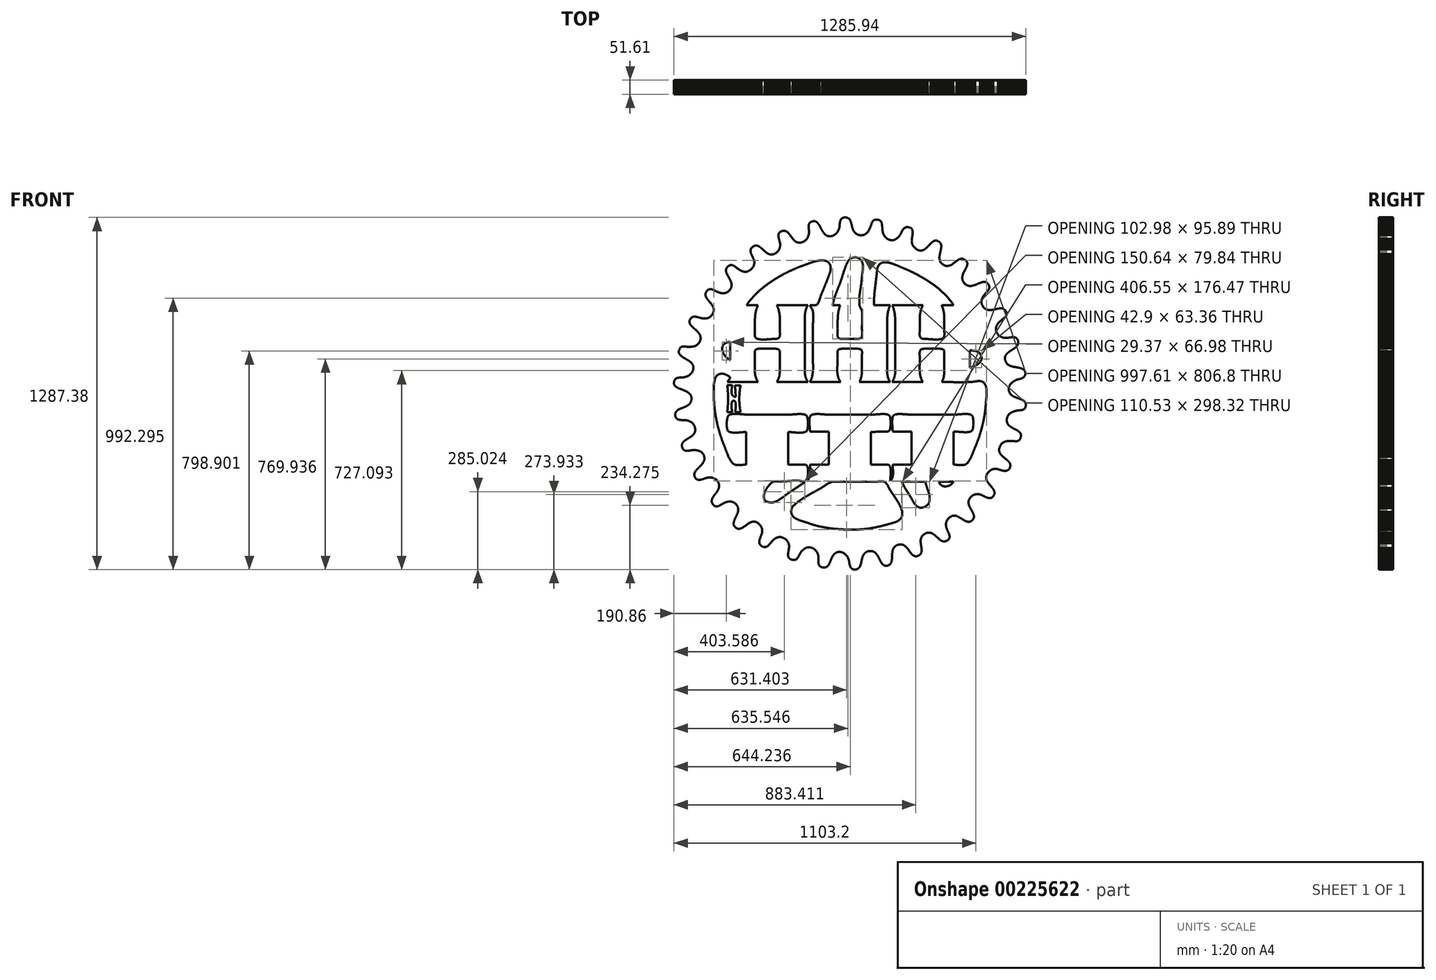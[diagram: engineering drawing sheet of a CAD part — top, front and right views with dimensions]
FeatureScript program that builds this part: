
annotation { "Feature Type Name" : "Feature", "Feature Type Description" : "" }
export const myFeature = defineFeature(function(context is Context, id is Id, definition is map)
    precondition{}
    {
        {
            var Q0;
            Q0=qCreatedBy(makeId("Front.planeOp"),FACE);
            var sketch = newSketch(context, id + "F0", { "sketchPlane" : qUnion([Q0])});
            skLineSegment(sketch, "E0", {"start": v(538.6, 219.48) * mm, "end": v(537.62, 221.14) * mm});
            skLineSegment(sketch, "E1", {"start": v(537.62, 221.14) * mm, "end": v(536.76, 222.78) * mm});
            skLineSegment(sketch, "E2", {"start": v(536.76, 222.78) * mm, "end": v(536, 224.4) * mm});
            skLineSegment(sketch, "E3", {"start": v(536, 224.4) * mm, "end": v(535.36, 226.02) * mm});
            skLineSegment(sketch, "E4", {"start": v(535.36, 226.02) * mm, "end": v(534.83, 227.62) * mm});
            skLineSegment(sketch, "E5", {"start": v(534.83, 227.62) * mm, "end": v(534.4, 229.21) * mm});
            skLineSegment(sketch, "E6", {"start": v(534.4, 229.21) * mm, "end": v(534.08, 230.79) * mm});
            skLineSegment(sketch, "E7", {"start": v(534.08, 230.79) * mm, "end": v(533.85, 232.35) * mm});
            skLineSegment(sketch, "E8", {"start": v(533.85, 232.35) * mm, "end": v(533.72, 233.9) * mm});
            skLineSegment(sketch, "E9", {"start": v(533.72, 233.9) * mm, "end": v(533.69, 235.43) * mm});
            skLineSegment(sketch, "E10", {"start": v(533.69, 235.43) * mm, "end": v(533.74, 236.95) * mm});
            skLineSegment(sketch, "E11", {"start": v(533.74, 236.95) * mm, "end": v(533.88, 238.46) * mm});
            skLineSegment(sketch, "E12", {"start": v(533.88, 238.46) * mm, "end": v(534.1, 239.95) * mm});
            skLineSegment(sketch, "E13", {"start": v(534.1, 239.95) * mm, "end": v(534.4, 241.42) * mm});
            skLineSegment(sketch, "E14", {"start": v(534.4, 241.42) * mm, "end": v(534.78, 242.88) * mm});
            skLineSegment(sketch, "E15", {"start": v(534.78, 242.88) * mm, "end": v(535.23, 244.32) * mm});
            skLineSegment(sketch, "E16", {"start": v(535.23, 244.32) * mm, "end": v(535.76, 245.75) * mm});
            skLineSegment(sketch, "E17", {"start": v(535.76, 245.75) * mm, "end": v(536.35, 247.16) * mm});
            skLineSegment(sketch, "E18", {"start": v(536.35, 247.16) * mm, "end": v(537, 248.55) * mm});
            skLineSegment(sketch, "E19", {"start": v(537, 248.55) * mm, "end": v(537.73, 249.93) * mm});
            skLineSegment(sketch, "E20", {"start": v(537.73, 249.93) * mm, "end": v(538.5, 251.29) * mm});
            skLineSegment(sketch, "E21", {"start": v(538.5, 251.29) * mm, "end": v(539.34, 252.63) * mm});
            skLineSegment(sketch, "E22", {"start": v(539.34, 252.63) * mm, "end": v(540.23, 253.95) * mm});
            skLineSegment(sketch, "E23", {"start": v(540.23, 253.95) * mm, "end": v(541.16, 255.25) * mm});
            skLineSegment(sketch, "E24", {"start": v(541.16, 255.25) * mm, "end": v(542.15, 256.53) * mm});
            skLineSegment(sketch, "E25", {"start": v(542.15, 256.53) * mm, "end": v(543.17, 257.8) * mm});
            skLineSegment(sketch, "E26", {"start": v(543.17, 257.8) * mm, "end": v(544.24, 259.05) * mm});
            skLineSegment(sketch, "E27", {"start": v(544.24, 259.05) * mm, "end": v(545.34, 260.27) * mm});
            skLineSegment(sketch, "E28", {"start": v(545.34, 260.27) * mm, "end": v(546.48, 261.48) * mm});
            skLineSegment(sketch, "E29", {"start": v(546.48, 261.48) * mm, "end": v(547.65, 262.67) * mm});
            skLineSegment(sketch, "E30", {"start": v(547.65, 262.67) * mm, "end": v(548.85, 263.83) * mm});
            skLineSegment(sketch, "E31", {"start": v(548.85, 263.83) * mm, "end": v(550.07, 264.98) * mm});
            skLineSegment(sketch, "E32", {"start": v(550.07, 264.98) * mm, "end": v(551.31, 266.1) * mm});
            skLineSegment(sketch, "E33", {"start": v(551.31, 266.1) * mm, "end": v(552.58, 267.2) * mm});
            skLineSegment(sketch, "E34", {"start": v(552.58, 267.2) * mm, "end": v(553.85, 268.28) * mm});
            skLineSegment(sketch, "E35", {"start": v(553.85, 268.28) * mm, "end": v(555.14, 269.34) * mm});
            skLineSegment(sketch, "E36", {"start": v(555.14, 269.34) * mm, "end": v(556.45, 270.38) * mm});
            skLineSegment(sketch, "E37", {"start": v(556.45, 270.38) * mm, "end": v(557.7, 271.34) * mm});
            skLineSegment(sketch, "E38", {"start": v(557.7, 271.34) * mm, "end": v(559, 272.32) * mm});
            skLineSegment(sketch, "E39", {"start": v(559, 272.32) * mm, "end": v(560.31, 273.3) * mm});
            skLineSegment(sketch, "E40", {"start": v(560.31, 273.3) * mm, "end": v(561.65, 274.3) * mm});
            skLineSegment(sketch, "E41", {"start": v(561.65, 274.3) * mm, "end": v(562.98, 275.33) * mm});
            skLineSegment(sketch, "E42", {"start": v(562.98, 275.33) * mm, "end": v(564.3, 276.38) * mm});
            skLineSegment(sketch, "E43", {"start": v(564.3, 276.38) * mm, "end": v(565.58, 277.45) * mm});
            skLineSegment(sketch, "E44", {"start": v(565.58, 277.45) * mm, "end": v(566.81, 278.56) * mm});
            skLineSegment(sketch, "E45", {"start": v(566.81, 278.56) * mm, "end": v(567.99, 279.7) * mm});
            skLineSegment(sketch, "E46", {"start": v(567.99, 279.7) * mm, "end": v(569.08, 280.88) * mm});
            skLineSegment(sketch, "E47", {"start": v(569.08, 280.88) * mm, "end": v(570.08, 282.1) * mm});
            skLineSegment(sketch, "E48", {"start": v(570.08, 282.1) * mm, "end": v(570.97, 283.36) * mm});
            skLineSegment(sketch, "E49", {"start": v(570.97, 283.36) * mm, "end": v(571.74, 284.67) * mm});
            skLineSegment(sketch, "E50", {"start": v(571.74, 284.67) * mm, "end": v(572.37, 286.04) * mm});
            skLineSegment(sketch, "E51", {"start": v(572.37, 286.04) * mm, "end": v(572.84, 287.46) * mm});
            skLineSegment(sketch, "E52", {"start": v(572.84, 287.46) * mm, "end": v(573.15, 288.93) * mm});
            skLineSegment(sketch, "E53", {"start": v(573.15, 288.93) * mm, "end": v(573.27, 290.48) * mm});
            skLineSegment(sketch, "E54", {"start": v(573.27, 290.48) * mm, "end": v(573.2, 292.08) * mm});
            skLineSegment(sketch, "E55", {"start": v(573.2, 292.08) * mm, "end": v(572.9, 293.76) * mm});
            skLineSegment(sketch, "E56", {"start": v(572.9, 293.76) * mm, "end": v(572.38, 295.51) * mm});
            skLineSegment(sketch, "E57", {"start": v(572.38, 295.51) * mm, "end": v(571.85, 296.89) * mm});
            skLineSegment(sketch, "E58", {"start": v(571.85, 296.89) * mm, "end": v(571.3, 298.18) * mm});
            skLineSegment(sketch, "E59", {"start": v(571.3, 298.18) * mm, "end": v(570.74, 299.4) * mm});
            skLineSegment(sketch, "E60", {"start": v(570.74, 299.4) * mm, "end": v(570.14, 300.56) * mm});
            skLineSegment(sketch, "E61", {"start": v(570.14, 300.56) * mm, "end": v(569.52, 301.64) * mm});
            skLineSegment(sketch, "E62", {"start": v(569.52, 301.64) * mm, "end": v(568.88, 302.65) * mm});
            skLineSegment(sketch, "E63", {"start": v(568.88, 302.65) * mm, "end": v(568.2, 303.6) * mm});
            skLineSegment(sketch, "E64", {"start": v(568.2, 303.6) * mm, "end": v(567.52, 304.48) * mm});
            skLineSegment(sketch, "E65", {"start": v(567.52, 304.48) * mm, "end": v(566.8, 305.3) * mm});
            skLineSegment(sketch, "E66", {"start": v(566.8, 305.3) * mm, "end": v(566.07, 306.06) * mm});
            skLineSegment(sketch, "E67", {"start": v(566.07, 306.06) * mm, "end": v(565.32, 306.76) * mm});
            skLineSegment(sketch, "E68", {"start": v(565.32, 306.76) * mm, "end": v(564.54, 307.4) * mm});
            skLineSegment(sketch, "E69", {"start": v(564.54, 307.4) * mm, "end": v(563.75, 307.98) * mm});
            skLineSegment(sketch, "E70", {"start": v(563.75, 307.98) * mm, "end": v(562.93, 308.51) * mm});
            skLineSegment(sketch, "E71", {"start": v(562.93, 308.51) * mm, "end": v(562.1, 308.99) * mm});
            skLineSegment(sketch, "E72", {"start": v(562.1, 308.99) * mm, "end": v(561.25, 309.42) * mm});
            skLineSegment(sketch, "E73", {"start": v(561.25, 309.42) * mm, "end": v(560.38, 309.8) * mm});
            skLineSegment(sketch, "E74", {"start": v(560.38, 309.8) * mm, "end": v(559.49, 310.12) * mm});
            skLineSegment(sketch, "E75", {"start": v(559.49, 310.12) * mm, "end": v(558.58, 310.4) * mm});
            skLineSegment(sketch, "E76", {"start": v(558.58, 310.4) * mm, "end": v(557.66, 310.65) * mm});
            skLineSegment(sketch, "E77", {"start": v(557.66, 310.65) * mm, "end": v(556.73, 310.85) * mm});
            skLineSegment(sketch, "E78", {"start": v(556.73, 310.85) * mm, "end": v(555.77, 311.01) * mm});
            skLineSegment(sketch, "E79", {"start": v(555.77, 311.01) * mm, "end": v(554.8, 311.13) * mm});
            skLineSegment(sketch, "E80", {"start": v(554.8, 311.13) * mm, "end": v(553.82, 311.22) * mm});
            skLineSegment(sketch, "E81", {"start": v(553.82, 311.22) * mm, "end": v(552.83, 311.27) * mm});
            skLineSegment(sketch, "E82", {"start": v(552.83, 311.27) * mm, "end": v(551.82, 311.28) * mm});
            skLineSegment(sketch, "E83", {"start": v(551.82, 311.28) * mm, "end": v(550.8, 311.27) * mm});
            skLineSegment(sketch, "E84", {"start": v(550.8, 311.27) * mm, "end": v(549.76, 311.22) * mm});
            skLineSegment(sketch, "E85", {"start": v(549.76, 311.22) * mm, "end": v(548.71, 311.15) * mm});
            skLineSegment(sketch, "E86", {"start": v(548.71, 311.15) * mm, "end": v(547.66, 311.05) * mm});
            skLineSegment(sketch, "E87", {"start": v(547.66, 311.05) * mm, "end": v(546.59, 310.93) * mm});
            skLineSegment(sketch, "E88", {"start": v(546.59, 310.93) * mm, "end": v(545.5, 310.79) * mm});
            skLineSegment(sketch, "E89", {"start": v(545.5, 310.79) * mm, "end": v(544.42, 310.62) * mm});
            skLineSegment(sketch, "E90", {"start": v(544.42, 310.62) * mm, "end": v(543.32, 310.44) * mm});
            skLineSegment(sketch, "E91", {"start": v(543.32, 310.44) * mm, "end": v(542.21, 310.23) * mm});
            skLineSegment(sketch, "E92", {"start": v(542.21, 310.23) * mm, "end": v(541.1, 310.02) * mm});
            skLineSegment(sketch, "E93", {"start": v(541.1, 310.02) * mm, "end": v(539.97, 309.79) * mm});
            skLineSegment(sketch, "E94", {"start": v(539.97, 309.79) * mm, "end": v(538.84, 309.54) * mm});
            skLineSegment(sketch, "E95", {"start": v(538.84, 309.54) * mm, "end": v(537.7, 309.3) * mm});
            skLineSegment(sketch, "E96", {"start": v(537.7, 309.3) * mm, "end": v(536.56, 309.03) * mm});
            skLineSegment(sketch, "E97", {"start": v(536.56, 309.03) * mm, "end": v(535.42, 308.76) * mm});
            skLineSegment(sketch, "E98", {"start": v(535.42, 308.76) * mm, "end": v(534.26, 308.5) * mm});
            skLineSegment(sketch, "E99", {"start": v(534.26, 308.5) * mm, "end": v(533.1, 308.21) * mm});
            skLineSegment(sketch, "E100", {"start": v(533.1, 308.21) * mm, "end": v(531.94, 307.94) * mm});
            skLineSegment(sketch, "E101", {"start": v(531.94, 307.94) * mm, "end": v(530.77, 307.66) * mm});
            skLineSegment(sketch, "E102", {"start": v(530.77, 307.66) * mm, "end": v(529.6, 307.39) * mm});
            skLineSegment(sketch, "E103", {"start": v(529.6, 307.39) * mm, "end": v(528.43, 307.12) * mm});
            skLineSegment(sketch, "E104", {"start": v(528.43, 307.12) * mm, "end": v(527.26, 306.85) * mm});
            skLineSegment(sketch, "E105", {"start": v(527.26, 306.85) * mm, "end": v(526.08, 306.6) * mm});
            skLineSegment(sketch, "E106", {"start": v(526.08, 306.6) * mm, "end": v(524.9, 306.35) * mm});
            skLineSegment(sketch, "E107", {"start": v(524.9, 306.35) * mm, "end": v(523.73, 306.11) * mm});
            skLineSegment(sketch, "E108", {"start": v(523.73, 306.11) * mm, "end": v(522.55, 305.89) * mm});
            skLineSegment(sketch, "E109", {"start": v(522.55, 305.89) * mm, "end": v(521.37, 305.68) * mm});
            skLineSegment(sketch, "E110", {"start": v(521.37, 305.68) * mm, "end": v(520.2, 305.49) * mm});
            skLineSegment(sketch, "E111", {"start": v(520.2, 305.49) * mm, "end": v(519.02, 305.31) * mm});
            skLineSegment(sketch, "E112", {"start": v(519.02, 305.31) * mm, "end": v(517.85, 305.16) * mm});
            skLineSegment(sketch, "E113", {"start": v(517.85, 305.16) * mm, "end": v(516.68, 305.02) * mm});
            skLineSegment(sketch, "E114", {"start": v(516.68, 305.02) * mm, "end": v(515.51, 304.92) * mm});
            skLineSegment(sketch, "E115", {"start": v(515.51, 304.92) * mm, "end": v(514.35, 304.83) * mm});
            skLineSegment(sketch, "E116", {"start": v(514.35, 304.83) * mm, "end": v(513.19, 304.77) * mm});
            skLineSegment(sketch, "E117", {"start": v(513.19, 304.77) * mm, "end": v(512.03, 304.74) * mm});
            skLineSegment(sketch, "E118", {"start": v(512.03, 304.74) * mm, "end": v(510.88, 304.75) * mm});
            skLineSegment(sketch, "E119", {"start": v(510.88, 304.75) * mm, "end": v(509.74, 304.78) * mm});
            skLineSegment(sketch, "E120", {"start": v(509.74, 304.78) * mm, "end": v(508.6, 304.85) * mm});
            skLineSegment(sketch, "E121", {"start": v(508.6, 304.85) * mm, "end": v(507.47, 304.95) * mm});
            skLineSegment(sketch, "E122", {"start": v(507.47, 304.95) * mm, "end": v(506.34, 305.1) * mm});
            skLineSegment(sketch, "E123", {"start": v(506.34, 305.1) * mm, "end": v(505.23, 305.27) * mm});
            skLineSegment(sketch, "E124", {"start": v(505.23, 305.27) * mm, "end": v(504.12, 305.5) * mm});
            skLineSegment(sketch, "E125", {"start": v(504.12, 305.5) * mm, "end": v(503.02, 305.76) * mm});
            skLineSegment(sketch, "E126", {"start": v(503.02, 305.76) * mm, "end": v(501.93, 306.07) * mm});
            skLineSegment(sketch, "E127", {"start": v(501.93, 306.07) * mm, "end": v(500.85, 306.43) * mm});
            skLineSegment(sketch, "E128", {"start": v(500.85, 306.43) * mm, "end": v(499.78, 306.83) * mm});
            skLineSegment(sketch, "E129", {"start": v(499.78, 306.83) * mm, "end": v(498.72, 307.28) * mm});
            skLineSegment(sketch, "E130", {"start": v(498.72, 307.28) * mm, "end": v(497.67, 307.79) * mm});
            skLineSegment(sketch, "E131", {"start": v(497.67, 307.79) * mm, "end": v(496.63, 308.35) * mm});
            skLineSegment(sketch, "E132", {"start": v(496.63, 308.35) * mm, "end": v(495.6, 308.96) * mm});
            skLineSegment(sketch, "E133", {"start": v(495.6, 308.96) * mm, "end": v(494.6, 309.63) * mm});
            skLineSegment(sketch, "E134", {"start": v(494.6, 309.63) * mm, "end": v(493.6, 310.36) * mm});
            skLineSegment(sketch, "E135", {"start": v(493.6, 310.36) * mm, "end": v(492.6, 311.15) * mm});
            skLineSegment(sketch, "E136", {"start": v(492.6, 311.15) * mm, "end": v(491.64, 312) * mm});
            skLineSegment(sketch, "E137", {"start": v(491.64, 312) * mm, "end": v(490.68, 312.92) * mm});
            skLineSegment(sketch, "E138", {"start": v(490.68, 312.92) * mm, "end": v(489.74, 313.9) * mm});
            skLineSegment(sketch, "E139", {"start": v(489.74, 313.9) * mm, "end": v(488.82, 314.95) * mm});
            skLineSegment(sketch, "E140", {"start": v(488.82, 314.95) * mm, "end": v(487.9, 316.07) * mm});
            skLineSegment(sketch, "E141", {"start": v(487.9, 316.07) * mm, "end": v(487.02, 317.26) * mm});
            skLineSegment(sketch, "E142", {"start": v(487.02, 317.26) * mm, "end": v(485.9, 318.9) * mm});
            skLineSegment(sketch, "E143", {"start": v(485.9, 318.9) * mm, "end": v(484.9, 320.52) * mm});
            skLineSegment(sketch, "E144", {"start": v(484.9, 320.52) * mm, "end": v(484.03, 322.13) * mm});
            skLineSegment(sketch, "E145", {"start": v(484.03, 322.13) * mm, "end": v(483.27, 323.73) * mm});
            skLineSegment(sketch, "E146", {"start": v(483.27, 323.73) * mm, "end": v(482.63, 325.33) * mm});
            skLineSegment(sketch, "E147", {"start": v(482.63, 325.33) * mm, "end": v(482.09, 326.91) * mm});
            skLineSegment(sketch, "E148", {"start": v(482.09, 326.91) * mm, "end": v(481.65, 328.5) * mm});
            skLineSegment(sketch, "E149", {"start": v(481.65, 328.5) * mm, "end": v(481.31, 330.06) * mm});
            skLineSegment(sketch, "E150", {"start": v(481.31, 330.06) * mm, "end": v(481.08, 331.62) * mm});
            skLineSegment(sketch, "E151", {"start": v(481.08, 331.62) * mm, "end": v(480.94, 333.17) * mm});
            skLineSegment(sketch, "E152", {"start": v(480.94, 333.17) * mm, "end": v(480.88, 334.7) * mm});
            skLineSegment(sketch, "E153", {"start": v(480.88, 334.7) * mm, "end": v(480.92, 336.24) * mm});
            skLineSegment(sketch, "E154", {"start": v(480.92, 336.24) * mm, "end": v(481.04, 337.76) * mm});
            skLineSegment(sketch, "E155", {"start": v(481.04, 337.76) * mm, "end": v(481.25, 339.27) * mm});
            skLineSegment(sketch, "E156", {"start": v(481.25, 339.27) * mm, "end": v(481.53, 340.78) * mm});
            skLineSegment(sketch, "E157", {"start": v(481.53, 340.78) * mm, "end": v(481.88, 342.27) * mm});
            skLineSegment(sketch, "E158", {"start": v(481.88, 342.27) * mm, "end": v(482.3, 343.75) * mm});
            skLineSegment(sketch, "E159", {"start": v(482.3, 343.75) * mm, "end": v(482.8, 345.23) * mm});
            skLineSegment(sketch, "E160", {"start": v(482.8, 345.23) * mm, "end": v(483.36, 346.69) * mm});
            skLineSegment(sketch, "E161", {"start": v(483.36, 346.69) * mm, "end": v(483.98, 348.14) * mm});
            skLineSegment(sketch, "E162", {"start": v(483.98, 348.14) * mm, "end": v(484.65, 349.59) * mm});
            skLineSegment(sketch, "E163", {"start": v(484.65, 349.59) * mm, "end": v(485.39, 351.02) * mm});
            skLineSegment(sketch, "E164", {"start": v(485.39, 351.02) * mm, "end": v(486.17, 352.44) * mm});
            skLineSegment(sketch, "E165", {"start": v(486.17, 352.44) * mm, "end": v(487, 353.86) * mm});
            skLineSegment(sketch, "E166", {"start": v(487, 353.86) * mm, "end": v(487.87, 355.26) * mm});
            skLineSegment(sketch, "E167", {"start": v(487.87, 355.26) * mm, "end": v(488.78, 356.65) * mm});
            skLineSegment(sketch, "E168", {"start": v(488.78, 356.65) * mm, "end": v(489.74, 358.03) * mm});
            skLineSegment(sketch, "E169", {"start": v(489.74, 358.03) * mm, "end": v(490.72, 359.4) * mm});
            skLineSegment(sketch, "E170", {"start": v(490.72, 359.4) * mm, "end": v(491.74, 360.77) * mm});
            skLineSegment(sketch, "E171", {"start": v(491.74, 360.77) * mm, "end": v(492.78, 362.12) * mm});
            skLineSegment(sketch, "E172", {"start": v(492.78, 362.12) * mm, "end": v(493.85, 363.46) * mm});
            skLineSegment(sketch, "E173", {"start": v(493.85, 363.46) * mm, "end": v(494.94, 364.78) * mm});
            skLineSegment(sketch, "E174", {"start": v(494.94, 364.78) * mm, "end": v(496.05, 366.1) * mm});
            skLineSegment(sketch, "E175", {"start": v(496.05, 366.1) * mm, "end": v(497.17, 367.4) * mm});
            skLineSegment(sketch, "E176", {"start": v(497.17, 367.4) * mm, "end": v(498.18, 368.56) * mm});
            skLineSegment(sketch, "E177", {"start": v(498.18, 368.56) * mm, "end": v(499.26, 369.76) * mm});
            skLineSegment(sketch, "E178", {"start": v(499.26, 369.76) * mm, "end": v(500.37, 371) * mm});
            skLineSegment(sketch, "E179", {"start": v(500.37, 371) * mm, "end": v(501.5, 372.27) * mm});
            skLineSegment(sketch, "E180", {"start": v(501.5, 372.27) * mm, "end": v(502.65, 373.58) * mm});
            skLineSegment(sketch, "E181", {"start": v(502.65, 373.58) * mm, "end": v(503.77, 374.92) * mm});
            skLineSegment(sketch, "E182", {"start": v(503.77, 374.92) * mm, "end": v(504.86, 376.3) * mm});
            skLineSegment(sketch, "E183", {"start": v(504.86, 376.3) * mm, "end": v(505.89, 377.72) * mm});
            skLineSegment(sketch, "E184", {"start": v(505.89, 377.72) * mm, "end": v(506.84, 379.16) * mm});
            skLineSegment(sketch, "E185", {"start": v(506.84, 379.16) * mm, "end": v(507.7, 380.63) * mm});
            skLineSegment(sketch, "E186", {"start": v(507.7, 380.63) * mm, "end": v(508.46, 382.13) * mm});
            skLineSegment(sketch, "E187", {"start": v(508.46, 382.13) * mm, "end": v(509.08, 383.66) * mm});
            skLineSegment(sketch, "E188", {"start": v(509.08, 383.66) * mm, "end": v(509.56, 385.2) * mm});
            skLineSegment(sketch, "E189", {"start": v(509.56, 385.2) * mm, "end": v(509.86, 386.78) * mm});
            skLineSegment(sketch, "E190", {"start": v(509.86, 386.78) * mm, "end": v(509.97, 388.38) * mm});
            skLineSegment(sketch, "E191", {"start": v(509.97, 388.38) * mm, "end": v(509.88, 389.99) * mm});
            skLineSegment(sketch, "E192", {"start": v(509.88, 389.99) * mm, "end": v(509.56, 391.62) * mm});
            skLineSegment(sketch, "E193", {"start": v(509.56, 391.62) * mm, "end": v(509, 393.27) * mm});
            skLineSegment(sketch, "E194", {"start": v(509, 393.27) * mm, "end": v(508.37, 394.72) * mm});
            skLineSegment(sketch, "E195", {"start": v(508.37, 394.72) * mm, "end": v(507.7, 396.08) * mm});
            skLineSegment(sketch, "E196", {"start": v(507.7, 396.08) * mm, "end": v(507.03, 397.35) * mm});
            skLineSegment(sketch, "E197", {"start": v(507.03, 397.35) * mm, "end": v(506.33, 398.54) * mm});
            skLineSegment(sketch, "E198", {"start": v(506.33, 398.54) * mm, "end": v(505.61, 399.64) * mm});
            skLineSegment(sketch, "E199", {"start": v(505.61, 399.64) * mm, "end": v(504.88, 400.67) * mm});
            skLineSegment(sketch, "E200", {"start": v(504.88, 400.67) * mm, "end": v(504.12, 401.61) * mm});
            skLineSegment(sketch, "E201", {"start": v(504.12, 401.61) * mm, "end": v(503.34, 402.48) * mm});
            skLineSegment(sketch, "E202", {"start": v(503.34, 402.48) * mm, "end": v(502.54, 403.28) * mm});
            skLineSegment(sketch, "E203", {"start": v(502.54, 403.28) * mm, "end": v(501.73, 404) * mm});
            skLineSegment(sketch, "E204", {"start": v(501.73, 404) * mm, "end": v(500.9, 404.65) * mm});
            skLineSegment(sketch, "E205", {"start": v(500.9, 404.65) * mm, "end": v(500.05, 405.23) * mm});
            skLineSegment(sketch, "E206", {"start": v(500.05, 405.23) * mm, "end": v(499.18, 405.75) * mm});
            skLineSegment(sketch, "E207", {"start": v(499.18, 405.75) * mm, "end": v(498.3, 406.2) * mm});
            skLineSegment(sketch, "E208", {"start": v(498.3, 406.2) * mm, "end": v(497.4, 406.6) * mm});
            skLineSegment(sketch, "E209", {"start": v(497.4, 406.6) * mm, "end": v(496.49, 406.93) * mm});
            skLineSegment(sketch, "E210", {"start": v(496.49, 406.93) * mm, "end": v(495.56, 407.2) * mm});
            skLineSegment(sketch, "E211", {"start": v(495.56, 407.2) * mm, "end": v(494.61, 407.42) * mm});
            skLineSegment(sketch, "E212", {"start": v(494.61, 407.42) * mm, "end": v(493.65, 407.58) * mm});
            skLineSegment(sketch, "E213", {"start": v(493.65, 407.58) * mm, "end": v(492.68, 407.7) * mm});
            skLineSegment(sketch, "E214", {"start": v(492.68, 407.7) * mm, "end": v(491.7, 407.76) * mm});
            skLineSegment(sketch, "E215", {"start": v(491.7, 407.76) * mm, "end": v(490.69, 407.77) * mm});
            skLineSegment(sketch, "E216", {"start": v(490.69, 407.77) * mm, "end": v(489.68, 407.74) * mm});
            skLineSegment(sketch, "E217", {"start": v(489.68, 407.74) * mm, "end": v(488.65, 407.67) * mm});
            skLineSegment(sketch, "E218", {"start": v(488.65, 407.67) * mm, "end": v(487.61, 407.55) * mm});
            skLineSegment(sketch, "E219", {"start": v(487.61, 407.55) * mm, "end": v(486.56, 407.4) * mm});
            skLineSegment(sketch, "E220", {"start": v(486.56, 407.4) * mm, "end": v(485.5, 407.2) * mm});
            skLineSegment(sketch, "E221", {"start": v(485.5, 407.2) * mm, "end": v(484.43, 406.98) * mm});
            skLineSegment(sketch, "E222", {"start": v(484.43, 406.98) * mm, "end": v(483.35, 406.72) * mm});
            skLineSegment(sketch, "E223", {"start": v(483.35, 406.72) * mm, "end": v(482.25, 406.43) * mm});
            skLineSegment(sketch, "E224", {"start": v(482.25, 406.43) * mm, "end": v(481.15, 406.1) * mm});
            skLineSegment(sketch, "E225", {"start": v(481.15, 406.1) * mm, "end": v(480.04, 405.76) * mm});
            skLineSegment(sketch, "E226", {"start": v(480.04, 405.76) * mm, "end": v(478.92, 405.4) * mm});
            skLineSegment(sketch, "E227", {"start": v(478.92, 405.4) * mm, "end": v(477.8, 405) * mm});
            skLineSegment(sketch, "E228", {"start": v(477.8, 405) * mm, "end": v(476.66, 404.59) * mm});
            skLineSegment(sketch, "E229", {"start": v(476.66, 404.59) * mm, "end": v(475.51, 404.15) * mm});
            skLineSegment(sketch, "E230", {"start": v(475.51, 404.15) * mm, "end": v(474.36, 403.7) * mm});
            skLineSegment(sketch, "E231", {"start": v(474.36, 403.7) * mm, "end": v(473.2, 403.24) * mm});
            skLineSegment(sketch, "E232", {"start": v(473.2, 403.24) * mm, "end": v(472.04, 402.77) * mm});
            skLineSegment(sketch, "E233", {"start": v(472.04, 402.77) * mm, "end": v(470.87, 402.28) * mm});
            skLineSegment(sketch, "E234", {"start": v(470.87, 402.28) * mm, "end": v(469.7, 401.79) * mm});
            skLineSegment(sketch, "E235", {"start": v(469.7, 401.79) * mm, "end": v(468.52, 401.29) * mm});
            skLineSegment(sketch, "E236", {"start": v(468.52, 401.29) * mm, "end": v(467.33, 400.79) * mm});
            skLineSegment(sketch, "E237", {"start": v(467.33, 400.79) * mm, "end": v(466.14, 400.28) * mm});
            skLineSegment(sketch, "E238", {"start": v(466.14, 400.28) * mm, "end": v(464.95, 399.78) * mm});
            skLineSegment(sketch, "E239", {"start": v(464.95, 399.78) * mm, "end": v(463.75, 399.27) * mm});
            skLineSegment(sketch, "E240", {"start": v(463.75, 399.27) * mm, "end": v(462.55, 398.78) * mm});
            skLineSegment(sketch, "E241", {"start": v(462.55, 398.78) * mm, "end": v(461.35, 398.28) * mm});
            skLineSegment(sketch, "E242", {"start": v(461.35, 398.28) * mm, "end": v(460.15, 397.8) * mm});
            skLineSegment(sketch, "E243", {"start": v(460.15, 397.8) * mm, "end": v(458.94, 397.33) * mm});
            skLineSegment(sketch, "E244", {"start": v(458.94, 397.33) * mm, "end": v(457.73, 396.87) * mm});
            skLineSegment(sketch, "E245", {"start": v(457.73, 396.87) * mm, "end": v(456.52, 396.42) * mm});
            skLineSegment(sketch, "E246", {"start": v(456.52, 396.42) * mm, "end": v(455.32, 396) * mm});
            skLineSegment(sketch, "E247", {"start": v(455.32, 396) * mm, "end": v(454.1, 395.59) * mm});
            skLineSegment(sketch, "E248", {"start": v(454.1, 395.59) * mm, "end": v(452.9, 395.2) * mm});
            skLineSegment(sketch, "E249", {"start": v(452.9, 395.2) * mm, "end": v(451.69, 394.83) * mm});
            skLineSegment(sketch, "E250", {"start": v(451.69, 394.83) * mm, "end": v(450.48, 394.5) * mm});
            skLineSegment(sketch, "E251", {"start": v(450.48, 394.5) * mm, "end": v(449.28, 394.18) * mm});
            skLineSegment(sketch, "E252", {"start": v(449.28, 394.18) * mm, "end": v(448.07, 393.9) * mm});
            skLineSegment(sketch, "E253", {"start": v(448.07, 393.9) * mm, "end": v(446.87, 393.64) * mm});
            skLineSegment(sketch, "E254", {"start": v(446.87, 393.64) * mm, "end": v(445.67, 393.43) * mm});
            skLineSegment(sketch, "E255", {"start": v(445.67, 393.43) * mm, "end": v(444.48, 393.24) * mm});
            skLineSegment(sketch, "E256", {"start": v(444.48, 393.24) * mm, "end": v(443.28, 393.1) * mm});
            skLineSegment(sketch, "E257", {"start": v(443.28, 393.1) * mm, "end": v(442.1, 393) * mm});
            skLineSegment(sketch, "E258", {"start": v(442.1, 393) * mm, "end": v(440.91, 392.93) * mm});
            skLineSegment(sketch, "E259", {"start": v(440.91, 392.93) * mm, "end": v(439.73, 392.9) * mm});
            skLineSegment(sketch, "E260", {"start": v(439.73, 392.9) * mm, "end": v(438.56, 392.93) * mm});
            skLineSegment(sketch, "E261", {"start": v(438.56, 392.93) * mm, "end": v(437.4, 393) * mm});
            skLineSegment(sketch, "E262", {"start": v(437.4, 393) * mm, "end": v(436.23, 393.13) * mm});
            skLineSegment(sketch, "E263", {"start": v(436.23, 393.13) * mm, "end": v(435.07, 393.3) * mm});
            skLineSegment(sketch, "E264", {"start": v(435.07, 393.3) * mm, "end": v(433.92, 393.53) * mm});
            skLineSegment(sketch, "E265", {"start": v(433.92, 393.53) * mm, "end": v(432.78, 393.82) * mm});
            skLineSegment(sketch, "E266", {"start": v(432.78, 393.82) * mm, "end": v(431.65, 394.16) * mm});
            skLineSegment(sketch, "E267", {"start": v(431.65, 394.16) * mm, "end": v(430.52, 394.57) * mm});
            skLineSegment(sketch, "E268", {"start": v(430.52, 394.57) * mm, "end": v(429.4, 395.04) * mm});
            skLineSegment(sketch, "E269", {"start": v(429.4, 395.04) * mm, "end": v(428.3, 395.57) * mm});
            skLineSegment(sketch, "E270", {"start": v(428.3, 395.57) * mm, "end": v(427.2, 396.17) * mm});
            skLineSegment(sketch, "E271", {"start": v(427.2, 396.17) * mm, "end": v(426.1, 396.84) * mm});
            skLineSegment(sketch, "E272", {"start": v(426.1, 396.84) * mm, "end": v(424.45, 397.96) * mm});
            skLineSegment(sketch, "E273", {"start": v(424.45, 397.96) * mm, "end": v(422.9, 399.12) * mm});
            skLineSegment(sketch, "E274", {"start": v(422.9, 399.12) * mm, "end": v(421.45, 400.3) * mm});
            skLineSegment(sketch, "E275", {"start": v(421.45, 400.3) * mm, "end": v(420.1, 401.5) * mm});
            skLineSegment(sketch, "E276", {"start": v(420.1, 401.5) * mm, "end": v(418.86, 402.75) * mm});
            skLineSegment(sketch, "E277", {"start": v(418.86, 402.75) * mm, "end": v(417.72, 404) * mm});
            skLineSegment(sketch, "E278", {"start": v(417.72, 404) * mm, "end": v(416.67, 405.3) * mm});
            skLineSegment(sketch, "E279", {"start": v(416.67, 405.3) * mm, "end": v(415.72, 406.6) * mm});
            skLineSegment(sketch, "E280", {"start": v(415.72, 406.6) * mm, "end": v(414.85, 407.93) * mm});
            skLineSegment(sketch, "E281", {"start": v(414.85, 407.93) * mm, "end": v(414.08, 409.29) * mm});
            skLineSegment(sketch, "E282", {"start": v(414.08, 409.29) * mm, "end": v(413.4, 410.66) * mm});
            skLineSegment(sketch, "E283", {"start": v(413.4, 410.66) * mm, "end": v(412.8, 412.05) * mm});
            skLineSegment(sketch, "E284", {"start": v(412.8, 412.05) * mm, "end": v(412.29, 413.46) * mm});
            skLineSegment(sketch, "E285", {"start": v(412.29, 413.46) * mm, "end": v(411.85, 414.88) * mm});
            skLineSegment(sketch, "E286", {"start": v(411.85, 414.88) * mm, "end": v(411.5, 416.32) * mm});
            skLineSegment(sketch, "E287", {"start": v(411.5, 416.32) * mm, "end": v(411.22, 417.77) * mm});
            skLineSegment(sketch, "E288", {"start": v(411.22, 417.77) * mm, "end": v(411.02, 419.24) * mm});
            skLineSegment(sketch, "E289", {"start": v(411.02, 419.24) * mm, "end": v(410.9, 420.72) * mm});
            skLineSegment(sketch, "E290", {"start": v(410.9, 420.72) * mm, "end": v(410.84, 422.21) * mm});
            skLineSegment(sketch, "E291", {"start": v(410.84, 422.21) * mm, "end": v(410.85, 423.71) * mm});
            skLineSegment(sketch, "E292", {"start": v(410.85, 423.71) * mm, "end": v(410.92, 425.22) * mm});
            skLineSegment(sketch, "E293", {"start": v(410.92, 425.22) * mm, "end": v(411.06, 426.74) * mm});
            skLineSegment(sketch, "E294", {"start": v(411.06, 426.74) * mm, "end": v(411.27, 428.26) * mm});
            skLineSegment(sketch, "E295", {"start": v(411.27, 428.26) * mm, "end": v(411.53, 429.8) * mm});
            skLineSegment(sketch, "E296", {"start": v(411.53, 429.8) * mm, "end": v(411.85, 431.33) * mm});
            skLineSegment(sketch, "E297", {"start": v(411.85, 431.33) * mm, "end": v(412.23, 432.87) * mm});
            skLineSegment(sketch, "E298", {"start": v(412.23, 432.87) * mm, "end": v(412.66, 434.4) * mm});
            skLineSegment(sketch, "E299", {"start": v(412.66, 434.4) * mm, "end": v(413.14, 435.95) * mm});
            skLineSegment(sketch, "E300", {"start": v(413.14, 435.95) * mm, "end": v(413.67, 437.5) * mm});
            skLineSegment(sketch, "E301", {"start": v(413.67, 437.5) * mm, "end": v(414.25, 439.03) * mm});
            skLineSegment(sketch, "E302", {"start": v(414.25, 439.03) * mm, "end": v(414.87, 440.57) * mm});
            skLineSegment(sketch, "E303", {"start": v(414.87, 440.57) * mm, "end": v(415.54, 442.1) * mm});
            skLineSegment(sketch, "E304", {"start": v(415.54, 442.1) * mm, "end": v(416.24, 443.64) * mm});
            skLineSegment(sketch, "E305", {"start": v(416.24, 443.64) * mm, "end": v(416.99, 445.17) * mm});
            skLineSegment(sketch, "E306", {"start": v(416.99, 445.17) * mm, "end": v(417.77, 446.69) * mm});
            skLineSegment(sketch, "E307", {"start": v(417.77, 446.69) * mm, "end": v(418.58, 448.2) * mm});
            skLineSegment(sketch, "E308", {"start": v(418.58, 448.2) * mm, "end": v(419.43, 449.7) * mm});
            skLineSegment(sketch, "E309", {"start": v(419.43, 449.7) * mm, "end": v(420.3, 451.2) * mm});
            skLineSegment(sketch, "E310", {"start": v(420.3, 451.2) * mm, "end": v(421.16, 452.63) * mm});
            skLineSegment(sketch, "E311", {"start": v(421.16, 452.63) * mm, "end": v(422, 454.06) * mm});
            skLineSegment(sketch, "E312", {"start": v(422, 454.06) * mm, "end": v(422.8, 455.49) * mm});
            skLineSegment(sketch, "E313", {"start": v(422.8, 455.49) * mm, "end": v(423.6, 456.92) * mm});
            skLineSegment(sketch, "E314", {"start": v(423.6, 456.92) * mm, "end": v(424.35, 458.34) * mm});
            skLineSegment(sketch, "E315", {"start": v(424.35, 458.34) * mm, "end": v(425.08, 459.77) * mm});
            skLineSegment(sketch, "E316", {"start": v(425.08, 459.77) * mm, "end": v(425.76, 461.18) * mm});
            skLineSegment(sketch, "E317", {"start": v(425.76, 461.18) * mm, "end": v(426.4, 462.6) * mm});
            skLineSegment(sketch, "E318", {"start": v(426.4, 462.6) * mm, "end": v(427, 464) * mm});
            skLineSegment(sketch, "E319", {"start": v(427, 464) * mm, "end": v(427.53, 465.4) * mm});
            skLineSegment(sketch, "E320", {"start": v(427.53, 465.4) * mm, "end": v(428, 466.77) * mm});
            skLineSegment(sketch, "E321", {"start": v(428, 466.77) * mm, "end": v(428.41, 468.15) * mm});
            skLineSegment(sketch, "E322", {"start": v(428.41, 468.15) * mm, "end": v(428.75, 469.5) * mm});
            skLineSegment(sketch, "E323", {"start": v(428.75, 469.5) * mm, "end": v(429.02, 470.85) * mm});
            skLineSegment(sketch, "E324", {"start": v(429.02, 470.85) * mm, "end": v(429.2, 472.18) * mm});
            skLineSegment(sketch, "E325", {"start": v(429.2, 472.18) * mm, "end": v(429.3, 473.49) * mm});
            skLineSegment(sketch, "E326", {"start": v(429.3, 473.49) * mm, "end": v(429.31, 474.78) * mm});
            skLineSegment(sketch, "E327", {"start": v(429.31, 474.78) * mm, "end": v(429.23, 476.06) * mm});
            skLineSegment(sketch, "E328", {"start": v(429.23, 476.06) * mm, "end": v(429.04, 477.31) * mm});
            skLineSegment(sketch, "E329", {"start": v(429.04, 477.31) * mm, "end": v(428.75, 478.54) * mm});
            skLineSegment(sketch, "E330", {"start": v(428.75, 478.54) * mm, "end": v(428.35, 479.75) * mm});
            skLineSegment(sketch, "E331", {"start": v(428.35, 479.75) * mm, "end": v(427.84, 480.93) * mm});
            skLineSegment(sketch, "E332", {"start": v(427.84, 480.93) * mm, "end": v(427.2, 482.1) * mm});
            skLineSegment(sketch, "E333", {"start": v(427.2, 482.1) * mm, "end": v(426.44, 483.22) * mm});
            skLineSegment(sketch, "E334", {"start": v(426.44, 483.22) * mm, "end": v(425.55, 484.32) * mm});
            skLineSegment(sketch, "E335", {"start": v(425.55, 484.32) * mm, "end": v(424.52, 485.4) * mm});
            skLineSegment(sketch, "E336", {"start": v(424.52, 485.4) * mm, "end": v(423.35, 486.44) * mm});
            skLineSegment(sketch, "E337", {"start": v(423.35, 486.44) * mm, "end": v(422.04, 487.45) * mm});
            skLineSegment(sketch, "E338", {"start": v(422.04, 487.45) * mm, "end": v(420.58, 488.42) * mm});
            skLineSegment(sketch, "E339", {"start": v(420.58, 488.42) * mm, "end": v(418.96, 489.36) * mm});
            skLineSegment(sketch, "E340", {"start": v(418.96, 489.36) * mm, "end": v(417.18, 490.27) * mm});
            skLineSegment(sketch, "E341", {"start": v(417.18, 490.27) * mm, "end": v(415.24, 491.13) * mm});
            skLineSegment(sketch, "E342", {"start": v(415.24, 491.13) * mm, "end": v(413.97, 491.61) * mm});
            skLineSegment(sketch, "E343", {"start": v(413.97, 491.61) * mm, "end": v(412.7, 491.99) * mm});
            skLineSegment(sketch, "E344", {"start": v(412.7, 491.99) * mm, "end": v(411.46, 492.26) * mm});
            skLineSegment(sketch, "E345", {"start": v(411.46, 492.26) * mm, "end": v(410.22, 492.43) * mm});
            skLineSegment(sketch, "E346", {"start": v(410.22, 492.43) * mm, "end": v(409, 492.52) * mm});
            skLineSegment(sketch, "E347", {"start": v(409, 492.52) * mm, "end": v(407.77, 492.5) * mm});
            skLineSegment(sketch, "E348", {"start": v(407.77, 492.5) * mm, "end": v(406.56, 492.42) * mm});
            skLineSegment(sketch, "E349", {"start": v(406.56, 492.42) * mm, "end": v(405.35, 492.24) * mm});
            skLineSegment(sketch, "E350", {"start": v(405.35, 492.24) * mm, "end": v(404.15, 492) * mm});
            skLineSegment(sketch, "E351", {"start": v(404.15, 492) * mm, "end": v(402.96, 491.67) * mm});
            skLineSegment(sketch, "E352", {"start": v(402.96, 491.67) * mm, "end": v(401.78, 491.28) * mm});
            skLineSegment(sketch, "E353", {"start": v(401.78, 491.28) * mm, "end": v(400.6, 490.83) * mm});
            skLineSegment(sketch, "E354", {"start": v(400.6, 490.83) * mm, "end": v(399.42, 490.31) * mm});
            skLineSegment(sketch, "E355", {"start": v(399.42, 490.31) * mm, "end": v(398.24, 489.74) * mm});
            skLineSegment(sketch, "E356", {"start": v(398.24, 489.74) * mm, "end": v(397.07, 489.11) * mm});
            skLineSegment(sketch, "E357", {"start": v(397.07, 489.11) * mm, "end": v(395.9, 488.44) * mm});
            skLineSegment(sketch, "E358", {"start": v(395.9, 488.44) * mm, "end": v(394.74, 487.72) * mm});
            skLineSegment(sketch, "E359", {"start": v(394.74, 487.72) * mm, "end": v(393.57, 486.97) * mm});
            skLineSegment(sketch, "E360", {"start": v(393.57, 486.97) * mm, "end": v(392.41, 486.17) * mm});
            skLineSegment(sketch, "E361", {"start": v(392.41, 486.17) * mm, "end": v(391.25, 485.35) * mm});
            skLineSegment(sketch, "E362", {"start": v(391.25, 485.35) * mm, "end": v(390.08, 484.5) * mm});
            skLineSegment(sketch, "E363", {"start": v(390.08, 484.5) * mm, "end": v(388.91, 483.62) * mm});
            skLineSegment(sketch, "E364", {"start": v(388.91, 483.62) * mm, "end": v(387.74, 482.73) * mm});
            skLineSegment(sketch, "E365", {"start": v(387.74, 482.73) * mm, "end": v(386.57, 481.82) * mm});
            skLineSegment(sketch, "E366", {"start": v(386.57, 481.82) * mm, "end": v(385.4, 480.9) * mm});
            skLineSegment(sketch, "E367", {"start": v(385.4, 480.9) * mm, "end": v(384.22, 479.96) * mm});
            skLineSegment(sketch, "E368", {"start": v(384.22, 479.96) * mm, "end": v(383.03, 479.03) * mm});
            skLineSegment(sketch, "E369", {"start": v(383.03, 479.03) * mm, "end": v(381.85, 478.1) * mm});
            skLineSegment(sketch, "E370", {"start": v(381.85, 478.1) * mm, "end": v(380.65, 477.17) * mm});
            skLineSegment(sketch, "E371", {"start": v(380.65, 477.17) * mm, "end": v(379.45, 476.26) * mm});
            skLineSegment(sketch, "E372", {"start": v(379.45, 476.26) * mm, "end": v(378.24, 475.35) * mm});
            skLineSegment(sketch, "E373", {"start": v(378.24, 475.35) * mm, "end": v(377.02, 474.46) * mm});
            skLineSegment(sketch, "E374", {"start": v(377.02, 474.46) * mm, "end": v(375.8, 473.6) * mm});
            skLineSegment(sketch, "E375", {"start": v(375.8, 473.6) * mm, "end": v(374.57, 472.76) * mm});
            skLineSegment(sketch, "E376", {"start": v(374.57, 472.76) * mm, "end": v(373.32, 471.95) * mm});
            skLineSegment(sketch, "E377", {"start": v(373.32, 471.95) * mm, "end": v(372.07, 471.17) * mm});
            skLineSegment(sketch, "E378", {"start": v(372.07, 471.17) * mm, "end": v(370.8, 470.43) * mm});
            skLineSegment(sketch, "E379", {"start": v(370.8, 470.43) * mm, "end": v(369.53, 469.73) * mm});
            skLineSegment(sketch, "E380", {"start": v(369.53, 469.73) * mm, "end": v(368.24, 469.08) * mm});
            skLineSegment(sketch, "E381", {"start": v(368.24, 469.08) * mm, "end": v(366.94, 468.48) * mm});
            skLineSegment(sketch, "E382", {"start": v(366.94, 468.48) * mm, "end": v(365.62, 467.93) * mm});
            skLineSegment(sketch, "E383", {"start": v(365.62, 467.93) * mm, "end": v(364.29, 467.44) * mm});
            skLineSegment(sketch, "E384", {"start": v(364.29, 467.44) * mm, "end": v(362.94, 467.01) * mm});
            skLineSegment(sketch, "E385", {"start": v(362.94, 467.01) * mm, "end": v(361.58, 466.65) * mm});
            skLineSegment(sketch, "E386", {"start": v(361.58, 466.65) * mm, "end": v(360.2, 466.36) * mm});
            skLineSegment(sketch, "E387", {"start": v(360.2, 466.36) * mm, "end": v(358.82, 466.15) * mm});
            skLineSegment(sketch, "E388", {"start": v(358.82, 466.15) * mm, "end": v(357.4, 466.01) * mm});
            skLineSegment(sketch, "E389", {"start": v(357.4, 466.01) * mm, "end": v(355.98, 465.96) * mm});
            skLineSegment(sketch, "E390", {"start": v(355.98, 465.96) * mm, "end": v(354.53, 465.99) * mm});
            skLineSegment(sketch, "E391", {"start": v(354.53, 465.99) * mm, "end": v(353.06, 466.11) * mm});
            skLineSegment(sketch, "E392", {"start": v(353.06, 466.11) * mm, "end": v(351.58, 466.33) * mm});
            skLineSegment(sketch, "E393", {"start": v(351.58, 466.33) * mm, "end": v(350.07, 466.65) * mm});
            skLineSegment(sketch, "E394", {"start": v(350.07, 466.65) * mm, "end": v(348.3, 467.14) * mm});
            skLineSegment(sketch, "E395", {"start": v(348.3, 467.14) * mm, "end": v(346.6, 467.73) * mm});
            skLineSegment(sketch, "E396", {"start": v(346.6, 467.73) * mm, "end": v(344.95, 468.43) * mm});
            skLineSegment(sketch, "E397", {"start": v(344.95, 468.43) * mm, "end": v(343.35, 469.23) * mm});
            skLineSegment(sketch, "E398", {"start": v(343.35, 469.23) * mm, "end": v(341.8, 470.12) * mm});
            skLineSegment(sketch, "E399", {"start": v(341.8, 470.12) * mm, "end": v(340.3, 471.1) * mm});
            skLineSegment(sketch, "E400", {"start": v(340.3, 471.1) * mm, "end": v(338.84, 472.18) * mm});
            skLineSegment(sketch, "E401", {"start": v(338.84, 472.18) * mm, "end": v(337.42, 473.33) * mm});
            skLineSegment(sketch, "E402", {"start": v(337.42, 473.33) * mm, "end": v(336.31, 474.32) * mm});
            skLineSegment(sketch, "E403", {"start": v(336.31, 474.32) * mm, "end": v(335.27, 475.34) * mm});
            skLineSegment(sketch, "E404", {"start": v(335.27, 475.34) * mm, "end": v(334.31, 476.37) * mm});
            skLineSegment(sketch, "E405", {"start": v(334.31, 476.37) * mm, "end": v(333.42, 477.41) * mm});
            skLineSegment(sketch, "E406", {"start": v(333.42, 477.41) * mm, "end": v(332.6, 478.48) * mm});
            skLineSegment(sketch, "E407", {"start": v(332.6, 478.48) * mm, "end": v(331.84, 479.56) * mm});
            skLineSegment(sketch, "E408", {"start": v(331.84, 479.56) * mm, "end": v(331.15, 480.65) * mm});
            skLineSegment(sketch, "E409", {"start": v(331.15, 480.65) * mm, "end": v(330.53, 481.76) * mm});
            skLineSegment(sketch, "E410", {"start": v(330.53, 481.76) * mm, "end": v(329.96, 482.88) * mm});
            skLineSegment(sketch, "E411", {"start": v(329.96, 482.88) * mm, "end": v(329.46, 484.02) * mm});
            skLineSegment(sketch, "E412", {"start": v(329.46, 484.02) * mm, "end": v(329.01, 485.17) * mm});
            skLineSegment(sketch, "E413", {"start": v(329.01, 485.17) * mm, "end": v(328.62, 486.33) * mm});
            skLineSegment(sketch, "E414", {"start": v(328.62, 486.33) * mm, "end": v(328.28, 487.5) * mm});
            skLineSegment(sketch, "E415", {"start": v(328.28, 487.5) * mm, "end": v(327.99, 488.68) * mm});
            skLineSegment(sketch, "E416", {"start": v(327.99, 488.68) * mm, "end": v(327.75, 489.88) * mm});
            skLineSegment(sketch, "E417", {"start": v(327.75, 489.88) * mm, "end": v(327.55, 491.08) * mm});
            skLineSegment(sketch, "E418", {"start": v(327.55, 491.08) * mm, "end": v(327.4, 492.3) * mm});
            skLineSegment(sketch, "E419", {"start": v(327.4, 492.3) * mm, "end": v(327.3, 493.51) * mm});
            skLineSegment(sketch, "E420", {"start": v(327.3, 493.51) * mm, "end": v(327.23, 494.74) * mm});
            skLineSegment(sketch, "E421", {"start": v(327.23, 494.74) * mm, "end": v(327.2, 495.97) * mm});
            skLineSegment(sketch, "E422", {"start": v(327.2, 495.97) * mm, "end": v(327.21, 497.21) * mm});
            skLineSegment(sketch, "E423", {"start": v(327.21, 497.21) * mm, "end": v(327.25, 498.46) * mm});
            skLineSegment(sketch, "E424", {"start": v(327.25, 498.46) * mm, "end": v(327.33, 499.71) * mm});
            skLineSegment(sketch, "E425", {"start": v(327.33, 499.71) * mm, "end": v(327.43, 500.97) * mm});
            skLineSegment(sketch, "E426", {"start": v(327.43, 500.97) * mm, "end": v(327.57, 502.23) * mm});
            skLineSegment(sketch, "E427", {"start": v(327.57, 502.23) * mm, "end": v(327.72, 503.5) * mm});
            skLineSegment(sketch, "E428", {"start": v(327.72, 503.5) * mm, "end": v(327.9, 504.76) * mm});
            skLineSegment(sketch, "E429", {"start": v(327.9, 504.76) * mm, "end": v(328.1, 506.02) * mm});
            skLineSegment(sketch, "E430", {"start": v(328.1, 506.02) * mm, "end": v(328.33, 507.3) * mm});
            skLineSegment(sketch, "E431", {"start": v(328.33, 507.3) * mm, "end": v(328.57, 508.56) * mm});
            skLineSegment(sketch, "E432", {"start": v(328.57, 508.56) * mm, "end": v(328.83, 509.83) * mm});
            skLineSegment(sketch, "E433", {"start": v(328.83, 509.83) * mm, "end": v(329.1, 511.1) * mm});
            skLineSegment(sketch, "E434", {"start": v(329.1, 511.1) * mm, "end": v(329.38, 512.37) * mm});
            skLineSegment(sketch, "E435", {"start": v(329.38, 512.37) * mm, "end": v(329.67, 513.64) * mm});
            skLineSegment(sketch, "E436", {"start": v(329.67, 513.64) * mm, "end": v(329.96, 514.9) * mm});
            skLineSegment(sketch, "E437", {"start": v(329.96, 514.9) * mm, "end": v(330.27, 516.17) * mm});
            skLineSegment(sketch, "E438", {"start": v(330.27, 516.17) * mm, "end": v(330.57, 517.42) * mm});
            skLineSegment(sketch, "E439", {"start": v(330.57, 517.42) * mm, "end": v(330.87, 518.68) * mm});
            skLineSegment(sketch, "E440", {"start": v(330.87, 518.68) * mm, "end": v(331.18, 519.93) * mm});
            skLineSegment(sketch, "E441", {"start": v(331.18, 519.93) * mm, "end": v(331.48, 521.17) * mm});
            skLineSegment(sketch, "E442", {"start": v(331.48, 521.17) * mm, "end": v(331.77, 522.4) * mm});
            skLineSegment(sketch, "E443", {"start": v(331.77, 522.4) * mm, "end": v(332.06, 523.64) * mm});
            skLineSegment(sketch, "E444", {"start": v(332.06, 523.64) * mm, "end": v(332.34, 524.86) * mm});
            skLineSegment(sketch, "E445", {"start": v(332.34, 524.86) * mm, "end": v(332.6, 526.08) * mm});
            skLineSegment(sketch, "E446", {"start": v(332.6, 526.08) * mm, "end": v(332.86, 527.28) * mm});
            skLineSegment(sketch, "E447", {"start": v(332.86, 527.28) * mm, "end": v(333.1, 528.48) * mm});
            skLineSegment(sketch, "E448", {"start": v(333.1, 528.48) * mm, "end": v(333.3, 529.67) * mm});
            skLineSegment(sketch, "E449", {"start": v(333.3, 529.67) * mm, "end": v(333.5, 530.84) * mm});
            skLineSegment(sketch, "E450", {"start": v(333.5, 530.84) * mm, "end": v(333.68, 532) * mm});
            skLineSegment(sketch, "E451", {"start": v(333.68, 532) * mm, "end": v(333.83, 533.16) * mm});
            skLineSegment(sketch, "E452", {"start": v(333.83, 533.16) * mm, "end": v(333.96, 534.3) * mm});
            skLineSegment(sketch, "E453", {"start": v(333.96, 534.3) * mm, "end": v(334.05, 535.43) * mm});
            skLineSegment(sketch, "E454", {"start": v(334.05, 535.43) * mm, "end": v(334.12, 536.55) * mm});
            skLineSegment(sketch, "E455", {"start": v(334.12, 536.55) * mm, "end": v(334.15, 537.65) * mm});
            skLineSegment(sketch, "E456", {"start": v(334.15, 537.65) * mm, "end": v(334.15, 538.74) * mm});
            skLineSegment(sketch, "E457", {"start": v(334.15, 538.74) * mm, "end": v(334.11, 539.8) * mm});
            skLineSegment(sketch, "E458", {"start": v(334.11, 539.8) * mm, "end": v(334.04, 540.86) * mm});
            skLineSegment(sketch, "E459", {"start": v(334.04, 540.86) * mm, "end": v(333.92, 541.9) * mm});
            skLineSegment(sketch, "E460", {"start": v(333.92, 541.9) * mm, "end": v(333.76, 542.92) * mm});
            skLineSegment(sketch, "E461", {"start": v(333.76, 542.92) * mm, "end": v(333.55, 543.92) * mm});
            skLineSegment(sketch, "E462", {"start": v(333.55, 543.92) * mm, "end": v(333.3, 544.9) * mm});
            skLineSegment(sketch, "E463", {"start": v(333.3, 544.9) * mm, "end": v(333, 545.87) * mm});
            skLineSegment(sketch, "E464", {"start": v(333, 545.87) * mm, "end": v(332.64, 546.81) * mm});
            skLineSegment(sketch, "E465", {"start": v(332.64, 546.81) * mm, "end": v(332.23, 547.74) * mm});
            skLineSegment(sketch, "E466", {"start": v(332.23, 547.74) * mm, "end": v(331.77, 548.64) * mm});
            skLineSegment(sketch, "E467", {"start": v(331.77, 548.64) * mm, "end": v(331.24, 549.52) * mm});
            skLineSegment(sketch, "E468", {"start": v(331.24, 549.52) * mm, "end": v(330.66, 550.38) * mm});
            skLineSegment(sketch, "E469", {"start": v(330.66, 550.38) * mm, "end": v(330.02, 551.21) * mm});
            skLineSegment(sketch, "E470", {"start": v(330.02, 551.21) * mm, "end": v(329.31, 552.02) * mm});
            skLineSegment(sketch, "E471", {"start": v(329.31, 552.02) * mm, "end": v(328.54, 552.81) * mm});
            skLineSegment(sketch, "E472", {"start": v(328.54, 552.81) * mm, "end": v(327.7, 553.58) * mm});
            skLineSegment(sketch, "E473", {"start": v(327.7, 553.58) * mm, "end": v(326.79, 554.31) * mm});
            skLineSegment(sketch, "E474", {"start": v(326.79, 554.31) * mm, "end": v(325.8, 555.02) * mm});
            skLineSegment(sketch, "E475", {"start": v(325.8, 555.02) * mm, "end": v(324.74, 555.7) * mm});
            skLineSegment(sketch, "E476", {"start": v(324.74, 555.7) * mm, "end": v(323.6, 556.36) * mm});
            skLineSegment(sketch, "E477", {"start": v(323.6, 556.36) * mm, "end": v(322.4, 557) * mm});
            skLineSegment(sketch, "E478", {"start": v(322.4, 557) * mm, "end": v(321.1, 557.6) * mm});
            skLineSegment(sketch, "E479", {"start": v(321.1, 557.6) * mm, "end": v(319.93, 558.07) * mm});
            skLineSegment(sketch, "E480", {"start": v(319.93, 558.07) * mm, "end": v(318.77, 558.45) * mm});
            skLineSegment(sketch, "E481", {"start": v(318.77, 558.45) * mm, "end": v(317.63, 558.75) * mm});
            skLineSegment(sketch, "E482", {"start": v(317.63, 558.75) * mm, "end": v(316.5, 558.96) * mm});
            skLineSegment(sketch, "E483", {"start": v(316.5, 558.96) * mm, "end": v(315.4, 559.09) * mm});
            skLineSegment(sketch, "E484", {"start": v(315.4, 559.09) * mm, "end": v(314.3, 559.14) * mm});
            skLineSegment(sketch, "E485", {"start": v(314.3, 559.14) * mm, "end": v(313.23, 559.1) * mm});
            skLineSegment(sketch, "E486", {"start": v(313.23, 559.1) * mm, "end": v(312.17, 559) * mm});
            skLineSegment(sketch, "E487", {"start": v(312.17, 559) * mm, "end": v(311.12, 558.83) * mm});
            skLineSegment(sketch, "E488", {"start": v(311.12, 558.83) * mm, "end": v(310.09, 558.6) * mm});
            skLineSegment(sketch, "E489", {"start": v(310.09, 558.6) * mm, "end": v(309.06, 558.29) * mm});
            skLineSegment(sketch, "E490", {"start": v(309.06, 558.29) * mm, "end": v(308.05, 557.92) * mm});
            skLineSegment(sketch, "E491", {"start": v(308.05, 557.92) * mm, "end": v(307.05, 557.5) * mm});
            skLineSegment(sketch, "E492", {"start": v(307.05, 557.5) * mm, "end": v(306.06, 557) * mm});
            skLineSegment(sketch, "E493", {"start": v(306.06, 557) * mm, "end": v(305.08, 556.47) * mm});
            skLineSegment(sketch, "E494", {"start": v(305.08, 556.47) * mm, "end": v(304.1, 555.88) * mm});
            skLineSegment(sketch, "E495", {"start": v(304.1, 555.88) * mm, "end": v(303.14, 555.24) * mm});
            skLineSegment(sketch, "E496", {"start": v(303.14, 555.24) * mm, "end": v(302.18, 554.56) * mm});
            skLineSegment(sketch, "E497", {"start": v(302.18, 554.56) * mm, "end": v(301.23, 553.84) * mm});
            skLineSegment(sketch, "E498", {"start": v(301.23, 553.84) * mm, "end": v(300.28, 553.07) * mm});
            skLineSegment(sketch, "E499", {"start": v(300.28, 553.07) * mm, "end": v(299.34, 552.27) * mm});
            skLineSegment(sketch, "E500", {"start": v(299.34, 552.27) * mm, "end": v(298.4, 551.43) * mm});
            skLineSegment(sketch, "E501", {"start": v(298.4, 551.43) * mm, "end": v(297.47, 550.56) * mm});
            skLineSegment(sketch, "E502", {"start": v(297.47, 550.56) * mm, "end": v(296.54, 549.67) * mm});
            skLineSegment(sketch, "E503", {"start": v(296.54, 549.67) * mm, "end": v(295.61, 548.75) * mm});
            skLineSegment(sketch, "E504", {"start": v(295.61, 548.75) * mm, "end": v(294.68, 547.8) * mm});
            skLineSegment(sketch, "E505", {"start": v(294.68, 547.8) * mm, "end": v(293.76, 546.84) * mm});
            skLineSegment(sketch, "E506", {"start": v(293.76, 546.84) * mm, "end": v(292.83, 545.86) * mm});
            skLineSegment(sketch, "E507", {"start": v(292.83, 545.86) * mm, "end": v(291.9, 544.86) * mm});
            skLineSegment(sketch, "E508", {"start": v(291.9, 544.86) * mm, "end": v(290.97, 543.85) * mm});
            skLineSegment(sketch, "E509", {"start": v(290.97, 543.85) * mm, "end": v(290.04, 542.84) * mm});
            skLineSegment(sketch, "E510", {"start": v(290.04, 542.84) * mm, "end": v(289.1, 541.81) * mm});
            skLineSegment(sketch, "E511", {"start": v(289.1, 541.81) * mm, "end": v(288.17, 540.79) * mm});
            skLineSegment(sketch, "E512", {"start": v(288.17, 540.79) * mm, "end": v(287.23, 539.76) * mm});
            skLineSegment(sketch, "E513", {"start": v(287.23, 539.76) * mm, "end": v(286.28, 538.74) * mm});
            skLineSegment(sketch, "E514", {"start": v(286.28, 538.74) * mm, "end": v(285.33, 537.72) * mm});
            skLineSegment(sketch, "E515", {"start": v(285.33, 537.72) * mm, "end": v(284.37, 536.72) * mm});
            skLineSegment(sketch, "E516", {"start": v(284.37, 536.72) * mm, "end": v(283.4, 535.72) * mm});
            skLineSegment(sketch, "E517", {"start": v(283.4, 535.72) * mm, "end": v(282.43, 534.73) * mm});
            skLineSegment(sketch, "E518", {"start": v(282.43, 534.73) * mm, "end": v(281.45, 533.77) * mm});
            skLineSegment(sketch, "E519", {"start": v(281.45, 533.77) * mm, "end": v(280.45, 532.82) * mm});
            skLineSegment(sketch, "E520", {"start": v(280.45, 532.82) * mm, "end": v(279.45, 531.9) * mm});
            skLineSegment(sketch, "E521", {"start": v(279.45, 531.9) * mm, "end": v(278.44, 531) * mm});
            skLineSegment(sketch, "E522", {"start": v(278.44, 531) * mm, "end": v(277.41, 530.13) * mm});
            skLineSegment(sketch, "E523", {"start": v(277.41, 530.13) * mm, "end": v(276.37, 529.29) * mm});
            skLineSegment(sketch, "E524", {"start": v(276.37, 529.29) * mm, "end": v(275.32, 528.48) * mm});
            skLineSegment(sketch, "E525", {"start": v(275.32, 528.48) * mm, "end": v(274.26, 527.71) * mm});
            skLineSegment(sketch, "E526", {"start": v(274.26, 527.71) * mm, "end": v(273.18, 526.98) * mm});
            skLineSegment(sketch, "E527", {"start": v(273.18, 526.98) * mm, "end": v(272.09, 526.3) * mm});
            skLineSegment(sketch, "E528", {"start": v(272.09, 526.3) * mm, "end": v(270.98, 525.65) * mm});
            skLineSegment(sketch, "E529", {"start": v(270.98, 525.65) * mm, "end": v(269.85, 525.06) * mm});
            skLineSegment(sketch, "E530", {"start": v(269.85, 525.06) * mm, "end": v(268.71, 524.51) * mm});
            skLineSegment(sketch, "E531", {"start": v(268.71, 524.51) * mm, "end": v(267.55, 524.02) * mm});
            skLineSegment(sketch, "E532", {"start": v(267.55, 524.02) * mm, "end": v(266.37, 523.59) * mm});
            skLineSegment(sketch, "E533", {"start": v(266.37, 523.59) * mm, "end": v(265.17, 523.21) * mm});
            skLineSegment(sketch, "E534", {"start": v(265.17, 523.21) * mm, "end": v(263.95, 522.9) * mm});
            skLineSegment(sketch, "E535", {"start": v(263.95, 522.9) * mm, "end": v(262.71, 522.65) * mm});
            skLineSegment(sketch, "E536", {"start": v(262.71, 522.65) * mm, "end": v(261.45, 522.47) * mm});
            skLineSegment(sketch, "E537", {"start": v(261.45, 522.47) * mm, "end": v(260.17, 522.36) * mm});
            skLineSegment(sketch, "E538", {"start": v(260.17, 522.36) * mm, "end": v(258.86, 522.33) * mm});
            skLineSegment(sketch, "E539", {"start": v(258.86, 522.33) * mm, "end": v(257.53, 522.37) * mm});
            skLineSegment(sketch, "E540", {"start": v(257.53, 522.37) * mm, "end": v(256.18, 522.49) * mm});
            skLineSegment(sketch, "E541", {"start": v(256.18, 522.49) * mm, "end": v(254.8, 522.69) * mm});
            skLineSegment(sketch, "E542", {"start": v(254.8, 522.69) * mm, "end": v(253.4, 522.97) * mm});
            skLineSegment(sketch, "E543", {"start": v(253.4, 522.97) * mm, "end": v(251.96, 523.35) * mm});
            skLineSegment(sketch, "E544", {"start": v(251.96, 523.35) * mm, "end": v(250.5, 523.8) * mm});
            skLineSegment(sketch, "E545", {"start": v(250.5, 523.8) * mm, "end": v(248.9, 524.41) * mm});
            skLineSegment(sketch, "E546", {"start": v(248.9, 524.41) * mm, "end": v(247.33, 525.1) * mm});
            skLineSegment(sketch, "E547", {"start": v(247.33, 525.1) * mm, "end": v(245.79, 525.85) * mm});
            skLineSegment(sketch, "E548", {"start": v(245.79, 525.85) * mm, "end": v(244.29, 526.69) * mm});
            skLineSegment(sketch, "E549", {"start": v(244.29, 526.69) * mm, "end": v(242.82, 527.6) * mm});
            skLineSegment(sketch, "E550", {"start": v(242.82, 527.6) * mm, "end": v(241.4, 528.57) * mm});
            skLineSegment(sketch, "E551", {"start": v(241.4, 528.57) * mm, "end": v(240.03, 529.6) * mm});
            skLineSegment(sketch, "E552", {"start": v(240.03, 529.6) * mm, "end": v(238.7, 530.7) * mm});
            skLineSegment(sketch, "E553", {"start": v(238.7, 530.7) * mm, "end": v(237.42, 531.87) * mm});
            skLineSegment(sketch, "E554", {"start": v(237.42, 531.87) * mm, "end": v(236.2, 533.1) * mm});
            skLineSegment(sketch, "E555", {"start": v(236.2, 533.1) * mm, "end": v(235.03, 534.37) * mm});
            skLineSegment(sketch, "E556", {"start": v(235.03, 534.37) * mm, "end": v(233.91, 535.7) * mm});
            skLineSegment(sketch, "E557", {"start": v(233.91, 535.7) * mm, "end": v(232.86, 537.07) * mm});
            skLineSegment(sketch, "E558", {"start": v(232.86, 537.07) * mm, "end": v(231.88, 538.49) * mm});
            skLineSegment(sketch, "E559", {"start": v(231.88, 538.49) * mm, "end": v(230.96, 539.95) * mm});
            skLineSegment(sketch, "E560", {"start": v(230.96, 539.95) * mm, "end": v(230.1, 541.45) * mm});
            skLineSegment(sketch, "E561", {"start": v(230.1, 541.45) * mm, "end": v(229.33, 543) * mm});
            skLineSegment(sketch, "E562", {"start": v(229.33, 543) * mm, "end": v(228.62, 544.57) * mm});
            skLineSegment(sketch, "E563", {"start": v(228.62, 544.57) * mm, "end": v(228, 546.17) * mm});
            skLineSegment(sketch, "E564", {"start": v(228, 546.17) * mm, "end": v(227.45, 547.8) * mm});
            skLineSegment(sketch, "E565", {"start": v(227.45, 547.8) * mm, "end": v(226.98, 549.46) * mm});
            skLineSegment(sketch, "E566", {"start": v(226.98, 549.46) * mm, "end": v(226.6, 551.13) * mm});
            skLineSegment(sketch, "E567", {"start": v(226.6, 551.13) * mm, "end": v(226.31, 552.83) * mm});
            skLineSegment(sketch, "E568", {"start": v(226.31, 552.83) * mm, "end": v(226.11, 554.55) * mm});
            skLineSegment(sketch, "E569", {"start": v(226.11, 554.55) * mm, "end": v(226, 556.27) * mm});
            skLineSegment(sketch, "E570", {"start": v(226, 556.27) * mm, "end": v(226, 558) * mm});
            skLineSegment(sketch, "E571", {"start": v(226, 558) * mm, "end": v(226.04, 559.25) * mm});
            skLineSegment(sketch, "E572", {"start": v(226.04, 559.25) * mm, "end": v(226.12, 560.53) * mm});
            skLineSegment(sketch, "E573", {"start": v(226.12, 560.53) * mm, "end": v(226.24, 561.83) * mm});
            skLineSegment(sketch, "E574", {"start": v(226.24, 561.83) * mm, "end": v(226.38, 563.16) * mm});
            skLineSegment(sketch, "E575", {"start": v(226.38, 563.16) * mm, "end": v(226.55, 564.52) * mm});
            skLineSegment(sketch, "E576", {"start": v(226.55, 564.52) * mm, "end": v(226.74, 565.9) * mm});
            skLineSegment(sketch, "E577", {"start": v(226.74, 565.9) * mm, "end": v(226.95, 567.3) * mm});
            skLineSegment(sketch, "E578", {"start": v(226.95, 567.3) * mm, "end": v(227.17, 568.7) * mm});
            skLineSegment(sketch, "E579", {"start": v(227.17, 568.7) * mm, "end": v(227.4, 570.13) * mm});
            skLineSegment(sketch, "E580", {"start": v(227.4, 570.13) * mm, "end": v(227.64, 571.57) * mm});
            skLineSegment(sketch, "E581", {"start": v(227.64, 571.57) * mm, "end": v(227.88, 573.01) * mm});
            skLineSegment(sketch, "E582", {"start": v(227.88, 573.01) * mm, "end": v(228.11, 574.46) * mm});
            skLineSegment(sketch, "E583", {"start": v(228.11, 574.46) * mm, "end": v(228.35, 575.91) * mm});
            skLineSegment(sketch, "E584", {"start": v(228.35, 575.91) * mm, "end": v(228.57, 577.37) * mm});
            skLineSegment(sketch, "E585", {"start": v(228.57, 577.37) * mm, "end": v(228.79, 578.82) * mm});
            skLineSegment(sketch, "E586", {"start": v(228.79, 578.82) * mm, "end": v(228.98, 580.26) * mm});
            skLineSegment(sketch, "E587", {"start": v(228.98, 580.26) * mm, "end": v(229.16, 581.7) * mm});
            skLineSegment(sketch, "E588", {"start": v(229.16, 581.7) * mm, "end": v(229.31, 583.13) * mm});
            skLineSegment(sketch, "E589", {"start": v(229.31, 583.13) * mm, "end": v(229.44, 584.54) * mm});
            skLineSegment(sketch, "E590", {"start": v(229.44, 584.54) * mm, "end": v(229.53, 585.94) * mm});
            skLineSegment(sketch, "E591", {"start": v(229.53, 585.94) * mm, "end": v(229.6, 587.32) * mm});
            skLineSegment(sketch, "E592", {"start": v(229.6, 587.32) * mm, "end": v(229.61, 588.68) * mm});
            skLineSegment(sketch, "E593", {"start": v(229.61, 588.68) * mm, "end": v(229.59, 590.02) * mm});
            skLineSegment(sketch, "E594", {"start": v(229.59, 590.02) * mm, "end": v(229.52, 591.33) * mm});
            skLineSegment(sketch, "E595", {"start": v(229.52, 591.33) * mm, "end": v(229.4, 592.61) * mm});
            skLineSegment(sketch, "E596", {"start": v(229.4, 592.61) * mm, "end": v(229.24, 593.86) * mm});
            skLineSegment(sketch, "E597", {"start": v(229.24, 593.86) * mm, "end": v(229, 595.08) * mm});
            skLineSegment(sketch, "E598", {"start": v(229, 595.08) * mm, "end": v(228.72, 596.26) * mm});
            skLineSegment(sketch, "E599", {"start": v(228.72, 596.26) * mm, "end": v(228.37, 597.4) * mm});
            skLineSegment(sketch, "E600", {"start": v(228.37, 597.4) * mm, "end": v(227.95, 598.5) * mm});
            skLineSegment(sketch, "E601", {"start": v(227.95, 598.5) * mm, "end": v(227.45, 599.55) * mm});
            skLineSegment(sketch, "E602", {"start": v(227.45, 599.55) * mm, "end": v(226.88, 600.55) * mm});
            skLineSegment(sketch, "E603", {"start": v(226.88, 600.55) * mm, "end": v(226.23, 601.5) * mm});
            skLineSegment(sketch, "E604", {"start": v(226.23, 601.5) * mm, "end": v(225.5, 602.4) * mm});
            skLineSegment(sketch, "E605", {"start": v(225.5, 602.4) * mm, "end": v(224.68, 603.26) * mm});
            skLineSegment(sketch, "E606", {"start": v(224.68, 603.26) * mm, "end": v(223.77, 604.05) * mm});
            skLineSegment(sketch, "E607", {"start": v(223.77, 604.05) * mm, "end": v(222.77, 604.77) * mm});
            skLineSegment(sketch, "E608", {"start": v(222.77, 604.77) * mm, "end": v(221.67, 605.44) * mm});
            skLineSegment(sketch, "E609", {"start": v(221.67, 605.44) * mm, "end": v(220.46, 606.04) * mm});
            skLineSegment(sketch, "E610", {"start": v(220.46, 606.04) * mm, "end": v(219.15, 606.57) * mm});
            skLineSegment(sketch, "E611", {"start": v(219.15, 606.57) * mm, "end": v(217.73, 607.03) * mm});
            skLineSegment(sketch, "E612", {"start": v(217.73, 607.03) * mm, "end": v(216.2, 607.42) * mm});
            skLineSegment(sketch, "E613", {"start": v(216.2, 607.42) * mm, "end": v(214.55, 607.73) * mm});
            skLineSegment(sketch, "E614", {"start": v(214.55, 607.73) * mm, "end": v(212.78, 607.96) * mm});
            skLineSegment(sketch, "E615", {"start": v(212.78, 607.96) * mm, "end": v(210.89, 608.1) * mm});
            skLineSegment(sketch, "E616", {"start": v(210.89, 608.1) * mm, "end": v(208.86, 608.17) * mm});
            skLineSegment(sketch, "E617", {"start": v(208.86, 608.17) * mm, "end": v(207.06, 608.08) * mm});
            skLineSegment(sketch, "E618", {"start": v(207.06, 608.08) * mm, "end": v(205.36, 607.8) * mm});
            skLineSegment(sketch, "E619", {"start": v(205.36, 607.8) * mm, "end": v(203.76, 607.34) * mm});
            skLineSegment(sketch, "E620", {"start": v(203.76, 607.34) * mm, "end": v(202.27, 606.71) * mm});
            skLineSegment(sketch, "E621", {"start": v(202.27, 606.71) * mm, "end": v(200.87, 605.93) * mm});
            skLineSegment(sketch, "E622", {"start": v(200.87, 605.93) * mm, "end": v(199.55, 605) * mm});
            skLineSegment(sketch, "E623", {"start": v(199.55, 605) * mm, "end": v(198.31, 603.96) * mm});
            skLineSegment(sketch, "E624", {"start": v(198.31, 603.96) * mm, "end": v(197.15, 602.8) * mm});
            skLineSegment(sketch, "E625", {"start": v(197.15, 602.8) * mm, "end": v(196.06, 601.56) * mm});
            skLineSegment(sketch, "E626", {"start": v(196.06, 601.56) * mm, "end": v(195.02, 600.23) * mm});
            skLineSegment(sketch, "E627", {"start": v(195.02, 600.23) * mm, "end": v(194.05, 598.83) * mm});
            skLineSegment(sketch, "E628", {"start": v(194.05, 598.83) * mm, "end": v(193.12, 597.38) * mm});
            skLineSegment(sketch, "E629", {"start": v(193.12, 597.38) * mm, "end": v(192.24, 595.89) * mm});
            skLineSegment(sketch, "E630", {"start": v(192.24, 595.89) * mm, "end": v(191.4, 594.38) * mm});
            skLineSegment(sketch, "E631", {"start": v(191.4, 594.38) * mm, "end": v(190.58, 592.86) * mm});
            skLineSegment(sketch, "E632", {"start": v(190.58, 592.86) * mm, "end": v(189.8, 591.34) * mm});
            skLineSegment(sketch, "E633", {"start": v(189.8, 591.34) * mm, "end": v(189.03, 589.85) * mm});
            skLineSegment(sketch, "E634", {"start": v(189.03, 589.85) * mm, "end": v(188.28, 588.39) * mm});
            skLineSegment(sketch, "E635", {"start": v(188.28, 588.39) * mm, "end": v(187.54, 586.97) * mm});
            skLineSegment(sketch, "E636", {"start": v(187.54, 586.97) * mm, "end": v(186.75, 585.54) * mm});
            skLineSegment(sketch, "E637", {"start": v(186.75, 585.54) * mm, "end": v(185.93, 584.1) * mm});
            skLineSegment(sketch, "E638", {"start": v(185.93, 584.1) * mm, "end": v(185.07, 582.66) * mm});
            skLineSegment(sketch, "E639", {"start": v(185.07, 582.66) * mm, "end": v(184.19, 581.23) * mm});
            skLineSegment(sketch, "E640", {"start": v(184.19, 581.23) * mm, "end": v(183.27, 579.82) * mm});
            skLineSegment(sketch, "E641", {"start": v(183.27, 579.82) * mm, "end": v(182.32, 578.42) * mm});
            skLineSegment(sketch, "E642", {"start": v(182.32, 578.42) * mm, "end": v(181.33, 577.04) * mm});
            skLineSegment(sketch, "E643", {"start": v(181.33, 577.04) * mm, "end": v(180.3, 575.68) * mm});
            skLineSegment(sketch, "E644", {"start": v(180.3, 575.68) * mm, "end": v(179.25, 574.35) * mm});
            skLineSegment(sketch, "E645", {"start": v(179.25, 574.35) * mm, "end": v(178.17, 573.06) * mm});
            skLineSegment(sketch, "E646", {"start": v(178.17, 573.06) * mm, "end": v(177.04, 571.8) * mm});
            skLineSegment(sketch, "E647", {"start": v(177.04, 571.8) * mm, "end": v(175.89, 570.59) * mm});
            skLineSegment(sketch, "E648", {"start": v(175.89, 570.59) * mm, "end": v(174.7, 569.42) * mm});
            skLineSegment(sketch, "E649", {"start": v(174.7, 569.42) * mm, "end": v(173.47, 568.3) * mm});
            skLineSegment(sketch, "E650", {"start": v(173.47, 568.3) * mm, "end": v(172.22, 567.24) * mm});
            skLineSegment(sketch, "E651", {"start": v(172.22, 567.24) * mm, "end": v(170.92, 566.23) * mm});
            skLineSegment(sketch, "E652", {"start": v(170.92, 566.23) * mm, "end": v(169.6, 565.29) * mm});
            skLineSegment(sketch, "E653", {"start": v(169.6, 565.29) * mm, "end": v(168.23, 564.41) * mm});
            skLineSegment(sketch, "E654", {"start": v(168.23, 564.41) * mm, "end": v(166.83, 563.6) * mm});
            skLineSegment(sketch, "E655", {"start": v(166.83, 563.6) * mm, "end": v(165.4, 562.88) * mm});
            skLineSegment(sketch, "E656", {"start": v(165.4, 562.88) * mm, "end": v(163.93, 562.23) * mm});
            skLineSegment(sketch, "E657", {"start": v(163.93, 562.23) * mm, "end": v(162.43, 561.66) * mm});
            skLineSegment(sketch, "E658", {"start": v(162.43, 561.66) * mm, "end": v(160.9, 561.19) * mm});
            skLineSegment(sketch, "E659", {"start": v(160.9, 561.19) * mm, "end": v(159.32, 560.8) * mm});
            skLineSegment(sketch, "E660", {"start": v(159.32, 560.8) * mm, "end": v(157.7, 560.51) * mm});
            skLineSegment(sketch, "E661", {"start": v(157.7, 560.51) * mm, "end": v(156.06, 560.33) * mm});
            skLineSegment(sketch, "E662", {"start": v(156.06, 560.33) * mm, "end": v(154.38, 560.25) * mm});
            skLineSegment(sketch, "E663", {"start": v(154.38, 560.25) * mm, "end": v(152.66, 560.27) * mm});
            skLineSegment(sketch, "E664", {"start": v(152.66, 560.27) * mm, "end": v(150.91, 560.41) * mm});
            skLineSegment(sketch, "E665", {"start": v(150.91, 560.41) * mm, "end": v(149.12, 560.67) * mm});
            skLineSegment(sketch, "E666", {"start": v(149.12, 560.67) * mm, "end": v(147.23, 561.05) * mm});
            skLineSegment(sketch, "E667", {"start": v(147.23, 561.05) * mm, "end": v(145.4, 561.52) * mm});
            skLineSegment(sketch, "E668", {"start": v(145.4, 561.52) * mm, "end": v(143.65, 562.06) * mm});
            skLineSegment(sketch, "E669", {"start": v(143.65, 562.06) * mm, "end": v(141.96, 562.68) * mm});
            skLineSegment(sketch, "E670", {"start": v(141.96, 562.68) * mm, "end": v(140.34, 563.37) * mm});
            skLineSegment(sketch, "E671", {"start": v(140.34, 563.37) * mm, "end": v(138.78, 564.13) * mm});
            skLineSegment(sketch, "E672", {"start": v(138.78, 564.13) * mm, "end": v(137.29, 564.96) * mm});
            skLineSegment(sketch, "E673", {"start": v(137.29, 564.96) * mm, "end": v(135.86, 565.86) * mm});
            skLineSegment(sketch, "E674", {"start": v(135.86, 565.86) * mm, "end": v(134.5, 566.83) * mm});
            skLineSegment(sketch, "E675", {"start": v(134.5, 566.83) * mm, "end": v(133.2, 567.86) * mm});
            skLineSegment(sketch, "E676", {"start": v(133.2, 567.86) * mm, "end": v(131.95, 568.94) * mm});
            skLineSegment(sketch, "E677", {"start": v(131.95, 568.94) * mm, "end": v(130.77, 570.09) * mm});
            skLineSegment(sketch, "E678", {"start": v(130.77, 570.09) * mm, "end": v(129.64, 571.28) * mm});
            skLineSegment(sketch, "E679", {"start": v(129.64, 571.28) * mm, "end": v(128.58, 572.54) * mm});
            skLineSegment(sketch, "E680", {"start": v(128.58, 572.54) * mm, "end": v(127.57, 573.84) * mm});
            skLineSegment(sketch, "E681", {"start": v(127.57, 573.84) * mm, "end": v(126.63, 575.19) * mm});
            skLineSegment(sketch, "E682", {"start": v(126.63, 575.19) * mm, "end": v(125.73, 576.59) * mm});
            skLineSegment(sketch, "E683", {"start": v(125.73, 576.59) * mm, "end": v(124.9, 578.03) * mm});
            skLineSegment(sketch, "E684", {"start": v(124.9, 578.03) * mm, "end": v(124.11, 579.5) * mm});
            skLineSegment(sketch, "E685", {"start": v(124.11, 579.5) * mm, "end": v(123.38, 581.03) * mm});
            skLineSegment(sketch, "E686", {"start": v(123.38, 581.03) * mm, "end": v(122.7, 582.58) * mm});
            skLineSegment(sketch, "E687", {"start": v(122.7, 582.58) * mm, "end": v(122.08, 584.18) * mm});
            skLineSegment(sketch, "E688", {"start": v(122.08, 584.18) * mm, "end": v(121.5, 585.8) * mm});
            skLineSegment(sketch, "E689", {"start": v(121.5, 585.8) * mm, "end": v(120.98, 587.45) * mm});
            skLineSegment(sketch, "E690", {"start": v(120.98, 587.45) * mm, "end": v(120.51, 589.13) * mm});
            skLineSegment(sketch, "E691", {"start": v(120.51, 589.13) * mm, "end": v(120.08, 590.83) * mm});
            skLineSegment(sketch, "E692", {"start": v(120.08, 590.83) * mm, "end": v(119.7, 592.56) * mm});
            skLineSegment(sketch, "E693", {"start": v(119.7, 592.56) * mm, "end": v(119.38, 594.3) * mm});
            skLineSegment(sketch, "E694", {"start": v(119.38, 594.3) * mm, "end": v(119.09, 596.07) * mm});
            skLineSegment(sketch, "E695", {"start": v(119.09, 596.07) * mm, "end": v(118.85, 597.85) * mm});
            skLineSegment(sketch, "E696", {"start": v(118.85, 597.85) * mm, "end": v(118.65, 599.65) * mm});
            skLineSegment(sketch, "E697", {"start": v(118.65, 599.65) * mm, "end": v(118.51, 601.23) * mm});
            skLineSegment(sketch, "E698", {"start": v(118.51, 601.23) * mm, "end": v(118.39, 602.82) * mm});
            skLineSegment(sketch, "E699", {"start": v(118.39, 602.82) * mm, "end": v(118.28, 604.4) * mm});
            skLineSegment(sketch, "E700", {"start": v(118.28, 604.4) * mm, "end": v(118.18, 606) * mm});
            skLineSegment(sketch, "E701", {"start": v(118.18, 606) * mm, "end": v(118.09, 607.57) * mm});
            skLineSegment(sketch, "E702", {"start": v(118.09, 607.57) * mm, "end": v(117.99, 609.14) * mm});
            skLineSegment(sketch, "E703", {"start": v(117.99, 609.14) * mm, "end": v(117.89, 610.7) * mm});
            skLineSegment(sketch, "E704", {"start": v(117.89, 610.7) * mm, "end": v(117.78, 612.23) * mm});
            skLineSegment(sketch, "E705", {"start": v(117.78, 612.23) * mm, "end": v(117.65, 613.75) * mm});
            skLineSegment(sketch, "E706", {"start": v(117.65, 613.75) * mm, "end": v(117.5, 615.24) * mm});
            skLineSegment(sketch, "E707", {"start": v(117.5, 615.24) * mm, "end": v(117.32, 616.71) * mm});
            skLineSegment(sketch, "E708", {"start": v(117.32, 616.71) * mm, "end": v(117.12, 618.15) * mm});
            skLineSegment(sketch, "E709", {"start": v(117.12, 618.15) * mm, "end": v(116.88, 619.56) * mm});
            skLineSegment(sketch, "E710", {"start": v(116.88, 619.56) * mm, "end": v(116.6, 620.93) * mm});
            skLineSegment(sketch, "E711", {"start": v(116.6, 620.93) * mm, "end": v(116.27, 622.26) * mm});
            skLineSegment(sketch, "E712", {"start": v(116.27, 622.26) * mm, "end": v(115.9, 623.54) * mm});
            skLineSegment(sketch, "E713", {"start": v(115.9, 623.54) * mm, "end": v(115.46, 624.78) * mm});
            skLineSegment(sketch, "E714", {"start": v(115.46, 624.78) * mm, "end": v(114.97, 625.98) * mm});
            skLineSegment(sketch, "E715", {"start": v(114.97, 625.98) * mm, "end": v(114.41, 627.12) * mm});
            skLineSegment(sketch, "E716", {"start": v(114.41, 627.12) * mm, "end": v(113.78, 628.2) * mm});
            skLineSegment(sketch, "E717", {"start": v(113.78, 628.2) * mm, "end": v(113.08, 629.22) * mm});
            skLineSegment(sketch, "E718", {"start": v(113.08, 629.22) * mm, "end": v(112.3, 630.19) * mm});
            skLineSegment(sketch, "E719", {"start": v(112.3, 630.19) * mm, "end": v(111.43, 631.08) * mm});
            skLineSegment(sketch, "E720", {"start": v(111.43, 631.08) * mm, "end": v(110.47, 631.9) * mm});
            skLineSegment(sketch, "E721", {"start": v(110.47, 631.9) * mm, "end": v(109.41, 632.66) * mm});
            skLineSegment(sketch, "E722", {"start": v(109.41, 632.66) * mm, "end": v(108.26, 633.34) * mm});
            skLineSegment(sketch, "E723", {"start": v(108.26, 633.34) * mm, "end": v(107, 633.95) * mm});
            skLineSegment(sketch, "E724", {"start": v(107, 633.95) * mm, "end": v(105.63, 634.46) * mm});
            skLineSegment(sketch, "E725", {"start": v(105.63, 634.46) * mm, "end": v(104.14, 634.9) * mm});
            skLineSegment(sketch, "E726", {"start": v(104.14, 634.9) * mm, "end": v(102.54, 635.24) * mm});
            skLineSegment(sketch, "E727", {"start": v(102.54, 635.24) * mm, "end": v(100.8, 635.5) * mm});
            skLineSegment(sketch, "E728", {"start": v(100.8, 635.5) * mm, "end": v(98.95, 635.66) * mm});
            skLineSegment(sketch, "E729", {"start": v(98.95, 635.66) * mm, "end": v(96.95, 635.72) * mm});
            skLineSegment(sketch, "E730", {"start": v(96.95, 635.72) * mm, "end": v(94.82, 635.68) * mm});
            skLineSegment(sketch, "E731", {"start": v(94.82, 635.68) * mm, "end": v(92.95, 635.5) * mm});
            skLineSegment(sketch, "E732", {"start": v(92.95, 635.5) * mm, "end": v(91.23, 635.1) * mm});
            skLineSegment(sketch, "E733", {"start": v(91.23, 635.1) * mm, "end": v(89.65, 634.55) * mm});
            skLineSegment(sketch, "E734", {"start": v(89.65, 634.55) * mm, "end": v(88.2, 633.82) * mm});
            skLineSegment(sketch, "E735", {"start": v(88.2, 633.82) * mm, "end": v(86.88, 632.93) * mm});
            skLineSegment(sketch, "E736", {"start": v(86.88, 632.93) * mm, "end": v(85.67, 631.9) * mm});
            skLineSegment(sketch, "E737", {"start": v(85.67, 631.9) * mm, "end": v(84.57, 630.76) * mm});
            skLineSegment(sketch, "E738", {"start": v(84.57, 630.76) * mm, "end": v(83.56, 629.5) * mm});
            skLineSegment(sketch, "E739", {"start": v(83.56, 629.5) * mm, "end": v(82.64, 628.14) * mm});
            skLineSegment(sketch, "E740", {"start": v(82.64, 628.14) * mm, "end": v(81.8, 626.7) * mm});
            skLineSegment(sketch, "E741", {"start": v(81.8, 626.7) * mm, "end": v(81.03, 625.19) * mm});
            skLineSegment(sketch, "E742", {"start": v(81.03, 625.19) * mm, "end": v(80.33, 623.62) * mm});
            skLineSegment(sketch, "E743", {"start": v(80.33, 623.62) * mm, "end": v(79.68, 622.02) * mm});
            skLineSegment(sketch, "E744", {"start": v(79.68, 622.02) * mm, "end": v(79.07, 620.38) * mm});
            skLineSegment(sketch, "E745", {"start": v(79.07, 620.38) * mm, "end": v(78.5, 618.74) * mm});
            skLineSegment(sketch, "E746", {"start": v(78.5, 618.74) * mm, "end": v(77.96, 617.1) * mm});
            skLineSegment(sketch, "E747", {"start": v(77.96, 617.1) * mm, "end": v(77.43, 615.47) * mm});
            skLineSegment(sketch, "E748", {"start": v(77.43, 615.47) * mm, "end": v(76.92, 613.87) * mm});
            skLineSegment(sketch, "E749", {"start": v(76.92, 613.87) * mm, "end": v(76.4, 612.32) * mm});
            skLineSegment(sketch, "E750", {"start": v(76.4, 612.32) * mm, "end": v(75.87, 610.74) * mm});
            skLineSegment(sketch, "E751", {"start": v(75.87, 610.74) * mm, "end": v(75.3, 609.16) * mm});
            skLineSegment(sketch, "E752", {"start": v(75.3, 609.16) * mm, "end": v(74.7, 607.58) * mm});
            skLineSegment(sketch, "E753", {"start": v(74.7, 607.58) * mm, "end": v(74.08, 606) * mm});
            skLineSegment(sketch, "E754", {"start": v(74.08, 606) * mm, "end": v(73.43, 604.44) * mm});
            skLineSegment(sketch, "E755", {"start": v(73.43, 604.44) * mm, "end": v(72.75, 602.89) * mm});
            skLineSegment(sketch, "E756", {"start": v(72.75, 602.89) * mm, "end": v(72.04, 601.35) * mm});
            skLineSegment(sketch, "E757", {"start": v(72.04, 601.35) * mm, "end": v(71.3, 599.83) * mm});
            skLineSegment(sketch, "E758", {"start": v(71.3, 599.83) * mm, "end": v(70.51, 598.34) * mm});
            skLineSegment(sketch, "E759", {"start": v(70.51, 598.34) * mm, "end": v(69.7, 596.86) * mm});
            skLineSegment(sketch, "E760", {"start": v(69.7, 596.86) * mm, "end": v(68.85, 595.42) * mm});
            skLineSegment(sketch, "E761", {"start": v(68.85, 595.42) * mm, "end": v(67.96, 594.02) * mm});
            skLineSegment(sketch, "E762", {"start": v(67.96, 594.02) * mm, "end": v(67.03, 592.65) * mm});
            skLineSegment(sketch, "E763", {"start": v(67.03, 592.65) * mm, "end": v(66.07, 591.32) * mm});
            skLineSegment(sketch, "E764", {"start": v(66.07, 591.32) * mm, "end": v(65.06, 590.03) * mm});
            skLineSegment(sketch, "E765", {"start": v(65.06, 590.03) * mm, "end": v(64.01, 588.8) * mm});
            skLineSegment(sketch, "E766", {"start": v(64.01, 588.8) * mm, "end": v(62.92, 587.6) * mm});
            skLineSegment(sketch, "E767", {"start": v(62.92, 587.6) * mm, "end": v(61.78, 586.47) * mm});
            skLineSegment(sketch, "E768", {"start": v(61.78, 586.47) * mm, "end": v(60.6, 585.4) * mm});
            skLineSegment(sketch, "E769", {"start": v(60.6, 585.4) * mm, "end": v(59.37, 584.39) * mm});
            skLineSegment(sketch, "E770", {"start": v(59.37, 584.39) * mm, "end": v(58.1, 583.44) * mm});
            skLineSegment(sketch, "E771", {"start": v(58.1, 583.44) * mm, "end": v(56.76, 582.57) * mm});
            skLineSegment(sketch, "E772", {"start": v(56.76, 582.57) * mm, "end": v(55.38, 581.76) * mm});
            skLineSegment(sketch, "E773", {"start": v(55.38, 581.76) * mm, "end": v(53.95, 581.04) * mm});
            skLineSegment(sketch, "E774", {"start": v(53.95, 581.04) * mm, "end": v(52.47, 580.39) * mm});
            skLineSegment(sketch, "E775", {"start": v(52.47, 580.39) * mm, "end": v(50.93, 579.83) * mm});
            skLineSegment(sketch, "E776", {"start": v(50.93, 579.83) * mm, "end": v(49.34, 579.35) * mm});
            skLineSegment(sketch, "E777", {"start": v(49.34, 579.35) * mm, "end": v(47.7, 578.96) * mm});
            skLineSegment(sketch, "E778", {"start": v(47.7, 578.96) * mm, "end": v(45.98, 578.67) * mm});
            skLineSegment(sketch, "E779", {"start": v(45.98, 578.67) * mm, "end": v(44.22, 578.48) * mm});
            skLineSegment(sketch, "E780", {"start": v(44.22, 578.48) * mm, "end": v(42.4, 578.39) * mm});
            skLineSegment(sketch, "E781", {"start": v(42.4, 578.39) * mm, "end": v(40.5, 578.4) * mm});
            skLineSegment(sketch, "E782", {"start": v(40.5, 578.4) * mm, "end": v(38.5, 578.51) * mm});
            skLineSegment(sketch, "E783", {"start": v(38.5, 578.51) * mm, "end": v(36.57, 578.7) * mm});
            skLineSegment(sketch, "E784", {"start": v(36.57, 578.7) * mm, "end": v(34.74, 578.98) * mm});
            skLineSegment(sketch, "E785", {"start": v(34.74, 578.98) * mm, "end": v(33, 579.33) * mm});
            skLineSegment(sketch, "E786", {"start": v(33, 579.33) * mm, "end": v(31.32, 579.75) * mm});
            skLineSegment(sketch, "E787", {"start": v(31.32, 579.75) * mm, "end": v(29.73, 580.25) * mm});
            skLineSegment(sketch, "E788", {"start": v(29.73, 580.25) * mm, "end": v(28.22, 580.81) * mm});
            skLineSegment(sketch, "E789", {"start": v(28.22, 580.81) * mm, "end": v(26.78, 581.44) * mm});
            skLineSegment(sketch, "E790", {"start": v(26.78, 581.44) * mm, "end": v(25.42, 582.14) * mm});
            skLineSegment(sketch, "E791", {"start": v(25.42, 582.14) * mm, "end": v(24.12, 582.9) * mm});
            skLineSegment(sketch, "E792", {"start": v(24.12, 582.9) * mm, "end": v(22.88, 583.72) * mm});
            skLineSegment(sketch, "E793", {"start": v(22.88, 583.72) * mm, "end": v(21.72, 584.6) * mm});
            skLineSegment(sketch, "E794", {"start": v(21.72, 584.6) * mm, "end": v(20.6, 585.52) * mm});
            skLineSegment(sketch, "E795", {"start": v(20.6, 585.52) * mm, "end": v(19.56, 586.5) * mm});
            skLineSegment(sketch, "E796", {"start": v(19.56, 586.5) * mm, "end": v(18.57, 587.54) * mm});
            skLineSegment(sketch, "E797", {"start": v(18.57, 587.54) * mm, "end": v(17.63, 588.63) * mm});
            skLineSegment(sketch, "E798", {"start": v(17.63, 588.63) * mm, "end": v(16.74, 589.75) * mm});
            skLineSegment(sketch, "E799", {"start": v(16.74, 589.75) * mm, "end": v(15.9, 590.93) * mm});
            skLineSegment(sketch, "E800", {"start": v(15.9, 590.93) * mm, "end": v(15.1, 592.14) * mm});
            skLineSegment(sketch, "E801", {"start": v(15.1, 592.14) * mm, "end": v(14.36, 593.4) * mm});
            skLineSegment(sketch, "E802", {"start": v(14.36, 593.4) * mm, "end": v(13.65, 594.68) * mm});
            skLineSegment(sketch, "E803", {"start": v(13.65, 594.68) * mm, "end": v(12.98, 596) * mm});
            skLineSegment(sketch, "E804", {"start": v(12.98, 596) * mm, "end": v(12.34, 597.36) * mm});
            skLineSegment(sketch, "E805", {"start": v(12.34, 597.36) * mm, "end": v(11.74, 598.74) * mm});
            skLineSegment(sketch, "E806", {"start": v(11.74, 598.74) * mm, "end": v(11.17, 600.15) * mm});
            skLineSegment(sketch, "E807", {"start": v(11.17, 600.15) * mm, "end": v(10.63, 601.59) * mm});
            skLineSegment(sketch, "E808", {"start": v(10.63, 601.59) * mm, "end": v(10.11, 603.04) * mm});
            skLineSegment(sketch, "E809", {"start": v(10.11, 603.04) * mm, "end": v(9.62, 604.52) * mm});
            skLineSegment(sketch, "E810", {"start": v(9.62, 604.52) * mm, "end": v(9.15, 606.02) * mm});
            skLineSegment(sketch, "E811", {"start": v(9.15, 606.02) * mm, "end": v(8.7, 607.53) * mm});
            skLineSegment(sketch, "E812", {"start": v(8.7, 607.53) * mm, "end": v(8.26, 609.05) * mm});
            skLineSegment(sketch, "E813", {"start": v(8.26, 609.05) * mm, "end": v(7.84, 610.58) * mm});
            skLineSegment(sketch, "E814", {"start": v(7.84, 610.58) * mm, "end": v(7.42, 612.13) * mm});
            skLineSegment(sketch, "E815", {"start": v(7.42, 612.13) * mm, "end": v(7.02, 613.67) * mm});
            skLineSegment(sketch, "E816", {"start": v(7.02, 613.67) * mm, "end": v(6.62, 615.23) * mm});
            skLineSegment(sketch, "E817", {"start": v(6.62, 615.23) * mm, "end": v(6.22, 616.78) * mm});
            skLineSegment(sketch, "E818", {"start": v(6.22, 616.78) * mm, "end": v(5.83, 618.33) * mm});
            skLineSegment(sketch, "E819", {"start": v(5.83, 618.33) * mm, "end": v(5.43, 619.88) * mm});
            skLineSegment(sketch, "E820", {"start": v(5.43, 619.88) * mm, "end": v(5.03, 621.42) * mm});
            skLineSegment(sketch, "E821", {"start": v(5.03, 621.42) * mm, "end": v(4.62, 622.95) * mm});
            skLineSegment(sketch, "E822", {"start": v(4.62, 622.95) * mm, "end": v(4.2, 624.48) * mm});
            skLineSegment(sketch, "E823", {"start": v(4.2, 624.48) * mm, "end": v(3.77, 625.99) * mm});
            skLineSegment(sketch, "E824", {"start": v(3.77, 625.99) * mm, "end": v(3.33, 627.48) * mm});
            skLineSegment(sketch, "E825", {"start": v(3.33, 627.48) * mm, "end": v(2.87, 628.96) * mm});
            skLineSegment(sketch, "E826", {"start": v(2.87, 628.96) * mm, "end": v(2.39, 630.42) * mm});
            skLineSegment(sketch, "E827", {"start": v(2.39, 630.42) * mm, "end": v(1.76, 632.04) * mm});
            skLineSegment(sketch, "E828", {"start": v(1.76, 632.04) * mm, "end": v(1, 633.56) * mm});
            skLineSegment(sketch, "E829", {"start": v(1, 633.56) * mm, "end": v(0.15, 634.99) * mm});
            skLineSegment(sketch, "E830", {"start": v(0.15, 634.99) * mm, "end": v(-0.82, 636.3) * mm});
            skLineSegment(sketch, "E831", {"start": v(-0.82, 636.3) * mm, "end": v(-1.88, 637.53) * mm});
            skLineSegment(sketch, "E832", {"start": v(-1.88, 637.53) * mm, "end": v(-3.04, 638.64) * mm});
            skLineSegment(sketch, "E833", {"start": v(-3.04, 638.64) * mm, "end": v(-4.27, 639.64) * mm});
            skLineSegment(sketch, "E834", {"start": v(-4.27, 639.64) * mm, "end": v(-5.59, 640.54) * mm});
            skLineSegment(sketch, "E835", {"start": v(-5.59, 640.54) * mm, "end": v(-6.97, 641.33) * mm});
            skLineSegment(sketch, "E836", {"start": v(-6.97, 641.33) * mm, "end": v(-8.4, 642.01) * mm});
            skLineSegment(sketch, "E837", {"start": v(-8.4, 642.01) * mm, "end": v(-9.9, 642.58) * mm});
            skLineSegment(sketch, "E838", {"start": v(-9.9, 642.58) * mm, "end": v(-11.45, 643.03) * mm});
            skLineSegment(sketch, "E839", {"start": v(-11.45, 643.03) * mm, "end": v(-13.04, 643.37) * mm});
            skLineSegment(sketch, "E840", {"start": v(-13.04, 643.37) * mm, "end": v(-14.65, 643.59) * mm});
            skLineSegment(sketch, "E841", {"start": v(-14.65, 643.59) * mm, "end": v(-16.3, 643.7) * mm});
            skLineSegment(sketch, "E842", {"start": v(-16.3, 643.7) * mm, "end": v(-17.96, 643.67) * mm});
            skLineSegment(sketch, "E843", {"start": v(-17.96, 643.67) * mm, "end": v(-19.63, 643.54) * mm});
            skLineSegment(sketch, "E844", {"start": v(-19.63, 643.54) * mm, "end": v(-21.3, 643.28) * mm});
            skLineSegment(sketch, "E845", {"start": v(-21.3, 643.28) * mm, "end": v(-22.98, 642.9) * mm});
            skLineSegment(sketch, "E846", {"start": v(-22.98, 642.9) * mm, "end": v(-24.64, 642.39) * mm});
            skLineSegment(sketch, "E847", {"start": v(-24.64, 642.39) * mm, "end": v(-26.28, 641.75) * mm});
            skLineSegment(sketch, "E848", {"start": v(-26.28, 641.75) * mm, "end": v(-27.78, 641) * mm});
            skLineSegment(sketch, "E849", {"start": v(-27.78, 641) * mm, "end": v(-29.12, 640.1) * mm});
            skLineSegment(sketch, "E850", {"start": v(-29.12, 640.1) * mm, "end": v(-30.32, 639.05) * mm});
            skLineSegment(sketch, "E851", {"start": v(-30.32, 639.05) * mm, "end": v(-31.39, 637.88) * mm});
            skLineSegment(sketch, "E852", {"start": v(-31.39, 637.88) * mm, "end": v(-32.33, 636.6) * mm});
            skLineSegment(sketch, "E853", {"start": v(-32.33, 636.6) * mm, "end": v(-33.16, 635.22) * mm});
            skLineSegment(sketch, "E854", {"start": v(-33.16, 635.22) * mm, "end": v(-33.88, 633.74) * mm});
            skLineSegment(sketch, "E855", {"start": v(-33.88, 633.74) * mm, "end": v(-34.5, 632.19) * mm});
            skLineSegment(sketch, "E856", {"start": v(-34.5, 632.19) * mm, "end": v(-35.04, 630.57) * mm});
            skLineSegment(sketch, "E857", {"start": v(-35.04, 630.57) * mm, "end": v(-35.5, 628.9) * mm});
            skLineSegment(sketch, "E858", {"start": v(-35.5, 628.9) * mm, "end": v(-35.88, 627.19) * mm});
            skLineSegment(sketch, "E859", {"start": v(-35.88, 627.19) * mm, "end": v(-36.2, 625.45) * mm});
            skLineSegment(sketch, "E860", {"start": v(-36.2, 625.45) * mm, "end": v(-36.48, 623.69) * mm});
            skLineSegment(sketch, "E861", {"start": v(-36.48, 623.69) * mm, "end": v(-36.71, 621.93) * mm});
            skLineSegment(sketch, "E862", {"start": v(-36.71, 621.93) * mm, "end": v(-36.9, 620.17) * mm});
            skLineSegment(sketch, "E863", {"start": v(-36.9, 620.17) * mm, "end": v(-37.08, 618.44) * mm});
            skLineSegment(sketch, "E864", {"start": v(-37.08, 618.44) * mm, "end": v(-37.23, 616.74) * mm});
            skLineSegment(sketch, "E865", {"start": v(-37.23, 616.74) * mm, "end": v(-37.38, 615.08) * mm});
            skLineSegment(sketch, "E866", {"start": v(-37.38, 615.08) * mm, "end": v(-37.53, 613.49) * mm});
            skLineSegment(sketch, "E867", {"start": v(-37.53, 613.49) * mm, "end": v(-37.69, 611.96) * mm});
            skLineSegment(sketch, "E868", {"start": v(-37.69, 611.96) * mm, "end": v(-37.86, 610.5) * mm});
            skLineSegment(sketch, "E869", {"start": v(-37.86, 610.5) * mm, "end": v(-38.13, 608.8) * mm});
            skLineSegment(sketch, "E870", {"start": v(-38.13, 608.8) * mm, "end": v(-38.45, 607.1) * mm});
            skLineSegment(sketch, "E871", {"start": v(-38.45, 607.1) * mm, "end": v(-38.84, 605.42) * mm});
            skLineSegment(sketch, "E872", {"start": v(-38.84, 605.42) * mm, "end": v(-39.28, 603.75) * mm});
            skLineSegment(sketch, "E873", {"start": v(-39.28, 603.75) * mm, "end": v(-39.78, 602.1) * mm});
            skLineSegment(sketch, "E874", {"start": v(-39.78, 602.1) * mm, "end": v(-40.34, 600.48) * mm});
            skLineSegment(sketch, "E875", {"start": v(-40.34, 600.48) * mm, "end": v(-40.96, 598.87) * mm});
            skLineSegment(sketch, "E876", {"start": v(-40.96, 598.87) * mm, "end": v(-41.63, 597.3) * mm});
            skLineSegment(sketch, "E877", {"start": v(-41.63, 597.3) * mm, "end": v(-42.36, 595.74) * mm});
            skLineSegment(sketch, "E878", {"start": v(-42.36, 595.74) * mm, "end": v(-43.15, 594.22) * mm});
            skLineSegment(sketch, "E879", {"start": v(-43.15, 594.22) * mm, "end": v(-44, 592.74) * mm});
            skLineSegment(sketch, "E880", {"start": v(-44, 592.74) * mm, "end": v(-44.9, 591.3) * mm});
            skLineSegment(sketch, "E881", {"start": v(-44.9, 591.3) * mm, "end": v(-45.85, 589.9) * mm});
            skLineSegment(sketch, "E882", {"start": v(-45.85, 589.9) * mm, "end": v(-46.86, 588.53) * mm});
            skLineSegment(sketch, "E883", {"start": v(-46.86, 588.53) * mm, "end": v(-47.92, 587.22) * mm});
            skLineSegment(sketch, "E884", {"start": v(-47.92, 587.22) * mm, "end": v(-49.03, 585.95) * mm});
            skLineSegment(sketch, "E885", {"start": v(-49.03, 585.95) * mm, "end": v(-50.2, 584.74) * mm});
            skLineSegment(sketch, "E886", {"start": v(-50.2, 584.74) * mm, "end": v(-51.42, 583.58) * mm});
            skLineSegment(sketch, "E887", {"start": v(-51.42, 583.58) * mm, "end": v(-52.69, 582.48) * mm});
            skLineSegment(sketch, "E888", {"start": v(-52.69, 582.48) * mm, "end": v(-54.01, 581.44) * mm});
            skLineSegment(sketch, "E889", {"start": v(-54.01, 581.44) * mm, "end": v(-55.38, 580.46) * mm});
            skLineSegment(sketch, "E890", {"start": v(-55.38, 580.46) * mm, "end": v(-56.8, 579.55) * mm});
            skLineSegment(sketch, "E891", {"start": v(-56.8, 579.55) * mm, "end": v(-58.28, 578.7) * mm});
            skLineSegment(sketch, "E892", {"start": v(-58.28, 578.7) * mm, "end": v(-59.8, 577.94) * mm});
            skLineSegment(sketch, "E893", {"start": v(-59.8, 577.94) * mm, "end": v(-61.37, 577.24) * mm});
            skLineSegment(sketch, "E894", {"start": v(-61.37, 577.24) * mm, "end": v(-62.99, 576.62) * mm});
            skLineSegment(sketch, "E895", {"start": v(-62.99, 576.62) * mm, "end": v(-64.65, 576.08) * mm});
            skLineSegment(sketch, "E896", {"start": v(-64.65, 576.08) * mm, "end": v(-66.36, 575.62) * mm});
            skLineSegment(sketch, "E897", {"start": v(-66.36, 575.62) * mm, "end": v(-68.12, 575.25) * mm});
            skLineSegment(sketch, "E898", {"start": v(-68.12, 575.25) * mm, "end": v(-69.93, 574.97) * mm});
            skLineSegment(sketch, "E899", {"start": v(-69.93, 574.97) * mm, "end": v(-71.25, 574.82) * mm});
            skLineSegment(sketch, "E900", {"start": v(-71.25, 574.82) * mm, "end": v(-72.54, 574.74) * mm});
            skLineSegment(sketch, "E901", {"start": v(-72.54, 574.74) * mm, "end": v(-73.8, 574.71) * mm});
            skLineSegment(sketch, "E902", {"start": v(-73.8, 574.71) * mm, "end": v(-75.03, 574.74) * mm});
            skLineSegment(sketch, "E903", {"start": v(-75.03, 574.74) * mm, "end": v(-76.22, 574.83) * mm});
            skLineSegment(sketch, "E904", {"start": v(-76.22, 574.83) * mm, "end": v(-77.39, 574.96) * mm});
            skLineSegment(sketch, "E905", {"start": v(-77.39, 574.96) * mm, "end": v(-78.52, 575.15) * mm});
            skLineSegment(sketch, "E906", {"start": v(-78.52, 575.15) * mm, "end": v(-79.63, 575.4) * mm});
            skLineSegment(sketch, "E907", {"start": v(-79.63, 575.4) * mm, "end": v(-80.71, 575.68) * mm});
            skLineSegment(sketch, "E908", {"start": v(-80.71, 575.68) * mm, "end": v(-81.76, 576.02) * mm});
            skLineSegment(sketch, "E909", {"start": v(-81.76, 576.02) * mm, "end": v(-82.8, 576.4) * mm});
            skLineSegment(sketch, "E910", {"start": v(-82.8, 576.4) * mm, "end": v(-83.8, 576.83) * mm});
            skLineSegment(sketch, "E911", {"start": v(-83.8, 576.83) * mm, "end": v(-84.77, 577.3) * mm});
            skLineSegment(sketch, "E912", {"start": v(-84.77, 577.3) * mm, "end": v(-85.72, 577.82) * mm});
            skLineSegment(sketch, "E913", {"start": v(-85.72, 577.82) * mm, "end": v(-86.65, 578.37) * mm});
            skLineSegment(sketch, "E914", {"start": v(-86.65, 578.37) * mm, "end": v(-87.55, 578.96) * mm});
            skLineSegment(sketch, "E915", {"start": v(-87.55, 578.96) * mm, "end": v(-88.43, 579.6) * mm});
            skLineSegment(sketch, "E916", {"start": v(-88.43, 579.6) * mm, "end": v(-89.3, 580.26) * mm});
            skLineSegment(sketch, "E917", {"start": v(-89.3, 580.26) * mm, "end": v(-90.14, 580.96) * mm});
            skLineSegment(sketch, "E918", {"start": v(-90.14, 580.96) * mm, "end": v(-90.96, 581.69) * mm});
            skLineSegment(sketch, "E919", {"start": v(-90.96, 581.69) * mm, "end": v(-91.76, 582.45) * mm});
            skLineSegment(sketch, "E920", {"start": v(-91.76, 582.45) * mm, "end": v(-92.54, 583.25) * mm});
            skLineSegment(sketch, "E921", {"start": v(-92.54, 583.25) * mm, "end": v(-93.31, 584.07) * mm});
            skLineSegment(sketch, "E922", {"start": v(-93.31, 584.07) * mm, "end": v(-94.06, 584.92) * mm});
            skLineSegment(sketch, "E923", {"start": v(-94.06, 584.92) * mm, "end": v(-94.8, 585.79) * mm});
            skLineSegment(sketch, "E924", {"start": v(-94.8, 585.79) * mm, "end": v(-95.5, 586.69) * mm});
            skLineSegment(sketch, "E925", {"start": v(-95.5, 586.69) * mm, "end": v(-96.21, 587.6) * mm});
            skLineSegment(sketch, "E926", {"start": v(-96.21, 587.6) * mm, "end": v(-96.9, 588.55) * mm});
            skLineSegment(sketch, "E927", {"start": v(-96.9, 588.55) * mm, "end": v(-97.58, 589.51) * mm});
            skLineSegment(sketch, "E928", {"start": v(-97.58, 589.51) * mm, "end": v(-98.24, 590.5) * mm});
            skLineSegment(sketch, "E929", {"start": v(-98.24, 590.5) * mm, "end": v(-98.9, 591.49) * mm});
            skLineSegment(sketch, "E930", {"start": v(-98.9, 591.49) * mm, "end": v(-99.53, 592.5) * mm});
            skLineSegment(sketch, "E931", {"start": v(-99.53, 592.5) * mm, "end": v(-100.16, 593.52) * mm});
            skLineSegment(sketch, "E932", {"start": v(-100.16, 593.52) * mm, "end": v(-100.78, 594.56) * mm});
            skLineSegment(sketch, "E933", {"start": v(-100.78, 594.56) * mm, "end": v(-101.4, 595.6) * mm});
            skLineSegment(sketch, "E934", {"start": v(-101.4, 595.6) * mm, "end": v(-102, 596.66) * mm});
            skLineSegment(sketch, "E935", {"start": v(-102, 596.66) * mm, "end": v(-102.59, 597.73) * mm});
            skLineSegment(sketch, "E936", {"start": v(-102.59, 597.73) * mm, "end": v(-103.18, 598.8) * mm});
            skLineSegment(sketch, "E937", {"start": v(-103.18, 598.8) * mm, "end": v(-103.76, 599.88) * mm});
            skLineSegment(sketch, "E938", {"start": v(-103.76, 599.88) * mm, "end": v(-104.34, 600.95) * mm});
            skLineSegment(sketch, "E939", {"start": v(-104.34, 600.95) * mm, "end": v(-104.9, 602.04) * mm});
            skLineSegment(sketch, "E940", {"start": v(-104.9, 602.04) * mm, "end": v(-105.48, 603.12) * mm});
            skLineSegment(sketch, "E941", {"start": v(-105.48, 603.12) * mm, "end": v(-106.04, 604.2) * mm});
            skLineSegment(sketch, "E942", {"start": v(-106.04, 604.2) * mm, "end": v(-106.6, 605.27) * mm});
            skLineSegment(sketch, "E943", {"start": v(-106.6, 605.27) * mm, "end": v(-107.17, 606.35) * mm});
            skLineSegment(sketch, "E944", {"start": v(-107.17, 606.35) * mm, "end": v(-107.73, 607.41) * mm});
            skLineSegment(sketch, "E945", {"start": v(-107.73, 607.41) * mm, "end": v(-108.3, 608.48) * mm});
            skLineSegment(sketch, "E946", {"start": v(-108.3, 608.48) * mm, "end": v(-108.85, 609.53) * mm});
            skLineSegment(sketch, "E947", {"start": v(-108.85, 609.53) * mm, "end": v(-109.41, 610.57) * mm});
            skLineSegment(sketch, "E948", {"start": v(-109.41, 610.57) * mm, "end": v(-109.98, 611.6) * mm});
            skLineSegment(sketch, "E949", {"start": v(-109.98, 611.6) * mm, "end": v(-110.55, 612.62) * mm});
            skLineSegment(sketch, "E950", {"start": v(-110.55, 612.62) * mm, "end": v(-111.12, 613.62) * mm});
            skLineSegment(sketch, "E951", {"start": v(-111.12, 613.62) * mm, "end": v(-111.7, 614.6) * mm});
            skLineSegment(sketch, "E952", {"start": v(-111.7, 614.6) * mm, "end": v(-112.27, 615.58) * mm});
            skLineSegment(sketch, "E953", {"start": v(-112.27, 615.58) * mm, "end": v(-112.86, 616.53) * mm});
            skLineSegment(sketch, "E954", {"start": v(-112.86, 616.53) * mm, "end": v(-113.45, 617.46) * mm});
            skLineSegment(sketch, "E955", {"start": v(-113.45, 617.46) * mm, "end": v(-114.05, 618.37) * mm});
            skLineSegment(sketch, "E956", {"start": v(-114.05, 618.37) * mm, "end": v(-114.66, 619.26) * mm});
            skLineSegment(sketch, "E957", {"start": v(-114.66, 619.26) * mm, "end": v(-115.27, 620.12) * mm});
            skLineSegment(sketch, "E958", {"start": v(-115.27, 620.12) * mm, "end": v(-115.9, 620.95) * mm});
            skLineSegment(sketch, "E959", {"start": v(-115.9, 620.95) * mm, "end": v(-116.53, 621.76) * mm});
            skLineSegment(sketch, "E960", {"start": v(-116.53, 621.76) * mm, "end": v(-117.18, 622.54) * mm});
            skLineSegment(sketch, "E961", {"start": v(-117.18, 622.54) * mm, "end": v(-117.84, 623.29) * mm});
            skLineSegment(sketch, "E962", {"start": v(-117.84, 623.29) * mm, "end": v(-118.5, 624) * mm});
            skLineSegment(sketch, "E963", {"start": v(-118.5, 624) * mm, "end": v(-119.19, 624.68) * mm});
            skLineSegment(sketch, "E964", {"start": v(-119.19, 624.68) * mm, "end": v(-119.89, 625.33) * mm});
            skLineSegment(sketch, "E965", {"start": v(-119.89, 625.33) * mm, "end": v(-120.6, 625.94) * mm});
            skLineSegment(sketch, "E966", {"start": v(-120.6, 625.94) * mm, "end": v(-121.32, 626.51) * mm});
            skLineSegment(sketch, "E967", {"start": v(-121.32, 626.51) * mm, "end": v(-122.06, 627.04) * mm});
            skLineSegment(sketch, "E968", {"start": v(-122.06, 627.04) * mm, "end": v(-122.82, 627.54) * mm});
            skLineSegment(sketch, "E969", {"start": v(-122.82, 627.54) * mm, "end": v(-123.6, 627.99) * mm});
            skLineSegment(sketch, "E970", {"start": v(-123.6, 627.99) * mm, "end": v(-124.4, 628.4) * mm});
            skLineSegment(sketch, "E971", {"start": v(-124.4, 628.4) * mm, "end": v(-125.2, 628.75) * mm});
            skLineSegment(sketch, "E972", {"start": v(-125.2, 628.75) * mm, "end": v(-126.04, 629.06) * mm});
            skLineSegment(sketch, "E973", {"start": v(-126.04, 629.06) * mm, "end": v(-126.9, 629.33) * mm});
            skLineSegment(sketch, "E974", {"start": v(-126.9, 629.33) * mm, "end": v(-127.76, 629.54) * mm});
            skLineSegment(sketch, "E975", {"start": v(-127.76, 629.54) * mm, "end": v(-128.66, 629.7) * mm});
            skLineSegment(sketch, "E976", {"start": v(-128.66, 629.7) * mm, "end": v(-129.58, 629.81) * mm});
            skLineSegment(sketch, "E977", {"start": v(-129.58, 629.81) * mm, "end": v(-130.52, 629.87) * mm});
            skLineSegment(sketch, "E978", {"start": v(-130.52, 629.87) * mm, "end": v(-131.48, 629.87) * mm});
            skLineSegment(sketch, "E979", {"start": v(-131.48, 629.87) * mm, "end": v(-132.47, 629.81) * mm});
            skLineSegment(sketch, "E980", {"start": v(-132.47, 629.81) * mm, "end": v(-133.49, 629.7) * mm});
            skLineSegment(sketch, "E981", {"start": v(-133.49, 629.7) * mm, "end": v(-134.53, 629.52) * mm});
            skLineSegment(sketch, "E982", {"start": v(-134.53, 629.52) * mm, "end": v(-135.6, 629.29) * mm});
            skLineSegment(sketch, "E983", {"start": v(-135.6, 629.29) * mm, "end": v(-136.7, 628.98) * mm});
            skLineSegment(sketch, "E984", {"start": v(-136.7, 628.98) * mm, "end": v(-137.81, 628.62) * mm});
            skLineSegment(sketch, "E985", {"start": v(-137.81, 628.62) * mm, "end": v(-138.97, 628.19) * mm});
            skLineSegment(sketch, "E986", {"start": v(-138.97, 628.19) * mm, "end": v(-140.15, 627.69) * mm});
            skLineSegment(sketch, "E987", {"start": v(-140.15, 627.69) * mm, "end": v(-141.36, 627.12) * mm});
            skLineSegment(sketch, "E988", {"start": v(-141.36, 627.12) * mm, "end": v(-142.6, 626.48) * mm});
            skLineSegment(sketch, "E989", {"start": v(-142.6, 626.48) * mm, "end": v(-143.88, 625.77) * mm});
            skLineSegment(sketch, "E990", {"start": v(-143.88, 625.77) * mm, "end": v(-145.28, 624.84) * mm});
            skLineSegment(sketch, "E991", {"start": v(-145.28, 624.84) * mm, "end": v(-146.48, 623.8) * mm});
            skLineSegment(sketch, "E992", {"start": v(-146.48, 623.8) * mm, "end": v(-147.5, 622.63) * mm});
            skLineSegment(sketch, "E993", {"start": v(-147.5, 622.63) * mm, "end": v(-148.37, 621.36) * mm});
            skLineSegment(sketch, "E994", {"start": v(-148.37, 621.36) * mm, "end": v(-149.07, 620) * mm});
            skLineSegment(sketch, "E995", {"start": v(-149.07, 620) * mm, "end": v(-149.63, 618.56) * mm});
            skLineSegment(sketch, "E996", {"start": v(-149.63, 618.56) * mm, "end": v(-150.07, 617.05) * mm});
            skLineSegment(sketch, "E997", {"start": v(-150.07, 617.05) * mm, "end": v(-150.39, 615.48) * mm});
            skLineSegment(sketch, "E998", {"start": v(-150.39, 615.48) * mm, "end": v(-150.6, 613.86) * mm});
            skLineSegment(sketch, "E999", {"start": v(-150.6, 613.86) * mm, "end": v(-150.73, 612.2) * mm});
            skLineSegment(sketch, "E1000", {"start": v(-150.73, 612.2) * mm, "end": v(-150.77, 610.5) * mm});
            skLineSegment(sketch, "E1001", {"start": v(-150.77, 610.5) * mm, "end": v(-150.75, 608.8) * mm});
            skLineSegment(sketch, "E1002", {"start": v(-150.75, 608.8) * mm, "end": v(-150.67, 607.07) * mm});
            skLineSegment(sketch, "E1003", {"start": v(-150.67, 607.07) * mm, "end": v(-150.55, 605.35) * mm});
            skLineSegment(sketch, "E1004", {"start": v(-150.55, 605.35) * mm, "end": v(-150.4, 603.64) * mm});
            skLineSegment(sketch, "E1005", {"start": v(-150.4, 603.64) * mm, "end": v(-150.24, 601.96) * mm});
            skLineSegment(sketch, "E1006", {"start": v(-150.24, 601.96) * mm, "end": v(-150.07, 600.3) * mm});
            skLineSegment(sketch, "E1007", {"start": v(-150.07, 600.3) * mm, "end": v(-149.91, 598.7) * mm});
            skLineSegment(sketch, "E1008", {"start": v(-149.91, 598.7) * mm, "end": v(-149.77, 597.13) * mm});
            skLineSegment(sketch, "E1009", {"start": v(-149.77, 597.13) * mm, "end": v(-149.67, 595.64) * mm});
            skLineSegment(sketch, "E1010", {"start": v(-149.67, 595.64) * mm, "end": v(-149.6, 594.22) * mm});
            skLineSegment(sketch, "E1011", {"start": v(-149.6, 594.22) * mm, "end": v(-149.59, 592.4) * mm});
            skLineSegment(sketch, "E1012", {"start": v(-149.59, 592.4) * mm, "end": v(-149.61, 590.62) * mm});
            skLineSegment(sketch, "E1013", {"start": v(-149.61, 590.62) * mm, "end": v(-149.69, 588.84) * mm});
            skLineSegment(sketch, "E1014", {"start": v(-149.69, 588.84) * mm, "end": v(-149.81, 587.09) * mm});
            skLineSegment(sketch, "E1015", {"start": v(-149.81, 587.09) * mm, "end": v(-149.98, 585.35) * mm});
            skLineSegment(sketch, "E1016", {"start": v(-149.98, 585.35) * mm, "end": v(-150.2, 583.64) * mm});
            skLineSegment(sketch, "E1017", {"start": v(-150.2, 583.64) * mm, "end": v(-150.48, 581.95) * mm});
            skLineSegment(sketch, "E1018", {"start": v(-150.48, 581.95) * mm, "end": v(-150.8, 580.28) * mm});
            skLineSegment(sketch, "E1019", {"start": v(-150.8, 580.28) * mm, "end": v(-151.18, 578.64) * mm});
            skLineSegment(sketch, "E1020", {"start": v(-151.18, 578.64) * mm, "end": v(-151.62, 577.03) * mm});
            skLineSegment(sketch, "E1021", {"start": v(-151.62, 577.03) * mm, "end": v(-152.1, 575.45) * mm});
            skLineSegment(sketch, "E1022", {"start": v(-152.1, 575.45) * mm, "end": v(-152.65, 573.9) * mm});
            skLineSegment(sketch, "E1023", {"start": v(-152.65, 573.9) * mm, "end": v(-153.25, 572.38) * mm});
            skLineSegment(sketch, "E1024", {"start": v(-153.25, 572.38) * mm, "end": v(-153.91, 570.9) * mm});
            skLineSegment(sketch, "E1025", {"start": v(-153.91, 570.9) * mm, "end": v(-154.63, 569.46) * mm});
            skLineSegment(sketch, "E1026", {"start": v(-154.63, 569.46) * mm, "end": v(-155.4, 568.05) * mm});
            skLineSegment(sketch, "E1027", {"start": v(-155.4, 568.05) * mm, "end": v(-156.25, 566.68) * mm});
            skLineSegment(sketch, "E1028", {"start": v(-156.25, 566.68) * mm, "end": v(-157.15, 565.36) * mm});
            skLineSegment(sketch, "E1029", {"start": v(-157.15, 565.36) * mm, "end": v(-158.11, 564.08) * mm});
            skLineSegment(sketch, "E1030", {"start": v(-158.11, 564.08) * mm, "end": v(-159.14, 562.85) * mm});
            skLineSegment(sketch, "E1031", {"start": v(-159.14, 562.85) * mm, "end": v(-160.23, 561.66) * mm});
            skLineSegment(sketch, "E1032", {"start": v(-160.23, 561.66) * mm, "end": v(-161.38, 560.52) * mm});
            skLineSegment(sketch, "E1033", {"start": v(-161.38, 560.52) * mm, "end": v(-162.6, 559.44) * mm});
            skLineSegment(sketch, "E1034", {"start": v(-162.6, 559.44) * mm, "end": v(-163.9, 558.4) * mm});
            skLineSegment(sketch, "E1035", {"start": v(-163.9, 558.4) * mm, "end": v(-165.25, 557.42) * mm});
            skLineSegment(sketch, "E1036", {"start": v(-165.25, 557.42) * mm, "end": v(-166.68, 556.5) * mm});
            skLineSegment(sketch, "E1037", {"start": v(-166.68, 556.5) * mm, "end": v(-168.17, 555.63) * mm});
            skLineSegment(sketch, "E1038", {"start": v(-168.17, 555.63) * mm, "end": v(-169.74, 554.82) * mm});
            skLineSegment(sketch, "E1039", {"start": v(-169.74, 554.82) * mm, "end": v(-171.38, 554.07) * mm});
            skLineSegment(sketch, "E1040", {"start": v(-171.38, 554.07) * mm, "end": v(-173.1, 553.38) * mm});
            skLineSegment(sketch, "E1041", {"start": v(-173.1, 553.38) * mm, "end": v(-174.88, 552.76) * mm});
            skLineSegment(sketch, "E1042", {"start": v(-174.88, 552.76) * mm, "end": v(-176.74, 552.2) * mm});
            skLineSegment(sketch, "E1043", {"start": v(-176.74, 552.2) * mm, "end": v(-178.14, 551.85) * mm});
            skLineSegment(sketch, "E1044", {"start": v(-178.14, 551.85) * mm, "end": v(-179.51, 551.56) * mm});
            skLineSegment(sketch, "E1045", {"start": v(-179.51, 551.56) * mm, "end": v(-180.86, 551.35) * mm});
            skLineSegment(sketch, "E1046", {"start": v(-180.86, 551.35) * mm, "end": v(-182.17, 551.2) * mm});
            skLineSegment(sketch, "E1047", {"start": v(-182.17, 551.2) * mm, "end": v(-183.45, 551.11) * mm});
            skLineSegment(sketch, "E1048", {"start": v(-183.45, 551.11) * mm, "end": v(-184.7, 551.09) * mm});
            skLineSegment(sketch, "E1049", {"start": v(-184.7, 551.09) * mm, "end": v(-185.92, 551.13) * mm});
            skLineSegment(sketch, "E1050", {"start": v(-185.92, 551.13) * mm, "end": v(-187.12, 551.23) * mm});
            skLineSegment(sketch, "E1051", {"start": v(-187.12, 551.23) * mm, "end": v(-188.3, 551.38) * mm});
            skLineSegment(sketch, "E1052", {"start": v(-188.3, 551.38) * mm, "end": v(-189.43, 551.6) * mm});
            skLineSegment(sketch, "E1053", {"start": v(-189.43, 551.6) * mm, "end": v(-190.55, 551.86) * mm});
            skLineSegment(sketch, "E1054", {"start": v(-190.55, 551.86) * mm, "end": v(-191.65, 552.17) * mm});
            skLineSegment(sketch, "E1055", {"start": v(-191.65, 552.17) * mm, "end": v(-192.72, 552.54) * mm});
            skLineSegment(sketch, "E1056", {"start": v(-192.72, 552.54) * mm, "end": v(-193.77, 552.95) * mm});
            skLineSegment(sketch, "E1057", {"start": v(-193.77, 552.95) * mm, "end": v(-194.8, 553.41) * mm});
            skLineSegment(sketch, "E1058", {"start": v(-194.8, 553.41) * mm, "end": v(-195.8, 553.92) * mm});
            skLineSegment(sketch, "E1059", {"start": v(-195.8, 553.92) * mm, "end": v(-196.78, 554.46) * mm});
            skLineSegment(sketch, "E1060", {"start": v(-196.78, 554.46) * mm, "end": v(-197.75, 555.05) * mm});
            skLineSegment(sketch, "E1061", {"start": v(-197.75, 555.05) * mm, "end": v(-198.7, 555.67) * mm});
            skLineSegment(sketch, "E1062", {"start": v(-198.7, 555.67) * mm, "end": v(-199.62, 556.34) * mm});
            skLineSegment(sketch, "E1063", {"start": v(-199.62, 556.34) * mm, "end": v(-200.53, 557.03) * mm});
            skLineSegment(sketch, "E1064", {"start": v(-200.53, 557.03) * mm, "end": v(-201.42, 557.76) * mm});
            skLineSegment(sketch, "E1065", {"start": v(-201.42, 557.76) * mm, "end": v(-202.3, 558.52) * mm});
            skLineSegment(sketch, "E1066", {"start": v(-202.3, 558.52) * mm, "end": v(-203.16, 559.31) * mm});
            skLineSegment(sketch, "E1067", {"start": v(-203.16, 559.31) * mm, "end": v(-204.01, 560.13) * mm});
            skLineSegment(sketch, "E1068", {"start": v(-204.01, 560.13) * mm, "end": v(-204.85, 560.97) * mm});
            skLineSegment(sketch, "E1069", {"start": v(-204.85, 560.97) * mm, "end": v(-205.67, 561.84) * mm});
            skLineSegment(sketch, "E1070", {"start": v(-205.67, 561.84) * mm, "end": v(-206.48, 562.73) * mm});
            skLineSegment(sketch, "E1071", {"start": v(-206.48, 562.73) * mm, "end": v(-207.28, 563.64) * mm});
            skLineSegment(sketch, "E1072", {"start": v(-207.28, 563.64) * mm, "end": v(-208.07, 564.56) * mm});
            skLineSegment(sketch, "E1073", {"start": v(-208.07, 564.56) * mm, "end": v(-208.85, 565.5) * mm});
            skLineSegment(sketch, "E1074", {"start": v(-208.85, 565.5) * mm, "end": v(-209.62, 566.46) * mm});
            skLineSegment(sketch, "E1075", {"start": v(-209.62, 566.46) * mm, "end": v(-210.38, 567.43) * mm});
            skLineSegment(sketch, "E1076", {"start": v(-210.38, 567.43) * mm, "end": v(-211.14, 568.4) * mm});
            skLineSegment(sketch, "E1077", {"start": v(-211.14, 568.4) * mm, "end": v(-211.89, 569.4) * mm});
            skLineSegment(sketch, "E1078", {"start": v(-211.89, 569.4) * mm, "end": v(-212.63, 570.4) * mm});
            skLineSegment(sketch, "E1079", {"start": v(-212.63, 570.4) * mm, "end": v(-213.37, 571.4) * mm});
            skLineSegment(sketch, "E1080", {"start": v(-213.37, 571.4) * mm, "end": v(-214.1, 572.4) * mm});
            skLineSegment(sketch, "E1081", {"start": v(-214.1, 572.4) * mm, "end": v(-214.83, 573.4) * mm});
            skLineSegment(sketch, "E1082", {"start": v(-214.83, 573.4) * mm, "end": v(-215.56, 574.4) * mm});
            skLineSegment(sketch, "E1083", {"start": v(-215.56, 574.4) * mm, "end": v(-216.28, 575.4) * mm});
            skLineSegment(sketch, "E1084", {"start": v(-216.28, 575.4) * mm, "end": v(-217, 576.4) * mm});
            skLineSegment(sketch, "E1085", {"start": v(-217, 576.4) * mm, "end": v(-217.73, 577.38) * mm});
            skLineSegment(sketch, "E1086", {"start": v(-217.73, 577.38) * mm, "end": v(-218.46, 578.36) * mm});
            skLineSegment(sketch, "E1087", {"start": v(-218.46, 578.36) * mm, "end": v(-219.19, 579.33) * mm});
            skLineSegment(sketch, "E1088", {"start": v(-219.19, 579.33) * mm, "end": v(-219.91, 580.3) * mm});
            skLineSegment(sketch, "E1089", {"start": v(-219.91, 580.3) * mm, "end": v(-220.65, 581.24) * mm});
            skLineSegment(sketch, "E1090", {"start": v(-220.65, 581.24) * mm, "end": v(-221.38, 582.17) * mm});
            skLineSegment(sketch, "E1091", {"start": v(-221.38, 582.17) * mm, "end": v(-222.12, 583.08) * mm});
            skLineSegment(sketch, "E1092", {"start": v(-222.12, 583.08) * mm, "end": v(-222.86, 583.97) * mm});
            skLineSegment(sketch, "E1093", {"start": v(-222.86, 583.97) * mm, "end": v(-223.62, 584.84) * mm});
            skLineSegment(sketch, "E1094", {"start": v(-223.62, 584.84) * mm, "end": v(-224.37, 585.69) * mm});
            skLineSegment(sketch, "E1095", {"start": v(-224.37, 585.69) * mm, "end": v(-225.14, 586.51) * mm});
            skLineSegment(sketch, "E1096", {"start": v(-225.14, 586.51) * mm, "end": v(-225.9, 587.3) * mm});
            skLineSegment(sketch, "E1097", {"start": v(-225.9, 587.3) * mm, "end": v(-226.7, 588.07) * mm});
            skLineSegment(sketch, "E1098", {"start": v(-226.7, 588.07) * mm, "end": v(-227.48, 588.8) * mm});
            skLineSegment(sketch, "E1099", {"start": v(-227.48, 588.8) * mm, "end": v(-228.29, 589.51) * mm});
            skLineSegment(sketch, "E1100", {"start": v(-228.29, 589.51) * mm, "end": v(-229.1, 590.18) * mm});
            skLineSegment(sketch, "E1101", {"start": v(-229.1, 590.18) * mm, "end": v(-229.93, 590.81) * mm});
            skLineSegment(sketch, "E1102", {"start": v(-229.93, 590.81) * mm, "end": v(-230.76, 591.4) * mm});
            skLineSegment(sketch, "E1103", {"start": v(-230.76, 591.4) * mm, "end": v(-231.62, 591.96) * mm});
            skLineSegment(sketch, "E1104", {"start": v(-231.62, 591.96) * mm, "end": v(-232.48, 592.47) * mm});
            skLineSegment(sketch, "E1105", {"start": v(-232.48, 592.47) * mm, "end": v(-233.37, 592.94) * mm});
            skLineSegment(sketch, "E1106", {"start": v(-233.37, 592.94) * mm, "end": v(-234.26, 593.36) * mm});
            skLineSegment(sketch, "E1107", {"start": v(-234.26, 593.36) * mm, "end": v(-235.18, 593.73) * mm});
            skLineSegment(sketch, "E1108", {"start": v(-235.18, 593.73) * mm, "end": v(-236.11, 594.06) * mm});
            skLineSegment(sketch, "E1109", {"start": v(-236.11, 594.06) * mm, "end": v(-237.06, 594.33) * mm});
            skLineSegment(sketch, "E1110", {"start": v(-237.06, 594.33) * mm, "end": v(-238.03, 594.55) * mm});
            skLineSegment(sketch, "E1111", {"start": v(-238.03, 594.55) * mm, "end": v(-239.02, 594.72) * mm});
            skLineSegment(sketch, "E1112", {"start": v(-239.02, 594.72) * mm, "end": v(-240.03, 594.83) * mm});
            skLineSegment(sketch, "E1113", {"start": v(-240.03, 594.83) * mm, "end": v(-241.06, 594.88) * mm});
            skLineSegment(sketch, "E1114", {"start": v(-241.06, 594.88) * mm, "end": v(-242.12, 594.86) * mm});
            skLineSegment(sketch, "E1115", {"start": v(-242.12, 594.86) * mm, "end": v(-243.2, 594.8) * mm});
            skLineSegment(sketch, "E1116", {"start": v(-243.2, 594.8) * mm, "end": v(-244.3, 594.65) * mm});
            skLineSegment(sketch, "E1117", {"start": v(-244.3, 594.65) * mm, "end": v(-245.42, 594.45) * mm});
            skLineSegment(sketch, "E1118", {"start": v(-245.42, 594.45) * mm, "end": v(-246.57, 594.17) * mm});
            skLineSegment(sketch, "E1119", {"start": v(-246.57, 594.17) * mm, "end": v(-247.75, 593.83) * mm});
            skLineSegment(sketch, "E1120", {"start": v(-247.75, 593.83) * mm, "end": v(-248.96, 593.42) * mm});
            skLineSegment(sketch, "E1121", {"start": v(-248.96, 593.42) * mm, "end": v(-250.19, 592.93) * mm});
            skLineSegment(sketch, "E1122", {"start": v(-250.19, 592.93) * mm, "end": v(-251.45, 592.36) * mm});
            skLineSegment(sketch, "E1123", {"start": v(-251.45, 592.36) * mm, "end": v(-252.74, 591.72) * mm});
            skLineSegment(sketch, "E1124", {"start": v(-252.74, 591.72) * mm, "end": v(-254.33, 590.8) * mm});
            skLineSegment(sketch, "E1125", {"start": v(-254.33, 590.8) * mm, "end": v(-255.73, 589.8) * mm});
            skLineSegment(sketch, "E1126", {"start": v(-255.73, 589.8) * mm, "end": v(-256.96, 588.72) * mm});
            skLineSegment(sketch, "E1127", {"start": v(-256.96, 588.72) * mm, "end": v(-258.01, 587.57) * mm});
            skLineSegment(sketch, "E1128", {"start": v(-258.01, 587.57) * mm, "end": v(-258.9, 586.36) * mm});
            skLineSegment(sketch, "E1129", {"start": v(-258.9, 586.36) * mm, "end": v(-259.64, 585.09) * mm});
            skLineSegment(sketch, "E1130", {"start": v(-259.64, 585.09) * mm, "end": v(-260.24, 583.76) * mm});
            skLineSegment(sketch, "E1131", {"start": v(-260.24, 583.76) * mm, "end": v(-260.7, 582.39) * mm});
            skLineSegment(sketch, "E1132", {"start": v(-260.7, 582.39) * mm, "end": v(-261.03, 580.97) * mm});
            skLineSegment(sketch, "E1133", {"start": v(-261.03, 580.97) * mm, "end": v(-261.25, 579.5) * mm});
            skLineSegment(sketch, "E1134", {"start": v(-261.25, 579.5) * mm, "end": v(-261.37, 578) * mm});
            skLineSegment(sketch, "E1135", {"start": v(-261.37, 578) * mm, "end": v(-261.38, 576.48) * mm});
            skLineSegment(sketch, "E1136", {"start": v(-261.38, 576.48) * mm, "end": v(-261.3, 574.92) * mm});
            skLineSegment(sketch, "E1137", {"start": v(-261.3, 574.92) * mm, "end": v(-261.15, 573.34) * mm});
            skLineSegment(sketch, "E1138", {"start": v(-261.15, 573.34) * mm, "end": v(-260.93, 571.75) * mm});
            skLineSegment(sketch, "E1139", {"start": v(-260.93, 571.75) * mm, "end": v(-260.64, 570.14) * mm});
            skLineSegment(sketch, "E1140", {"start": v(-260.64, 570.14) * mm, "end": v(-260.3, 568.52) * mm});
            skLineSegment(sketch, "E1141", {"start": v(-260.3, 568.52) * mm, "end": v(-259.92, 566.9) * mm});
            skLineSegment(sketch, "E1142", {"start": v(-259.92, 566.9) * mm, "end": v(-259.5, 565.28) * mm});
            skLineSegment(sketch, "E1143", {"start": v(-259.5, 565.28) * mm, "end": v(-259.07, 563.67) * mm});
            skLineSegment(sketch, "E1144", {"start": v(-259.07, 563.67) * mm, "end": v(-258.61, 562.07) * mm});
            skLineSegment(sketch, "E1145", {"start": v(-258.61, 562.07) * mm, "end": v(-258.15, 560.48) * mm});
            skLineSegment(sketch, "E1146", {"start": v(-258.15, 560.48) * mm, "end": v(-257.7, 558.92) * mm});
            skLineSegment(sketch, "E1147", {"start": v(-257.7, 558.92) * mm, "end": v(-257.24, 557.38) * mm});
            skLineSegment(sketch, "E1148", {"start": v(-257.24, 557.38) * mm, "end": v(-256.82, 555.87) * mm});
            skLineSegment(sketch, "E1149", {"start": v(-256.82, 555.87) * mm, "end": v(-256.42, 554.39) * mm});
            skLineSegment(sketch, "E1150", {"start": v(-256.42, 554.39) * mm, "end": v(-256, 552.67) * mm});
            skLineSegment(sketch, "E1151", {"start": v(-256, 552.67) * mm, "end": v(-255.66, 550.94) * mm});
            skLineSegment(sketch, "E1152", {"start": v(-255.66, 550.94) * mm, "end": v(-255.38, 549.2) * mm});
            skLineSegment(sketch, "E1153", {"start": v(-255.38, 549.2) * mm, "end": v(-255.17, 547.48) * mm});
            skLineSegment(sketch, "E1154", {"start": v(-255.17, 547.48) * mm, "end": v(-255.03, 545.75) * mm});
            skLineSegment(sketch, "E1155", {"start": v(-255.03, 545.75) * mm, "end": v(-254.96, 544.02) * mm});
            skLineSegment(sketch, "E1156", {"start": v(-254.96, 544.02) * mm, "end": v(-254.95, 542.3) * mm});
            skLineSegment(sketch, "E1157", {"start": v(-254.95, 542.3) * mm, "end": v(-255.02, 540.6) * mm});
            skLineSegment(sketch, "E1158", {"start": v(-255.02, 540.6) * mm, "end": v(-255.15, 538.9) * mm});
            skLineSegment(sketch, "E1159", {"start": v(-255.15, 538.9) * mm, "end": v(-255.36, 537.23) * mm});
            skLineSegment(sketch, "E1160", {"start": v(-255.36, 537.23) * mm, "end": v(-255.63, 535.57) * mm});
            skLineSegment(sketch, "E1161", {"start": v(-255.63, 535.57) * mm, "end": v(-255.98, 533.93) * mm});
            skLineSegment(sketch, "E1162", {"start": v(-255.98, 533.93) * mm, "end": v(-256.4, 532.3) * mm});
            skLineSegment(sketch, "E1163", {"start": v(-256.4, 532.3) * mm, "end": v(-256.88, 530.72) * mm});
            skLineSegment(sketch, "E1164", {"start": v(-256.88, 530.72) * mm, "end": v(-257.44, 529.15) * mm});
            skLineSegment(sketch, "E1165", {"start": v(-257.44, 529.15) * mm, "end": v(-258.07, 527.62) * mm});
            skLineSegment(sketch, "E1166", {"start": v(-258.07, 527.62) * mm, "end": v(-258.77, 526.12) * mm});
            skLineSegment(sketch, "E1167", {"start": v(-258.77, 526.12) * mm, "end": v(-259.54, 524.65) * mm});
            skLineSegment(sketch, "E1168", {"start": v(-259.54, 524.65) * mm, "end": v(-260.38, 523.23) * mm});
            skLineSegment(sketch, "E1169", {"start": v(-260.38, 523.23) * mm, "end": v(-261.3, 521.84) * mm});
            skLineSegment(sketch, "E1170", {"start": v(-261.3, 521.84) * mm, "end": v(-262.29, 520.5) * mm});
            skLineSegment(sketch, "E1171", {"start": v(-262.29, 520.5) * mm, "end": v(-263.35, 519.2) * mm});
            skLineSegment(sketch, "E1172", {"start": v(-263.35, 519.2) * mm, "end": v(-264.48, 517.95) * mm});
            skLineSegment(sketch, "E1173", {"start": v(-264.48, 517.95) * mm, "end": v(-265.7, 516.76) * mm});
            skLineSegment(sketch, "E1174", {"start": v(-265.7, 516.76) * mm, "end": v(-266.97, 515.61) * mm});
            skLineSegment(sketch, "E1175", {"start": v(-266.97, 515.61) * mm, "end": v(-268.33, 514.53) * mm});
            skLineSegment(sketch, "E1176", {"start": v(-268.33, 514.53) * mm, "end": v(-269.76, 513.5) * mm});
            skLineSegment(sketch, "E1177", {"start": v(-269.76, 513.5) * mm, "end": v(-271.26, 512.53) * mm});
            skLineSegment(sketch, "E1178", {"start": v(-271.26, 512.53) * mm, "end": v(-272.84, 511.63) * mm});
            skLineSegment(sketch, "E1179", {"start": v(-272.84, 511.63) * mm, "end": v(-274.5, 510.8) * mm});
            skLineSegment(sketch, "E1180", {"start": v(-274.5, 510.8) * mm, "end": v(-275.9, 510.17) * mm});
            skLineSegment(sketch, "E1181", {"start": v(-275.9, 510.17) * mm, "end": v(-277.26, 509.62) * mm});
            skLineSegment(sketch, "E1182", {"start": v(-277.26, 509.62) * mm, "end": v(-278.62, 509.15) * mm});
            skLineSegment(sketch, "E1183", {"start": v(-278.62, 509.15) * mm, "end": v(-279.95, 508.75) * mm});
            skLineSegment(sketch, "E1184", {"start": v(-279.95, 508.75) * mm, "end": v(-281.26, 508.42) * mm});
            skLineSegment(sketch, "E1185", {"start": v(-281.26, 508.42) * mm, "end": v(-282.54, 508.16) * mm});
            skLineSegment(sketch, "E1186", {"start": v(-282.54, 508.16) * mm, "end": v(-283.81, 507.98) * mm});
            skLineSegment(sketch, "E1187", {"start": v(-283.81, 507.98) * mm, "end": v(-285.06, 507.85) * mm});
            skLineSegment(sketch, "E1188", {"start": v(-285.06, 507.85) * mm, "end": v(-286.3, 507.8) * mm});
            skLineSegment(sketch, "E1189", {"start": v(-286.3, 507.8) * mm, "end": v(-287.5, 507.8) * mm});
            skLineSegment(sketch, "E1190", {"start": v(-287.5, 507.8) * mm, "end": v(-288.7, 507.86) * mm});
            skLineSegment(sketch, "E1191", {"start": v(-288.7, 507.86) * mm, "end": v(-289.87, 507.97) * mm});
            skLineSegment(sketch, "E1192", {"start": v(-289.87, 507.97) * mm, "end": v(-291.03, 508.15) * mm});
            skLineSegment(sketch, "E1193", {"start": v(-291.03, 508.15) * mm, "end": v(-292.18, 508.37) * mm});
            skLineSegment(sketch, "E1194", {"start": v(-292.18, 508.37) * mm, "end": v(-293.3, 508.65) * mm});
            skLineSegment(sketch, "E1195", {"start": v(-293.3, 508.65) * mm, "end": v(-294.42, 508.98) * mm});
            skLineSegment(sketch, "E1196", {"start": v(-294.42, 508.98) * mm, "end": v(-295.52, 509.35) * mm});
            skLineSegment(sketch, "E1197", {"start": v(-295.52, 509.35) * mm, "end": v(-296.6, 509.77) * mm});
            skLineSegment(sketch, "E1198", {"start": v(-296.6, 509.77) * mm, "end": v(-297.67, 510.23) * mm});
            skLineSegment(sketch, "E1199", {"start": v(-297.67, 510.23) * mm, "end": v(-298.73, 510.73) * mm});
            skLineSegment(sketch, "E1200", {"start": v(-298.73, 510.73) * mm, "end": v(-299.77, 511.27) * mm});
            skLineSegment(sketch, "E1201", {"start": v(-299.77, 511.27) * mm, "end": v(-300.8, 511.84) * mm});
            skLineSegment(sketch, "E1202", {"start": v(-300.8, 511.84) * mm, "end": v(-301.82, 512.45) * mm});
            skLineSegment(sketch, "E1203", {"start": v(-301.82, 512.45) * mm, "end": v(-302.83, 513.1) * mm});
            skLineSegment(sketch, "E1204", {"start": v(-302.83, 513.1) * mm, "end": v(-303.83, 513.76) * mm});
            skLineSegment(sketch, "E1205", {"start": v(-303.83, 513.76) * mm, "end": v(-304.82, 514.46) * mm});
            skLineSegment(sketch, "E1206", {"start": v(-304.82, 514.46) * mm, "end": v(-305.8, 515.18) * mm});
            skLineSegment(sketch, "E1207", {"start": v(-305.8, 515.18) * mm, "end": v(-306.77, 515.93) * mm});
            skLineSegment(sketch, "E1208", {"start": v(-306.77, 515.93) * mm, "end": v(-307.73, 516.7) * mm});
            skLineSegment(sketch, "E1209", {"start": v(-307.73, 516.7) * mm, "end": v(-308.68, 517.48) * mm});
            skLineSegment(sketch, "E1210", {"start": v(-308.68, 517.48) * mm, "end": v(-309.63, 518.29) * mm});
            skLineSegment(sketch, "E1211", {"start": v(-309.63, 518.29) * mm, "end": v(-310.57, 519.1) * mm});
            skLineSegment(sketch, "E1212", {"start": v(-310.57, 519.1) * mm, "end": v(-311.5, 519.94) * mm});
            skLineSegment(sketch, "E1213", {"start": v(-311.5, 519.94) * mm, "end": v(-312.43, 520.78) * mm});
            skLineSegment(sketch, "E1214", {"start": v(-312.43, 520.78) * mm, "end": v(-313.35, 521.63) * mm});
            skLineSegment(sketch, "E1215", {"start": v(-313.35, 521.63) * mm, "end": v(-314.26, 522.49) * mm});
            skLineSegment(sketch, "E1216", {"start": v(-314.26, 522.49) * mm, "end": v(-315.18, 523.35) * mm});
            skLineSegment(sketch, "E1217", {"start": v(-315.18, 523.35) * mm, "end": v(-316.09, 524.21) * mm});
            skLineSegment(sketch, "E1218", {"start": v(-316.09, 524.21) * mm, "end": v(-317, 525.08) * mm});
            skLineSegment(sketch, "E1219", {"start": v(-317, 525.08) * mm, "end": v(-317.9, 525.94) * mm});
            skLineSegment(sketch, "E1220", {"start": v(-317.9, 525.94) * mm, "end": v(-318.8, 526.8) * mm});
            skLineSegment(sketch, "E1221", {"start": v(-318.8, 526.8) * mm, "end": v(-319.7, 527.65) * mm});
            skLineSegment(sketch, "E1222", {"start": v(-319.7, 527.65) * mm, "end": v(-320.6, 528.5) * mm});
            skLineSegment(sketch, "E1223", {"start": v(-320.6, 528.5) * mm, "end": v(-321.49, 529.33) * mm});
            skLineSegment(sketch, "E1224", {"start": v(-321.49, 529.33) * mm, "end": v(-322.38, 530.15) * mm});
            skLineSegment(sketch, "E1225", {"start": v(-322.38, 530.15) * mm, "end": v(-323.28, 530.95) * mm});
            skLineSegment(sketch, "E1226", {"start": v(-323.28, 530.95) * mm, "end": v(-324.18, 531.74) * mm});
            skLineSegment(sketch, "E1227", {"start": v(-324.18, 531.74) * mm, "end": v(-325.08, 532.5) * mm});
            skLineSegment(sketch, "E1228", {"start": v(-325.08, 532.5) * mm, "end": v(-325.98, 533.26) * mm});
            skLineSegment(sketch, "E1229", {"start": v(-325.98, 533.26) * mm, "end": v(-326.88, 533.98) * mm});
            skLineSegment(sketch, "E1230", {"start": v(-326.88, 533.98) * mm, "end": v(-327.8, 534.68) * mm});
            skLineSegment(sketch, "E1231", {"start": v(-327.8, 534.68) * mm, "end": v(-328.7, 535.36) * mm});
            skLineSegment(sketch, "E1232", {"start": v(-328.7, 535.36) * mm, "end": v(-329.62, 536) * mm});
            skLineSegment(sketch, "E1233", {"start": v(-329.62, 536) * mm, "end": v(-330.54, 536.61) * mm});
            skLineSegment(sketch, "E1234", {"start": v(-330.54, 536.61) * mm, "end": v(-331.46, 537.19) * mm});
            skLineSegment(sketch, "E1235", {"start": v(-331.46, 537.19) * mm, "end": v(-332.4, 537.73) * mm});
            skLineSegment(sketch, "E1236", {"start": v(-332.4, 537.73) * mm, "end": v(-333.33, 538.24) * mm});
            skLineSegment(sketch, "E1237", {"start": v(-333.33, 538.24) * mm, "end": v(-334.27, 538.7) * mm});
            skLineSegment(sketch, "E1238", {"start": v(-334.27, 538.7) * mm, "end": v(-335.22, 539.12) * mm});
            skLineSegment(sketch, "E1239", {"start": v(-335.22, 539.12) * mm, "end": v(-336.18, 539.5) * mm});
            skLineSegment(sketch, "E1240", {"start": v(-336.18, 539.5) * mm, "end": v(-337.14, 539.83) * mm});
            skLineSegment(sketch, "E1241", {"start": v(-337.14, 539.83) * mm, "end": v(-338.12, 540.11) * mm});
            skLineSegment(sketch, "E1242", {"start": v(-338.12, 540.11) * mm, "end": v(-339.1, 540.34) * mm});
            skLineSegment(sketch, "E1243", {"start": v(-339.1, 540.34) * mm, "end": v(-340.1, 540.52) * mm});
            skLineSegment(sketch, "E1244", {"start": v(-340.1, 540.52) * mm, "end": v(-341.1, 540.64) * mm});
            skLineSegment(sketch, "E1245", {"start": v(-341.1, 540.64) * mm, "end": v(-342.11, 540.71) * mm});
            skLineSegment(sketch, "E1246", {"start": v(-342.11, 540.71) * mm, "end": v(-343.14, 540.72) * mm});
            skLineSegment(sketch, "E1247", {"start": v(-343.14, 540.72) * mm, "end": v(-344.18, 540.67) * mm});
            skLineSegment(sketch, "E1248", {"start": v(-344.18, 540.67) * mm, "end": v(-345.23, 540.55) * mm});
            skLineSegment(sketch, "E1249", {"start": v(-345.23, 540.55) * mm, "end": v(-346.3, 540.37) * mm});
            skLineSegment(sketch, "E1250", {"start": v(-346.3, 540.37) * mm, "end": v(-347.37, 540.12) * mm});
            skLineSegment(sketch, "E1251", {"start": v(-347.37, 540.12) * mm, "end": v(-348.46, 539.8) * mm});
            skLineSegment(sketch, "E1252", {"start": v(-348.46, 539.8) * mm, "end": v(-349.56, 539.4) * mm});
            skLineSegment(sketch, "E1253", {"start": v(-349.56, 539.4) * mm, "end": v(-350.68, 538.94) * mm});
            skLineSegment(sketch, "E1254", {"start": v(-350.68, 538.94) * mm, "end": v(-351.82, 538.4) * mm});
            skLineSegment(sketch, "E1255", {"start": v(-351.82, 538.4) * mm, "end": v(-352.97, 537.78) * mm});
            skLineSegment(sketch, "E1256", {"start": v(-352.97, 537.78) * mm, "end": v(-354.14, 537.08) * mm});
            skLineSegment(sketch, "E1257", {"start": v(-354.14, 537.08) * mm, "end": v(-355.68, 536.04) * mm});
            skLineSegment(sketch, "E1258", {"start": v(-355.68, 536.04) * mm, "end": v(-357.05, 534.97) * mm});
            skLineSegment(sketch, "E1259", {"start": v(-357.05, 534.97) * mm, "end": v(-358.27, 533.87) * mm});
            skLineSegment(sketch, "E1260", {"start": v(-358.27, 533.87) * mm, "end": v(-359.35, 532.73) * mm});
            skLineSegment(sketch, "E1261", {"start": v(-359.35, 532.73) * mm, "end": v(-360.28, 531.57) * mm});
            skLineSegment(sketch, "E1262", {"start": v(-360.28, 531.57) * mm, "end": v(-361.07, 530.37) * mm});
            skLineSegment(sketch, "E1263", {"start": v(-361.07, 530.37) * mm, "end": v(-361.74, 529.16) * mm});
            skLineSegment(sketch, "E1264", {"start": v(-361.74, 529.16) * mm, "end": v(-362.28, 527.91) * mm});
            skLineSegment(sketch, "E1265", {"start": v(-362.28, 527.91) * mm, "end": v(-362.7, 526.64) * mm});
            skLineSegment(sketch, "E1266", {"start": v(-362.7, 526.64) * mm, "end": v(-363.01, 525.35) * mm});
            skLineSegment(sketch, "E1267", {"start": v(-363.01, 525.35) * mm, "end": v(-363.22, 524.04) * mm});
            skLineSegment(sketch, "E1268", {"start": v(-363.22, 524.04) * mm, "end": v(-363.32, 522.7) * mm});
            skLineSegment(sketch, "E1269", {"start": v(-363.32, 522.7) * mm, "end": v(-363.33, 521.36) * mm});
            skLineSegment(sketch, "E1270", {"start": v(-363.33, 521.36) * mm, "end": v(-363.25, 520) * mm});
            skLineSegment(sketch, "E1271", {"start": v(-363.25, 520) * mm, "end": v(-363.09, 518.61) * mm});
            skLineSegment(sketch, "E1272", {"start": v(-363.09, 518.61) * mm, "end": v(-362.85, 517.22) * mm});
            skLineSegment(sketch, "E1273", {"start": v(-362.85, 517.22) * mm, "end": v(-362.54, 515.81) * mm});
            skLineSegment(sketch, "E1274", {"start": v(-362.54, 515.81) * mm, "end": v(-362.17, 514.4) * mm});
            skLineSegment(sketch, "E1275", {"start": v(-362.17, 514.4) * mm, "end": v(-361.73, 512.97) * mm});
            skLineSegment(sketch, "E1276", {"start": v(-361.73, 512.97) * mm, "end": v(-361.25, 511.54) * mm});
            skLineSegment(sketch, "E1277", {"start": v(-361.25, 511.54) * mm, "end": v(-360.72, 510.1) * mm});
            skLineSegment(sketch, "E1278", {"start": v(-360.72, 510.1) * mm, "end": v(-360.14, 508.65) * mm});
            skLineSegment(sketch, "E1279", {"start": v(-360.14, 508.65) * mm, "end": v(-359.54, 507.2) * mm});
            skLineSegment(sketch, "E1280", {"start": v(-359.54, 507.2) * mm, "end": v(-358.9, 505.75) * mm});
            skLineSegment(sketch, "E1281", {"start": v(-358.9, 505.75) * mm, "end": v(-358.24, 504.3) * mm});
            skLineSegment(sketch, "E1282", {"start": v(-358.24, 504.3) * mm, "end": v(-357.57, 502.85) * mm});
            skLineSegment(sketch, "E1283", {"start": v(-357.57, 502.85) * mm, "end": v(-356.88, 501.4) * mm});
            skLineSegment(sketch, "E1284", {"start": v(-356.88, 501.4) * mm, "end": v(-356.19, 499.96) * mm});
            skLineSegment(sketch, "E1285", {"start": v(-356.19, 499.96) * mm, "end": v(-355.5, 498.53) * mm});
            skLineSegment(sketch, "E1286", {"start": v(-355.5, 498.53) * mm, "end": v(-354.81, 497.1) * mm});
            skLineSegment(sketch, "E1287", {"start": v(-354.81, 497.1) * mm, "end": v(-354.14, 495.68) * mm});
            skLineSegment(sketch, "E1288", {"start": v(-354.14, 495.68) * mm, "end": v(-353.49, 494.26) * mm});
            skLineSegment(sketch, "E1289", {"start": v(-353.49, 494.26) * mm, "end": v(-352.86, 492.86) * mm});
            skLineSegment(sketch, "E1290", {"start": v(-352.86, 492.86) * mm, "end": v(-352.26, 491.48) * mm});
            skLineSegment(sketch, "E1291", {"start": v(-352.26, 491.48) * mm, "end": v(-351.7, 490.1) * mm});
            skLineSegment(sketch, "E1292", {"start": v(-351.7, 490.1) * mm, "end": v(-351.19, 488.75) * mm});
            skLineSegment(sketch, "E1293", {"start": v(-351.19, 488.75) * mm, "end": v(-350.72, 487.4) * mm});
            skLineSegment(sketch, "E1294", {"start": v(-350.72, 487.4) * mm, "end": v(-350.2, 485.66) * mm});
            skLineSegment(sketch, "E1295", {"start": v(-350.2, 485.66) * mm, "end": v(-349.8, 483.9) * mm});
            skLineSegment(sketch, "E1296", {"start": v(-349.8, 483.9) * mm, "end": v(-349.51, 482.17) * mm});
            skLineSegment(sketch, "E1297", {"start": v(-349.51, 482.17) * mm, "end": v(-349.34, 480.43) * mm});
            skLineSegment(sketch, "E1298", {"start": v(-349.34, 480.43) * mm, "end": v(-349.28, 478.7) * mm});
            skLineSegment(sketch, "E1299", {"start": v(-349.28, 478.7) * mm, "end": v(-349.32, 476.98) * mm});
            skLineSegment(sketch, "E1300", {"start": v(-349.32, 476.98) * mm, "end": v(-349.47, 475.27) * mm});
            skLineSegment(sketch, "E1301", {"start": v(-349.47, 475.27) * mm, "end": v(-349.72, 473.59) * mm});
            skLineSegment(sketch, "E1302", {"start": v(-349.72, 473.59) * mm, "end": v(-350.06, 471.92) * mm});
            skLineSegment(sketch, "E1303", {"start": v(-350.06, 471.92) * mm, "end": v(-350.5, 470.27) * mm});
            skLineSegment(sketch, "E1304", {"start": v(-350.5, 470.27) * mm, "end": v(-351.02, 468.64) * mm});
            skLineSegment(sketch, "E1305", {"start": v(-351.02, 468.64) * mm, "end": v(-351.64, 467.04) * mm});
            skLineSegment(sketch, "E1306", {"start": v(-351.64, 467.04) * mm, "end": v(-352.34, 465.47) * mm});
            skLineSegment(sketch, "E1307", {"start": v(-352.34, 465.47) * mm, "end": v(-353.12, 463.94) * mm});
            skLineSegment(sketch, "E1308", {"start": v(-353.12, 463.94) * mm, "end": v(-353.97, 462.43) * mm});
            skLineSegment(sketch, "E1309", {"start": v(-353.97, 462.43) * mm, "end": v(-354.9, 460.96) * mm});
            skLineSegment(sketch, "E1310", {"start": v(-354.9, 460.96) * mm, "end": v(-355.9, 459.53) * mm});
            skLineSegment(sketch, "E1311", {"start": v(-355.9, 459.53) * mm, "end": v(-356.98, 458.14) * mm});
            skLineSegment(sketch, "E1312", {"start": v(-356.98, 458.14) * mm, "end": v(-358.1, 456.8) * mm});
            skLineSegment(sketch, "E1313", {"start": v(-358.1, 456.8) * mm, "end": v(-359.3, 455.5) * mm});
            skLineSegment(sketch, "E1314", {"start": v(-359.3, 455.5) * mm, "end": v(-360.56, 454.25) * mm});
            skLineSegment(sketch, "E1315", {"start": v(-360.56, 454.25) * mm, "end": v(-361.87, 453.05) * mm});
            skLineSegment(sketch, "E1316", {"start": v(-361.87, 453.05) * mm, "end": v(-363.23, 451.9) * mm});
            skLineSegment(sketch, "E1317", {"start": v(-363.23, 451.9) * mm, "end": v(-364.8, 450.71) * mm});
            skLineSegment(sketch, "E1318", {"start": v(-364.8, 450.71) * mm, "end": v(-366.35, 449.64) * mm});
            skLineSegment(sketch, "E1319", {"start": v(-366.35, 449.64) * mm, "end": v(-367.92, 448.68) * mm});
            skLineSegment(sketch, "E1320", {"start": v(-367.92, 448.68) * mm, "end": v(-369.49, 447.84) * mm});
            skLineSegment(sketch, "E1321", {"start": v(-369.49, 447.84) * mm, "end": v(-371.06, 447.1) * mm});
            skLineSegment(sketch, "E1322", {"start": v(-371.06, 447.1) * mm, "end": v(-372.63, 446.49) * mm});
            skLineSegment(sketch, "E1323", {"start": v(-372.63, 446.49) * mm, "end": v(-374.2, 445.97) * mm});
            skLineSegment(sketch, "E1324", {"start": v(-374.2, 445.97) * mm, "end": v(-375.76, 445.56) * mm});
            skLineSegment(sketch, "E1325", {"start": v(-375.76, 445.56) * mm, "end": v(-377.33, 445.24) * mm});
            skLineSegment(sketch, "E1326", {"start": v(-377.33, 445.24) * mm, "end": v(-378.9, 445.02) * mm});
            skLineSegment(sketch, "E1327", {"start": v(-378.9, 445.02) * mm, "end": v(-380.46, 444.9) * mm});
            skLineSegment(sketch, "E1328", {"start": v(-380.46, 444.9) * mm, "end": v(-382.02, 444.86) * mm});
            skLineSegment(sketch, "E1329", {"start": v(-382.02, 444.86) * mm, "end": v(-383.58, 444.9) * mm});
            skLineSegment(sketch, "E1330", {"start": v(-383.58, 444.9) * mm, "end": v(-385.14, 445.04) * mm});
            skLineSegment(sketch, "E1331", {"start": v(-385.14, 445.04) * mm, "end": v(-386.7, 445.24) * mm});
            skLineSegment(sketch, "E1332", {"start": v(-386.7, 445.24) * mm, "end": v(-388.24, 445.53) * mm});
            skLineSegment(sketch, "E1333", {"start": v(-388.24, 445.53) * mm, "end": v(-389.78, 445.89) * mm});
            skLineSegment(sketch, "E1334", {"start": v(-389.78, 445.89) * mm, "end": v(-391.32, 446.32) * mm});
            skLineSegment(sketch, "E1335", {"start": v(-391.32, 446.32) * mm, "end": v(-392.86, 446.81) * mm});
            skLineSegment(sketch, "E1336", {"start": v(-392.86, 446.81) * mm, "end": v(-394.38, 447.37) * mm});
            skLineSegment(sketch, "E1337", {"start": v(-394.38, 447.37) * mm, "end": v(-395.9, 447.99) * mm});
            skLineSegment(sketch, "E1338", {"start": v(-395.9, 447.99) * mm, "end": v(-397.42, 448.66) * mm});
            skLineSegment(sketch, "E1339", {"start": v(-397.42, 448.66) * mm, "end": v(-398.93, 449.4) * mm});
            skLineSegment(sketch, "E1340", {"start": v(-398.93, 449.4) * mm, "end": v(-400.43, 450.17) * mm});
            skLineSegment(sketch, "E1341", {"start": v(-400.43, 450.17) * mm, "end": v(-401.92, 451) * mm});
            skLineSegment(sketch, "E1342", {"start": v(-401.92, 451) * mm, "end": v(-403.4, 451.86) * mm});
            skLineSegment(sketch, "E1343", {"start": v(-403.4, 451.86) * mm, "end": v(-404.87, 452.77) * mm});
            skLineSegment(sketch, "E1344", {"start": v(-404.87, 452.77) * mm, "end": v(-406.33, 453.72) * mm});
            skLineSegment(sketch, "E1345", {"start": v(-406.33, 453.72) * mm, "end": v(-407.79, 454.7) * mm});
            skLineSegment(sketch, "E1346", {"start": v(-407.79, 454.7) * mm, "end": v(-409.23, 455.71) * mm});
            skLineSegment(sketch, "E1347", {"start": v(-409.23, 455.71) * mm, "end": v(-410.66, 456.75) * mm});
            skLineSegment(sketch, "E1348", {"start": v(-410.66, 456.75) * mm, "end": v(-412.08, 457.82) * mm});
            skLineSegment(sketch, "E1349", {"start": v(-412.08, 457.82) * mm, "end": v(-413.4, 458.83) * mm});
            skLineSegment(sketch, "E1350", {"start": v(-413.4, 458.83) * mm, "end": v(-414.73, 459.86) * mm});
            skLineSegment(sketch, "E1351", {"start": v(-414.73, 459.86) * mm, "end": v(-416.07, 460.9) * mm});
            skLineSegment(sketch, "E1352", {"start": v(-416.07, 460.9) * mm, "end": v(-417.4, 461.92) * mm});
            skLineSegment(sketch, "E1353", {"start": v(-417.4, 461.92) * mm, "end": v(-418.75, 462.92) * mm});
            skLineSegment(sketch, "E1354", {"start": v(-418.75, 462.92) * mm, "end": v(-420.1, 463.9) * mm});
            skLineSegment(sketch, "E1355", {"start": v(-420.1, 463.9) * mm, "end": v(-421.45, 464.83) * mm});
            skLineSegment(sketch, "E1356", {"start": v(-421.45, 464.83) * mm, "end": v(-422.81, 465.71) * mm});
            skLineSegment(sketch, "E1357", {"start": v(-422.81, 465.71) * mm, "end": v(-424.18, 466.53) * mm});
            skLineSegment(sketch, "E1358", {"start": v(-424.18, 466.53) * mm, "end": v(-425.56, 467.27) * mm});
            skLineSegment(sketch, "E1359", {"start": v(-425.56, 467.27) * mm, "end": v(-426.95, 467.93) * mm});
            skLineSegment(sketch, "E1360", {"start": v(-426.95, 467.93) * mm, "end": v(-428.35, 468.5) * mm});
            skLineSegment(sketch, "E1361", {"start": v(-428.35, 468.5) * mm, "end": v(-429.76, 468.95) * mm});
            skLineSegment(sketch, "E1362", {"start": v(-429.76, 468.95) * mm, "end": v(-431.18, 469.3) * mm});
            skLineSegment(sketch, "E1363", {"start": v(-431.18, 469.3) * mm, "end": v(-432.62, 469.5) * mm});
            skLineSegment(sketch, "E1364", {"start": v(-432.62, 469.5) * mm, "end": v(-434.07, 469.58) * mm});
            skLineSegment(sketch, "E1365", {"start": v(-434.07, 469.58) * mm, "end": v(-435.53, 469.5) * mm});
            skLineSegment(sketch, "E1366", {"start": v(-435.53, 469.5) * mm, "end": v(-437, 469.26) * mm});
            skLineSegment(sketch, "E1367", {"start": v(-437, 469.26) * mm, "end": v(-438.5, 468.85) * mm});
            skLineSegment(sketch, "E1368", {"start": v(-438.5, 468.85) * mm, "end": v(-440, 468.25) * mm});
            skLineSegment(sketch, "E1369", {"start": v(-440, 468.25) * mm, "end": v(-441.53, 467.47) * mm});
            skLineSegment(sketch, "E1370", {"start": v(-441.53, 467.47) * mm, "end": v(-443.08, 466.48) * mm});
            skLineSegment(sketch, "E1371", {"start": v(-443.08, 466.48) * mm, "end": v(-444.64, 465.27) * mm});
            skLineSegment(sketch, "E1372", {"start": v(-444.64, 465.27) * mm, "end": v(-445.66, 464.37) * mm});
            skLineSegment(sketch, "E1373", {"start": v(-445.66, 464.37) * mm, "end": v(-446.61, 463.47) * mm});
            skLineSegment(sketch, "E1374", {"start": v(-446.61, 463.47) * mm, "end": v(-447.49, 462.56) * mm});
            skLineSegment(sketch, "E1375", {"start": v(-447.49, 462.56) * mm, "end": v(-448.29, 461.66) * mm});
            skLineSegment(sketch, "E1376", {"start": v(-448.29, 461.66) * mm, "end": v(-449.02, 460.74) * mm});
            skLineSegment(sketch, "E1377", {"start": v(-449.02, 460.74) * mm, "end": v(-449.68, 459.83) * mm});
            skLineSegment(sketch, "E1378", {"start": v(-449.68, 459.83) * mm, "end": v(-450.27, 458.9) * mm});
            skLineSegment(sketch, "E1379", {"start": v(-450.27, 458.9) * mm, "end": v(-450.8, 457.98) * mm});
            skLineSegment(sketch, "E1380", {"start": v(-450.8, 457.98) * mm, "end": v(-451.25, 457.05) * mm});
            skLineSegment(sketch, "E1381", {"start": v(-451.25, 457.05) * mm, "end": v(-451.65, 456.12) * mm});
            skLineSegment(sketch, "E1382", {"start": v(-451.65, 456.12) * mm, "end": v(-451.99, 455.18) * mm});
            skLineSegment(sketch, "E1383", {"start": v(-451.99, 455.18) * mm, "end": v(-452.27, 454.24) * mm});
            skLineSegment(sketch, "E1384", {"start": v(-452.27, 454.24) * mm, "end": v(-452.49, 453.3) * mm});
            skLineSegment(sketch, "E1385", {"start": v(-452.49, 453.3) * mm, "end": v(-452.66, 452.35) * mm});
            skLineSegment(sketch, "E1386", {"start": v(-452.66, 452.35) * mm, "end": v(-452.77, 451.4) * mm});
            skLineSegment(sketch, "E1387", {"start": v(-452.77, 451.4) * mm, "end": v(-452.83, 450.44) * mm});
            skLineSegment(sketch, "E1388", {"start": v(-452.83, 450.44) * mm, "end": v(-452.85, 449.48) * mm});
            skLineSegment(sketch, "E1389", {"start": v(-452.85, 449.48) * mm, "end": v(-452.81, 448.51) * mm});
            skLineSegment(sketch, "E1390", {"start": v(-452.81, 448.51) * mm, "end": v(-452.74, 447.55) * mm});
            skLineSegment(sketch, "E1391", {"start": v(-452.74, 447.55) * mm, "end": v(-452.61, 446.57) * mm});
            skLineSegment(sketch, "E1392", {"start": v(-452.61, 446.57) * mm, "end": v(-452.45, 445.6) * mm});
            skLineSegment(sketch, "E1393", {"start": v(-452.45, 445.6) * mm, "end": v(-452.25, 444.62) * mm});
            skLineSegment(sketch, "E1394", {"start": v(-452.25, 444.62) * mm, "end": v(-452, 443.64) * mm});
            skLineSegment(sketch, "E1395", {"start": v(-452, 443.64) * mm, "end": v(-451.73, 442.65) * mm});
            skLineSegment(sketch, "E1396", {"start": v(-451.73, 442.65) * mm, "end": v(-451.41, 441.66) * mm});
            skLineSegment(sketch, "E1397", {"start": v(-451.41, 441.66) * mm, "end": v(-451.07, 440.66) * mm});
            skLineSegment(sketch, "E1398", {"start": v(-451.07, 440.66) * mm, "end": v(-450.7, 439.67) * mm});
            skLineSegment(sketch, "E1399", {"start": v(-450.7, 439.67) * mm, "end": v(-450.3, 438.66) * mm});
            skLineSegment(sketch, "E1400", {"start": v(-450.3, 438.66) * mm, "end": v(-449.86, 437.66) * mm});
            skLineSegment(sketch, "E1401", {"start": v(-449.86, 437.66) * mm, "end": v(-449.4, 436.65) * mm});
            skLineSegment(sketch, "E1402", {"start": v(-449.4, 436.65) * mm, "end": v(-448.93, 435.64) * mm});
            skLineSegment(sketch, "E1403", {"start": v(-448.93, 435.64) * mm, "end": v(-448.43, 434.62) * mm});
            skLineSegment(sketch, "E1404", {"start": v(-448.43, 434.62) * mm, "end": v(-447.91, 433.6) * mm});
            skLineSegment(sketch, "E1405", {"start": v(-447.91, 433.6) * mm, "end": v(-447.38, 432.58) * mm});
            skLineSegment(sketch, "E1406", {"start": v(-447.38, 432.58) * mm, "end": v(-446.82, 431.55) * mm});
            skLineSegment(sketch, "E1407", {"start": v(-446.82, 431.55) * mm, "end": v(-446.26, 430.52) * mm});
            skLineSegment(sketch, "E1408", {"start": v(-446.26, 430.52) * mm, "end": v(-445.68, 429.49) * mm});
            skLineSegment(sketch, "E1409", {"start": v(-445.68, 429.49) * mm, "end": v(-445.1, 428.45) * mm});
            skLineSegment(sketch, "E1410", {"start": v(-445.1, 428.45) * mm, "end": v(-444.5, 427.4) * mm});
            skLineSegment(sketch, "E1411", {"start": v(-444.5, 427.4) * mm, "end": v(-443.9, 426.36) * mm});
            skLineSegment(sketch, "E1412", {"start": v(-443.9, 426.36) * mm, "end": v(-443.3, 425.32) * mm});
            skLineSegment(sketch, "E1413", {"start": v(-443.3, 425.32) * mm, "end": v(-442.7, 424.26) * mm});
            skLineSegment(sketch, "E1414", {"start": v(-442.7, 424.26) * mm, "end": v(-442.08, 423.2) * mm});
            skLineSegment(sketch, "E1415", {"start": v(-442.08, 423.2) * mm, "end": v(-441.48, 422.15) * mm});
            skLineSegment(sketch, "E1416", {"start": v(-441.48, 422.15) * mm, "end": v(-440.88, 421.09) * mm});
            skLineSegment(sketch, "E1417", {"start": v(-440.88, 421.09) * mm, "end": v(-440.28, 420.02) * mm});
            skLineSegment(sketch, "E1418", {"start": v(-440.28, 420.02) * mm, "end": v(-439.69, 418.95) * mm});
            skLineSegment(sketch, "E1419", {"start": v(-439.69, 418.95) * mm, "end": v(-439.1, 417.88) * mm});
            skLineSegment(sketch, "E1420", {"start": v(-439.1, 417.88) * mm, "end": v(-438.54, 416.8) * mm});
            skLineSegment(sketch, "E1421", {"start": v(-438.54, 416.8) * mm, "end": v(-437.98, 415.73) * mm});
            skLineSegment(sketch, "E1422", {"start": v(-437.98, 415.73) * mm, "end": v(-437.43, 414.65) * mm});
            skLineSegment(sketch, "E1423", {"start": v(-437.43, 414.65) * mm, "end": v(-436.9, 413.56) * mm});
            skLineSegment(sketch, "E1424", {"start": v(-436.9, 413.56) * mm, "end": v(-436.4, 412.47) * mm});
            skLineSegment(sketch, "E1425", {"start": v(-436.4, 412.47) * mm, "end": v(-435.91, 411.38) * mm});
            skLineSegment(sketch, "E1426", {"start": v(-435.91, 411.38) * mm, "end": v(-435.44, 410.28) * mm});
            skLineSegment(sketch, "E1427", {"start": v(-435.44, 410.28) * mm, "end": v(-435, 409.19) * mm});
            skLineSegment(sketch, "E1428", {"start": v(-435, 409.19) * mm, "end": v(-434.58, 408.08) * mm});
            skLineSegment(sketch, "E1429", {"start": v(-434.58, 408.08) * mm, "end": v(-434.2, 406.98) * mm});
            skLineSegment(sketch, "E1430", {"start": v(-434.2, 406.98) * mm, "end": v(-433.84, 405.87) * mm});
            skLineSegment(sketch, "E1431", {"start": v(-433.84, 405.87) * mm, "end": v(-433.5, 404.76) * mm});
            skLineSegment(sketch, "E1432", {"start": v(-433.5, 404.76) * mm, "end": v(-433.21, 403.64) * mm});
            skLineSegment(sketch, "E1433", {"start": v(-433.21, 403.64) * mm, "end": v(-432.95, 402.53) * mm});
            skLineSegment(sketch, "E1434", {"start": v(-432.95, 402.53) * mm, "end": v(-432.73, 401.4) * mm});
            skLineSegment(sketch, "E1435", {"start": v(-432.73, 401.4) * mm, "end": v(-432.55, 400.28) * mm});
            skLineSegment(sketch, "E1436", {"start": v(-432.55, 400.28) * mm, "end": v(-432.4, 399.15) * mm});
            skLineSegment(sketch, "E1437", {"start": v(-432.4, 399.15) * mm, "end": v(-432.3, 398.02) * mm});
            skLineSegment(sketch, "E1438", {"start": v(-432.3, 398.02) * mm, "end": v(-432.25, 396.9) * mm});
            skLineSegment(sketch, "E1439", {"start": v(-432.25, 396.9) * mm, "end": v(-432.24, 395.76) * mm});
            skLineSegment(sketch, "E1440", {"start": v(-432.24, 395.76) * mm, "end": v(-432.28, 394.62) * mm});
            skLineSegment(sketch, "E1441", {"start": v(-432.28, 394.62) * mm, "end": v(-432.37, 393.47) * mm});
            skLineSegment(sketch, "E1442", {"start": v(-432.37, 393.47) * mm, "end": v(-432.51, 392.33) * mm});
            skLineSegment(sketch, "E1443", {"start": v(-432.51, 392.33) * mm, "end": v(-432.7, 391.18) * mm});
            skLineSegment(sketch, "E1444", {"start": v(-432.7, 391.18) * mm, "end": v(-432.96, 390.03) * mm});
            skLineSegment(sketch, "E1445", {"start": v(-432.96, 390.03) * mm, "end": v(-433.27, 388.87) * mm});
            skLineSegment(sketch, "E1446", {"start": v(-433.27, 388.87) * mm, "end": v(-433.63, 387.71) * mm});
            skLineSegment(sketch, "E1447", {"start": v(-433.63, 387.71) * mm, "end": v(-434.06, 386.55) * mm});
            skLineSegment(sketch, "E1448", {"start": v(-434.06, 386.55) * mm, "end": v(-434.56, 385.4) * mm});
            skLineSegment(sketch, "E1449", {"start": v(-434.56, 385.4) * mm, "end": v(-435.12, 384.22) * mm});
            skLineSegment(sketch, "E1450", {"start": v(-435.12, 384.22) * mm, "end": v(-435.74, 383.06) * mm});
            skLineSegment(sketch, "E1451", {"start": v(-435.74, 383.06) * mm, "end": v(-436.44, 381.88) * mm});
            skLineSegment(sketch, "E1452", {"start": v(-436.44, 381.88) * mm, "end": v(-437.2, 380.7) * mm});
            skLineSegment(sketch, "E1453", {"start": v(-437.2, 380.7) * mm, "end": v(-438.04, 379.53) * mm});
            skLineSegment(sketch, "E1454", {"start": v(-438.04, 379.53) * mm, "end": v(-438.95, 378.35) * mm});
            skLineSegment(sketch, "E1455", {"start": v(-438.95, 378.35) * mm, "end": v(-439.94, 377.17) * mm});
            skLineSegment(sketch, "E1456", {"start": v(-439.94, 377.17) * mm, "end": v(-441.24, 375.75) * mm});
            skLineSegment(sketch, "E1457", {"start": v(-441.24, 375.75) * mm, "end": v(-442.57, 374.45) * mm});
            skLineSegment(sketch, "E1458", {"start": v(-442.57, 374.45) * mm, "end": v(-443.93, 373.26) * mm});
            skLineSegment(sketch, "E1459", {"start": v(-443.93, 373.26) * mm, "end": v(-445.32, 372.17) * mm});
            skLineSegment(sketch, "E1460", {"start": v(-445.32, 372.17) * mm, "end": v(-446.74, 371.19) * mm});
            skLineSegment(sketch, "E1461", {"start": v(-446.74, 371.19) * mm, "end": v(-448.2, 370.3) * mm});
            skLineSegment(sketch, "E1462", {"start": v(-448.2, 370.3) * mm, "end": v(-449.67, 369.52) * mm});
            skLineSegment(sketch, "E1463", {"start": v(-449.67, 369.52) * mm, "end": v(-451.17, 368.83) * mm});
            skLineSegment(sketch, "E1464", {"start": v(-451.17, 368.83) * mm, "end": v(-452.7, 368.24) * mm});
            skLineSegment(sketch, "E1465", {"start": v(-452.7, 368.24) * mm, "end": v(-454.24, 367.73) * mm});
            skLineSegment(sketch, "E1466", {"start": v(-454.24, 367.73) * mm, "end": v(-455.8, 367.32) * mm});
            skLineSegment(sketch, "E1467", {"start": v(-455.8, 367.32) * mm, "end": v(-457.37, 366.98) * mm});
            skLineSegment(sketch, "E1468", {"start": v(-457.37, 366.98) * mm, "end": v(-458.97, 366.73) * mm});
            skLineSegment(sketch, "E1469", {"start": v(-458.97, 366.73) * mm, "end": v(-460.57, 366.56) * mm});
            skLineSegment(sketch, "E1470", {"start": v(-460.57, 366.56) * mm, "end": v(-462.19, 366.47) * mm});
            skLineSegment(sketch, "E1471", {"start": v(-462.19, 366.47) * mm, "end": v(-463.82, 366.45) * mm});
            skLineSegment(sketch, "E1472", {"start": v(-463.82, 366.45) * mm, "end": v(-465.45, 366.5) * mm});
            skLineSegment(sketch, "E1473", {"start": v(-465.45, 366.5) * mm, "end": v(-467.09, 366.62) * mm});
            skLineSegment(sketch, "E1474", {"start": v(-467.09, 366.62) * mm, "end": v(-468.73, 366.8) * mm});
            skLineSegment(sketch, "E1475", {"start": v(-468.73, 366.8) * mm, "end": v(-470.38, 367.05) * mm});
            skLineSegment(sketch, "E1476", {"start": v(-470.38, 367.05) * mm, "end": v(-472.03, 367.36) * mm});
            skLineSegment(sketch, "E1477", {"start": v(-472.03, 367.36) * mm, "end": v(-473.67, 367.73) * mm});
            skLineSegment(sketch, "E1478", {"start": v(-473.67, 367.73) * mm, "end": v(-475.31, 368.15) * mm});
            skLineSegment(sketch, "E1479", {"start": v(-475.31, 368.15) * mm, "end": v(-476.95, 368.62) * mm});
            skLineSegment(sketch, "E1480", {"start": v(-476.95, 368.62) * mm, "end": v(-478.58, 369.14) * mm});
            skLineSegment(sketch, "E1481", {"start": v(-478.58, 369.14) * mm, "end": v(-480.2, 369.71) * mm});
            skLineSegment(sketch, "E1482", {"start": v(-480.2, 369.71) * mm, "end": v(-481.81, 370.33) * mm});
            skLineSegment(sketch, "E1483", {"start": v(-481.81, 370.33) * mm, "end": v(-483.4, 370.98) * mm});
            skLineSegment(sketch, "E1484", {"start": v(-483.4, 370.98) * mm, "end": v(-485, 371.67) * mm});
            skLineSegment(sketch, "E1485", {"start": v(-485, 371.67) * mm, "end": v(-486.56, 372.4) * mm});
            skLineSegment(sketch, "E1486", {"start": v(-486.56, 372.4) * mm, "end": v(-488.11, 373.17) * mm});
            skLineSegment(sketch, "E1487", {"start": v(-488.11, 373.17) * mm, "end": v(-489.52, 373.89) * mm});
            skLineSegment(sketch, "E1488", {"start": v(-489.52, 373.89) * mm, "end": v(-490.96, 374.64) * mm});
            skLineSegment(sketch, "E1489", {"start": v(-490.96, 374.64) * mm, "end": v(-492.43, 375.41) * mm});
            skLineSegment(sketch, "E1490", {"start": v(-492.43, 375.41) * mm, "end": v(-493.93, 376.2) * mm});
            skLineSegment(sketch, "E1491", {"start": v(-493.93, 376.2) * mm, "end": v(-495.45, 376.97) * mm});
            skLineSegment(sketch, "E1492", {"start": v(-495.45, 376.97) * mm, "end": v(-496.99, 377.72) * mm});
            skLineSegment(sketch, "E1493", {"start": v(-496.99, 377.72) * mm, "end": v(-498.55, 378.44) * mm});
            skLineSegment(sketch, "E1494", {"start": v(-498.55, 378.44) * mm, "end": v(-500.11, 379.12) * mm});
            skLineSegment(sketch, "E1495", {"start": v(-500.11, 379.12) * mm, "end": v(-501.69, 379.74) * mm});
            skLineSegment(sketch, "E1496", {"start": v(-501.69, 379.74) * mm, "end": v(-503.27, 380.29) * mm});
            skLineSegment(sketch, "E1497", {"start": v(-503.27, 380.29) * mm, "end": v(-504.84, 380.75) * mm});
            skLineSegment(sketch, "E1498", {"start": v(-504.84, 380.75) * mm, "end": v(-506.42, 381.12) * mm});
            skLineSegment(sketch, "E1499", {"start": v(-506.42, 381.12) * mm, "end": v(-507.99, 381.37) * mm});
            skLineSegment(sketch, "E1500", {"start": v(-507.99, 381.37) * mm, "end": v(-509.54, 381.5) * mm});
            skLineSegment(sketch, "E1501", {"start": v(-509.54, 381.5) * mm, "end": v(-511.08, 381.5) * mm});
            skLineSegment(sketch, "E1502", {"start": v(-511.08, 381.5) * mm, "end": v(-512.6, 381.35) * mm});
            skLineSegment(sketch, "E1503", {"start": v(-512.6, 381.35) * mm, "end": v(-514.1, 381.03) * mm});
            skLineSegment(sketch, "E1504", {"start": v(-514.1, 381.03) * mm, "end": v(-515.58, 380.54) * mm});
            skLineSegment(sketch, "E1505", {"start": v(-515.58, 380.54) * mm, "end": v(-517.02, 379.86) * mm});
            skLineSegment(sketch, "E1506", {"start": v(-517.02, 379.86) * mm, "end": v(-518.43, 378.98) * mm});
            skLineSegment(sketch, "E1507", {"start": v(-518.43, 378.98) * mm, "end": v(-519.8, 377.88) * mm});
            skLineSegment(sketch, "E1508", {"start": v(-519.8, 377.88) * mm, "end": v(-521.13, 376.56) * mm});
            skLineSegment(sketch, "E1509", {"start": v(-521.13, 376.56) * mm, "end": v(-522.09, 375.47) * mm});
            skLineSegment(sketch, "E1510", {"start": v(-522.09, 375.47) * mm, "end": v(-522.96, 374.4) * mm});
            skLineSegment(sketch, "E1511", {"start": v(-522.96, 374.4) * mm, "end": v(-523.76, 373.32) * mm});
            skLineSegment(sketch, "E1512", {"start": v(-523.76, 373.32) * mm, "end": v(-524.48, 372.26) * mm});
            skLineSegment(sketch, "E1513", {"start": v(-524.48, 372.26) * mm, "end": v(-525.13, 371.21) * mm});
            skLineSegment(sketch, "E1514", {"start": v(-525.13, 371.21) * mm, "end": v(-525.7, 370.17) * mm});
            skLineSegment(sketch, "E1515", {"start": v(-525.7, 370.17) * mm, "end": v(-526.22, 369.14) * mm});
            skLineSegment(sketch, "E1516", {"start": v(-526.22, 369.14) * mm, "end": v(-526.65, 368.12) * mm});
            skLineSegment(sketch, "E1517", {"start": v(-526.65, 368.12) * mm, "end": v(-527.03, 367.1) * mm});
            skLineSegment(sketch, "E1518", {"start": v(-527.03, 367.1) * mm, "end": v(-527.33, 366.1) * mm});
            skLineSegment(sketch, "E1519", {"start": v(-527.33, 366.1) * mm, "end": v(-527.58, 365.1) * mm});
            skLineSegment(sketch, "E1520", {"start": v(-527.58, 365.1) * mm, "end": v(-527.76, 364.12) * mm});
            skLineSegment(sketch, "E1521", {"start": v(-527.76, 364.12) * mm, "end": v(-527.88, 363.14) * mm});
            skLineSegment(sketch, "E1522", {"start": v(-527.88, 363.14) * mm, "end": v(-527.95, 362.16) * mm});
            skLineSegment(sketch, "E1523", {"start": v(-527.95, 362.16) * mm, "end": v(-527.96, 361.2) * mm});
            skLineSegment(sketch, "E1524", {"start": v(-527.96, 361.2) * mm, "end": v(-527.92, 360.23) * mm});
            skLineSegment(sketch, "E1525", {"start": v(-527.92, 360.23) * mm, "end": v(-527.83, 359.28) * mm});
            skLineSegment(sketch, "E1526", {"start": v(-527.83, 359.28) * mm, "end": v(-527.69, 358.32) * mm});
            skLineSegment(sketch, "E1527", {"start": v(-527.69, 358.32) * mm, "end": v(-527.5, 357.38) * mm});
            skLineSegment(sketch, "E1528", {"start": v(-527.5, 357.38) * mm, "end": v(-527.26, 356.44) * mm});
            skLineSegment(sketch, "E1529", {"start": v(-527.26, 356.44) * mm, "end": v(-526.98, 355.5) * mm});
            skLineSegment(sketch, "E1530", {"start": v(-526.98, 355.5) * mm, "end": v(-526.65, 354.57) * mm});
            skLineSegment(sketch, "E1531", {"start": v(-526.65, 354.57) * mm, "end": v(-526.29, 353.65) * mm});
            skLineSegment(sketch, "E1532", {"start": v(-526.29, 353.65) * mm, "end": v(-525.89, 352.72) * mm});
            skLineSegment(sketch, "E1533", {"start": v(-525.89, 352.72) * mm, "end": v(-525.45, 351.8) * mm});
            skLineSegment(sketch, "E1534", {"start": v(-525.45, 351.8) * mm, "end": v(-524.97, 350.89) * mm});
            skLineSegment(sketch, "E1535", {"start": v(-524.97, 350.89) * mm, "end": v(-524.46, 349.98) * mm});
            skLineSegment(sketch, "E1536", {"start": v(-524.46, 349.98) * mm, "end": v(-523.93, 349.06) * mm});
            skLineSegment(sketch, "E1537", {"start": v(-523.93, 349.06) * mm, "end": v(-523.36, 348.16) * mm});
            skLineSegment(sketch, "E1538", {"start": v(-523.36, 348.16) * mm, "end": v(-522.76, 347.25) * mm});
            skLineSegment(sketch, "E1539", {"start": v(-522.76, 347.25) * mm, "end": v(-522.14, 346.34) * mm});
            skLineSegment(sketch, "E1540", {"start": v(-522.14, 346.34) * mm, "end": v(-521.5, 345.44) * mm});
            skLineSegment(sketch, "E1541", {"start": v(-521.5, 345.44) * mm, "end": v(-520.83, 344.53) * mm});
            skLineSegment(sketch, "E1542", {"start": v(-520.83, 344.53) * mm, "end": v(-520.14, 343.63) * mm});
            skLineSegment(sketch, "E1543", {"start": v(-520.14, 343.63) * mm, "end": v(-519.44, 342.73) * mm});
            skLineSegment(sketch, "E1544", {"start": v(-519.44, 342.73) * mm, "end": v(-518.71, 341.82) * mm});
            skLineSegment(sketch, "E1545", {"start": v(-518.71, 341.82) * mm, "end": v(-517.98, 340.92) * mm});
            skLineSegment(sketch, "E1546", {"start": v(-517.98, 340.92) * mm, "end": v(-517.23, 340.01) * mm});
            skLineSegment(sketch, "E1547", {"start": v(-517.23, 340.01) * mm, "end": v(-516.47, 339.1) * mm});
            skLineSegment(sketch, "E1548", {"start": v(-516.47, 339.1) * mm, "end": v(-515.7, 338.2) * mm});
            skLineSegment(sketch, "E1549", {"start": v(-515.7, 338.2) * mm, "end": v(-514.92, 337.3) * mm});
            skLineSegment(sketch, "E1550", {"start": v(-514.92, 337.3) * mm, "end": v(-514.14, 336.38) * mm});
            skLineSegment(sketch, "E1551", {"start": v(-514.14, 336.38) * mm, "end": v(-513.36, 335.47) * mm});
            skLineSegment(sketch, "E1552", {"start": v(-513.36, 335.47) * mm, "end": v(-512.57, 334.55) * mm});
            skLineSegment(sketch, "E1553", {"start": v(-512.57, 334.55) * mm, "end": v(-511.78, 333.63) * mm});
            skLineSegment(sketch, "E1554", {"start": v(-511.78, 333.63) * mm, "end": v(-511, 332.7) * mm});
            skLineSegment(sketch, "E1555", {"start": v(-511, 332.7) * mm, "end": v(-510.22, 331.78) * mm});
            skLineSegment(sketch, "E1556", {"start": v(-510.22, 331.78) * mm, "end": v(-509.45, 330.85) * mm});
            skLineSegment(sketch, "E1557", {"start": v(-509.45, 330.85) * mm, "end": v(-508.68, 329.92) * mm});
            skLineSegment(sketch, "E1558", {"start": v(-508.68, 329.92) * mm, "end": v(-507.92, 328.98) * mm});
            skLineSegment(sketch, "E1559", {"start": v(-507.92, 328.98) * mm, "end": v(-507.18, 328.03) * mm});
            skLineSegment(sketch, "E1560", {"start": v(-507.18, 328.03) * mm, "end": v(-506.45, 327.08) * mm});
            skLineSegment(sketch, "E1561", {"start": v(-506.45, 327.08) * mm, "end": v(-505.73, 326.12) * mm});
            skLineSegment(sketch, "E1562", {"start": v(-505.73, 326.12) * mm, "end": v(-505.03, 325.16) * mm});
            skLineSegment(sketch, "E1563", {"start": v(-505.03, 325.16) * mm, "end": v(-504.35, 324.2) * mm});
            skLineSegment(sketch, "E1564", {"start": v(-504.35, 324.2) * mm, "end": v(-503.69, 323.22) * mm});
            skLineSegment(sketch, "E1565", {"start": v(-503.69, 323.22) * mm, "end": v(-503.05, 322.24) * mm});
            skLineSegment(sketch, "E1566", {"start": v(-503.05, 322.24) * mm, "end": v(-502.44, 321.25) * mm});
            skLineSegment(sketch, "E1567", {"start": v(-502.44, 321.25) * mm, "end": v(-501.85, 320.25) * mm});
            skLineSegment(sketch, "E1568", {"start": v(-501.85, 320.25) * mm, "end": v(-501.3, 319.25) * mm});
            skLineSegment(sketch, "E1569", {"start": v(-501.3, 319.25) * mm, "end": v(-500.76, 318.23) * mm});
            skLineSegment(sketch, "E1570", {"start": v(-500.76, 318.23) * mm, "end": v(-500.26, 317.21) * mm});
            skLineSegment(sketch, "E1571", {"start": v(-500.26, 317.21) * mm, "end": v(-499.8, 316.18) * mm});
            skLineSegment(sketch, "E1572", {"start": v(-499.8, 316.18) * mm, "end": v(-499.37, 315.14) * mm});
            skLineSegment(sketch, "E1573", {"start": v(-499.37, 315.14) * mm, "end": v(-498.98, 314.1) * mm});
            skLineSegment(sketch, "E1574", {"start": v(-498.98, 314.1) * mm, "end": v(-498.63, 313.03) * mm});
            skLineSegment(sketch, "E1575", {"start": v(-498.63, 313.03) * mm, "end": v(-498.32, 311.96) * mm});
            skLineSegment(sketch, "E1576", {"start": v(-498.32, 311.96) * mm, "end": v(-498.05, 310.88) * mm});
            skLineSegment(sketch, "E1577", {"start": v(-498.05, 310.88) * mm, "end": v(-497.83, 309.8) * mm});
            skLineSegment(sketch, "E1578", {"start": v(-497.83, 309.8) * mm, "end": v(-497.65, 308.69) * mm});
            skLineSegment(sketch, "E1579", {"start": v(-497.65, 308.69) * mm, "end": v(-497.53, 307.57) * mm});
            skLineSegment(sketch, "E1580", {"start": v(-497.53, 307.57) * mm, "end": v(-497.45, 306.45) * mm});
            skLineSegment(sketch, "E1581", {"start": v(-497.45, 306.45) * mm, "end": v(-497.43, 305.31) * mm});
            skLineSegment(sketch, "E1582", {"start": v(-497.43, 305.31) * mm, "end": v(-497.45, 304.16) * mm});
            skLineSegment(sketch, "E1583", {"start": v(-497.45, 304.16) * mm, "end": v(-497.54, 303) * mm});
            skLineSegment(sketch, "E1584", {"start": v(-497.54, 303) * mm, "end": v(-497.68, 301.82) * mm});
            skLineSegment(sketch, "E1585", {"start": v(-497.68, 301.82) * mm, "end": v(-497.88, 300.63) * mm});
            skLineSegment(sketch, "E1586", {"start": v(-497.88, 300.63) * mm, "end": v(-498.15, 299.43) * mm});
            skLineSegment(sketch, "E1587", {"start": v(-498.15, 299.43) * mm, "end": v(-498.48, 298.21) * mm});
            skLineSegment(sketch, "E1588", {"start": v(-498.48, 298.21) * mm, "end": v(-498.87, 296.98) * mm});
            skLineSegment(sketch, "E1589", {"start": v(-498.87, 296.98) * mm, "end": v(-499.33, 295.73) * mm});
            skLineSegment(sketch, "E1590", {"start": v(-499.33, 295.73) * mm, "end": v(-499.86, 294.47) * mm});
            skLineSegment(sketch, "E1591", {"start": v(-499.86, 294.47) * mm, "end": v(-500.46, 293.2) * mm});
            skLineSegment(sketch, "E1592", {"start": v(-500.46, 293.2) * mm, "end": v(-501.13, 291.9) * mm});
            skLineSegment(sketch, "E1593", {"start": v(-501.13, 291.9) * mm, "end": v(-502.09, 290.22) * mm});
            skLineSegment(sketch, "E1594", {"start": v(-502.09, 290.22) * mm, "end": v(-503.1, 288.64) * mm});
            skLineSegment(sketch, "E1595", {"start": v(-503.1, 288.64) * mm, "end": v(-504.14, 287.15) * mm});
            skLineSegment(sketch, "E1596", {"start": v(-504.14, 287.15) * mm, "end": v(-505.23, 285.74) * mm});
            skLineSegment(sketch, "E1597", {"start": v(-505.23, 285.74) * mm, "end": v(-506.37, 284.43) * mm});
            skLineSegment(sketch, "E1598", {"start": v(-506.37, 284.43) * mm, "end": v(-507.54, 283.2) * mm});
            skLineSegment(sketch, "E1599", {"start": v(-507.54, 283.2) * mm, "end": v(-508.76, 282.05) * mm});
            skLineSegment(sketch, "E1600", {"start": v(-508.76, 282.05) * mm, "end": v(-510, 280.98) * mm});
            skLineSegment(sketch, "E1601", {"start": v(-510, 280.98) * mm, "end": v(-511.3, 280) * mm});
            skLineSegment(sketch, "E1602", {"start": v(-511.3, 280) * mm, "end": v(-512.61, 279.1) * mm});
            skLineSegment(sketch, "E1603", {"start": v(-512.61, 279.1) * mm, "end": v(-513.97, 278.26) * mm});
            skLineSegment(sketch, "E1604", {"start": v(-513.97, 278.26) * mm, "end": v(-515.36, 277.52) * mm});
            skLineSegment(sketch, "E1605", {"start": v(-515.36, 277.52) * mm, "end": v(-516.77, 276.84) * mm});
            skLineSegment(sketch, "E1606", {"start": v(-516.77, 276.84) * mm, "end": v(-518.22, 276.24) * mm});
            skLineSegment(sketch, "E1607", {"start": v(-518.22, 276.24) * mm, "end": v(-519.7, 275.72) * mm});
            skLineSegment(sketch, "E1608", {"start": v(-519.7, 275.72) * mm, "end": v(-521.2, 275.26) * mm});
            skLineSegment(sketch, "E1609", {"start": v(-521.2, 275.26) * mm, "end": v(-522.73, 274.88) * mm});
            skLineSegment(sketch, "E1610", {"start": v(-522.73, 274.88) * mm, "end": v(-524.28, 274.57) * mm});
            skLineSegment(sketch, "E1611", {"start": v(-524.28, 274.57) * mm, "end": v(-525.86, 274.32) * mm});
            skLineSegment(sketch, "E1612", {"start": v(-525.86, 274.32) * mm, "end": v(-527.45, 274.14) * mm});
            skLineSegment(sketch, "E1613", {"start": v(-527.45, 274.14) * mm, "end": v(-529.07, 274.02) * mm});
            skLineSegment(sketch, "E1614", {"start": v(-529.07, 274.02) * mm, "end": v(-530.7, 273.97) * mm});
            skLineSegment(sketch, "E1615", {"start": v(-530.7, 273.97) * mm, "end": v(-532.36, 273.98) * mm});
            skLineSegment(sketch, "E1616", {"start": v(-532.36, 273.98) * mm, "end": v(-534.02, 274.05) * mm});
            skLineSegment(sketch, "E1617", {"start": v(-534.02, 274.05) * mm, "end": v(-535.7, 274.18) * mm});
            skLineSegment(sketch, "E1618", {"start": v(-535.7, 274.18) * mm, "end": v(-537.4, 274.37) * mm});
            skLineSegment(sketch, "E1619", {"start": v(-537.4, 274.37) * mm, "end": v(-539.11, 274.61) * mm});
            skLineSegment(sketch, "E1620", {"start": v(-539.11, 274.61) * mm, "end": v(-540.83, 274.91) * mm});
            skLineSegment(sketch, "E1621", {"start": v(-540.83, 274.91) * mm, "end": v(-542.56, 275.27) * mm});
            skLineSegment(sketch, "E1622", {"start": v(-542.56, 275.27) * mm, "end": v(-544.3, 275.67) * mm});
            skLineSegment(sketch, "E1623", {"start": v(-544.3, 275.67) * mm, "end": v(-546.04, 276.13) * mm});
            skLineSegment(sketch, "E1624", {"start": v(-546.04, 276.13) * mm, "end": v(-547.44, 276.53) * mm});
            skLineSegment(sketch, "E1625", {"start": v(-547.44, 276.53) * mm, "end": v(-548.9, 276.97) * mm});
            skLineSegment(sketch, "E1626", {"start": v(-548.9, 276.97) * mm, "end": v(-550.44, 277.44) * mm});
            skLineSegment(sketch, "E1627", {"start": v(-550.44, 277.44) * mm, "end": v(-552.03, 277.92) * mm});
            skLineSegment(sketch, "E1628", {"start": v(-552.03, 277.92) * mm, "end": v(-553.67, 278.42) * mm});
            skLineSegment(sketch, "E1629", {"start": v(-553.67, 278.42) * mm, "end": v(-555.36, 278.9) * mm});
            skLineSegment(sketch, "E1630", {"start": v(-555.36, 278.9) * mm, "end": v(-557.07, 279.36) * mm});
            skLineSegment(sketch, "E1631", {"start": v(-557.07, 279.36) * mm, "end": v(-558.8, 279.8) * mm});
            skLineSegment(sketch, "E1632", {"start": v(-558.8, 279.8) * mm, "end": v(-560.55, 280.18) * mm});
            skLineSegment(sketch, "E1633", {"start": v(-560.55, 280.18) * mm, "end": v(-562.3, 280.5) * mm});
            skLineSegment(sketch, "E1634", {"start": v(-562.3, 280.5) * mm, "end": v(-564.04, 280.77) * mm});
            skLineSegment(sketch, "E1635", {"start": v(-564.04, 280.77) * mm, "end": v(-565.78, 280.95) * mm});
            skLineSegment(sketch, "E1636", {"start": v(-565.78, 280.95) * mm, "end": v(-567.49, 281.03) * mm});
            skLineSegment(sketch, "E1637", {"start": v(-567.49, 281.03) * mm, "end": v(-569.16, 281) * mm});
            skLineSegment(sketch, "E1638", {"start": v(-569.16, 281) * mm, "end": v(-570.8, 280.87) * mm});
            skLineSegment(sketch, "E1639", {"start": v(-570.8, 280.87) * mm, "end": v(-572.4, 280.6) * mm});
            skLineSegment(sketch, "E1640", {"start": v(-572.4, 280.6) * mm, "end": v(-573.92, 280.18) * mm});
            skLineSegment(sketch, "E1641", {"start": v(-573.92, 280.18) * mm, "end": v(-575.39, 279.6) * mm});
            skLineSegment(sketch, "E1642", {"start": v(-575.39, 279.6) * mm, "end": v(-576.77, 278.87) * mm});
            skLineSegment(sketch, "E1643", {"start": v(-576.77, 278.87) * mm, "end": v(-578.08, 277.95) * mm});
            skLineSegment(sketch, "E1644", {"start": v(-578.08, 277.95) * mm, "end": v(-579.29, 276.83) * mm});
            skLineSegment(sketch, "E1645", {"start": v(-579.29, 276.83) * mm, "end": v(-580.25, 275.79) * mm});
            skLineSegment(sketch, "E1646", {"start": v(-580.25, 275.79) * mm, "end": v(-581.14, 274.75) * mm});
            skLineSegment(sketch, "E1647", {"start": v(-581.14, 274.75) * mm, "end": v(-581.96, 273.73) * mm});
            skLineSegment(sketch, "E1648", {"start": v(-581.96, 273.73) * mm, "end": v(-582.7, 272.72) * mm});
            skLineSegment(sketch, "E1649", {"start": v(-582.7, 272.72) * mm, "end": v(-583.37, 271.73) * mm});
            skLineSegment(sketch, "E1650", {"start": v(-583.37, 271.73) * mm, "end": v(-583.97, 270.74) * mm});
            skLineSegment(sketch, "E1651", {"start": v(-583.97, 270.74) * mm, "end": v(-584.5, 269.77) * mm});
            skLineSegment(sketch, "E1652", {"start": v(-584.5, 269.77) * mm, "end": v(-584.96, 268.8) * mm});
            skLineSegment(sketch, "E1653", {"start": v(-584.96, 268.8) * mm, "end": v(-585.36, 267.86) * mm});
            skLineSegment(sketch, "E1654", {"start": v(-585.36, 267.86) * mm, "end": v(-585.69, 266.92) * mm});
            skLineSegment(sketch, "E1655", {"start": v(-585.69, 266.92) * mm, "end": v(-585.96, 265.99) * mm});
            skLineSegment(sketch, "E1656", {"start": v(-585.96, 265.99) * mm, "end": v(-586.17, 265.07) * mm});
            skLineSegment(sketch, "E1657", {"start": v(-586.17, 265.07) * mm, "end": v(-586.32, 264.16) * mm});
            skLineSegment(sketch, "E1658", {"start": v(-586.32, 264.16) * mm, "end": v(-586.4, 263.25) * mm});
            skLineSegment(sketch, "E1659", {"start": v(-586.4, 263.25) * mm, "end": v(-586.44, 262.36) * mm});
            skLineSegment(sketch, "E1660", {"start": v(-586.44, 262.36) * mm, "end": v(-586.42, 261.47) * mm});
            skLineSegment(sketch, "E1661", {"start": v(-586.42, 261.47) * mm, "end": v(-586.35, 260.6) * mm});
            skLineSegment(sketch, "E1662", {"start": v(-586.35, 260.6) * mm, "end": v(-586.23, 259.73) * mm});
            skLineSegment(sketch, "E1663", {"start": v(-586.23, 259.73) * mm, "end": v(-586.06, 258.86) * mm});
            skLineSegment(sketch, "E1664", {"start": v(-586.06, 258.86) * mm, "end": v(-585.84, 258) * mm});
            skLineSegment(sketch, "E1665", {"start": v(-585.84, 258) * mm, "end": v(-585.57, 257.16) * mm});
            skLineSegment(sketch, "E1666", {"start": v(-585.57, 257.16) * mm, "end": v(-585.26, 256.31) * mm});
            skLineSegment(sketch, "E1667", {"start": v(-585.26, 256.31) * mm, "end": v(-584.9, 255.47) * mm});
            skLineSegment(sketch, "E1668", {"start": v(-584.9, 255.47) * mm, "end": v(-584.5, 254.64) * mm});
            skLineSegment(sketch, "E1669", {"start": v(-584.5, 254.64) * mm, "end": v(-584.07, 253.82) * mm});
            skLineSegment(sketch, "E1670", {"start": v(-584.07, 253.82) * mm, "end": v(-583.6, 253) * mm});
            skLineSegment(sketch, "E1671", {"start": v(-583.6, 253) * mm, "end": v(-583.08, 252.17) * mm});
            skLineSegment(sketch, "E1672", {"start": v(-583.08, 252.17) * mm, "end": v(-582.53, 251.36) * mm});
            skLineSegment(sketch, "E1673", {"start": v(-582.53, 251.36) * mm, "end": v(-581.95, 250.55) * mm});
            skLineSegment(sketch, "E1674", {"start": v(-581.95, 250.55) * mm, "end": v(-581.34, 249.74) * mm});
            skLineSegment(sketch, "E1675", {"start": v(-581.34, 249.74) * mm, "end": v(-580.7, 248.94) * mm});
            skLineSegment(sketch, "E1676", {"start": v(-580.7, 248.94) * mm, "end": v(-580.03, 248.13) * mm});
            skLineSegment(sketch, "E1677", {"start": v(-580.03, 248.13) * mm, "end": v(-579.33, 247.33) * mm});
            skLineSegment(sketch, "E1678", {"start": v(-579.33, 247.33) * mm, "end": v(-578.6, 246.53) * mm});
            skLineSegment(sketch, "E1679", {"start": v(-578.6, 246.53) * mm, "end": v(-577.86, 245.74) * mm});
            skLineSegment(sketch, "E1680", {"start": v(-577.86, 245.74) * mm, "end": v(-577.09, 244.94) * mm});
            skLineSegment(sketch, "E1681", {"start": v(-577.09, 244.94) * mm, "end": v(-576.3, 244.15) * mm});
            skLineSegment(sketch, "E1682", {"start": v(-576.3, 244.15) * mm, "end": v(-575.49, 243.35) * mm});
            skLineSegment(sketch, "E1683", {"start": v(-575.49, 243.35) * mm, "end": v(-574.66, 242.56) * mm});
            skLineSegment(sketch, "E1684", {"start": v(-574.66, 242.56) * mm, "end": v(-573.82, 241.76) * mm});
            skLineSegment(sketch, "E1685", {"start": v(-573.82, 241.76) * mm, "end": v(-572.96, 240.96) * mm});
            skLineSegment(sketch, "E1686", {"start": v(-572.96, 240.96) * mm, "end": v(-572.1, 240.17) * mm});
            skLineSegment(sketch, "E1687", {"start": v(-572.1, 240.17) * mm, "end": v(-571.21, 239.37) * mm});
            skLineSegment(sketch, "E1688", {"start": v(-571.21, 239.37) * mm, "end": v(-570.32, 238.57) * mm});
            skLineSegment(sketch, "E1689", {"start": v(-570.32, 238.57) * mm, "end": v(-569.43, 237.77) * mm});
            skLineSegment(sketch, "E1690", {"start": v(-569.43, 237.77) * mm, "end": v(-568.52, 236.96) * mm});
            skLineSegment(sketch, "E1691", {"start": v(-568.52, 236.96) * mm, "end": v(-567.62, 236.15) * mm});
            skLineSegment(sketch, "E1692", {"start": v(-567.62, 236.15) * mm, "end": v(-566.7, 235.34) * mm});
            skLineSegment(sketch, "E1693", {"start": v(-566.7, 235.34) * mm, "end": v(-565.8, 234.53) * mm});
            skLineSegment(sketch, "E1694", {"start": v(-565.8, 234.53) * mm, "end": v(-564.88, 233.7) * mm});
            skLineSegment(sketch, "E1695", {"start": v(-564.88, 233.7) * mm, "end": v(-563.97, 232.89) * mm});
            skLineSegment(sketch, "E1696", {"start": v(-563.97, 232.89) * mm, "end": v(-563.07, 232.06) * mm});
            skLineSegment(sketch, "E1697", {"start": v(-563.07, 232.06) * mm, "end": v(-562.17, 231.23) * mm});
            skLineSegment(sketch, "E1698", {"start": v(-562.17, 231.23) * mm, "end": v(-561.27, 230.39) * mm});
            skLineSegment(sketch, "E1699", {"start": v(-561.27, 230.39) * mm, "end": v(-560.39, 229.55) * mm});
            skLineSegment(sketch, "E1700", {"start": v(-560.39, 229.55) * mm, "end": v(-559.51, 228.7) * mm});
            skLineSegment(sketch, "E1701", {"start": v(-559.51, 228.7) * mm, "end": v(-558.65, 227.84) * mm});
            skLineSegment(sketch, "E1702", {"start": v(-558.65, 227.84) * mm, "end": v(-557.8, 226.98) * mm});
            skLineSegment(sketch, "E1703", {"start": v(-557.8, 226.98) * mm, "end": v(-556.96, 226.1) * mm});
            skLineSegment(sketch, "E1704", {"start": v(-556.96, 226.1) * mm, "end": v(-556.14, 225.23) * mm});
            skLineSegment(sketch, "E1705", {"start": v(-556.14, 225.23) * mm, "end": v(-555.34, 224.34) * mm});
            skLineSegment(sketch, "E1706", {"start": v(-555.34, 224.34) * mm, "end": v(-554.56, 223.45) * mm});
            skLineSegment(sketch, "E1707", {"start": v(-554.56, 223.45) * mm, "end": v(-553.8, 222.55) * mm});
            skLineSegment(sketch, "E1708", {"start": v(-553.8, 222.55) * mm, "end": v(-553.06, 221.63) * mm});
            skLineSegment(sketch, "E1709", {"start": v(-553.06, 221.63) * mm, "end": v(-552.35, 220.71) * mm});
            skLineSegment(sketch, "E1710", {"start": v(-552.35, 220.71) * mm, "end": v(-551.66, 219.78) * mm});
            skLineSegment(sketch, "E1711", {"start": v(-551.66, 219.78) * mm, "end": v(-551, 218.84) * mm});
            skLineSegment(sketch, "E1712", {"start": v(-551, 218.84) * mm, "end": v(-550.38, 217.9) * mm});
            skLineSegment(sketch, "E1713", {"start": v(-550.38, 217.9) * mm, "end": v(-549.78, 216.93) * mm});
            skLineSegment(sketch, "E1714", {"start": v(-549.78, 216.93) * mm, "end": v(-549.21, 215.96) * mm});
            skLineSegment(sketch, "E1715", {"start": v(-549.21, 215.96) * mm, "end": v(-548.68, 214.97) * mm});
            skLineSegment(sketch, "E1716", {"start": v(-548.68, 214.97) * mm, "end": v(-548.19, 213.98) * mm});
            skLineSegment(sketch, "E1717", {"start": v(-548.19, 213.98) * mm, "end": v(-547.73, 212.97) * mm});
            skLineSegment(sketch, "E1718", {"start": v(-547.73, 212.97) * mm, "end": v(-547.3, 211.95) * mm});
            skLineSegment(sketch, "E1719", {"start": v(-547.3, 211.95) * mm, "end": v(-546.93, 210.91) * mm});
            skLineSegment(sketch, "E1720", {"start": v(-546.93, 210.91) * mm, "end": v(-546.6, 209.87) * mm});
            skLineSegment(sketch, "E1721", {"start": v(-546.6, 209.87) * mm, "end": v(-546.3, 208.8) * mm});
            skLineSegment(sketch, "E1722", {"start": v(-546.3, 208.8) * mm, "end": v(-546.06, 207.73) * mm});
            skLineSegment(sketch, "E1723", {"start": v(-546.06, 207.73) * mm, "end": v(-545.86, 206.64) * mm});
            skLineSegment(sketch, "E1724", {"start": v(-545.86, 206.64) * mm, "end": v(-545.7, 205.54) * mm});
            skLineSegment(sketch, "E1725", {"start": v(-545.7, 205.54) * mm, "end": v(-545.6, 204.42) * mm});
            skLineSegment(sketch, "E1726", {"start": v(-545.6, 204.42) * mm, "end": v(-545.56, 203.28) * mm});
            skLineSegment(sketch, "E1727", {"start": v(-545.56, 203.28) * mm, "end": v(-545.56, 202.13) * mm});
            skLineSegment(sketch, "E1728", {"start": v(-545.56, 202.13) * mm, "end": v(-545.62, 200.97) * mm});
            skLineSegment(sketch, "E1729", {"start": v(-545.62, 200.97) * mm, "end": v(-545.74, 199.79) * mm});
            skLineSegment(sketch, "E1730", {"start": v(-545.74, 199.79) * mm, "end": v(-545.92, 198.59) * mm});
            skLineSegment(sketch, "E1731", {"start": v(-545.92, 198.59) * mm, "end": v(-546.15, 197.37) * mm});
            skLineSegment(sketch, "E1732", {"start": v(-546.15, 197.37) * mm, "end": v(-546.45, 196.14) * mm});
            skLineSegment(sketch, "E1733", {"start": v(-546.45, 196.14) * mm, "end": v(-546.81, 194.88) * mm});
            skLineSegment(sketch, "E1734", {"start": v(-546.81, 194.88) * mm, "end": v(-547.24, 193.61) * mm});
            skLineSegment(sketch, "E1735", {"start": v(-547.24, 193.61) * mm, "end": v(-547.73, 192.32) * mm});
            skLineSegment(sketch, "E1736", {"start": v(-547.73, 192.32) * mm, "end": v(-548.54, 190.44) * mm});
            skLineSegment(sketch, "E1737", {"start": v(-548.54, 190.44) * mm, "end": v(-549.4, 188.67) * mm});
            skLineSegment(sketch, "E1738", {"start": v(-549.4, 188.67) * mm, "end": v(-550.32, 187) * mm});
            skLineSegment(sketch, "E1739", {"start": v(-550.32, 187) * mm, "end": v(-551.28, 185.43) * mm});
            skLineSegment(sketch, "E1740", {"start": v(-551.28, 185.43) * mm, "end": v(-552.3, 183.97) * mm});
            skLineSegment(sketch, "E1741", {"start": v(-552.3, 183.97) * mm, "end": v(-553.35, 182.6) * mm});
            skLineSegment(sketch, "E1742", {"start": v(-553.35, 182.6) * mm, "end": v(-554.45, 181.32) * mm});
            skLineSegment(sketch, "E1743", {"start": v(-554.45, 181.32) * mm, "end": v(-555.6, 180.13) * mm});
            skLineSegment(sketch, "E1744", {"start": v(-555.6, 180.13) * mm, "end": v(-556.8, 179.02) * mm});
            skLineSegment(sketch, "E1745", {"start": v(-556.8, 179.02) * mm, "end": v(-558.03, 178) * mm});
            skLineSegment(sketch, "E1746", {"start": v(-558.03, 178) * mm, "end": v(-559.3, 177.06) * mm});
            skLineSegment(sketch, "E1747", {"start": v(-559.3, 177.06) * mm, "end": v(-560.62, 176.2) * mm});
            skLineSegment(sketch, "E1748", {"start": v(-560.62, 176.2) * mm, "end": v(-561.97, 175.42) * mm});
            skLineSegment(sketch, "E1749", {"start": v(-561.97, 175.42) * mm, "end": v(-563.36, 174.7) * mm});
            skLineSegment(sketch, "E1750", {"start": v(-563.36, 174.7) * mm, "end": v(-564.78, 174.06) * mm});
            skLineSegment(sketch, "E1751", {"start": v(-564.78, 174.06) * mm, "end": v(-566.24, 173.47) * mm});
            skLineSegment(sketch, "E1752", {"start": v(-566.24, 173.47) * mm, "end": v(-567.73, 172.96) * mm});
            skLineSegment(sketch, "E1753", {"start": v(-567.73, 172.96) * mm, "end": v(-569.25, 172.5) * mm});
            skLineSegment(sketch, "E1754", {"start": v(-569.25, 172.5) * mm, "end": v(-570.8, 172.1) * mm});
            skLineSegment(sketch, "E1755", {"start": v(-570.8, 172.1) * mm, "end": v(-572.38, 171.74) * mm});
            skLineSegment(sketch, "E1756", {"start": v(-572.38, 171.74) * mm, "end": v(-574, 171.44) * mm});
            skLineSegment(sketch, "E1757", {"start": v(-574, 171.44) * mm, "end": v(-575.63, 171.2) * mm});
            skLineSegment(sketch, "E1758", {"start": v(-575.63, 171.2) * mm, "end": v(-577.28, 170.99) * mm});
            skLineSegment(sketch, "E1759", {"start": v(-577.28, 170.99) * mm, "end": v(-578.97, 170.82) * mm});
            skLineSegment(sketch, "E1760", {"start": v(-578.97, 170.82) * mm, "end": v(-580.67, 170.7) * mm});
            skLineSegment(sketch, "E1761", {"start": v(-580.67, 170.7) * mm, "end": v(-582.4, 170.6) * mm});
            skLineSegment(sketch, "E1762", {"start": v(-582.4, 170.6) * mm, "end": v(-584.14, 170.54) * mm});
            skLineSegment(sketch, "E1763", {"start": v(-584.14, 170.54) * mm, "end": v(-585.9, 170.5) * mm});
            skLineSegment(sketch, "E1764", {"start": v(-585.9, 170.5) * mm, "end": v(-587.68, 170.5) * mm});
            skLineSegment(sketch, "E1765", {"start": v(-587.68, 170.5) * mm, "end": v(-589.48, 170.52) * mm});
            skLineSegment(sketch, "E1766", {"start": v(-589.48, 170.52) * mm, "end": v(-591.29, 170.56) * mm});
            skLineSegment(sketch, "E1767", {"start": v(-591.29, 170.56) * mm, "end": v(-593.11, 170.62) * mm});
            skLineSegment(sketch, "E1768", {"start": v(-593.11, 170.62) * mm, "end": v(-594.68, 170.7) * mm});
            skLineSegment(sketch, "E1769", {"start": v(-594.68, 170.7) * mm, "end": v(-596.3, 170.86) * mm});
            skLineSegment(sketch, "E1770", {"start": v(-596.3, 170.86) * mm, "end": v(-597.98, 171.06) * mm});
            skLineSegment(sketch, "E1771", {"start": v(-597.98, 171.06) * mm, "end": v(-599.7, 171.27) * mm});
            skLineSegment(sketch, "E1772", {"start": v(-599.7, 171.27) * mm, "end": v(-601.44, 171.48) * mm});
            skLineSegment(sketch, "E1773", {"start": v(-601.44, 171.48) * mm, "end": v(-603.2, 171.67) * mm});
            skLineSegment(sketch, "E1774", {"start": v(-603.2, 171.67) * mm, "end": v(-604.95, 171.83) * mm});
            skLineSegment(sketch, "E1775", {"start": v(-604.95, 171.83) * mm, "end": v(-606.7, 171.91) * mm});
            skLineSegment(sketch, "E1776", {"start": v(-606.7, 171.91) * mm, "end": v(-608.43, 171.92) * mm});
            skLineSegment(sketch, "E1777", {"start": v(-608.43, 171.92) * mm, "end": v(-610.12, 171.82) * mm});
            skLineSegment(sketch, "E1778", {"start": v(-610.12, 171.82) * mm, "end": v(-611.77, 171.6) * mm});
            skLineSegment(sketch, "E1779", {"start": v(-611.77, 171.6) * mm, "end": v(-613.35, 171.22) * mm});
            skLineSegment(sketch, "E1780", {"start": v(-613.35, 171.22) * mm, "end": v(-614.87, 170.69) * mm});
            skLineSegment(sketch, "E1781", {"start": v(-614.87, 170.69) * mm, "end": v(-616.31, 169.97) * mm});
            skLineSegment(sketch, "E1782", {"start": v(-616.31, 169.97) * mm, "end": v(-617.66, 169.04) * mm});
            skLineSegment(sketch, "E1783", {"start": v(-617.66, 169.04) * mm, "end": v(-618.9, 167.88) * mm});
            skLineSegment(sketch, "E1784", {"start": v(-618.9, 167.88) * mm, "end": v(-620.01, 166.47) * mm});
            skLineSegment(sketch, "E1785", {"start": v(-620.01, 166.47) * mm, "end": v(-620.86, 165.2) * mm});
            skLineSegment(sketch, "E1786", {"start": v(-620.86, 165.2) * mm, "end": v(-621.63, 163.95) * mm});
            skLineSegment(sketch, "E1787", {"start": v(-621.63, 163.95) * mm, "end": v(-622.32, 162.73) * mm});
            skLineSegment(sketch, "E1788", {"start": v(-622.32, 162.73) * mm, "end": v(-622.94, 161.54) * mm});
            skLineSegment(sketch, "E1789", {"start": v(-622.94, 161.54) * mm, "end": v(-623.48, 160.38) * mm});
            skLineSegment(sketch, "E1790", {"start": v(-623.48, 160.38) * mm, "end": v(-623.95, 159.24) * mm});
            skLineSegment(sketch, "E1791", {"start": v(-623.95, 159.24) * mm, "end": v(-624.34, 158.13) * mm});
            skLineSegment(sketch, "E1792", {"start": v(-624.34, 158.13) * mm, "end": v(-624.67, 157.04) * mm});
            skLineSegment(sketch, "E1793", {"start": v(-624.67, 157.04) * mm, "end": v(-624.93, 155.98) * mm});
            skLineSegment(sketch, "E1794", {"start": v(-624.93, 155.98) * mm, "end": v(-625.13, 154.94) * mm});
            skLineSegment(sketch, "E1795", {"start": v(-625.13, 154.94) * mm, "end": v(-625.26, 153.93) * mm});
            skLineSegment(sketch, "E1796", {"start": v(-625.26, 153.93) * mm, "end": v(-625.32, 152.93) * mm});
            skLineSegment(sketch, "E1797", {"start": v(-625.32, 152.93) * mm, "end": v(-625.33, 151.96) * mm});
            skLineSegment(sketch, "E1798", {"start": v(-625.33, 151.96) * mm, "end": v(-625.27, 151.01) * mm});
            skLineSegment(sketch, "E1799", {"start": v(-625.27, 151.01) * mm, "end": v(-625.16, 150.08) * mm});
            skLineSegment(sketch, "E1800", {"start": v(-625.16, 150.08) * mm, "end": v(-625, 149.17) * mm});
            skLineSegment(sketch, "E1801", {"start": v(-625, 149.17) * mm, "end": v(-624.77, 148.28) * mm});
            skLineSegment(sketch, "E1802", {"start": v(-624.77, 148.28) * mm, "end": v(-624.5, 147.41) * mm});
            skLineSegment(sketch, "E1803", {"start": v(-624.5, 147.41) * mm, "end": v(-624.17, 146.56) * mm});
            skLineSegment(sketch, "E1804", {"start": v(-624.17, 146.56) * mm, "end": v(-623.8, 145.72) * mm});
            skLineSegment(sketch, "E1805", {"start": v(-623.8, 145.72) * mm, "end": v(-623.37, 144.9) * mm});
            skLineSegment(sketch, "E1806", {"start": v(-623.37, 144.9) * mm, "end": v(-622.9, 144.1) * mm});
            skLineSegment(sketch, "E1807", {"start": v(-622.9, 144.1) * mm, "end": v(-622.38, 143.3) * mm});
            skLineSegment(sketch, "E1808", {"start": v(-622.38, 143.3) * mm, "end": v(-621.83, 142.53) * mm});
            skLineSegment(sketch, "E1809", {"start": v(-621.83, 142.53) * mm, "end": v(-621.23, 141.76) * mm});
            skLineSegment(sketch, "E1810", {"start": v(-621.23, 141.76) * mm, "end": v(-620.59, 141.01) * mm});
            skLineSegment(sketch, "E1811", {"start": v(-620.59, 141.01) * mm, "end": v(-619.91, 140.28) * mm});
            skLineSegment(sketch, "E1812", {"start": v(-619.91, 140.28) * mm, "end": v(-619.2, 139.55) * mm});
            skLineSegment(sketch, "E1813", {"start": v(-619.2, 139.55) * mm, "end": v(-618.45, 138.84) * mm});
            skLineSegment(sketch, "E1814", {"start": v(-618.45, 138.84) * mm, "end": v(-617.67, 138.13) * mm});
            skLineSegment(sketch, "E1815", {"start": v(-617.67, 138.13) * mm, "end": v(-616.86, 137.44) * mm});
            skLineSegment(sketch, "E1816", {"start": v(-616.86, 137.44) * mm, "end": v(-616.01, 136.75) * mm});
            skLineSegment(sketch, "E1817", {"start": v(-616.01, 136.75) * mm, "end": v(-615.14, 136.07) * mm});
            skLineSegment(sketch, "E1818", {"start": v(-615.14, 136.07) * mm, "end": v(-614.25, 135.4) * mm});
            skLineSegment(sketch, "E1819", {"start": v(-614.25, 135.4) * mm, "end": v(-613.32, 134.74) * mm});
            skLineSegment(sketch, "E1820", {"start": v(-613.32, 134.74) * mm, "end": v(-612.38, 134.08) * mm});
            skLineSegment(sketch, "E1821", {"start": v(-612.38, 134.08) * mm, "end": v(-611.41, 133.43) * mm});
            skLineSegment(sketch, "E1822", {"start": v(-611.41, 133.43) * mm, "end": v(-610.43, 132.78) * mm});
            skLineSegment(sketch, "E1823", {"start": v(-610.43, 132.78) * mm, "end": v(-609.42, 132.14) * mm});
            skLineSegment(sketch, "E1824", {"start": v(-609.42, 132.14) * mm, "end": v(-608.4, 131.5) * mm});
            skLineSegment(sketch, "E1825", {"start": v(-608.4, 131.5) * mm, "end": v(-607.36, 130.86) * mm});
            skLineSegment(sketch, "E1826", {"start": v(-607.36, 130.86) * mm, "end": v(-606.31, 130.23) * mm});
            skLineSegment(sketch, "E1827", {"start": v(-606.31, 130.23) * mm, "end": v(-605.25, 129.6) * mm});
            skLineSegment(sketch, "E1828", {"start": v(-605.25, 129.6) * mm, "end": v(-604.18, 128.96) * mm});
            skLineSegment(sketch, "E1829", {"start": v(-604.18, 128.96) * mm, "end": v(-603.1, 128.33) * mm});
            skLineSegment(sketch, "E1830", {"start": v(-603.1, 128.33) * mm, "end": v(-602.02, 127.7) * mm});
            skLineSegment(sketch, "E1831", {"start": v(-602.02, 127.7) * mm, "end": v(-600.92, 127.06) * mm});
            skLineSegment(sketch, "E1832", {"start": v(-600.92, 127.06) * mm, "end": v(-599.83, 126.42) * mm});
            skLineSegment(sketch, "E1833", {"start": v(-599.83, 126.42) * mm, "end": v(-598.73, 125.78) * mm});
            skLineSegment(sketch, "E1834", {"start": v(-598.73, 125.78) * mm, "end": v(-597.64, 125.14) * mm});
            skLineSegment(sketch, "E1835", {"start": v(-597.64, 125.14) * mm, "end": v(-596.54, 124.5) * mm});
            skLineSegment(sketch, "E1836", {"start": v(-596.54, 124.5) * mm, "end": v(-595.45, 123.84) * mm});
            skLineSegment(sketch, "E1837", {"start": v(-595.45, 123.84) * mm, "end": v(-594.36, 123.18) * mm});
            skLineSegment(sketch, "E1838", {"start": v(-594.36, 123.18) * mm, "end": v(-593.28, 122.52) * mm});
            skLineSegment(sketch, "E1839", {"start": v(-593.28, 122.52) * mm, "end": v(-592.21, 121.85) * mm});
            skLineSegment(sketch, "E1840", {"start": v(-592.21, 121.85) * mm, "end": v(-591.15, 121.17) * mm});
            skLineSegment(sketch, "E1841", {"start": v(-591.15, 121.17) * mm, "end": v(-590.1, 120.48) * mm});
            skLineSegment(sketch, "E1842", {"start": v(-590.1, 120.48) * mm, "end": v(-589.06, 119.79) * mm});
            skLineSegment(sketch, "E1843", {"start": v(-589.06, 119.79) * mm, "end": v(-588.04, 119.09) * mm});
            skLineSegment(sketch, "E1844", {"start": v(-588.04, 119.09) * mm, "end": v(-587.03, 118.37) * mm});
            skLineSegment(sketch, "E1845", {"start": v(-587.03, 118.37) * mm, "end": v(-586.04, 117.65) * mm});
            skLineSegment(sketch, "E1846", {"start": v(-586.04, 117.65) * mm, "end": v(-585.08, 116.9) * mm});
            skLineSegment(sketch, "E1847", {"start": v(-585.08, 116.9) * mm, "end": v(-584.13, 116.16) * mm});
            skLineSegment(sketch, "E1848", {"start": v(-584.13, 116.16) * mm, "end": v(-583.2, 115.4) * mm});
            skLineSegment(sketch, "E1849", {"start": v(-583.2, 115.4) * mm, "end": v(-582.3, 114.62) * mm});
            skLineSegment(sketch, "E1850", {"start": v(-582.3, 114.62) * mm, "end": v(-581.43, 113.83) * mm});
            skLineSegment(sketch, "E1851", {"start": v(-581.43, 113.83) * mm, "end": v(-580.59, 113.03) * mm});
            skLineSegment(sketch, "E1852", {"start": v(-580.59, 113.03) * mm, "end": v(-579.77, 112.2) * mm});
            skLineSegment(sketch, "E1853", {"start": v(-579.77, 112.2) * mm, "end": v(-578.99, 111.37) * mm});
            skLineSegment(sketch, "E1854", {"start": v(-578.99, 111.37) * mm, "end": v(-578.24, 110.52) * mm});
            skLineSegment(sketch, "E1855", {"start": v(-578.24, 110.52) * mm, "end": v(-577.52, 109.65) * mm});
            skLineSegment(sketch, "E1856", {"start": v(-577.52, 109.65) * mm, "end": v(-576.84, 108.76) * mm});
            skLineSegment(sketch, "E1857", {"start": v(-576.84, 108.76) * mm, "end": v(-576.2, 107.85) * mm});
            skLineSegment(sketch, "E1858", {"start": v(-576.2, 107.85) * mm, "end": v(-575.6, 106.92) * mm});
            skLineSegment(sketch, "E1859", {"start": v(-575.6, 106.92) * mm, "end": v(-575.03, 105.97) * mm});
            skLineSegment(sketch, "E1860", {"start": v(-575.03, 105.97) * mm, "end": v(-574.51, 105) * mm});
            skLineSegment(sketch, "E1861", {"start": v(-574.51, 105) * mm, "end": v(-574.04, 104.01) * mm});
            skLineSegment(sketch, "E1862", {"start": v(-574.04, 104.01) * mm, "end": v(-573.6, 103) * mm});
            skLineSegment(sketch, "E1863", {"start": v(-573.6, 103) * mm, "end": v(-573.23, 101.96) * mm});
            skLineSegment(sketch, "E1864", {"start": v(-573.23, 101.96) * mm, "end": v(-572.9, 100.9) * mm});
            skLineSegment(sketch, "E1865", {"start": v(-572.9, 100.9) * mm, "end": v(-572.61, 99.82) * mm});
            skLineSegment(sketch, "E1866", {"start": v(-572.61, 99.82) * mm, "end": v(-572.39, 98.7) * mm});
            skLineSegment(sketch, "E1867", {"start": v(-572.39, 98.7) * mm, "end": v(-572.21, 97.57) * mm});
            skLineSegment(sketch, "E1868", {"start": v(-572.21, 97.57) * mm, "end": v(-572.1, 96.4) * mm});
            skLineSegment(sketch, "E1869", {"start": v(-572.1, 96.4) * mm, "end": v(-572.04, 95.22) * mm});
            skLineSegment(sketch, "E1870", {"start": v(-572.04, 95.22) * mm, "end": v(-572.04, 94) * mm});
            skLineSegment(sketch, "E1871", {"start": v(-572.04, 94) * mm, "end": v(-572.1, 92.76) * mm});
            skLineSegment(sketch, "E1872", {"start": v(-572.1, 92.76) * mm, "end": v(-572.27, 90.95) * mm});
            skLineSegment(sketch, "E1873", {"start": v(-572.27, 90.95) * mm, "end": v(-572.54, 89.2) * mm});
            skLineSegment(sketch, "E1874", {"start": v(-572.54, 89.2) * mm, "end": v(-572.89, 87.5) * mm});
            skLineSegment(sketch, "E1875", {"start": v(-572.89, 87.5) * mm, "end": v(-573.32, 85.84) * mm});
            skLineSegment(sketch, "E1876", {"start": v(-573.32, 85.84) * mm, "end": v(-573.83, 84.23) * mm});
            skLineSegment(sketch, "E1877", {"start": v(-573.83, 84.23) * mm, "end": v(-574.42, 82.67) * mm});
            skLineSegment(sketch, "E1878", {"start": v(-574.42, 82.67) * mm, "end": v(-575.08, 81.15) * mm});
            skLineSegment(sketch, "E1879", {"start": v(-575.08, 81.15) * mm, "end": v(-575.81, 79.69) * mm});
            skLineSegment(sketch, "E1880", {"start": v(-575.81, 79.69) * mm, "end": v(-576.62, 78.27) * mm});
            skLineSegment(sketch, "E1881", {"start": v(-576.62, 78.27) * mm, "end": v(-577.48, 76.9) * mm});
            skLineSegment(sketch, "E1882", {"start": v(-577.48, 76.9) * mm, "end": v(-578.41, 75.58) * mm});
            skLineSegment(sketch, "E1883", {"start": v(-578.41, 75.58) * mm, "end": v(-579.4, 74.3) * mm});
            skLineSegment(sketch, "E1884", {"start": v(-579.4, 74.3) * mm, "end": v(-580.46, 73.08) * mm});
            skLineSegment(sketch, "E1885", {"start": v(-580.46, 73.08) * mm, "end": v(-581.56, 71.9) * mm});
            skLineSegment(sketch, "E1886", {"start": v(-581.56, 71.9) * mm, "end": v(-582.72, 70.78) * mm});
            skLineSegment(sketch, "E1887", {"start": v(-582.72, 70.78) * mm, "end": v(-583.93, 69.7) * mm});
            skLineSegment(sketch, "E1888", {"start": v(-583.93, 69.7) * mm, "end": v(-585.19, 68.67) * mm});
            skLineSegment(sketch, "E1889", {"start": v(-585.19, 68.67) * mm, "end": v(-586.49, 67.7) * mm});
            skLineSegment(sketch, "E1890", {"start": v(-586.49, 67.7) * mm, "end": v(-587.83, 66.76) * mm});
            skLineSegment(sketch, "E1891", {"start": v(-587.83, 66.76) * mm, "end": v(-589.21, 65.87) * mm});
            skLineSegment(sketch, "E1892", {"start": v(-589.21, 65.87) * mm, "end": v(-590.63, 65.04) * mm});
            skLineSegment(sketch, "E1893", {"start": v(-590.63, 65.04) * mm, "end": v(-592.08, 64.25) * mm});
            skLineSegment(sketch, "E1894", {"start": v(-592.08, 64.25) * mm, "end": v(-593.57, 63.52) * mm});
            skLineSegment(sketch, "E1895", {"start": v(-593.57, 63.52) * mm, "end": v(-595.08, 62.83) * mm});
            skLineSegment(sketch, "E1896", {"start": v(-595.08, 62.83) * mm, "end": v(-596.62, 62.2) * mm});
            skLineSegment(sketch, "E1897", {"start": v(-596.62, 62.2) * mm, "end": v(-598.19, 61.6) * mm});
            skLineSegment(sketch, "E1898", {"start": v(-598.19, 61.6) * mm, "end": v(-599.77, 61.06) * mm});
            skLineSegment(sketch, "E1899", {"start": v(-599.77, 61.06) * mm, "end": v(-601.37, 60.57) * mm});
            skLineSegment(sketch, "E1900", {"start": v(-601.37, 60.57) * mm, "end": v(-602.99, 60.13) * mm});
            skLineSegment(sketch, "E1901", {"start": v(-602.99, 60.13) * mm, "end": v(-604.62, 59.74) * mm});
            skLineSegment(sketch, "E1902", {"start": v(-604.62, 59.74) * mm, "end": v(-606.26, 59.4) * mm});
            skLineSegment(sketch, "E1903", {"start": v(-606.26, 59.4) * mm, "end": v(-607.9, 59.1) * mm});
            skLineSegment(sketch, "E1904", {"start": v(-607.9, 59.1) * mm, "end": v(-609.56, 58.86) * mm});
            skLineSegment(sketch, "E1905", {"start": v(-609.56, 58.86) * mm, "end": v(-611.22, 58.67) * mm});
            skLineSegment(sketch, "E1906", {"start": v(-611.22, 58.67) * mm, "end": v(-612.66, 58.54) * mm});
            skLineSegment(sketch, "E1907", {"start": v(-612.66, 58.54) * mm, "end": v(-614.17, 58.45) * mm});
            skLineSegment(sketch, "E1908", {"start": v(-614.17, 58.45) * mm, "end": v(-615.75, 58.38) * mm});
            skLineSegment(sketch, "E1909", {"start": v(-615.75, 58.38) * mm, "end": v(-617.39, 58.32) * mm});
            skLineSegment(sketch, "E1910", {"start": v(-617.39, 58.32) * mm, "end": v(-619.06, 58.25) * mm});
            skLineSegment(sketch, "E1911", {"start": v(-619.06, 58.25) * mm, "end": v(-620.76, 58.17) * mm});
            skLineSegment(sketch, "E1912", {"start": v(-620.76, 58.17) * mm, "end": v(-622.48, 58.07) * mm});
            skLineSegment(sketch, "E1913", {"start": v(-622.48, 58.07) * mm, "end": v(-624.2, 57.93) * mm});
            skLineSegment(sketch, "E1914", {"start": v(-624.2, 57.93) * mm, "end": v(-625.9, 57.73) * mm});
            skLineSegment(sketch, "E1915", {"start": v(-625.9, 57.73) * mm, "end": v(-627.59, 57.48) * mm});
            skLineSegment(sketch, "E1916", {"start": v(-627.59, 57.48) * mm, "end": v(-629.24, 57.16) * mm});
            skLineSegment(sketch, "E1917", {"start": v(-629.24, 57.16) * mm, "end": v(-630.84, 56.75) * mm});
            skLineSegment(sketch, "E1918", {"start": v(-630.84, 56.75) * mm, "end": v(-632.38, 56.25) * mm});
            skLineSegment(sketch, "E1919", {"start": v(-632.38, 56.25) * mm, "end": v(-633.84, 55.64) * mm});
            skLineSegment(sketch, "E1920", {"start": v(-633.84, 55.64) * mm, "end": v(-635.22, 54.91) * mm});
            skLineSegment(sketch, "E1921", {"start": v(-635.22, 54.91) * mm, "end": v(-636.5, 54.05) * mm});
            skLineSegment(sketch, "E1922", {"start": v(-636.5, 54.05) * mm, "end": v(-637.67, 53.06) * mm});
            skLineSegment(sketch, "E1923", {"start": v(-637.67, 53.06) * mm, "end": v(-638.7, 51.9) * mm});
            skLineSegment(sketch, "E1924", {"start": v(-638.7, 51.9) * mm, "end": v(-639.62, 50.6) * mm});
            skLineSegment(sketch, "E1925", {"start": v(-639.62, 50.6) * mm, "end": v(-640.37, 49.11) * mm});
            skLineSegment(sketch, "E1926", {"start": v(-640.37, 49.11) * mm, "end": v(-640.9, 47.8) * mm});
            skLineSegment(sketch, "E1927", {"start": v(-640.9, 47.8) * mm, "end": v(-641.38, 46.54) * mm});
            skLineSegment(sketch, "E1928", {"start": v(-641.38, 46.54) * mm, "end": v(-641.79, 45.31) * mm});
            skLineSegment(sketch, "E1929", {"start": v(-641.79, 45.31) * mm, "end": v(-642.13, 44.12) * mm});
            skLineSegment(sketch, "E1930", {"start": v(-642.13, 44.12) * mm, "end": v(-642.42, 42.97) * mm});
            skLineSegment(sketch, "E1931", {"start": v(-642.42, 42.97) * mm, "end": v(-642.64, 41.84) * mm});
            skLineSegment(sketch, "E1932", {"start": v(-642.64, 41.84) * mm, "end": v(-642.8, 40.75) * mm});
            skLineSegment(sketch, "E1933", {"start": v(-642.8, 40.75) * mm, "end": v(-642.92, 39.7) * mm});
            skLineSegment(sketch, "E1934", {"start": v(-642.92, 39.7) * mm, "end": v(-642.97, 38.67) * mm});
            skLineSegment(sketch, "E1935", {"start": v(-642.97, 38.67) * mm, "end": v(-642.97, 37.68) * mm});
            skLineSegment(sketch, "E1936", {"start": v(-642.97, 37.68) * mm, "end": v(-642.92, 36.71) * mm});
            skLineSegment(sketch, "E1937", {"start": v(-642.92, 36.71) * mm, "end": v(-642.82, 35.78) * mm});
            skLineSegment(sketch, "E1938", {"start": v(-642.82, 35.78) * mm, "end": v(-642.66, 34.87) * mm});
            skLineSegment(sketch, "E1939", {"start": v(-642.66, 34.87) * mm, "end": v(-642.46, 34) * mm});
            skLineSegment(sketch, "E1940", {"start": v(-642.46, 34) * mm, "end": v(-642.2, 33.14) * mm});
            skLineSegment(sketch, "E1941", {"start": v(-642.2, 33.14) * mm, "end": v(-641.9, 32.32) * mm});
            skLineSegment(sketch, "E1942", {"start": v(-641.9, 32.32) * mm, "end": v(-641.56, 31.52) * mm});
            skLineSegment(sketch, "E1943", {"start": v(-641.56, 31.52) * mm, "end": v(-641.17, 30.74) * mm});
            skLineSegment(sketch, "E1944", {"start": v(-641.17, 30.74) * mm, "end": v(-640.74, 30) * mm});
            skLineSegment(sketch, "E1945", {"start": v(-640.74, 30) * mm, "end": v(-640.26, 29.26) * mm});
            skLineSegment(sketch, "E1946", {"start": v(-640.26, 29.26) * mm, "end": v(-639.75, 28.56) * mm});
            skLineSegment(sketch, "E1947", {"start": v(-639.75, 28.56) * mm, "end": v(-639.2, 27.87) * mm});
            skLineSegment(sketch, "E1948", {"start": v(-639.2, 27.87) * mm, "end": v(-638.6, 27.2) * mm});
            skLineSegment(sketch, "E1949", {"start": v(-638.6, 27.2) * mm, "end": v(-637.97, 26.56) * mm});
            skLineSegment(sketch, "E1950", {"start": v(-637.97, 26.56) * mm, "end": v(-637.3, 25.93) * mm});
            skLineSegment(sketch, "E1951", {"start": v(-637.3, 25.93) * mm, "end": v(-636.61, 25.32) * mm});
            skLineSegment(sketch, "E1952", {"start": v(-636.61, 25.32) * mm, "end": v(-635.88, 24.73) * mm});
            skLineSegment(sketch, "E1953", {"start": v(-635.88, 24.73) * mm, "end": v(-635.12, 24.16) * mm});
            skLineSegment(sketch, "E1954", {"start": v(-635.12, 24.16) * mm, "end": v(-634.33, 23.6) * mm});
            skLineSegment(sketch, "E1955", {"start": v(-634.33, 23.6) * mm, "end": v(-633.5, 23.05) * mm});
            skLineSegment(sketch, "E1956", {"start": v(-633.5, 23.05) * mm, "end": v(-632.66, 22.52) * mm});
            skLineSegment(sketch, "E1957", {"start": v(-632.66, 22.52) * mm, "end": v(-631.78, 22) * mm});
            skLineSegment(sketch, "E1958", {"start": v(-631.78, 22) * mm, "end": v(-630.88, 21.5) * mm});
            skLineSegment(sketch, "E1959", {"start": v(-630.88, 21.5) * mm, "end": v(-629.96, 21) * mm});
            skLineSegment(sketch, "E1960", {"start": v(-629.96, 21) * mm, "end": v(-629.01, 20.52) * mm});
            skLineSegment(sketch, "E1961", {"start": v(-629.01, 20.52) * mm, "end": v(-628.04, 20.04) * mm});
            skLineSegment(sketch, "E1962", {"start": v(-628.04, 20.04) * mm, "end": v(-627.06, 19.58) * mm});
            skLineSegment(sketch, "E1963", {"start": v(-627.06, 19.58) * mm, "end": v(-626.05, 19.12) * mm});
            skLineSegment(sketch, "E1964", {"start": v(-626.05, 19.12) * mm, "end": v(-625.03, 18.67) * mm});
            skLineSegment(sketch, "E1965", {"start": v(-625.03, 18.67) * mm, "end": v(-623.99, 18.23) * mm});
            skLineSegment(sketch, "E1966", {"start": v(-623.99, 18.23) * mm, "end": v(-622.93, 17.8) * mm});
            skLineSegment(sketch, "E1967", {"start": v(-622.93, 17.8) * mm, "end": v(-621.86, 17.36) * mm});
            skLineSegment(sketch, "E1968", {"start": v(-621.86, 17.36) * mm, "end": v(-620.78, 16.93) * mm});
            skLineSegment(sketch, "E1969", {"start": v(-620.78, 16.93) * mm, "end": v(-619.69, 16.5) * mm});
            skLineSegment(sketch, "E1970", {"start": v(-619.69, 16.5) * mm, "end": v(-618.58, 16.08) * mm});
            skLineSegment(sketch, "E1971", {"start": v(-618.58, 16.08) * mm, "end": v(-617.47, 15.66) * mm});
            skLineSegment(sketch, "E1972", {"start": v(-617.47, 15.66) * mm, "end": v(-616.35, 15.24) * mm});
            skLineSegment(sketch, "E1973", {"start": v(-616.35, 15.24) * mm, "end": v(-615.23, 14.82) * mm});
            skLineSegment(sketch, "E1974", {"start": v(-615.23, 14.82) * mm, "end": v(-614.1, 14.4) * mm});
            skLineSegment(sketch, "E1975", {"start": v(-614.1, 14.4) * mm, "end": v(-612.97, 13.98) * mm});
            skLineSegment(sketch, "E1976", {"start": v(-612.97, 13.98) * mm, "end": v(-611.83, 13.55) * mm});
            skLineSegment(sketch, "E1977", {"start": v(-611.83, 13.55) * mm, "end": v(-610.7, 13.13) * mm});
            skLineSegment(sketch, "E1978", {"start": v(-610.7, 13.13) * mm, "end": v(-609.56, 12.7) * mm});
            skLineSegment(sketch, "E1979", {"start": v(-609.56, 12.7) * mm, "end": v(-608.42, 12.26) * mm});
            skLineSegment(sketch, "E1980", {"start": v(-608.42, 12.26) * mm, "end": v(-607.3, 11.81) * mm});
            skLineSegment(sketch, "E1981", {"start": v(-607.3, 11.81) * mm, "end": v(-606.16, 11.36) * mm});
            skLineSegment(sketch, "E1982", {"start": v(-606.16, 11.36) * mm, "end": v(-605.04, 10.9) * mm});
            skLineSegment(sketch, "E1983", {"start": v(-605.04, 10.9) * mm, "end": v(-603.93, 10.44) * mm});
            skLineSegment(sketch, "E1984", {"start": v(-603.93, 10.44) * mm, "end": v(-602.82, 9.97) * mm});
            skLineSegment(sketch, "E1985", {"start": v(-602.82, 9.97) * mm, "end": v(-601.72, 9.49) * mm});
            skLineSegment(sketch, "E1986", {"start": v(-601.72, 9.49) * mm, "end": v(-600.63, 9) * mm});
            skLineSegment(sketch, "E1987", {"start": v(-600.63, 9) * mm, "end": v(-599.56, 8.49) * mm});
            skLineSegment(sketch, "E1988", {"start": v(-599.56, 8.49) * mm, "end": v(-598.5, 7.97) * mm});
            skLineSegment(sketch, "E1989", {"start": v(-598.5, 7.97) * mm, "end": v(-597.45, 7.44) * mm});
            skLineSegment(sketch, "E1990", {"start": v(-597.45, 7.44) * mm, "end": v(-596.41, 6.9) * mm});
            skLineSegment(sketch, "E1991", {"start": v(-596.41, 6.9) * mm, "end": v(-595.4, 6.33) * mm});
            skLineSegment(sketch, "E1992", {"start": v(-595.4, 6.33) * mm, "end": v(-594.4, 5.76) * mm});
            skLineSegment(sketch, "E1993", {"start": v(-594.4, 5.76) * mm, "end": v(-593.42, 5.17) * mm});
            skLineSegment(sketch, "E1994", {"start": v(-593.42, 5.17) * mm, "end": v(-592.46, 4.56) * mm});
            skLineSegment(sketch, "E1995", {"start": v(-592.46, 4.56) * mm, "end": v(-591.52, 3.94) * mm});
            skLineSegment(sketch, "E1996", {"start": v(-591.52, 3.94) * mm, "end": v(-590.61, 3.3) * mm});
            skLineSegment(sketch, "E1997", {"start": v(-590.61, 3.3) * mm, "end": v(-589.72, 2.63) * mm});
            skLineSegment(sketch, "E1998", {"start": v(-589.72, 2.63) * mm, "end": v(-588.86, 1.94) * mm});
            skLineSegment(sketch, "E1999", {"start": v(-588.86, 1.94) * mm, "end": v(-588.02, 1.24) * mm});
            skLineSegment(sketch, "E2000", {"start": v(-588.02, 1.24) * mm, "end": v(-587.22, 0.5) * mm});
            skLineSegment(sketch, "E2001", {"start": v(-587.22, 0.5) * mm, "end": v(-586.44, -0.24) * mm});
            skLineSegment(sketch, "E2002", {"start": v(-586.44, -0.24) * mm, "end": v(-585.69, -1.02) * mm});
            skLineSegment(sketch, "E2003", {"start": v(-585.69, -1.02) * mm, "end": v(-584.97, -1.81) * mm});
            skLineSegment(sketch, "E2004", {"start": v(-584.97, -1.81) * mm, "end": v(-584.3, -2.64) * mm});
            skLineSegment(sketch, "E2005", {"start": v(-584.3, -2.64) * mm, "end": v(-583.65, -3.49) * mm});
            skLineSegment(sketch, "E2006", {"start": v(-583.65, -3.49) * mm, "end": v(-583.03, -4.36) * mm});
            skLineSegment(sketch, "E2007", {"start": v(-583.03, -4.36) * mm, "end": v(-582.46, -5.27) * mm});
            skLineSegment(sketch, "E2008", {"start": v(-582.46, -5.27) * mm, "end": v(-581.92, -6.2) * mm});
            skLineSegment(sketch, "E2009", {"start": v(-581.92, -6.2) * mm, "end": v(-581.43, -7.16) * mm});
            skLineSegment(sketch, "E2010", {"start": v(-581.43, -7.16) * mm, "end": v(-580.97, -8.16) * mm});
            skLineSegment(sketch, "E2011", {"start": v(-580.97, -8.16) * mm, "end": v(-580.56, -9.18) * mm});
            skLineSegment(sketch, "E2012", {"start": v(-580.56, -9.18) * mm, "end": v(-580.2, -10.24) * mm});
            skLineSegment(sketch, "E2013", {"start": v(-580.2, -10.24) * mm, "end": v(-579.87, -11.32) * mm});
            skLineSegment(sketch, "E2014", {"start": v(-579.87, -11.32) * mm, "end": v(-579.59, -12.44) * mm});
            skLineSegment(sketch, "E2015", {"start": v(-579.59, -12.44) * mm, "end": v(-579.36, -13.6) * mm});
            skLineSegment(sketch, "E2016", {"start": v(-579.36, -13.6) * mm, "end": v(-579.18, -14.79) * mm});
            skLineSegment(sketch, "E2017", {"start": v(-579.18, -14.79) * mm, "end": v(-579.04, -16.02) * mm});
            skLineSegment(sketch, "E2018", {"start": v(-579.04, -16.02) * mm, "end": v(-578.96, -17.28) * mm});
            skLineSegment(sketch, "E2019", {"start": v(-578.96, -17.28) * mm, "end": v(-578.93, -18.58) * mm});
            skLineSegment(sketch, "E2020", {"start": v(-578.93, -18.58) * mm, "end": v(-578.96, -19.92) * mm});
            skLineSegment(sketch, "E2021", {"start": v(-578.96, -19.92) * mm, "end": v(-579.04, -21.3) * mm});
            skLineSegment(sketch, "E2022", {"start": v(-579.04, -21.3) * mm, "end": v(-579.19, -22.82) * mm});
            skLineSegment(sketch, "E2023", {"start": v(-579.19, -22.82) * mm, "end": v(-579.4, -24.28) * mm});
            skLineSegment(sketch, "E2024", {"start": v(-579.4, -24.28) * mm, "end": v(-579.66, -25.7) * mm});
            skLineSegment(sketch, "E2025", {"start": v(-579.66, -25.7) * mm, "end": v(-579.99, -27.06) * mm});
            skLineSegment(sketch, "E2026", {"start": v(-579.99, -27.06) * mm, "end": v(-580.37, -28.37) * mm});
            skLineSegment(sketch, "E2027", {"start": v(-580.37, -28.37) * mm, "end": v(-580.8, -29.63) * mm});
            skLineSegment(sketch, "E2028", {"start": v(-580.8, -29.63) * mm, "end": v(-581.28, -30.84) * mm});
            skLineSegment(sketch, "E2029", {"start": v(-581.28, -30.84) * mm, "end": v(-581.8, -32) * mm});
            skLineSegment(sketch, "E2030", {"start": v(-581.8, -32) * mm, "end": v(-582.39, -33.12) * mm});
            skLineSegment(sketch, "E2031", {"start": v(-582.39, -33.12) * mm, "end": v(-583, -34.2) * mm});
            skLineSegment(sketch, "E2032", {"start": v(-583, -34.2) * mm, "end": v(-583.68, -35.23) * mm});
            skLineSegment(sketch, "E2033", {"start": v(-583.68, -35.23) * mm, "end": v(-584.39, -36.23) * mm});
            skLineSegment(sketch, "E2034", {"start": v(-584.39, -36.23) * mm, "end": v(-585.14, -37.18) * mm});
            skLineSegment(sketch, "E2035", {"start": v(-585.14, -37.18) * mm, "end": v(-585.93, -38.1) * mm});
            skLineSegment(sketch, "E2036", {"start": v(-585.93, -38.1) * mm, "end": v(-586.75, -38.98) * mm});
            skLineSegment(sketch, "E2037", {"start": v(-586.75, -38.98) * mm, "end": v(-587.61, -39.82) * mm});
            skLineSegment(sketch, "E2038", {"start": v(-587.61, -39.82) * mm, "end": v(-588.5, -40.63) * mm});
            skLineSegment(sketch, "E2039", {"start": v(-588.5, -40.63) * mm, "end": v(-589.43, -41.41) * mm});
            skLineSegment(sketch, "E2040", {"start": v(-589.43, -41.41) * mm, "end": v(-590.39, -42.16) * mm});
            skLineSegment(sketch, "E2041", {"start": v(-590.39, -42.16) * mm, "end": v(-591.37, -42.88) * mm});
            skLineSegment(sketch, "E2042", {"start": v(-591.37, -42.88) * mm, "end": v(-592.38, -43.58) * mm});
            skLineSegment(sketch, "E2043", {"start": v(-592.38, -43.58) * mm, "end": v(-593.42, -44.24) * mm});
            skLineSegment(sketch, "E2044", {"start": v(-593.42, -44.24) * mm, "end": v(-594.48, -44.89) * mm});
            skLineSegment(sketch, "E2045", {"start": v(-594.48, -44.89) * mm, "end": v(-595.56, -45.5) * mm});
            skLineSegment(sketch, "E2046", {"start": v(-595.56, -45.5) * mm, "end": v(-596.66, -46.1) * mm});
            skLineSegment(sketch, "E2047", {"start": v(-596.66, -46.1) * mm, "end": v(-597.77, -46.68) * mm});
            skLineSegment(sketch, "E2048", {"start": v(-597.77, -46.68) * mm, "end": v(-598.9, -47.24) * mm});
            skLineSegment(sketch, "E2049", {"start": v(-598.9, -47.24) * mm, "end": v(-600.05, -47.78) * mm});
            skLineSegment(sketch, "E2050", {"start": v(-600.05, -47.78) * mm, "end": v(-601.21, -48.31) * mm});
            skLineSegment(sketch, "E2051", {"start": v(-601.21, -48.31) * mm, "end": v(-602.38, -48.82) * mm});
            skLineSegment(sketch, "E2052", {"start": v(-602.38, -48.82) * mm, "end": v(-603.56, -49.32) * mm});
            skLineSegment(sketch, "E2053", {"start": v(-603.56, -49.32) * mm, "end": v(-604.75, -49.81) * mm});
            skLineSegment(sketch, "E2054", {"start": v(-604.75, -49.81) * mm, "end": v(-605.94, -50.29) * mm});
            skLineSegment(sketch, "E2055", {"start": v(-605.94, -50.29) * mm, "end": v(-607.14, -50.76) * mm});
            skLineSegment(sketch, "E2056", {"start": v(-607.14, -50.76) * mm, "end": v(-608.34, -51.22) * mm});
            skLineSegment(sketch, "E2057", {"start": v(-608.34, -51.22) * mm, "end": v(-609.54, -51.68) * mm});
            skLineSegment(sketch, "E2058", {"start": v(-609.54, -51.68) * mm, "end": v(-610.73, -52.13) * mm});
            skLineSegment(sketch, "E2059", {"start": v(-610.73, -52.13) * mm, "end": v(-611.93, -52.59) * mm});
            skLineSegment(sketch, "E2060", {"start": v(-611.93, -52.59) * mm, "end": v(-613.12, -53.04) * mm});
            skLineSegment(sketch, "E2061", {"start": v(-613.12, -53.04) * mm, "end": v(-614.3, -53.49) * mm});
            skLineSegment(sketch, "E2062", {"start": v(-614.3, -53.49) * mm, "end": v(-615.48, -53.94) * mm});
            skLineSegment(sketch, "E2063", {"start": v(-615.48, -53.94) * mm, "end": v(-616.64, -54.4) * mm});
            skLineSegment(sketch, "E2064", {"start": v(-616.64, -54.4) * mm, "end": v(-617.8, -54.86) * mm});
            skLineSegment(sketch, "E2065", {"start": v(-617.8, -54.86) * mm, "end": v(-618.93, -55.33) * mm});
            skLineSegment(sketch, "E2066", {"start": v(-618.93, -55.33) * mm, "end": v(-620.06, -55.8) * mm});
            skLineSegment(sketch, "E2067", {"start": v(-620.06, -55.8) * mm, "end": v(-621.17, -56.29) * mm});
            skLineSegment(sketch, "E2068", {"start": v(-621.17, -56.29) * mm, "end": v(-622.25, -56.78) * mm});
            skLineSegment(sketch, "E2069", {"start": v(-622.25, -56.78) * mm, "end": v(-623.32, -57.3) * mm});
            skLineSegment(sketch, "E2070", {"start": v(-623.32, -57.3) * mm, "end": v(-624.37, -57.81) * mm});
            skLineSegment(sketch, "E2071", {"start": v(-624.37, -57.81) * mm, "end": v(-625.39, -58.35) * mm});
            skLineSegment(sketch, "E2072", {"start": v(-625.39, -58.35) * mm, "end": v(-626.38, -58.9) * mm});
            skLineSegment(sketch, "E2073", {"start": v(-626.38, -58.9) * mm, "end": v(-627.35, -59.48) * mm});
            skLineSegment(sketch, "E2074", {"start": v(-627.35, -59.48) * mm, "end": v(-628.3, -60.07) * mm});
            skLineSegment(sketch, "E2075", {"start": v(-628.3, -60.07) * mm, "end": v(-629.2, -60.68) * mm});
            skLineSegment(sketch, "E2076", {"start": v(-629.2, -60.68) * mm, "end": v(-630.08, -61.32) * mm});
            skLineSegment(sketch, "E2077", {"start": v(-630.08, -61.32) * mm, "end": v(-630.92, -61.98) * mm});
            skLineSegment(sketch, "E2078", {"start": v(-630.92, -61.98) * mm, "end": v(-631.72, -62.66) * mm});
            skLineSegment(sketch, "E2079", {"start": v(-631.72, -62.66) * mm, "end": v(-632.49, -63.37) * mm});
            skLineSegment(sketch, "E2080", {"start": v(-632.49, -63.37) * mm, "end": v(-633.22, -64.11) * mm});
            skLineSegment(sketch, "E2081", {"start": v(-633.22, -64.11) * mm, "end": v(-633.9, -64.88) * mm});
            skLineSegment(sketch, "E2082", {"start": v(-633.9, -64.88) * mm, "end": v(-634.54, -65.69) * mm});
            skLineSegment(sketch, "E2083", {"start": v(-634.54, -65.69) * mm, "end": v(-635.14, -66.52) * mm});
            skLineSegment(sketch, "E2084", {"start": v(-635.14, -66.52) * mm, "end": v(-635.7, -67.39) * mm});
            skLineSegment(sketch, "E2085", {"start": v(-635.7, -67.39) * mm, "end": v(-636.2, -68.3) * mm});
            skLineSegment(sketch, "E2086", {"start": v(-636.2, -68.3) * mm, "end": v(-636.65, -69.24) * mm});
            skLineSegment(sketch, "E2087", {"start": v(-636.65, -69.24) * mm, "end": v(-637.05, -70.22) * mm});
            skLineSegment(sketch, "E2088", {"start": v(-637.05, -70.22) * mm, "end": v(-637.4, -71.24) * mm});
            skLineSegment(sketch, "E2089", {"start": v(-637.4, -71.24) * mm, "end": v(-637.69, -72.3) * mm});
            skLineSegment(sketch, "E2090", {"start": v(-637.69, -72.3) * mm, "end": v(-637.92, -73.4) * mm});
            skLineSegment(sketch, "E2091", {"start": v(-637.92, -73.4) * mm, "end": v(-638.1, -74.56) * mm});
            skLineSegment(sketch, "E2092", {"start": v(-638.1, -74.56) * mm, "end": v(-638.21, -75.76) * mm});
            skLineSegment(sketch, "E2093", {"start": v(-638.21, -75.76) * mm, "end": v(-638.27, -77) * mm});
            skLineSegment(sketch, "E2094", {"start": v(-638.27, -77) * mm, "end": v(-638.26, -78.3) * mm});
            skLineSegment(sketch, "E2095", {"start": v(-638.26, -78.3) * mm, "end": v(-638.18, -79.64) * mm});
            skLineSegment(sketch, "E2096", {"start": v(-638.18, -79.64) * mm, "end": v(-638.04, -81.04) * mm});
            skLineSegment(sketch, "E2097", {"start": v(-638.04, -81.04) * mm, "end": v(-637.72, -83) * mm});
            skLineSegment(sketch, "E2098", {"start": v(-637.72, -83) * mm, "end": v(-637.28, -84.78) * mm});
            skLineSegment(sketch, "E2099", {"start": v(-637.28, -84.78) * mm, "end": v(-636.73, -86.42) * mm});
            skLineSegment(sketch, "E2100", {"start": v(-636.73, -86.42) * mm, "end": v(-636.06, -87.9) * mm});
            skLineSegment(sketch, "E2101", {"start": v(-636.06, -87.9) * mm, "end": v(-635.3, -89.24) * mm});
            skLineSegment(sketch, "E2102", {"start": v(-635.3, -89.24) * mm, "end": v(-634.44, -90.44) * mm});
            skLineSegment(sketch, "E2103", {"start": v(-634.44, -90.44) * mm, "end": v(-633.49, -91.51) * mm});
            skLineSegment(sketch, "E2104", {"start": v(-633.49, -91.51) * mm, "end": v(-632.45, -92.47) * mm});
            skLineSegment(sketch, "E2105", {"start": v(-632.45, -92.47) * mm, "end": v(-631.33, -93.3) * mm});
            skLineSegment(sketch, "E2106", {"start": v(-631.33, -93.3) * mm, "end": v(-630.14, -94.04) * mm});
            skLineSegment(sketch, "E2107", {"start": v(-630.14, -94.04) * mm, "end": v(-628.87, -94.67) * mm});
            skLineSegment(sketch, "E2108", {"start": v(-628.87, -94.67) * mm, "end": v(-627.55, -95.21) * mm});
            skLineSegment(sketch, "E2109", {"start": v(-627.55, -95.21) * mm, "end": v(-626.17, -95.67) * mm});
            skLineSegment(sketch, "E2110", {"start": v(-626.17, -95.67) * mm, "end": v(-624.73, -96.05) * mm});
            skLineSegment(sketch, "E2111", {"start": v(-624.73, -96.05) * mm, "end": v(-623.25, -96.36) * mm});
            skLineSegment(sketch, "E2112", {"start": v(-623.25, -96.36) * mm, "end": v(-621.73, -96.61) * mm});
            skLineSegment(sketch, "E2113", {"start": v(-621.73, -96.61) * mm, "end": v(-620.18, -96.8) * mm});
            skLineSegment(sketch, "E2114", {"start": v(-620.18, -96.8) * mm, "end": v(-618.6, -96.96) * mm});
            skLineSegment(sketch, "E2115", {"start": v(-618.6, -96.96) * mm, "end": v(-616.99, -97.07) * mm});
            skLineSegment(sketch, "E2116", {"start": v(-616.99, -97.07) * mm, "end": v(-615.36, -97.14) * mm});
            skLineSegment(sketch, "E2117", {"start": v(-615.36, -97.14) * mm, "end": v(-613.72, -97.2) * mm});
            skLineSegment(sketch, "E2118", {"start": v(-613.72, -97.2) * mm, "end": v(-612.08, -97.23) * mm});
            skLineSegment(sketch, "E2119", {"start": v(-612.08, -97.23) * mm, "end": v(-610.44, -97.25) * mm});
            skLineSegment(sketch, "E2120", {"start": v(-610.44, -97.25) * mm, "end": v(-608.8, -97.28) * mm});
            skLineSegment(sketch, "E2121", {"start": v(-608.8, -97.28) * mm, "end": v(-607.17, -97.3) * mm});
            skLineSegment(sketch, "E2122", {"start": v(-607.17, -97.3) * mm, "end": v(-605.56, -97.34) * mm});
            skLineSegment(sketch, "E2123", {"start": v(-605.56, -97.34) * mm, "end": v(-603.97, -97.4) * mm});
            skLineSegment(sketch, "E2124", {"start": v(-603.97, -97.4) * mm, "end": v(-602.28, -97.5) * mm});
            skLineSegment(sketch, "E2125", {"start": v(-602.28, -97.5) * mm, "end": v(-600.58, -97.67) * mm});
            skLineSegment(sketch, "E2126", {"start": v(-600.58, -97.67) * mm, "end": v(-598.9, -97.9) * mm});
            skLineSegment(sketch, "E2127", {"start": v(-598.9, -97.9) * mm, "end": v(-597.21, -98.17) * mm});
            skLineSegment(sketch, "E2128", {"start": v(-597.21, -98.17) * mm, "end": v(-595.55, -98.5) * mm});
            skLineSegment(sketch, "E2129", {"start": v(-595.55, -98.5) * mm, "end": v(-593.9, -98.9) * mm});
            skLineSegment(sketch, "E2130", {"start": v(-593.9, -98.9) * mm, "end": v(-592.26, -99.35) * mm});
            skLineSegment(sketch, "E2131", {"start": v(-592.26, -99.35) * mm, "end": v(-590.65, -99.85) * mm});
            skLineSegment(sketch, "E2132", {"start": v(-590.65, -99.85) * mm, "end": v(-589.06, -100.41) * mm});
            skLineSegment(sketch, "E2133", {"start": v(-589.06, -100.41) * mm, "end": v(-587.5, -101.03) * mm});
            skLineSegment(sketch, "E2134", {"start": v(-587.5, -101.03) * mm, "end": v(-585.96, -101.7) * mm});
            skLineSegment(sketch, "E2135", {"start": v(-585.96, -101.7) * mm, "end": v(-584.46, -102.43) * mm});
            skLineSegment(sketch, "E2136", {"start": v(-584.46, -102.43) * mm, "end": v(-583, -103.2) * mm});
            skLineSegment(sketch, "E2137", {"start": v(-583, -103.2) * mm, "end": v(-581.57, -104.04) * mm});
            skLineSegment(sketch, "E2138", {"start": v(-581.57, -104.04) * mm, "end": v(-580.18, -104.93) * mm});
            skLineSegment(sketch, "E2139", {"start": v(-580.18, -104.93) * mm, "end": v(-578.83, -105.88) * mm});
            skLineSegment(sketch, "E2140", {"start": v(-578.83, -105.88) * mm, "end": v(-577.53, -106.88) * mm});
            skLineSegment(sketch, "E2141", {"start": v(-577.53, -106.88) * mm, "end": v(-576.28, -107.93) * mm});
            skLineSegment(sketch, "E2142", {"start": v(-576.28, -107.93) * mm, "end": v(-575.09, -109.03) * mm});
            skLineSegment(sketch, "E2143", {"start": v(-575.09, -109.03) * mm, "end": v(-573.94, -110.19) * mm});
            skLineSegment(sketch, "E2144", {"start": v(-573.94, -110.19) * mm, "end": v(-572.86, -111.4) * mm});
            skLineSegment(sketch, "E2145", {"start": v(-572.86, -111.4) * mm, "end": v(-571.83, -112.66) * mm});
            skLineSegment(sketch, "E2146", {"start": v(-571.83, -112.66) * mm, "end": v(-570.86, -113.97) * mm});
            skLineSegment(sketch, "E2147", {"start": v(-570.86, -113.97) * mm, "end": v(-569.97, -115.34) * mm});
            skLineSegment(sketch, "E2148", {"start": v(-569.97, -115.34) * mm, "end": v(-569.14, -116.76) * mm});
            skLineSegment(sketch, "E2149", {"start": v(-569.14, -116.76) * mm, "end": v(-568.38, -118.22) * mm});
            skLineSegment(sketch, "E2150", {"start": v(-568.38, -118.22) * mm, "end": v(-567.7, -119.74) * mm});
            skLineSegment(sketch, "E2151", {"start": v(-567.7, -119.74) * mm, "end": v(-567.09, -121.31) * mm});
            skLineSegment(sketch, "E2152", {"start": v(-567.09, -121.31) * mm, "end": v(-566.56, -122.93) * mm});
            skLineSegment(sketch, "E2153", {"start": v(-566.56, -122.93) * mm, "end": v(-566.11, -124.6) * mm});
            skLineSegment(sketch, "E2154", {"start": v(-566.11, -124.6) * mm, "end": v(-565.75, -126.33) * mm});
            skLineSegment(sketch, "E2155", {"start": v(-565.75, -126.33) * mm, "end": v(-565.48, -128.1) * mm});
            skLineSegment(sketch, "E2156", {"start": v(-565.48, -128.1) * mm, "end": v(-565.3, -129.92) * mm});
            skLineSegment(sketch, "E2157", {"start": v(-565.3, -129.92) * mm, "end": v(-565.23, -131.38) * mm});
            skLineSegment(sketch, "E2158", {"start": v(-565.23, -131.38) * mm, "end": v(-565.22, -132.8) * mm});
            skLineSegment(sketch, "E2159", {"start": v(-565.22, -132.8) * mm, "end": v(-565.27, -134.18) * mm});
            skLineSegment(sketch, "E2160", {"start": v(-565.27, -134.18) * mm, "end": v(-565.39, -135.52) * mm});
            skLineSegment(sketch, "E2161", {"start": v(-565.39, -135.52) * mm, "end": v(-565.57, -136.81) * mm});
            skLineSegment(sketch, "E2162", {"start": v(-565.57, -136.81) * mm, "end": v(-565.8, -138.08) * mm});
            skLineSegment(sketch, "E2163", {"start": v(-565.8, -138.08) * mm, "end": v(-566.1, -139.3) * mm});
            skLineSegment(sketch, "E2164", {"start": v(-566.1, -139.3) * mm, "end": v(-566.44, -140.49) * mm});
            skLineSegment(sketch, "E2165", {"start": v(-566.44, -140.49) * mm, "end": v(-566.83, -141.64) * mm});
            skLineSegment(sketch, "E2166", {"start": v(-566.83, -141.64) * mm, "end": v(-567.28, -142.76) * mm});
            skLineSegment(sketch, "E2167", {"start": v(-567.28, -142.76) * mm, "end": v(-567.78, -143.84) * mm});
            skLineSegment(sketch, "E2168", {"start": v(-567.78, -143.84) * mm, "end": v(-568.32, -144.9) * mm});
            skLineSegment(sketch, "E2169", {"start": v(-568.32, -144.9) * mm, "end": v(-568.9, -145.92) * mm});
            skLineSegment(sketch, "E2170", {"start": v(-568.9, -145.92) * mm, "end": v(-569.54, -146.92) * mm});
            skLineSegment(sketch, "E2171", {"start": v(-569.54, -146.92) * mm, "end": v(-570.2, -147.89) * mm});
            skLineSegment(sketch, "E2172", {"start": v(-570.2, -147.89) * mm, "end": v(-570.91, -148.83) * mm});
            skLineSegment(sketch, "E2173", {"start": v(-570.91, -148.83) * mm, "end": v(-571.66, -149.74) * mm});
            skLineSegment(sketch, "E2174", {"start": v(-571.66, -149.74) * mm, "end": v(-572.44, -150.63) * mm});
            skLineSegment(sketch, "E2175", {"start": v(-572.44, -150.63) * mm, "end": v(-573.26, -151.5) * mm});
            skLineSegment(sketch, "E2176", {"start": v(-573.26, -151.5) * mm, "end": v(-574.1, -152.34) * mm});
            skLineSegment(sketch, "E2177", {"start": v(-574.1, -152.34) * mm, "end": v(-574.98, -153.16) * mm});
            skLineSegment(sketch, "E2178", {"start": v(-574.98, -153.16) * mm, "end": v(-575.88, -153.96) * mm});
            skLineSegment(sketch, "E2179", {"start": v(-575.88, -153.96) * mm, "end": v(-576.8, -154.75) * mm});
            skLineSegment(sketch, "E2180", {"start": v(-576.8, -154.75) * mm, "end": v(-577.76, -155.51) * mm});
            skLineSegment(sketch, "E2181", {"start": v(-577.76, -155.51) * mm, "end": v(-578.73, -156.26) * mm});
            skLineSegment(sketch, "E2182", {"start": v(-578.73, -156.26) * mm, "end": v(-579.73, -157) * mm});
            skLineSegment(sketch, "E2183", {"start": v(-579.73, -157) * mm, "end": v(-580.74, -157.71) * mm});
            skLineSegment(sketch, "E2184", {"start": v(-580.74, -157.71) * mm, "end": v(-581.77, -158.42) * mm});
            skLineSegment(sketch, "E2185", {"start": v(-581.77, -158.42) * mm, "end": v(-582.8, -159.11) * mm});
            skLineSegment(sketch, "E2186", {"start": v(-582.8, -159.11) * mm, "end": v(-583.86, -159.8) * mm});
            skLineSegment(sketch, "E2187", {"start": v(-583.86, -159.8) * mm, "end": v(-584.92, -160.47) * mm});
            skLineSegment(sketch, "E2188", {"start": v(-584.92, -160.47) * mm, "end": v(-586, -161.13) * mm});
            skLineSegment(sketch, "E2189", {"start": v(-586, -161.13) * mm, "end": v(-587.07, -161.78) * mm});
            skLineSegment(sketch, "E2190", {"start": v(-587.07, -161.78) * mm, "end": v(-588.16, -162.43) * mm});
            skLineSegment(sketch, "E2191", {"start": v(-588.16, -162.43) * mm, "end": v(-589.24, -163.07) * mm});
            skLineSegment(sketch, "E2192", {"start": v(-589.24, -163.07) * mm, "end": v(-590.33, -163.71) * mm});
            skLineSegment(sketch, "E2193", {"start": v(-590.33, -163.71) * mm, "end": v(-591.41, -164.35) * mm});
            skLineSegment(sketch, "E2194", {"start": v(-591.41, -164.35) * mm, "end": v(-592.5, -164.98) * mm});
            skLineSegment(sketch, "E2195", {"start": v(-592.5, -164.98) * mm, "end": v(-593.57, -165.61) * mm});
            skLineSegment(sketch, "E2196", {"start": v(-593.57, -165.61) * mm, "end": v(-594.64, -166.25) * mm});
            skLineSegment(sketch, "E2197", {"start": v(-594.64, -166.25) * mm, "end": v(-595.7, -166.88) * mm});
            skLineSegment(sketch, "E2198", {"start": v(-595.7, -166.88) * mm, "end": v(-596.75, -167.52) * mm});
            skLineSegment(sketch, "E2199", {"start": v(-596.75, -167.52) * mm, "end": v(-597.79, -168.16) * mm});
            skLineSegment(sketch, "E2200", {"start": v(-597.79, -168.16) * mm, "end": v(-598.8, -168.8) * mm});
            skLineSegment(sketch, "E2201", {"start": v(-598.8, -168.8) * mm, "end": v(-599.81, -169.45) * mm});
            skLineSegment(sketch, "E2202", {"start": v(-599.81, -169.45) * mm, "end": v(-600.8, -170.11) * mm});
            skLineSegment(sketch, "E2203", {"start": v(-600.8, -170.11) * mm, "end": v(-601.77, -170.78) * mm});
            skLineSegment(sketch, "E2204", {"start": v(-601.77, -170.78) * mm, "end": v(-602.71, -171.45) * mm});
            skLineSegment(sketch, "E2205", {"start": v(-602.71, -171.45) * mm, "end": v(-603.63, -172.14) * mm});
            skLineSegment(sketch, "E2206", {"start": v(-603.63, -172.14) * mm, "end": v(-604.53, -172.83) * mm});
            skLineSegment(sketch, "E2207", {"start": v(-604.53, -172.83) * mm, "end": v(-605.4, -173.54) * mm});
            skLineSegment(sketch, "E2208", {"start": v(-605.4, -173.54) * mm, "end": v(-606.23, -174.27) * mm});
            skLineSegment(sketch, "E2209", {"start": v(-606.23, -174.27) * mm, "end": v(-607.04, -175) * mm});
            skLineSegment(sketch, "E2210", {"start": v(-607.04, -175) * mm, "end": v(-607.8, -175.76) * mm});
            skLineSegment(sketch, "E2211", {"start": v(-607.8, -175.76) * mm, "end": v(-608.54, -176.53) * mm});
            skLineSegment(sketch, "E2212", {"start": v(-608.54, -176.53) * mm, "end": v(-609.24, -177.32) * mm});
            skLineSegment(sketch, "E2213", {"start": v(-609.24, -177.32) * mm, "end": v(-609.9, -178.13) * mm});
            skLineSegment(sketch, "E2214", {"start": v(-609.9, -178.13) * mm, "end": v(-610.52, -178.96) * mm});
            skLineSegment(sketch, "E2215", {"start": v(-610.52, -178.96) * mm, "end": v(-611.1, -179.8) * mm});
            skLineSegment(sketch, "E2216", {"start": v(-611.1, -179.8) * mm, "end": v(-611.62, -180.68) * mm});
            skLineSegment(sketch, "E2217", {"start": v(-611.62, -180.68) * mm, "end": v(-612.1, -181.58) * mm});
            skLineSegment(sketch, "E2218", {"start": v(-612.1, -181.58) * mm, "end": v(-612.53, -182.5) * mm});
            skLineSegment(sketch, "E2219", {"start": v(-612.53, -182.5) * mm, "end": v(-612.91, -183.45) * mm});
            skLineSegment(sketch, "E2220", {"start": v(-612.91, -183.45) * mm, "end": v(-613.24, -184.43) * mm});
            skLineSegment(sketch, "E2221", {"start": v(-613.24, -184.43) * mm, "end": v(-613.52, -185.43) * mm});
            skLineSegment(sketch, "E2222", {"start": v(-613.52, -185.43) * mm, "end": v(-613.73, -186.46) * mm});
            skLineSegment(sketch, "E2223", {"start": v(-613.73, -186.46) * mm, "end": v(-613.9, -187.53) * mm});
            skLineSegment(sketch, "E2224", {"start": v(-613.9, -187.53) * mm, "end": v(-614, -188.63) * mm});
            skLineSegment(sketch, "E2225", {"start": v(-614, -188.63) * mm, "end": v(-614.03, -189.75) * mm});
            skLineSegment(sketch, "E2226", {"start": v(-614.03, -189.75) * mm, "end": v(-614, -190.92) * mm});
            skLineSegment(sketch, "E2227", {"start": v(-614, -190.92) * mm, "end": v(-613.9, -192.12) * mm});
            skLineSegment(sketch, "E2228", {"start": v(-613.9, -192.12) * mm, "end": v(-613.74, -193.35) * mm});
            skLineSegment(sketch, "E2229", {"start": v(-613.74, -193.35) * mm, "end": v(-613.5, -194.63) * mm});
            skLineSegment(sketch, "E2230", {"start": v(-613.5, -194.63) * mm, "end": v(-613.2, -195.94) * mm});
            skLineSegment(sketch, "E2231", {"start": v(-613.2, -195.94) * mm, "end": v(-612.82, -197.29) * mm});
            skLineSegment(sketch, "E2232", {"start": v(-612.82, -197.29) * mm, "end": v(-612.37, -198.68) * mm});
            skLineSegment(sketch, "E2233", {"start": v(-612.37, -198.68) * mm, "end": v(-611.66, -200.45) * mm});
            skLineSegment(sketch, "E2234", {"start": v(-611.66, -200.45) * mm, "end": v(-610.85, -202.04) * mm});
            skLineSegment(sketch, "E2235", {"start": v(-610.85, -202.04) * mm, "end": v(-609.94, -203.44) * mm});
            skLineSegment(sketch, "E2236", {"start": v(-609.94, -203.44) * mm, "end": v(-608.94, -204.68) * mm});
            skLineSegment(sketch, "E2237", {"start": v(-608.94, -204.68) * mm, "end": v(-607.86, -205.75) * mm});
            skLineSegment(sketch, "E2238", {"start": v(-607.86, -205.75) * mm, "end": v(-606.7, -206.67) * mm});
            skLineSegment(sketch, "E2239", {"start": v(-606.7, -206.67) * mm, "end": v(-605.46, -207.45) * mm});
            skLineSegment(sketch, "E2240", {"start": v(-605.46, -207.45) * mm, "end": v(-604.15, -208.1) * mm});
            skLineSegment(sketch, "E2241", {"start": v(-604.15, -208.1) * mm, "end": v(-602.78, -208.61) * mm});
            skLineSegment(sketch, "E2242", {"start": v(-602.78, -208.61) * mm, "end": v(-601.36, -209.02) * mm});
            skLineSegment(sketch, "E2243", {"start": v(-601.36, -209.02) * mm, "end": v(-599.88, -209.31) * mm});
            skLineSegment(sketch, "E2244", {"start": v(-599.88, -209.31) * mm, "end": v(-598.36, -209.51) * mm});
            skLineSegment(sketch, "E2245", {"start": v(-598.36, -209.51) * mm, "end": v(-596.8, -209.62) * mm});
            skLineSegment(sketch, "E2246", {"start": v(-596.8, -209.62) * mm, "end": v(-595.22, -209.66) * mm});
            skLineSegment(sketch, "E2247", {"start": v(-595.22, -209.66) * mm, "end": v(-593.6, -209.62) * mm});
            skLineSegment(sketch, "E2248", {"start": v(-593.6, -209.62) * mm, "end": v(-591.97, -209.52) * mm});
            skLineSegment(sketch, "E2249", {"start": v(-591.97, -209.52) * mm, "end": v(-590.32, -209.37) * mm});
            skLineSegment(sketch, "E2250", {"start": v(-590.32, -209.37) * mm, "end": v(-588.66, -209.18) * mm});
            skLineSegment(sketch, "E2251", {"start": v(-588.66, -209.18) * mm, "end": v(-587, -208.95) * mm});
            skLineSegment(sketch, "E2252", {"start": v(-587, -208.95) * mm, "end": v(-585.34, -208.7) * mm});
            skLineSegment(sketch, "E2253", {"start": v(-585.34, -208.7) * mm, "end": v(-583.69, -208.44) * mm});
            skLineSegment(sketch, "E2254", {"start": v(-583.69, -208.44) * mm, "end": v(-582.05, -208.17) * mm});
            skLineSegment(sketch, "E2255", {"start": v(-582.05, -208.17) * mm, "end": v(-580.44, -207.9) * mm});
            skLineSegment(sketch, "E2256", {"start": v(-580.44, -207.9) * mm, "end": v(-578.89, -207.67) * mm});
            skLineSegment(sketch, "E2257", {"start": v(-578.89, -207.67) * mm, "end": v(-577.32, -207.47) * mm});
            skLineSegment(sketch, "E2258", {"start": v(-577.32, -207.47) * mm, "end": v(-575.73, -207.3) * mm});
            skLineSegment(sketch, "E2259", {"start": v(-575.73, -207.3) * mm, "end": v(-574.12, -207.17) * mm});
            skLineSegment(sketch, "E2260", {"start": v(-574.12, -207.17) * mm, "end": v(-572.5, -207.07) * mm});
            skLineSegment(sketch, "E2261", {"start": v(-572.5, -207.07) * mm, "end": v(-570.88, -207.01) * mm});
            skLineSegment(sketch, "E2262", {"start": v(-570.88, -207.01) * mm, "end": v(-569.25, -207) * mm});
            skLineSegment(sketch, "E2263", {"start": v(-569.25, -207) * mm, "end": v(-567.62, -207.02) * mm});
            skLineSegment(sketch, "E2264", {"start": v(-567.62, -207.02) * mm, "end": v(-565.98, -207.08) * mm});
            skLineSegment(sketch, "E2265", {"start": v(-565.98, -207.08) * mm, "end": v(-564.35, -207.2) * mm});
            skLineSegment(sketch, "E2266", {"start": v(-564.35, -207.2) * mm, "end": v(-562.73, -207.35) * mm});
            skLineSegment(sketch, "E2267", {"start": v(-562.73, -207.35) * mm, "end": v(-561.11, -207.55) * mm});
            skLineSegment(sketch, "E2268", {"start": v(-561.11, -207.55) * mm, "end": v(-559.5, -207.8) * mm});
            skLineSegment(sketch, "E2269", {"start": v(-559.5, -207.8) * mm, "end": v(-557.92, -208.09) * mm});
            skLineSegment(sketch, "E2270", {"start": v(-557.92, -208.09) * mm, "end": v(-556.34, -208.44) * mm});
            skLineSegment(sketch, "E2271", {"start": v(-556.34, -208.44) * mm, "end": v(-554.8, -208.83) * mm});
            skLineSegment(sketch, "E2272", {"start": v(-554.8, -208.83) * mm, "end": v(-553.27, -209.28) * mm});
            skLineSegment(sketch, "E2273", {"start": v(-553.27, -209.28) * mm, "end": v(-551.76, -209.78) * mm});
            skLineSegment(sketch, "E2274", {"start": v(-551.76, -209.78) * mm, "end": v(-550.3, -210.34) * mm});
            skLineSegment(sketch, "E2275", {"start": v(-550.3, -210.34) * mm, "end": v(-548.86, -210.96) * mm});
            skLineSegment(sketch, "E2276", {"start": v(-548.86, -210.96) * mm, "end": v(-547.45, -211.63) * mm});
            skLineSegment(sketch, "E2277", {"start": v(-547.45, -211.63) * mm, "end": v(-546.09, -212.36) * mm});
            skLineSegment(sketch, "E2278", {"start": v(-546.09, -212.36) * mm, "end": v(-544.77, -213.15) * mm});
            skLineSegment(sketch, "E2279", {"start": v(-544.77, -213.15) * mm, "end": v(-543.49, -214) * mm});
            skLineSegment(sketch, "E2280", {"start": v(-543.49, -214) * mm, "end": v(-542.26, -214.92) * mm});
            skLineSegment(sketch, "E2281", {"start": v(-542.26, -214.92) * mm, "end": v(-541.08, -215.9) * mm});
            skLineSegment(sketch, "E2282", {"start": v(-541.08, -215.9) * mm, "end": v(-539.95, -216.94) * mm});
            skLineSegment(sketch, "E2283", {"start": v(-539.95, -216.94) * mm, "end": v(-538.88, -218.05) * mm});
            skLineSegment(sketch, "E2284", {"start": v(-538.88, -218.05) * mm, "end": v(-537.87, -219.23) * mm});
            skLineSegment(sketch, "E2285", {"start": v(-537.87, -219.23) * mm, "end": v(-536.93, -220.48) * mm});
            skLineSegment(sketch, "E2286", {"start": v(-536.93, -220.48) * mm, "end": v(-536.04, -221.8) * mm});
            skLineSegment(sketch, "E2287", {"start": v(-536.04, -221.8) * mm, "end": v(-535.23, -223.19) * mm});
            skLineSegment(sketch, "E2288", {"start": v(-535.23, -223.19) * mm, "end": v(-534.49, -224.65) * mm});
            skLineSegment(sketch, "E2289", {"start": v(-534.49, -224.65) * mm, "end": v(-533.82, -226.19) * mm});
            skLineSegment(sketch, "E2290", {"start": v(-533.82, -226.19) * mm, "end": v(-533.23, -227.8) * mm});
            skLineSegment(sketch, "E2291", {"start": v(-533.23, -227.8) * mm, "end": v(-532.72, -229.49) * mm});
            skLineSegment(sketch, "E2292", {"start": v(-532.72, -229.49) * mm, "end": v(-532.29, -231.26) * mm});
            skLineSegment(sketch, "E2293", {"start": v(-532.29, -231.26) * mm, "end": v(-531.95, -233.1) * mm});
            skLineSegment(sketch, "E2294", {"start": v(-531.95, -233.1) * mm, "end": v(-531.77, -234.44) * mm});
            skLineSegment(sketch, "E2295", {"start": v(-531.77, -234.44) * mm, "end": v(-531.67, -235.76) * mm});
            skLineSegment(sketch, "E2296", {"start": v(-531.67, -235.76) * mm, "end": v(-531.63, -237.06) * mm});
            skLineSegment(sketch, "E2297", {"start": v(-531.63, -237.06) * mm, "end": v(-531.66, -238.35) * mm});
            skLineSegment(sketch, "E2298", {"start": v(-531.66, -238.35) * mm, "end": v(-531.75, -239.61) * mm});
            skLineSegment(sketch, "E2299", {"start": v(-531.75, -239.61) * mm, "end": v(-531.9, -240.86) * mm});
            skLineSegment(sketch, "E2300", {"start": v(-531.9, -240.86) * mm, "end": v(-532.12, -242.1) * mm});
            skLineSegment(sketch, "E2301", {"start": v(-532.12, -242.1) * mm, "end": v(-532.4, -243.3) * mm});
            skLineSegment(sketch, "E2302", {"start": v(-532.4, -243.3) * mm, "end": v(-532.72, -244.5) * mm});
            skLineSegment(sketch, "E2303", {"start": v(-532.72, -244.5) * mm, "end": v(-533.1, -245.7) * mm});
            skLineSegment(sketch, "E2304", {"start": v(-533.1, -245.7) * mm, "end": v(-533.52, -246.86) * mm});
            skLineSegment(sketch, "E2305", {"start": v(-533.52, -246.86) * mm, "end": v(-534, -248.02) * mm});
            skLineSegment(sketch, "E2306", {"start": v(-534, -248.02) * mm, "end": v(-534.52, -249.16) * mm});
            skLineSegment(sketch, "E2307", {"start": v(-534.52, -249.16) * mm, "end": v(-535.09, -250.28) * mm});
            skLineSegment(sketch, "E2308", {"start": v(-535.09, -250.28) * mm, "end": v(-535.7, -251.4) * mm});
            skLineSegment(sketch, "E2309", {"start": v(-535.7, -251.4) * mm, "end": v(-536.34, -252.5) * mm});
            skLineSegment(sketch, "E2310", {"start": v(-536.34, -252.5) * mm, "end": v(-537.02, -253.6) * mm});
            skLineSegment(sketch, "E2311", {"start": v(-537.02, -253.6) * mm, "end": v(-537.74, -254.67) * mm});
            skLineSegment(sketch, "E2312", {"start": v(-537.74, -254.67) * mm, "end": v(-538.49, -255.74) * mm});
            skLineSegment(sketch, "E2313", {"start": v(-538.49, -255.74) * mm, "end": v(-539.27, -256.8) * mm});
            skLineSegment(sketch, "E2314", {"start": v(-539.27, -256.8) * mm, "end": v(-540.07, -257.84) * mm});
            skLineSegment(sketch, "E2315", {"start": v(-540.07, -257.84) * mm, "end": v(-540.9, -258.88) * mm});
            skLineSegment(sketch, "E2316", {"start": v(-540.9, -258.88) * mm, "end": v(-541.76, -259.9) * mm});
            skLineSegment(sketch, "E2317", {"start": v(-541.76, -259.9) * mm, "end": v(-542.64, -260.92) * mm});
            skLineSegment(sketch, "E2318", {"start": v(-542.64, -260.92) * mm, "end": v(-543.53, -261.93) * mm});
            skLineSegment(sketch, "E2319", {"start": v(-543.53, -261.93) * mm, "end": v(-544.44, -262.93) * mm});
            skLineSegment(sketch, "E2320", {"start": v(-544.44, -262.93) * mm, "end": v(-545.37, -263.93) * mm});
            skLineSegment(sketch, "E2321", {"start": v(-545.37, -263.93) * mm, "end": v(-546.3, -264.92) * mm});
            skLineSegment(sketch, "E2322", {"start": v(-546.3, -264.92) * mm, "end": v(-547.25, -265.9) * mm});
            skLineSegment(sketch, "E2323", {"start": v(-547.25, -265.9) * mm, "end": v(-548.2, -266.87) * mm});
            skLineSegment(sketch, "E2324", {"start": v(-548.2, -266.87) * mm, "end": v(-549.16, -267.84) * mm});
            skLineSegment(sketch, "E2325", {"start": v(-549.16, -267.84) * mm, "end": v(-550.12, -268.8) * mm});
            skLineSegment(sketch, "E2326", {"start": v(-550.12, -268.8) * mm, "end": v(-551.09, -269.76) * mm});
            skLineSegment(sketch, "E2327", {"start": v(-551.09, -269.76) * mm, "end": v(-552.05, -270.72) * mm});
            skLineSegment(sketch, "E2328", {"start": v(-552.05, -270.72) * mm, "end": v(-553, -271.67) * mm});
            skLineSegment(sketch, "E2329", {"start": v(-553, -271.67) * mm, "end": v(-553.95, -272.62) * mm});
            skLineSegment(sketch, "E2330", {"start": v(-553.95, -272.62) * mm, "end": v(-554.9, -273.56) * mm});
            skLineSegment(sketch, "E2331", {"start": v(-554.9, -273.56) * mm, "end": v(-555.82, -274.5) * mm});
            skLineSegment(sketch, "E2332", {"start": v(-555.82, -274.5) * mm, "end": v(-556.74, -275.44) * mm});
            skLineSegment(sketch, "E2333", {"start": v(-556.74, -275.44) * mm, "end": v(-557.64, -276.38) * mm});
            skLineSegment(sketch, "E2334", {"start": v(-557.64, -276.38) * mm, "end": v(-558.53, -277.32) * mm});
            skLineSegment(sketch, "E2335", {"start": v(-558.53, -277.32) * mm, "end": v(-559.4, -278.26) * mm});
            skLineSegment(sketch, "E2336", {"start": v(-559.4, -278.26) * mm, "end": v(-560.23, -279.2) * mm});
            skLineSegment(sketch, "E2337", {"start": v(-560.23, -279.2) * mm, "end": v(-561.05, -280.13) * mm});
            skLineSegment(sketch, "E2338", {"start": v(-561.05, -280.13) * mm, "end": v(-561.84, -281.07) * mm});
            skLineSegment(sketch, "E2339", {"start": v(-561.84, -281.07) * mm, "end": v(-562.6, -282) * mm});
            skLineSegment(sketch, "E2340", {"start": v(-562.6, -282) * mm, "end": v(-563.34, -282.95) * mm});
            skLineSegment(sketch, "E2341", {"start": v(-563.34, -282.95) * mm, "end": v(-564.04, -283.9) * mm});
            skLineSegment(sketch, "E2342", {"start": v(-564.04, -283.9) * mm, "end": v(-564.7, -284.84) * mm});
            skLineSegment(sketch, "E2343", {"start": v(-564.7, -284.84) * mm, "end": v(-565.32, -285.79) * mm});
            skLineSegment(sketch, "E2344", {"start": v(-565.32, -285.79) * mm, "end": v(-565.9, -286.74) * mm});
            skLineSegment(sketch, "E2345", {"start": v(-565.9, -286.74) * mm, "end": v(-566.45, -287.7) * mm});
            skLineSegment(sketch, "E2346", {"start": v(-566.45, -287.7) * mm, "end": v(-566.94, -288.66) * mm});
            skLineSegment(sketch, "E2347", {"start": v(-566.94, -288.66) * mm, "end": v(-567.4, -289.62) * mm});
            skLineSegment(sketch, "E2348", {"start": v(-567.4, -289.62) * mm, "end": v(-567.8, -290.6) * mm});
            skLineSegment(sketch, "E2349", {"start": v(-567.8, -290.6) * mm, "end": v(-568.14, -291.57) * mm});
            skLineSegment(sketch, "E2350", {"start": v(-568.14, -291.57) * mm, "end": v(-568.44, -292.56) * mm});
            skLineSegment(sketch, "E2351", {"start": v(-568.44, -292.56) * mm, "end": v(-568.68, -293.55) * mm});
            skLineSegment(sketch, "E2352", {"start": v(-568.68, -293.55) * mm, "end": v(-568.86, -294.54) * mm});
            skLineSegment(sketch, "E2353", {"start": v(-568.86, -294.54) * mm, "end": v(-568.98, -295.55) * mm});
            skLineSegment(sketch, "E2354", {"start": v(-568.98, -295.55) * mm, "end": v(-569.04, -296.56) * mm});
            skLineSegment(sketch, "E2355", {"start": v(-569.04, -296.56) * mm, "end": v(-569.03, -297.58) * mm});
            skLineSegment(sketch, "E2356", {"start": v(-569.03, -297.58) * mm, "end": v(-568.95, -298.61) * mm});
            skLineSegment(sketch, "E2357", {"start": v(-568.95, -298.61) * mm, "end": v(-568.81, -299.65) * mm});
            skLineSegment(sketch, "E2358", {"start": v(-568.81, -299.65) * mm, "end": v(-568.6, -300.7) * mm});
            skLineSegment(sketch, "E2359", {"start": v(-568.6, -300.7) * mm, "end": v(-568.3, -301.76) * mm});
            skLineSegment(sketch, "E2360", {"start": v(-568.3, -301.76) * mm, "end": v(-567.94, -302.84) * mm});
            skLineSegment(sketch, "E2361", {"start": v(-567.94, -302.84) * mm, "end": v(-567.5, -303.92) * mm});
            skLineSegment(sketch, "E2362", {"start": v(-567.5, -303.92) * mm, "end": v(-566.96, -305.01) * mm});
            skLineSegment(sketch, "E2363", {"start": v(-566.96, -305.01) * mm, "end": v(-566.35, -306.12) * mm});
            skLineSegment(sketch, "E2364", {"start": v(-566.35, -306.12) * mm, "end": v(-565.66, -307.24) * mm});
            skLineSegment(sketch, "E2365", {"start": v(-565.66, -307.24) * mm, "end": v(-564.87, -308.37) * mm});
            skLineSegment(sketch, "E2366", {"start": v(-564.87, -308.37) * mm, "end": v(-564, -309.52) * mm});
            skLineSegment(sketch, "E2367", {"start": v(-564, -309.52) * mm, "end": v(-563.04, -310.68) * mm});
            skLineSegment(sketch, "E2368", {"start": v(-563.04, -310.68) * mm, "end": v(-561.8, -311.97) * mm});
            skLineSegment(sketch, "E2369", {"start": v(-561.8, -311.97) * mm, "end": v(-560.5, -313.05) * mm});
            skLineSegment(sketch, "E2370", {"start": v(-560.5, -313.05) * mm, "end": v(-559.15, -313.95) * mm});
            skLineSegment(sketch, "E2371", {"start": v(-559.15, -313.95) * mm, "end": v(-557.74, -314.67) * mm});
            skLineSegment(sketch, "E2372", {"start": v(-557.74, -314.67) * mm, "end": v(-556.3, -315.22) * mm});
            skLineSegment(sketch, "E2373", {"start": v(-556.3, -315.22) * mm, "end": v(-554.8, -315.61) * mm});
            skLineSegment(sketch, "E2374", {"start": v(-554.8, -315.61) * mm, "end": v(-553.28, -315.87) * mm});
            skLineSegment(sketch, "E2375", {"start": v(-553.28, -315.87) * mm, "end": v(-551.72, -315.98) * mm});
            skLineSegment(sketch, "E2376", {"start": v(-551.72, -315.98) * mm, "end": v(-550.14, -315.98) * mm});
            skLineSegment(sketch, "E2377", {"start": v(-550.14, -315.98) * mm, "end": v(-548.54, -315.87) * mm});
            skLineSegment(sketch, "E2378", {"start": v(-548.54, -315.87) * mm, "end": v(-546.92, -315.66) * mm});
            skLineSegment(sketch, "E2379", {"start": v(-546.92, -315.66) * mm, "end": v(-545.29, -315.37) * mm});
            skLineSegment(sketch, "E2380", {"start": v(-545.29, -315.37) * mm, "end": v(-543.65, -315) * mm});
            skLineSegment(sketch, "E2381", {"start": v(-543.65, -315) * mm, "end": v(-542, -314.57) * mm});
            skLineSegment(sketch, "E2382", {"start": v(-542, -314.57) * mm, "end": v(-540.37, -314.09) * mm});
            skLineSegment(sketch, "E2383", {"start": v(-540.37, -314.09) * mm, "end": v(-538.74, -313.56) * mm});
            skLineSegment(sketch, "E2384", {"start": v(-538.74, -313.56) * mm, "end": v(-537.12, -313.01) * mm});
            skLineSegment(sketch, "E2385", {"start": v(-537.12, -313.01) * mm, "end": v(-535.52, -312.44) * mm});
            skLineSegment(sketch, "E2386", {"start": v(-535.52, -312.44) * mm, "end": v(-533.94, -311.87) * mm});
            skLineSegment(sketch, "E2387", {"start": v(-533.94, -311.87) * mm, "end": v(-532.39, -311.3) * mm});
            skLineSegment(sketch, "E2388", {"start": v(-532.39, -311.3) * mm, "end": v(-530.87, -310.76) * mm});
            skLineSegment(sketch, "E2389", {"start": v(-530.87, -310.76) * mm, "end": v(-529.38, -310.24) * mm});
            skLineSegment(sketch, "E2390", {"start": v(-529.38, -310.24) * mm, "end": v(-527.94, -309.76) * mm});
            skLineSegment(sketch, "E2391", {"start": v(-527.94, -309.76) * mm, "end": v(-526.22, -309.24) * mm});
            skLineSegment(sketch, "E2392", {"start": v(-526.22, -309.24) * mm, "end": v(-524.5, -308.76) * mm});
            skLineSegment(sketch, "E2393", {"start": v(-524.5, -308.76) * mm, "end": v(-522.79, -308.34) * mm});
            skLineSegment(sketch, "E2394", {"start": v(-522.79, -308.34) * mm, "end": v(-521.08, -307.97) * mm});
            skLineSegment(sketch, "E2395", {"start": v(-521.08, -307.97) * mm, "end": v(-519.38, -307.65) * mm});
            skLineSegment(sketch, "E2396", {"start": v(-519.38, -307.65) * mm, "end": v(-517.68, -307.4) * mm});
            skLineSegment(sketch, "E2397", {"start": v(-517.68, -307.4) * mm, "end": v(-516, -307.2) * mm});
            skLineSegment(sketch, "E2398", {"start": v(-516, -307.2) * mm, "end": v(-514.32, -307.05) * mm});
            skLineSegment(sketch, "E2399", {"start": v(-514.32, -307.05) * mm, "end": v(-512.65, -306.97) * mm});
            skLineSegment(sketch, "E2400", {"start": v(-512.65, -306.97) * mm, "end": v(-511, -306.95) * mm});
            skLineSegment(sketch, "E2401", {"start": v(-511, -306.95) * mm, "end": v(-509.37, -307) * mm});
            skLineSegment(sketch, "E2402", {"start": v(-509.37, -307) * mm, "end": v(-507.75, -307.1) * mm});
            skLineSegment(sketch, "E2403", {"start": v(-507.75, -307.1) * mm, "end": v(-506.15, -307.28) * mm});
            skLineSegment(sketch, "E2404", {"start": v(-506.15, -307.28) * mm, "end": v(-504.57, -307.52) * mm});
            skLineSegment(sketch, "E2405", {"start": v(-504.57, -307.52) * mm, "end": v(-503, -307.84) * mm});
            skLineSegment(sketch, "E2406", {"start": v(-503, -307.84) * mm, "end": v(-501.46, -308.22) * mm});
            skLineSegment(sketch, "E2407", {"start": v(-501.46, -308.22) * mm, "end": v(-499.95, -308.68) * mm});
            skLineSegment(sketch, "E2408", {"start": v(-499.95, -308.68) * mm, "end": v(-498.46, -309.22) * mm});
            skLineSegment(sketch, "E2409", {"start": v(-498.46, -309.22) * mm, "end": v(-497, -309.83) * mm});
            skLineSegment(sketch, "E2410", {"start": v(-497, -309.83) * mm, "end": v(-495.55, -310.51) * mm});
            skLineSegment(sketch, "E2411", {"start": v(-495.55, -310.51) * mm, "end": v(-494.15, -311.28) * mm});
            skLineSegment(sketch, "E2412", {"start": v(-494.15, -311.28) * mm, "end": v(-492.77, -312.13) * mm});
            skLineSegment(sketch, "E2413", {"start": v(-492.77, -312.13) * mm, "end": v(-491.42, -313.06) * mm});
            skLineSegment(sketch, "E2414", {"start": v(-491.42, -313.06) * mm, "end": v(-490.11, -314.07) * mm});
            skLineSegment(sketch, "E2415", {"start": v(-490.11, -314.07) * mm, "end": v(-488.83, -315.17) * mm});
            skLineSegment(sketch, "E2416", {"start": v(-488.83, -315.17) * mm, "end": v(-487.6, -316.35) * mm});
            skLineSegment(sketch, "E2417", {"start": v(-487.6, -316.35) * mm, "end": v(-486.39, -317.62) * mm});
            skLineSegment(sketch, "E2418", {"start": v(-486.39, -317.62) * mm, "end": v(-485.23, -318.99) * mm});
            skLineSegment(sketch, "E2419", {"start": v(-485.23, -318.99) * mm, "end": v(-484.1, -320.44) * mm});
            skLineSegment(sketch, "E2420", {"start": v(-484.1, -320.44) * mm, "end": v(-483.02, -321.99) * mm});
            skLineSegment(sketch, "E2421", {"start": v(-483.02, -321.99) * mm, "end": v(-481.98, -323.63) * mm});
            skLineSegment(sketch, "E2422", {"start": v(-481.98, -323.63) * mm, "end": v(-481.28, -324.86) * mm});
            skLineSegment(sketch, "E2423", {"start": v(-481.28, -324.86) * mm, "end": v(-480.64, -326.08) * mm});
            skLineSegment(sketch, "E2424", {"start": v(-480.64, -326.08) * mm, "end": v(-480.07, -327.29) * mm});
            skLineSegment(sketch, "E2425", {"start": v(-480.07, -327.29) * mm, "end": v(-479.57, -328.49) * mm});
            skLineSegment(sketch, "E2426", {"start": v(-479.57, -328.49) * mm, "end": v(-479.14, -329.68) * mm});
            skLineSegment(sketch, "E2427", {"start": v(-479.14, -329.68) * mm, "end": v(-478.77, -330.86) * mm});
            skLineSegment(sketch, "E2428", {"start": v(-478.77, -330.86) * mm, "end": v(-478.46, -332.03) * mm});
            skLineSegment(sketch, "E2429", {"start": v(-478.46, -332.03) * mm, "end": v(-478.22, -333.2) * mm});
            skLineSegment(sketch, "E2430", {"start": v(-478.22, -333.2) * mm, "end": v(-478.03, -334.35) * mm});
            skLineSegment(sketch, "E2431", {"start": v(-478.03, -334.35) * mm, "end": v(-477.9, -335.49) * mm});
            skLineSegment(sketch, "E2432", {"start": v(-477.9, -335.49) * mm, "end": v(-477.82, -336.62) * mm});
            skLineSegment(sketch, "E2433", {"start": v(-477.82, -336.62) * mm, "end": v(-477.8, -337.75) * mm});
            skLineSegment(sketch, "E2434", {"start": v(-477.8, -337.75) * mm, "end": v(-477.82, -338.87) * mm});
            skLineSegment(sketch, "E2435", {"start": v(-477.82, -338.87) * mm, "end": v(-477.9, -339.98) * mm});
            skLineSegment(sketch, "E2436", {"start": v(-477.9, -339.98) * mm, "end": v(-478.03, -341.08) * mm});
            skLineSegment(sketch, "E2437", {"start": v(-478.03, -341.08) * mm, "end": v(-478.2, -342.17) * mm});
            skLineSegment(sketch, "E2438", {"start": v(-478.2, -342.17) * mm, "end": v(-478.41, -343.26) * mm});
            skLineSegment(sketch, "E2439", {"start": v(-478.41, -343.26) * mm, "end": v(-478.67, -344.33) * mm});
            skLineSegment(sketch, "E2440", {"start": v(-478.67, -344.33) * mm, "end": v(-478.97, -345.4) * mm});
            skLineSegment(sketch, "E2441", {"start": v(-478.97, -345.4) * mm, "end": v(-479.3, -346.47) * mm});
            skLineSegment(sketch, "E2442", {"start": v(-479.3, -346.47) * mm, "end": v(-479.68, -347.52) * mm});
            skLineSegment(sketch, "E2443", {"start": v(-479.68, -347.52) * mm, "end": v(-480.08, -348.57) * mm});
            skLineSegment(sketch, "E2444", {"start": v(-480.08, -348.57) * mm, "end": v(-480.53, -349.61) * mm});
            skLineSegment(sketch, "E2445", {"start": v(-480.53, -349.61) * mm, "end": v(-481, -350.65) * mm});
            skLineSegment(sketch, "E2446", {"start": v(-481, -350.65) * mm, "end": v(-481.5, -351.68) * mm});
            skLineSegment(sketch, "E2447", {"start": v(-481.5, -351.68) * mm, "end": v(-482.03, -352.7) * mm});
            skLineSegment(sketch, "E2448", {"start": v(-482.03, -352.7) * mm, "end": v(-482.59, -353.72) * mm});
            skLineSegment(sketch, "E2449", {"start": v(-482.59, -353.72) * mm, "end": v(-483.17, -354.73) * mm});
            skLineSegment(sketch, "E2450", {"start": v(-483.17, -354.73) * mm, "end": v(-483.77, -355.74) * mm});
            skLineSegment(sketch, "E2451", {"start": v(-483.77, -355.74) * mm, "end": v(-484.4, -356.74) * mm});
            skLineSegment(sketch, "E2452", {"start": v(-484.4, -356.74) * mm, "end": v(-485.03, -357.74) * mm});
            skLineSegment(sketch, "E2453", {"start": v(-485.03, -357.74) * mm, "end": v(-485.7, -358.73) * mm});
            skLineSegment(sketch, "E2454", {"start": v(-485.7, -358.73) * mm, "end": v(-486.36, -359.71) * mm});
            skLineSegment(sketch, "E2455", {"start": v(-486.36, -359.71) * mm, "end": v(-487.05, -360.7) * mm});
            skLineSegment(sketch, "E2456", {"start": v(-487.05, -360.7) * mm, "end": v(-487.75, -361.67) * mm});
            skLineSegment(sketch, "E2457", {"start": v(-487.75, -361.67) * mm, "end": v(-488.46, -362.64) * mm});
            skLineSegment(sketch, "E2458", {"start": v(-488.46, -362.64) * mm, "end": v(-489.17, -363.6) * mm});
            skLineSegment(sketch, "E2459", {"start": v(-489.17, -363.6) * mm, "end": v(-489.9, -364.57) * mm});
            skLineSegment(sketch, "E2460", {"start": v(-489.9, -364.57) * mm, "end": v(-490.62, -365.53) * mm});
            skLineSegment(sketch, "E2461", {"start": v(-490.62, -365.53) * mm, "end": v(-491.35, -366.49) * mm});
            skLineSegment(sketch, "E2462", {"start": v(-491.35, -366.49) * mm, "end": v(-492.08, -367.44) * mm});
            skLineSegment(sketch, "E2463", {"start": v(-492.08, -367.44) * mm, "end": v(-492.8, -368.4) * mm});
            skLineSegment(sketch, "E2464", {"start": v(-492.8, -368.4) * mm, "end": v(-493.53, -369.34) * mm});
            skLineSegment(sketch, "E2465", {"start": v(-493.53, -369.34) * mm, "end": v(-494.25, -370.28) * mm});
            skLineSegment(sketch, "E2466", {"start": v(-494.25, -370.28) * mm, "end": v(-494.96, -371.22) * mm});
            skLineSegment(sketch, "E2467", {"start": v(-494.96, -371.22) * mm, "end": v(-495.67, -372.16) * mm});
            skLineSegment(sketch, "E2468", {"start": v(-495.67, -372.16) * mm, "end": v(-496.36, -373.1) * mm});
            skLineSegment(sketch, "E2469", {"start": v(-496.36, -373.1) * mm, "end": v(-497.04, -374.03) * mm});
            skLineSegment(sketch, "E2470", {"start": v(-497.04, -374.03) * mm, "end": v(-497.71, -374.97) * mm});
            skLineSegment(sketch, "E2471", {"start": v(-497.71, -374.97) * mm, "end": v(-498.36, -375.9) * mm});
            skLineSegment(sketch, "E2472", {"start": v(-498.36, -375.9) * mm, "end": v(-499, -376.83) * mm});
            skLineSegment(sketch, "E2473", {"start": v(-499, -376.83) * mm, "end": v(-499.61, -377.75) * mm});
            skLineSegment(sketch, "E2474", {"start": v(-499.61, -377.75) * mm, "end": v(-500.2, -378.68) * mm});
            skLineSegment(sketch, "E2475", {"start": v(-500.2, -378.68) * mm, "end": v(-500.78, -379.6) * mm});
            skLineSegment(sketch, "E2476", {"start": v(-500.78, -379.6) * mm, "end": v(-501.33, -380.53) * mm});
            skLineSegment(sketch, "E2477", {"start": v(-501.33, -380.53) * mm, "end": v(-501.85, -381.45) * mm});
            skLineSegment(sketch, "E2478", {"start": v(-501.85, -381.45) * mm, "end": v(-502.34, -382.37) * mm});
            skLineSegment(sketch, "E2479", {"start": v(-502.34, -382.37) * mm, "end": v(-502.8, -383.3) * mm});
            skLineSegment(sketch, "E2480", {"start": v(-502.8, -383.3) * mm, "end": v(-503.23, -384.22) * mm});
            skLineSegment(sketch, "E2481", {"start": v(-503.23, -384.22) * mm, "end": v(-503.63, -385.14) * mm});
            skLineSegment(sketch, "E2482", {"start": v(-503.63, -385.14) * mm, "end": v(-503.99, -386.06) * mm});
            skLineSegment(sketch, "E2483", {"start": v(-503.99, -386.06) * mm, "end": v(-504.3, -386.99) * mm});
            skLineSegment(sketch, "E2484", {"start": v(-504.3, -386.99) * mm, "end": v(-504.6, -387.91) * mm});
            skLineSegment(sketch, "E2485", {"start": v(-504.6, -387.91) * mm, "end": v(-504.83, -388.84) * mm});
            skLineSegment(sketch, "E2486", {"start": v(-504.83, -388.84) * mm, "end": v(-505.03, -389.76) * mm});
            skLineSegment(sketch, "E2487", {"start": v(-505.03, -389.76) * mm, "end": v(-505.19, -390.69) * mm});
            skLineSegment(sketch, "E2488", {"start": v(-505.19, -390.69) * mm, "end": v(-505.3, -391.62) * mm});
            skLineSegment(sketch, "E2489", {"start": v(-505.3, -391.62) * mm, "end": v(-505.35, -392.54) * mm});
            skLineSegment(sketch, "E2490", {"start": v(-505.35, -392.54) * mm, "end": v(-505.36, -393.47) * mm});
            skLineSegment(sketch, "E2491", {"start": v(-505.36, -393.47) * mm, "end": v(-505.32, -394.4) * mm});
            skLineSegment(sketch, "E2492", {"start": v(-505.32, -394.4) * mm, "end": v(-505.22, -395.34) * mm});
            skLineSegment(sketch, "E2493", {"start": v(-505.22, -395.34) * mm, "end": v(-505.07, -396.28) * mm});
            skLineSegment(sketch, "E2494", {"start": v(-505.07, -396.28) * mm, "end": v(-504.86, -397.22) * mm});
            skLineSegment(sketch, "E2495", {"start": v(-504.86, -397.22) * mm, "end": v(-504.6, -398.16) * mm});
            skLineSegment(sketch, "E2496", {"start": v(-504.6, -398.16) * mm, "end": v(-504.27, -399.1) * mm});
            skLineSegment(sketch, "E2497", {"start": v(-504.27, -399.1) * mm, "end": v(-503.87, -400.05) * mm});
            skLineSegment(sketch, "E2498", {"start": v(-503.87, -400.05) * mm, "end": v(-503.42, -401) * mm});
            skLineSegment(sketch, "E2499", {"start": v(-503.42, -401) * mm, "end": v(-502.9, -401.96) * mm});
            skLineSegment(sketch, "E2500", {"start": v(-502.9, -401.96) * mm, "end": v(-502.3, -402.91) * mm});
            skLineSegment(sketch, "E2501", {"start": v(-502.3, -402.91) * mm, "end": v(-501.64, -403.87) * mm});
            skLineSegment(sketch, "E2502", {"start": v(-501.64, -403.87) * mm, "end": v(-500.9, -404.84) * mm});
            skLineSegment(sketch, "E2503", {"start": v(-500.9, -404.84) * mm, "end": v(-500.1, -405.8) * mm});
            skLineSegment(sketch, "E2504", {"start": v(-500.1, -405.8) * mm, "end": v(-499.22, -406.78) * mm});
            skLineSegment(sketch, "E2505", {"start": v(-499.22, -406.78) * mm, "end": v(-498.25, -407.76) * mm});
            skLineSegment(sketch, "E2506", {"start": v(-498.25, -407.76) * mm, "end": v(-497.22, -408.74) * mm});
            skLineSegment(sketch, "E2507", {"start": v(-497.22, -408.74) * mm, "end": v(-496.1, -409.72) * mm});
            skLineSegment(sketch, "E2508", {"start": v(-496.1, -409.72) * mm, "end": v(-494.68, -410.79) * mm});
            skLineSegment(sketch, "E2509", {"start": v(-494.68, -410.79) * mm, "end": v(-493.23, -411.62) * mm});
            skLineSegment(sketch, "E2510", {"start": v(-493.23, -411.62) * mm, "end": v(-491.75, -412.23) * mm});
            skLineSegment(sketch, "E2511", {"start": v(-491.75, -412.23) * mm, "end": v(-490.24, -412.64) * mm});
            skLineSegment(sketch, "E2512", {"start": v(-490.24, -412.64) * mm, "end": v(-488.7, -412.85) * mm});
            skLineSegment(sketch, "E2513", {"start": v(-488.7, -412.85) * mm, "end": v(-487.16, -412.9) * mm});
            skLineSegment(sketch, "E2514", {"start": v(-487.16, -412.9) * mm, "end": v(-485.59, -412.79) * mm});
            skLineSegment(sketch, "E2515", {"start": v(-485.59, -412.79) * mm, "end": v(-484.01, -412.53) * mm});
            skLineSegment(sketch, "E2516", {"start": v(-484.01, -412.53) * mm, "end": v(-482.43, -412.14) * mm});
            skLineSegment(sketch, "E2517", {"start": v(-482.43, -412.14) * mm, "end": v(-480.85, -411.64) * mm});
            skLineSegment(sketch, "E2518", {"start": v(-480.85, -411.64) * mm, "end": v(-479.27, -411.05) * mm});
            skLineSegment(sketch, "E2519", {"start": v(-479.27, -411.05) * mm, "end": v(-477.7, -410.37) * mm});
            skLineSegment(sketch, "E2520", {"start": v(-477.7, -410.37) * mm, "end": v(-476.13, -409.62) * mm});
            skLineSegment(sketch, "E2521", {"start": v(-476.13, -409.62) * mm, "end": v(-474.59, -408.82) * mm});
            skLineSegment(sketch, "E2522", {"start": v(-474.59, -408.82) * mm, "end": v(-473.06, -407.98) * mm});
            skLineSegment(sketch, "E2523", {"start": v(-473.06, -407.98) * mm, "end": v(-471.56, -407.12) * mm});
            skLineSegment(sketch, "E2524", {"start": v(-471.56, -407.12) * mm, "end": v(-470.09, -406.26) * mm});
            skLineSegment(sketch, "E2525", {"start": v(-470.09, -406.26) * mm, "end": v(-468.65, -405.4) * mm});
            skLineSegment(sketch, "E2526", {"start": v(-468.65, -405.4) * mm, "end": v(-467.25, -404.56) * mm});
            skLineSegment(sketch, "E2527", {"start": v(-467.25, -404.56) * mm, "end": v(-465.9, -403.77) * mm});
            skLineSegment(sketch, "E2528", {"start": v(-465.9, -403.77) * mm, "end": v(-464.58, -403.02) * mm});
            skLineSegment(sketch, "E2529", {"start": v(-464.58, -403.02) * mm, "end": v(-462.97, -402.15) * mm});
            skLineSegment(sketch, "E2530", {"start": v(-462.97, -402.15) * mm, "end": v(-461.35, -401.32) * mm});
            skLineSegment(sketch, "E2531", {"start": v(-461.35, -401.32) * mm, "end": v(-459.74, -400.52) * mm});
            skLineSegment(sketch, "E2532", {"start": v(-459.74, -400.52) * mm, "end": v(-458.12, -399.76) * mm});
            skLineSegment(sketch, "E2533", {"start": v(-458.12, -399.76) * mm, "end": v(-456.5, -399.06) * mm});
            skLineSegment(sketch, "E2534", {"start": v(-456.5, -399.06) * mm, "end": v(-454.88, -398.4) * mm});
            skLineSegment(sketch, "E2535", {"start": v(-454.88, -398.4) * mm, "end": v(-453.26, -397.78) * mm});
            skLineSegment(sketch, "E2536", {"start": v(-453.26, -397.78) * mm, "end": v(-451.64, -397.22) * mm});
            skLineSegment(sketch, "E2537", {"start": v(-451.64, -397.22) * mm, "end": v(-450.02, -396.72) * mm});
            skLineSegment(sketch, "E2538", {"start": v(-450.02, -396.72) * mm, "end": v(-448.4, -396.27) * mm});
            skLineSegment(sketch, "E2539", {"start": v(-448.4, -396.27) * mm, "end": v(-446.78, -395.89) * mm});
            skLineSegment(sketch, "E2540", {"start": v(-446.78, -395.89) * mm, "end": v(-445.17, -395.57) * mm});
            skLineSegment(sketch, "E2541", {"start": v(-445.17, -395.57) * mm, "end": v(-443.56, -395.32) * mm});
            skLineSegment(sketch, "E2542", {"start": v(-443.56, -395.32) * mm, "end": v(-441.96, -395.13) * mm});
            skLineSegment(sketch, "E2543", {"start": v(-441.96, -395.13) * mm, "end": v(-440.36, -395.02) * mm});
            skLineSegment(sketch, "E2544", {"start": v(-440.36, -395.02) * mm, "end": v(-438.77, -394.98) * mm});
            skLineSegment(sketch, "E2545", {"start": v(-438.77, -394.98) * mm, "end": v(-437.18, -395.02) * mm});
            skLineSegment(sketch, "E2546", {"start": v(-437.18, -395.02) * mm, "end": v(-435.6, -395.15) * mm});
            skLineSegment(sketch, "E2547", {"start": v(-435.6, -395.15) * mm, "end": v(-434.03, -395.35) * mm});
            skLineSegment(sketch, "E2548", {"start": v(-434.03, -395.35) * mm, "end": v(-432.47, -395.64) * mm});
            skLineSegment(sketch, "E2549", {"start": v(-432.47, -395.64) * mm, "end": v(-430.92, -396.02) * mm});
            skLineSegment(sketch, "E2550", {"start": v(-430.92, -396.02) * mm, "end": v(-429.37, -396.49) * mm});
            skLineSegment(sketch, "E2551", {"start": v(-429.37, -396.49) * mm, "end": v(-427.84, -397.05) * mm});
            skLineSegment(sketch, "E2552", {"start": v(-427.84, -397.05) * mm, "end": v(-426.32, -397.71) * mm});
            skLineSegment(sketch, "E2553", {"start": v(-426.32, -397.71) * mm, "end": v(-424.81, -398.47) * mm});
            skLineSegment(sketch, "E2554", {"start": v(-424.81, -398.47) * mm, "end": v(-423.31, -399.33) * mm});
            skLineSegment(sketch, "E2555", {"start": v(-423.31, -399.33) * mm, "end": v(-421.83, -400.3) * mm});
            skLineSegment(sketch, "E2556", {"start": v(-421.83, -400.3) * mm, "end": v(-420.36, -401.38) * mm});
            skLineSegment(sketch, "E2557", {"start": v(-420.36, -401.38) * mm, "end": v(-418.9, -402.56) * mm});
            skLineSegment(sketch, "E2558", {"start": v(-418.9, -402.56) * mm, "end": v(-417.47, -403.86) * mm});
            skLineSegment(sketch, "E2559", {"start": v(-417.47, -403.86) * mm, "end": v(-416.04, -405.27) * mm});
            skLineSegment(sketch, "E2560", {"start": v(-416.04, -405.27) * mm, "end": v(-415.03, -406.37) * mm});
            skLineSegment(sketch, "E2561", {"start": v(-415.03, -406.37) * mm, "end": v(-414.1, -407.47) * mm});
            skLineSegment(sketch, "E2562", {"start": v(-414.1, -407.47) * mm, "end": v(-413.25, -408.58) * mm});
            skLineSegment(sketch, "E2563", {"start": v(-413.25, -408.58) * mm, "end": v(-412.46, -409.69) * mm});
            skLineSegment(sketch, "E2564", {"start": v(-412.46, -409.69) * mm, "end": v(-411.76, -410.8) * mm});
            skLineSegment(sketch, "E2565", {"start": v(-411.76, -410.8) * mm, "end": v(-411.12, -411.93) * mm});
            skLineSegment(sketch, "E2566", {"start": v(-411.12, -411.93) * mm, "end": v(-410.55, -413.06) * mm});
            skLineSegment(sketch, "E2567", {"start": v(-410.55, -413.06) * mm, "end": v(-410.04, -414.19) * mm});
            skLineSegment(sketch, "E2568", {"start": v(-410.04, -414.19) * mm, "end": v(-409.6, -415.33) * mm});
            skLineSegment(sketch, "E2569", {"start": v(-409.6, -415.33) * mm, "end": v(-409.22, -416.46) * mm});
            skLineSegment(sketch, "E2570", {"start": v(-409.22, -416.46) * mm, "end": v(-408.9, -417.6) * mm});
            skLineSegment(sketch, "E2571", {"start": v(-408.9, -417.6) * mm, "end": v(-408.64, -418.76) * mm});
            skLineSegment(sketch, "E2572", {"start": v(-408.64, -418.76) * mm, "end": v(-408.44, -419.9) * mm});
            skLineSegment(sketch, "E2573", {"start": v(-408.44, -419.9) * mm, "end": v(-408.29, -421.06) * mm});
            skLineSegment(sketch, "E2574", {"start": v(-408.29, -421.06) * mm, "end": v(-408.19, -422.22) * mm});
            skLineSegment(sketch, "E2575", {"start": v(-408.19, -422.22) * mm, "end": v(-408.14, -423.37) * mm});
            skLineSegment(sketch, "E2576", {"start": v(-408.14, -423.37) * mm, "end": v(-408.14, -424.54) * mm});
            skLineSegment(sketch, "E2577", {"start": v(-408.14, -424.54) * mm, "end": v(-408.18, -425.7) * mm});
            skLineSegment(sketch, "E2578", {"start": v(-408.18, -425.7) * mm, "end": v(-408.27, -426.86) * mm});
            skLineSegment(sketch, "E2579", {"start": v(-408.27, -426.86) * mm, "end": v(-408.4, -428.03) * mm});
            skLineSegment(sketch, "E2580", {"start": v(-408.4, -428.03) * mm, "end": v(-408.57, -429.2) * mm});
            skLineSegment(sketch, "E2581", {"start": v(-408.57, -429.2) * mm, "end": v(-408.78, -430.36) * mm});
            skLineSegment(sketch, "E2582", {"start": v(-408.78, -430.36) * mm, "end": v(-409.02, -431.53) * mm});
            skLineSegment(sketch, "E2583", {"start": v(-409.02, -431.53) * mm, "end": v(-409.3, -432.7) * mm});
            skLineSegment(sketch, "E2584", {"start": v(-409.3, -432.7) * mm, "end": v(-409.61, -433.87) * mm});
            skLineSegment(sketch, "E2585", {"start": v(-409.61, -433.87) * mm, "end": v(-409.95, -435.04) * mm});
            skLineSegment(sketch, "E2586", {"start": v(-409.95, -435.04) * mm, "end": v(-410.32, -436.2) * mm});
            skLineSegment(sketch, "E2587", {"start": v(-410.32, -436.2) * mm, "end": v(-410.71, -437.37) * mm});
            skLineSegment(sketch, "E2588", {"start": v(-410.71, -437.37) * mm, "end": v(-411.13, -438.54) * mm});
            skLineSegment(sketch, "E2589", {"start": v(-411.13, -438.54) * mm, "end": v(-411.57, -439.7) * mm});
            skLineSegment(sketch, "E2590", {"start": v(-411.57, -439.7) * mm, "end": v(-412.03, -440.87) * mm});
            skLineSegment(sketch, "E2591", {"start": v(-412.03, -440.87) * mm, "end": v(-412.5, -442.03) * mm});
            skLineSegment(sketch, "E2592", {"start": v(-412.5, -442.03) * mm, "end": v(-413, -443.2) * mm});
            skLineSegment(sketch, "E2593", {"start": v(-413, -443.2) * mm, "end": v(-413.5, -444.35) * mm});
            skLineSegment(sketch, "E2594", {"start": v(-413.5, -444.35) * mm, "end": v(-414.02, -445.5) * mm});
            skLineSegment(sketch, "E2595", {"start": v(-414.02, -445.5) * mm, "end": v(-414.55, -446.66) * mm});
            skLineSegment(sketch, "E2596", {"start": v(-414.55, -446.66) * mm, "end": v(-415.08, -447.8) * mm});
            skLineSegment(sketch, "E2597", {"start": v(-415.08, -447.8) * mm, "end": v(-415.62, -448.96) * mm});
            skLineSegment(sketch, "E2598", {"start": v(-415.62, -448.96) * mm, "end": v(-416.16, -450.1) * mm});
            skLineSegment(sketch, "E2599", {"start": v(-416.16, -450.1) * mm, "end": v(-416.71, -451.24) * mm});
            skLineSegment(sketch, "E2600", {"start": v(-416.71, -451.24) * mm, "end": v(-417.26, -452.37) * mm});
            skLineSegment(sketch, "E2601", {"start": v(-417.26, -452.37) * mm, "end": v(-417.8, -453.5) * mm});
            skLineSegment(sketch, "E2602", {"start": v(-417.8, -453.5) * mm, "end": v(-418.34, -454.63) * mm});
            skLineSegment(sketch, "E2603", {"start": v(-418.34, -454.63) * mm, "end": v(-418.87, -455.75) * mm});
            skLineSegment(sketch, "E2604", {"start": v(-418.87, -455.75) * mm, "end": v(-419.4, -456.87) * mm});
            skLineSegment(sketch, "E2605", {"start": v(-419.4, -456.87) * mm, "end": v(-419.9, -457.98) * mm});
            skLineSegment(sketch, "E2606", {"start": v(-419.9, -457.98) * mm, "end": v(-420.4, -459.09) * mm});
            skLineSegment(sketch, "E2607", {"start": v(-420.4, -459.09) * mm, "end": v(-420.9, -460.19) * mm});
            skLineSegment(sketch, "E2608", {"start": v(-420.9, -460.19) * mm, "end": v(-421.36, -461.28) * mm});
            skLineSegment(sketch, "E2609", {"start": v(-421.36, -461.28) * mm, "end": v(-421.82, -462.37) * mm});
            skLineSegment(sketch, "E2610", {"start": v(-421.82, -462.37) * mm, "end": v(-422.25, -463.45) * mm});
            skLineSegment(sketch, "E2611", {"start": v(-422.25, -463.45) * mm, "end": v(-422.65, -464.52) * mm});
            skLineSegment(sketch, "E2612", {"start": v(-422.65, -464.52) * mm, "end": v(-423.04, -465.59) * mm});
            skLineSegment(sketch, "E2613", {"start": v(-423.04, -465.59) * mm, "end": v(-423.4, -466.65) * mm});
            skLineSegment(sketch, "E2614", {"start": v(-423.4, -466.65) * mm, "end": v(-423.73, -467.7) * mm});
            skLineSegment(sketch, "E2615", {"start": v(-423.73, -467.7) * mm, "end": v(-424.02, -468.74) * mm});
            skLineSegment(sketch, "E2616", {"start": v(-424.02, -468.74) * mm, "end": v(-424.29, -469.78) * mm});
            skLineSegment(sketch, "E2617", {"start": v(-424.29, -469.78) * mm, "end": v(-424.52, -470.8) * mm});
            skLineSegment(sketch, "E2618", {"start": v(-424.52, -470.8) * mm, "end": v(-424.72, -471.82) * mm});
            skLineSegment(sketch, "E2619", {"start": v(-424.72, -471.82) * mm, "end": v(-424.87, -472.83) * mm});
            skLineSegment(sketch, "E2620", {"start": v(-424.87, -472.83) * mm, "end": v(-424.99, -473.83) * mm});
            skLineSegment(sketch, "E2621", {"start": v(-424.99, -473.83) * mm, "end": v(-425.06, -474.83) * mm});
            skLineSegment(sketch, "E2622", {"start": v(-425.06, -474.83) * mm, "end": v(-425.09, -475.8) * mm});
            skLineSegment(sketch, "E2623", {"start": v(-425.09, -475.8) * mm, "end": v(-425.07, -476.78) * mm});
            skLineSegment(sketch, "E2624", {"start": v(-425.07, -476.78) * mm, "end": v(-425, -477.74) * mm});
            skLineSegment(sketch, "E2625", {"start": v(-425, -477.74) * mm, "end": v(-424.89, -478.69) * mm});
            skLineSegment(sketch, "E2626", {"start": v(-424.89, -478.69) * mm, "end": v(-424.71, -479.63) * mm});
            skLineSegment(sketch, "E2627", {"start": v(-424.71, -479.63) * mm, "end": v(-424.49, -480.56) * mm});
            skLineSegment(sketch, "E2628", {"start": v(-424.49, -480.56) * mm, "end": v(-424.2, -481.47) * mm});
            skLineSegment(sketch, "E2629", {"start": v(-424.2, -481.47) * mm, "end": v(-423.87, -482.38) * mm});
            skLineSegment(sketch, "E2630", {"start": v(-423.87, -482.38) * mm, "end": v(-423.47, -483.27) * mm});
            skLineSegment(sketch, "E2631", {"start": v(-423.47, -483.27) * mm, "end": v(-423, -484.15) * mm});
            skLineSegment(sketch, "E2632", {"start": v(-423, -484.15) * mm, "end": v(-422.47, -485.02) * mm});
            skLineSegment(sketch, "E2633", {"start": v(-422.47, -485.02) * mm, "end": v(-421.88, -485.88) * mm});
            skLineSegment(sketch, "E2634", {"start": v(-421.88, -485.88) * mm, "end": v(-421.21, -486.72) * mm});
            skLineSegment(sketch, "E2635", {"start": v(-421.21, -486.72) * mm, "end": v(-420.48, -487.55) * mm});
            skLineSegment(sketch, "E2636", {"start": v(-420.48, -487.55) * mm, "end": v(-419.67, -488.37) * mm});
            skLineSegment(sketch, "E2637", {"start": v(-419.67, -488.37) * mm, "end": v(-418.79, -489.18) * mm});
            skLineSegment(sketch, "E2638", {"start": v(-418.79, -489.18) * mm, "end": v(-417.83, -489.97) * mm});
            skLineSegment(sketch, "E2639", {"start": v(-417.83, -489.97) * mm, "end": v(-416.8, -490.74) * mm});
            skLineSegment(sketch, "E2640", {"start": v(-416.8, -490.74) * mm, "end": v(-415.67, -491.5) * mm});
            skLineSegment(sketch, "E2641", {"start": v(-415.67, -491.5) * mm, "end": v(-414.58, -492.17) * mm});
            skLineSegment(sketch, "E2642", {"start": v(-414.58, -492.17) * mm, "end": v(-413.5, -492.76) * mm});
            skLineSegment(sketch, "E2643", {"start": v(-413.5, -492.76) * mm, "end": v(-412.41, -493.26) * mm});
            skLineSegment(sketch, "E2644", {"start": v(-412.41, -493.26) * mm, "end": v(-411.34, -493.7) * mm});
            skLineSegment(sketch, "E2645", {"start": v(-411.34, -493.7) * mm, "end": v(-410.27, -494.04) * mm});
            skLineSegment(sketch, "E2646", {"start": v(-410.27, -494.04) * mm, "end": v(-409.2, -494.32) * mm});
            skLineSegment(sketch, "E2647", {"start": v(-409.2, -494.32) * mm, "end": v(-408.15, -494.52) * mm});
            skLineSegment(sketch, "E2648", {"start": v(-408.15, -494.52) * mm, "end": v(-407.1, -494.66) * mm});
            skLineSegment(sketch, "E2649", {"start": v(-407.1, -494.66) * mm, "end": v(-406.04, -494.73) * mm});
            skLineSegment(sketch, "E2650", {"start": v(-406.04, -494.73) * mm, "end": v(-405, -494.74) * mm});
            skLineSegment(sketch, "E2651", {"start": v(-405, -494.74) * mm, "end": v(-403.95, -494.69) * mm});
            skLineSegment(sketch, "E2652", {"start": v(-403.95, -494.69) * mm, "end": v(-402.9, -494.58) * mm});
            skLineSegment(sketch, "E2653", {"start": v(-402.9, -494.58) * mm, "end": v(-401.87, -494.4) * mm});
            skLineSegment(sketch, "E2654", {"start": v(-401.87, -494.4) * mm, "end": v(-400.84, -494.19) * mm});
            skLineSegment(sketch, "E2655", {"start": v(-400.84, -494.19) * mm, "end": v(-399.8, -493.91) * mm});
            skLineSegment(sketch, "E2656", {"start": v(-399.8, -493.91) * mm, "end": v(-398.77, -493.59) * mm});
            skLineSegment(sketch, "E2657", {"start": v(-398.77, -493.59) * mm, "end": v(-397.75, -493.22) * mm});
            skLineSegment(sketch, "E2658", {"start": v(-397.75, -493.22) * mm, "end": v(-396.72, -492.8) * mm});
            skLineSegment(sketch, "E2659", {"start": v(-396.72, -492.8) * mm, "end": v(-395.7, -492.35) * mm});
            skLineSegment(sketch, "E2660", {"start": v(-395.7, -492.35) * mm, "end": v(-394.67, -491.86) * mm});
            skLineSegment(sketch, "E2661", {"start": v(-394.67, -491.86) * mm, "end": v(-393.65, -491.33) * mm});
            skLineSegment(sketch, "E2662", {"start": v(-393.65, -491.33) * mm, "end": v(-392.63, -490.77) * mm});
            skLineSegment(sketch, "E2663", {"start": v(-392.63, -490.77) * mm, "end": v(-391.6, -490.17) * mm});
            skLineSegment(sketch, "E2664", {"start": v(-391.6, -490.17) * mm, "end": v(-390.58, -489.55) * mm});
            skLineSegment(sketch, "E2665", {"start": v(-390.58, -489.55) * mm, "end": v(-389.56, -488.9) * mm});
            skLineSegment(sketch, "E2666", {"start": v(-389.56, -488.9) * mm, "end": v(-388.54, -488.22) * mm});
            skLineSegment(sketch, "E2667", {"start": v(-388.54, -488.22) * mm, "end": v(-387.51, -487.52) * mm});
            skLineSegment(sketch, "E2668", {"start": v(-387.51, -487.52) * mm, "end": v(-386.49, -486.8) * mm});
            skLineSegment(sketch, "E2669", {"start": v(-386.49, -486.8) * mm, "end": v(-385.46, -486.07) * mm});
            skLineSegment(sketch, "E2670", {"start": v(-385.46, -486.07) * mm, "end": v(-384.43, -485.32) * mm});
            skLineSegment(sketch, "E2671", {"start": v(-384.43, -485.32) * mm, "end": v(-383.4, -484.57) * mm});
            skLineSegment(sketch, "E2672", {"start": v(-383.4, -484.57) * mm, "end": v(-382.37, -483.8) * mm});
            skLineSegment(sketch, "E2673", {"start": v(-382.37, -483.8) * mm, "end": v(-381.34, -483.02) * mm});
            skLineSegment(sketch, "E2674", {"start": v(-381.34, -483.02) * mm, "end": v(-380.3, -482.24) * mm});
            skLineSegment(sketch, "E2675", {"start": v(-380.3, -482.24) * mm, "end": v(-379.26, -481.46) * mm});
            skLineSegment(sketch, "E2676", {"start": v(-379.26, -481.46) * mm, "end": v(-378.22, -480.67) * mm});
            skLineSegment(sketch, "E2677", {"start": v(-378.22, -480.67) * mm, "end": v(-377.17, -479.9) * mm});
            skLineSegment(sketch, "E2678", {"start": v(-377.17, -479.9) * mm, "end": v(-376.12, -479.12) * mm});
            skLineSegment(sketch, "E2679", {"start": v(-376.12, -479.12) * mm, "end": v(-375.06, -478.36) * mm});
            skLineSegment(sketch, "E2680", {"start": v(-375.06, -478.36) * mm, "end": v(-374, -477.6) * mm});
            skLineSegment(sketch, "E2681", {"start": v(-374, -477.6) * mm, "end": v(-372.94, -476.86) * mm});
            skLineSegment(sketch, "E2682", {"start": v(-372.94, -476.86) * mm, "end": v(-371.87, -476.13) * mm});
            skLineSegment(sketch, "E2683", {"start": v(-371.87, -476.13) * mm, "end": v(-370.8, -475.42) * mm});
            skLineSegment(sketch, "E2684", {"start": v(-370.8, -475.42) * mm, "end": v(-369.71, -474.73) * mm});
            skLineSegment(sketch, "E2685", {"start": v(-369.71, -474.73) * mm, "end": v(-368.62, -474.06) * mm});
            skLineSegment(sketch, "E2686", {"start": v(-368.62, -474.06) * mm, "end": v(-367.53, -473.42) * mm});
            skLineSegment(sketch, "E2687", {"start": v(-367.53, -473.42) * mm, "end": v(-366.43, -472.8) * mm});
            skLineSegment(sketch, "E2688", {"start": v(-366.43, -472.8) * mm, "end": v(-365.33, -472.22) * mm});
            skLineSegment(sketch, "E2689", {"start": v(-365.33, -472.22) * mm, "end": v(-364.22, -471.67) * mm});
            skLineSegment(sketch, "E2690", {"start": v(-364.22, -471.67) * mm, "end": v(-363.1, -471.15) * mm});
            skLineSegment(sketch, "E2691", {"start": v(-363.1, -471.15) * mm, "end": v(-361.97, -470.67) * mm});
            skLineSegment(sketch, "E2692", {"start": v(-361.97, -470.67) * mm, "end": v(-360.83, -470.23) * mm});
            skLineSegment(sketch, "E2693", {"start": v(-360.83, -470.23) * mm, "end": v(-359.7, -469.84) * mm});
            skLineSegment(sketch, "E2694", {"start": v(-359.7, -469.84) * mm, "end": v(-358.54, -469.48) * mm});
            skLineSegment(sketch, "E2695", {"start": v(-358.54, -469.48) * mm, "end": v(-357.38, -469.18) * mm});
            skLineSegment(sketch, "E2696", {"start": v(-357.38, -469.18) * mm, "end": v(-356.21, -468.92) * mm});
            skLineSegment(sketch, "E2697", {"start": v(-356.21, -468.92) * mm, "end": v(-355.03, -468.72) * mm});
            skLineSegment(sketch, "E2698", {"start": v(-355.03, -468.72) * mm, "end": v(-353.85, -468.57) * mm});
            skLineSegment(sketch, "E2699", {"start": v(-353.85, -468.57) * mm, "end": v(-352.65, -468.48) * mm});
            skLineSegment(sketch, "E2700", {"start": v(-352.65, -468.48) * mm, "end": v(-351.44, -468.45) * mm});
            skLineSegment(sketch, "E2701", {"start": v(-351.44, -468.45) * mm, "end": v(-350.22, -468.48) * mm});
            skLineSegment(sketch, "E2702", {"start": v(-350.22, -468.48) * mm, "end": v(-349, -468.57) * mm});
            skLineSegment(sketch, "E2703", {"start": v(-349, -468.57) * mm, "end": v(-347.76, -468.73) * mm});
            skLineSegment(sketch, "E2704", {"start": v(-347.76, -468.73) * mm, "end": v(-346.5, -468.97) * mm});
            skLineSegment(sketch, "E2705", {"start": v(-346.5, -468.97) * mm, "end": v(-345.24, -469.27) * mm});
            skLineSegment(sketch, "E2706", {"start": v(-345.24, -469.27) * mm, "end": v(-343.97, -469.65) * mm});
            skLineSegment(sketch, "E2707", {"start": v(-343.97, -469.65) * mm, "end": v(-342.69, -470.1) * mm});
            skLineSegment(sketch, "E2708", {"start": v(-342.69, -470.1) * mm, "end": v(-341.39, -470.64) * mm});
            skLineSegment(sketch, "E2709", {"start": v(-341.39, -470.64) * mm, "end": v(-340.08, -471.25) * mm});
            skLineSegment(sketch, "E2710", {"start": v(-340.08, -471.25) * mm, "end": v(-338.76, -471.95) * mm});
            skLineSegment(sketch, "E2711", {"start": v(-338.76, -471.95) * mm, "end": v(-337.42, -472.74) * mm});
            skLineSegment(sketch, "E2712", {"start": v(-337.42, -472.74) * mm, "end": v(-336.07, -473.61) * mm});
            skLineSegment(sketch, "E2713", {"start": v(-336.07, -473.61) * mm, "end": v(-334.63, -474.65) * mm});
            skLineSegment(sketch, "E2714", {"start": v(-334.63, -474.65) * mm, "end": v(-333.24, -475.75) * mm});
            skLineSegment(sketch, "E2715", {"start": v(-333.24, -475.75) * mm, "end": v(-331.91, -476.9) * mm});
            skLineSegment(sketch, "E2716", {"start": v(-331.91, -476.9) * mm, "end": v(-330.65, -478.13) * mm});
            skLineSegment(sketch, "E2717", {"start": v(-330.65, -478.13) * mm, "end": v(-329.44, -479.4) * mm});
            skLineSegment(sketch, "E2718", {"start": v(-329.44, -479.4) * mm, "end": v(-328.3, -480.73) * mm});
            skLineSegment(sketch, "E2719", {"start": v(-328.3, -480.73) * mm, "end": v(-327.23, -482.1) * mm});
            skLineSegment(sketch, "E2720", {"start": v(-327.23, -482.1) * mm, "end": v(-326.23, -483.53) * mm});
            skLineSegment(sketch, "E2721", {"start": v(-326.23, -483.53) * mm, "end": v(-325.3, -485) * mm});
            skLineSegment(sketch, "E2722", {"start": v(-325.3, -485) * mm, "end": v(-324.44, -486.5) * mm});
            skLineSegment(sketch, "E2723", {"start": v(-324.44, -486.5) * mm, "end": v(-323.66, -488.05) * mm});
            skLineSegment(sketch, "E2724", {"start": v(-323.66, -488.05) * mm, "end": v(-322.96, -489.63) * mm});
            skLineSegment(sketch, "E2725", {"start": v(-322.96, -489.63) * mm, "end": v(-322.34, -491.24) * mm});
            skLineSegment(sketch, "E2726", {"start": v(-322.34, -491.24) * mm, "end": v(-321.8, -492.87) * mm});
            skLineSegment(sketch, "E2727", {"start": v(-321.8, -492.87) * mm, "end": v(-321.34, -494.53) * mm});
            skLineSegment(sketch, "E2728", {"start": v(-321.34, -494.53) * mm, "end": v(-320.98, -496.22) * mm});
            skLineSegment(sketch, "E2729", {"start": v(-320.98, -496.22) * mm, "end": v(-320.7, -497.92) * mm});
            skLineSegment(sketch, "E2730", {"start": v(-320.7, -497.92) * mm, "end": v(-320.51, -499.64) * mm});
            skLineSegment(sketch, "E2731", {"start": v(-320.51, -499.64) * mm, "end": v(-320.42, -501.36) * mm});
            skLineSegment(sketch, "E2732", {"start": v(-320.42, -501.36) * mm, "end": v(-320.42, -503.1) * mm});
            skLineSegment(sketch, "E2733", {"start": v(-320.42, -503.1) * mm, "end": v(-320.52, -504.85) * mm});
            skLineSegment(sketch, "E2734", {"start": v(-320.52, -504.85) * mm, "end": v(-320.72, -506.6) * mm});
            skLineSegment(sketch, "E2735", {"start": v(-320.72, -506.6) * mm, "end": v(-321.03, -508.34) * mm});
            skLineSegment(sketch, "E2736", {"start": v(-321.03, -508.34) * mm, "end": v(-321.43, -510.08) * mm});
            skLineSegment(sketch, "E2737", {"start": v(-321.43, -510.08) * mm, "end": v(-321.83, -511.51) * mm});
            skLineSegment(sketch, "E2738", {"start": v(-321.83, -511.51) * mm, "end": v(-322.27, -512.95) * mm});
            skLineSegment(sketch, "E2739", {"start": v(-322.27, -512.95) * mm, "end": v(-322.74, -514.4) * mm});
            skLineSegment(sketch, "E2740", {"start": v(-322.74, -514.4) * mm, "end": v(-323.24, -515.84) * mm});
            skLineSegment(sketch, "E2741", {"start": v(-323.24, -515.84) * mm, "end": v(-323.77, -517.29) * mm});
            skLineSegment(sketch, "E2742", {"start": v(-323.77, -517.29) * mm, "end": v(-324.31, -518.74) * mm});
            skLineSegment(sketch, "E2743", {"start": v(-324.31, -518.74) * mm, "end": v(-324.87, -520.19) * mm});
            skLineSegment(sketch, "E2744", {"start": v(-324.87, -520.19) * mm, "end": v(-325.44, -521.64) * mm});
            skLineSegment(sketch, "E2745", {"start": v(-325.44, -521.64) * mm, "end": v(-326, -523.1) * mm});
            skLineSegment(sketch, "E2746", {"start": v(-326, -523.1) * mm, "end": v(-326.57, -524.54) * mm});
            skLineSegment(sketch, "E2747", {"start": v(-326.57, -524.54) * mm, "end": v(-327.13, -525.98) * mm});
            skLineSegment(sketch, "E2748", {"start": v(-327.13, -525.98) * mm, "end": v(-327.67, -527.42) * mm});
            skLineSegment(sketch, "E2749", {"start": v(-327.67, -527.42) * mm, "end": v(-328.2, -528.85) * mm});
            skLineSegment(sketch, "E2750", {"start": v(-328.2, -528.85) * mm, "end": v(-328.7, -530.28) * mm});
            skLineSegment(sketch, "E2751", {"start": v(-328.7, -530.28) * mm, "end": v(-329.17, -531.7) * mm});
            skLineSegment(sketch, "E2752", {"start": v(-329.17, -531.7) * mm, "end": v(-329.6, -533.1) * mm});
            skLineSegment(sketch, "E2753", {"start": v(-329.6, -533.1) * mm, "end": v(-330, -534.5) * mm});
            skLineSegment(sketch, "E2754", {"start": v(-330, -534.5) * mm, "end": v(-330.35, -535.88) * mm});
            skLineSegment(sketch, "E2755", {"start": v(-330.35, -535.88) * mm, "end": v(-330.66, -537.25) * mm});
            skLineSegment(sketch, "E2756", {"start": v(-330.66, -537.25) * mm, "end": v(-330.9, -538.6) * mm});
            skLineSegment(sketch, "E2757", {"start": v(-330.9, -538.6) * mm, "end": v(-331.09, -539.94) * mm});
            skLineSegment(sketch, "E2758", {"start": v(-331.09, -539.94) * mm, "end": v(-331.2, -541.27) * mm});
            skLineSegment(sketch, "E2759", {"start": v(-331.2, -541.27) * mm, "end": v(-331.25, -542.57) * mm});
            skLineSegment(sketch, "E2760", {"start": v(-331.25, -542.57) * mm, "end": v(-331.22, -543.86) * mm});
            skLineSegment(sketch, "E2761", {"start": v(-331.22, -543.86) * mm, "end": v(-331.11, -545.12) * mm});
            skLineSegment(sketch, "E2762", {"start": v(-331.11, -545.12) * mm, "end": v(-330.91, -546.37) * mm});
            skLineSegment(sketch, "E2763", {"start": v(-330.91, -546.37) * mm, "end": v(-330.62, -547.59) * mm});
            skLineSegment(sketch, "E2764", {"start": v(-330.62, -547.59) * mm, "end": v(-330.23, -548.78) * mm});
            skLineSegment(sketch, "E2765", {"start": v(-330.23, -548.78) * mm, "end": v(-329.74, -549.96) * mm});
            skLineSegment(sketch, "E2766", {"start": v(-329.74, -549.96) * mm, "end": v(-329.13, -551.1) * mm});
            skLineSegment(sketch, "E2767", {"start": v(-329.13, -551.1) * mm, "end": v(-328.42, -552.22) * mm});
            skLineSegment(sketch, "E2768", {"start": v(-328.42, -552.22) * mm, "end": v(-327.58, -553.3) * mm});
            skLineSegment(sketch, "E2769", {"start": v(-327.58, -553.3) * mm, "end": v(-326.62, -554.37) * mm});
            skLineSegment(sketch, "E2770", {"start": v(-326.62, -554.37) * mm, "end": v(-325.53, -555.4) * mm});
            skLineSegment(sketch, "E2771", {"start": v(-325.53, -555.4) * mm, "end": v(-324.3, -556.39) * mm});
            skLineSegment(sketch, "E2772", {"start": v(-324.3, -556.39) * mm, "end": v(-322.94, -557.35) * mm});
            skLineSegment(sketch, "E2773", {"start": v(-322.94, -557.35) * mm, "end": v(-321.42, -558.28) * mm});
            skLineSegment(sketch, "E2774", {"start": v(-321.42, -558.28) * mm, "end": v(-319.76, -559.17) * mm});
            skLineSegment(sketch, "E2775", {"start": v(-319.76, -559.17) * mm, "end": v(-317.94, -560.02) * mm});
            skLineSegment(sketch, "E2776", {"start": v(-317.94, -560.02) * mm, "end": v(-316.17, -560.7) * mm});
            skLineSegment(sketch, "E2777", {"start": v(-316.17, -560.7) * mm, "end": v(-314.46, -561.17) * mm});
            skLineSegment(sketch, "E2778", {"start": v(-314.46, -561.17) * mm, "end": v(-312.79, -561.44) * mm});
            skLineSegment(sketch, "E2779", {"start": v(-312.79, -561.44) * mm, "end": v(-311.17, -561.53) * mm});
            skLineSegment(sketch, "E2780", {"start": v(-311.17, -561.53) * mm, "end": v(-309.6, -561.43) * mm});
            skLineSegment(sketch, "E2781", {"start": v(-309.6, -561.43) * mm, "end": v(-308.07, -561.18) * mm});
            skLineSegment(sketch, "E2782", {"start": v(-308.07, -561.18) * mm, "end": v(-306.58, -560.77) * mm});
            skLineSegment(sketch, "E2783", {"start": v(-306.58, -560.77) * mm, "end": v(-305.14, -560.22) * mm});
            skLineSegment(sketch, "E2784", {"start": v(-305.14, -560.22) * mm, "end": v(-303.74, -559.55) * mm});
            skLineSegment(sketch, "E2785", {"start": v(-303.74, -559.55) * mm, "end": v(-302.37, -558.76) * mm});
            skLineSegment(sketch, "E2786", {"start": v(-302.37, -558.76) * mm, "end": v(-301.04, -557.86) * mm});
            skLineSegment(sketch, "E2787", {"start": v(-301.04, -557.86) * mm, "end": v(-299.75, -556.87) * mm});
            skLineSegment(sketch, "E2788", {"start": v(-299.75, -556.87) * mm, "end": v(-298.48, -555.8) * mm});
            skLineSegment(sketch, "E2789", {"start": v(-298.48, -555.8) * mm, "end": v(-297.25, -554.66) * mm});
            skLineSegment(sketch, "E2790", {"start": v(-297.25, -554.66) * mm, "end": v(-296.05, -553.47) * mm});
            skLineSegment(sketch, "E2791", {"start": v(-296.05, -553.47) * mm, "end": v(-294.87, -552.23) * mm});
            skLineSegment(sketch, "E2792", {"start": v(-294.87, -552.23) * mm, "end": v(-293.72, -550.95) * mm});
            skLineSegment(sketch, "E2793", {"start": v(-293.72, -550.95) * mm, "end": v(-292.59, -549.66) * mm});
            skLineSegment(sketch, "E2794", {"start": v(-292.59, -549.66) * mm, "end": v(-291.48, -548.35) * mm});
            skLineSegment(sketch, "E2795", {"start": v(-291.48, -548.35) * mm, "end": v(-290.4, -547.04) * mm});
            skLineSegment(sketch, "E2796", {"start": v(-290.4, -547.04) * mm, "end": v(-289.33, -545.75) * mm});
            skLineSegment(sketch, "E2797", {"start": v(-289.33, -545.75) * mm, "end": v(-288.28, -544.49) * mm});
            skLineSegment(sketch, "E2798", {"start": v(-288.28, -544.49) * mm, "end": v(-287.15, -543.15) * mm});
            skLineSegment(sketch, "E2799", {"start": v(-287.15, -543.15) * mm, "end": v(-286, -541.83) * mm});
            skLineSegment(sketch, "E2800", {"start": v(-286, -541.83) * mm, "end": v(-284.83, -540.54) * mm});
            skLineSegment(sketch, "E2801", {"start": v(-284.83, -540.54) * mm, "end": v(-283.65, -539.28) * mm});
            skLineSegment(sketch, "E2802", {"start": v(-283.65, -539.28) * mm, "end": v(-282.45, -538.04) * mm});
            skLineSegment(sketch, "E2803", {"start": v(-282.45, -538.04) * mm, "end": v(-281.23, -536.84) * mm});
            skLineSegment(sketch, "E2804", {"start": v(-281.23, -536.84) * mm, "end": v(-279.99, -535.68) * mm});
            skLineSegment(sketch, "E2805", {"start": v(-279.99, -535.68) * mm, "end": v(-278.73, -534.56) * mm});
            skLineSegment(sketch, "E2806", {"start": v(-278.73, -534.56) * mm, "end": v(-277.45, -533.48) * mm});
            skLineSegment(sketch, "E2807", {"start": v(-277.45, -533.48) * mm, "end": v(-276.16, -532.45) * mm});
            skLineSegment(sketch, "E2808", {"start": v(-276.16, -532.45) * mm, "end": v(-274.84, -531.47) * mm});
            skLineSegment(sketch, "E2809", {"start": v(-274.84, -531.47) * mm, "end": v(-273.5, -530.55) * mm});
            skLineSegment(sketch, "E2810", {"start": v(-273.5, -530.55) * mm, "end": v(-272.15, -529.68) * mm});
            skLineSegment(sketch, "E2811", {"start": v(-272.15, -529.68) * mm, "end": v(-270.77, -528.87) * mm});
            skLineSegment(sketch, "E2812", {"start": v(-270.77, -528.87) * mm, "end": v(-269.37, -528.13) * mm});
            skLineSegment(sketch, "E2813", {"start": v(-269.37, -528.13) * mm, "end": v(-267.95, -527.46) * mm});
            skLineSegment(sketch, "E2814", {"start": v(-267.95, -527.46) * mm, "end": v(-266.5, -526.85) * mm});
            skLineSegment(sketch, "E2815", {"start": v(-266.5, -526.85) * mm, "end": v(-265.04, -526.32) * mm});
            skLineSegment(sketch, "E2816", {"start": v(-265.04, -526.32) * mm, "end": v(-263.55, -525.86) * mm});
            skLineSegment(sketch, "E2817", {"start": v(-263.55, -525.86) * mm, "end": v(-262.03, -525.49) * mm});
            skLineSegment(sketch, "E2818", {"start": v(-262.03, -525.49) * mm, "end": v(-260.5, -525.2) * mm});
            skLineSegment(sketch, "E2819", {"start": v(-260.5, -525.2) * mm, "end": v(-258.93, -525) * mm});
            skLineSegment(sketch, "E2820", {"start": v(-258.93, -525) * mm, "end": v(-257.35, -524.88) * mm});
            skLineSegment(sketch, "E2821", {"start": v(-257.35, -524.88) * mm, "end": v(-255.73, -524.86) * mm});
            skLineSegment(sketch, "E2822", {"start": v(-255.73, -524.86) * mm, "end": v(-254.1, -524.94) * mm});
            skLineSegment(sketch, "E2823", {"start": v(-254.1, -524.94) * mm, "end": v(-252.43, -525.11) * mm});
            skLineSegment(sketch, "E2824", {"start": v(-252.43, -525.11) * mm, "end": v(-250.74, -525.4) * mm});
            skLineSegment(sketch, "E2825", {"start": v(-250.74, -525.4) * mm, "end": v(-249.03, -525.78) * mm});
            skLineSegment(sketch, "E2826", {"start": v(-249.03, -525.78) * mm, "end": v(-247.29, -526.28) * mm});
            skLineSegment(sketch, "E2827", {"start": v(-247.29, -526.28) * mm, "end": v(-245.52, -526.89) * mm});
            skLineSegment(sketch, "E2828", {"start": v(-245.52, -526.89) * mm, "end": v(-243.72, -527.62) * mm});
            skLineSegment(sketch, "E2829", {"start": v(-243.72, -527.62) * mm, "end": v(-242.09, -528.37) * mm});
            skLineSegment(sketch, "E2830", {"start": v(-242.09, -528.37) * mm, "end": v(-240.5, -529.2) * mm});
            skLineSegment(sketch, "E2831", {"start": v(-240.5, -529.2) * mm, "end": v(-238.97, -530.1) * mm});
            skLineSegment(sketch, "E2832", {"start": v(-238.97, -530.1) * mm, "end": v(-237.5, -531.06) * mm});
            skLineSegment(sketch, "E2833", {"start": v(-237.5, -531.06) * mm, "end": v(-236.07, -532.1) * mm});
            skLineSegment(sketch, "E2834", {"start": v(-236.07, -532.1) * mm, "end": v(-234.7, -533.19) * mm});
            skLineSegment(sketch, "E2835", {"start": v(-234.7, -533.19) * mm, "end": v(-233.4, -534.34) * mm});
            skLineSegment(sketch, "E2836", {"start": v(-233.4, -534.34) * mm, "end": v(-232.16, -535.55) * mm});
            skLineSegment(sketch, "E2837", {"start": v(-232.16, -535.55) * mm, "end": v(-230.98, -536.82) * mm});
            skLineSegment(sketch, "E2838", {"start": v(-230.98, -536.82) * mm, "end": v(-229.87, -538.14) * mm});
            skLineSegment(sketch, "E2839", {"start": v(-229.87, -538.14) * mm, "end": v(-228.82, -539.5) * mm});
            skLineSegment(sketch, "E2840", {"start": v(-228.82, -539.5) * mm, "end": v(-227.84, -540.92) * mm});
            skLineSegment(sketch, "E2841", {"start": v(-227.84, -540.92) * mm, "end": v(-226.94, -542.39) * mm});
            skLineSegment(sketch, "E2842", {"start": v(-226.94, -542.39) * mm, "end": v(-226.1, -543.9) * mm});
            skLineSegment(sketch, "E2843", {"start": v(-226.1, -543.9) * mm, "end": v(-225.35, -545.44) * mm});
            skLineSegment(sketch, "E2844", {"start": v(-225.35, -545.44) * mm, "end": v(-224.67, -547.02) * mm});
            skLineSegment(sketch, "E2845", {"start": v(-224.67, -547.02) * mm, "end": v(-224.07, -548.64) * mm});
            skLineSegment(sketch, "E2846", {"start": v(-224.07, -548.64) * mm, "end": v(-223.55, -550.3) * mm});
            skLineSegment(sketch, "E2847", {"start": v(-223.55, -550.3) * mm, "end": v(-223.1, -551.98) * mm});
            skLineSegment(sketch, "E2848", {"start": v(-223.1, -551.98) * mm, "end": v(-222.76, -553.69) * mm});
            skLineSegment(sketch, "E2849", {"start": v(-222.76, -553.69) * mm, "end": v(-222.49, -555.43) * mm});
            skLineSegment(sketch, "E2850", {"start": v(-222.49, -555.43) * mm, "end": v(-222.31, -557.19) * mm});
            skLineSegment(sketch, "E2851", {"start": v(-222.31, -557.19) * mm, "end": v(-222.23, -558.97) * mm});
            skLineSegment(sketch, "E2852", {"start": v(-222.23, -558.97) * mm, "end": v(-222.23, -560.77) * mm});
            skLineSegment(sketch, "E2853", {"start": v(-222.23, -560.77) * mm, "end": v(-222.34, -562.58) * mm});
            skLineSegment(sketch, "E2854", {"start": v(-222.34, -562.58) * mm, "end": v(-222.48, -564.1) * mm});
            skLineSegment(sketch, "E2855", {"start": v(-222.48, -564.1) * mm, "end": v(-222.66, -565.6) * mm});
            skLineSegment(sketch, "E2856", {"start": v(-222.66, -565.6) * mm, "end": v(-222.87, -567.12) * mm});
            skLineSegment(sketch, "E2857", {"start": v(-222.87, -567.12) * mm, "end": v(-223.11, -568.64) * mm});
            skLineSegment(sketch, "E2858", {"start": v(-223.11, -568.64) * mm, "end": v(-223.37, -570.15) * mm});
            skLineSegment(sketch, "E2859", {"start": v(-223.37, -570.15) * mm, "end": v(-223.64, -571.66) * mm});
            skLineSegment(sketch, "E2860", {"start": v(-223.64, -571.66) * mm, "end": v(-223.93, -573.17) * mm});
            skLineSegment(sketch, "E2861", {"start": v(-223.93, -573.17) * mm, "end": v(-224.22, -574.67) * mm});
            skLineSegment(sketch, "E2862", {"start": v(-224.22, -574.67) * mm, "end": v(-224.5, -576.16) * mm});
            skLineSegment(sketch, "E2863", {"start": v(-224.5, -576.16) * mm, "end": v(-224.8, -577.64) * mm});
            skLineSegment(sketch, "E2864", {"start": v(-224.8, -577.64) * mm, "end": v(-225.07, -579.1) * mm});
            skLineSegment(sketch, "E2865", {"start": v(-225.07, -579.1) * mm, "end": v(-225.32, -580.57) * mm});
            skLineSegment(sketch, "E2866", {"start": v(-225.32, -580.57) * mm, "end": v(-225.56, -582) * mm});
            skLineSegment(sketch, "E2867", {"start": v(-225.56, -582) * mm, "end": v(-225.77, -583.43) * mm});
            skLineSegment(sketch, "E2868", {"start": v(-225.77, -583.43) * mm, "end": v(-225.95, -584.84) * mm});
            skLineSegment(sketch, "E2869", {"start": v(-225.95, -584.84) * mm, "end": v(-226.1, -586.22) * mm});
            skLineSegment(sketch, "E2870", {"start": v(-226.1, -586.22) * mm, "end": v(-226.2, -587.58) * mm});
            skLineSegment(sketch, "E2871", {"start": v(-226.2, -587.58) * mm, "end": v(-226.25, -588.93) * mm});
            skLineSegment(sketch, "E2872", {"start": v(-226.25, -588.93) * mm, "end": v(-226.25, -590.24) * mm});
            skLineSegment(sketch, "E2873", {"start": v(-226.25, -590.24) * mm, "end": v(-226.2, -591.53) * mm});
            skLineSegment(sketch, "E2874", {"start": v(-226.2, -591.53) * mm, "end": v(-226.07, -592.79) * mm});
            skLineSegment(sketch, "E2875", {"start": v(-226.07, -592.79) * mm, "end": v(-225.88, -594.02) * mm});
            skLineSegment(sketch, "E2876", {"start": v(-225.88, -594.02) * mm, "end": v(-225.62, -595.22) * mm});
            skLineSegment(sketch, "E2877", {"start": v(-225.62, -595.22) * mm, "end": v(-225.28, -596.38) * mm});
            skLineSegment(sketch, "E2878", {"start": v(-225.28, -596.38) * mm, "end": v(-224.86, -597.52) * mm});
            skLineSegment(sketch, "E2879", {"start": v(-224.86, -597.52) * mm, "end": v(-224.34, -598.6) * mm});
            skLineSegment(sketch, "E2880", {"start": v(-224.34, -598.6) * mm, "end": v(-223.74, -599.66) * mm});
            skLineSegment(sketch, "E2881", {"start": v(-223.74, -599.66) * mm, "end": v(-223.03, -600.68) * mm});
            skLineSegment(sketch, "E2882", {"start": v(-223.03, -600.68) * mm, "end": v(-222.22, -601.65) * mm});
            skLineSegment(sketch, "E2883", {"start": v(-222.22, -601.65) * mm, "end": v(-221.3, -602.58) * mm});
            skLineSegment(sketch, "E2884", {"start": v(-221.3, -602.58) * mm, "end": v(-220.26, -603.47) * mm});
            skLineSegment(sketch, "E2885", {"start": v(-220.26, -603.47) * mm, "end": v(-219.1, -604.3) * mm});
            skLineSegment(sketch, "E2886", {"start": v(-219.1, -604.3) * mm, "end": v(-217.81, -605.1) * mm});
            skLineSegment(sketch, "E2887", {"start": v(-217.81, -605.1) * mm, "end": v(-216.4, -605.84) * mm});
            skLineSegment(sketch, "E2888", {"start": v(-216.4, -605.84) * mm, "end": v(-214.85, -606.53) * mm});
            skLineSegment(sketch, "E2889", {"start": v(-214.85, -606.53) * mm, "end": v(-213.15, -607.16) * mm});
            skLineSegment(sketch, "E2890", {"start": v(-213.15, -607.16) * mm, "end": v(-211.31, -607.74) * mm});
            skLineSegment(sketch, "E2891", {"start": v(-211.31, -607.74) * mm, "end": v(-209.32, -608.27) * mm});
            skLineSegment(sketch, "E2892", {"start": v(-209.32, -608.27) * mm, "end": v(-207.43, -608.63) * mm});
            skLineSegment(sketch, "E2893", {"start": v(-207.43, -608.63) * mm, "end": v(-205.63, -608.8) * mm});
            skLineSegment(sketch, "E2894", {"start": v(-205.63, -608.8) * mm, "end": v(-203.93, -608.79) * mm});
            skLineSegment(sketch, "E2895", {"start": v(-203.93, -608.79) * mm, "end": v(-202.32, -608.6) * mm});
            skLineSegment(sketch, "E2896", {"start": v(-202.32, -608.6) * mm, "end": v(-200.79, -608.26) * mm});
            skLineSegment(sketch, "E2897", {"start": v(-200.79, -608.26) * mm, "end": v(-199.34, -607.76) * mm});
            skLineSegment(sketch, "E2898", {"start": v(-199.34, -607.76) * mm, "end": v(-197.97, -607.12) * mm});
            skLineSegment(sketch, "E2899", {"start": v(-197.97, -607.12) * mm, "end": v(-196.67, -606.35) * mm});
            skLineSegment(sketch, "E2900", {"start": v(-196.67, -606.35) * mm, "end": v(-195.43, -605.46) * mm});
            skLineSegment(sketch, "E2901", {"start": v(-195.43, -605.46) * mm, "end": v(-194.26, -604.47) * mm});
            skLineSegment(sketch, "E2902", {"start": v(-194.26, -604.47) * mm, "end": v(-193.15, -603.37) * mm});
            skLineSegment(sketch, "E2903", {"start": v(-193.15, -603.37) * mm, "end": v(-192.09, -602.19) * mm});
            skLineSegment(sketch, "E2904", {"start": v(-192.09, -602.19) * mm, "end": v(-191.08, -600.93) * mm});
            skLineSegment(sketch, "E2905", {"start": v(-191.08, -600.93) * mm, "end": v(-190.12, -599.6) * mm});
            skLineSegment(sketch, "E2906", {"start": v(-190.12, -599.6) * mm, "end": v(-189.2, -598.23) * mm});
            skLineSegment(sketch, "E2907", {"start": v(-189.2, -598.23) * mm, "end": v(-188.3, -596.8) * mm});
            skLineSegment(sketch, "E2908", {"start": v(-188.3, -596.8) * mm, "end": v(-187.45, -595.35) * mm});
            skLineSegment(sketch, "E2909", {"start": v(-187.45, -595.35) * mm, "end": v(-186.63, -593.87) * mm});
            skLineSegment(sketch, "E2910", {"start": v(-186.63, -593.87) * mm, "end": v(-185.82, -592.38) * mm});
            skLineSegment(sketch, "E2911", {"start": v(-185.82, -592.38) * mm, "end": v(-185.04, -590.88) * mm});
            skLineSegment(sketch, "E2912", {"start": v(-185.04, -590.88) * mm, "end": v(-184.27, -589.4) * mm});
            skLineSegment(sketch, "E2913", {"start": v(-184.27, -589.4) * mm, "end": v(-183.51, -587.93) * mm});
            skLineSegment(sketch, "E2914", {"start": v(-183.51, -587.93) * mm, "end": v(-182.74, -586.48) * mm});
            skLineSegment(sketch, "E2915", {"start": v(-182.74, -586.48) * mm, "end": v(-181.92, -585.03) * mm});
            skLineSegment(sketch, "E2916", {"start": v(-181.92, -585.03) * mm, "end": v(-181.06, -583.6) * mm});
            skLineSegment(sketch, "E2917", {"start": v(-181.06, -583.6) * mm, "end": v(-180.16, -582.17) * mm});
            skLineSegment(sketch, "E2918", {"start": v(-180.16, -582.17) * mm, "end": v(-179.22, -580.77) * mm});
            skLineSegment(sketch, "E2919", {"start": v(-179.22, -580.77) * mm, "end": v(-178.25, -579.38) * mm});
            skLineSegment(sketch, "E2920", {"start": v(-178.25, -579.38) * mm, "end": v(-177.23, -578.02) * mm});
            skLineSegment(sketch, "E2921", {"start": v(-177.23, -578.02) * mm, "end": v(-176.17, -576.69) * mm});
            skLineSegment(sketch, "E2922", {"start": v(-176.17, -576.69) * mm, "end": v(-175.08, -575.39) * mm});
            skLineSegment(sketch, "E2923", {"start": v(-175.08, -575.39) * mm, "end": v(-173.95, -574.13) * mm});
            skLineSegment(sketch, "E2924", {"start": v(-173.95, -574.13) * mm, "end": v(-172.78, -572.9) * mm});
            skLineSegment(sketch, "E2925", {"start": v(-172.78, -572.9) * mm, "end": v(-171.57, -571.73) * mm});
            skLineSegment(sketch, "E2926", {"start": v(-171.57, -571.73) * mm, "end": v(-170.33, -570.6) * mm});
            skLineSegment(sketch, "E2927", {"start": v(-170.33, -570.6) * mm, "end": v(-169.05, -569.52) * mm});
            skLineSegment(sketch, "E2928", {"start": v(-169.05, -569.52) * mm, "end": v(-167.74, -568.5) * mm});
            skLineSegment(sketch, "E2929", {"start": v(-167.74, -568.5) * mm, "end": v(-166.4, -567.54) * mm});
            skLineSegment(sketch, "E2930", {"start": v(-166.4, -567.54) * mm, "end": v(-165.01, -566.65) * mm});
            skLineSegment(sketch, "E2931", {"start": v(-165.01, -566.65) * mm, "end": v(-163.6, -565.83) * mm});
            skLineSegment(sketch, "E2932", {"start": v(-163.6, -565.83) * mm, "end": v(-162.15, -565.07) * mm});
            skLineSegment(sketch, "E2933", {"start": v(-162.15, -565.07) * mm, "end": v(-160.66, -564.4) * mm});
            skLineSegment(sketch, "E2934", {"start": v(-160.66, -564.4) * mm, "end": v(-159.15, -563.8) * mm});
            skLineSegment(sketch, "E2935", {"start": v(-159.15, -563.8) * mm, "end": v(-157.6, -563.3) * mm});
            skLineSegment(sketch, "E2936", {"start": v(-157.6, -563.3) * mm, "end": v(-156.03, -562.87) * mm});
            skLineSegment(sketch, "E2937", {"start": v(-156.03, -562.87) * mm, "end": v(-154.42, -562.54) * mm});
            skLineSegment(sketch, "E2938", {"start": v(-154.42, -562.54) * mm, "end": v(-152.78, -562.3) * mm});
            skLineSegment(sketch, "E2939", {"start": v(-152.78, -562.3) * mm, "end": v(-151.11, -562.18) * mm});
            skLineSegment(sketch, "E2940", {"start": v(-151.11, -562.18) * mm, "end": v(-149.42, -562.15) * mm});
            skLineSegment(sketch, "E2941", {"start": v(-149.42, -562.15) * mm, "end": v(-147.69, -562.23) * mm});
            skLineSegment(sketch, "E2942", {"start": v(-147.69, -562.23) * mm, "end": v(-145.93, -562.42) * mm});
            skLineSegment(sketch, "E2943", {"start": v(-145.93, -562.42) * mm, "end": v(-144.15, -562.73) * mm});
            skLineSegment(sketch, "E2944", {"start": v(-144.15, -562.73) * mm, "end": v(-142.45, -563.13) * mm});
            skLineSegment(sketch, "E2945", {"start": v(-142.45, -563.13) * mm, "end": v(-140.78, -563.6) * mm});
            skLineSegment(sketch, "E2946", {"start": v(-140.78, -563.6) * mm, "end": v(-139.15, -564.17) * mm});
            skLineSegment(sketch, "E2947", {"start": v(-139.15, -564.17) * mm, "end": v(-137.54, -564.8) * mm});
            skLineSegment(sketch, "E2948", {"start": v(-137.54, -564.8) * mm, "end": v(-135.98, -565.52) * mm});
            skLineSegment(sketch, "E2949", {"start": v(-135.98, -565.52) * mm, "end": v(-134.45, -566.3) * mm});
            skLineSegment(sketch, "E2950", {"start": v(-134.45, -566.3) * mm, "end": v(-132.96, -567.17) * mm});
            skLineSegment(sketch, "E2951", {"start": v(-132.96, -567.17) * mm, "end": v(-131.52, -568.1) * mm});
            skLineSegment(sketch, "E2952", {"start": v(-131.52, -568.1) * mm, "end": v(-130.12, -569.09) * mm});
            skLineSegment(sketch, "E2953", {"start": v(-130.12, -569.09) * mm, "end": v(-128.77, -570.14) * mm});
            skLineSegment(sketch, "E2954", {"start": v(-128.77, -570.14) * mm, "end": v(-127.47, -571.26) * mm});
            skLineSegment(sketch, "E2955", {"start": v(-127.47, -571.26) * mm, "end": v(-126.22, -572.43) * mm});
            skLineSegment(sketch, "E2956", {"start": v(-126.22, -572.43) * mm, "end": v(-125.03, -573.66) * mm});
            skLineSegment(sketch, "E2957", {"start": v(-125.03, -573.66) * mm, "end": v(-123.9, -574.94) * mm});
            skLineSegment(sketch, "E2958", {"start": v(-123.9, -574.94) * mm, "end": v(-122.82, -576.27) * mm});
            skLineSegment(sketch, "E2959", {"start": v(-122.82, -576.27) * mm, "end": v(-121.8, -577.64) * mm});
            skLineSegment(sketch, "E2960", {"start": v(-121.8, -577.64) * mm, "end": v(-120.85, -579.07) * mm});
            skLineSegment(sketch, "E2961", {"start": v(-120.85, -579.07) * mm, "end": v(-119.97, -580.53) * mm});
            skLineSegment(sketch, "E2962", {"start": v(-119.97, -580.53) * mm, "end": v(-119.15, -582.03) * mm});
            skLineSegment(sketch, "E2963", {"start": v(-119.15, -582.03) * mm, "end": v(-118.4, -583.57) * mm});
            skLineSegment(sketch, "E2964", {"start": v(-118.4, -583.57) * mm, "end": v(-117.73, -585.15) * mm});
            skLineSegment(sketch, "E2965", {"start": v(-117.73, -585.15) * mm, "end": v(-117.13, -586.75) * mm});
            skLineSegment(sketch, "E2966", {"start": v(-117.13, -586.75) * mm, "end": v(-116.61, -588.39) * mm});
            skLineSegment(sketch, "E2967", {"start": v(-116.61, -588.39) * mm, "end": v(-116.17, -590.05) * mm});
            skLineSegment(sketch, "E2968", {"start": v(-116.17, -590.05) * mm, "end": v(-115.82, -591.74) * mm});
            skLineSegment(sketch, "E2969", {"start": v(-115.82, -591.74) * mm, "end": v(-115.54, -593.44) * mm});
            skLineSegment(sketch, "E2970", {"start": v(-115.54, -593.44) * mm, "end": v(-115.35, -595.17) * mm});
            skLineSegment(sketch, "E2971", {"start": v(-115.35, -595.17) * mm, "end": v(-115.25, -596.66) * mm});
            skLineSegment(sketch, "E2972", {"start": v(-115.25, -596.66) * mm, "end": v(-115.18, -598.18) * mm});
            skLineSegment(sketch, "E2973", {"start": v(-115.18, -598.18) * mm, "end": v(-115.14, -599.7) * mm});
            skLineSegment(sketch, "E2974", {"start": v(-115.14, -599.7) * mm, "end": v(-115.13, -601.24) * mm});
            skLineSegment(sketch, "E2975", {"start": v(-115.13, -601.24) * mm, "end": v(-115.13, -602.79) * mm});
            skLineSegment(sketch, "E2976", {"start": v(-115.13, -602.79) * mm, "end": v(-115.15, -604.34) * mm});
            skLineSegment(sketch, "E2977", {"start": v(-115.15, -604.34) * mm, "end": v(-115.17, -605.89) * mm});
            skLineSegment(sketch, "E2978", {"start": v(-115.17, -605.89) * mm, "end": v(-115.2, -607.44) * mm});
            skLineSegment(sketch, "E2979", {"start": v(-115.2, -607.44) * mm, "end": v(-115.22, -608.98) * mm});
            skLineSegment(sketch, "E2980", {"start": v(-115.22, -608.98) * mm, "end": v(-115.23, -610.52) * mm});
            skLineSegment(sketch, "E2981", {"start": v(-115.23, -610.52) * mm, "end": v(-115.23, -612.04) * mm});
            skLineSegment(sketch, "E2982", {"start": v(-115.23, -612.04) * mm, "end": v(-115.2, -613.55) * mm});
            skLineSegment(sketch, "E2983", {"start": v(-115.2, -613.55) * mm, "end": v(-115.17, -615.04) * mm});
            skLineSegment(sketch, "E2984", {"start": v(-115.17, -615.04) * mm, "end": v(-115.1, -616.5) * mm});
            skLineSegment(sketch, "E2985", {"start": v(-115.1, -616.5) * mm, "end": v(-114.98, -617.95) * mm});
            skLineSegment(sketch, "E2986", {"start": v(-114.98, -617.95) * mm, "end": v(-114.83, -619.36) * mm});
            skLineSegment(sketch, "E2987", {"start": v(-114.83, -619.36) * mm, "end": v(-114.64, -620.75) * mm});
            skLineSegment(sketch, "E2988", {"start": v(-114.64, -620.75) * mm, "end": v(-114.39, -622.1) * mm});
            skLineSegment(sketch, "E2989", {"start": v(-114.39, -622.1) * mm, "end": v(-114.08, -623.4) * mm});
            skLineSegment(sketch, "E2990", {"start": v(-114.08, -623.4) * mm, "end": v(-113.72, -624.67) * mm});
            skLineSegment(sketch, "E2991", {"start": v(-113.72, -624.67) * mm, "end": v(-113.28, -625.9) * mm});
            skLineSegment(sketch, "E2992", {"start": v(-113.28, -625.9) * mm, "end": v(-112.77, -627.07) * mm});
            skLineSegment(sketch, "E2993", {"start": v(-112.77, -627.07) * mm, "end": v(-112.19, -628.2) * mm});
            skLineSegment(sketch, "E2994", {"start": v(-112.19, -628.2) * mm, "end": v(-111.52, -629.26) * mm});
            skLineSegment(sketch, "E2995", {"start": v(-111.52, -629.26) * mm, "end": v(-110.76, -630.28) * mm});
            skLineSegment(sketch, "E2996", {"start": v(-110.76, -630.28) * mm, "end": v(-109.9, -631.23) * mm});
            skLineSegment(sketch, "E2997", {"start": v(-109.9, -631.23) * mm, "end": v(-108.95, -632.11) * mm});
            skLineSegment(sketch, "E2998", {"start": v(-108.95, -632.11) * mm, "end": v(-107.9, -632.93) * mm});
            skLineSegment(sketch, "E2999", {"start": v(-107.9, -632.93) * mm, "end": v(-106.72, -633.68) * mm});
            skLineSegment(sketch, "E3000", {"start": v(-106.72, -633.68) * mm, "end": v(-105.44, -634.35) * mm});
            skLineSegment(sketch, "E3001", {"start": v(-105.44, -634.35) * mm, "end": v(-104.03, -634.95) * mm});
            skLineSegment(sketch, "E3002", {"start": v(-104.03, -634.95) * mm, "end": v(-102.5, -635.46) * mm});
            skLineSegment(sketch, "E3003", {"start": v(-102.5, -635.46) * mm, "end": v(-100.83, -635.9) * mm});
            skLineSegment(sketch, "E3004", {"start": v(-100.83, -635.9) * mm, "end": v(-99.03, -636.24) * mm});
            skLineSegment(sketch, "E3005", {"start": v(-99.03, -636.24) * mm, "end": v(-97.08, -636.5) * mm});
            skLineSegment(sketch, "E3006", {"start": v(-97.08, -636.5) * mm, "end": v(-95.8, -636.59) * mm});
            skLineSegment(sketch, "E3007", {"start": v(-95.8, -636.59) * mm, "end": v(-94.58, -636.62) * mm});
            skLineSegment(sketch, "E3008", {"start": v(-94.58, -636.62) * mm, "end": v(-93.39, -636.58) * mm});
            skLineSegment(sketch, "E3009", {"start": v(-93.39, -636.58) * mm, "end": v(-92.25, -636.49) * mm});
            skLineSegment(sketch, "E3010", {"start": v(-92.25, -636.49) * mm, "end": v(-91.14, -636.32) * mm});
            skLineSegment(sketch, "E3011", {"start": v(-91.14, -636.32) * mm, "end": v(-90.08, -636.1) * mm});
            skLineSegment(sketch, "E3012", {"start": v(-90.08, -636.1) * mm, "end": v(-89.06, -635.82) * mm});
            skLineSegment(sketch, "E3013", {"start": v(-89.06, -635.82) * mm, "end": v(-88.07, -635.48) * mm});
            skLineSegment(sketch, "E3014", {"start": v(-88.07, -635.48) * mm, "end": v(-87.12, -635.09) * mm});
            skLineSegment(sketch, "E3015", {"start": v(-87.12, -635.09) * mm, "end": v(-86.2, -634.64) * mm});
            skLineSegment(sketch, "E3016", {"start": v(-86.2, -634.64) * mm, "end": v(-85.32, -634.15) * mm});
            skLineSegment(sketch, "E3017", {"start": v(-85.32, -634.15) * mm, "end": v(-84.47, -633.6) * mm});
            skLineSegment(sketch, "E3018", {"start": v(-84.47, -633.6) * mm, "end": v(-83.65, -633) * mm});
            skLineSegment(sketch, "E3019", {"start": v(-83.65, -633) * mm, "end": v(-82.86, -632.36) * mm});
            skLineSegment(sketch, "E3020", {"start": v(-82.86, -632.36) * mm, "end": v(-82.1, -631.68) * mm});
            skLineSegment(sketch, "E3021", {"start": v(-82.1, -631.68) * mm, "end": v(-81.36, -630.95) * mm});
            skLineSegment(sketch, "E3022", {"start": v(-81.36, -630.95) * mm, "end": v(-80.65, -630.19) * mm});
            skLineSegment(sketch, "E3023", {"start": v(-80.65, -630.19) * mm, "end": v(-79.96, -629.38) * mm});
            skLineSegment(sketch, "E3024", {"start": v(-79.96, -629.38) * mm, "end": v(-79.3, -628.54) * mm});
            skLineSegment(sketch, "E3025", {"start": v(-79.3, -628.54) * mm, "end": v(-78.65, -627.66) * mm});
            skLineSegment(sketch, "E3026", {"start": v(-78.65, -627.66) * mm, "end": v(-78.03, -626.75) * mm});
            skLineSegment(sketch, "E3027", {"start": v(-78.03, -626.75) * mm, "end": v(-77.43, -625.81) * mm});
            skLineSegment(sketch, "E3028", {"start": v(-77.43, -625.81) * mm, "end": v(-76.84, -624.84) * mm});
            skLineSegment(sketch, "E3029", {"start": v(-76.84, -624.84) * mm, "end": v(-76.27, -623.84) * mm});
            skLineSegment(sketch, "E3030", {"start": v(-76.27, -623.84) * mm, "end": v(-75.71, -622.82) * mm});
            skLineSegment(sketch, "E3031", {"start": v(-75.71, -622.82) * mm, "end": v(-75.17, -621.77) * mm});
            skLineSegment(sketch, "E3032", {"start": v(-75.17, -621.77) * mm, "end": v(-74.64, -620.7) * mm});
            skLineSegment(sketch, "E3033", {"start": v(-74.64, -620.7) * mm, "end": v(-74.12, -619.6) * mm});
            skLineSegment(sketch, "E3034", {"start": v(-74.12, -619.6) * mm, "end": v(-73.6, -618.5) * mm});
            skLineSegment(sketch, "E3035", {"start": v(-73.6, -618.5) * mm, "end": v(-73.1, -617.37) * mm});
            skLineSegment(sketch, "E3036", {"start": v(-73.1, -617.37) * mm, "end": v(-72.6, -616.23) * mm});
            skLineSegment(sketch, "E3037", {"start": v(-72.6, -616.23) * mm, "end": v(-72.11, -615.08) * mm});
            skLineSegment(sketch, "E3038", {"start": v(-72.11, -615.08) * mm, "end": v(-71.63, -613.92) * mm});
            skLineSegment(sketch, "E3039", {"start": v(-71.63, -613.92) * mm, "end": v(-71.14, -612.74) * mm});
            skLineSegment(sketch, "E3040", {"start": v(-71.14, -612.74) * mm, "end": v(-70.66, -611.56) * mm});
            skLineSegment(sketch, "E3041", {"start": v(-70.66, -611.56) * mm, "end": v(-70.17, -610.38) * mm});
            skLineSegment(sketch, "E3042", {"start": v(-70.17, -610.38) * mm, "end": v(-69.69, -609.19) * mm});
            skLineSegment(sketch, "E3043", {"start": v(-69.69, -609.19) * mm, "end": v(-69.2, -608) * mm});
            skLineSegment(sketch, "E3044", {"start": v(-69.2, -608) * mm, "end": v(-68.71, -606.8) * mm});
            skLineSegment(sketch, "E3045", {"start": v(-68.71, -606.8) * mm, "end": v(-68.21, -605.6) * mm});
            skLineSegment(sketch, "E3046", {"start": v(-68.21, -605.6) * mm, "end": v(-67.71, -604.42) * mm});
            skLineSegment(sketch, "E3047", {"start": v(-67.71, -604.42) * mm, "end": v(-67.2, -603.24) * mm});
            skLineSegment(sketch, "E3048", {"start": v(-67.2, -603.24) * mm, "end": v(-66.68, -602.07) * mm});
            skLineSegment(sketch, "E3049", {"start": v(-66.68, -602.07) * mm, "end": v(-66.15, -600.9) * mm});
            skLineSegment(sketch, "E3050", {"start": v(-66.15, -600.9) * mm, "end": v(-65.6, -599.74) * mm});
            skLineSegment(sketch, "E3051", {"start": v(-65.6, -599.74) * mm, "end": v(-65.05, -598.6) * mm});
            skLineSegment(sketch, "E3052", {"start": v(-65.05, -598.6) * mm, "end": v(-64.48, -597.47) * mm});
            skLineSegment(sketch, "E3053", {"start": v(-64.48, -597.47) * mm, "end": v(-63.89, -596.36) * mm});
            skLineSegment(sketch, "E3054", {"start": v(-63.89, -596.36) * mm, "end": v(-63.28, -595.27) * mm});
            skLineSegment(sketch, "E3055", {"start": v(-63.28, -595.27) * mm, "end": v(-62.66, -594.2) * mm});
            skLineSegment(sketch, "E3056", {"start": v(-62.66, -594.2) * mm, "end": v(-62.02, -593.14) * mm});
            skLineSegment(sketch, "E3057", {"start": v(-62.02, -593.14) * mm, "end": v(-61.35, -592.12) * mm});
            skLineSegment(sketch, "E3058", {"start": v(-61.35, -592.12) * mm, "end": v(-60.66, -591.11) * mm});
            skLineSegment(sketch, "E3059", {"start": v(-60.66, -591.11) * mm, "end": v(-59.95, -590.14) * mm});
            skLineSegment(sketch, "E3060", {"start": v(-59.95, -590.14) * mm, "end": v(-59.22, -589.2) * mm});
            skLineSegment(sketch, "E3061", {"start": v(-59.22, -589.2) * mm, "end": v(-58.45, -588.28) * mm});
            skLineSegment(sketch, "E3062", {"start": v(-58.45, -588.28) * mm, "end": v(-57.66, -587.4) * mm});
            skLineSegment(sketch, "E3063", {"start": v(-57.66, -587.4) * mm, "end": v(-56.84, -586.55) * mm});
            skLineSegment(sketch, "E3064", {"start": v(-56.84, -586.55) * mm, "end": v(-55.99, -585.74) * mm});
            skLineSegment(sketch, "E3065", {"start": v(-55.99, -585.74) * mm, "end": v(-55.1, -584.96) * mm});
            skLineSegment(sketch, "E3066", {"start": v(-55.1, -584.96) * mm, "end": v(-54.19, -584.23) * mm});
            skLineSegment(sketch, "E3067", {"start": v(-54.19, -584.23) * mm, "end": v(-53.24, -583.54) * mm});
            skLineSegment(sketch, "E3068", {"start": v(-53.24, -583.54) * mm, "end": v(-52.25, -582.9) * mm});
            skLineSegment(sketch, "E3069", {"start": v(-52.25, -582.9) * mm, "end": v(-51.22, -582.29) * mm});
            skLineSegment(sketch, "E3070", {"start": v(-51.22, -582.29) * mm, "end": v(-50.16, -581.73) * mm});
            skLineSegment(sketch, "E3071", {"start": v(-50.16, -581.73) * mm, "end": v(-49.06, -581.23) * mm});
            skLineSegment(sketch, "E3072", {"start": v(-49.06, -581.23) * mm, "end": v(-47.91, -580.77) * mm});
            skLineSegment(sketch, "E3073", {"start": v(-47.91, -580.77) * mm, "end": v(-46.73, -580.37) * mm});
            skLineSegment(sketch, "E3074", {"start": v(-46.73, -580.37) * mm, "end": v(-45.5, -580.03) * mm});
            skLineSegment(sketch, "E3075", {"start": v(-45.5, -580.03) * mm, "end": v(-44.22, -579.74) * mm});
            skLineSegment(sketch, "E3076", {"start": v(-44.22, -579.74) * mm, "end": v(-42.9, -579.5) * mm});
            skLineSegment(sketch, "E3077", {"start": v(-42.9, -579.5) * mm, "end": v(-41.52, -579.33) * mm});
            skLineSegment(sketch, "E3078", {"start": v(-41.52, -579.33) * mm, "end": v(-40.1, -579.22) * mm});
            skLineSegment(sketch, "E3079", {"start": v(-40.1, -579.22) * mm, "end": v(-38.63, -579.18) * mm});
            skLineSegment(sketch, "E3080", {"start": v(-38.63, -579.18) * mm, "end": v(-37.1, -579.2) * mm});
            skLineSegment(sketch, "E3081", {"start": v(-37.1, -579.2) * mm, "end": v(-35.53, -579.28) * mm});
            skLineSegment(sketch, "E3082", {"start": v(-35.53, -579.28) * mm, "end": v(-33.72, -579.48) * mm});
            skLineSegment(sketch, "E3083", {"start": v(-33.72, -579.48) * mm, "end": v(-31.95, -579.77) * mm});
            skLineSegment(sketch, "E3084", {"start": v(-31.95, -579.77) * mm, "end": v(-30.22, -580.16) * mm});
            skLineSegment(sketch, "E3085", {"start": v(-30.22, -580.16) * mm, "end": v(-28.53, -580.65) * mm});
            skLineSegment(sketch, "E3086", {"start": v(-28.53, -580.65) * mm, "end": v(-26.89, -581.22) * mm});
            skLineSegment(sketch, "E3087", {"start": v(-26.89, -581.22) * mm, "end": v(-25.29, -581.89) * mm});
            skLineSegment(sketch, "E3088", {"start": v(-25.29, -581.89) * mm, "end": v(-23.73, -582.64) * mm});
            skLineSegment(sketch, "E3089", {"start": v(-23.73, -582.64) * mm, "end": v(-22.22, -583.47) * mm});
            skLineSegment(sketch, "E3090", {"start": v(-22.22, -583.47) * mm, "end": v(-20.76, -584.37) * mm});
            skLineSegment(sketch, "E3091", {"start": v(-20.76, -584.37) * mm, "end": v(-19.35, -585.35) * mm});
            skLineSegment(sketch, "E3092", {"start": v(-19.35, -585.35) * mm, "end": v(-17.99, -586.4) * mm});
            skLineSegment(sketch, "E3093", {"start": v(-17.99, -586.4) * mm, "end": v(-16.68, -587.52) * mm});
            skLineSegment(sketch, "E3094", {"start": v(-16.68, -587.52) * mm, "end": v(-15.42, -588.7) * mm});
            skLineSegment(sketch, "E3095", {"start": v(-15.42, -588.7) * mm, "end": v(-14.2, -589.93) * mm});
            skLineSegment(sketch, "E3096", {"start": v(-14.2, -589.93) * mm, "end": v(-13.06, -591.22) * mm});
            skLineSegment(sketch, "E3097", {"start": v(-13.06, -591.22) * mm, "end": v(-11.96, -592.57) * mm});
            skLineSegment(sketch, "E3098", {"start": v(-11.96, -592.57) * mm, "end": v(-10.91, -593.96) * mm});
            skLineSegment(sketch, "E3099", {"start": v(-10.91, -593.96) * mm, "end": v(-9.93, -595.4) * mm});
            skLineSegment(sketch, "E3100", {"start": v(-9.93, -595.4) * mm, "end": v(-9, -596.88) * mm});
            skLineSegment(sketch, "E3101", {"start": v(-9, -596.88) * mm, "end": v(-8.13, -598.4) * mm});
            skLineSegment(sketch, "E3102", {"start": v(-8.13, -598.4) * mm, "end": v(-7.32, -599.95) * mm});
            skLineSegment(sketch, "E3103", {"start": v(-7.32, -599.95) * mm, "end": v(-6.57, -601.53) * mm});
            skLineSegment(sketch, "E3104", {"start": v(-6.57, -601.53) * mm, "end": v(-5.89, -603.14) * mm});
            skLineSegment(sketch, "E3105", {"start": v(-5.89, -603.14) * mm, "end": v(-5.26, -604.77) * mm});
            skLineSegment(sketch, "E3106", {"start": v(-5.26, -604.77) * mm, "end": v(-4.7, -606.42) * mm});
            skLineSegment(sketch, "E3107", {"start": v(-4.7, -606.42) * mm, "end": v(-4.2, -608.1) * mm});
            skLineSegment(sketch, "E3108", {"start": v(-4.2, -608.1) * mm, "end": v(-3.78, -609.77) * mm});
            skLineSegment(sketch, "E3109", {"start": v(-3.78, -609.77) * mm, "end": v(-3.42, -611.46) * mm});
            skLineSegment(sketch, "E3110", {"start": v(-3.42, -611.46) * mm, "end": v(-3.14, -612.97) * mm});
            skLineSegment(sketch, "E3111", {"start": v(-3.14, -612.97) * mm, "end": v(-2.87, -614.52) * mm});
            skLineSegment(sketch, "E3112", {"start": v(-2.87, -614.52) * mm, "end": v(-2.6, -616.09) * mm});
            skLineSegment(sketch, "E3113", {"start": v(-2.6, -616.09) * mm, "end": v(-2.33, -617.68) * mm});
            skLineSegment(sketch, "E3114", {"start": v(-2.33, -617.68) * mm, "end": v(-2.05, -619.28) * mm});
            skLineSegment(sketch, "E3115", {"start": v(-2.05, -619.28) * mm, "end": v(-1.76, -620.89) * mm});
            skLineSegment(sketch, "E3116", {"start": v(-1.76, -620.89) * mm, "end": v(-1.45, -622.5) * mm});
            skLineSegment(sketch, "E3117", {"start": v(-1.45, -622.5) * mm, "end": v(-1.12, -624.1) * mm});
            skLineSegment(sketch, "E3118", {"start": v(-1.12, -624.1) * mm, "end": v(-0.76, -625.68) * mm});
            skLineSegment(sketch, "E3119", {"start": v(-0.76, -625.68) * mm, "end": v(-0.36, -627.24) * mm});
            skLineSegment(sketch, "E3120", {"start": v(-0.36, -627.24) * mm, "end": v(0.07, -628.77) * mm});
            skLineSegment(sketch, "E3121", {"start": v(0.07, -628.77) * mm, "end": v(0.55, -630.27) * mm});
            skLineSegment(sketch, "E3122", {"start": v(0.55, -630.27) * mm, "end": v(1.08, -631.73) * mm});
            skLineSegment(sketch, "E3123", {"start": v(1.08, -631.73) * mm, "end": v(1.67, -633.13) * mm});
            skLineSegment(sketch, "E3124", {"start": v(1.67, -633.13) * mm, "end": v(2.32, -634.48) * mm});
            skLineSegment(sketch, "E3125", {"start": v(2.32, -634.48) * mm, "end": v(3.03, -635.76) * mm});
            skLineSegment(sketch, "E3126", {"start": v(3.03, -635.76) * mm, "end": v(3.82, -636.98) * mm});
            skLineSegment(sketch, "E3127", {"start": v(3.82, -636.98) * mm, "end": v(4.68, -638.11) * mm});
            skLineSegment(sketch, "E3128", {"start": v(4.68, -638.11) * mm, "end": v(5.63, -639.16) * mm});
            skLineSegment(sketch, "E3129", {"start": v(5.63, -639.16) * mm, "end": v(6.66, -640.12) * mm});
            skLineSegment(sketch, "E3130", {"start": v(6.66, -640.12) * mm, "end": v(7.8, -640.98) * mm});
            skLineSegment(sketch, "E3131", {"start": v(7.8, -640.98) * mm, "end": v(9.02, -641.74) * mm});
            skLineSegment(sketch, "E3132", {"start": v(9.02, -641.74) * mm, "end": v(10.35, -642.38) * mm});
            skLineSegment(sketch, "E3133", {"start": v(10.35, -642.38) * mm, "end": v(11.8, -642.9) * mm});
            skLineSegment(sketch, "E3134", {"start": v(11.8, -642.9) * mm, "end": v(13.36, -643.3) * mm});
            skLineSegment(sketch, "E3135", {"start": v(13.36, -643.3) * mm, "end": v(15.03, -643.57) * mm});
            skLineSegment(sketch, "E3136", {"start": v(15.03, -643.57) * mm, "end": v(16.84, -643.7) * mm});
            skLineSegment(sketch, "E3137", {"start": v(16.84, -643.7) * mm, "end": v(18.78, -643.67) * mm});
            skLineSegment(sketch, "E3138", {"start": v(18.78, -643.67) * mm, "end": v(20.1, -643.57) * mm});
            skLineSegment(sketch, "E3139", {"start": v(20.1, -643.57) * mm, "end": v(21.35, -643.42) * mm});
            skLineSegment(sketch, "E3140", {"start": v(21.35, -643.42) * mm, "end": v(22.56, -643.22) * mm});
            skLineSegment(sketch, "E3141", {"start": v(22.56, -643.22) * mm, "end": v(23.71, -642.97) * mm});
            skLineSegment(sketch, "E3142", {"start": v(23.71, -642.97) * mm, "end": v(24.81, -642.67) * mm});
            skLineSegment(sketch, "E3143", {"start": v(24.81, -642.67) * mm, "end": v(25.87, -642.31) * mm});
            skLineSegment(sketch, "E3144", {"start": v(25.87, -642.31) * mm, "end": v(26.87, -641.91) * mm});
            skLineSegment(sketch, "E3145", {"start": v(26.87, -641.91) * mm, "end": v(27.83, -641.47) * mm});
            skLineSegment(sketch, "E3146", {"start": v(27.83, -641.47) * mm, "end": v(28.74, -640.98) * mm});
            skLineSegment(sketch, "E3147", {"start": v(28.74, -640.98) * mm, "end": v(29.61, -640.44) * mm});
            skLineSegment(sketch, "E3148", {"start": v(29.61, -640.44) * mm, "end": v(30.44, -639.87) * mm});
            skLineSegment(sketch, "E3149", {"start": v(30.44, -639.87) * mm, "end": v(31.23, -639.25) * mm});
            skLineSegment(sketch, "E3150", {"start": v(31.23, -639.25) * mm, "end": v(31.97, -638.6) * mm});
            skLineSegment(sketch, "E3151", {"start": v(31.97, -638.6) * mm, "end": v(32.69, -637.9) * mm});
            skLineSegment(sketch, "E3152", {"start": v(32.69, -637.9) * mm, "end": v(33.36, -637.17) * mm});
            skLineSegment(sketch, "E3153", {"start": v(33.36, -637.17) * mm, "end": v(34, -636.4) * mm});
            skLineSegment(sketch, "E3154", {"start": v(34, -636.4) * mm, "end": v(34.6, -635.6) * mm});
            skLineSegment(sketch, "E3155", {"start": v(34.6, -635.6) * mm, "end": v(35.18, -634.78) * mm});
            skLineSegment(sketch, "E3156", {"start": v(35.18, -634.78) * mm, "end": v(35.73, -633.91) * mm});
            skLineSegment(sketch, "E3157", {"start": v(35.73, -633.91) * mm, "end": v(36.24, -633.02) * mm});
            skLineSegment(sketch, "E3158", {"start": v(36.24, -633.02) * mm, "end": v(36.73, -632.1) * mm});
            skLineSegment(sketch, "E3159", {"start": v(36.73, -632.1) * mm, "end": v(37.2, -631.15) * mm});
            skLineSegment(sketch, "E3160", {"start": v(37.2, -631.15) * mm, "end": v(37.64, -630.18) * mm});
            skLineSegment(sketch, "E3161", {"start": v(37.64, -630.18) * mm, "end": v(38.06, -629.18) * mm});
            skLineSegment(sketch, "E3162", {"start": v(38.06, -629.18) * mm, "end": v(38.45, -628.16) * mm});
            skLineSegment(sketch, "E3163", {"start": v(38.45, -628.16) * mm, "end": v(38.83, -627.11) * mm});
            skLineSegment(sketch, "E3164", {"start": v(38.83, -627.11) * mm, "end": v(39.19, -626.05) * mm});
            skLineSegment(sketch, "E3165", {"start": v(39.19, -626.05) * mm, "end": v(39.53, -624.97) * mm});
            skLineSegment(sketch, "E3166", {"start": v(39.53, -624.97) * mm, "end": v(39.86, -623.87) * mm});
            skLineSegment(sketch, "E3167", {"start": v(39.86, -623.87) * mm, "end": v(40.17, -622.75) * mm});
            skLineSegment(sketch, "E3168", {"start": v(40.17, -622.75) * mm, "end": v(40.47, -621.62) * mm});
            skLineSegment(sketch, "E3169", {"start": v(40.47, -621.62) * mm, "end": v(40.76, -620.47) * mm});
            skLineSegment(sketch, "E3170", {"start": v(40.76, -620.47) * mm, "end": v(41.04, -619.31) * mm});
            skLineSegment(sketch, "E3171", {"start": v(41.04, -619.31) * mm, "end": v(41.32, -618.15) * mm});
            skLineSegment(sketch, "E3172", {"start": v(41.32, -618.15) * mm, "end": v(41.58, -616.97) * mm});
            skLineSegment(sketch, "E3173", {"start": v(41.58, -616.97) * mm, "end": v(41.85, -615.78) * mm});
            skLineSegment(sketch, "E3174", {"start": v(41.85, -615.78) * mm, "end": v(42.1, -614.6) * mm});
            skLineSegment(sketch, "E3175", {"start": v(42.1, -614.6) * mm, "end": v(42.36, -613.4) * mm});
            skLineSegment(sketch, "E3176", {"start": v(42.36, -613.4) * mm, "end": v(42.62, -612.19) * mm});
            skLineSegment(sketch, "E3177", {"start": v(42.62, -612.19) * mm, "end": v(42.88, -610.98) * mm});
            skLineSegment(sketch, "E3178", {"start": v(42.88, -610.98) * mm, "end": v(43.14, -609.78) * mm});
            skLineSegment(sketch, "E3179", {"start": v(43.14, -609.78) * mm, "end": v(43.41, -608.57) * mm});
            skLineSegment(sketch, "E3180", {"start": v(43.41, -608.57) * mm, "end": v(43.68, -607.37) * mm});
            skLineSegment(sketch, "E3181", {"start": v(43.68, -607.37) * mm, "end": v(43.96, -606.17) * mm});
            skLineSegment(sketch, "E3182", {"start": v(43.96, -606.17) * mm, "end": v(44.25, -604.97) * mm});
            skLineSegment(sketch, "E3183", {"start": v(44.25, -604.97) * mm, "end": v(44.55, -603.77) * mm});
            skLineSegment(sketch, "E3184", {"start": v(44.55, -603.77) * mm, "end": v(44.86, -602.59) * mm});
            skLineSegment(sketch, "E3185", {"start": v(44.86, -602.59) * mm, "end": v(45.18, -601.41) * mm});
            skLineSegment(sketch, "E3186", {"start": v(45.18, -601.41) * mm, "end": v(45.52, -600.24) * mm});
            skLineSegment(sketch, "E3187", {"start": v(45.52, -600.24) * mm, "end": v(45.88, -599.08) * mm});
            skLineSegment(sketch, "E3188", {"start": v(45.88, -599.08) * mm, "end": v(46.25, -597.94) * mm});
            skLineSegment(sketch, "E3189", {"start": v(46.25, -597.94) * mm, "end": v(46.64, -596.8) * mm});
            skLineSegment(sketch, "E3190", {"start": v(46.64, -596.8) * mm, "end": v(47.05, -595.7) * mm});
            skLineSegment(sketch, "E3191", {"start": v(47.05, -595.7) * mm, "end": v(47.49, -594.59) * mm});
            skLineSegment(sketch, "E3192", {"start": v(47.49, -594.59) * mm, "end": v(47.94, -593.5) * mm});
            skLineSegment(sketch, "E3193", {"start": v(47.94, -593.5) * mm, "end": v(48.43, -592.44) * mm});
            skLineSegment(sketch, "E3194", {"start": v(48.43, -592.44) * mm, "end": v(48.94, -591.4) * mm});
            skLineSegment(sketch, "E3195", {"start": v(48.94, -591.4) * mm, "end": v(49.48, -590.38) * mm});
            skLineSegment(sketch, "E3196", {"start": v(49.48, -590.38) * mm, "end": v(50.05, -589.38) * mm});
            skLineSegment(sketch, "E3197", {"start": v(50.05, -589.38) * mm, "end": v(50.64, -588.4) * mm});
            skLineSegment(sketch, "E3198", {"start": v(50.64, -588.4) * mm, "end": v(51.28, -587.45) * mm});
            skLineSegment(sketch, "E3199", {"start": v(51.28, -587.45) * mm, "end": v(51.94, -586.53) * mm});
            skLineSegment(sketch, "E3200", {"start": v(51.94, -586.53) * mm, "end": v(52.65, -585.64) * mm});
            skLineSegment(sketch, "E3201", {"start": v(52.65, -585.64) * mm, "end": v(53.38, -584.77) * mm});
            skLineSegment(sketch, "E3202", {"start": v(53.38, -584.77) * mm, "end": v(54.16, -583.94) * mm});
            skLineSegment(sketch, "E3203", {"start": v(54.16, -583.94) * mm, "end": v(54.98, -583.14) * mm});
            skLineSegment(sketch, "E3204", {"start": v(54.98, -583.14) * mm, "end": v(55.84, -582.38) * mm});
            skLineSegment(sketch, "E3205", {"start": v(55.84, -582.38) * mm, "end": v(56.74, -581.64) * mm});
            skLineSegment(sketch, "E3206", {"start": v(56.74, -581.64) * mm, "end": v(57.7, -580.95) * mm});
            skLineSegment(sketch, "E3207", {"start": v(57.7, -580.95) * mm, "end": v(58.68, -580.3) * mm});
            skLineSegment(sketch, "E3208", {"start": v(58.68, -580.3) * mm, "end": v(59.73, -579.68) * mm});
            skLineSegment(sketch, "E3209", {"start": v(59.73, -579.68) * mm, "end": v(60.82, -579.1) * mm});
            skLineSegment(sketch, "E3210", {"start": v(60.82, -579.1) * mm, "end": v(61.96, -578.57) * mm});
            skLineSegment(sketch, "E3211", {"start": v(61.96, -578.57) * mm, "end": v(63.15, -578.07) * mm});
            skLineSegment(sketch, "E3212", {"start": v(63.15, -578.07) * mm, "end": v(64.4, -577.63) * mm});
            skLineSegment(sketch, "E3213", {"start": v(64.4, -577.63) * mm, "end": v(65.7, -577.23) * mm});
            skLineSegment(sketch, "E3214", {"start": v(65.7, -577.23) * mm, "end": v(67.06, -576.87) * mm});
            skLineSegment(sketch, "E3215", {"start": v(67.06, -576.87) * mm, "end": v(68.47, -576.57) * mm});
            skLineSegment(sketch, "E3216", {"start": v(68.47, -576.57) * mm, "end": v(69.95, -576.32) * mm});
            skLineSegment(sketch, "E3217", {"start": v(69.95, -576.32) * mm, "end": v(71.49, -576.11) * mm});
            skLineSegment(sketch, "E3218", {"start": v(71.49, -576.11) * mm, "end": v(73.09, -575.96) * mm});
            skLineSegment(sketch, "E3219", {"start": v(73.09, -575.96) * mm, "end": v(74.64, -575.88) * mm});
            skLineSegment(sketch, "E3220", {"start": v(74.64, -575.88) * mm, "end": v(76.14, -575.87) * mm});
            skLineSegment(sketch, "E3221", {"start": v(76.14, -575.87) * mm, "end": v(77.6, -575.93) * mm});
            skLineSegment(sketch, "E3222", {"start": v(77.6, -575.93) * mm, "end": v(79, -576.06) * mm});
            skLineSegment(sketch, "E3223", {"start": v(79, -576.06) * mm, "end": v(80.37, -576.25) * mm});
            skLineSegment(sketch, "E3224", {"start": v(80.37, -576.25) * mm, "end": v(81.69, -576.51) * mm});
            skLineSegment(sketch, "E3225", {"start": v(81.69, -576.51) * mm, "end": v(82.96, -576.83) * mm});
            skLineSegment(sketch, "E3226", {"start": v(82.96, -576.83) * mm, "end": v(84.2, -577.2) * mm});
            skLineSegment(sketch, "E3227", {"start": v(84.2, -577.2) * mm, "end": v(85.4, -577.65) * mm});
            skLineSegment(sketch, "E3228", {"start": v(85.4, -577.65) * mm, "end": v(86.55, -578.14) * mm});
            skLineSegment(sketch, "E3229", {"start": v(86.55, -578.14) * mm, "end": v(87.67, -578.68) * mm});
            skLineSegment(sketch, "E3230", {"start": v(87.67, -578.68) * mm, "end": v(88.75, -579.28) * mm});
            skLineSegment(sketch, "E3231", {"start": v(88.75, -579.28) * mm, "end": v(89.8, -579.92) * mm});
            skLineSegment(sketch, "E3232", {"start": v(89.8, -579.92) * mm, "end": v(90.8, -580.62) * mm});
            skLineSegment(sketch, "E3233", {"start": v(90.8, -580.62) * mm, "end": v(91.78, -581.35) * mm});
            skLineSegment(sketch, "E3234", {"start": v(91.78, -581.35) * mm, "end": v(92.73, -582.13) * mm});
            skLineSegment(sketch, "E3235", {"start": v(92.73, -582.13) * mm, "end": v(93.65, -582.95) * mm});
            skLineSegment(sketch, "E3236", {"start": v(93.65, -582.95) * mm, "end": v(94.54, -583.81) * mm});
            skLineSegment(sketch, "E3237", {"start": v(94.54, -583.81) * mm, "end": v(95.4, -584.7) * mm});
            skLineSegment(sketch, "E3238", {"start": v(95.4, -584.7) * mm, "end": v(96.24, -585.64) * mm});
            skLineSegment(sketch, "E3239", {"start": v(96.24, -585.64) * mm, "end": v(97.05, -586.6) * mm});
            skLineSegment(sketch, "E3240", {"start": v(97.05, -586.6) * mm, "end": v(97.83, -587.6) * mm});
            skLineSegment(sketch, "E3241", {"start": v(97.83, -587.6) * mm, "end": v(98.6, -588.62) * mm});
            skLineSegment(sketch, "E3242", {"start": v(98.6, -588.62) * mm, "end": v(99.34, -589.66) * mm});
            skLineSegment(sketch, "E3243", {"start": v(99.34, -589.66) * mm, "end": v(100.07, -590.74) * mm});
            skLineSegment(sketch, "E3244", {"start": v(100.07, -590.74) * mm, "end": v(100.77, -591.83) * mm});
            skLineSegment(sketch, "E3245", {"start": v(100.77, -591.83) * mm, "end": v(101.46, -592.94) * mm});
            skLineSegment(sketch, "E3246", {"start": v(101.46, -592.94) * mm, "end": v(102.13, -594.07) * mm});
            skLineSegment(sketch, "E3247", {"start": v(102.13, -594.07) * mm, "end": v(102.79, -595.22) * mm});
            skLineSegment(sketch, "E3248", {"start": v(102.79, -595.22) * mm, "end": v(103.43, -596.38) * mm});
            skLineSegment(sketch, "E3249", {"start": v(103.43, -596.38) * mm, "end": v(104.06, -597.55) * mm});
            skLineSegment(sketch, "E3250", {"start": v(104.06, -597.55) * mm, "end": v(104.68, -598.74) * mm});
            skLineSegment(sketch, "E3251", {"start": v(104.68, -598.74) * mm, "end": v(105.3, -599.92) * mm});
            skLineSegment(sketch, "E3252", {"start": v(105.3, -599.92) * mm, "end": v(105.9, -601.12) * mm});
            skLineSegment(sketch, "E3253", {"start": v(105.9, -601.12) * mm, "end": v(106.49, -602.32) * mm});
            skLineSegment(sketch, "E3254", {"start": v(106.49, -602.32) * mm, "end": v(107.08, -603.51) * mm});
            skLineSegment(sketch, "E3255", {"start": v(107.08, -603.51) * mm, "end": v(107.66, -604.71) * mm});
            skLineSegment(sketch, "E3256", {"start": v(107.66, -604.71) * mm, "end": v(108.25, -605.9) * mm});
            skLineSegment(sketch, "E3257", {"start": v(108.25, -605.9) * mm, "end": v(108.83, -607.1) * mm});
            skLineSegment(sketch, "E3258", {"start": v(108.83, -607.1) * mm, "end": v(109.4, -608.28) * mm});
            skLineSegment(sketch, "E3259", {"start": v(109.4, -608.28) * mm, "end": v(109.98, -609.45) * mm});
            skLineSegment(sketch, "E3260", {"start": v(109.98, -609.45) * mm, "end": v(110.56, -610.61) * mm});
            skLineSegment(sketch, "E3261", {"start": v(110.56, -610.61) * mm, "end": v(111.15, -611.76) * mm});
            skLineSegment(sketch, "E3262", {"start": v(111.15, -611.76) * mm, "end": v(111.74, -612.9) * mm});
            skLineSegment(sketch, "E3263", {"start": v(111.74, -612.9) * mm, "end": v(112.33, -614) * mm});
            skLineSegment(sketch, "E3264", {"start": v(112.33, -614) * mm, "end": v(112.93, -615.1) * mm});
            skLineSegment(sketch, "E3265", {"start": v(112.93, -615.1) * mm, "end": v(113.54, -616.17) * mm});
            skLineSegment(sketch, "E3266", {"start": v(113.54, -616.17) * mm, "end": v(114.16, -617.22) * mm});
            skLineSegment(sketch, "E3267", {"start": v(114.16, -617.22) * mm, "end": v(114.8, -618.24) * mm});
            skLineSegment(sketch, "E3268", {"start": v(114.8, -618.24) * mm, "end": v(115.43, -619.24) * mm});
            skLineSegment(sketch, "E3269", {"start": v(115.43, -619.24) * mm, "end": v(116.09, -620.2) * mm});
            skLineSegment(sketch, "E3270", {"start": v(116.09, -620.2) * mm, "end": v(116.76, -621.13) * mm});
            skLineSegment(sketch, "E3271", {"start": v(116.76, -621.13) * mm, "end": v(117.44, -622.03) * mm});
            skLineSegment(sketch, "E3272", {"start": v(117.44, -622.03) * mm, "end": v(118.15, -622.9) * mm});
            skLineSegment(sketch, "E3273", {"start": v(118.15, -622.9) * mm, "end": v(118.87, -623.71) * mm});
            skLineSegment(sketch, "E3274", {"start": v(118.87, -623.71) * mm, "end": v(119.6, -624.5) * mm});
            skLineSegment(sketch, "E3275", {"start": v(119.6, -624.5) * mm, "end": v(120.37, -625.23) * mm});
            skLineSegment(sketch, "E3276", {"start": v(120.37, -625.23) * mm, "end": v(121.15, -625.93) * mm});
            skLineSegment(sketch, "E3277", {"start": v(121.15, -625.93) * mm, "end": v(121.96, -626.57) * mm});
            skLineSegment(sketch, "E3278", {"start": v(121.96, -626.57) * mm, "end": v(122.8, -627.17) * mm});
            skLineSegment(sketch, "E3279", {"start": v(122.8, -627.17) * mm, "end": v(123.65, -627.72) * mm});
            skLineSegment(sketch, "E3280", {"start": v(123.65, -627.72) * mm, "end": v(124.54, -628.21) * mm});
            skLineSegment(sketch, "E3281", {"start": v(124.54, -628.21) * mm, "end": v(125.45, -628.65) * mm});
            skLineSegment(sketch, "E3282", {"start": v(125.45, -628.65) * mm, "end": v(126.4, -629.03) * mm});
            skLineSegment(sketch, "E3283", {"start": v(126.4, -629.03) * mm, "end": v(127.37, -629.35) * mm});
            skLineSegment(sketch, "E3284", {"start": v(127.37, -629.35) * mm, "end": v(128.38, -629.61) * mm});
            skLineSegment(sketch, "E3285", {"start": v(128.38, -629.61) * mm, "end": v(129.42, -629.8) * mm});
            skLineSegment(sketch, "E3286", {"start": v(129.42, -629.8) * mm, "end": v(130.5, -629.94) * mm});
            skLineSegment(sketch, "E3287", {"start": v(130.5, -629.94) * mm, "end": v(131.61, -630) * mm});
            skLineSegment(sketch, "E3288", {"start": v(131.61, -630) * mm, "end": v(132.76, -630) * mm});
            skLineSegment(sketch, "E3289", {"start": v(132.76, -630) * mm, "end": v(133.95, -629.91) * mm});
            skLineSegment(sketch, "E3290", {"start": v(133.95, -629.91) * mm, "end": v(135.18, -629.76) * mm});
            skLineSegment(sketch, "E3291", {"start": v(135.18, -629.76) * mm, "end": v(136.45, -629.53) * mm});
            skLineSegment(sketch, "E3292", {"start": v(136.45, -629.53) * mm, "end": v(137.7, -629.24) * mm});
            skLineSegment(sketch, "E3293", {"start": v(137.7, -629.24) * mm, "end": v(138.9, -628.9) * mm});
            skLineSegment(sketch, "E3294", {"start": v(138.9, -628.9) * mm, "end": v(140.04, -628.53) * mm});
            skLineSegment(sketch, "E3295", {"start": v(140.04, -628.53) * mm, "end": v(141.11, -628.1) * mm});
            skLineSegment(sketch, "E3296", {"start": v(141.11, -628.1) * mm, "end": v(142.13, -627.64) * mm});
            skLineSegment(sketch, "E3297", {"start": v(142.13, -627.64) * mm, "end": v(143.1, -627.14) * mm});
            skLineSegment(sketch, "E3298", {"start": v(143.1, -627.14) * mm, "end": v(144, -626.6) * mm});
            skLineSegment(sketch, "E3299", {"start": v(144, -626.6) * mm, "end": v(144.85, -626.02) * mm});
            skLineSegment(sketch, "E3300", {"start": v(144.85, -626.02) * mm, "end": v(145.66, -625.4) * mm});
            skLineSegment(sketch, "E3301", {"start": v(145.66, -625.4) * mm, "end": v(146.41, -624.76) * mm});
            skLineSegment(sketch, "E3302", {"start": v(146.41, -624.76) * mm, "end": v(147.12, -624.07) * mm});
            skLineSegment(sketch, "E3303", {"start": v(147.12, -624.07) * mm, "end": v(147.78, -623.35) * mm});
            skLineSegment(sketch, "E3304", {"start": v(147.78, -623.35) * mm, "end": v(148.4, -622.6) * mm});
            skLineSegment(sketch, "E3305", {"start": v(148.4, -622.6) * mm, "end": v(148.97, -621.81) * mm});
            skLineSegment(sketch, "E3306", {"start": v(148.97, -621.81) * mm, "end": v(149.5, -621) * mm});
            skLineSegment(sketch, "E3307", {"start": v(149.5, -621) * mm, "end": v(149.99, -620.16) * mm});
            skLineSegment(sketch, "E3308", {"start": v(149.99, -620.16) * mm, "end": v(150.44, -619.28) * mm});
            skLineSegment(sketch, "E3309", {"start": v(150.44, -619.28) * mm, "end": v(150.86, -618.38) * mm});
            skLineSegment(sketch, "E3310", {"start": v(150.86, -618.38) * mm, "end": v(151.24, -617.46) * mm});
            skLineSegment(sketch, "E3311", {"start": v(151.24, -617.46) * mm, "end": v(151.6, -616.5) * mm});
            skLineSegment(sketch, "E3312", {"start": v(151.6, -616.5) * mm, "end": v(151.91, -615.53) * mm});
            skLineSegment(sketch, "E3313", {"start": v(151.91, -615.53) * mm, "end": v(152.2, -614.53) * mm});
            skLineSegment(sketch, "E3314", {"start": v(152.2, -614.53) * mm, "end": v(152.47, -613.51) * mm});
            skLineSegment(sketch, "E3315", {"start": v(152.47, -613.51) * mm, "end": v(152.7, -612.47) * mm});
            skLineSegment(sketch, "E3316", {"start": v(152.7, -612.47) * mm, "end": v(152.91, -611.41) * mm});
            skLineSegment(sketch, "E3317", {"start": v(152.91, -611.41) * mm, "end": v(153.1, -610.33) * mm});
            skLineSegment(sketch, "E3318", {"start": v(153.1, -610.33) * mm, "end": v(153.27, -609.23) * mm});
            skLineSegment(sketch, "E3319", {"start": v(153.27, -609.23) * mm, "end": v(153.42, -608.12) * mm});
            skLineSegment(sketch, "E3320", {"start": v(153.42, -608.12) * mm, "end": v(153.54, -607) * mm});
            skLineSegment(sketch, "E3321", {"start": v(153.54, -607) * mm, "end": v(153.66, -605.85) * mm});
            skLineSegment(sketch, "E3322", {"start": v(153.66, -605.85) * mm, "end": v(153.76, -604.69) * mm});
            skLineSegment(sketch, "E3323", {"start": v(153.76, -604.69) * mm, "end": v(153.84, -603.52) * mm});
            skLineSegment(sketch, "E3324", {"start": v(153.84, -603.52) * mm, "end": v(153.91, -602.34) * mm});
            skLineSegment(sketch, "E3325", {"start": v(153.91, -602.34) * mm, "end": v(153.98, -601.15) * mm});
            skLineSegment(sketch, "E3326", {"start": v(153.98, -601.15) * mm, "end": v(154.03, -599.94) * mm});
            skLineSegment(sketch, "E3327", {"start": v(154.03, -599.94) * mm, "end": v(154.08, -598.74) * mm});
            skLineSegment(sketch, "E3328", {"start": v(154.08, -598.74) * mm, "end": v(154.13, -597.52) * mm});
            skLineSegment(sketch, "E3329", {"start": v(154.13, -597.52) * mm, "end": v(154.17, -596.3) * mm});
            skLineSegment(sketch, "E3330", {"start": v(154.17, -596.3) * mm, "end": v(154.21, -595.07) * mm});
            skLineSegment(sketch, "E3331", {"start": v(154.21, -595.07) * mm, "end": v(154.25, -593.84) * mm});
            skLineSegment(sketch, "E3332", {"start": v(154.25, -593.84) * mm, "end": v(154.3, -592.6) * mm});
            skLineSegment(sketch, "E3333", {"start": v(154.3, -592.6) * mm, "end": v(154.34, -591.37) * mm});
            skLineSegment(sketch, "E3334", {"start": v(154.34, -591.37) * mm, "end": v(154.4, -590.13) * mm});
            skLineSegment(sketch, "E3335", {"start": v(154.4, -590.13) * mm, "end": v(154.45, -588.9) * mm});
            skLineSegment(sketch, "E3336", {"start": v(154.45, -588.9) * mm, "end": v(154.52, -587.66) * mm});
            skLineSegment(sketch, "E3337", {"start": v(154.52, -587.66) * mm, "end": v(154.6, -586.43) * mm});
            skLineSegment(sketch, "E3338", {"start": v(154.6, -586.43) * mm, "end": v(154.68, -585.2) * mm});
            skLineSegment(sketch, "E3339", {"start": v(154.68, -585.2) * mm, "end": v(154.78, -583.98) * mm});
            skLineSegment(sketch, "E3340", {"start": v(154.78, -583.98) * mm, "end": v(154.9, -582.76) * mm});
            skLineSegment(sketch, "E3341", {"start": v(154.9, -582.76) * mm, "end": v(155.04, -581.55) * mm});
            skLineSegment(sketch, "E3342", {"start": v(155.04, -581.55) * mm, "end": v(155.19, -580.35) * mm});
            skLineSegment(sketch, "E3343", {"start": v(155.19, -580.35) * mm, "end": v(155.36, -579.15) * mm});
            skLineSegment(sketch, "E3344", {"start": v(155.36, -579.15) * mm, "end": v(155.55, -577.97) * mm});
            skLineSegment(sketch, "E3345", {"start": v(155.55, -577.97) * mm, "end": v(155.77, -576.8) * mm});
            skLineSegment(sketch, "E3346", {"start": v(155.77, -576.8) * mm, "end": v(156.01, -575.63) * mm});
            skLineSegment(sketch, "E3347", {"start": v(156.01, -575.63) * mm, "end": v(156.28, -574.49) * mm});
            skLineSegment(sketch, "E3348", {"start": v(156.28, -574.49) * mm, "end": v(156.58, -573.35) * mm});
            skLineSegment(sketch, "E3349", {"start": v(156.58, -573.35) * mm, "end": v(156.9, -572.23) * mm});
            skLineSegment(sketch, "E3350", {"start": v(156.9, -572.23) * mm, "end": v(157.27, -571.13) * mm});
            skLineSegment(sketch, "E3351", {"start": v(157.27, -571.13) * mm, "end": v(157.66, -570.04) * mm});
            skLineSegment(sketch, "E3352", {"start": v(157.66, -570.04) * mm, "end": v(158.09, -568.98) * mm});
            skLineSegment(sketch, "E3353", {"start": v(158.09, -568.98) * mm, "end": v(158.55, -567.93) * mm});
            skLineSegment(sketch, "E3354", {"start": v(158.55, -567.93) * mm, "end": v(159.06, -566.9) * mm});
            skLineSegment(sketch, "E3355", {"start": v(159.06, -566.9) * mm, "end": v(159.6, -565.9) * mm});
            skLineSegment(sketch, "E3356", {"start": v(159.6, -565.9) * mm, "end": v(160.18, -564.92) * mm});
            skLineSegment(sketch, "E3357", {"start": v(160.18, -564.92) * mm, "end": v(160.81, -563.96) * mm});
            skLineSegment(sketch, "E3358", {"start": v(160.81, -563.96) * mm, "end": v(161.48, -563.03) * mm});
            skLineSegment(sketch, "E3359", {"start": v(161.48, -563.03) * mm, "end": v(162.2, -562.12) * mm});
            skLineSegment(sketch, "E3360", {"start": v(162.2, -562.12) * mm, "end": v(162.97, -561.24) * mm});
            skLineSegment(sketch, "E3361", {"start": v(162.97, -561.24) * mm, "end": v(163.79, -560.39) * mm});
            skLineSegment(sketch, "E3362", {"start": v(163.79, -560.39) * mm, "end": v(164.66, -559.56) * mm});
            skLineSegment(sketch, "E3363", {"start": v(164.66, -559.56) * mm, "end": v(165.58, -558.77) * mm});
            skLineSegment(sketch, "E3364", {"start": v(165.58, -558.77) * mm, "end": v(166.55, -558) * mm});
            skLineSegment(sketch, "E3365", {"start": v(166.55, -558) * mm, "end": v(167.59, -557.28) * mm});
            skLineSegment(sketch, "E3366", {"start": v(167.59, -557.28) * mm, "end": v(168.68, -556.58) * mm});
            skLineSegment(sketch, "E3367", {"start": v(168.68, -556.58) * mm, "end": v(169.83, -555.92) * mm});
            skLineSegment(sketch, "E3368", {"start": v(169.83, -555.92) * mm, "end": v(171.04, -555.3) * mm});
            skLineSegment(sketch, "E3369", {"start": v(171.04, -555.3) * mm, "end": v(172.32, -554.7) * mm});
            skLineSegment(sketch, "E3370", {"start": v(172.32, -554.7) * mm, "end": v(173.66, -554.15) * mm});
            skLineSegment(sketch, "E3371", {"start": v(173.66, -554.15) * mm, "end": v(175.07, -553.64) * mm});
            skLineSegment(sketch, "E3372", {"start": v(175.07, -553.64) * mm, "end": v(176.54, -553.16) * mm});
            skLineSegment(sketch, "E3373", {"start": v(176.54, -553.16) * mm, "end": v(178.09, -552.73) * mm});
            skLineSegment(sketch, "E3374", {"start": v(178.09, -552.73) * mm, "end": v(179.58, -552.38) * mm});
            skLineSegment(sketch, "E3375", {"start": v(179.58, -552.38) * mm, "end": v(181.04, -552.1) * mm});
            skLineSegment(sketch, "E3376", {"start": v(181.04, -552.1) * mm, "end": v(182.46, -551.9) * mm});
            skLineSegment(sketch, "E3377", {"start": v(182.46, -551.9) * mm, "end": v(183.85, -551.78) * mm});
            skLineSegment(sketch, "E3378", {"start": v(183.85, -551.78) * mm, "end": v(185.2, -551.73) * mm});
            skLineSegment(sketch, "E3379", {"start": v(185.2, -551.73) * mm, "end": v(186.53, -551.75) * mm});
            skLineSegment(sketch, "E3380", {"start": v(186.53, -551.75) * mm, "end": v(187.82, -551.84) * mm});
            skLineSegment(sketch, "E3381", {"start": v(187.82, -551.84) * mm, "end": v(189.08, -551.99) * mm});
            skLineSegment(sketch, "E3382", {"start": v(189.08, -551.99) * mm, "end": v(190.32, -552.2) * mm});
            skLineSegment(sketch, "E3383", {"start": v(190.32, -552.2) * mm, "end": v(191.52, -552.48) * mm});
            skLineSegment(sketch, "E3384", {"start": v(191.52, -552.48) * mm, "end": v(192.7, -552.81) * mm});
            skLineSegment(sketch, "E3385", {"start": v(192.7, -552.81) * mm, "end": v(193.85, -553.2) * mm});
            skLineSegment(sketch, "E3386", {"start": v(193.85, -553.2) * mm, "end": v(194.97, -553.65) * mm});
            skLineSegment(sketch, "E3387", {"start": v(194.97, -553.65) * mm, "end": v(196.07, -554.15) * mm});
            skLineSegment(sketch, "E3388", {"start": v(196.07, -554.15) * mm, "end": v(197.14, -554.7) * mm});
            skLineSegment(sketch, "E3389", {"start": v(197.14, -554.7) * mm, "end": v(198.2, -555.29) * mm});
            skLineSegment(sketch, "E3390", {"start": v(198.2, -555.29) * mm, "end": v(199.22, -555.93) * mm});
            skLineSegment(sketch, "E3391", {"start": v(199.22, -555.93) * mm, "end": v(200.23, -556.61) * mm});
            skLineSegment(sketch, "E3392", {"start": v(200.23, -556.61) * mm, "end": v(201.21, -557.33) * mm});
            skLineSegment(sketch, "E3393", {"start": v(201.21, -557.33) * mm, "end": v(202.18, -558.1) * mm});
            skLineSegment(sketch, "E3394", {"start": v(202.18, -558.1) * mm, "end": v(203.13, -558.9) * mm});
            skLineSegment(sketch, "E3395", {"start": v(203.13, -558.9) * mm, "end": v(204.06, -559.72) * mm});
            skLineSegment(sketch, "E3396", {"start": v(204.06, -559.72) * mm, "end": v(204.97, -560.58) * mm});
            skLineSegment(sketch, "E3397", {"start": v(204.97, -560.58) * mm, "end": v(205.87, -561.48) * mm});
            skLineSegment(sketch, "E3398", {"start": v(205.87, -561.48) * mm, "end": v(206.75, -562.4) * mm});
            skLineSegment(sketch, "E3399", {"start": v(206.75, -562.4) * mm, "end": v(207.61, -563.34) * mm});
            skLineSegment(sketch, "E3400", {"start": v(207.61, -563.34) * mm, "end": v(208.47, -564.3) * mm});
            skLineSegment(sketch, "E3401", {"start": v(208.47, -564.3) * mm, "end": v(209.3, -565.29) * mm});
            skLineSegment(sketch, "E3402", {"start": v(209.3, -565.29) * mm, "end": v(210.14, -566.29) * mm});
            skLineSegment(sketch, "E3403", {"start": v(210.14, -566.29) * mm, "end": v(210.96, -567.3) * mm});
            skLineSegment(sketch, "E3404", {"start": v(210.96, -567.3) * mm, "end": v(211.77, -568.34) * mm});
            skLineSegment(sketch, "E3405", {"start": v(211.77, -568.34) * mm, "end": v(212.57, -569.38) * mm});
            skLineSegment(sketch, "E3406", {"start": v(212.57, -569.38) * mm, "end": v(213.36, -570.43) * mm});
            skLineSegment(sketch, "E3407", {"start": v(213.36, -570.43) * mm, "end": v(214.14, -571.49) * mm});
            skLineSegment(sketch, "E3408", {"start": v(214.14, -571.49) * mm, "end": v(214.92, -572.55) * mm});
            skLineSegment(sketch, "E3409", {"start": v(214.92, -572.55) * mm, "end": v(215.7, -573.62) * mm});
            skLineSegment(sketch, "E3410", {"start": v(215.7, -573.62) * mm, "end": v(216.46, -574.68) * mm});
            skLineSegment(sketch, "E3411", {"start": v(216.46, -574.68) * mm, "end": v(217.23, -575.74) * mm});
            skLineSegment(sketch, "E3412", {"start": v(217.23, -575.74) * mm, "end": v(218, -576.8) * mm});
            skLineSegment(sketch, "E3413", {"start": v(218, -576.8) * mm, "end": v(218.75, -577.85) * mm});
            skLineSegment(sketch, "E3414", {"start": v(218.75, -577.85) * mm, "end": v(219.51, -578.88) * mm});
            skLineSegment(sketch, "E3415", {"start": v(219.51, -578.88) * mm, "end": v(220.27, -579.91) * mm});
            skLineSegment(sketch, "E3416", {"start": v(220.27, -579.91) * mm, "end": v(221.03, -580.93) * mm});
            skLineSegment(sketch, "E3417", {"start": v(221.03, -580.93) * mm, "end": v(221.8, -581.92) * mm});
            skLineSegment(sketch, "E3418", {"start": v(221.8, -581.92) * mm, "end": v(222.56, -582.9) * mm});
            skLineSegment(sketch, "E3419", {"start": v(222.56, -582.9) * mm, "end": v(223.33, -583.86) * mm});
            skLineSegment(sketch, "E3420", {"start": v(223.33, -583.86) * mm, "end": v(224.1, -584.8) * mm});
            skLineSegment(sketch, "E3421", {"start": v(224.1, -584.8) * mm, "end": v(224.88, -585.7) * mm});
            skLineSegment(sketch, "E3422", {"start": v(224.88, -585.7) * mm, "end": v(225.66, -586.59) * mm});
            skLineSegment(sketch, "E3423", {"start": v(225.66, -586.59) * mm, "end": v(226.45, -587.44) * mm});
            skLineSegment(sketch, "E3424", {"start": v(226.45, -587.44) * mm, "end": v(227.25, -588.26) * mm});
            skLineSegment(sketch, "E3425", {"start": v(227.25, -588.26) * mm, "end": v(228.06, -589.05) * mm});
            skLineSegment(sketch, "E3426", {"start": v(228.06, -589.05) * mm, "end": v(228.88, -589.8) * mm});
            skLineSegment(sketch, "E3427", {"start": v(228.88, -589.8) * mm, "end": v(229.7, -590.5) * mm});
            skLineSegment(sketch, "E3428", {"start": v(229.7, -590.5) * mm, "end": v(230.55, -591.18) * mm});
            skLineSegment(sketch, "E3429", {"start": v(230.55, -591.18) * mm, "end": v(231.4, -591.8) * mm});
            skLineSegment(sketch, "E3430", {"start": v(231.4, -591.8) * mm, "end": v(232.27, -592.38) * mm});
            skLineSegment(sketch, "E3431", {"start": v(232.27, -592.38) * mm, "end": v(233.15, -592.91) * mm});
            skLineSegment(sketch, "E3432", {"start": v(233.15, -592.91) * mm, "end": v(234.05, -593.4) * mm});
            skLineSegment(sketch, "E3433", {"start": v(234.05, -593.4) * mm, "end": v(234.96, -593.82) * mm});
            skLineSegment(sketch, "E3434", {"start": v(234.96, -593.82) * mm, "end": v(235.89, -594.2) * mm});
            skLineSegment(sketch, "E3435", {"start": v(235.89, -594.2) * mm, "end": v(236.84, -594.51) * mm});
            skLineSegment(sketch, "E3436", {"start": v(236.84, -594.51) * mm, "end": v(237.8, -594.77) * mm});
            skLineSegment(sketch, "E3437", {"start": v(237.8, -594.77) * mm, "end": v(238.79, -594.97) * mm});
            skLineSegment(sketch, "E3438", {"start": v(238.79, -594.97) * mm, "end": v(239.8, -595.1) * mm});
            skLineSegment(sketch, "E3439", {"start": v(239.8, -595.1) * mm, "end": v(240.82, -595.16) * mm});
            skLineSegment(sketch, "E3440", {"start": v(240.82, -595.16) * mm, "end": v(241.87, -595.16) * mm});
            skLineSegment(sketch, "E3441", {"start": v(241.87, -595.16) * mm, "end": v(242.94, -595.09) * mm});
            skLineSegment(sketch, "E3442", {"start": v(242.94, -595.09) * mm, "end": v(244.04, -594.94) * mm});
            skLineSegment(sketch, "E3443", {"start": v(244.04, -594.94) * mm, "end": v(245.16, -594.72) * mm});
            skLineSegment(sketch, "E3444", {"start": v(245.16, -594.72) * mm, "end": v(246.31, -594.42) * mm});
            skLineSegment(sketch, "E3445", {"start": v(246.31, -594.42) * mm, "end": v(247.49, -594.04) * mm});
            skLineSegment(sketch, "E3446", {"start": v(247.49, -594.04) * mm, "end": v(248.69, -593.58) * mm});
            skLineSegment(sketch, "E3447", {"start": v(248.69, -593.58) * mm, "end": v(249.91, -593.05) * mm});
            skLineSegment(sketch, "E3448", {"start": v(249.91, -593.05) * mm, "end": v(251.07, -592.48) * mm});
            skLineSegment(sketch, "E3449", {"start": v(251.07, -592.48) * mm, "end": v(252.15, -591.89) * mm});
            skLineSegment(sketch, "E3450", {"start": v(252.15, -591.89) * mm, "end": v(253.17, -591.27) * mm});
            skLineSegment(sketch, "E3451", {"start": v(253.17, -591.27) * mm, "end": v(254.12, -590.62) * mm});
            skLineSegment(sketch, "E3452", {"start": v(254.12, -590.62) * mm, "end": v(255, -589.95) * mm});
            skLineSegment(sketch, "E3453", {"start": v(255, -589.95) * mm, "end": v(255.83, -589.25) * mm});
            skLineSegment(sketch, "E3454", {"start": v(255.83, -589.25) * mm, "end": v(256.6, -588.52) * mm});
            skLineSegment(sketch, "E3455", {"start": v(256.6, -588.52) * mm, "end": v(257.3, -587.78) * mm});
            skLineSegment(sketch, "E3456", {"start": v(257.3, -587.78) * mm, "end": v(257.95, -587) * mm});
            skLineSegment(sketch, "E3457", {"start": v(257.95, -587) * mm, "end": v(258.55, -586.2) * mm});
            skLineSegment(sketch, "E3458", {"start": v(258.55, -586.2) * mm, "end": v(259.1, -585.4) * mm});
            skLineSegment(sketch, "E3459", {"start": v(259.1, -585.4) * mm, "end": v(259.59, -584.55) * mm});
            skLineSegment(sketch, "E3460", {"start": v(259.59, -584.55) * mm, "end": v(260.03, -583.7) * mm});
            skLineSegment(sketch, "E3461", {"start": v(260.03, -583.7) * mm, "end": v(260.43, -582.81) * mm});
            skLineSegment(sketch, "E3462", {"start": v(260.43, -582.81) * mm, "end": v(260.78, -581.91) * mm});
            skLineSegment(sketch, "E3463", {"start": v(260.78, -581.91) * mm, "end": v(261.08, -581) * mm});
            skLineSegment(sketch, "E3464", {"start": v(261.08, -581) * mm, "end": v(261.35, -580.06) * mm});
            skLineSegment(sketch, "E3465", {"start": v(261.35, -580.06) * mm, "end": v(261.57, -579.1) * mm});
            skLineSegment(sketch, "E3466", {"start": v(261.57, -579.1) * mm, "end": v(261.76, -578.13) * mm});
            skLineSegment(sketch, "E3467", {"start": v(261.76, -578.13) * mm, "end": v(261.91, -577.14) * mm});
            skLineSegment(sketch, "E3468", {"start": v(261.91, -577.14) * mm, "end": v(262.03, -576.14) * mm});
            skLineSegment(sketch, "E3469", {"start": v(262.03, -576.14) * mm, "end": v(262.11, -575.12) * mm});
            skLineSegment(sketch, "E3470", {"start": v(262.11, -575.12) * mm, "end": v(262.17, -574.09) * mm});
            skLineSegment(sketch, "E3471", {"start": v(262.17, -574.09) * mm, "end": v(262.2, -573.04) * mm});
            skLineSegment(sketch, "E3472", {"start": v(262.2, -573.04) * mm, "end": v(262.2, -571.98) * mm});
            skLineSegment(sketch, "E3473", {"start": v(262.2, -571.98) * mm, "end": v(262.17, -570.9) * mm});
            skLineSegment(sketch, "E3474", {"start": v(262.17, -570.9) * mm, "end": v(262.11, -569.82) * mm});
            skLineSegment(sketch, "E3475", {"start": v(262.11, -569.82) * mm, "end": v(262.04, -568.72) * mm});
            skLineSegment(sketch, "E3476", {"start": v(262.04, -568.72) * mm, "end": v(261.95, -567.62) * mm});
            skLineSegment(sketch, "E3477", {"start": v(261.95, -567.62) * mm, "end": v(261.84, -566.5) * mm});
            skLineSegment(sketch, "E3478", {"start": v(261.84, -566.5) * mm, "end": v(261.72, -565.37) * mm});
            skLineSegment(sketch, "E3479", {"start": v(261.72, -565.37) * mm, "end": v(261.58, -564.24) * mm});
            skLineSegment(sketch, "E3480", {"start": v(261.58, -564.24) * mm, "end": v(261.43, -563.1) * mm});
            skLineSegment(sketch, "E3481", {"start": v(261.43, -563.1) * mm, "end": v(261.27, -561.95) * mm});
            skLineSegment(sketch, "E3482", {"start": v(261.27, -561.95) * mm, "end": v(261.1, -560.8) * mm});
            skLineSegment(sketch, "E3483", {"start": v(261.1, -560.8) * mm, "end": v(260.92, -559.63) * mm});
            skLineSegment(sketch, "E3484", {"start": v(260.92, -559.63) * mm, "end": v(260.74, -558.47) * mm});
            skLineSegment(sketch, "E3485", {"start": v(260.74, -558.47) * mm, "end": v(260.55, -557.3) * mm});
            skLineSegment(sketch, "E3486", {"start": v(260.55, -557.3) * mm, "end": v(260.37, -556.12) * mm});
            skLineSegment(sketch, "E3487", {"start": v(260.37, -556.12) * mm, "end": v(260.18, -554.94) * mm});
            skLineSegment(sketch, "E3488", {"start": v(260.18, -554.94) * mm, "end": v(260, -553.76) * mm});
            skLineSegment(sketch, "E3489", {"start": v(260, -553.76) * mm, "end": v(259.82, -552.58) * mm});
            skLineSegment(sketch, "E3490", {"start": v(259.82, -552.58) * mm, "end": v(259.65, -551.4) * mm});
            skLineSegment(sketch, "E3491", {"start": v(259.65, -551.4) * mm, "end": v(259.48, -550.2) * mm});
            skLineSegment(sketch, "E3492", {"start": v(259.48, -550.2) * mm, "end": v(259.33, -549.02) * mm});
            skLineSegment(sketch, "E3493", {"start": v(259.33, -549.02) * mm, "end": v(259.18, -547.84) * mm});
            skLineSegment(sketch, "E3494", {"start": v(259.18, -547.84) * mm, "end": v(259.05, -546.65) * mm});
            skLineSegment(sketch, "E3495", {"start": v(259.05, -546.65) * mm, "end": v(258.94, -545.47) * mm});
            skLineSegment(sketch, "E3496", {"start": v(258.94, -545.47) * mm, "end": v(258.84, -544.3) * mm});
            skLineSegment(sketch, "E3497", {"start": v(258.84, -544.3) * mm, "end": v(258.77, -543.12) * mm});
            skLineSegment(sketch, "E3498", {"start": v(258.77, -543.12) * mm, "end": v(258.7, -541.95) * mm});
            skLineSegment(sketch, "E3499", {"start": v(258.7, -541.95) * mm, "end": v(258.67, -540.78) * mm});
            skLineSegment(sketch, "E3500", {"start": v(258.67, -540.78) * mm, "end": v(258.67, -539.62) * mm});
            skLineSegment(sketch, "E3501", {"start": v(258.67, -539.62) * mm, "end": v(258.68, -538.46) * mm});
            skLineSegment(sketch, "E3502", {"start": v(258.68, -538.46) * mm, "end": v(258.73, -537.31) * mm});
            skLineSegment(sketch, "E3503", {"start": v(258.73, -537.31) * mm, "end": v(258.8, -536.17) * mm});
            skLineSegment(sketch, "E3504", {"start": v(258.8, -536.17) * mm, "end": v(258.9, -535.04) * mm});
            skLineSegment(sketch, "E3505", {"start": v(258.9, -535.04) * mm, "end": v(259.05, -533.91) * mm});
            skLineSegment(sketch, "E3506", {"start": v(259.05, -533.91) * mm, "end": v(259.23, -532.8) * mm});
            skLineSegment(sketch, "E3507", {"start": v(259.23, -532.8) * mm, "end": v(259.44, -531.69) * mm});
            skLineSegment(sketch, "E3508", {"start": v(259.44, -531.69) * mm, "end": v(259.7, -530.6) * mm});
            skLineSegment(sketch, "E3509", {"start": v(259.7, -530.6) * mm, "end": v(259.99, -529.5) * mm});
            skLineSegment(sketch, "E3510", {"start": v(259.99, -529.5) * mm, "end": v(260.33, -528.44) * mm});
            skLineSegment(sketch, "E3511", {"start": v(260.33, -528.44) * mm, "end": v(260.7, -527.38) * mm});
            skLineSegment(sketch, "E3512", {"start": v(260.7, -527.38) * mm, "end": v(261.14, -526.33) * mm});
            skLineSegment(sketch, "E3513", {"start": v(261.14, -526.33) * mm, "end": v(261.61, -525.3) * mm});
            skLineSegment(sketch, "E3514", {"start": v(261.61, -525.3) * mm, "end": v(262.14, -524.28) * mm});
            skLineSegment(sketch, "E3515", {"start": v(262.14, -524.28) * mm, "end": v(262.72, -523.27) * mm});
            skLineSegment(sketch, "E3516", {"start": v(262.72, -523.27) * mm, "end": v(263.36, -522.28) * mm});
            skLineSegment(sketch, "E3517", {"start": v(263.36, -522.28) * mm, "end": v(264.05, -521.31) * mm});
            skLineSegment(sketch, "E3518", {"start": v(264.05, -521.31) * mm, "end": v(264.8, -520.36) * mm});
            skLineSegment(sketch, "E3519", {"start": v(264.8, -520.36) * mm, "end": v(265.6, -519.42) * mm});
            skLineSegment(sketch, "E3520", {"start": v(265.6, -519.42) * mm, "end": v(266.47, -518.5) * mm});
            skLineSegment(sketch, "E3521", {"start": v(266.47, -518.5) * mm, "end": v(267.4, -517.6) * mm});
            skLineSegment(sketch, "E3522", {"start": v(267.4, -517.6) * mm, "end": v(268.4, -516.72) * mm});
            skLineSegment(sketch, "E3523", {"start": v(268.4, -516.72) * mm, "end": v(269.46, -515.86) * mm});
            skLineSegment(sketch, "E3524", {"start": v(269.46, -515.86) * mm, "end": v(270.6, -515.02) * mm});
            skLineSegment(sketch, "E3525", {"start": v(270.6, -515.02) * mm, "end": v(271.8, -514.2) * mm});
            skLineSegment(sketch, "E3526", {"start": v(271.8, -514.2) * mm, "end": v(273.07, -513.41) * mm});
            skLineSegment(sketch, "E3527", {"start": v(273.07, -513.41) * mm, "end": v(274.42, -512.64) * mm});
            skLineSegment(sketch, "E3528", {"start": v(274.42, -512.64) * mm, "end": v(275.85, -511.9) * mm});
            skLineSegment(sketch, "E3529", {"start": v(275.85, -511.9) * mm, "end": v(277.25, -511.22) * mm});
            skLineSegment(sketch, "E3530", {"start": v(277.25, -511.22) * mm, "end": v(278.63, -510.64) * mm});
            skLineSegment(sketch, "E3531", {"start": v(278.63, -510.64) * mm, "end": v(279.99, -510.13) * mm});
            skLineSegment(sketch, "E3532", {"start": v(279.99, -510.13) * mm, "end": v(281.33, -509.7) * mm});
            skLineSegment(sketch, "E3533", {"start": v(281.33, -509.7) * mm, "end": v(282.64, -509.34) * mm});
            skLineSegment(sketch, "E3534", {"start": v(282.64, -509.34) * mm, "end": v(283.94, -509.05) * mm});
            skLineSegment(sketch, "E3535", {"start": v(283.94, -509.05) * mm, "end": v(285.22, -508.83) * mm});
            skLineSegment(sketch, "E3536", {"start": v(285.22, -508.83) * mm, "end": v(286.48, -508.69) * mm});
            skLineSegment(sketch, "E3537", {"start": v(286.48, -508.69) * mm, "end": v(287.72, -508.6) * mm});
            skLineSegment(sketch, "E3538", {"start": v(287.72, -508.6) * mm, "end": v(288.94, -508.58) * mm});
            skLineSegment(sketch, "E3539", {"start": v(288.94, -508.58) * mm, "end": v(290.14, -508.63) * mm});
            skLineSegment(sketch, "E3540", {"start": v(290.14, -508.63) * mm, "end": v(291.33, -508.73) * mm});
            skLineSegment(sketch, "E3541", {"start": v(291.33, -508.73) * mm, "end": v(292.5, -508.89) * mm});
            skLineSegment(sketch, "E3542", {"start": v(292.5, -508.89) * mm, "end": v(293.65, -509.1) * mm});
            skLineSegment(sketch, "E3543", {"start": v(293.65, -509.1) * mm, "end": v(294.8, -509.36) * mm});
            skLineSegment(sketch, "E3544", {"start": v(294.8, -509.36) * mm, "end": v(295.92, -509.68) * mm});
            skLineSegment(sketch, "E3545", {"start": v(295.92, -509.68) * mm, "end": v(297.03, -510.04) * mm});
            skLineSegment(sketch, "E3546", {"start": v(297.03, -510.04) * mm, "end": v(298.12, -510.45) * mm});
            skLineSegment(sketch, "E3547", {"start": v(298.12, -510.45) * mm, "end": v(299.2, -510.9) * mm});
            skLineSegment(sketch, "E3548", {"start": v(299.2, -510.9) * mm, "end": v(300.27, -511.4) * mm});
            skLineSegment(sketch, "E3549", {"start": v(300.27, -511.4) * mm, "end": v(301.33, -511.93) * mm});
            skLineSegment(sketch, "E3550", {"start": v(301.33, -511.93) * mm, "end": v(302.38, -512.5) * mm});
            skLineSegment(sketch, "E3551", {"start": v(302.38, -512.5) * mm, "end": v(303.41, -513.11) * mm});
            skLineSegment(sketch, "E3552", {"start": v(303.41, -513.11) * mm, "end": v(304.43, -513.75) * mm});
            skLineSegment(sketch, "E3553", {"start": v(304.43, -513.75) * mm, "end": v(305.45, -514.42) * mm});
            skLineSegment(sketch, "E3554", {"start": v(305.45, -514.42) * mm, "end": v(306.45, -515.12) * mm});
            skLineSegment(sketch, "E3555", {"start": v(306.45, -515.12) * mm, "end": v(307.44, -515.84) * mm});
            skLineSegment(sketch, "E3556", {"start": v(307.44, -515.84) * mm, "end": v(308.43, -516.59) * mm});
            skLineSegment(sketch, "E3557", {"start": v(308.43, -516.59) * mm, "end": v(309.4, -517.36) * mm});
            skLineSegment(sketch, "E3558", {"start": v(309.4, -517.36) * mm, "end": v(310.37, -518.14) * mm});
            skLineSegment(sketch, "E3559", {"start": v(310.37, -518.14) * mm, "end": v(311.33, -518.95) * mm});
            skLineSegment(sketch, "E3560", {"start": v(311.33, -518.95) * mm, "end": v(312.29, -519.77) * mm});
            skLineSegment(sketch, "E3561", {"start": v(312.29, -519.77) * mm, "end": v(313.24, -520.6) * mm});
            skLineSegment(sketch, "E3562", {"start": v(313.24, -520.6) * mm, "end": v(314.18, -521.45) * mm});
            skLineSegment(sketch, "E3563", {"start": v(314.18, -521.45) * mm, "end": v(315.12, -522.3) * mm});
            skLineSegment(sketch, "E3564", {"start": v(315.12, -522.3) * mm, "end": v(316.05, -523.16) * mm});
            skLineSegment(sketch, "E3565", {"start": v(316.05, -523.16) * mm, "end": v(316.98, -524.03) * mm});
            skLineSegment(sketch, "E3566", {"start": v(316.98, -524.03) * mm, "end": v(317.9, -524.9) * mm});
            skLineSegment(sketch, "E3567", {"start": v(317.9, -524.9) * mm, "end": v(318.83, -525.76) * mm});
            skLineSegment(sketch, "E3568", {"start": v(318.83, -525.76) * mm, "end": v(319.75, -526.62) * mm});
            skLineSegment(sketch, "E3569", {"start": v(319.75, -526.62) * mm, "end": v(320.66, -527.48) * mm});
            skLineSegment(sketch, "E3570", {"start": v(320.66, -527.48) * mm, "end": v(321.58, -528.33) * mm});
            skLineSegment(sketch, "E3571", {"start": v(321.58, -528.33) * mm, "end": v(322.5, -529.18) * mm});
            skLineSegment(sketch, "E3572", {"start": v(322.5, -529.18) * mm, "end": v(323.4, -530) * mm});
            skLineSegment(sketch, "E3573", {"start": v(323.4, -530) * mm, "end": v(324.32, -530.82) * mm});
            skLineSegment(sketch, "E3574", {"start": v(324.32, -530.82) * mm, "end": v(325.24, -531.63) * mm});
            skLineSegment(sketch, "E3575", {"start": v(325.24, -531.63) * mm, "end": v(326.15, -532.41) * mm});
            skLineSegment(sketch, "E3576", {"start": v(326.15, -532.41) * mm, "end": v(327.07, -533.18) * mm});
            skLineSegment(sketch, "E3577", {"start": v(327.07, -533.18) * mm, "end": v(327.99, -533.92) * mm});
            skLineSegment(sketch, "E3578", {"start": v(327.99, -533.92) * mm, "end": v(328.91, -534.64) * mm});
            skLineSegment(sketch, "E3579", {"start": v(328.91, -534.64) * mm, "end": v(329.84, -535.33) * mm});
            skLineSegment(sketch, "E3580", {"start": v(329.84, -535.33) * mm, "end": v(330.76, -536) * mm});
            skLineSegment(sketch, "E3581", {"start": v(330.76, -536) * mm, "end": v(331.7, -536.62) * mm});
            skLineSegment(sketch, "E3582", {"start": v(331.7, -536.62) * mm, "end": v(332.63, -537.22) * mm});
            skLineSegment(sketch, "E3583", {"start": v(332.63, -537.22) * mm, "end": v(333.58, -537.78) * mm});
            skLineSegment(sketch, "E3584", {"start": v(333.58, -537.78) * mm, "end": v(334.52, -538.3) * mm});
            skLineSegment(sketch, "E3585", {"start": v(334.52, -538.3) * mm, "end": v(335.48, -538.8) * mm});
            skLineSegment(sketch, "E3586", {"start": v(335.48, -538.8) * mm, "end": v(336.44, -539.24) * mm});
            skLineSegment(sketch, "E3587", {"start": v(336.44, -539.24) * mm, "end": v(337.4, -539.64) * mm});
            skLineSegment(sketch, "E3588", {"start": v(337.4, -539.64) * mm, "end": v(338.38, -540) * mm});
            skLineSegment(sketch, "E3589", {"start": v(338.38, -540) * mm, "end": v(339.37, -540.3) * mm});
            skLineSegment(sketch, "E3590", {"start": v(339.37, -540.3) * mm, "end": v(340.36, -540.55) * mm});
            skLineSegment(sketch, "E3591", {"start": v(340.36, -540.55) * mm, "end": v(341.36, -540.75) * mm});
            skLineSegment(sketch, "E3592", {"start": v(341.36, -540.75) * mm, "end": v(342.37, -540.9) * mm});
            skLineSegment(sketch, "E3593", {"start": v(342.37, -540.9) * mm, "end": v(343.4, -540.99) * mm});
            skLineSegment(sketch, "E3594", {"start": v(343.4, -540.99) * mm, "end": v(344.43, -541.01) * mm});
            skLineSegment(sketch, "E3595", {"start": v(344.43, -541.01) * mm, "end": v(345.47, -540.98) * mm});
            skLineSegment(sketch, "E3596", {"start": v(345.47, -540.98) * mm, "end": v(346.53, -540.89) * mm});
            skLineSegment(sketch, "E3597", {"start": v(346.53, -540.89) * mm, "end": v(347.6, -540.72) * mm});
            skLineSegment(sketch, "E3598", {"start": v(347.6, -540.72) * mm, "end": v(348.68, -540.5) * mm});
            skLineSegment(sketch, "E3599", {"start": v(348.68, -540.5) * mm, "end": v(349.77, -540.19) * mm});
            skLineSegment(sketch, "E3600", {"start": v(349.77, -540.19) * mm, "end": v(350.88, -539.82) * mm});
            skLineSegment(sketch, "E3601", {"start": v(350.88, -539.82) * mm, "end": v(352, -539.37) * mm});
            skLineSegment(sketch, "E3602", {"start": v(352, -539.37) * mm, "end": v(353.14, -538.84) * mm});
            skLineSegment(sketch, "E3603", {"start": v(353.14, -538.84) * mm, "end": v(354.3, -538.23) * mm});
            skLineSegment(sketch, "E3604", {"start": v(354.3, -538.23) * mm, "end": v(355.47, -537.55) * mm});
            skLineSegment(sketch, "E3605", {"start": v(355.47, -537.55) * mm, "end": v(357.08, -536.47) * mm});
            skLineSegment(sketch, "E3606", {"start": v(357.08, -536.47) * mm, "end": v(358.51, -535.37) * mm});
            skLineSegment(sketch, "E3607", {"start": v(358.51, -535.37) * mm, "end": v(359.77, -534.24) * mm});
            skLineSegment(sketch, "E3608", {"start": v(359.77, -534.24) * mm, "end": v(360.86, -533.07) * mm});
            skLineSegment(sketch, "E3609", {"start": v(360.86, -533.07) * mm, "end": v(361.8, -531.88) * mm});
            skLineSegment(sketch, "E3610", {"start": v(361.8, -531.88) * mm, "end": v(362.58, -530.67) * mm});
            skLineSegment(sketch, "E3611", {"start": v(362.58, -530.67) * mm, "end": v(363.21, -529.43) * mm});
            skLineSegment(sketch, "E3612", {"start": v(363.21, -529.43) * mm, "end": v(363.71, -528.17) * mm});
            skLineSegment(sketch, "E3613", {"start": v(363.71, -528.17) * mm, "end": v(364.09, -526.88) * mm});
            skLineSegment(sketch, "E3614", {"start": v(364.09, -526.88) * mm, "end": v(364.34, -525.58) * mm});
            skLineSegment(sketch, "E3615", {"start": v(364.34, -525.58) * mm, "end": v(364.47, -524.25) * mm});
            skLineSegment(sketch, "E3616", {"start": v(364.47, -524.25) * mm, "end": v(364.5, -522.91) * mm});
            skLineSegment(sketch, "E3617", {"start": v(364.5, -522.91) * mm, "end": v(364.43, -521.56) * mm});
            skLineSegment(sketch, "E3618", {"start": v(364.43, -521.56) * mm, "end": v(364.27, -520.18) * mm});
            skLineSegment(sketch, "E3619", {"start": v(364.27, -520.18) * mm, "end": v(364.02, -518.8) * mm});
            skLineSegment(sketch, "E3620", {"start": v(364.02, -518.8) * mm, "end": v(363.7, -517.4) * mm});
            skLineSegment(sketch, "E3621", {"start": v(363.7, -517.4) * mm, "end": v(363.3, -516) * mm});
            skLineSegment(sketch, "E3622", {"start": v(363.3, -516) * mm, "end": v(362.85, -514.58) * mm});
            skLineSegment(sketch, "E3623", {"start": v(362.85, -514.58) * mm, "end": v(362.34, -513.16) * mm});
            skLineSegment(sketch, "E3624", {"start": v(362.34, -513.16) * mm, "end": v(361.79, -511.73) * mm});
            skLineSegment(sketch, "E3625", {"start": v(361.79, -511.73) * mm, "end": v(361.2, -510.3) * mm});
            skLineSegment(sketch, "E3626", {"start": v(361.2, -510.3) * mm, "end": v(360.56, -508.86) * mm});
            skLineSegment(sketch, "E3627", {"start": v(360.56, -508.86) * mm, "end": v(359.9, -507.42) * mm});
            skLineSegment(sketch, "E3628", {"start": v(359.9, -507.42) * mm, "end": v(359.24, -505.98) * mm});
            skLineSegment(sketch, "E3629", {"start": v(359.24, -505.98) * mm, "end": v(358.56, -504.54) * mm});
            skLineSegment(sketch, "E3630", {"start": v(358.56, -504.54) * mm, "end": v(357.88, -503.1) * mm});
            skLineSegment(sketch, "E3631", {"start": v(357.88, -503.1) * mm, "end": v(357.2, -501.67) * mm});
            skLineSegment(sketch, "E3632", {"start": v(357.2, -501.67) * mm, "end": v(356.53, -500.24) * mm});
            skLineSegment(sketch, "E3633", {"start": v(356.53, -500.24) * mm, "end": v(355.89, -498.82) * mm});
            skLineSegment(sketch, "E3634", {"start": v(355.89, -498.82) * mm, "end": v(355.27, -497.41) * mm});
            skLineSegment(sketch, "E3635", {"start": v(355.27, -497.41) * mm, "end": v(354.57, -495.7) * mm});
            skLineSegment(sketch, "E3636", {"start": v(354.57, -495.7) * mm, "end": v(353.93, -494) * mm});
            skLineSegment(sketch, "E3637", {"start": v(353.93, -494) * mm, "end": v(353.35, -492.29) * mm});
            skLineSegment(sketch, "E3638", {"start": v(353.35, -492.29) * mm, "end": v(352.84, -490.6) * mm});
            skLineSegment(sketch, "E3639", {"start": v(352.84, -490.6) * mm, "end": v(352.39, -488.9) * mm});
            skLineSegment(sketch, "E3640", {"start": v(352.39, -488.9) * mm, "end": v(352, -487.22) * mm});
            skLineSegment(sketch, "E3641", {"start": v(352, -487.22) * mm, "end": v(351.7, -485.55) * mm});
            skLineSegment(sketch, "E3642", {"start": v(351.7, -485.55) * mm, "end": v(351.46, -483.89) * mm});
            skLineSegment(sketch, "E3643", {"start": v(351.46, -483.89) * mm, "end": v(351.28, -482.23) * mm});
            skLineSegment(sketch, "E3644", {"start": v(351.28, -482.23) * mm, "end": v(351.18, -480.6) * mm});
            skLineSegment(sketch, "E3645", {"start": v(351.18, -480.6) * mm, "end": v(351.16, -478.97) * mm});
            skLineSegment(sketch, "E3646", {"start": v(351.16, -478.97) * mm, "end": v(351.2, -477.35) * mm});
            skLineSegment(sketch, "E3647", {"start": v(351.2, -477.35) * mm, "end": v(351.33, -475.75) * mm});
            skLineSegment(sketch, "E3648", {"start": v(351.33, -475.75) * mm, "end": v(351.53, -474.17) * mm});
            skLineSegment(sketch, "E3649", {"start": v(351.53, -474.17) * mm, "end": v(351.8, -472.6) * mm});
            skLineSegment(sketch, "E3650", {"start": v(351.8, -472.6) * mm, "end": v(352.16, -471.05) * mm});
            skLineSegment(sketch, "E3651", {"start": v(352.16, -471.05) * mm, "end": v(352.6, -469.51) * mm});
            skLineSegment(sketch, "E3652", {"start": v(352.6, -469.51) * mm, "end": v(353.12, -468) * mm});
            skLineSegment(sketch, "E3653", {"start": v(353.12, -468) * mm, "end": v(353.72, -466.5) * mm});
            skLineSegment(sketch, "E3654", {"start": v(353.72, -466.5) * mm, "end": v(354.4, -465.03) * mm});
            skLineSegment(sketch, "E3655", {"start": v(354.4, -465.03) * mm, "end": v(355.18, -463.58) * mm});
            skLineSegment(sketch, "E3656", {"start": v(355.18, -463.58) * mm, "end": v(356.04, -462.15) * mm});
            skLineSegment(sketch, "E3657", {"start": v(356.04, -462.15) * mm, "end": v(356.99, -460.75) * mm});
            skLineSegment(sketch, "E3658", {"start": v(356.99, -460.75) * mm, "end": v(358.02, -459.37) * mm});
            skLineSegment(sketch, "E3659", {"start": v(358.02, -459.37) * mm, "end": v(359.15, -458.01) * mm});
            skLineSegment(sketch, "E3660", {"start": v(359.15, -458.01) * mm, "end": v(360.37, -456.69) * mm});
            skLineSegment(sketch, "E3661", {"start": v(360.37, -456.69) * mm, "end": v(361.68, -455.38) * mm});
            skLineSegment(sketch, "E3662", {"start": v(361.68, -455.38) * mm, "end": v(363.08, -454.11) * mm});
            skLineSegment(sketch, "E3663", {"start": v(363.08, -454.11) * mm, "end": v(364.58, -452.87) * mm});
            skLineSegment(sketch, "E3664", {"start": v(364.58, -452.87) * mm, "end": v(365.84, -451.9) * mm});
            skLineSegment(sketch, "E3665", {"start": v(365.84, -451.9) * mm, "end": v(367.1, -451.04) * mm});
            skLineSegment(sketch, "E3666", {"start": v(367.1, -451.04) * mm, "end": v(368.34, -450.25) * mm});
            skLineSegment(sketch, "E3667", {"start": v(368.34, -450.25) * mm, "end": v(369.59, -449.55) * mm});
            skLineSegment(sketch, "E3668", {"start": v(369.59, -449.55) * mm, "end": v(370.82, -448.92) * mm});
            skLineSegment(sketch, "E3669", {"start": v(370.82, -448.92) * mm, "end": v(372.05, -448.38) * mm});
            skLineSegment(sketch, "E3670", {"start": v(372.05, -448.38) * mm, "end": v(373.28, -447.91) * mm});
            skLineSegment(sketch, "E3671", {"start": v(373.28, -447.91) * mm, "end": v(374.5, -447.52) * mm});
            skLineSegment(sketch, "E3672", {"start": v(374.5, -447.52) * mm, "end": v(375.7, -447.2) * mm});
            skLineSegment(sketch, "E3673", {"start": v(375.7, -447.2) * mm, "end": v(376.92, -446.94) * mm});
            skLineSegment(sketch, "E3674", {"start": v(376.92, -446.94) * mm, "end": v(378.12, -446.75) * mm});
            skLineSegment(sketch, "E3675", {"start": v(378.12, -446.75) * mm, "end": v(379.31, -446.62) * mm});
            skLineSegment(sketch, "E3676", {"start": v(379.31, -446.62) * mm, "end": v(380.5, -446.56) * mm});
            skLineSegment(sketch, "E3677", {"start": v(380.5, -446.56) * mm, "end": v(381.69, -446.56) * mm});
            skLineSegment(sketch, "E3678", {"start": v(381.69, -446.56) * mm, "end": v(382.87, -446.61) * mm});
            skLineSegment(sketch, "E3679", {"start": v(382.87, -446.61) * mm, "end": v(384.04, -446.72) * mm});
            skLineSegment(sketch, "E3680", {"start": v(384.04, -446.72) * mm, "end": v(385.21, -446.88) * mm});
            skLineSegment(sketch, "E3681", {"start": v(385.21, -446.88) * mm, "end": v(386.38, -447.09) * mm});
            skLineSegment(sketch, "E3682", {"start": v(386.38, -447.09) * mm, "end": v(387.54, -447.34) * mm});
            skLineSegment(sketch, "E3683", {"start": v(387.54, -447.34) * mm, "end": v(388.7, -447.64) * mm});
            skLineSegment(sketch, "E3684", {"start": v(388.7, -447.64) * mm, "end": v(389.84, -447.99) * mm});
            skLineSegment(sketch, "E3685", {"start": v(389.84, -447.99) * mm, "end": v(390.99, -448.37) * mm});
            skLineSegment(sketch, "E3686", {"start": v(390.99, -448.37) * mm, "end": v(392.13, -448.8) * mm});
            skLineSegment(sketch, "E3687", {"start": v(392.13, -448.8) * mm, "end": v(393.26, -449.25) * mm});
            skLineSegment(sketch, "E3688", {"start": v(393.26, -449.25) * mm, "end": v(394.4, -449.74) * mm});
            skLineSegment(sketch, "E3689", {"start": v(394.4, -449.74) * mm, "end": v(395.52, -450.26) * mm});
            skLineSegment(sketch, "E3690", {"start": v(395.52, -450.26) * mm, "end": v(396.64, -450.81) * mm});
            skLineSegment(sketch, "E3691", {"start": v(396.64, -450.81) * mm, "end": v(397.76, -451.39) * mm});
            skLineSegment(sketch, "E3692", {"start": v(397.76, -451.39) * mm, "end": v(398.87, -451.98) * mm});
            skLineSegment(sketch, "E3693", {"start": v(398.87, -451.98) * mm, "end": v(399.98, -452.6) * mm});
            skLineSegment(sketch, "E3694", {"start": v(399.98, -452.6) * mm, "end": v(401.09, -453.24) * mm});
            skLineSegment(sketch, "E3695", {"start": v(401.09, -453.24) * mm, "end": v(402.2, -453.9) * mm});
            skLineSegment(sketch, "E3696", {"start": v(402.2, -453.9) * mm, "end": v(403.29, -454.56) * mm});
            skLineSegment(sketch, "E3697", {"start": v(403.29, -454.56) * mm, "end": v(404.38, -455.24) * mm});
            skLineSegment(sketch, "E3698", {"start": v(404.38, -455.24) * mm, "end": v(405.47, -455.93) * mm});
            skLineSegment(sketch, "E3699", {"start": v(405.47, -455.93) * mm, "end": v(406.56, -456.62) * mm});
            skLineSegment(sketch, "E3700", {"start": v(406.56, -456.62) * mm, "end": v(407.64, -457.32) * mm});
            skLineSegment(sketch, "E3701", {"start": v(407.64, -457.32) * mm, "end": v(408.72, -458.02) * mm});
            skLineSegment(sketch, "E3702", {"start": v(408.72, -458.02) * mm, "end": v(409.8, -458.73) * mm});
            skLineSegment(sketch, "E3703", {"start": v(409.8, -458.73) * mm, "end": v(410.87, -459.42) * mm});
            skLineSegment(sketch, "E3704", {"start": v(410.87, -459.42) * mm, "end": v(411.94, -460.12) * mm});
            skLineSegment(sketch, "E3705", {"start": v(411.94, -460.12) * mm, "end": v(413, -460.8) * mm});
            skLineSegment(sketch, "E3706", {"start": v(413, -460.8) * mm, "end": v(414.07, -461.48) * mm});
            skLineSegment(sketch, "E3707", {"start": v(414.07, -461.48) * mm, "end": v(415.13, -462.14) * mm});
            skLineSegment(sketch, "E3708", {"start": v(415.13, -462.14) * mm, "end": v(416.2, -462.79) * mm});
            skLineSegment(sketch, "E3709", {"start": v(416.2, -462.79) * mm, "end": v(417.25, -463.42) * mm});
            skLineSegment(sketch, "E3710", {"start": v(417.25, -463.42) * mm, "end": v(418.3, -464.03) * mm});
            skLineSegment(sketch, "E3711", {"start": v(418.3, -464.03) * mm, "end": v(419.35, -464.62) * mm});
            skLineSegment(sketch, "E3712", {"start": v(419.35, -464.62) * mm, "end": v(420.4, -465.18) * mm});
            skLineSegment(sketch, "E3713", {"start": v(420.4, -465.18) * mm, "end": v(421.44, -465.72) * mm});
            skLineSegment(sketch, "E3714", {"start": v(421.44, -465.72) * mm, "end": v(422.48, -466.23) * mm});
            skLineSegment(sketch, "E3715", {"start": v(422.48, -466.23) * mm, "end": v(423.52, -466.7) * mm});
            skLineSegment(sketch, "E3716", {"start": v(423.52, -466.7) * mm, "end": v(424.56, -467.15) * mm});
            skLineSegment(sketch, "E3717", {"start": v(424.56, -467.15) * mm, "end": v(425.6, -467.56) * mm});
            skLineSegment(sketch, "E3718", {"start": v(425.6, -467.56) * mm, "end": v(426.63, -467.93) * mm});
            skLineSegment(sketch, "E3719", {"start": v(426.63, -467.93) * mm, "end": v(427.66, -468.25) * mm});
            skLineSegment(sketch, "E3720", {"start": v(427.66, -468.25) * mm, "end": v(428.7, -468.54) * mm});
            skLineSegment(sketch, "E3721", {"start": v(428.7, -468.54) * mm, "end": v(429.72, -468.78) * mm});
            skLineSegment(sketch, "E3722", {"start": v(429.72, -468.78) * mm, "end": v(430.75, -468.97) * mm});
            skLineSegment(sketch, "E3723", {"start": v(430.75, -468.97) * mm, "end": v(431.77, -469.1) * mm});
            skLineSegment(sketch, "E3724", {"start": v(431.77, -469.1) * mm, "end": v(432.8, -469.2) * mm});
            skLineSegment(sketch, "E3725", {"start": v(432.8, -469.2) * mm, "end": v(433.81, -469.22) * mm});
            skLineSegment(sketch, "E3726", {"start": v(433.81, -469.22) * mm, "end": v(434.83, -469.2) * mm});
            skLineSegment(sketch, "E3727", {"start": v(434.83, -469.2) * mm, "end": v(435.85, -469.11) * mm});
            skLineSegment(sketch, "E3728", {"start": v(435.85, -469.11) * mm, "end": v(436.87, -468.96) * mm});
            skLineSegment(sketch, "E3729", {"start": v(436.87, -468.96) * mm, "end": v(437.89, -468.75) * mm});
            skLineSegment(sketch, "E3730", {"start": v(437.89, -468.75) * mm, "end": v(438.9, -468.47) * mm});
            skLineSegment(sketch, "E3731", {"start": v(438.9, -468.47) * mm, "end": v(439.91, -468.12) * mm});
            skLineSegment(sketch, "E3732", {"start": v(439.91, -468.12) * mm, "end": v(440.93, -467.7) * mm});
            skLineSegment(sketch, "E3733", {"start": v(440.93, -467.7) * mm, "end": v(441.94, -467.2) * mm});
            skLineSegment(sketch, "E3734", {"start": v(441.94, -467.2) * mm, "end": v(442.95, -466.62) * mm});
            skLineSegment(sketch, "E3735", {"start": v(442.95, -466.62) * mm, "end": v(443.96, -465.97) * mm});
            skLineSegment(sketch, "E3736", {"start": v(443.96, -465.97) * mm, "end": v(444.97, -465.23) * mm});
            skLineSegment(sketch, "E3737", {"start": v(444.97, -465.23) * mm, "end": v(445.98, -464.41) * mm});
            skLineSegment(sketch, "E3738", {"start": v(445.98, -464.41) * mm, "end": v(446.98, -463.52) * mm});
            skLineSegment(sketch, "E3739", {"start": v(446.98, -463.52) * mm, "end": v(447.9, -462.63) * mm});
            skLineSegment(sketch, "E3740", {"start": v(447.9, -462.63) * mm, "end": v(448.74, -461.72) * mm});
            skLineSegment(sketch, "E3741", {"start": v(448.74, -461.72) * mm, "end": v(449.5, -460.82) * mm});
            skLineSegment(sketch, "E3742", {"start": v(449.5, -460.82) * mm, "end": v(450.19, -459.9) * mm});
            skLineSegment(sketch, "E3743", {"start": v(450.19, -459.9) * mm, "end": v(450.8, -458.99) * mm});
            skLineSegment(sketch, "E3744", {"start": v(450.8, -458.99) * mm, "end": v(451.35, -458.06) * mm});
            skLineSegment(sketch, "E3745", {"start": v(451.35, -458.06) * mm, "end": v(451.83, -457.13) * mm});
            skLineSegment(sketch, "E3746", {"start": v(451.83, -457.13) * mm, "end": v(452.24, -456.2) * mm});
            skLineSegment(sketch, "E3747", {"start": v(452.24, -456.2) * mm, "end": v(452.58, -455.26) * mm});
            skLineSegment(sketch, "E3748", {"start": v(452.58, -455.26) * mm, "end": v(452.87, -454.32) * mm});
            skLineSegment(sketch, "E3749", {"start": v(452.87, -454.32) * mm, "end": v(453.1, -453.37) * mm});
            skLineSegment(sketch, "E3750", {"start": v(453.1, -453.37) * mm, "end": v(453.26, -452.41) * mm});
            skLineSegment(sketch, "E3751", {"start": v(453.26, -452.41) * mm, "end": v(453.37, -451.46) * mm});
            skLineSegment(sketch, "E3752", {"start": v(453.37, -451.46) * mm, "end": v(453.43, -450.5) * mm});
            skLineSegment(sketch, "E3753", {"start": v(453.43, -450.5) * mm, "end": v(453.43, -449.52) * mm});
            skLineSegment(sketch, "E3754", {"start": v(453.43, -449.52) * mm, "end": v(453.39, -448.55) * mm});
            skLineSegment(sketch, "E3755", {"start": v(453.39, -448.55) * mm, "end": v(453.3, -447.57) * mm});
            skLineSegment(sketch, "E3756", {"start": v(453.3, -447.57) * mm, "end": v(453.16, -446.6) * mm});
            skLineSegment(sketch, "E3757", {"start": v(453.16, -446.6) * mm, "end": v(452.98, -445.6) * mm});
            skLineSegment(sketch, "E3758", {"start": v(452.98, -445.6) * mm, "end": v(452.76, -444.61) * mm});
            skLineSegment(sketch, "E3759", {"start": v(452.76, -444.61) * mm, "end": v(452.5, -443.62) * mm});
            skLineSegment(sketch, "E3760", {"start": v(452.5, -443.62) * mm, "end": v(452.2, -442.61) * mm});
            skLineSegment(sketch, "E3761", {"start": v(452.2, -442.61) * mm, "end": v(451.87, -441.6) * mm});
            skLineSegment(sketch, "E3762", {"start": v(451.87, -441.6) * mm, "end": v(451.5, -440.6) * mm});
            skLineSegment(sketch, "E3763", {"start": v(451.5, -440.6) * mm, "end": v(451.1, -439.59) * mm});
            skLineSegment(sketch, "E3764", {"start": v(451.1, -439.59) * mm, "end": v(450.67, -438.57) * mm});
            skLineSegment(sketch, "E3765", {"start": v(450.67, -438.57) * mm, "end": v(450.22, -437.55) * mm});
            skLineSegment(sketch, "E3766", {"start": v(450.22, -437.55) * mm, "end": v(449.74, -436.52) * mm});
            skLineSegment(sketch, "E3767", {"start": v(449.74, -436.52) * mm, "end": v(449.24, -435.49) * mm});
            skLineSegment(sketch, "E3768", {"start": v(449.24, -435.49) * mm, "end": v(448.72, -434.45) * mm});
            skLineSegment(sketch, "E3769", {"start": v(448.72, -434.45) * mm, "end": v(448.18, -433.42) * mm});
            skLineSegment(sketch, "E3770", {"start": v(448.18, -433.42) * mm, "end": v(447.62, -432.37) * mm});
            skLineSegment(sketch, "E3771", {"start": v(447.62, -432.37) * mm, "end": v(447.05, -431.33) * mm});
            skLineSegment(sketch, "E3772", {"start": v(447.05, -431.33) * mm, "end": v(446.47, -430.28) * mm});
            skLineSegment(sketch, "E3773", {"start": v(446.47, -430.28) * mm, "end": v(445.88, -429.22) * mm});
            skLineSegment(sketch, "E3774", {"start": v(445.88, -429.22) * mm, "end": v(445.27, -428.16) * mm});
            skLineSegment(sketch, "E3775", {"start": v(445.27, -428.16) * mm, "end": v(444.67, -427.1) * mm});
            skLineSegment(sketch, "E3776", {"start": v(444.67, -427.1) * mm, "end": v(444.05, -426.04) * mm});
            skLineSegment(sketch, "E3777", {"start": v(444.05, -426.04) * mm, "end": v(443.44, -424.97) * mm});
            skLineSegment(sketch, "E3778", {"start": v(443.44, -424.97) * mm, "end": v(442.82, -423.9) * mm});
            skLineSegment(sketch, "E3779", {"start": v(442.82, -423.9) * mm, "end": v(442.21, -422.82) * mm});
            skLineSegment(sketch, "E3780", {"start": v(442.21, -422.82) * mm, "end": v(441.6, -421.74) * mm});
            skLineSegment(sketch, "E3781", {"start": v(441.6, -421.74) * mm, "end": v(441, -420.66) * mm});
            skLineSegment(sketch, "E3782", {"start": v(441, -420.66) * mm, "end": v(440.4, -419.57) * mm});
            skLineSegment(sketch, "E3783", {"start": v(440.4, -419.57) * mm, "end": v(439.83, -418.48) * mm});
            skLineSegment(sketch, "E3784", {"start": v(439.83, -418.48) * mm, "end": v(439.26, -417.39) * mm});
            skLineSegment(sketch, "E3785", {"start": v(439.26, -417.39) * mm, "end": v(438.7, -416.3) * mm});
            skLineSegment(sketch, "E3786", {"start": v(438.7, -416.3) * mm, "end": v(438.16, -415.2) * mm});
            skLineSegment(sketch, "E3787", {"start": v(438.16, -415.2) * mm, "end": v(437.64, -414.1) * mm});
            skLineSegment(sketch, "E3788", {"start": v(437.64, -414.1) * mm, "end": v(437.14, -412.98) * mm});
            skLineSegment(sketch, "E3789", {"start": v(437.14, -412.98) * mm, "end": v(436.66, -411.88) * mm});
            skLineSegment(sketch, "E3790", {"start": v(436.66, -411.88) * mm, "end": v(436.21, -410.76) * mm});
            skLineSegment(sketch, "E3791", {"start": v(436.21, -410.76) * mm, "end": v(435.79, -409.65) * mm});
            skLineSegment(sketch, "E3792", {"start": v(435.79, -409.65) * mm, "end": v(435.39, -408.53) * mm});
            skLineSegment(sketch, "E3793", {"start": v(435.39, -408.53) * mm, "end": v(435.02, -407.41) * mm});
            skLineSegment(sketch, "E3794", {"start": v(435.02, -407.41) * mm, "end": v(434.7, -406.3) * mm});
            skLineSegment(sketch, "E3795", {"start": v(434.7, -406.3) * mm, "end": v(434.4, -405.16) * mm});
            skLineSegment(sketch, "E3796", {"start": v(434.4, -405.16) * mm, "end": v(434.14, -404.04) * mm});
            skLineSegment(sketch, "E3797", {"start": v(434.14, -404.04) * mm, "end": v(433.92, -402.9) * mm});
            skLineSegment(sketch, "E3798", {"start": v(433.92, -402.9) * mm, "end": v(433.74, -401.77) * mm});
            skLineSegment(sketch, "E3799", {"start": v(433.74, -401.77) * mm, "end": v(433.6, -400.64) * mm});
            skLineSegment(sketch, "E3800", {"start": v(433.6, -400.64) * mm, "end": v(433.51, -399.5) * mm});
            skLineSegment(sketch, "E3801", {"start": v(433.51, -399.5) * mm, "end": v(433.47, -398.36) * mm});
            skLineSegment(sketch, "E3802", {"start": v(433.47, -398.36) * mm, "end": v(433.48, -397.21) * mm});
            skLineSegment(sketch, "E3803", {"start": v(433.48, -397.21) * mm, "end": v(433.54, -396.07) * mm});
            skLineSegment(sketch, "E3804", {"start": v(433.54, -396.07) * mm, "end": v(433.65, -394.92) * mm});
            skLineSegment(sketch, "E3805", {"start": v(433.65, -394.92) * mm, "end": v(433.82, -393.77) * mm});
            skLineSegment(sketch, "E3806", {"start": v(433.82, -393.77) * mm, "end": v(434.05, -392.62) * mm});
            skLineSegment(sketch, "E3807", {"start": v(434.05, -392.62) * mm, "end": v(434.34, -391.46) * mm});
            skLineSegment(sketch, "E3808", {"start": v(434.34, -391.46) * mm, "end": v(434.69, -390.3) * mm});
            skLineSegment(sketch, "E3809", {"start": v(434.69, -390.3) * mm, "end": v(435.1, -389.15) * mm});
            skLineSegment(sketch, "E3810", {"start": v(435.1, -389.15) * mm, "end": v(435.58, -387.99) * mm});
            skLineSegment(sketch, "E3811", {"start": v(435.58, -387.99) * mm, "end": v(436.13, -386.83) * mm});
            skLineSegment(sketch, "E3812", {"start": v(436.13, -386.83) * mm, "end": v(436.75, -385.66) * mm});
            skLineSegment(sketch, "E3813", {"start": v(436.75, -385.66) * mm, "end": v(437.44, -384.5) * mm});
            skLineSegment(sketch, "E3814", {"start": v(437.44, -384.5) * mm, "end": v(438.2, -383.33) * mm});
            skLineSegment(sketch, "E3815", {"start": v(438.2, -383.33) * mm, "end": v(439.05, -382.16) * mm});
            skLineSegment(sketch, "E3816", {"start": v(439.05, -382.16) * mm, "end": v(439.97, -380.99) * mm});
            skLineSegment(sketch, "E3817", {"start": v(439.97, -380.99) * mm, "end": v(440.97, -379.81) * mm});
            skLineSegment(sketch, "E3818", {"start": v(440.97, -379.81) * mm, "end": v(442.3, -378.39) * mm});
            skLineSegment(sketch, "E3819", {"start": v(442.3, -378.39) * mm, "end": v(443.64, -377.06) * mm});
            skLineSegment(sketch, "E3820", {"start": v(443.64, -377.06) * mm, "end": v(445.01, -375.82) * mm});
            skLineSegment(sketch, "E3821", {"start": v(445.01, -375.82) * mm, "end": v(446.4, -374.69) * mm});
            skLineSegment(sketch, "E3822", {"start": v(446.4, -374.69) * mm, "end": v(447.82, -373.65) * mm});
            skLineSegment(sketch, "E3823", {"start": v(447.82, -373.65) * mm, "end": v(449.25, -372.7) * mm});
            skLineSegment(sketch, "E3824", {"start": v(449.25, -372.7) * mm, "end": v(450.7, -371.84) * mm});
            skLineSegment(sketch, "E3825", {"start": v(450.7, -371.84) * mm, "end": v(452.16, -371.08) * mm});
            skLineSegment(sketch, "E3826", {"start": v(452.16, -371.08) * mm, "end": v(453.65, -370.4) * mm});
            skLineSegment(sketch, "E3827", {"start": v(453.65, -370.4) * mm, "end": v(455.15, -369.81) * mm});
            skLineSegment(sketch, "E3828", {"start": v(455.15, -369.81) * mm, "end": v(456.67, -369.3) * mm});
            skLineSegment(sketch, "E3829", {"start": v(456.67, -369.3) * mm, "end": v(458.2, -368.9) * mm});
            skLineSegment(sketch, "E3830", {"start": v(458.2, -368.9) * mm, "end": v(459.75, -368.56) * mm});
            skLineSegment(sketch, "E3831", {"start": v(459.75, -368.56) * mm, "end": v(461.3, -368.3) * mm});
            skLineSegment(sketch, "E3832", {"start": v(461.3, -368.3) * mm, "end": v(462.88, -368.13) * mm});
            skLineSegment(sketch, "E3833", {"start": v(462.88, -368.13) * mm, "end": v(464.47, -368.04) * mm});
            skLineSegment(sketch, "E3834", {"start": v(464.47, -368.04) * mm, "end": v(466.06, -368.02) * mm});
            skLineSegment(sketch, "E3835", {"start": v(466.06, -368.02) * mm, "end": v(467.67, -368.08) * mm});
            skLineSegment(sketch, "E3836", {"start": v(467.67, -368.08) * mm, "end": v(469.29, -368.21) * mm});
            skLineSegment(sketch, "E3837", {"start": v(469.29, -368.21) * mm, "end": v(470.92, -368.42) * mm});
            skLineSegment(sketch, "E3838", {"start": v(470.92, -368.42) * mm, "end": v(472.55, -368.7) * mm});
            skLineSegment(sketch, "E3839", {"start": v(472.55, -368.7) * mm, "end": v(474.2, -369.05) * mm});
            skLineSegment(sketch, "E3840", {"start": v(474.2, -369.05) * mm, "end": v(475.84, -369.47) * mm});
            skLineSegment(sketch, "E3841", {"start": v(475.84, -369.47) * mm, "end": v(477.5, -369.96) * mm});
            skLineSegment(sketch, "E3842", {"start": v(477.5, -369.96) * mm, "end": v(479.16, -370.51) * mm});
            skLineSegment(sketch, "E3843", {"start": v(479.16, -370.51) * mm, "end": v(480.82, -371.13) * mm});
            skLineSegment(sketch, "E3844", {"start": v(480.82, -371.13) * mm, "end": v(482.5, -371.82) * mm});
            skLineSegment(sketch, "E3845", {"start": v(482.5, -371.82) * mm, "end": v(484.17, -372.56) * mm});
            skLineSegment(sketch, "E3846", {"start": v(484.17, -372.56) * mm, "end": v(485.84, -373.36) * mm});
            skLineSegment(sketch, "E3847", {"start": v(485.84, -373.36) * mm, "end": v(487.15, -374.02) * mm});
            skLineSegment(sketch, "E3848", {"start": v(487.15, -374.02) * mm, "end": v(488.5, -374.72) * mm});
            skLineSegment(sketch, "E3849", {"start": v(488.5, -374.72) * mm, "end": v(489.88, -375.44) * mm});
            skLineSegment(sketch, "E3850", {"start": v(489.88, -375.44) * mm, "end": v(491.3, -376.18) * mm});
            skLineSegment(sketch, "E3851", {"start": v(491.3, -376.18) * mm, "end": v(492.76, -376.93) * mm});
            skLineSegment(sketch, "E3852", {"start": v(492.76, -376.93) * mm, "end": v(494.25, -377.67) * mm});
            skLineSegment(sketch, "E3853", {"start": v(494.25, -377.67) * mm, "end": v(495.76, -378.4) * mm});
            skLineSegment(sketch, "E3854", {"start": v(495.76, -378.4) * mm, "end": v(497.28, -379.1) * mm});
            skLineSegment(sketch, "E3855", {"start": v(497.28, -379.1) * mm, "end": v(498.82, -379.77) * mm});
            skLineSegment(sketch, "E3856", {"start": v(498.82, -379.77) * mm, "end": v(500.38, -380.4) * mm});
            skLineSegment(sketch, "E3857", {"start": v(500.38, -380.4) * mm, "end": v(501.94, -380.97) * mm});
            skLineSegment(sketch, "E3858", {"start": v(501.94, -380.97) * mm, "end": v(503.5, -381.48) * mm});
            skLineSegment(sketch, "E3859", {"start": v(503.5, -381.48) * mm, "end": v(505.06, -381.91) * mm});
            skLineSegment(sketch, "E3860", {"start": v(505.06, -381.91) * mm, "end": v(506.62, -382.26) * mm});
            skLineSegment(sketch, "E3861", {"start": v(506.62, -382.26) * mm, "end": v(508.17, -382.52) * mm});
            skLineSegment(sketch, "E3862", {"start": v(508.17, -382.52) * mm, "end": v(509.7, -382.67) * mm});
            skLineSegment(sketch, "E3863", {"start": v(509.7, -382.67) * mm, "end": v(511.22, -382.7) * mm});
            skLineSegment(sketch, "E3864", {"start": v(511.22, -382.7) * mm, "end": v(512.71, -382.62) * mm});
            skLineSegment(sketch, "E3865", {"start": v(512.71, -382.62) * mm, "end": v(514.18, -382.4) * mm});
            skLineSegment(sketch, "E3866", {"start": v(514.18, -382.4) * mm, "end": v(515.62, -382.03) * mm});
            skLineSegment(sketch, "E3867", {"start": v(515.62, -382.03) * mm, "end": v(517.03, -381.5) * mm});
            skLineSegment(sketch, "E3868", {"start": v(517.03, -381.5) * mm, "end": v(518.4, -380.82) * mm});
            skLineSegment(sketch, "E3869", {"start": v(518.4, -380.82) * mm, "end": v(519.72, -379.95) * mm});
            skLineSegment(sketch, "E3870", {"start": v(519.72, -379.95) * mm, "end": v(521, -378.9) * mm});
            skLineSegment(sketch, "E3871", {"start": v(521, -378.9) * mm, "end": v(522.23, -377.66) * mm});
            skLineSegment(sketch, "E3872", {"start": v(522.23, -377.66) * mm, "end": v(523.13, -376.62) * mm});
            skLineSegment(sketch, "E3873", {"start": v(523.13, -376.62) * mm, "end": v(523.95, -375.6) * mm});
            skLineSegment(sketch, "E3874", {"start": v(523.95, -375.6) * mm, "end": v(524.7, -374.57) * mm});
            skLineSegment(sketch, "E3875", {"start": v(524.7, -374.57) * mm, "end": v(525.38, -373.56) * mm});
            skLineSegment(sketch, "E3876", {"start": v(525.38, -373.56) * mm, "end": v(525.99, -372.55) * mm});
            skLineSegment(sketch, "E3877", {"start": v(525.99, -372.55) * mm, "end": v(526.53, -371.55) * mm});
            skLineSegment(sketch, "E3878", {"start": v(526.53, -371.55) * mm, "end": v(527, -370.57) * mm});
            skLineSegment(sketch, "E3879", {"start": v(527, -370.57) * mm, "end": v(527.41, -369.58) * mm});
            skLineSegment(sketch, "E3880", {"start": v(527.41, -369.58) * mm, "end": v(527.76, -368.6) * mm});
            skLineSegment(sketch, "E3881", {"start": v(527.76, -368.6) * mm, "end": v(528.05, -367.64) * mm});
            skLineSegment(sketch, "E3882", {"start": v(528.05, -367.64) * mm, "end": v(528.28, -366.68) * mm});
            skLineSegment(sketch, "E3883", {"start": v(528.28, -366.68) * mm, "end": v(528.45, -365.72) * mm});
            skLineSegment(sketch, "E3884", {"start": v(528.45, -365.72) * mm, "end": v(528.56, -364.77) * mm});
            skLineSegment(sketch, "E3885", {"start": v(528.56, -364.77) * mm, "end": v(528.62, -363.83) * mm});
            skLineSegment(sketch, "E3886", {"start": v(528.62, -363.83) * mm, "end": v(528.63, -362.9) * mm});
            skLineSegment(sketch, "E3887", {"start": v(528.63, -362.9) * mm, "end": v(528.59, -361.96) * mm});
            skLineSegment(sketch, "E3888", {"start": v(528.59, -361.96) * mm, "end": v(528.5, -361.03) * mm});
            skLineSegment(sketch, "E3889", {"start": v(528.5, -361.03) * mm, "end": v(528.36, -360.1) * mm});
            skLineSegment(sketch, "E3890", {"start": v(528.36, -360.1) * mm, "end": v(528.18, -359.19) * mm});
            skLineSegment(sketch, "E3891", {"start": v(528.18, -359.19) * mm, "end": v(527.95, -358.27) * mm});
            skLineSegment(sketch, "E3892", {"start": v(527.95, -358.27) * mm, "end": v(527.68, -357.36) * mm});
            skLineSegment(sketch, "E3893", {"start": v(527.68, -357.36) * mm, "end": v(527.37, -356.46) * mm});
            skLineSegment(sketch, "E3894", {"start": v(527.37, -356.46) * mm, "end": v(527.03, -355.55) * mm});
            skLineSegment(sketch, "E3895", {"start": v(527.03, -355.55) * mm, "end": v(526.64, -354.65) * mm});
            skLineSegment(sketch, "E3896", {"start": v(526.64, -354.65) * mm, "end": v(526.22, -353.75) * mm});
            skLineSegment(sketch, "E3897", {"start": v(526.22, -353.75) * mm, "end": v(525.77, -352.86) * mm});
            skLineSegment(sketch, "E3898", {"start": v(525.77, -352.86) * mm, "end": v(525.28, -351.97) * mm});
            skLineSegment(sketch, "E3899", {"start": v(525.28, -351.97) * mm, "end": v(524.77, -351.07) * mm});
            skLineSegment(sketch, "E3900", {"start": v(524.77, -351.07) * mm, "end": v(524.22, -350.18) * mm});
            skLineSegment(sketch, "E3901", {"start": v(524.22, -350.18) * mm, "end": v(523.65, -349.3) * mm});
            skLineSegment(sketch, "E3902", {"start": v(523.65, -349.3) * mm, "end": v(523.06, -348.41) * mm});
            skLineSegment(sketch, "E3903", {"start": v(523.06, -348.41) * mm, "end": v(522.44, -347.52) * mm});
            skLineSegment(sketch, "E3904", {"start": v(522.44, -347.52) * mm, "end": v(521.8, -346.64) * mm});
            skLineSegment(sketch, "E3905", {"start": v(521.8, -346.64) * mm, "end": v(521.14, -345.75) * mm});
            skLineSegment(sketch, "E3906", {"start": v(521.14, -345.75) * mm, "end": v(520.46, -344.87) * mm});
            skLineSegment(sketch, "E3907", {"start": v(520.46, -344.87) * mm, "end": v(519.77, -343.98) * mm});
            skLineSegment(sketch, "E3908", {"start": v(519.77, -343.98) * mm, "end": v(519.06, -343.1) * mm});
            skLineSegment(sketch, "E3909", {"start": v(519.06, -343.1) * mm, "end": v(518.34, -342.21) * mm});
            skLineSegment(sketch, "E3910", {"start": v(518.34, -342.21) * mm, "end": v(517.6, -341.33) * mm});
            skLineSegment(sketch, "E3911", {"start": v(517.6, -341.33) * mm, "end": v(516.87, -340.44) * mm});
            skLineSegment(sketch, "E3912", {"start": v(516.87, -340.44) * mm, "end": v(516.12, -339.55) * mm});
            skLineSegment(sketch, "E3913", {"start": v(516.12, -339.55) * mm, "end": v(515.36, -338.66) * mm});
            skLineSegment(sketch, "E3914", {"start": v(515.36, -338.66) * mm, "end": v(514.6, -337.76) * mm});
            skLineSegment(sketch, "E3915", {"start": v(514.6, -337.76) * mm, "end": v(513.84, -336.87) * mm});
            skLineSegment(sketch, "E3916", {"start": v(513.84, -336.87) * mm, "end": v(513.08, -335.97) * mm});
            skLineSegment(sketch, "E3917", {"start": v(513.08, -335.97) * mm, "end": v(512.31, -335.07) * mm});
            skLineSegment(sketch, "E3918", {"start": v(512.31, -335.07) * mm, "end": v(511.55, -334.16) * mm});
            skLineSegment(sketch, "E3919", {"start": v(511.55, -334.16) * mm, "end": v(510.8, -333.25) * mm});
            skLineSegment(sketch, "E3920", {"start": v(510.8, -333.25) * mm, "end": v(510.05, -332.34) * mm});
            skLineSegment(sketch, "E3921", {"start": v(510.05, -332.34) * mm, "end": v(509.3, -331.42) * mm});
            skLineSegment(sketch, "E3922", {"start": v(509.3, -331.42) * mm, "end": v(508.57, -330.5) * mm});
            skLineSegment(sketch, "E3923", {"start": v(508.57, -330.5) * mm, "end": v(507.85, -329.58) * mm});
            skLineSegment(sketch, "E3924", {"start": v(507.85, -329.58) * mm, "end": v(507.14, -328.65) * mm});
            skLineSegment(sketch, "E3925", {"start": v(507.14, -328.65) * mm, "end": v(506.45, -327.72) * mm});
            skLineSegment(sketch, "E3926", {"start": v(506.45, -327.72) * mm, "end": v(505.77, -326.78) * mm});
            skLineSegment(sketch, "E3927", {"start": v(505.77, -326.78) * mm, "end": v(505.1, -325.83) * mm});
            skLineSegment(sketch, "E3928", {"start": v(505.1, -325.83) * mm, "end": v(504.47, -324.88) * mm});
            skLineSegment(sketch, "E3929", {"start": v(504.47, -324.88) * mm, "end": v(503.85, -323.92) * mm});
            skLineSegment(sketch, "E3930", {"start": v(503.85, -323.92) * mm, "end": v(503.25, -322.96) * mm});
            skLineSegment(sketch, "E3931", {"start": v(503.25, -322.96) * mm, "end": v(502.68, -322) * mm});
            skLineSegment(sketch, "E3932", {"start": v(502.68, -322) * mm, "end": v(502.13, -321.01) * mm});
            skLineSegment(sketch, "E3933", {"start": v(502.13, -321.01) * mm, "end": v(501.62, -320.03) * mm});
            skLineSegment(sketch, "E3934", {"start": v(501.62, -320.03) * mm, "end": v(501.13, -319.04) * mm});
            skLineSegment(sketch, "E3935", {"start": v(501.13, -319.04) * mm, "end": v(500.67, -318.04) * mm});
            skLineSegment(sketch, "E3936", {"start": v(500.67, -318.04) * mm, "end": v(500.25, -317.03) * mm});
            skLineSegment(sketch, "E3937", {"start": v(500.25, -317.03) * mm, "end": v(499.87, -316.02) * mm});
            skLineSegment(sketch, "E3938", {"start": v(499.87, -316.02) * mm, "end": v(499.51, -315) * mm});
            skLineSegment(sketch, "E3939", {"start": v(499.51, -315) * mm, "end": v(499.2, -313.96) * mm});
            skLineSegment(sketch, "E3940", {"start": v(499.2, -313.96) * mm, "end": v(498.93, -312.92) * mm});
            skLineSegment(sketch, "E3941", {"start": v(498.93, -312.92) * mm, "end": v(498.7, -311.87) * mm});
            skLineSegment(sketch, "E3942", {"start": v(498.7, -311.87) * mm, "end": v(498.52, -310.8) * mm});
            skLineSegment(sketch, "E3943", {"start": v(498.52, -310.8) * mm, "end": v(498.37, -309.74) * mm});
            skLineSegment(sketch, "E3944", {"start": v(498.37, -309.74) * mm, "end": v(498.28, -308.65) * mm});
            skLineSegment(sketch, "E3945", {"start": v(498.28, -308.65) * mm, "end": v(498.24, -307.56) * mm});
            skLineSegment(sketch, "E3946", {"start": v(498.24, -307.56) * mm, "end": v(498.24, -306.46) * mm});
            skLineSegment(sketch, "E3947", {"start": v(498.24, -306.46) * mm, "end": v(498.3, -305.35) * mm});
            skLineSegment(sketch, "E3948", {"start": v(498.3, -305.35) * mm, "end": v(498.4, -304.22) * mm});
            skLineSegment(sketch, "E3949", {"start": v(498.4, -304.22) * mm, "end": v(498.58, -303.09) * mm});
            skLineSegment(sketch, "E3950", {"start": v(498.58, -303.09) * mm, "end": v(498.8, -301.94) * mm});
            skLineSegment(sketch, "E3951", {"start": v(498.8, -301.94) * mm, "end": v(499.08, -300.78) * mm});
            skLineSegment(sketch, "E3952", {"start": v(499.08, -300.78) * mm, "end": v(499.43, -299.61) * mm});
            skLineSegment(sketch, "E3953", {"start": v(499.43, -299.61) * mm, "end": v(499.84, -298.43) * mm});
            skLineSegment(sketch, "E3954", {"start": v(499.84, -298.43) * mm, "end": v(500.3, -297.23) * mm});
            skLineSegment(sketch, "E3955", {"start": v(500.3, -297.23) * mm, "end": v(500.84, -296.02) * mm});
            skLineSegment(sketch, "E3956", {"start": v(500.84, -296.02) * mm, "end": v(501.45, -294.8) * mm});
            skLineSegment(sketch, "E3957", {"start": v(501.45, -294.8) * mm, "end": v(502.12, -293.56) * mm});
            skLineSegment(sketch, "E3958", {"start": v(502.12, -293.56) * mm, "end": v(502.86, -292.3) * mm});
            skLineSegment(sketch, "E3959", {"start": v(502.86, -292.3) * mm, "end": v(503.68, -291.04) * mm});
            skLineSegment(sketch, "E3960", {"start": v(503.68, -291.04) * mm, "end": v(504.7, -289.6) * mm});
            skLineSegment(sketch, "E3961", {"start": v(504.7, -289.6) * mm, "end": v(505.77, -288.23) * mm});
            skLineSegment(sketch, "E3962", {"start": v(505.77, -288.23) * mm, "end": v(506.92, -286.9) * mm});
            skLineSegment(sketch, "E3963", {"start": v(506.92, -286.9) * mm, "end": v(508.13, -285.63) * mm});
            skLineSegment(sketch, "E3964", {"start": v(508.13, -285.63) * mm, "end": v(509.39, -284.42) * mm});
            skLineSegment(sketch, "E3965", {"start": v(509.39, -284.42) * mm, "end": v(510.7, -283.27) * mm});
            skLineSegment(sketch, "E3966", {"start": v(510.7, -283.27) * mm, "end": v(512.08, -282.18) * mm});
            skLineSegment(sketch, "E3967", {"start": v(512.08, -282.18) * mm, "end": v(513.5, -281.17) * mm});
            skLineSegment(sketch, "E3968", {"start": v(513.5, -281.17) * mm, "end": v(514.96, -280.22) * mm});
            skLineSegment(sketch, "E3969", {"start": v(514.96, -280.22) * mm, "end": v(516.46, -279.35) * mm});
            skLineSegment(sketch, "E3970", {"start": v(516.46, -279.35) * mm, "end": v(518, -278.56) * mm});
            skLineSegment(sketch, "E3971", {"start": v(518, -278.56) * mm, "end": v(519.59, -277.84) * mm});
            skLineSegment(sketch, "E3972", {"start": v(519.59, -277.84) * mm, "end": v(521.2, -277.21) * mm});
            skLineSegment(sketch, "E3973", {"start": v(521.2, -277.21) * mm, "end": v(522.84, -276.67) * mm});
            skLineSegment(sketch, "E3974", {"start": v(522.84, -276.67) * mm, "end": v(524.5, -276.21) * mm});
            skLineSegment(sketch, "E3975", {"start": v(524.5, -276.21) * mm, "end": v(526.19, -275.85) * mm});
            skLineSegment(sketch, "E3976", {"start": v(526.19, -275.85) * mm, "end": v(527.9, -275.58) * mm});
            skLineSegment(sketch, "E3977", {"start": v(527.9, -275.58) * mm, "end": v(529.61, -275.41) * mm});
            skLineSegment(sketch, "E3978", {"start": v(529.61, -275.41) * mm, "end": v(531.35, -275.34) * mm});
            skLineSegment(sketch, "E3979", {"start": v(531.35, -275.34) * mm, "end": v(533.1, -275.37) * mm});
            skLineSegment(sketch, "E3980", {"start": v(533.1, -275.37) * mm, "end": v(534.84, -275.51) * mm});
            skLineSegment(sketch, "E3981", {"start": v(534.84, -275.51) * mm, "end": v(536.6, -275.76) * mm});
            skLineSegment(sketch, "E3982", {"start": v(536.6, -275.76) * mm, "end": v(538.34, -276.12) * mm});
            skLineSegment(sketch, "E3983", {"start": v(538.34, -276.12) * mm, "end": v(539.74, -276.48) * mm});
            skLineSegment(sketch, "E3984", {"start": v(539.74, -276.48) * mm, "end": v(541.17, -276.88) * mm});
            skLineSegment(sketch, "E3985", {"start": v(541.17, -276.88) * mm, "end": v(542.63, -277.3) * mm});
            skLineSegment(sketch, "E3986", {"start": v(542.63, -277.3) * mm, "end": v(544.12, -277.77) * mm});
            skLineSegment(sketch, "E3987", {"start": v(544.12, -277.77) * mm, "end": v(545.64, -278.26) * mm});
            skLineSegment(sketch, "E3988", {"start": v(545.64, -278.26) * mm, "end": v(547.17, -278.75) * mm});
            skLineSegment(sketch, "E3989", {"start": v(547.17, -278.75) * mm, "end": v(548.73, -279.26) * mm});
            skLineSegment(sketch, "E3990", {"start": v(548.73, -279.26) * mm, "end": v(550.3, -279.76) * mm});
            skLineSegment(sketch, "E3991", {"start": v(550.3, -279.76) * mm, "end": v(551.87, -280.26) * mm});
            skLineSegment(sketch, "E3992", {"start": v(551.87, -280.26) * mm, "end": v(553.46, -280.74) * mm});
            skLineSegment(sketch, "E3993", {"start": v(553.46, -280.74) * mm, "end": v(555.05, -281.2) * mm});
            skLineSegment(sketch, "E3994", {"start": v(555.05, -281.2) * mm, "end": v(556.65, -281.64) * mm});
            skLineSegment(sketch, "E3995", {"start": v(556.65, -281.64) * mm, "end": v(558.24, -282.03) * mm});
            skLineSegment(sketch, "E3996", {"start": v(558.24, -282.03) * mm, "end": v(559.83, -282.38) * mm});
            skLineSegment(sketch, "E3997", {"start": v(559.83, -282.38) * mm, "end": v(561.4, -282.68) * mm});
            skLineSegment(sketch, "E3998", {"start": v(561.4, -282.68) * mm, "end": v(562.97, -282.93) * mm});
            skLineSegment(sketch, "E3999", {"start": v(562.97, -282.93) * mm, "end": v(564.53, -283.1) * mm});
            skLineSegment(sketch, "E4000", {"start": v(564.53, -283.1) * mm, "end": v(566.06, -283.2) * mm});
            skLineSegment(sketch, "E4001", {"start": v(566.06, -283.2) * mm, "end": v(567.58, -283.23) * mm});
            skLineSegment(sketch, "E4002", {"start": v(567.58, -283.23) * mm, "end": v(569.07, -283.17) * mm});
            skLineSegment(sketch, "E4003", {"start": v(569.07, -283.17) * mm, "end": v(570.53, -283.01) * mm});
            skLineSegment(sketch, "E4004", {"start": v(570.53, -283.01) * mm, "end": v(571.96, -282.75) * mm});
            skLineSegment(sketch, "E4005", {"start": v(571.96, -282.75) * mm, "end": v(573.36, -282.39) * mm});
            skLineSegment(sketch, "E4006", {"start": v(573.36, -282.39) * mm, "end": v(574.72, -281.9) * mm});
            skLineSegment(sketch, "E4007", {"start": v(574.72, -281.9) * mm, "end": v(576.04, -281.3) * mm});
            skLineSegment(sketch, "E4008", {"start": v(576.04, -281.3) * mm, "end": v(577.32, -280.56) * mm});
            skLineSegment(sketch, "E4009", {"start": v(577.32, -280.56) * mm, "end": v(578.55, -279.68) * mm});
            skLineSegment(sketch, "E4010", {"start": v(578.55, -279.68) * mm, "end": v(579.73, -278.66) * mm});
            skLineSegment(sketch, "E4011", {"start": v(579.73, -278.66) * mm, "end": v(580.86, -277.5) * mm});
            skLineSegment(sketch, "E4012", {"start": v(580.86, -277.5) * mm, "end": v(581.93, -276.16) * mm});
            skLineSegment(sketch, "E4013", {"start": v(581.93, -276.16) * mm, "end": v(582.94, -274.66) * mm});
            skLineSegment(sketch, "E4014", {"start": v(582.94, -274.66) * mm, "end": v(583.64, -273.5) * mm});
            skLineSegment(sketch, "E4015", {"start": v(583.64, -273.5) * mm, "end": v(584.25, -272.34) * mm});
            skLineSegment(sketch, "E4016", {"start": v(584.25, -272.34) * mm, "end": v(584.8, -271.22) * mm});
            skLineSegment(sketch, "E4017", {"start": v(584.8, -271.22) * mm, "end": v(585.27, -270.1) * mm});
            skLineSegment(sketch, "E4018", {"start": v(585.27, -270.1) * mm, "end": v(585.67, -269.02) * mm});
            skLineSegment(sketch, "E4019", {"start": v(585.67, -269.02) * mm, "end": v(586, -267.96) * mm});
            skLineSegment(sketch, "E4020", {"start": v(586, -267.96) * mm, "end": v(586.27, -266.9) * mm});
            skLineSegment(sketch, "E4021", {"start": v(586.27, -266.9) * mm, "end": v(586.47, -265.88) * mm});
            skLineSegment(sketch, "E4022", {"start": v(586.47, -265.88) * mm, "end": v(586.6, -264.86) * mm});
            skLineSegment(sketch, "E4023", {"start": v(586.6, -264.86) * mm, "end": v(586.69, -263.87) * mm});
            skLineSegment(sketch, "E4024", {"start": v(586.69, -263.87) * mm, "end": v(586.7, -262.89) * mm});
            skLineSegment(sketch, "E4025", {"start": v(586.7, -262.89) * mm, "end": v(586.66, -261.92) * mm});
            skLineSegment(sketch, "E4026", {"start": v(586.66, -261.92) * mm, "end": v(586.57, -260.98) * mm});
            skLineSegment(sketch, "E4027", {"start": v(586.57, -260.98) * mm, "end": v(586.42, -260.04) * mm});
            skLineSegment(sketch, "E4028", {"start": v(586.42, -260.04) * mm, "end": v(586.21, -259.12) * mm});
            skLineSegment(sketch, "E4029", {"start": v(586.21, -259.12) * mm, "end": v(585.96, -258.22) * mm});
            skLineSegment(sketch, "E4030", {"start": v(585.96, -258.22) * mm, "end": v(585.66, -257.32) * mm});
            skLineSegment(sketch, "E4031", {"start": v(585.66, -257.32) * mm, "end": v(585.3, -256.44) * mm});
            skLineSegment(sketch, "E4032", {"start": v(585.3, -256.44) * mm, "end": v(584.92, -255.57) * mm});
            skLineSegment(sketch, "E4033", {"start": v(584.92, -255.57) * mm, "end": v(584.48, -254.72) * mm});
            skLineSegment(sketch, "E4034", {"start": v(584.48, -254.72) * mm, "end": v(584, -253.87) * mm});
            skLineSegment(sketch, "E4035", {"start": v(584, -253.87) * mm, "end": v(583.48, -253.03) * mm});
            skLineSegment(sketch, "E4036", {"start": v(583.48, -253.03) * mm, "end": v(582.92, -252.2) * mm});
            skLineSegment(sketch, "E4037", {"start": v(582.92, -252.2) * mm, "end": v(582.33, -251.39) * mm});
            skLineSegment(sketch, "E4038", {"start": v(582.33, -251.39) * mm, "end": v(581.7, -250.57) * mm});
            skLineSegment(sketch, "E4039", {"start": v(581.7, -250.57) * mm, "end": v(581.04, -249.77) * mm});
            skLineSegment(sketch, "E4040", {"start": v(581.04, -249.77) * mm, "end": v(580.34, -248.98) * mm});
            skLineSegment(sketch, "E4041", {"start": v(580.34, -248.98) * mm, "end": v(579.62, -248.19) * mm});
            skLineSegment(sketch, "E4042", {"start": v(579.62, -248.19) * mm, "end": v(578.87, -247.4) * mm});
            skLineSegment(sketch, "E4043", {"start": v(578.87, -247.4) * mm, "end": v(578.1, -246.63) * mm});
            skLineSegment(sketch, "E4044", {"start": v(578.1, -246.63) * mm, "end": v(577.3, -245.85) * mm});
            skLineSegment(sketch, "E4045", {"start": v(577.3, -245.85) * mm, "end": v(576.47, -245.08) * mm});
            skLineSegment(sketch, "E4046", {"start": v(576.47, -245.08) * mm, "end": v(575.63, -244.32) * mm});
            skLineSegment(sketch, "E4047", {"start": v(575.63, -244.32) * mm, "end": v(574.77, -243.56) * mm});
            skLineSegment(sketch, "E4048", {"start": v(574.77, -243.56) * mm, "end": v(573.9, -242.8) * mm});
            skLineSegment(sketch, "E4049", {"start": v(573.9, -242.8) * mm, "end": v(573, -242.04) * mm});
            skLineSegment(sketch, "E4050", {"start": v(573, -242.04) * mm, "end": v(572.1, -241.28) * mm});
            skLineSegment(sketch, "E4051", {"start": v(572.1, -241.28) * mm, "end": v(571.18, -240.53) * mm});
            skLineSegment(sketch, "E4052", {"start": v(571.18, -240.53) * mm, "end": v(570.25, -239.77) * mm});
            skLineSegment(sketch, "E4053", {"start": v(570.25, -239.77) * mm, "end": v(569.32, -239.02) * mm});
            skLineSegment(sketch, "E4054", {"start": v(569.32, -239.02) * mm, "end": v(568.38, -238.26) * mm});
            skLineSegment(sketch, "E4055", {"start": v(568.38, -238.26) * mm, "end": v(567.43, -237.5) * mm});
            skLineSegment(sketch, "E4056", {"start": v(567.43, -237.5) * mm, "end": v(566.48, -236.74) * mm});
            skLineSegment(sketch, "E4057", {"start": v(566.48, -236.74) * mm, "end": v(565.53, -235.98) * mm});
            skLineSegment(sketch, "E4058", {"start": v(565.53, -235.98) * mm, "end": v(564.58, -235.2) * mm});
            skLineSegment(sketch, "E4059", {"start": v(564.58, -235.2) * mm, "end": v(563.64, -234.44) * mm});
            skLineSegment(sketch, "E4060", {"start": v(563.64, -234.44) * mm, "end": v(562.7, -233.66) * mm});
            skLineSegment(sketch, "E4061", {"start": v(562.7, -233.66) * mm, "end": v(561.76, -232.88) * mm});
            skLineSegment(sketch, "E4062", {"start": v(561.76, -232.88) * mm, "end": v(560.84, -232.1) * mm});
            skLineSegment(sketch, "E4063", {"start": v(560.84, -232.1) * mm, "end": v(559.92, -231.3) * mm});
            skLineSegment(sketch, "E4064", {"start": v(559.92, -231.3) * mm, "end": v(559.01, -230.5) * mm});
            skLineSegment(sketch, "E4065", {"start": v(559.01, -230.5) * mm, "end": v(558.12, -229.7) * mm});
            skLineSegment(sketch, "E4066", {"start": v(558.12, -229.7) * mm, "end": v(557.24, -228.88) * mm});
            skLineSegment(sketch, "E4067", {"start": v(557.24, -228.88) * mm, "end": v(556.38, -228.06) * mm});
            skLineSegment(sketch, "E4068", {"start": v(556.38, -228.06) * mm, "end": v(555.54, -227.23) * mm});
            skLineSegment(sketch, "E4069", {"start": v(555.54, -227.23) * mm, "end": v(554.72, -226.38) * mm});
            skLineSegment(sketch, "E4070", {"start": v(554.72, -226.38) * mm, "end": v(553.92, -225.53) * mm});
            skLineSegment(sketch, "E4071", {"start": v(553.92, -225.53) * mm, "end": v(553.15, -224.67) * mm});
            skLineSegment(sketch, "E4072", {"start": v(553.15, -224.67) * mm, "end": v(552.4, -223.8) * mm});
            skLineSegment(sketch, "E4073", {"start": v(552.4, -223.8) * mm, "end": v(551.68, -222.9) * mm});
            skLineSegment(sketch, "E4074", {"start": v(551.68, -222.9) * mm, "end": v(550.99, -222) * mm});
            skLineSegment(sketch, "E4075", {"start": v(550.99, -222) * mm, "end": v(550.33, -221.1) * mm});
            skLineSegment(sketch, "E4076", {"start": v(550.33, -221.1) * mm, "end": v(549.7, -220.16) * mm});
            skLineSegment(sketch, "E4077", {"start": v(549.7, -220.16) * mm, "end": v(549.1, -219.22) * mm});
            skLineSegment(sketch, "E4078", {"start": v(549.1, -219.22) * mm, "end": v(548.55, -218.27) * mm});
            skLineSegment(sketch, "E4079", {"start": v(548.55, -218.27) * mm, "end": v(548.03, -217.3) * mm});
            skLineSegment(sketch, "E4080", {"start": v(548.03, -217.3) * mm, "end": v(547.55, -216.3) * mm});
            skLineSegment(sketch, "E4081", {"start": v(547.55, -216.3) * mm, "end": v(547.11, -215.3) * mm});
            skLineSegment(sketch, "E4082", {"start": v(547.11, -215.3) * mm, "end": v(546.72, -214.28) * mm});
            skLineSegment(sketch, "E4083", {"start": v(546.72, -214.28) * mm, "end": v(546.37, -213.24) * mm});
            skLineSegment(sketch, "E4084", {"start": v(546.37, -213.24) * mm, "end": v(546.07, -212.18) * mm});
            skLineSegment(sketch, "E4085", {"start": v(546.07, -212.18) * mm, "end": v(545.82, -211.1) * mm});
            skLineSegment(sketch, "E4086", {"start": v(545.82, -211.1) * mm, "end": v(545.62, -210) * mm});
            skLineSegment(sketch, "E4087", {"start": v(545.62, -210) * mm, "end": v(545.47, -208.89) * mm});
            skLineSegment(sketch, "E4088", {"start": v(545.47, -208.89) * mm, "end": v(545.38, -207.75) * mm});
            skLineSegment(sketch, "E4089", {"start": v(545.38, -207.75) * mm, "end": v(545.34, -206.59) * mm});
            skLineSegment(sketch, "E4090", {"start": v(545.34, -206.59) * mm, "end": v(545.36, -205.4) * mm});
            skLineSegment(sketch, "E4091", {"start": v(545.36, -205.4) * mm, "end": v(545.44, -204.2) * mm});
            skLineSegment(sketch, "E4092", {"start": v(545.44, -204.2) * mm, "end": v(545.58, -202.97) * mm});
            skLineSegment(sketch, "E4093", {"start": v(545.58, -202.97) * mm, "end": v(545.78, -201.72) * mm});
            skLineSegment(sketch, "E4094", {"start": v(545.78, -201.72) * mm, "end": v(546.05, -200.45) * mm});
            skLineSegment(sketch, "E4095", {"start": v(546.05, -200.45) * mm, "end": v(546.38, -199.14) * mm});
            skLineSegment(sketch, "E4096", {"start": v(546.38, -199.14) * mm, "end": v(546.79, -197.82) * mm});
            skLineSegment(sketch, "E4097", {"start": v(546.79, -197.82) * mm, "end": v(547.26, -196.47) * mm});
            skLineSegment(sketch, "E4098", {"start": v(547.26, -196.47) * mm, "end": v(547.8, -195.09) * mm});
            skLineSegment(sketch, "E4099", {"start": v(547.8, -195.09) * mm, "end": v(548.63, -193.23) * mm});
            skLineSegment(sketch, "E4100", {"start": v(548.63, -193.23) * mm, "end": v(549.52, -191.48) * mm});
            skLineSegment(sketch, "E4101", {"start": v(549.52, -191.48) * mm, "end": v(550.45, -189.83) * mm});
            skLineSegment(sketch, "E4102", {"start": v(550.45, -189.83) * mm, "end": v(551.45, -188.27) * mm});
            skLineSegment(sketch, "E4103", {"start": v(551.45, -188.27) * mm, "end": v(552.49, -186.81) * mm});
            skLineSegment(sketch, "E4104", {"start": v(552.49, -186.81) * mm, "end": v(553.58, -185.44) * mm});
            skLineSegment(sketch, "E4105", {"start": v(553.58, -185.44) * mm, "end": v(554.72, -184.16) * mm});
            skLineSegment(sketch, "E4106", {"start": v(554.72, -184.16) * mm, "end": v(555.91, -182.97) * mm});
            skLineSegment(sketch, "E4107", {"start": v(555.91, -182.97) * mm, "end": v(557.15, -181.86) * mm});
            skLineSegment(sketch, "E4108", {"start": v(557.15, -181.86) * mm, "end": v(558.43, -180.83) * mm});
            skLineSegment(sketch, "E4109", {"start": v(558.43, -180.83) * mm, "end": v(559.75, -179.88) * mm});
            skLineSegment(sketch, "E4110", {"start": v(559.75, -179.88) * mm, "end": v(561.1, -179) * mm});
            skLineSegment(sketch, "E4111", {"start": v(561.1, -179) * mm, "end": v(562.51, -178.21) * mm});
            skLineSegment(sketch, "E4112", {"start": v(562.51, -178.21) * mm, "end": v(563.95, -177.48) * mm});
            skLineSegment(sketch, "E4113", {"start": v(563.95, -177.48) * mm, "end": v(565.43, -176.82) * mm});
            skLineSegment(sketch, "E4114", {"start": v(565.43, -176.82) * mm, "end": v(566.94, -176.23) * mm});
            skLineSegment(sketch, "E4115", {"start": v(566.94, -176.23) * mm, "end": v(568.48, -175.7) * mm});
            skLineSegment(sketch, "E4116", {"start": v(568.48, -175.7) * mm, "end": v(570.05, -175.23) * mm});
            skLineSegment(sketch, "E4117", {"start": v(570.05, -175.23) * mm, "end": v(571.66, -174.82) * mm});
            skLineSegment(sketch, "E4118", {"start": v(571.66, -174.82) * mm, "end": v(573.3, -174.46) * mm});
            skLineSegment(sketch, "E4119", {"start": v(573.3, -174.46) * mm, "end": v(574.95, -174.16) * mm});
            skLineSegment(sketch, "E4120", {"start": v(574.95, -174.16) * mm, "end": v(576.64, -173.9) * mm});
            skLineSegment(sketch, "E4121", {"start": v(576.64, -173.9) * mm, "end": v(578.35, -173.7) * mm});
            skLineSegment(sketch, "E4122", {"start": v(578.35, -173.7) * mm, "end": v(580.08, -173.54) * mm});
            skLineSegment(sketch, "E4123", {"start": v(580.08, -173.54) * mm, "end": v(581.83, -173.42) * mm});
            skLineSegment(sketch, "E4124", {"start": v(581.83, -173.42) * mm, "end": v(583.6, -173.34) * mm});
            skLineSegment(sketch, "E4125", {"start": v(583.6, -173.34) * mm, "end": v(585.39, -173.3) * mm});
            skLineSegment(sketch, "E4126", {"start": v(585.39, -173.3) * mm, "end": v(587.2, -173.3) * mm});
            skLineSegment(sketch, "E4127", {"start": v(587.2, -173.3) * mm, "end": v(589.01, -173.32) * mm});
            skLineSegment(sketch, "E4128", {"start": v(589.01, -173.32) * mm, "end": v(590.84, -173.37) * mm});
            skLineSegment(sketch, "E4129", {"start": v(590.84, -173.37) * mm, "end": v(592.47, -173.45) * mm});
            skLineSegment(sketch, "E4130", {"start": v(592.47, -173.45) * mm, "end": v(594.1, -173.58) * mm});
            skLineSegment(sketch, "E4131", {"start": v(594.1, -173.58) * mm, "end": v(595.75, -173.73) * mm});
            skLineSegment(sketch, "E4132", {"start": v(595.75, -173.73) * mm, "end": v(597.4, -173.9) * mm});
            skLineSegment(sketch, "E4133", {"start": v(597.4, -173.9) * mm, "end": v(599.04, -174.06) * mm});
            skLineSegment(sketch, "E4134", {"start": v(599.04, -174.06) * mm, "end": v(600.67, -174.23) * mm});
            skLineSegment(sketch, "E4135", {"start": v(600.67, -174.23) * mm, "end": v(602.3, -174.37) * mm});
            skLineSegment(sketch, "E4136", {"start": v(602.3, -174.37) * mm, "end": v(603.9, -174.48) * mm});
            skLineSegment(sketch, "E4137", {"start": v(603.9, -174.48) * mm, "end": v(605.49, -174.54) * mm});
            skLineSegment(sketch, "E4138", {"start": v(605.49, -174.54) * mm, "end": v(607.05, -174.56) * mm});
            skLineSegment(sketch, "E4139", {"start": v(607.05, -174.56) * mm, "end": v(608.58, -174.5) * mm});
            skLineSegment(sketch, "E4140", {"start": v(608.58, -174.5) * mm, "end": v(610.08, -174.36) * mm});
            skLineSegment(sketch, "E4141", {"start": v(610.08, -174.36) * mm, "end": v(611.55, -174.14) * mm});
            skLineSegment(sketch, "E4142", {"start": v(611.55, -174.14) * mm, "end": v(612.97, -173.81) * mm});
            skLineSegment(sketch, "E4143", {"start": v(612.97, -173.81) * mm, "end": v(614.34, -173.37) * mm});
            skLineSegment(sketch, "E4144", {"start": v(614.34, -173.37) * mm, "end": v(615.67, -172.8) * mm});
            skLineSegment(sketch, "E4145", {"start": v(615.67, -172.8) * mm, "end": v(616.94, -172.1) * mm});
            skLineSegment(sketch, "E4146", {"start": v(616.94, -172.1) * mm, "end": v(618.15, -171.23) * mm});
            skLineSegment(sketch, "E4147", {"start": v(618.15, -171.23) * mm, "end": v(619.3, -170.21) * mm});
            skLineSegment(sketch, "E4148", {"start": v(619.3, -170.21) * mm, "end": v(620.39, -169.02) * mm});
            skLineSegment(sketch, "E4149", {"start": v(620.39, -169.02) * mm, "end": v(621.4, -167.64) * mm});
            skLineSegment(sketch, "E4150", {"start": v(621.4, -167.64) * mm, "end": v(622.33, -166.07) * mm});
            skLineSegment(sketch, "E4151", {"start": v(622.33, -166.07) * mm, "end": v(623.19, -164.28) * mm});
            skLineSegment(sketch, "E4152", {"start": v(623.19, -164.28) * mm, "end": v(623.72, -162.96) * mm});
            skLineSegment(sketch, "E4153", {"start": v(623.72, -162.96) * mm, "end": v(624.2, -161.68) * mm});
            skLineSegment(sketch, "E4154", {"start": v(624.2, -161.68) * mm, "end": v(624.59, -160.44) * mm});
            skLineSegment(sketch, "E4155", {"start": v(624.59, -160.44) * mm, "end": v(624.92, -159.23) * mm});
            skLineSegment(sketch, "E4156", {"start": v(624.92, -159.23) * mm, "end": v(625.18, -158.05) * mm});
            skLineSegment(sketch, "E4157", {"start": v(625.18, -158.05) * mm, "end": v(625.38, -156.91) * mm});
            skLineSegment(sketch, "E4158", {"start": v(625.38, -156.91) * mm, "end": v(625.51, -155.8) * mm});
            skLineSegment(sketch, "E4159", {"start": v(625.51, -155.8) * mm, "end": v(625.58, -154.72) * mm});
            skLineSegment(sketch, "E4160", {"start": v(625.58, -154.72) * mm, "end": v(625.6, -153.68) * mm});
            skLineSegment(sketch, "E4161", {"start": v(625.6, -153.68) * mm, "end": v(625.55, -152.66) * mm});
            skLineSegment(sketch, "E4162", {"start": v(625.55, -152.66) * mm, "end": v(625.45, -151.67) * mm});
            skLineSegment(sketch, "E4163", {"start": v(625.45, -151.67) * mm, "end": v(625.29, -150.71) * mm});
            skLineSegment(sketch, "E4164", {"start": v(625.29, -150.71) * mm, "end": v(625.08, -149.78) * mm});
            skLineSegment(sketch, "E4165", {"start": v(625.08, -149.78) * mm, "end": v(624.81, -148.88) * mm});
            skLineSegment(sketch, "E4166", {"start": v(624.81, -148.88) * mm, "end": v(624.5, -148) * mm});
            skLineSegment(sketch, "E4167", {"start": v(624.5, -148) * mm, "end": v(624.13, -147.14) * mm});
            skLineSegment(sketch, "E4168", {"start": v(624.13, -147.14) * mm, "end": v(623.72, -146.3) * mm});
            skLineSegment(sketch, "E4169", {"start": v(623.72, -146.3) * mm, "end": v(623.27, -145.5) * mm});
            skLineSegment(sketch, "E4170", {"start": v(623.27, -145.5) * mm, "end": v(622.77, -144.7) * mm});
            skLineSegment(sketch, "E4171", {"start": v(622.77, -144.7) * mm, "end": v(622.23, -143.94) * mm});
            skLineSegment(sketch, "E4172", {"start": v(622.23, -143.94) * mm, "end": v(621.64, -143.19) * mm});
            skLineSegment(sketch, "E4173", {"start": v(621.64, -143.19) * mm, "end": v(621.02, -142.46) * mm});
            skLineSegment(sketch, "E4174", {"start": v(621.02, -142.46) * mm, "end": v(620.36, -141.74) * mm});
            skLineSegment(sketch, "E4175", {"start": v(620.36, -141.74) * mm, "end": v(619.67, -141.05) * mm});
            skLineSegment(sketch, "E4176", {"start": v(619.67, -141.05) * mm, "end": v(618.94, -140.37) * mm});
            skLineSegment(sketch, "E4177", {"start": v(618.94, -140.37) * mm, "end": v(618.17, -139.7) * mm});
            skLineSegment(sketch, "E4178", {"start": v(618.17, -139.7) * mm, "end": v(617.38, -139.05) * mm});
            skLineSegment(sketch, "E4179", {"start": v(617.38, -139.05) * mm, "end": v(616.56, -138.42) * mm});
            skLineSegment(sketch, "E4180", {"start": v(616.56, -138.42) * mm, "end": v(615.7, -137.8) * mm});
            skLineSegment(sketch, "E4181", {"start": v(615.7, -137.8) * mm, "end": v(614.83, -137.18) * mm});
            skLineSegment(sketch, "E4182", {"start": v(614.83, -137.18) * mm, "end": v(613.93, -136.57) * mm});
            skLineSegment(sketch, "E4183", {"start": v(613.93, -136.57) * mm, "end": v(613, -135.98) * mm});
            skLineSegment(sketch, "E4184", {"start": v(613, -135.98) * mm, "end": v(612.06, -135.4) * mm});
            skLineSegment(sketch, "E4185", {"start": v(612.06, -135.4) * mm, "end": v(611.1, -134.82) * mm});
            skLineSegment(sketch, "E4186", {"start": v(611.1, -134.82) * mm, "end": v(610.11, -134.25) * mm});
            skLineSegment(sketch, "E4187", {"start": v(610.11, -134.25) * mm, "end": v(609.11, -133.68) * mm});
            skLineSegment(sketch, "E4188", {"start": v(609.11, -133.68) * mm, "end": v(608.1, -133.12) * mm});
            skLineSegment(sketch, "E4189", {"start": v(608.1, -133.12) * mm, "end": v(607.07, -132.56) * mm});
            skLineSegment(sketch, "E4190", {"start": v(607.07, -132.56) * mm, "end": v(606.03, -132.01) * mm});
            skLineSegment(sketch, "E4191", {"start": v(606.03, -132.01) * mm, "end": v(604.98, -131.46) * mm});
            skLineSegment(sketch, "E4192", {"start": v(604.98, -131.46) * mm, "end": v(603.93, -130.9) * mm});
            skLineSegment(sketch, "E4193", {"start": v(603.93, -130.9) * mm, "end": v(602.86, -130.36) * mm});
            skLineSegment(sketch, "E4194", {"start": v(602.86, -130.36) * mm, "end": v(601.8, -129.8) * mm});
            skLineSegment(sketch, "E4195", {"start": v(601.8, -129.8) * mm, "end": v(600.72, -129.26) * mm});
            skLineSegment(sketch, "E4196", {"start": v(600.72, -129.26) * mm, "end": v(599.65, -128.7) * mm});
            skLineSegment(sketch, "E4197", {"start": v(599.65, -128.7) * mm, "end": v(598.57, -128.14) * mm});
            skLineSegment(sketch, "E4198", {"start": v(598.57, -128.14) * mm, "end": v(597.5, -127.58) * mm});
            skLineSegment(sketch, "E4199", {"start": v(597.5, -127.58) * mm, "end": v(596.43, -127.01) * mm});
            skLineSegment(sketch, "E4200", {"start": v(596.43, -127.01) * mm, "end": v(595.36, -126.44) * mm});
            skLineSegment(sketch, "E4201", {"start": v(595.36, -126.44) * mm, "end": v(594.3, -125.85) * mm});
            skLineSegment(sketch, "E4202", {"start": v(594.3, -125.85) * mm, "end": v(593.25, -125.26) * mm});
            skLineSegment(sketch, "E4203", {"start": v(593.25, -125.26) * mm, "end": v(592.2, -124.66) * mm});
            skLineSegment(sketch, "E4204", {"start": v(592.2, -124.66) * mm, "end": v(591.17, -124.06) * mm});
            skLineSegment(sketch, "E4205", {"start": v(591.17, -124.06) * mm, "end": v(590.15, -123.43) * mm});
            skLineSegment(sketch, "E4206", {"start": v(590.15, -123.43) * mm, "end": v(589.15, -122.8) * mm});
            skLineSegment(sketch, "E4207", {"start": v(589.15, -122.8) * mm, "end": v(588.16, -122.16) * mm});
            skLineSegment(sketch, "E4208", {"start": v(588.16, -122.16) * mm, "end": v(587.19, -121.5) * mm});
            skLineSegment(sketch, "E4209", {"start": v(587.19, -121.5) * mm, "end": v(586.24, -120.83) * mm});
            skLineSegment(sketch, "E4210", {"start": v(586.24, -120.83) * mm, "end": v(585.3, -120.14) * mm});
            skLineSegment(sketch, "E4211", {"start": v(585.3, -120.14) * mm, "end": v(584.4, -119.43) * mm});
            skLineSegment(sketch, "E4212", {"start": v(584.4, -119.43) * mm, "end": v(583.51, -118.7) * mm});
            skLineSegment(sketch, "E4213", {"start": v(583.51, -118.7) * mm, "end": v(582.65, -117.97) * mm});
            skLineSegment(sketch, "E4214", {"start": v(582.65, -117.97) * mm, "end": v(581.82, -117.2) * mm});
            skLineSegment(sketch, "E4215", {"start": v(581.82, -117.2) * mm, "end": v(581.01, -116.43) * mm});
            skLineSegment(sketch, "E4216", {"start": v(581.01, -116.43) * mm, "end": v(580.24, -115.62) * mm});
            skLineSegment(sketch, "E4217", {"start": v(580.24, -115.62) * mm, "end": v(579.5, -114.8) * mm});
            skLineSegment(sketch, "E4218", {"start": v(579.5, -114.8) * mm, "end": v(578.8, -113.95) * mm});
            skLineSegment(sketch, "E4219", {"start": v(578.8, -113.95) * mm, "end": v(578.12, -113.08) * mm});
            skLineSegment(sketch, "E4220", {"start": v(578.12, -113.08) * mm, "end": v(577.48, -112.18) * mm});
            skLineSegment(sketch, "E4221", {"start": v(577.48, -112.18) * mm, "end": v(576.89, -111.26) * mm});
            skLineSegment(sketch, "E4222", {"start": v(576.89, -111.26) * mm, "end": v(576.33, -110.31) * mm});
            skLineSegment(sketch, "E4223", {"start": v(576.33, -110.31) * mm, "end": v(575.82, -109.34) * mm});
            skLineSegment(sketch, "E4224", {"start": v(575.82, -109.34) * mm, "end": v(575.34, -108.33) * mm});
            skLineSegment(sketch, "E4225", {"start": v(575.34, -108.33) * mm, "end": v(574.92, -107.3) * mm});
            skLineSegment(sketch, "E4226", {"start": v(574.92, -107.3) * mm, "end": v(574.54, -106.23) * mm});
            skLineSegment(sketch, "E4227", {"start": v(574.54, -106.23) * mm, "end": v(574.2, -105.14) * mm});
            skLineSegment(sketch, "E4228", {"start": v(574.2, -105.14) * mm, "end": v(573.92, -104.01) * mm});
            skLineSegment(sketch, "E4229", {"start": v(573.92, -104.01) * mm, "end": v(573.7, -102.85) * mm});
            skLineSegment(sketch, "E4230", {"start": v(573.7, -102.85) * mm, "end": v(573.52, -101.65) * mm});
            skLineSegment(sketch, "E4231", {"start": v(573.52, -101.65) * mm, "end": v(573.4, -100.42) * mm});
            skLineSegment(sketch, "E4232", {"start": v(573.4, -100.42) * mm, "end": v(573.33, -99.15) * mm});
            skLineSegment(sketch, "E4233", {"start": v(573.33, -99.15) * mm, "end": v(573.32, -97.85) * mm});
            skLineSegment(sketch, "E4234", {"start": v(573.32, -97.85) * mm, "end": v(573.37, -96.5) * mm});
            skLineSegment(sketch, "E4235", {"start": v(573.37, -96.5) * mm, "end": v(573.48, -95.13) * mm});
            skLineSegment(sketch, "E4236", {"start": v(573.48, -95.13) * mm, "end": v(573.66, -93.7) * mm});
            skLineSegment(sketch, "E4237", {"start": v(573.66, -93.7) * mm, "end": v(573.98, -91.77) * mm});
            skLineSegment(sketch, "E4238", {"start": v(573.98, -91.77) * mm, "end": v(574.4, -89.92) * mm});
            skLineSegment(sketch, "E4239", {"start": v(574.4, -89.92) * mm, "end": v(574.88, -88.14) * mm});
            skLineSegment(sketch, "E4240", {"start": v(574.88, -88.14) * mm, "end": v(575.45, -86.43) * mm});
            skLineSegment(sketch, "E4241", {"start": v(575.45, -86.43) * mm, "end": v(576.1, -84.8) * mm});
            skLineSegment(sketch, "E4242", {"start": v(576.1, -84.8) * mm, "end": v(576.81, -83.24) * mm});
            skLineSegment(sketch, "E4243", {"start": v(576.81, -83.24) * mm, "end": v(577.6, -81.75) * mm});
            skLineSegment(sketch, "E4244", {"start": v(577.6, -81.75) * mm, "end": v(578.45, -80.33) * mm});
            skLineSegment(sketch, "E4245", {"start": v(578.45, -80.33) * mm, "end": v(579.37, -78.98) * mm});
            skLineSegment(sketch, "E4246", {"start": v(579.37, -78.98) * mm, "end": v(580.36, -77.7) * mm});
            skLineSegment(sketch, "E4247", {"start": v(580.36, -77.7) * mm, "end": v(581.4, -76.47) * mm});
            skLineSegment(sketch, "E4248", {"start": v(581.4, -76.47) * mm, "end": v(582.5, -75.3) * mm});
            skLineSegment(sketch, "E4249", {"start": v(582.5, -75.3) * mm, "end": v(583.66, -74.2) * mm});
            skLineSegment(sketch, "E4250", {"start": v(583.66, -74.2) * mm, "end": v(584.86, -73.15) * mm});
            skLineSegment(sketch, "E4251", {"start": v(584.86, -73.15) * mm, "end": v(586.12, -72.17) * mm});
            skLineSegment(sketch, "E4252", {"start": v(586.12, -72.17) * mm, "end": v(587.43, -71.23) * mm});
            skLineSegment(sketch, "E4253", {"start": v(587.43, -71.23) * mm, "end": v(588.78, -70.35) * mm});
            skLineSegment(sketch, "E4254", {"start": v(588.78, -70.35) * mm, "end": v(590.17, -69.53) * mm});
            skLineSegment(sketch, "E4255", {"start": v(590.17, -69.53) * mm, "end": v(591.6, -68.75) * mm});
            skLineSegment(sketch, "E4256", {"start": v(591.6, -68.75) * mm, "end": v(593.07, -68.02) * mm});
            skLineSegment(sketch, "E4257", {"start": v(593.07, -68.02) * mm, "end": v(594.58, -67.34) * mm});
            skLineSegment(sketch, "E4258", {"start": v(594.58, -67.34) * mm, "end": v(596.11, -66.7) * mm});
            skLineSegment(sketch, "E4259", {"start": v(596.11, -66.7) * mm, "end": v(597.68, -66.1) * mm});
            skLineSegment(sketch, "E4260", {"start": v(597.68, -66.1) * mm, "end": v(599.27, -65.55) * mm});
            skLineSegment(sketch, "E4261", {"start": v(599.27, -65.55) * mm, "end": v(600.88, -65.04) * mm});
            skLineSegment(sketch, "E4262", {"start": v(600.88, -65.04) * mm, "end": v(602.52, -64.56) * mm});
            skLineSegment(sketch, "E4263", {"start": v(602.52, -64.56) * mm, "end": v(604.18, -64.12) * mm});
            skLineSegment(sketch, "E4264", {"start": v(604.18, -64.12) * mm, "end": v(605.85, -63.72) * mm});
            skLineSegment(sketch, "E4265", {"start": v(605.85, -63.72) * mm, "end": v(607.54, -63.35) * mm});
            skLineSegment(sketch, "E4266", {"start": v(607.54, -63.35) * mm, "end": v(609.24, -63.01) * mm});
            skLineSegment(sketch, "E4267", {"start": v(609.24, -63.01) * mm, "end": v(610.95, -62.7) * mm});
            skLineSegment(sketch, "E4268", {"start": v(610.95, -62.7) * mm, "end": v(612.66, -62.42) * mm});
            skLineSegment(sketch, "E4269", {"start": v(612.66, -62.42) * mm, "end": v(614.38, -62.16) * mm});
            skLineSegment(sketch, "E4270", {"start": v(614.38, -62.16) * mm, "end": v(615.83, -61.98) * mm});
            skLineSegment(sketch, "E4271", {"start": v(615.83, -61.98) * mm, "end": v(617.4, -61.82) * mm});
            skLineSegment(sketch, "E4272", {"start": v(617.4, -61.82) * mm, "end": v(619.04, -61.67) * mm});
            skLineSegment(sketch, "E4273", {"start": v(619.04, -61.67) * mm, "end": v(620.75, -61.5) * mm});
            skLineSegment(sketch, "E4274", {"start": v(620.75, -61.5) * mm, "end": v(622.51, -61.33) * mm});
            skLineSegment(sketch, "E4275", {"start": v(622.51, -61.33) * mm, "end": v(624.3, -61.13) * mm});
            skLineSegment(sketch, "E4276", {"start": v(624.3, -61.13) * mm, "end": v(626.1, -60.88) * mm});
            skLineSegment(sketch, "E4277", {"start": v(626.1, -60.88) * mm, "end": v(627.88, -60.58) * mm});
            skLineSegment(sketch, "E4278", {"start": v(627.88, -60.58) * mm, "end": v(629.64, -60.22) * mm});
            skLineSegment(sketch, "E4279", {"start": v(629.64, -60.22) * mm, "end": v(631.35, -59.77) * mm});
            skLineSegment(sketch, "E4280", {"start": v(631.35, -59.77) * mm, "end": v(633, -59.24) * mm});
            skLineSegment(sketch, "E4281", {"start": v(633, -59.24) * mm, "end": v(634.55, -58.6) * mm});
            skLineSegment(sketch, "E4282", {"start": v(634.55, -58.6) * mm, "end": v(636, -57.84) * mm});
            skLineSegment(sketch, "E4283", {"start": v(636, -57.84) * mm, "end": v(637.33, -56.95) * mm});
            skLineSegment(sketch, "E4284", {"start": v(637.33, -56.95) * mm, "end": v(638.52, -55.93) * mm});
            skLineSegment(sketch, "E4285", {"start": v(638.52, -55.93) * mm, "end": v(639.54, -54.75) * mm});
            skLineSegment(sketch, "E4286", {"start": v(639.54, -54.75) * mm, "end": v(640.38, -53.4) * mm});
            skLineSegment(sketch, "E4287", {"start": v(640.38, -53.4) * mm, "end": v(641.03, -51.87) * mm});
            skLineSegment(sketch, "E4288", {"start": v(641.03, -51.87) * mm, "end": v(641.48, -50.45) * mm});
            skLineSegment(sketch, "E4289", {"start": v(641.48, -50.45) * mm, "end": v(641.86, -49.07) * mm});
            skLineSegment(sketch, "E4290", {"start": v(641.86, -49.07) * mm, "end": v(642.2, -47.74) * mm});
            skLineSegment(sketch, "E4291", {"start": v(642.2, -47.74) * mm, "end": v(642.46, -46.45) * mm});
            skLineSegment(sketch, "E4292", {"start": v(642.46, -46.45) * mm, "end": v(642.67, -45.2) * mm});
            skLineSegment(sketch, "E4293", {"start": v(642.67, -45.2) * mm, "end": v(642.83, -44) * mm});
            skLineSegment(sketch, "E4294", {"start": v(642.83, -44) * mm, "end": v(642.93, -42.83) * mm});
            skLineSegment(sketch, "E4295", {"start": v(642.93, -42.83) * mm, "end": v(642.97, -41.7) * mm});
            skLineSegment(sketch, "E4296", {"start": v(642.97, -41.7) * mm, "end": v(642.97, -40.62) * mm});
            skLineSegment(sketch, "E4297", {"start": v(642.97, -40.62) * mm, "end": v(642.91, -39.56) * mm});
            skLineSegment(sketch, "E4298", {"start": v(642.91, -39.56) * mm, "end": v(642.8, -38.55) * mm});
            skLineSegment(sketch, "E4299", {"start": v(642.8, -38.55) * mm, "end": v(642.65, -37.57) * mm});
            skLineSegment(sketch, "E4300", {"start": v(642.65, -37.57) * mm, "end": v(642.45, -36.63) * mm});
            skLineSegment(sketch, "E4301", {"start": v(642.45, -36.63) * mm, "end": v(642.2, -35.72) * mm});
            skLineSegment(sketch, "E4302", {"start": v(642.2, -35.72) * mm, "end": v(641.9, -34.84) * mm});
            skLineSegment(sketch, "E4303", {"start": v(641.9, -34.84) * mm, "end": v(641.56, -34) * mm});
            skLineSegment(sketch, "E4304", {"start": v(641.56, -34) * mm, "end": v(641.18, -33.18) * mm});
            skLineSegment(sketch, "E4305", {"start": v(641.18, -33.18) * mm, "end": v(640.76, -32.4) * mm});
            skLineSegment(sketch, "E4306", {"start": v(640.76, -32.4) * mm, "end": v(640.3, -31.64) * mm});
            skLineSegment(sketch, "E4307", {"start": v(640.3, -31.64) * mm, "end": v(639.8, -30.9) * mm});
            skLineSegment(sketch, "E4308", {"start": v(639.8, -30.9) * mm, "end": v(639.25, -30.2) * mm});
            skLineSegment(sketch, "E4309", {"start": v(639.25, -30.2) * mm, "end": v(638.68, -29.52) * mm});
            skLineSegment(sketch, "E4310", {"start": v(638.68, -29.52) * mm, "end": v(638.07, -28.87) * mm});
            skLineSegment(sketch, "E4311", {"start": v(638.07, -28.87) * mm, "end": v(637.42, -28.24) * mm});
            skLineSegment(sketch, "E4312", {"start": v(637.42, -28.24) * mm, "end": v(636.74, -27.63) * mm});
            skLineSegment(sketch, "E4313", {"start": v(636.74, -27.63) * mm, "end": v(636.03, -27.04) * mm});
            skLineSegment(sketch, "E4314", {"start": v(636.03, -27.04) * mm, "end": v(635.3, -26.48) * mm});
            skLineSegment(sketch, "E4315", {"start": v(635.3, -26.48) * mm, "end": v(634.52, -25.93) * mm});
            skLineSegment(sketch, "E4316", {"start": v(634.52, -25.93) * mm, "end": v(633.73, -25.4) * mm});
            skLineSegment(sketch, "E4317", {"start": v(633.73, -25.4) * mm, "end": v(632.9, -24.89) * mm});
            skLineSegment(sketch, "E4318", {"start": v(632.9, -24.89) * mm, "end": v(632.05, -24.4) * mm});
            skLineSegment(sketch, "E4319", {"start": v(632.05, -24.4) * mm, "end": v(631.18, -23.91) * mm});
            skLineSegment(sketch, "E4320", {"start": v(631.18, -23.91) * mm, "end": v(630.28, -23.45) * mm});
            skLineSegment(sketch, "E4321", {"start": v(630.28, -23.45) * mm, "end": v(629.36, -23) * mm});
            skLineSegment(sketch, "E4322", {"start": v(629.36, -23) * mm, "end": v(628.42, -22.56) * mm});
            skLineSegment(sketch, "E4323", {"start": v(628.42, -22.56) * mm, "end": v(627.47, -22.13) * mm});
            skLineSegment(sketch, "E4324", {"start": v(627.47, -22.13) * mm, "end": v(626.49, -21.7) * mm});
            skLineSegment(sketch, "E4325", {"start": v(626.49, -21.7) * mm, "end": v(625.5, -21.3) * mm});
            skLineSegment(sketch, "E4326", {"start": v(625.5, -21.3) * mm, "end": v(624.49, -20.9) * mm});
            skLineSegment(sketch, "E4327", {"start": v(624.49, -20.9) * mm, "end": v(623.46, -20.5) * mm});
            skLineSegment(sketch, "E4328", {"start": v(623.46, -20.5) * mm, "end": v(622.43, -20.12) * mm});
            skLineSegment(sketch, "E4329", {"start": v(622.43, -20.12) * mm, "end": v(621.38, -19.74) * mm});
            skLineSegment(sketch, "E4330", {"start": v(621.38, -19.74) * mm, "end": v(620.32, -19.36) * mm});
            skLineSegment(sketch, "E4331", {"start": v(620.32, -19.36) * mm, "end": v(619.25, -18.99) * mm});
            skLineSegment(sketch, "E4332", {"start": v(619.25, -18.99) * mm, "end": v(618.17, -18.61) * mm});
            skLineSegment(sketch, "E4333", {"start": v(618.17, -18.61) * mm, "end": v(617.09, -18.24) * mm});
            skLineSegment(sketch, "E4334", {"start": v(617.09, -18.24) * mm, "end": v(616, -17.87) * mm});
            skLineSegment(sketch, "E4335", {"start": v(616, -17.87) * mm, "end": v(614.9, -17.5) * mm});
            skLineSegment(sketch, "E4336", {"start": v(614.9, -17.5) * mm, "end": v(613.8, -17.13) * mm});
            skLineSegment(sketch, "E4337", {"start": v(613.8, -17.13) * mm, "end": v(612.7, -16.75) * mm});
            skLineSegment(sketch, "E4338", {"start": v(612.7, -16.75) * mm, "end": v(611.6, -16.37) * mm});
            skLineSegment(sketch, "E4339", {"start": v(611.6, -16.37) * mm, "end": v(610.5, -15.99) * mm});
            skLineSegment(sketch, "E4340", {"start": v(610.5, -15.99) * mm, "end": v(609.4, -15.6) * mm});
            skLineSegment(sketch, "E4341", {"start": v(609.4, -15.6) * mm, "end": v(608.3, -15.2) * mm});
            skLineSegment(sketch, "E4342", {"start": v(608.3, -15.2) * mm, "end": v(607.22, -14.8) * mm});
            skLineSegment(sketch, "E4343", {"start": v(607.22, -14.8) * mm, "end": v(606.13, -14.38) * mm});
            skLineSegment(sketch, "E4344", {"start": v(606.13, -14.38) * mm, "end": v(605.05, -13.96) * mm});
            skLineSegment(sketch, "E4345", {"start": v(605.05, -13.96) * mm, "end": v(603.97, -13.52) * mm});
            skLineSegment(sketch, "E4346", {"start": v(603.97, -13.52) * mm, "end": v(602.91, -13.08) * mm});
            skLineSegment(sketch, "E4347", {"start": v(602.91, -13.08) * mm, "end": v(601.86, -12.62) * mm});
            skLineSegment(sketch, "E4348", {"start": v(601.86, -12.62) * mm, "end": v(600.81, -12.14) * mm});
            skLineSegment(sketch, "E4349", {"start": v(600.81, -12.14) * mm, "end": v(599.78, -11.65) * mm});
            skLineSegment(sketch, "E4350", {"start": v(599.78, -11.65) * mm, "end": v(598.77, -11.15) * mm});
            skLineSegment(sketch, "E4351", {"start": v(598.77, -11.15) * mm, "end": v(597.77, -10.63) * mm});
            skLineSegment(sketch, "E4352", {"start": v(597.77, -10.63) * mm, "end": v(596.78, -10.1) * mm});
            skLineSegment(sketch, "E4353", {"start": v(596.78, -10.1) * mm, "end": v(595.82, -9.53) * mm});
            skLineSegment(sketch, "E4354", {"start": v(595.82, -9.53) * mm, "end": v(594.87, -8.96) * mm});
            skLineSegment(sketch, "E4355", {"start": v(594.87, -8.96) * mm, "end": v(593.94, -8.36) * mm});
            skLineSegment(sketch, "E4356", {"start": v(593.94, -8.36) * mm, "end": v(593.03, -7.74) * mm});
            skLineSegment(sketch, "E4357", {"start": v(593.03, -7.74) * mm, "end": v(592.15, -7.1) * mm});
            skLineSegment(sketch, "E4358", {"start": v(592.15, -7.1) * mm, "end": v(591.29, -6.43) * mm});
            skLineSegment(sketch, "E4359", {"start": v(591.29, -6.43) * mm, "end": v(590.45, -5.73) * mm});
            skLineSegment(sketch, "E4360", {"start": v(590.45, -5.73) * mm, "end": v(589.64, -5.01) * mm});
            skLineSegment(sketch, "E4361", {"start": v(589.64, -5.01) * mm, "end": v(588.86, -4.27) * mm});
            skLineSegment(sketch, "E4362", {"start": v(588.86, -4.27) * mm, "end": v(588.1, -3.5) * mm});
            skLineSegment(sketch, "E4363", {"start": v(588.1, -3.5) * mm, "end": v(587.38, -2.7) * mm});
            skLineSegment(sketch, "E4364", {"start": v(587.38, -2.7) * mm, "end": v(586.68, -1.86) * mm});
            skLineSegment(sketch, "E4365", {"start": v(586.68, -1.86) * mm, "end": v(586.02, -1) * mm});
            skLineSegment(sketch, "E4366", {"start": v(586.02, -1) * mm, "end": v(585.4, -0.1) * mm});
            skLineSegment(sketch, "E4367", {"start": v(585.4, -0.1) * mm, "end": v(584.8, 0.83) * mm});
            skLineSegment(sketch, "E4368", {"start": v(584.8, 0.83) * mm, "end": v(584.24, 1.79) * mm});
            skLineSegment(sketch, "E4369", {"start": v(584.24, 1.79) * mm, "end": v(583.72, 2.79) * mm});
            skLineSegment(sketch, "E4370", {"start": v(583.72, 2.79) * mm, "end": v(583.24, 3.82) * mm});
            skLineSegment(sketch, "E4371", {"start": v(583.24, 3.82) * mm, "end": v(582.8, 4.9) * mm});
            skLineSegment(sketch, "E4372", {"start": v(582.8, 4.9) * mm, "end": v(582.4, 6) * mm});
            skLineSegment(sketch, "E4373", {"start": v(582.4, 6) * mm, "end": v(582.04, 7.15) * mm});
            skLineSegment(sketch, "E4374", {"start": v(582.04, 7.15) * mm, "end": v(581.72, 8.34) * mm});
            skLineSegment(sketch, "E4375", {"start": v(581.72, 8.34) * mm, "end": v(581.45, 9.56) * mm});
            skLineSegment(sketch, "E4376", {"start": v(581.45, 9.56) * mm, "end": v(581.23, 10.84) * mm});
            skLineSegment(sketch, "E4377", {"start": v(581.23, 10.84) * mm, "end": v(581.05, 12.15) * mm});
            skLineSegment(sketch, "E4378", {"start": v(581.05, 12.15) * mm, "end": v(580.92, 13.5) * mm});
            skLineSegment(sketch, "E4379", {"start": v(580.92, 13.5) * mm, "end": v(580.84, 14.91) * mm});
            skLineSegment(sketch, "E4380", {"start": v(580.84, 14.91) * mm, "end": v(580.83, 16.7) * mm});
            skLineSegment(sketch, "E4381", {"start": v(580.83, 16.7) * mm, "end": v(580.92, 18.45) * mm});
            skLineSegment(sketch, "E4382", {"start": v(580.92, 18.45) * mm, "end": v(581.13, 20.18) * mm});
            skLineSegment(sketch, "E4383", {"start": v(581.13, 20.18) * mm, "end": v(581.44, 21.87) * mm});
            skLineSegment(sketch, "E4384", {"start": v(581.44, 21.87) * mm, "end": v(581.85, 23.52) * mm});
            skLineSegment(sketch, "E4385", {"start": v(581.85, 23.52) * mm, "end": v(582.36, 25.14) * mm});
            skLineSegment(sketch, "E4386", {"start": v(582.36, 25.14) * mm, "end": v(582.95, 26.72) * mm});
            skLineSegment(sketch, "E4387", {"start": v(582.95, 26.72) * mm, "end": v(583.64, 28.27) * mm});
            skLineSegment(sketch, "E4388", {"start": v(583.64, 28.27) * mm, "end": v(584.4, 29.78) * mm});
            skLineSegment(sketch, "E4389", {"start": v(584.4, 29.78) * mm, "end": v(585.25, 31.25) * mm});
            skLineSegment(sketch, "E4390", {"start": v(585.25, 31.25) * mm, "end": v(586.17, 32.67) * mm});
            skLineSegment(sketch, "E4391", {"start": v(586.17, 32.67) * mm, "end": v(587.16, 34.06) * mm});
            skLineSegment(sketch, "E4392", {"start": v(587.16, 34.06) * mm, "end": v(588.22, 35.4) * mm});
            skLineSegment(sketch, "E4393", {"start": v(588.22, 35.4) * mm, "end": v(589.35, 36.7) * mm});
            skLineSegment(sketch, "E4394", {"start": v(589.35, 36.7) * mm, "end": v(590.53, 37.96) * mm});
            skLineSegment(sketch, "E4395", {"start": v(590.53, 37.96) * mm, "end": v(591.77, 39.17) * mm});
            skLineSegment(sketch, "E4396", {"start": v(591.77, 39.17) * mm, "end": v(593.05, 40.34) * mm});
            skLineSegment(sketch, "E4397", {"start": v(593.05, 40.34) * mm, "end": v(594.39, 41.45) * mm});
            skLineSegment(sketch, "E4398", {"start": v(594.39, 41.45) * mm, "end": v(595.76, 42.52) * mm});
            skLineSegment(sketch, "E4399", {"start": v(595.76, 42.52) * mm, "end": v(597.18, 43.55) * mm});
            skLineSegment(sketch, "E4400", {"start": v(597.18, 43.55) * mm, "end": v(598.63, 44.52) * mm});
            skLineSegment(sketch, "E4401", {"start": v(598.63, 44.52) * mm, "end": v(600.11, 45.44) * mm});
            skLineSegment(sketch, "E4402", {"start": v(600.11, 45.44) * mm, "end": v(601.62, 46.3) * mm});
            skLineSegment(sketch, "E4403", {"start": v(601.62, 46.3) * mm, "end": v(603.15, 47.12) * mm});
            skLineSegment(sketch, "E4404", {"start": v(603.15, 47.12) * mm, "end": v(604.7, 47.88) * mm});
            skLineSegment(sketch, "E4405", {"start": v(604.7, 47.88) * mm, "end": v(606.26, 48.58) * mm});
            skLineSegment(sketch, "E4406", {"start": v(606.26, 48.58) * mm, "end": v(607.83, 49.23) * mm});
            skLineSegment(sketch, "E4407", {"start": v(607.83, 49.23) * mm, "end": v(609.4, 49.83) * mm});
            skLineSegment(sketch, "E4408", {"start": v(609.4, 49.83) * mm, "end": v(610.99, 50.36) * mm});
            skLineSegment(sketch, "E4409", {"start": v(610.99, 50.36) * mm, "end": v(612.57, 50.84) * mm});
            skLineSegment(sketch, "E4410", {"start": v(612.57, 50.84) * mm, "end": v(614.1, 51.26) * mm});
            skLineSegment(sketch, "E4411", {"start": v(614.1, 51.26) * mm, "end": v(615.68, 51.68) * mm});
            skLineSegment(sketch, "E4412", {"start": v(615.68, 51.68) * mm, "end": v(617.28, 52.1) * mm});
            skLineSegment(sketch, "E4413", {"start": v(617.28, 52.1) * mm, "end": v(618.9, 52.51) * mm});
            skLineSegment(sketch, "E4414", {"start": v(618.9, 52.51) * mm, "end": v(620.54, 52.95) * mm});
            skLineSegment(sketch, "E4415", {"start": v(620.54, 52.95) * mm, "end": v(622.18, 53.4) * mm});
            skLineSegment(sketch, "E4416", {"start": v(622.18, 53.4) * mm, "end": v(623.81, 53.9) * mm});
            skLineSegment(sketch, "E4417", {"start": v(623.81, 53.9) * mm, "end": v(625.43, 54.41) * mm});
            skLineSegment(sketch, "E4418", {"start": v(625.43, 54.41) * mm, "end": v(627.01, 54.98) * mm});
            skLineSegment(sketch, "E4419", {"start": v(627.01, 54.98) * mm, "end": v(628.57, 55.59) * mm});
            skLineSegment(sketch, "E4420", {"start": v(628.57, 55.59) * mm, "end": v(630.07, 56.25) * mm});
            skLineSegment(sketch, "E4421", {"start": v(630.07, 56.25) * mm, "end": v(631.53, 56.98) * mm});
            skLineSegment(sketch, "E4422", {"start": v(631.53, 56.98) * mm, "end": v(632.92, 57.77) * mm});
            skLineSegment(sketch, "E4423", {"start": v(632.92, 57.77) * mm, "end": v(634.24, 58.64) * mm});
            skLineSegment(sketch, "E4424", {"start": v(634.24, 58.64) * mm, "end": v(635.48, 59.6) * mm});
            skLineSegment(sketch, "E4425", {"start": v(635.48, 59.6) * mm, "end": v(636.62, 60.64) * mm});
            skLineSegment(sketch, "E4426", {"start": v(636.62, 60.64) * mm, "end": v(637.67, 61.78) * mm});
            skLineSegment(sketch, "E4427", {"start": v(637.67, 61.78) * mm, "end": v(638.6, 63.03) * mm});
            skLineSegment(sketch, "E4428", {"start": v(638.6, 63.03) * mm, "end": v(639.42, 64.38) * mm});
            skLineSegment(sketch, "E4429", {"start": v(639.42, 64.38) * mm, "end": v(640.1, 65.85) * mm});
            skLineSegment(sketch, "E4430", {"start": v(640.1, 65.85) * mm, "end": v(640.66, 67.44) * mm});
            skLineSegment(sketch, "E4431", {"start": v(640.66, 67.44) * mm, "end": v(641.06, 69.17) * mm});
            skLineSegment(sketch, "E4432", {"start": v(641.06, 69.17) * mm, "end": v(641.3, 71.03) * mm});
            skLineSegment(sketch, "E4433", {"start": v(641.3, 71.03) * mm, "end": v(641.4, 72.5) * mm});
            skLineSegment(sketch, "E4434", {"start": v(641.4, 72.5) * mm, "end": v(641.4, 73.9) * mm});
            skLineSegment(sketch, "E4435", {"start": v(641.4, 73.9) * mm, "end": v(641.34, 75.24) * mm});
            skLineSegment(sketch, "E4436", {"start": v(641.34, 75.24) * mm, "end": v(641.2, 76.52) * mm});
            skLineSegment(sketch, "E4437", {"start": v(641.2, 76.52) * mm, "end": v(641, 77.73) * mm});
            skLineSegment(sketch, "E4438", {"start": v(641, 77.73) * mm, "end": v(640.72, 78.89) * mm});
            skLineSegment(sketch, "E4439", {"start": v(640.72, 78.89) * mm, "end": v(640.38, 79.99) * mm});
            skLineSegment(sketch, "E4440", {"start": v(640.38, 79.99) * mm, "end": v(639.97, 81.03) * mm});
            skLineSegment(sketch, "E4441", {"start": v(639.97, 81.03) * mm, "end": v(639.5, 82.02) * mm});
            skLineSegment(sketch, "E4442", {"start": v(639.5, 82.02) * mm, "end": v(638.96, 82.96) * mm});
            skLineSegment(sketch, "E4443", {"start": v(638.96, 82.96) * mm, "end": v(638.36, 83.86) * mm});
            skLineSegment(sketch, "E4444", {"start": v(638.36, 83.86) * mm, "end": v(637.71, 84.7) * mm});
            skLineSegment(sketch, "E4445", {"start": v(637.71, 84.7) * mm, "end": v(637, 85.5) * mm});
            skLineSegment(sketch, "E4446", {"start": v(637, 85.5) * mm, "end": v(636.25, 86.25) * mm});
            skLineSegment(sketch, "E4447", {"start": v(636.25, 86.25) * mm, "end": v(635.43, 86.96) * mm});
            skLineSegment(sketch, "E4448", {"start": v(635.43, 86.96) * mm, "end": v(634.57, 87.63) * mm});
            skLineSegment(sketch, "E4449", {"start": v(634.57, 87.63) * mm, "end": v(633.66, 88.26) * mm});
            skLineSegment(sketch, "E4450", {"start": v(633.66, 88.26) * mm, "end": v(632.71, 88.86) * mm});
            skLineSegment(sketch, "E4451", {"start": v(632.71, 88.86) * mm, "end": v(631.71, 89.42) * mm});
            skLineSegment(sketch, "E4452", {"start": v(631.71, 89.42) * mm, "end": v(630.68, 89.95) * mm});
            skLineSegment(sketch, "E4453", {"start": v(630.68, 89.95) * mm, "end": v(629.6, 90.45) * mm});
            skLineSegment(sketch, "E4454", {"start": v(629.6, 90.45) * mm, "end": v(628.49, 90.91) * mm});
            skLineSegment(sketch, "E4455", {"start": v(628.49, 90.91) * mm, "end": v(627.34, 91.35) * mm});
            skLineSegment(sketch, "E4456", {"start": v(627.34, 91.35) * mm, "end": v(626.15, 91.77) * mm});
            skLineSegment(sketch, "E4457", {"start": v(626.15, 91.77) * mm, "end": v(624.94, 92.16) * mm});
            skLineSegment(sketch, "E4458", {"start": v(624.94, 92.16) * mm, "end": v(623.7, 92.53) * mm});
            skLineSegment(sketch, "E4459", {"start": v(623.7, 92.53) * mm, "end": v(622.42, 92.88) * mm});
            skLineSegment(sketch, "E4460", {"start": v(622.42, 92.88) * mm, "end": v(621.13, 93.2) * mm});
            skLineSegment(sketch, "E4461", {"start": v(621.13, 93.2) * mm, "end": v(619.81, 93.52) * mm});
            skLineSegment(sketch, "E4462", {"start": v(619.81, 93.52) * mm, "end": v(618.47, 93.82) * mm});
            skLineSegment(sketch, "E4463", {"start": v(618.47, 93.82) * mm, "end": v(617.11, 94.11) * mm});
            skLineSegment(sketch, "E4464", {"start": v(617.11, 94.11) * mm, "end": v(615.73, 94.39) * mm});
            skLineSegment(sketch, "E4465", {"start": v(615.73, 94.39) * mm, "end": v(614.34, 94.66) * mm});
            skLineSegment(sketch, "E4466", {"start": v(614.34, 94.66) * mm, "end": v(612.94, 94.92) * mm});
            skLineSegment(sketch, "E4467", {"start": v(612.94, 94.92) * mm, "end": v(611.52, 95.17) * mm});
            skLineSegment(sketch, "E4468", {"start": v(611.52, 95.17) * mm, "end": v(610.1, 95.42) * mm});
            skLineSegment(sketch, "E4469", {"start": v(610.1, 95.42) * mm, "end": v(608.67, 95.67) * mm});
            skLineSegment(sketch, "E4470", {"start": v(608.67, 95.67) * mm, "end": v(607.23, 95.93) * mm});
            skLineSegment(sketch, "E4471", {"start": v(607.23, 95.93) * mm, "end": v(605.79, 96.18) * mm});
            skLineSegment(sketch, "E4472", {"start": v(605.79, 96.18) * mm, "end": v(604.35, 96.43) * mm});
            skLineSegment(sketch, "E4473", {"start": v(604.35, 96.43) * mm, "end": v(602.9, 96.7) * mm});
            skLineSegment(sketch, "E4474", {"start": v(602.9, 96.7) * mm, "end": v(601.47, 96.97) * mm});
            skLineSegment(sketch, "E4475", {"start": v(601.47, 96.97) * mm, "end": v(600.03, 97.25) * mm});
            skLineSegment(sketch, "E4476", {"start": v(600.03, 97.25) * mm, "end": v(598.6, 97.54) * mm});
            skLineSegment(sketch, "E4477", {"start": v(598.6, 97.54) * mm, "end": v(597.2, 97.84) * mm});
            skLineSegment(sketch, "E4478", {"start": v(597.2, 97.84) * mm, "end": v(595.79, 98.16) * mm});
            skLineSegment(sketch, "E4479", {"start": v(595.79, 98.16) * mm, "end": v(594.4, 98.5) * mm});
            skLineSegment(sketch, "E4480", {"start": v(594.4, 98.5) * mm, "end": v(593.02, 98.85) * mm});
            skLineSegment(sketch, "E4481", {"start": v(593.02, 98.85) * mm, "end": v(591.65, 99.22) * mm});
            skLineSegment(sketch, "E4482", {"start": v(591.65, 99.22) * mm, "end": v(590.31, 99.62) * mm});
            skLineSegment(sketch, "E4483", {"start": v(590.31, 99.62) * mm, "end": v(589, 100.04) * mm});
            skLineSegment(sketch, "E4484", {"start": v(589, 100.04) * mm, "end": v(587.7, 100.49) * mm});
            skLineSegment(sketch, "E4485", {"start": v(587.7, 100.49) * mm, "end": v(586.42, 100.96) * mm});
            skLineSegment(sketch, "E4486", {"start": v(586.42, 100.96) * mm, "end": v(585.17, 101.47) * mm});
            skLineSegment(sketch, "E4487", {"start": v(585.17, 101.47) * mm, "end": v(583.96, 102) * mm});
            skLineSegment(sketch, "E4488", {"start": v(583.96, 102) * mm, "end": v(582.77, 102.57) * mm});
            skLineSegment(sketch, "E4489", {"start": v(582.77, 102.57) * mm, "end": v(581.62, 103.18) * mm});
            skLineSegment(sketch, "E4490", {"start": v(581.62, 103.18) * mm, "end": v(580.5, 103.82) * mm});
            skLineSegment(sketch, "E4491", {"start": v(580.5, 103.82) * mm, "end": v(579.42, 104.5) * mm});
            skLineSegment(sketch, "E4492", {"start": v(579.42, 104.5) * mm, "end": v(578.37, 105.22) * mm});
            skLineSegment(sketch, "E4493", {"start": v(578.37, 105.22) * mm, "end": v(577.37, 105.98) * mm});
            skLineSegment(sketch, "E4494", {"start": v(577.37, 105.98) * mm, "end": v(576.42, 106.8) * mm});
            skLineSegment(sketch, "E4495", {"start": v(576.42, 106.8) * mm, "end": v(575.5, 107.65) * mm});
            skLineSegment(sketch, "E4496", {"start": v(575.5, 107.65) * mm, "end": v(574.64, 108.55) * mm});
            skLineSegment(sketch, "E4497", {"start": v(574.64, 108.55) * mm, "end": v(573.82, 109.5) * mm});
            skLineSegment(sketch, "E4498", {"start": v(573.82, 109.5) * mm, "end": v(573.05, 110.5) * mm});
            skLineSegment(sketch, "E4499", {"start": v(573.05, 110.5) * mm, "end": v(572.34, 111.56) * mm});
            skLineSegment(sketch, "E4500", {"start": v(572.34, 111.56) * mm, "end": v(571.68, 112.68) * mm});
            skLineSegment(sketch, "E4501", {"start": v(571.68, 112.68) * mm, "end": v(570.92, 114.11) * mm});
            skLineSegment(sketch, "E4502", {"start": v(570.92, 114.11) * mm, "end": v(570.22, 115.52) * mm});
            skLineSegment(sketch, "E4503", {"start": v(570.22, 115.52) * mm, "end": v(569.6, 116.9) * mm});
            skLineSegment(sketch, "E4504", {"start": v(569.6, 116.9) * mm, "end": v(569.04, 118.24) * mm});
            skLineSegment(sketch, "E4505", {"start": v(569.04, 118.24) * mm, "end": v(568.55, 119.56) * mm});
            skLineSegment(sketch, "E4506", {"start": v(568.55, 119.56) * mm, "end": v(568.12, 120.85) * mm});
            skLineSegment(sketch, "E4507", {"start": v(568.12, 120.85) * mm, "end": v(567.76, 122.1) * mm});
            skLineSegment(sketch, "E4508", {"start": v(567.76, 122.1) * mm, "end": v(567.45, 123.34) * mm});
            skLineSegment(sketch, "E4509", {"start": v(567.45, 123.34) * mm, "end": v(567.2, 124.55) * mm});
            skLineSegment(sketch, "E4510", {"start": v(567.2, 124.55) * mm, "end": v(567.02, 125.73) * mm});
            skLineSegment(sketch, "E4511", {"start": v(567.02, 125.73) * mm, "end": v(566.9, 126.9) * mm});
            skLineSegment(sketch, "E4512", {"start": v(566.9, 126.9) * mm, "end": v(566.83, 128.02) * mm});
            skLineSegment(sketch, "E4513", {"start": v(566.83, 128.02) * mm, "end": v(566.81, 129.13) * mm});
            skLineSegment(sketch, "E4514", {"start": v(566.81, 129.13) * mm, "end": v(566.85, 130.22) * mm});
            skLineSegment(sketch, "E4515", {"start": v(566.85, 130.22) * mm, "end": v(566.94, 131.28) * mm});
            skLineSegment(sketch, "E4516", {"start": v(566.94, 131.28) * mm, "end": v(567.07, 132.32) * mm});
            skLineSegment(sketch, "E4517", {"start": v(567.07, 132.32) * mm, "end": v(567.26, 133.34) * mm});
            skLineSegment(sketch, "E4518", {"start": v(567.26, 133.34) * mm, "end": v(567.5, 134.34) * mm});
            skLineSegment(sketch, "E4519", {"start": v(567.5, 134.34) * mm, "end": v(567.77, 135.31) * mm});
            skLineSegment(sketch, "E4520", {"start": v(567.77, 135.31) * mm, "end": v(568.1, 136.27) * mm});
            skLineSegment(sketch, "E4521", {"start": v(568.1, 136.27) * mm, "end": v(568.47, 137.2) * mm});
            skLineSegment(sketch, "E4522", {"start": v(568.47, 137.2) * mm, "end": v(568.88, 138.13) * mm});
            skLineSegment(sketch, "E4523", {"start": v(568.88, 138.13) * mm, "end": v(569.32, 139.03) * mm});
            skLineSegment(sketch, "E4524", {"start": v(569.32, 139.03) * mm, "end": v(569.81, 139.91) * mm});
            skLineSegment(sketch, "E4525", {"start": v(569.81, 139.91) * mm, "end": v(570.34, 140.78) * mm});
            skLineSegment(sketch, "E4526", {"start": v(570.34, 140.78) * mm, "end": v(570.9, 141.63) * mm});
            skLineSegment(sketch, "E4527", {"start": v(570.9, 141.63) * mm, "end": v(571.5, 142.46) * mm});
            skLineSegment(sketch, "E4528", {"start": v(571.5, 142.46) * mm, "end": v(572.12, 143.28) * mm});
            skLineSegment(sketch, "E4529", {"start": v(572.12, 143.28) * mm, "end": v(572.78, 144.09) * mm});
            skLineSegment(sketch, "E4530", {"start": v(572.78, 144.09) * mm, "end": v(573.47, 144.88) * mm});
            skLineSegment(sketch, "E4531", {"start": v(573.47, 144.88) * mm, "end": v(574.19, 145.66) * mm});
            skLineSegment(sketch, "E4532", {"start": v(574.19, 145.66) * mm, "end": v(574.93, 146.42) * mm});
            skLineSegment(sketch, "E4533", {"start": v(574.93, 146.42) * mm, "end": v(575.7, 147.18) * mm});
            skLineSegment(sketch, "E4534", {"start": v(575.7, 147.18) * mm, "end": v(576.5, 147.92) * mm});
            skLineSegment(sketch, "E4535", {"start": v(576.5, 147.92) * mm, "end": v(577.32, 148.65) * mm});
            skLineSegment(sketch, "E4536", {"start": v(577.32, 148.65) * mm, "end": v(578.16, 149.37) * mm});
            skLineSegment(sketch, "E4537", {"start": v(578.16, 149.37) * mm, "end": v(579.02, 150.08) * mm});
            skLineSegment(sketch, "E4538", {"start": v(579.02, 150.08) * mm, "end": v(579.9, 150.79) * mm});
            skLineSegment(sketch, "E4539", {"start": v(579.9, 150.79) * mm, "end": v(580.79, 151.48) * mm});
            skLineSegment(sketch, "E4540", {"start": v(580.79, 151.48) * mm, "end": v(581.7, 152.17) * mm});
            skLineSegment(sketch, "E4541", {"start": v(581.7, 152.17) * mm, "end": v(582.63, 152.84) * mm});
            skLineSegment(sketch, "E4542", {"start": v(582.63, 152.84) * mm, "end": v(583.56, 153.52) * mm});
            skLineSegment(sketch, "E4543", {"start": v(583.56, 153.52) * mm, "end": v(584.51, 154.18) * mm});
            skLineSegment(sketch, "E4544", {"start": v(584.51, 154.18) * mm, "end": v(585.47, 154.84) * mm});
            skLineSegment(sketch, "E4545", {"start": v(585.47, 154.84) * mm, "end": v(586.44, 155.5) * mm});
            skLineSegment(sketch, "E4546", {"start": v(586.44, 155.5) * mm, "end": v(587.41, 156.15) * mm});
            skLineSegment(sketch, "E4547", {"start": v(587.41, 156.15) * mm, "end": v(588.4, 156.8) * mm});
            skLineSegment(sketch, "E4548", {"start": v(588.4, 156.8) * mm, "end": v(589.38, 157.44) * mm});
            skLineSegment(sketch, "E4549", {"start": v(589.38, 157.44) * mm, "end": v(590.36, 158.08) * mm});
            skLineSegment(sketch, "E4550", {"start": v(590.36, 158.08) * mm, "end": v(591.35, 158.72) * mm});
            skLineSegment(sketch, "E4551", {"start": v(591.35, 158.72) * mm, "end": v(592.34, 159.36) * mm});
            skLineSegment(sketch, "E4552", {"start": v(592.34, 159.36) * mm, "end": v(593.33, 160) * mm});
            skLineSegment(sketch, "E4553", {"start": v(593.33, 160) * mm, "end": v(594.31, 160.64) * mm});
            skLineSegment(sketch, "E4554", {"start": v(594.31, 160.64) * mm, "end": v(595.29, 161.28) * mm});
            skLineSegment(sketch, "E4555", {"start": v(595.29, 161.28) * mm, "end": v(596.26, 161.92) * mm});
            skLineSegment(sketch, "E4556", {"start": v(596.26, 161.92) * mm, "end": v(597.23, 162.56) * mm});
            skLineSegment(sketch, "E4557", {"start": v(597.23, 162.56) * mm, "end": v(598.19, 163.2) * mm});
            skLineSegment(sketch, "E4558", {"start": v(598.19, 163.2) * mm, "end": v(599.13, 163.85) * mm});
            skLineSegment(sketch, "E4559", {"start": v(599.13, 163.85) * mm, "end": v(600.07, 164.5) * mm});
            skLineSegment(sketch, "E4560", {"start": v(600.07, 164.5) * mm, "end": v(601, 165.15) * mm});
            skLineSegment(sketch, "E4561", {"start": v(601, 165.15) * mm, "end": v(601.9, 165.81) * mm});
            skLineSegment(sketch, "E4562", {"start": v(601.9, 165.81) * mm, "end": v(602.79, 166.48) * mm});
            skLineSegment(sketch, "E4563", {"start": v(602.79, 166.48) * mm, "end": v(603.66, 167.15) * mm});
            skLineSegment(sketch, "E4564", {"start": v(603.66, 167.15) * mm, "end": v(604.52, 167.82) * mm});
            skLineSegment(sketch, "E4565", {"start": v(604.52, 167.82) * mm, "end": v(605.35, 168.5) * mm});
            skLineSegment(sketch, "E4566", {"start": v(605.35, 168.5) * mm, "end": v(606.17, 169.2) * mm});
            skLineSegment(sketch, "E4567", {"start": v(606.17, 169.2) * mm, "end": v(606.96, 169.9) * mm});
            skLineSegment(sketch, "E4568", {"start": v(606.96, 169.9) * mm, "end": v(607.72, 170.6) * mm});
            skLineSegment(sketch, "E4569", {"start": v(607.72, 170.6) * mm, "end": v(608.46, 171.33) * mm});
            skLineSegment(sketch, "E4570", {"start": v(608.46, 171.33) * mm, "end": v(609.18, 172.06) * mm});
            skLineSegment(sketch, "E4571", {"start": v(609.18, 172.06) * mm, "end": v(609.86, 172.8) * mm});
            skLineSegment(sketch, "E4572", {"start": v(609.86, 172.8) * mm, "end": v(610.51, 173.54) * mm});
            skLineSegment(sketch, "E4573", {"start": v(610.51, 173.54) * mm, "end": v(611.13, 174.3) * mm});
            skLineSegment(sketch, "E4574", {"start": v(611.13, 174.3) * mm, "end": v(611.72, 175.08) * mm});
            skLineSegment(sketch, "E4575", {"start": v(611.72, 175.08) * mm, "end": v(612.27, 175.87) * mm});
            skLineSegment(sketch, "E4576", {"start": v(612.27, 175.87) * mm, "end": v(612.8, 176.67) * mm});
            skLineSegment(sketch, "E4577", {"start": v(612.8, 176.67) * mm, "end": v(613.27, 177.49) * mm});
            skLineSegment(sketch, "E4578", {"start": v(613.27, 177.49) * mm, "end": v(613.71, 178.32) * mm});
            skLineSegment(sketch, "E4579", {"start": v(613.71, 178.32) * mm, "end": v(614.11, 179.16) * mm});
            skLineSegment(sketch, "E4580", {"start": v(614.11, 179.16) * mm, "end": v(614.47, 180.03) * mm});
            skLineSegment(sketch, "E4581", {"start": v(614.47, 180.03) * mm, "end": v(614.79, 180.9) * mm});
            skLineSegment(sketch, "E4582", {"start": v(614.79, 180.9) * mm, "end": v(615.06, 181.8) * mm});
            skLineSegment(sketch, "E4583", {"start": v(615.06, 181.8) * mm, "end": v(615.28, 182.72) * mm});
            skLineSegment(sketch, "E4584", {"start": v(615.28, 182.72) * mm, "end": v(615.46, 183.65) * mm});
            skLineSegment(sketch, "E4585", {"start": v(615.46, 183.65) * mm, "end": v(615.59, 184.6) * mm});
            skLineSegment(sketch, "E4586", {"start": v(615.59, 184.6) * mm, "end": v(615.66, 185.57) * mm});
            skLineSegment(sketch, "E4587", {"start": v(615.66, 185.57) * mm, "end": v(615.7, 186.56) * mm});
            skLineSegment(sketch, "E4588", {"start": v(615.7, 186.56) * mm, "end": v(615.66, 187.58) * mm});
            skLineSegment(sketch, "E4589", {"start": v(615.66, 187.58) * mm, "end": v(615.58, 188.61) * mm});
            skLineSegment(sketch, "E4590", {"start": v(615.58, 188.61) * mm, "end": v(615.44, 189.67) * mm});
            skLineSegment(sketch, "E4591", {"start": v(615.44, 189.67) * mm, "end": v(615.25, 190.75) * mm});
            skLineSegment(sketch, "E4592", {"start": v(615.25, 190.75) * mm, "end": v(614.99, 191.85) * mm});
            skLineSegment(sketch, "E4593", {"start": v(614.99, 191.85) * mm, "end": v(614.67, 192.97) * mm});
            skLineSegment(sketch, "E4594", {"start": v(614.67, 192.97) * mm, "end": v(614.3, 194.12) * mm});
            skLineSegment(sketch, "E4595", {"start": v(614.3, 194.12) * mm, "end": v(613.58, 195.92) * mm});
            skLineSegment(sketch, "E4596", {"start": v(613.58, 195.92) * mm, "end": v(612.78, 197.54) * mm});
            skLineSegment(sketch, "E4597", {"start": v(612.78, 197.54) * mm, "end": v(611.89, 198.98) * mm});
            skLineSegment(sketch, "E4598", {"start": v(611.89, 198.98) * mm, "end": v(610.91, 200.26) * mm});
            skLineSegment(sketch, "E4599", {"start": v(610.91, 200.26) * mm, "end": v(609.86, 201.38) * mm});
            skLineSegment(sketch, "E4600", {"start": v(609.86, 201.38) * mm, "end": v(608.73, 202.36) * mm});
            skLineSegment(sketch, "E4601", {"start": v(608.73, 202.36) * mm, "end": v(607.54, 203.19) * mm});
            skLineSegment(sketch, "E4602", {"start": v(607.54, 203.19) * mm, "end": v(606.28, 203.9) * mm});
            skLineSegment(sketch, "E4603", {"start": v(606.28, 203.9) * mm, "end": v(604.96, 204.47) * mm});
            skLineSegment(sketch, "E4604", {"start": v(604.96, 204.47) * mm, "end": v(603.6, 204.94) * mm});
            skLineSegment(sketch, "E4605", {"start": v(603.6, 204.94) * mm, "end": v(602.17, 205.3) * mm});
            skLineSegment(sketch, "E4606", {"start": v(602.17, 205.3) * mm, "end": v(600.7, 205.56) * mm});
            skLineSegment(sketch, "E4607", {"start": v(600.7, 205.56) * mm, "end": v(599.2, 205.73) * mm});
            skLineSegment(sketch, "E4608", {"start": v(599.2, 205.73) * mm, "end": v(597.67, 205.82) * mm});
            skLineSegment(sketch, "E4609", {"start": v(597.67, 205.82) * mm, "end": v(596.1, 205.84) * mm});
            skLineSegment(sketch, "E4610", {"start": v(596.1, 205.84) * mm, "end": v(594.5, 205.8) * mm});
            skLineSegment(sketch, "E4611", {"start": v(594.5, 205.8) * mm, "end": v(592.88, 205.7) * mm});
            skLineSegment(sketch, "E4612", {"start": v(592.88, 205.7) * mm, "end": v(591.25, 205.55) * mm});
            skLineSegment(sketch, "E4613", {"start": v(591.25, 205.55) * mm, "end": v(589.6, 205.36) * mm});
            skLineSegment(sketch, "E4614", {"start": v(589.6, 205.36) * mm, "end": v(587.96, 205.15) * mm});
            skLineSegment(sketch, "E4615", {"start": v(587.96, 205.15) * mm, "end": v(586.3, 204.9) * mm});
            skLineSegment(sketch, "E4616", {"start": v(586.3, 204.9) * mm, "end": v(584.65, 204.66) * mm});
            skLineSegment(sketch, "E4617", {"start": v(584.65, 204.66) * mm, "end": v(583.01, 204.4) * mm});
            skLineSegment(sketch, "E4618", {"start": v(583.01, 204.4) * mm, "end": v(581.38, 204.15) * mm});
            skLineSegment(sketch, "E4619", {"start": v(581.38, 204.15) * mm, "end": v(579.77, 203.9) * mm});
            skLineSegment(sketch, "E4620", {"start": v(579.77, 203.9) * mm, "end": v(578.18, 203.68) * mm});
            skLineSegment(sketch, "E4621", {"start": v(578.18, 203.68) * mm, "end": v(576.37, 203.47) * mm});
            skLineSegment(sketch, "E4622", {"start": v(576.37, 203.47) * mm, "end": v(574.57, 203.3) * mm});
            skLineSegment(sketch, "E4623", {"start": v(574.57, 203.3) * mm, "end": v(572.79, 203.2) * mm});
            skLineSegment(sketch, "E4624", {"start": v(572.79, 203.2) * mm, "end": v(571.01, 203.15) * mm});
            skLineSegment(sketch, "E4625", {"start": v(571.01, 203.15) * mm, "end": v(569.25, 203.16) * mm});
            skLineSegment(sketch, "E4626", {"start": v(569.25, 203.16) * mm, "end": v(567.5, 203.22) * mm});
            skLineSegment(sketch, "E4627", {"start": v(567.5, 203.22) * mm, "end": v(565.77, 203.35) * mm});
            skLineSegment(sketch, "E4628", {"start": v(565.77, 203.35) * mm, "end": v(564.06, 203.54) * mm});
            skLineSegment(sketch, "E4629", {"start": v(564.06, 203.54) * mm, "end": v(562.37, 203.8) * mm});
            skLineSegment(sketch, "E4630", {"start": v(562.37, 203.8) * mm, "end": v(560.7, 204.1) * mm});
            skLineSegment(sketch, "E4631", {"start": v(560.7, 204.1) * mm, "end": v(559.07, 204.5) * mm});
            skLineSegment(sketch, "E4632", {"start": v(559.07, 204.5) * mm, "end": v(557.45, 204.95) * mm});
            skLineSegment(sketch, "E4633", {"start": v(557.45, 204.95) * mm, "end": v(555.86, 205.48) * mm});
            skLineSegment(sketch, "E4634", {"start": v(555.86, 205.48) * mm, "end": v(554.3, 206.07) * mm});
            skLineSegment(sketch, "E4635", {"start": v(554.3, 206.07) * mm, "end": v(552.78, 206.75) * mm});
            skLineSegment(sketch, "E4636", {"start": v(552.78, 206.75) * mm, "end": v(551.29, 207.5) * mm});
            skLineSegment(sketch, "E4637", {"start": v(551.29, 207.5) * mm, "end": v(549.83, 208.32) * mm});
            skLineSegment(sketch, "E4638", {"start": v(549.83, 208.32) * mm, "end": v(548.4, 209.22) * mm});
            skLineSegment(sketch, "E4639", {"start": v(548.4, 209.22) * mm, "end": v(547.03, 210.2) * mm});
            skLineSegment(sketch, "E4640", {"start": v(547.03, 210.2) * mm, "end": v(545.69, 211.27) * mm});
            skLineSegment(sketch, "E4641", {"start": v(545.69, 211.27) * mm, "end": v(544.4, 212.42) * mm});
            skLineSegment(sketch, "E4642", {"start": v(544.4, 212.42) * mm, "end": v(543.14, 213.66) * mm});
            skLineSegment(sketch, "E4643", {"start": v(543.14, 213.66) * mm, "end": v(541.93, 214.98) * mm});
            skLineSegment(sketch, "E4644", {"start": v(541.93, 214.98) * mm, "end": v(540.77, 216.39) * mm});
            skLineSegment(sketch, "E4645", {"start": v(540.77, 216.39) * mm, "end": v(539.66, 217.9) * mm});
            skLineSegment(sketch, "E4646", {"start": v(539.66, 217.9) * mm, "end": v(538.6, 219.48) * mm});
            skLineSegment(sketch, "E4647", {"start": v(-24.67, 199.57) * mm, "end": v(-22.86, 199.56) * mm});
            skLineSegment(sketch, "E4648", {"start": v(-22.86, 199.56) * mm, "end": v(-21.05, 199.55) * mm});
            skLineSegment(sketch, "E4649", {"start": v(-21.05, 199.55) * mm, "end": v(-19.24, 199.54) * mm});
            skLineSegment(sketch, "E4650", {"start": v(-19.24, 199.54) * mm, "end": v(-17.43, 199.53) * mm});
            skLineSegment(sketch, "E4651", {"start": v(-17.43, 199.53) * mm, "end": v(-15.62, 199.52) * mm});
            skLineSegment(sketch, "E4652", {"start": v(-15.62, 199.52) * mm, "end": v(-13.81, 199.5) * mm});
            skLineSegment(sketch, "E4653", {"start": v(-13.81, 199.5) * mm, "end": v(-12, 199.5) * mm});
            skLineSegment(sketch, "E4654", {"start": v(-12, 199.5) * mm, "end": v(-10.19, 199.49) * mm});
            skLineSegment(sketch, "E4655", {"start": v(-10.19, 199.49) * mm, "end": v(-8.38, 199.48) * mm});
            skLineSegment(sketch, "E4656", {"start": v(-8.38, 199.48) * mm, "end": v(-6.57, 199.47) * mm});
            skLineSegment(sketch, "E4657", {"start": v(-6.57, 199.47) * mm, "end": v(-4.76, 199.47) * mm});
            skLineSegment(sketch, "E4658", {"start": v(-4.76, 199.47) * mm, "end": v(-2.95, 199.46) * mm});
            skLineSegment(sketch, "E4659", {"start": v(-2.95, 199.46) * mm, "end": v(-1.14, 199.45) * mm});
            skLineSegment(sketch, "E4660", {"start": v(-1.14, 199.45) * mm, "end": v(0.68, 199.45) * mm});
            skLineSegment(sketch, "E4661", {"start": v(0.68, 199.45) * mm, "end": v(2.49, 199.45) * mm});
            skLineSegment(sketch, "E4662", {"start": v(2.49, 199.45) * mm, "end": v(4.3, 199.45) * mm});
            skLineSegment(sketch, "E4663", {"start": v(4.3, 199.45) * mm, "end": v(6.1, 199.45) * mm});
            skLineSegment(sketch, "E4664", {"start": v(6.1, 199.45) * mm, "end": v(7.92, 199.45) * mm});
            skLineSegment(sketch, "E4665", {"start": v(7.92, 199.45) * mm, "end": v(9.73, 199.45) * mm});
            skLineSegment(sketch, "E4666", {"start": v(9.73, 199.45) * mm, "end": v(11.54, 199.45) * mm});
            skLineSegment(sketch, "E4667", {"start": v(11.54, 199.45) * mm, "end": v(13.35, 199.46) * mm});
            skLineSegment(sketch, "E4668", {"start": v(13.35, 199.46) * mm, "end": v(15.16, 199.47) * mm});
            skLineSegment(sketch, "E4669", {"start": v(15.16, 199.47) * mm, "end": v(16.97, 199.48) * mm});
            skLineSegment(sketch, "E4670", {"start": v(16.97, 199.48) * mm, "end": v(18.78, 199.5) * mm});
            skLineSegment(sketch, "E4671", {"start": v(18.78, 199.5) * mm, "end": v(20.6, 199.5) * mm});
            skLineSegment(sketch, "E4672", {"start": v(20.6, 199.5) * mm, "end": v(22.4, 199.53) * mm});
            skLineSegment(sketch, "E4673", {"start": v(22.4, 199.53) * mm, "end": v(24.21, 199.55) * mm});
            skLineSegment(sketch, "E4674", {"start": v(24.21, 199.55) * mm, "end": v(26.02, 199.57) * mm});
            skLineSegment(sketch, "E4675", {"start": v(26.02, 199.57) * mm, "end": v(27.66, 199.6) * mm});
            skLineSegment(sketch, "E4676", {"start": v(27.66, 199.6) * mm, "end": v(29.38, 199.65) * mm});
            skLineSegment(sketch, "E4677", {"start": v(29.38, 199.65) * mm, "end": v(31.14, 199.75) * mm});
            skLineSegment(sketch, "E4678", {"start": v(31.14, 199.75) * mm, "end": v(32.9, 199.93) * mm});
            skLineSegment(sketch, "E4679", {"start": v(32.9, 199.93) * mm, "end": v(34.66, 200.22) * mm});
            skLineSegment(sketch, "E4680", {"start": v(34.66, 200.22) * mm, "end": v(36.35, 200.63) * mm});
            skLineSegment(sketch, "E4681", {"start": v(36.35, 200.63) * mm, "end": v(37.95, 201.2) * mm});
            skLineSegment(sketch, "E4682", {"start": v(37.95, 201.2) * mm, "end": v(39.44, 201.93) * mm});
            skLineSegment(sketch, "E4683", {"start": v(39.44, 201.93) * mm, "end": v(40.77, 202.88) * mm});
            skLineSegment(sketch, "E4684", {"start": v(40.77, 202.88) * mm, "end": v(41.92, 204.05) * mm});
            skLineSegment(sketch, "E4685", {"start": v(41.92, 204.05) * mm, "end": v(42.86, 205.48) * mm});
            skLineSegment(sketch, "E4686", {"start": v(42.86, 205.48) * mm, "end": v(43.55, 207.2) * mm});
            skLineSegment(sketch, "E4687", {"start": v(43.55, 207.2) * mm, "end": v(43.97, 208.8) * mm});
            skLineSegment(sketch, "E4688", {"start": v(43.97, 208.8) * mm, "end": v(44.3, 210.46) * mm});
            skLineSegment(sketch, "E4689", {"start": v(44.3, 210.46) * mm, "end": v(44.57, 212.17) * mm});
            skLineSegment(sketch, "E4690", {"start": v(44.57, 212.17) * mm, "end": v(44.75, 213.93) * mm});
            skLineSegment(sketch, "E4691", {"start": v(44.75, 213.93) * mm, "end": v(44.88, 215.73) * mm});
            skLineSegment(sketch, "E4692", {"start": v(44.88, 215.73) * mm, "end": v(44.94, 217.56) * mm});
            skLineSegment(sketch, "E4693", {"start": v(44.94, 217.56) * mm, "end": v(44.96, 219.4) * mm});
            skLineSegment(sketch, "E4694", {"start": v(44.96, 219.4) * mm, "end": v(44.94, 221.28) * mm});
            skLineSegment(sketch, "E4695", {"start": v(44.94, 221.28) * mm, "end": v(44.89, 223.15) * mm});
            skLineSegment(sketch, "E4696", {"start": v(44.89, 223.15) * mm, "end": v(44.8, 225.04) * mm});
            skLineSegment(sketch, "E4697", {"start": v(44.8, 225.04) * mm, "end": v(44.7, 226.91) * mm});
            skLineSegment(sketch, "E4698", {"start": v(44.7, 226.91) * mm, "end": v(44.6, 228.78) * mm});
            skLineSegment(sketch, "E4699", {"start": v(44.6, 228.78) * mm, "end": v(44.48, 230.63) * mm});
            skLineSegment(sketch, "E4700", {"start": v(44.48, 230.63) * mm, "end": v(44.37, 232.46) * mm});
            skLineSegment(sketch, "E4701", {"start": v(44.37, 232.46) * mm, "end": v(44.28, 234.26) * mm});
            skLineSegment(sketch, "E4702", {"start": v(44.28, 234.26) * mm, "end": v(44.2, 236.02) * mm});
            skLineSegment(sketch, "E4703", {"start": v(44.2, 236.02) * mm, "end": v(44.14, 237.73) * mm});
            skLineSegment(sketch, "E4704", {"start": v(44.14, 237.73) * mm, "end": v(44.12, 239.4) * mm});
            skLineSegment(sketch, "E4705", {"start": v(44.12, 239.4) * mm, "end": v(44.13, 241.12) * mm});
            skLineSegment(sketch, "E4706", {"start": v(44.13, 241.12) * mm, "end": v(44.15, 242.87) * mm});
            skLineSegment(sketch, "E4707", {"start": v(44.15, 242.87) * mm, "end": v(44.19, 244.64) * mm});
            skLineSegment(sketch, "E4708", {"start": v(44.19, 244.64) * mm, "end": v(44.24, 246.41) * mm});
            skLineSegment(sketch, "E4709", {"start": v(44.24, 246.41) * mm, "end": v(44.3, 248.2) * mm});
            skLineSegment(sketch, "E4710", {"start": v(44.3, 248.2) * mm, "end": v(44.36, 250) * mm});
            skLineSegment(sketch, "E4711", {"start": v(44.36, 250) * mm, "end": v(44.44, 251.81) * mm});
            skLineSegment(sketch, "E4712", {"start": v(44.44, 251.81) * mm, "end": v(44.52, 253.63) * mm});
            skLineSegment(sketch, "E4713", {"start": v(44.52, 253.63) * mm, "end": v(44.6, 255.46) * mm});
            skLineSegment(sketch, "E4714", {"start": v(44.6, 255.46) * mm, "end": v(44.7, 257.3) * mm});
            skLineSegment(sketch, "E4715", {"start": v(44.7, 257.3) * mm, "end": v(44.79, 259.14) * mm});
            skLineSegment(sketch, "E4716", {"start": v(44.79, 259.14) * mm, "end": v(44.88, 261) * mm});
            skLineSegment(sketch, "E4717", {"start": v(44.88, 261) * mm, "end": v(44.97, 262.84) * mm});
            skLineSegment(sketch, "E4718", {"start": v(44.97, 262.84) * mm, "end": v(45.06, 264.7) * mm});
            skLineSegment(sketch, "E4719", {"start": v(45.06, 264.7) * mm, "end": v(45.14, 266.56) * mm});
            skLineSegment(sketch, "E4720", {"start": v(45.14, 266.56) * mm, "end": v(45.21, 268.42) * mm});
            skLineSegment(sketch, "E4721", {"start": v(45.21, 268.42) * mm, "end": v(45.28, 270.28) * mm});
            skLineSegment(sketch, "E4722", {"start": v(45.28, 270.28) * mm, "end": v(45.35, 272.14) * mm});
            skLineSegment(sketch, "E4723", {"start": v(45.35, 272.14) * mm, "end": v(45.4, 274) * mm});
            skLineSegment(sketch, "E4724", {"start": v(45.4, 274) * mm, "end": v(45.44, 275.86) * mm});
            skLineSegment(sketch, "E4725", {"start": v(45.44, 275.86) * mm, "end": v(45.46, 277.71) * mm});
            skLineSegment(sketch, "E4726", {"start": v(45.46, 277.71) * mm, "end": v(45.47, 279.56) * mm});
            skLineSegment(sketch, "E4727", {"start": v(45.47, 279.56) * mm, "end": v(45.47, 281.4) * mm});
            skLineSegment(sketch, "E4728", {"start": v(45.47, 281.4) * mm, "end": v(45.45, 283.24) * mm});
            skLineSegment(sketch, "E4729", {"start": v(45.45, 283.24) * mm, "end": v(45.4, 285.07) * mm});
            skLineSegment(sketch, "E4730", {"start": v(45.4, 285.07) * mm, "end": v(45.34, 286.9) * mm});
            skLineSegment(sketch, "E4731", {"start": v(45.34, 286.9) * mm, "end": v(45.26, 288.7) * mm});
            skLineSegment(sketch, "E4732", {"start": v(45.26, 288.7) * mm, "end": v(45.15, 290.5) * mm});
            skLineSegment(sketch, "E4733", {"start": v(45.15, 290.5) * mm, "end": v(45.02, 292.3) * mm});
            skLineSegment(sketch, "E4734", {"start": v(45.02, 292.3) * mm, "end": v(44.86, 294.08) * mm});
            skLineSegment(sketch, "E4735", {"start": v(44.86, 294.08) * mm, "end": v(44.68, 295.84) * mm});
            skLineSegment(sketch, "E4736", {"start": v(44.68, 295.84) * mm, "end": v(44.46, 297.6) * mm});
            skLineSegment(sketch, "E4737", {"start": v(44.46, 297.6) * mm, "end": v(44.22, 299.33) * mm});
            skLineSegment(sketch, "E4738", {"start": v(44.22, 299.33) * mm, "end": v(43.94, 301.05) * mm});
            skLineSegment(sketch, "E4739", {"start": v(43.94, 301.05) * mm, "end": v(43.63, 302.75) * mm});
            skLineSegment(sketch, "E4740", {"start": v(43.63, 302.75) * mm, "end": v(43.21, 304.45) * mm});
            skLineSegment(sketch, "E4741", {"start": v(43.21, 304.45) * mm, "end": v(42.66, 306.1) * mm});
            skLineSegment(sketch, "E4742", {"start": v(42.66, 306.1) * mm, "end": v(42, 307.69) * mm});
            skLineSegment(sketch, "E4743", {"start": v(42, 307.69) * mm, "end": v(41.24, 309.25) * mm});
            skLineSegment(sketch, "E4744", {"start": v(41.24, 309.25) * mm, "end": v(40.43, 310.79) * mm});
            skLineSegment(sketch, "E4745", {"start": v(40.43, 310.79) * mm, "end": v(39.59, 312.31) * mm});
            skLineSegment(sketch, "E4746", {"start": v(39.59, 312.31) * mm, "end": v(38.74, 313.83) * mm});
            skLineSegment(sketch, "E4747", {"start": v(38.74, 313.83) * mm, "end": v(37.92, 315.36) * mm});
            skLineSegment(sketch, "E4748", {"start": v(37.92, 315.36) * mm, "end": v(37.14, 316.9) * mm});
            skLineSegment(sketch, "E4749", {"start": v(37.14, 316.9) * mm, "end": v(36.44, 318.47) * mm});
            skLineSegment(sketch, "E4750", {"start": v(36.44, 318.47) * mm, "end": v(35.84, 320.07) * mm});
            skLineSegment(sketch, "E4751", {"start": v(35.84, 320.07) * mm, "end": v(35.37, 321.73) * mm});
            skLineSegment(sketch, "E4752", {"start": v(35.37, 321.73) * mm, "end": v(35.06, 323.43) * mm});
            skLineSegment(sketch, "E4753", {"start": v(35.06, 323.43) * mm, "end": v(34.85, 325.15) * mm});
            skLineSegment(sketch, "E4754", {"start": v(34.85, 325.15) * mm, "end": v(34.67, 326.87) * mm});
            skLineSegment(sketch, "E4755", {"start": v(34.67, 326.87) * mm, "end": v(34.52, 328.6) * mm});
            skLineSegment(sketch, "E4756", {"start": v(34.52, 328.6) * mm, "end": v(34.4, 330.34) * mm});
            skLineSegment(sketch, "E4757", {"start": v(34.4, 330.34) * mm, "end": v(34.3, 332.09) * mm});
            skLineSegment(sketch, "E4758", {"start": v(34.3, 332.09) * mm, "end": v(34.23, 333.84) * mm});
            skLineSegment(sketch, "E4759", {"start": v(34.23, 333.84) * mm, "end": v(34.18, 335.6) * mm});
            skLineSegment(sketch, "E4760", {"start": v(34.18, 335.6) * mm, "end": v(34.16, 337.37) * mm});
            skLineSegment(sketch, "E4761", {"start": v(34.16, 337.37) * mm, "end": v(34.16, 339.14) * mm});
            skLineSegment(sketch, "E4762", {"start": v(34.16, 339.14) * mm, "end": v(34.18, 340.92) * mm});
            skLineSegment(sketch, "E4763", {"start": v(34.18, 340.92) * mm, "end": v(34.22, 342.71) * mm});
            skLineSegment(sketch, "E4764", {"start": v(34.22, 342.71) * mm, "end": v(34.29, 344.5) * mm});
            skLineSegment(sketch, "E4765", {"start": v(34.29, 344.5) * mm, "end": v(34.37, 346.3) * mm});
            skLineSegment(sketch, "E4766", {"start": v(34.37, 346.3) * mm, "end": v(34.47, 348.1) * mm});
            skLineSegment(sketch, "E4767", {"start": v(34.47, 348.1) * mm, "end": v(34.59, 349.9) * mm});
            skLineSegment(sketch, "E4768", {"start": v(34.59, 349.9) * mm, "end": v(34.72, 351.72) * mm});
            skLineSegment(sketch, "E4769", {"start": v(34.72, 351.72) * mm, "end": v(34.87, 353.53) * mm});
            skLineSegment(sketch, "E4770", {"start": v(34.87, 353.53) * mm, "end": v(35.04, 355.35) * mm});
            skLineSegment(sketch, "E4771", {"start": v(35.04, 355.35) * mm, "end": v(35.22, 357.18) * mm});
            skLineSegment(sketch, "E4772", {"start": v(35.22, 357.18) * mm, "end": v(35.41, 359) * mm});
            skLineSegment(sketch, "E4773", {"start": v(35.41, 359) * mm, "end": v(35.62, 360.83) * mm});
            skLineSegment(sketch, "E4774", {"start": v(35.62, 360.83) * mm, "end": v(35.83, 362.66) * mm});
            skLineSegment(sketch, "E4775", {"start": v(35.83, 362.66) * mm, "end": v(36.06, 364.5) * mm});
            skLineSegment(sketch, "E4776", {"start": v(36.06, 364.5) * mm, "end": v(36.3, 366.33) * mm});
            skLineSegment(sketch, "E4777", {"start": v(36.3, 366.33) * mm, "end": v(36.55, 368.16) * mm});
            skLineSegment(sketch, "E4778", {"start": v(36.55, 368.16) * mm, "end": v(36.8, 370) * mm});
            skLineSegment(sketch, "E4779", {"start": v(36.8, 370) * mm, "end": v(37.07, 371.83) * mm});
            skLineSegment(sketch, "E4780", {"start": v(37.07, 371.83) * mm, "end": v(37.34, 373.67) * mm});
            skLineSegment(sketch, "E4781", {"start": v(37.34, 373.67) * mm, "end": v(37.61, 375.51) * mm});
            skLineSegment(sketch, "E4782", {"start": v(37.61, 375.51) * mm, "end": v(37.9, 377.35) * mm});
            skLineSegment(sketch, "E4783", {"start": v(37.9, 377.35) * mm, "end": v(38.18, 379.19) * mm});
            skLineSegment(sketch, "E4784", {"start": v(38.18, 379.19) * mm, "end": v(38.46, 381.02) * mm});
            skLineSegment(sketch, "E4785", {"start": v(38.46, 381.02) * mm, "end": v(38.75, 382.86) * mm});
            skLineSegment(sketch, "E4786", {"start": v(38.75, 382.86) * mm, "end": v(39.04, 384.7) * mm});
            skLineSegment(sketch, "E4787", {"start": v(39.04, 384.7) * mm, "end": v(39.33, 386.52) * mm});
            skLineSegment(sketch, "E4788", {"start": v(39.33, 386.52) * mm, "end": v(39.63, 388.35) * mm});
            skLineSegment(sketch, "E4789", {"start": v(39.63, 388.35) * mm, "end": v(39.92, 390.18) * mm});
            skLineSegment(sketch, "E4790", {"start": v(39.92, 390.18) * mm, "end": v(40.2, 392) * mm});
            skLineSegment(sketch, "E4791", {"start": v(40.2, 392) * mm, "end": v(40.49, 393.83) * mm});
            skLineSegment(sketch, "E4792", {"start": v(40.49, 393.83) * mm, "end": v(40.77, 395.65) * mm});
            skLineSegment(sketch, "E4793", {"start": v(40.77, 395.65) * mm, "end": v(41.05, 397.47) * mm});
            skLineSegment(sketch, "E4794", {"start": v(41.05, 397.47) * mm, "end": v(41.32, 399.28) * mm});
            skLineSegment(sketch, "E4795", {"start": v(41.32, 399.28) * mm, "end": v(41.58, 401.08) * mm});
            skLineSegment(sketch, "E4796", {"start": v(41.58, 401.08) * mm, "end": v(41.84, 402.89) * mm});
            skLineSegment(sketch, "E4797", {"start": v(41.84, 402.89) * mm, "end": v(42.09, 404.68) * mm});
            skLineSegment(sketch, "E4798", {"start": v(42.09, 404.68) * mm, "end": v(42.33, 406.48) * mm});
            skLineSegment(sketch, "E4799", {"start": v(42.33, 406.48) * mm, "end": v(42.56, 408.26) * mm});
            skLineSegment(sketch, "E4800", {"start": v(42.56, 408.26) * mm, "end": v(42.78, 410.04) * mm});
            skLineSegment(sketch, "E4801", {"start": v(42.78, 410.04) * mm, "end": v(42.99, 411.82) * mm});
            skLineSegment(sketch, "E4802", {"start": v(42.99, 411.82) * mm, "end": v(43.19, 413.59) * mm});
            skLineSegment(sketch, "E4803", {"start": v(43.19, 413.59) * mm, "end": v(43.37, 415.35) * mm});
            skLineSegment(sketch, "E4804", {"start": v(43.37, 415.35) * mm, "end": v(43.54, 417.1) * mm});
            skLineSegment(sketch, "E4805", {"start": v(43.54, 417.1) * mm, "end": v(43.7, 418.85) * mm});
            skLineSegment(sketch, "E4806", {"start": v(43.7, 418.85) * mm, "end": v(43.83, 420.6) * mm});
            skLineSegment(sketch, "E4807", {"start": v(43.83, 420.6) * mm, "end": v(43.95, 422.32) * mm});
            skLineSegment(sketch, "E4808", {"start": v(43.95, 422.32) * mm, "end": v(44.06, 424.04) * mm});
            skLineSegment(sketch, "E4809", {"start": v(44.06, 424.04) * mm, "end": v(44.15, 425.48) * mm});
            skLineSegment(sketch, "E4810", {"start": v(44.15, 425.48) * mm, "end": v(44.27, 426.96) * mm});
            skLineSegment(sketch, "E4811", {"start": v(44.27, 426.96) * mm, "end": v(44.42, 428.47) * mm});
            skLineSegment(sketch, "E4812", {"start": v(44.42, 428.47) * mm, "end": v(44.58, 430.01) * mm});
            skLineSegment(sketch, "E4813", {"start": v(44.58, 430.01) * mm, "end": v(44.76, 431.58) * mm});
            skLineSegment(sketch, "E4814", {"start": v(44.76, 431.58) * mm, "end": v(44.96, 433.18) * mm});
            skLineSegment(sketch, "E4815", {"start": v(44.96, 433.18) * mm, "end": v(45.17, 434.8) * mm});
            skLineSegment(sketch, "E4816", {"start": v(45.17, 434.8) * mm, "end": v(45.39, 436.45) * mm});
            skLineSegment(sketch, "E4817", {"start": v(45.39, 436.45) * mm, "end": v(45.62, 438.12) * mm});
            skLineSegment(sketch, "E4818", {"start": v(45.62, 438.12) * mm, "end": v(45.84, 439.8) * mm});
            skLineSegment(sketch, "E4819", {"start": v(45.84, 439.8) * mm, "end": v(46.07, 441.5) * mm});
            skLineSegment(sketch, "E4820", {"start": v(46.07, 441.5) * mm, "end": v(46.3, 443.22) * mm});
            skLineSegment(sketch, "E4821", {"start": v(46.3, 443.22) * mm, "end": v(46.53, 444.95) * mm});
            skLineSegment(sketch, "E4822", {"start": v(46.53, 444.95) * mm, "end": v(46.74, 446.7) * mm});
            skLineSegment(sketch, "E4823", {"start": v(46.74, 446.7) * mm, "end": v(46.94, 448.44) * mm});
            skLineSegment(sketch, "E4824", {"start": v(46.94, 448.44) * mm, "end": v(47.13, 450.2) * mm});
            skLineSegment(sketch, "E4825", {"start": v(47.13, 450.2) * mm, "end": v(47.3, 451.95) * mm});
            skLineSegment(sketch, "E4826", {"start": v(47.3, 451.95) * mm, "end": v(47.46, 453.7) * mm});
            skLineSegment(sketch, "E4827", {"start": v(47.46, 453.7) * mm, "end": v(47.6, 455.46) * mm});
            skLineSegment(sketch, "E4828", {"start": v(47.6, 455.46) * mm, "end": v(47.7, 457.21) * mm});
            skLineSegment(sketch, "E4829", {"start": v(47.7, 457.21) * mm, "end": v(47.78, 458.96) * mm});
            skLineSegment(sketch, "E4830", {"start": v(47.78, 458.96) * mm, "end": v(47.83, 460.7) * mm});
            skLineSegment(sketch, "E4831", {"start": v(47.83, 460.7) * mm, "end": v(47.84, 462.43) * mm});
            skLineSegment(sketch, "E4832", {"start": v(47.84, 462.43) * mm, "end": v(47.82, 464.15) * mm});
            skLineSegment(sketch, "E4833", {"start": v(47.82, 464.15) * mm, "end": v(47.75, 465.85) * mm});
            skLineSegment(sketch, "E4834", {"start": v(47.75, 465.85) * mm, "end": v(47.65, 467.54) * mm});
            skLineSegment(sketch, "E4835", {"start": v(47.65, 467.54) * mm, "end": v(47.5, 469.21) * mm});
            skLineSegment(sketch, "E4836", {"start": v(47.5, 469.21) * mm, "end": v(47.3, 470.86) * mm});
            skLineSegment(sketch, "E4837", {"start": v(47.3, 470.86) * mm, "end": v(47.05, 472.5) * mm});
            skLineSegment(sketch, "E4838", {"start": v(47.05, 472.5) * mm, "end": v(46.74, 474.1) * mm});
            skLineSegment(sketch, "E4839", {"start": v(46.74, 474.1) * mm, "end": v(46.38, 475.67) * mm});
            skLineSegment(sketch, "E4840", {"start": v(46.38, 475.67) * mm, "end": v(45.96, 477.21) * mm});
            skLineSegment(sketch, "E4841", {"start": v(45.96, 477.21) * mm, "end": v(45.47, 478.73) * mm});
            skLineSegment(sketch, "E4842", {"start": v(45.47, 478.73) * mm, "end": v(44.92, 480.2) * mm});
            skLineSegment(sketch, "E4843", {"start": v(44.92, 480.2) * mm, "end": v(44.3, 481.65) * mm});
            skLineSegment(sketch, "E4844", {"start": v(44.3, 481.65) * mm, "end": v(43.62, 483.06) * mm});
            skLineSegment(sketch, "E4845", {"start": v(43.62, 483.06) * mm, "end": v(42.85, 484.43) * mm});
            skLineSegment(sketch, "E4846", {"start": v(42.85, 484.43) * mm, "end": v(42.01, 485.75) * mm});
            skLineSegment(sketch, "E4847", {"start": v(42.01, 485.75) * mm, "end": v(41.09, 487.03) * mm});
            skLineSegment(sketch, "E4848", {"start": v(41.09, 487.03) * mm, "end": v(40.08, 488.26) * mm});
            skLineSegment(sketch, "E4849", {"start": v(40.08, 488.26) * mm, "end": v(39, 489.45) * mm});
            skLineSegment(sketch, "E4850", {"start": v(39, 489.45) * mm, "end": v(37.82, 490.58) * mm});
            skLineSegment(sketch, "E4851", {"start": v(37.82, 490.58) * mm, "end": v(36.55, 491.66) * mm});
            skLineSegment(sketch, "E4852", {"start": v(36.55, 491.66) * mm, "end": v(35.18, 492.7) * mm});
            skLineSegment(sketch, "E4853", {"start": v(35.18, 492.7) * mm, "end": v(33.77, 493.62) * mm});
            skLineSegment(sketch, "E4854", {"start": v(33.77, 493.62) * mm, "end": v(32.34, 494.45) * mm});
            skLineSegment(sketch, "E4855", {"start": v(32.34, 494.45) * mm, "end": v(30.87, 495.19) * mm});
            skLineSegment(sketch, "E4856", {"start": v(30.87, 495.19) * mm, "end": v(29.38, 495.83) * mm});
            skLineSegment(sketch, "E4857", {"start": v(29.38, 495.83) * mm, "end": v(27.87, 496.38) * mm});
            skLineSegment(sketch, "E4858", {"start": v(27.87, 496.38) * mm, "end": v(26.34, 496.83) * mm});
            skLineSegment(sketch, "E4859", {"start": v(26.34, 496.83) * mm, "end": v(24.79, 497.2) * mm});
            skLineSegment(sketch, "E4860", {"start": v(24.79, 497.2) * mm, "end": v(23.23, 497.47) * mm});
            skLineSegment(sketch, "E4861", {"start": v(23.23, 497.47) * mm, "end": v(21.66, 497.65) * mm});
            skLineSegment(sketch, "E4862", {"start": v(21.66, 497.65) * mm, "end": v(20.1, 497.75) * mm});
            skLineSegment(sketch, "E4863", {"start": v(20.1, 497.75) * mm, "end": v(18.52, 497.76) * mm});
            skLineSegment(sketch, "E4864", {"start": v(18.52, 497.76) * mm, "end": v(16.95, 497.7) * mm});
            skLineSegment(sketch, "E4865", {"start": v(16.95, 497.7) * mm, "end": v(15.4, 497.54) * mm});
            skLineSegment(sketch, "E4866", {"start": v(15.4, 497.54) * mm, "end": v(13.84, 497.3) * mm});
            skLineSegment(sketch, "E4867", {"start": v(13.84, 497.3) * mm, "end": v(12.3, 496.98) * mm});
            skLineSegment(sketch, "E4868", {"start": v(12.3, 496.98) * mm, "end": v(10.78, 496.58) * mm});
            skLineSegment(sketch, "E4869", {"start": v(10.78, 496.58) * mm, "end": v(9.28, 496.1) * mm});
            skLineSegment(sketch, "E4870", {"start": v(9.28, 496.1) * mm, "end": v(7.8, 495.56) * mm});
            skLineSegment(sketch, "E4871", {"start": v(7.8, 495.56) * mm, "end": v(6.35, 494.93) * mm});
            skLineSegment(sketch, "E4872", {"start": v(6.35, 494.93) * mm, "end": v(4.93, 494.23) * mm});
            skLineSegment(sketch, "E4873", {"start": v(4.93, 494.23) * mm, "end": v(3.54, 493.45) * mm});
            skLineSegment(sketch, "E4874", {"start": v(3.54, 493.45) * mm, "end": v(2.2, 492.6) * mm});
            skLineSegment(sketch, "E4875", {"start": v(2.2, 492.6) * mm, "end": v(0.9, 491.69) * mm});
            skLineSegment(sketch, "E4876", {"start": v(0.9, 491.69) * mm, "end": v(-0.37, 490.7) * mm});
            skLineSegment(sketch, "E4877", {"start": v(-0.37, 490.7) * mm, "end": v(-1.58, 489.65) * mm});
            skLineSegment(sketch, "E4878", {"start": v(-1.58, 489.65) * mm, "end": v(-2.74, 488.53) * mm});
            skLineSegment(sketch, "E4879", {"start": v(-2.74, 488.53) * mm, "end": v(-3.84, 487.34) * mm});
            skLineSegment(sketch, "E4880", {"start": v(-3.84, 487.34) * mm, "end": v(-4.88, 486.1) * mm});
            skLineSegment(sketch, "E4881", {"start": v(-4.88, 486.1) * mm, "end": v(-5.86, 484.78) * mm});
            skLineSegment(sketch, "E4882", {"start": v(-5.86, 484.78) * mm, "end": v(-6.78, 483.4) * mm});
            skLineSegment(sketch, "E4883", {"start": v(-6.78, 483.4) * mm, "end": v(-7.62, 481.97) * mm});
            skLineSegment(sketch, "E4884", {"start": v(-7.62, 481.97) * mm, "end": v(-8.47, 480.41) * mm});
            skLineSegment(sketch, "E4885", {"start": v(-8.47, 480.41) * mm, "end": v(-9.3, 478.83) * mm});
            skLineSegment(sketch, "E4886", {"start": v(-9.3, 478.83) * mm, "end": v(-10.1, 477.23) * mm});
            skLineSegment(sketch, "E4887", {"start": v(-10.1, 477.23) * mm, "end": v(-10.89, 475.62) * mm});
            skLineSegment(sketch, "E4888", {"start": v(-10.89, 475.62) * mm, "end": v(-11.66, 474) * mm});
            skLineSegment(sketch, "E4889", {"start": v(-11.66, 474) * mm, "end": v(-12.4, 472.35) * mm});
            skLineSegment(sketch, "E4890", {"start": v(-12.4, 472.35) * mm, "end": v(-13.14, 470.69) * mm});
            skLineSegment(sketch, "E4891", {"start": v(-13.14, 470.69) * mm, "end": v(-13.86, 469.01) * mm});
            skLineSegment(sketch, "E4892", {"start": v(-13.86, 469.01) * mm, "end": v(-14.56, 467.33) * mm});
            skLineSegment(sketch, "E4893", {"start": v(-14.56, 467.33) * mm, "end": v(-15.24, 465.63) * mm});
            skLineSegment(sketch, "E4894", {"start": v(-15.24, 465.63) * mm, "end": v(-15.92, 463.92) * mm});
            skLineSegment(sketch, "E4895", {"start": v(-15.92, 463.92) * mm, "end": v(-16.58, 462.2) * mm});
            skLineSegment(sketch, "E4896", {"start": v(-16.58, 462.2) * mm, "end": v(-17.22, 460.47) * mm});
            skLineSegment(sketch, "E4897", {"start": v(-17.22, 460.47) * mm, "end": v(-17.86, 458.73) * mm});
            skLineSegment(sketch, "E4898", {"start": v(-17.86, 458.73) * mm, "end": v(-18.48, 456.99) * mm});
            skLineSegment(sketch, "E4899", {"start": v(-18.48, 456.99) * mm, "end": v(-19.1, 455.23) * mm});
            skLineSegment(sketch, "E4900", {"start": v(-19.1, 455.23) * mm, "end": v(-19.7, 453.47) * mm});
            skLineSegment(sketch, "E4901", {"start": v(-19.7, 453.47) * mm, "end": v(-20.3, 451.7) * mm});
            skLineSegment(sketch, "E4902", {"start": v(-20.3, 451.7) * mm, "end": v(-20.88, 449.94) * mm});
            skLineSegment(sketch, "E4903", {"start": v(-20.88, 449.94) * mm, "end": v(-21.45, 448.16) * mm});
            skLineSegment(sketch, "E4904", {"start": v(-21.45, 448.16) * mm, "end": v(-22.03, 446.38) * mm});
            skLineSegment(sketch, "E4905", {"start": v(-22.03, 446.38) * mm, "end": v(-22.6, 444.6) * mm});
            skLineSegment(sketch, "E4906", {"start": v(-22.6, 444.6) * mm, "end": v(-23.15, 442.82) * mm});
            skLineSegment(sketch, "E4907", {"start": v(-23.15, 442.82) * mm, "end": v(-23.7, 441.04) * mm});
            skLineSegment(sketch, "E4908", {"start": v(-23.7, 441.04) * mm, "end": v(-24.26, 439.26) * mm});
            skLineSegment(sketch, "E4909", {"start": v(-24.26, 439.26) * mm, "end": v(-24.8, 437.48) * mm});
            skLineSegment(sketch, "E4910", {"start": v(-24.8, 437.48) * mm, "end": v(-25.35, 435.7) * mm});
            skLineSegment(sketch, "E4911", {"start": v(-25.35, 435.7) * mm, "end": v(-25.9, 433.92) * mm});
            skLineSegment(sketch, "E4912", {"start": v(-25.9, 433.92) * mm, "end": v(-26.44, 432.14) * mm});
            skLineSegment(sketch, "E4913", {"start": v(-26.44, 432.14) * mm, "end": v(-26.99, 430.37) * mm});
            skLineSegment(sketch, "E4914", {"start": v(-26.99, 430.37) * mm, "end": v(-27.53, 428.6) * mm});
            skLineSegment(sketch, "E4915", {"start": v(-27.53, 428.6) * mm, "end": v(-28.08, 426.84) * mm});
            skLineSegment(sketch, "E4916", {"start": v(-28.08, 426.84) * mm, "end": v(-28.62, 425.09) * mm});
            skLineSegment(sketch, "E4917", {"start": v(-28.62, 425.09) * mm, "end": v(-29.17, 423.34) * mm});
            skLineSegment(sketch, "E4918", {"start": v(-29.17, 423.34) * mm, "end": v(-29.73, 421.6) * mm});
            skLineSegment(sketch, "E4919", {"start": v(-29.73, 421.6) * mm, "end": v(-30.29, 419.87) * mm});
            skLineSegment(sketch, "E4920", {"start": v(-30.29, 419.87) * mm, "end": v(-30.85, 418.15) * mm});
            skLineSegment(sketch, "E4921", {"start": v(-30.85, 418.15) * mm, "end": v(-31.42, 416.44) * mm});
            skLineSegment(sketch, "E4922", {"start": v(-31.42, 416.44) * mm, "end": v(-32, 414.74) * mm});
            skLineSegment(sketch, "E4923", {"start": v(-32, 414.74) * mm, "end": v(-32.57, 413.05) * mm});
            skLineSegment(sketch, "E4924", {"start": v(-32.57, 413.05) * mm, "end": v(-33.16, 411.37) * mm});
            skLineSegment(sketch, "E4925", {"start": v(-33.16, 411.37) * mm, "end": v(-33.75, 409.73) * mm});
            skLineSegment(sketch, "E4926", {"start": v(-33.75, 409.73) * mm, "end": v(-34.35, 408.08) * mm});
            skLineSegment(sketch, "E4927", {"start": v(-34.35, 408.08) * mm, "end": v(-34.96, 406.43) * mm});
            skLineSegment(sketch, "E4928", {"start": v(-34.96, 406.43) * mm, "end": v(-35.58, 404.77) * mm});
            skLineSegment(sketch, "E4929", {"start": v(-35.58, 404.77) * mm, "end": v(-36.2, 403.11) * mm});
            skLineSegment(sketch, "E4930", {"start": v(-36.2, 403.11) * mm, "end": v(-36.84, 401.45) * mm});
            skLineSegment(sketch, "E4931", {"start": v(-36.84, 401.45) * mm, "end": v(-37.48, 399.78) * mm});
            skLineSegment(sketch, "E4932", {"start": v(-37.48, 399.78) * mm, "end": v(-38.13, 398.11) * mm});
            skLineSegment(sketch, "E4933", {"start": v(-38.13, 398.11) * mm, "end": v(-38.78, 396.44) * mm});
            skLineSegment(sketch, "E4934", {"start": v(-38.78, 396.44) * mm, "end": v(-39.44, 394.76) * mm});
            skLineSegment(sketch, "E4935", {"start": v(-39.44, 394.76) * mm, "end": v(-40.1, 393.08) * mm});
            skLineSegment(sketch, "E4936", {"start": v(-40.1, 393.08) * mm, "end": v(-40.76, 391.4) * mm});
            skLineSegment(sketch, "E4937", {"start": v(-40.76, 391.4) * mm, "end": v(-41.43, 389.72) * mm});
            skLineSegment(sketch, "E4938", {"start": v(-41.43, 389.72) * mm, "end": v(-42.1, 388.03) * mm});
            skLineSegment(sketch, "E4939", {"start": v(-42.1, 388.03) * mm, "end": v(-42.77, 386.34) * mm});
            skLineSegment(sketch, "E4940", {"start": v(-42.77, 386.34) * mm, "end": v(-43.44, 384.65) * mm});
            skLineSegment(sketch, "E4941", {"start": v(-43.44, 384.65) * mm, "end": v(-44.11, 382.95) * mm});
            skLineSegment(sketch, "E4942", {"start": v(-44.11, 382.95) * mm, "end": v(-44.79, 381.25) * mm});
            skLineSegment(sketch, "E4943", {"start": v(-44.79, 381.25) * mm, "end": v(-45.46, 379.55) * mm});
            skLineSegment(sketch, "E4944", {"start": v(-45.46, 379.55) * mm, "end": v(-46.13, 377.85) * mm});
            skLineSegment(sketch, "E4945", {"start": v(-46.13, 377.85) * mm, "end": v(-46.8, 376.14) * mm});
            skLineSegment(sketch, "E4946", {"start": v(-46.8, 376.14) * mm, "end": v(-47.46, 374.44) * mm});
            skLineSegment(sketch, "E4947", {"start": v(-47.46, 374.44) * mm, "end": v(-48.11, 372.73) * mm});
            skLineSegment(sketch, "E4948", {"start": v(-48.11, 372.73) * mm, "end": v(-48.77, 371.02) * mm});
            skLineSegment(sketch, "E4949", {"start": v(-48.77, 371.02) * mm, "end": v(-49.42, 369.3) * mm});
            skLineSegment(sketch, "E4950", {"start": v(-49.42, 369.3) * mm, "end": v(-50.06, 367.6) * mm});
            skLineSegment(sketch, "E4951", {"start": v(-50.06, 367.6) * mm, "end": v(-50.7, 365.88) * mm});
            skLineSegment(sketch, "E4952", {"start": v(-50.7, 365.88) * mm, "end": v(-51.33, 364.16) * mm});
            skLineSegment(sketch, "E4953", {"start": v(-51.33, 364.16) * mm, "end": v(-51.96, 362.44) * mm});
            skLineSegment(sketch, "E4954", {"start": v(-51.96, 362.44) * mm, "end": v(-52.57, 360.72) * mm});
            skLineSegment(sketch, "E4955", {"start": v(-52.57, 360.72) * mm, "end": v(-53.18, 359) * mm});
            skLineSegment(sketch, "E4956", {"start": v(-53.18, 359) * mm, "end": v(-53.78, 357.27) * mm});
            skLineSegment(sketch, "E4957", {"start": v(-53.78, 357.27) * mm, "end": v(-54.36, 355.55) * mm});
            skLineSegment(sketch, "E4958", {"start": v(-54.36, 355.55) * mm, "end": v(-54.94, 353.82) * mm});
            skLineSegment(sketch, "E4959", {"start": v(-54.94, 353.82) * mm, "end": v(-55.5, 352.1) * mm});
            skLineSegment(sketch, "E4960", {"start": v(-55.5, 352.1) * mm, "end": v(-56.05, 350.37) * mm});
            skLineSegment(sketch, "E4961", {"start": v(-56.05, 350.37) * mm, "end": v(-56.6, 348.64) * mm});
            skLineSegment(sketch, "E4962", {"start": v(-56.6, 348.64) * mm, "end": v(-57.12, 346.91) * mm});
            skLineSegment(sketch, "E4963", {"start": v(-57.12, 346.91) * mm, "end": v(-57.63, 345.18) * mm});
            skLineSegment(sketch, "E4964", {"start": v(-57.63, 345.18) * mm, "end": v(-58.13, 343.45) * mm});
            skLineSegment(sketch, "E4965", {"start": v(-58.13, 343.45) * mm, "end": v(-58.6, 341.72) * mm});
            skLineSegment(sketch, "E4966", {"start": v(-58.6, 341.72) * mm, "end": v(-59.07, 339.99) * mm});
            skLineSegment(sketch, "E4967", {"start": v(-59.07, 339.99) * mm, "end": v(-59.52, 338.26) * mm});
            skLineSegment(sketch, "E4968", {"start": v(-59.52, 338.26) * mm, "end": v(-59.95, 336.52) * mm});
            skLineSegment(sketch, "E4969", {"start": v(-59.95, 336.52) * mm, "end": v(-60.36, 334.8) * mm});
            skLineSegment(sketch, "E4970", {"start": v(-60.36, 334.8) * mm, "end": v(-60.76, 333.06) * mm});
            skLineSegment(sketch, "E4971", {"start": v(-60.76, 333.06) * mm, "end": v(-61.13, 331.33) * mm});
            skLineSegment(sketch, "E4972", {"start": v(-61.13, 331.33) * mm, "end": v(-61.48, 329.6) * mm});
            skLineSegment(sketch, "E4973", {"start": v(-61.48, 329.6) * mm, "end": v(-61.82, 327.86) * mm});
            skLineSegment(sketch, "E4974", {"start": v(-61.82, 327.86) * mm, "end": v(-62.13, 326.13) * mm});
            skLineSegment(sketch, "E4975", {"start": v(-62.13, 326.13) * mm, "end": v(-62.42, 324.4) * mm});
            skLineSegment(sketch, "E4976", {"start": v(-62.42, 324.4) * mm, "end": v(-62.69, 322.67) * mm});
            skLineSegment(sketch, "E4977", {"start": v(-62.69, 322.67) * mm, "end": v(-35.53, 322.67) * mm});
            skLineSegment(sketch, "E4978", {"start": v(-35.53, 322.67) * mm, "end": v(-36.18, 320.9) * mm});
            skLineSegment(sketch, "E4979", {"start": v(-36.18, 320.9) * mm, "end": v(-36.8, 319.15) * mm});
            skLineSegment(sketch, "E4980", {"start": v(-36.8, 319.15) * mm, "end": v(-37.4, 317.4) * mm});
            skLineSegment(sketch, "E4981", {"start": v(-37.4, 317.4) * mm, "end": v(-37.96, 315.64) * mm});
            skLineSegment(sketch, "E4982", {"start": v(-37.96, 315.64) * mm, "end": v(-38.49, 313.9) * mm});
            skLineSegment(sketch, "E4983", {"start": v(-38.49, 313.9) * mm, "end": v(-39, 312.15) * mm});
            skLineSegment(sketch, "E4984", {"start": v(-39, 312.15) * mm, "end": v(-39.47, 310.4) * mm});
            skLineSegment(sketch, "E4985", {"start": v(-39.47, 310.4) * mm, "end": v(-39.92, 308.67) * mm});
            skLineSegment(sketch, "E4986", {"start": v(-39.92, 308.67) * mm, "end": v(-40.34, 306.93) * mm});
            skLineSegment(sketch, "E4987", {"start": v(-40.34, 306.93) * mm, "end": v(-40.74, 305.2) * mm});
            skLineSegment(sketch, "E4988", {"start": v(-40.74, 305.2) * mm, "end": v(-41.11, 303.46) * mm});
            skLineSegment(sketch, "E4989", {"start": v(-41.11, 303.46) * mm, "end": v(-41.46, 301.73) * mm});
            skLineSegment(sketch, "E4990", {"start": v(-41.46, 301.73) * mm, "end": v(-41.8, 300) * mm});
            skLineSegment(sketch, "E4991", {"start": v(-41.8, 300) * mm, "end": v(-42.1, 298.27) * mm});
            skLineSegment(sketch, "E4992", {"start": v(-42.1, 298.27) * mm, "end": v(-42.38, 296.54) * mm});
            skLineSegment(sketch, "E4993", {"start": v(-42.38, 296.54) * mm, "end": v(-42.64, 294.8) * mm});
            skLineSegment(sketch, "E4994", {"start": v(-42.64, 294.8) * mm, "end": v(-42.89, 293.07) * mm});
            skLineSegment(sketch, "E4995", {"start": v(-42.89, 293.07) * mm, "end": v(-43.1, 291.34) * mm});
            skLineSegment(sketch, "E4996", {"start": v(-43.1, 291.34) * mm, "end": v(-43.32, 289.61) * mm});
            skLineSegment(sketch, "E4997", {"start": v(-43.32, 289.61) * mm, "end": v(-43.5, 287.88) * mm});
            skLineSegment(sketch, "E4998", {"start": v(-43.5, 287.88) * mm, "end": v(-43.67, 286.14) * mm});
            skLineSegment(sketch, "E4999", {"start": v(-43.67, 286.14) * mm, "end": v(-43.83, 284.4) * mm});
            skLineSegment(sketch, "E5000", {"start": v(-43.83, 284.4) * mm, "end": v(-43.97, 282.67) * mm});
            skLineSegment(sketch, "E5001", {"start": v(-43.97, 282.67) * mm, "end": v(-44.1, 280.93) * mm});
            skLineSegment(sketch, "E5002", {"start": v(-44.1, 280.93) * mm, "end": v(-44.2, 279.18) * mm});
            skLineSegment(sketch, "E5003", {"start": v(-44.2, 279.18) * mm, "end": v(-44.3, 277.44) * mm});
            skLineSegment(sketch, "E5004", {"start": v(-44.3, 277.44) * mm, "end": v(-44.38, 275.69) * mm});
            skLineSegment(sketch, "E5005", {"start": v(-44.38, 275.69) * mm, "end": v(-44.46, 273.93) * mm});
            skLineSegment(sketch, "E5006", {"start": v(-44.46, 273.93) * mm, "end": v(-44.52, 272.18) * mm});
            skLineSegment(sketch, "E5007", {"start": v(-44.52, 272.18) * mm, "end": v(-44.57, 270.42) * mm});
            skLineSegment(sketch, "E5008", {"start": v(-44.57, 270.42) * mm, "end": v(-44.6, 268.65) * mm});
            skLineSegment(sketch, "E5009", {"start": v(-44.6, 268.65) * mm, "end": v(-44.64, 266.88) * mm});
            skLineSegment(sketch, "E5010", {"start": v(-44.64, 266.88) * mm, "end": v(-44.67, 265.1) * mm});
            skLineSegment(sketch, "E5011", {"start": v(-44.67, 265.1) * mm, "end": v(-44.69, 263.32) * mm});
            skLineSegment(sketch, "E5012", {"start": v(-44.69, 263.32) * mm, "end": v(-44.7, 261.54) * mm});
            skLineSegment(sketch, "E5013", {"start": v(-44.7, 261.54) * mm, "end": v(-44.7, 259.75) * mm});
            skLineSegment(sketch, "E5014", {"start": v(-44.7, 259.75) * mm, "end": v(-44.7, 257.95) * mm});
            skLineSegment(sketch, "E5015", {"start": v(-44.7, 257.95) * mm, "end": v(-44.7, 256.14) * mm});
            skLineSegment(sketch, "E5016", {"start": v(-44.7, 256.14) * mm, "end": v(-44.7, 254.33) * mm});
            skLineSegment(sketch, "E5017", {"start": v(-44.7, 254.33) * mm, "end": v(-44.68, 252.51) * mm});
            skLineSegment(sketch, "E5018", {"start": v(-44.68, 252.51) * mm, "end": v(-44.67, 250.69) * mm});
            skLineSegment(sketch, "E5019", {"start": v(-44.67, 250.69) * mm, "end": v(-44.65, 248.85) * mm});
            skLineSegment(sketch, "E5020", {"start": v(-44.65, 248.85) * mm, "end": v(-44.64, 247) * mm});
            skLineSegment(sketch, "E5021", {"start": v(-44.64, 247) * mm, "end": v(-44.63, 245.16) * mm});
            skLineSegment(sketch, "E5022", {"start": v(-44.63, 245.16) * mm, "end": v(-44.61, 243.3) * mm});
            skLineSegment(sketch, "E5023", {"start": v(-44.61, 243.3) * mm, "end": v(-44.6, 241.43) * mm});
            skLineSegment(sketch, "E5024", {"start": v(-44.6, 241.43) * mm, "end": v(-44.6, 239.55) * mm});
            skLineSegment(sketch, "E5025", {"start": v(-44.6, 239.55) * mm, "end": v(-44.59, 237.67) * mm});
            skLineSegment(sketch, "E5026", {"start": v(-44.59, 237.67) * mm, "end": v(-44.58, 235.77) * mm});
            skLineSegment(sketch, "E5027", {"start": v(-44.58, 235.77) * mm, "end": v(-44.61, 234.34) * mm});
            skLineSegment(sketch, "E5028", {"start": v(-44.61, 234.34) * mm, "end": v(-44.68, 232.78) * mm});
            skLineSegment(sketch, "E5029", {"start": v(-44.68, 232.78) * mm, "end": v(-44.8, 231.1) * mm});
            skLineSegment(sketch, "E5030", {"start": v(-44.8, 231.1) * mm, "end": v(-44.92, 229.32) * mm});
            skLineSegment(sketch, "E5031", {"start": v(-44.92, 229.32) * mm, "end": v(-45.07, 227.46) * mm});
            skLineSegment(sketch, "E5032", {"start": v(-45.07, 227.46) * mm, "end": v(-45.2, 225.54) * mm});
            skLineSegment(sketch, "E5033", {"start": v(-45.2, 225.54) * mm, "end": v(-45.34, 223.57) * mm});
            skLineSegment(sketch, "E5034", {"start": v(-45.34, 223.57) * mm, "end": v(-45.45, 221.58) * mm});
            skLineSegment(sketch, "E5035", {"start": v(-45.45, 221.58) * mm, "end": v(-45.52, 219.59) * mm});
            skLineSegment(sketch, "E5036", {"start": v(-45.52, 219.59) * mm, "end": v(-45.55, 217.6) * mm});
            skLineSegment(sketch, "E5037", {"start": v(-45.55, 217.6) * mm, "end": v(-45.52, 215.65) * mm});
            skLineSegment(sketch, "E5038", {"start": v(-45.52, 215.65) * mm, "end": v(-45.42, 213.75) * mm});
            skLineSegment(sketch, "E5039", {"start": v(-45.42, 213.75) * mm, "end": v(-45.24, 211.9) * mm});
            skLineSegment(sketch, "E5040", {"start": v(-45.24, 211.9) * mm, "end": v(-44.97, 210.15) * mm});
            skLineSegment(sketch, "E5041", {"start": v(-44.97, 210.15) * mm, "end": v(-44.6, 208.5) * mm});
            skLineSegment(sketch, "E5042", {"start": v(-44.6, 208.5) * mm, "end": v(-44.1, 206.98) * mm});
            skLineSegment(sketch, "E5043", {"start": v(-44.1, 206.98) * mm, "end": v(-43.48, 205.6) * mm});
            skLineSegment(sketch, "E5044", {"start": v(-43.48, 205.6) * mm, "end": v(-42.72, 204.37) * mm});
            skLineSegment(sketch, "E5045", {"start": v(-42.72, 204.37) * mm, "end": v(-41.56, 203.05) * mm});
            skLineSegment(sketch, "E5046", {"start": v(-41.56, 203.05) * mm, "end": v(-40.2, 202) * mm});
            skLineSegment(sketch, "E5047", {"start": v(-40.2, 202) * mm, "end": v(-38.69, 201.19) * mm});
            skLineSegment(sketch, "E5048", {"start": v(-38.69, 201.19) * mm, "end": v(-37.04, 200.57) * mm});
            skLineSegment(sketch, "E5049", {"start": v(-37.04, 200.57) * mm, "end": v(-35.3, 200.14) * mm});
            skLineSegment(sketch, "E5050", {"start": v(-35.3, 200.14) * mm, "end": v(-33.5, 199.85) * mm});
            skLineSegment(sketch, "E5051", {"start": v(-33.5, 199.85) * mm, "end": v(-31.68, 199.68) * mm});
            skLineSegment(sketch, "E5052", {"start": v(-31.68, 199.68) * mm, "end": v(-29.84, 199.59) * mm});
            skLineSegment(sketch, "E5053", {"start": v(-29.84, 199.59) * mm, "end": v(-28.05, 199.56) * mm});
            skLineSegment(sketch, "E5054", {"start": v(-28.05, 199.56) * mm, "end": v(-26.3, 199.56) * mm});
            skLineSegment(sketch, "E5055", {"start": v(-26.3, 199.56) * mm, "end": v(-24.67, 199.57) * mm});
            skLineSegment(sketch, "E5056", {"start": v(-143.06, -80.57) * mm, "end": v(-142.17, -79.8) * mm});
            skLineSegment(sketch, "E5057", {"start": v(-142.17, -79.8) * mm, "end": v(-141.16, -79.1) * mm});
            skLineSegment(sketch, "E5058", {"start": v(-141.16, -79.1) * mm, "end": v(-140.02, -78.47) * mm});
            skLineSegment(sketch, "E5059", {"start": v(-140.02, -78.47) * mm, "end": v(-138.78, -77.9) * mm});
            skLineSegment(sketch, "E5060", {"start": v(-138.78, -77.9) * mm, "end": v(-137.43, -77.4) * mm});
            skLineSegment(sketch, "E5061", {"start": v(-137.43, -77.4) * mm, "end": v(-135.99, -76.95) * mm});
            skLineSegment(sketch, "E5062", {"start": v(-135.99, -76.95) * mm, "end": v(-134.45, -76.56) * mm});
            skLineSegment(sketch, "E5063", {"start": v(-134.45, -76.56) * mm, "end": v(-132.83, -76.22) * mm});
            skLineSegment(sketch, "E5064", {"start": v(-132.83, -76.22) * mm, "end": v(-131.13, -75.94) * mm});
            skLineSegment(sketch, "E5065", {"start": v(-131.13, -75.94) * mm, "end": v(-129.36, -75.7) * mm});
            skLineSegment(sketch, "E5066", {"start": v(-129.36, -75.7) * mm, "end": v(-127.52, -75.51) * mm});
            skLineSegment(sketch, "E5067", {"start": v(-127.52, -75.51) * mm, "end": v(-125.63, -75.37) * mm});
            skLineSegment(sketch, "E5068", {"start": v(-125.63, -75.37) * mm, "end": v(-123.68, -75.26) * mm});
            skLineSegment(sketch, "E5069", {"start": v(-123.68, -75.26) * mm, "end": v(-121.7, -75.19) * mm});
            skLineSegment(sketch, "E5070", {"start": v(-121.7, -75.19) * mm, "end": v(-119.67, -75.15) * mm});
            skLineSegment(sketch, "E5071", {"start": v(-119.67, -75.15) * mm, "end": v(-117.61, -75.15) * mm});
            skLineSegment(sketch, "E5072", {"start": v(-117.61, -75.15) * mm, "end": v(-115.53, -75.17) * mm});
            skLineSegment(sketch, "E5073", {"start": v(-115.53, -75.17) * mm, "end": v(-113.43, -75.22) * mm});
            skLineSegment(sketch, "E5074", {"start": v(-113.43, -75.22) * mm, "end": v(-111.32, -75.3) * mm});
            skLineSegment(sketch, "E5075", {"start": v(-111.32, -75.3) * mm, "end": v(-109.2, -75.4) * mm});
            skLineSegment(sketch, "E5076", {"start": v(-109.2, -75.4) * mm, "end": v(-107.08, -75.5) * mm});
            skLineSegment(sketch, "E5077", {"start": v(-107.08, -75.5) * mm, "end": v(-104.98, -75.63) * mm});
            skLineSegment(sketch, "E5078", {"start": v(-104.98, -75.63) * mm, "end": v(-102.89, -75.77) * mm});
            skLineSegment(sketch, "E5079", {"start": v(-102.89, -75.77) * mm, "end": v(-100.82, -75.92) * mm});
            skLineSegment(sketch, "E5080", {"start": v(-100.82, -75.92) * mm, "end": v(-98.78, -76.07) * mm});
            skLineSegment(sketch, "E5081", {"start": v(-98.78, -76.07) * mm, "end": v(-96.78, -76.23) * mm});
            skLineSegment(sketch, "E5082", {"start": v(-96.78, -76.23) * mm, "end": v(-94.82, -76.39) * mm});
            skLineSegment(sketch, "E5083", {"start": v(-94.82, -76.39) * mm, "end": v(-92.9, -76.55) * mm});
            skLineSegment(sketch, "E5084", {"start": v(-92.9, -76.55) * mm, "end": v(-91.05, -76.7) * mm});
            skLineSegment(sketch, "E5085", {"start": v(-91.05, -76.7) * mm, "end": v(-89.25, -76.84) * mm});
            skLineSegment(sketch, "E5086", {"start": v(-89.25, -76.84) * mm, "end": v(-87.52, -76.98) * mm});
            skLineSegment(sketch, "E5087", {"start": v(-87.52, -76.98) * mm, "end": v(-85.87, -77.1) * mm});
            skLineSegment(sketch, "E5088", {"start": v(-85.87, -77.1) * mm, "end": v(-84.3, -77.2) * mm});
            skLineSegment(sketch, "E5089", {"start": v(-84.3, -77.2) * mm, "end": v(-82.82, -77.3) * mm});
            skLineSegment(sketch, "E5090", {"start": v(-82.82, -77.3) * mm, "end": v(-81.44, -77.36) * mm});
            skLineSegment(sketch, "E5091", {"start": v(-81.44, -77.36) * mm, "end": v(-80.15, -77.4) * mm});
            skLineSegment(sketch, "E5092", {"start": v(-80.15, -77.4) * mm, "end": v(-78.98, -77.42) * mm});
            skLineSegment(sketch, "E5093", {"start": v(-78.98, -77.42) * mm, "end": v(82.14, -77.42) * mm});
            skLineSegment(sketch, "E5094", {"start": v(82.14, -77.42) * mm, "end": v(83.44, -77.4) * mm});
            skLineSegment(sketch, "E5095", {"start": v(83.44, -77.4) * mm, "end": v(84.83, -77.36) * mm});
            skLineSegment(sketch, "E5096", {"start": v(84.83, -77.36) * mm, "end": v(86.3, -77.29) * mm});
            skLineSegment(sketch, "E5097", {"start": v(86.3, -77.29) * mm, "end": v(87.86, -77.2) * mm});
            skLineSegment(sketch, "E5098", {"start": v(87.86, -77.2) * mm, "end": v(89.49, -77.09) * mm});
            skLineSegment(sketch, "E5099", {"start": v(89.49, -77.09) * mm, "end": v(91.18, -76.96) * mm});
            skLineSegment(sketch, "E5100", {"start": v(91.18, -76.96) * mm, "end": v(92.93, -76.82) * mm});
            skLineSegment(sketch, "E5101", {"start": v(92.93, -76.82) * mm, "end": v(94.73, -76.67) * mm});
            skLineSegment(sketch, "E5102", {"start": v(94.73, -76.67) * mm, "end": v(96.59, -76.51) * mm});
            skLineSegment(sketch, "E5103", {"start": v(96.59, -76.51) * mm, "end": v(98.48, -76.35) * mm});
            skLineSegment(sketch, "E5104", {"start": v(98.48, -76.35) * mm, "end": v(100.42, -76.18) * mm});
            skLineSegment(sketch, "E5105", {"start": v(100.42, -76.18) * mm, "end": v(102.39, -76.02) * mm});
            skLineSegment(sketch, "E5106", {"start": v(102.39, -76.02) * mm, "end": v(104.38, -75.86) * mm});
            skLineSegment(sketch, "E5107", {"start": v(104.38, -75.86) * mm, "end": v(106.4, -75.7) * mm});
            skLineSegment(sketch, "E5108", {"start": v(106.4, -75.7) * mm, "end": v(108.42, -75.56) * mm});
            skLineSegment(sketch, "E5109", {"start": v(108.42, -75.56) * mm, "end": v(110.45, -75.43) * mm});
            skLineSegment(sketch, "E5110", {"start": v(110.45, -75.43) * mm, "end": v(112.5, -75.32) * mm});
            skLineSegment(sketch, "E5111", {"start": v(112.5, -75.32) * mm, "end": v(114.53, -75.22) * mm});
            skLineSegment(sketch, "E5112", {"start": v(114.53, -75.22) * mm, "end": v(116.56, -75.15) * mm});
            skLineSegment(sketch, "E5113", {"start": v(116.56, -75.15) * mm, "end": v(118.57, -75.1) * mm});
            skLineSegment(sketch, "E5114", {"start": v(118.57, -75.1) * mm, "end": v(120.56, -75.08) * mm});
            skLineSegment(sketch, "E5115", {"start": v(120.56, -75.08) * mm, "end": v(122.53, -75.09) * mm});
            skLineSegment(sketch, "E5116", {"start": v(122.53, -75.09) * mm, "end": v(124.46, -75.13) * mm});
            skLineSegment(sketch, "E5117", {"start": v(124.46, -75.13) * mm, "end": v(126.36, -75.2) * mm});
            skLineSegment(sketch, "E5118", {"start": v(126.36, -75.2) * mm, "end": v(128.21, -75.32) * mm});
            skLineSegment(sketch, "E5119", {"start": v(128.21, -75.32) * mm, "end": v(130.02, -75.48) * mm});
            skLineSegment(sketch, "E5120", {"start": v(130.02, -75.48) * mm, "end": v(131.77, -75.68) * mm});
            skLineSegment(sketch, "E5121", {"start": v(131.77, -75.68) * mm, "end": v(133.46, -75.93) * mm});
            skLineSegment(sketch, "E5122", {"start": v(133.46, -75.93) * mm, "end": v(135.08, -76.23) * mm});
            skLineSegment(sketch, "E5123", {"start": v(135.08, -76.23) * mm, "end": v(136.64, -76.6) * mm});
            skLineSegment(sketch, "E5124", {"start": v(136.64, -76.6) * mm, "end": v(138.1, -77) * mm});
            skLineSegment(sketch, "E5125", {"start": v(138.1, -77) * mm, "end": v(139.5, -77.47) * mm});
            skLineSegment(sketch, "E5126", {"start": v(139.5, -77.47) * mm, "end": v(140.8, -78) * mm});
            skLineSegment(sketch, "E5127", {"start": v(140.8, -78) * mm, "end": v(142, -78.6) * mm});
            skLineSegment(sketch, "E5128", {"start": v(142, -78.6) * mm, "end": v(143.12, -79.28) * mm});
            skLineSegment(sketch, "E5129", {"start": v(143.12, -79.28) * mm, "end": v(143.75, -79.8) * mm});
            skLineSegment(sketch, "E5130", {"start": v(143.75, -79.8) * mm, "end": v(144.35, -80.53) * mm});
            skLineSegment(sketch, "E5131", {"start": v(144.35, -80.53) * mm, "end": v(144.92, -81.42) * mm});
            skLineSegment(sketch, "E5132", {"start": v(144.92, -81.42) * mm, "end": v(145.45, -82.47) * mm});
            skLineSegment(sketch, "E5133", {"start": v(145.45, -82.47) * mm, "end": v(145.94, -83.67) * mm});
            skLineSegment(sketch, "E5134", {"start": v(145.94, -83.67) * mm, "end": v(146.4, -85.02) * mm});
            skLineSegment(sketch, "E5135", {"start": v(146.4, -85.02) * mm, "end": v(146.81, -86.5) * mm});
            skLineSegment(sketch, "E5136", {"start": v(146.81, -86.5) * mm, "end": v(147.2, -88.09) * mm});
            skLineSegment(sketch, "E5137", {"start": v(147.2, -88.09) * mm, "end": v(147.54, -89.79) * mm});
            skLineSegment(sketch, "E5138", {"start": v(147.54, -89.79) * mm, "end": v(147.85, -91.59) * mm});
            skLineSegment(sketch, "E5139", {"start": v(147.85, -91.59) * mm, "end": v(148.12, -93.47) * mm});
            skLineSegment(sketch, "E5140", {"start": v(148.12, -93.47) * mm, "end": v(148.36, -95.44) * mm});
            skLineSegment(sketch, "E5141", {"start": v(148.36, -95.44) * mm, "end": v(148.56, -97.46) * mm});
            skLineSegment(sketch, "E5142", {"start": v(148.56, -97.46) * mm, "end": v(148.72, -99.54) * mm});
            skLineSegment(sketch, "E5143", {"start": v(148.72, -99.54) * mm, "end": v(148.85, -101.67) * mm});
            skLineSegment(sketch, "E5144", {"start": v(148.85, -101.67) * mm, "end": v(148.94, -103.82) * mm});
            skLineSegment(sketch, "E5145", {"start": v(148.94, -103.82) * mm, "end": v(149, -106) * mm});
            skLineSegment(sketch, "E5146", {"start": v(149, -106) * mm, "end": v(149.02, -108.2) * mm});
            skLineSegment(sketch, "E5147", {"start": v(149.02, -108.2) * mm, "end": v(149, -110.38) * mm});
            skLineSegment(sketch, "E5148", {"start": v(149, -110.38) * mm, "end": v(148.94, -112.56) * mm});
            skLineSegment(sketch, "E5149", {"start": v(148.94, -112.56) * mm, "end": v(148.85, -114.72) * mm});
            skLineSegment(sketch, "E5150", {"start": v(148.85, -114.72) * mm, "end": v(148.72, -116.84) * mm});
            skLineSegment(sketch, "E5151", {"start": v(148.72, -116.84) * mm, "end": v(148.56, -118.92) * mm});
            skLineSegment(sketch, "E5152", {"start": v(148.56, -118.92) * mm, "end": v(148.36, -120.95) * mm});
            skLineSegment(sketch, "E5153", {"start": v(148.36, -120.95) * mm, "end": v(148.12, -122.9) * mm});
            skLineSegment(sketch, "E5154", {"start": v(148.12, -122.9) * mm, "end": v(147.85, -124.8) * mm});
            skLineSegment(sketch, "E5155", {"start": v(147.85, -124.8) * mm, "end": v(147.54, -126.6) * mm});
            skLineSegment(sketch, "E5156", {"start": v(147.54, -126.6) * mm, "end": v(147.2, -128.3) * mm});
            skLineSegment(sketch, "E5157", {"start": v(147.2, -128.3) * mm, "end": v(146.81, -129.89) * mm});
            skLineSegment(sketch, "E5158", {"start": v(146.81, -129.89) * mm, "end": v(146.4, -131.36) * mm});
            skLineSegment(sketch, "E5159", {"start": v(146.4, -131.36) * mm, "end": v(145.94, -132.7) * mm});
            skLineSegment(sketch, "E5160", {"start": v(145.94, -132.7) * mm, "end": v(145.45, -133.91) * mm});
            skLineSegment(sketch, "E5161", {"start": v(145.45, -133.91) * mm, "end": v(144.92, -134.97) * mm});
            skLineSegment(sketch, "E5162", {"start": v(144.92, -134.97) * mm, "end": v(144.35, -135.86) * mm});
            skLineSegment(sketch, "E5163", {"start": v(144.35, -135.86) * mm, "end": v(143.75, -136.57) * mm});
            skLineSegment(sketch, "E5164", {"start": v(143.75, -136.57) * mm, "end": v(143.12, -137.1) * mm});
            skLineSegment(sketch, "E5165", {"start": v(143.12, -137.1) * mm, "end": v(141.69, -137.9) * mm});
            skLineSegment(sketch, "E5166", {"start": v(141.69, -137.9) * mm, "end": v(140.1, -138.49) * mm});
            skLineSegment(sketch, "E5167", {"start": v(140.1, -138.49) * mm, "end": v(138.4, -138.91) * mm});
            skLineSegment(sketch, "E5168", {"start": v(138.4, -138.91) * mm, "end": v(136.6, -139.18) * mm});
            skLineSegment(sketch, "E5169", {"start": v(136.6, -139.18) * mm, "end": v(134.74, -139.33) * mm});
            skLineSegment(sketch, "E5170", {"start": v(134.74, -139.33) * mm, "end": v(132.83, -139.38) * mm});
            skLineSegment(sketch, "E5171", {"start": v(132.83, -139.38) * mm, "end": v(130.9, -139.36) * mm});
            skLineSegment(sketch, "E5172", {"start": v(130.9, -139.36) * mm, "end": v(128.98, -139.28) * mm});
            skLineSegment(sketch, "E5173", {"start": v(128.98, -139.28) * mm, "end": v(127.1, -139.18) * mm});
            skLineSegment(sketch, "E5174", {"start": v(127.1, -139.18) * mm, "end": v(125.3, -139.08) * mm});
            skLineSegment(sketch, "E5175", {"start": v(125.3, -139.08) * mm, "end": v(123.57, -139) * mm});
            skLineSegment(sketch, "E5176", {"start": v(123.57, -139) * mm, "end": v(121.97, -138.97) * mm});
            skLineSegment(sketch, "E5177", {"start": v(121.97, -138.97) * mm, "end": v(120.15, -138.98) * mm});
            skLineSegment(sketch, "E5178", {"start": v(120.15, -138.98) * mm, "end": v(118.34, -139) * mm});
            skLineSegment(sketch, "E5179", {"start": v(118.34, -139) * mm, "end": v(116.52, -139.04) * mm});
            skLineSegment(sketch, "E5180", {"start": v(116.52, -139.04) * mm, "end": v(114.71, -139.1) * mm});
            skLineSegment(sketch, "E5181", {"start": v(114.71, -139.1) * mm, "end": v(112.9, -139.16) * mm});
            skLineSegment(sketch, "E5182", {"start": v(112.9, -139.16) * mm, "end": v(111.1, -139.23) * mm});
            skLineSegment(sketch, "E5183", {"start": v(111.1, -139.23) * mm, "end": v(109.28, -139.31) * mm});
            skLineSegment(sketch, "E5184", {"start": v(109.28, -139.31) * mm, "end": v(107.48, -139.4) * mm});
            skLineSegment(sketch, "E5185", {"start": v(107.48, -139.4) * mm, "end": v(105.67, -139.5) * mm});
            skLineSegment(sketch, "E5186", {"start": v(105.67, -139.5) * mm, "end": v(103.87, -139.6) * mm});
            skLineSegment(sketch, "E5187", {"start": v(103.87, -139.6) * mm, "end": v(102.06, -139.71) * mm});
            skLineSegment(sketch, "E5188", {"start": v(102.06, -139.71) * mm, "end": v(100.25, -139.82) * mm});
            skLineSegment(sketch, "E5189", {"start": v(100.25, -139.82) * mm, "end": v(98.45, -139.93) * mm});
            skLineSegment(sketch, "E5190", {"start": v(98.45, -139.93) * mm, "end": v(96.64, -140.03) * mm});
            skLineSegment(sketch, "E5191", {"start": v(96.64, -140.03) * mm, "end": v(94.84, -140.14) * mm});
            skLineSegment(sketch, "E5192", {"start": v(94.84, -140.14) * mm, "end": v(93.03, -140.24) * mm});
            skLineSegment(sketch, "E5193", {"start": v(93.03, -140.24) * mm, "end": v(91.22, -140.34) * mm});
            skLineSegment(sketch, "E5194", {"start": v(91.22, -140.34) * mm, "end": v(89.41, -140.43) * mm});
            skLineSegment(sketch, "E5195", {"start": v(89.41, -140.43) * mm, "end": v(87.6, -140.51) * mm});
            skLineSegment(sketch, "E5196", {"start": v(87.6, -140.51) * mm, "end": v(85.8, -140.59) * mm});
            skLineSegment(sketch, "E5197", {"start": v(85.8, -140.59) * mm, "end": v(83.98, -140.65) * mm});
            skLineSegment(sketch, "E5198", {"start": v(83.98, -140.65) * mm, "end": v(82.16, -140.7) * mm});
            skLineSegment(sketch, "E5199", {"start": v(82.16, -140.7) * mm, "end": v(80.35, -140.74) * mm});
            skLineSegment(sketch, "E5200", {"start": v(80.35, -140.74) * mm, "end": v(78.53, -140.77) * mm});
            skLineSegment(sketch, "E5201", {"start": v(78.53, -140.77) * mm, "end": v(76.7, -140.78) * mm});
            skLineSegment(sketch, "E5202", {"start": v(76.7, -140.78) * mm, "end": v(76.7, -260.26) * mm});
            skLineSegment(sketch, "E5203", {"start": v(76.7, -260.26) * mm, "end": v(125.59, -260.26) * mm});
            skLineSegment(sketch, "E5204", {"start": v(125.59, -260.26) * mm, "end": v(127.2, -260.23) * mm});
            skLineSegment(sketch, "E5205", {"start": v(127.2, -260.23) * mm, "end": v(128.92, -260.16) * mm});
            skLineSegment(sketch, "E5206", {"start": v(128.92, -260.16) * mm, "end": v(130.74, -260.08) * mm});
            skLineSegment(sketch, "E5207", {"start": v(130.74, -260.08) * mm, "end": v(132.61, -260.02) * mm});
            skLineSegment(sketch, "E5208", {"start": v(132.61, -260.02) * mm, "end": v(134.51, -260.03) * mm});
            skLineSegment(sketch, "E5209", {"start": v(134.51, -260.03) * mm, "end": v(136.4, -260.13) * mm});
            skLineSegment(sketch, "E5210", {"start": v(136.4, -260.13) * mm, "end": v(138.23, -260.35) * mm});
            skLineSegment(sketch, "E5211", {"start": v(138.23, -260.35) * mm, "end": v(139.98, -260.73) * mm});
            skLineSegment(sketch, "E5212", {"start": v(139.98, -260.73) * mm, "end": v(141.62, -261.3) * mm});
            skLineSegment(sketch, "E5213", {"start": v(141.62, -261.3) * mm, "end": v(143.1, -262.1) * mm});
            skLineSegment(sketch, "E5214", {"start": v(143.1, -262.1) * mm, "end": v(144.4, -263.16) * mm});
            skLineSegment(sketch, "E5215", {"start": v(144.4, -263.16) * mm, "end": v(145.18, -264.05) * mm});
            skLineSegment(sketch, "E5216", {"start": v(145.18, -264.05) * mm, "end": v(145.88, -265.07) * mm});
            skLineSegment(sketch, "E5217", {"start": v(145.88, -265.07) * mm, "end": v(146.5, -266.23) * mm});
            skLineSegment(sketch, "E5218", {"start": v(146.5, -266.23) * mm, "end": v(147.04, -267.5) * mm});
            skLineSegment(sketch, "E5219", {"start": v(147.04, -267.5) * mm, "end": v(147.52, -268.9) * mm});
            skLineSegment(sketch, "E5220", {"start": v(147.52, -268.9) * mm, "end": v(147.93, -270.4) * mm});
            skLineSegment(sketch, "E5221", {"start": v(147.93, -270.4) * mm, "end": v(148.29, -271.98) * mm});
            skLineSegment(sketch, "E5222", {"start": v(148.29, -271.98) * mm, "end": v(148.58, -273.66) * mm});
            skLineSegment(sketch, "E5223", {"start": v(148.58, -273.66) * mm, "end": v(148.82, -275.42) * mm});
            skLineSegment(sketch, "E5224", {"start": v(148.82, -275.42) * mm, "end": v(149, -277.26) * mm});
            skLineSegment(sketch, "E5225", {"start": v(149, -277.26) * mm, "end": v(149.14, -279.15) * mm});
            skLineSegment(sketch, "E5226", {"start": v(149.14, -279.15) * mm, "end": v(149.24, -281.1) * mm});
            skLineSegment(sketch, "E5227", {"start": v(149.24, -281.1) * mm, "end": v(149.3, -283.1) * mm});
            skLineSegment(sketch, "E5228", {"start": v(149.3, -283.1) * mm, "end": v(149.31, -285.13) * mm});
            skLineSegment(sketch, "E5229", {"start": v(149.31, -285.13) * mm, "end": v(149.3, -287.2) * mm});
            skLineSegment(sketch, "E5230", {"start": v(149.3, -287.2) * mm, "end": v(149.25, -289.29) * mm});
            skLineSegment(sketch, "E5231", {"start": v(149.25, -289.29) * mm, "end": v(149.18, -291.39) * mm});
            skLineSegment(sketch, "E5232", {"start": v(149.18, -291.39) * mm, "end": v(149.09, -293.5) * mm});
            skLineSegment(sketch, "E5233", {"start": v(149.09, -293.5) * mm, "end": v(148.97, -295.6) * mm});
            skLineSegment(sketch, "E5234", {"start": v(148.97, -295.6) * mm, "end": v(148.84, -297.68) * mm});
            skLineSegment(sketch, "E5235", {"start": v(148.84, -297.68) * mm, "end": v(148.7, -299.75) * mm});
            skLineSegment(sketch, "E5236", {"start": v(148.7, -299.75) * mm, "end": v(148.55, -301.8) * mm});
            skLineSegment(sketch, "E5237", {"start": v(148.55, -301.8) * mm, "end": v(148.4, -303.8) * mm});
            skLineSegment(sketch, "E5238", {"start": v(148.4, -303.8) * mm, "end": v(148.24, -305.76) * mm});
            skLineSegment(sketch, "E5239", {"start": v(148.24, -305.76) * mm, "end": v(148.08, -307.67) * mm});
            skLineSegment(sketch, "E5240", {"start": v(148.08, -307.67) * mm, "end": v(147.93, -309.51) * mm});
            skLineSegment(sketch, "E5241", {"start": v(147.93, -309.51) * mm, "end": v(147.79, -311.29) * mm});
            skLineSegment(sketch, "E5242", {"start": v(147.79, -311.29) * mm, "end": v(147.66, -312.99) * mm});
            skLineSegment(sketch, "E5243", {"start": v(147.66, -312.99) * mm, "end": v(147.54, -314.6) * mm});
            skLineSegment(sketch, "E5244", {"start": v(147.54, -314.6) * mm, "end": v(147.45, -316.1) * mm});
            skLineSegment(sketch, "E5245", {"start": v(147.45, -316.1) * mm, "end": v(147.37, -317.52) * mm});
            skLineSegment(sketch, "E5246", {"start": v(147.37, -317.52) * mm, "end": v(147.33, -318.82) * mm});
            skLineSegment(sketch, "E5247", {"start": v(147.33, -318.82) * mm, "end": v(147.31, -320) * mm});
            skLineSegment(sketch, "E5248", {"start": v(147.31, -320) * mm, "end": v(148.52, -319) * mm});
            skLineSegment(sketch, "E5249", {"start": v(148.52, -319) * mm, "end": v(149.63, -317.94) * mm});
            skLineSegment(sketch, "E5250", {"start": v(149.63, -317.94) * mm, "end": v(150.65, -316.8) * mm});
            skLineSegment(sketch, "E5251", {"start": v(150.65, -316.8) * mm, "end": v(151.59, -315.58) * mm});
            skLineSegment(sketch, "E5252", {"start": v(151.59, -315.58) * mm, "end": v(152.44, -314.3) * mm});
            skLineSegment(sketch, "E5253", {"start": v(152.44, -314.3) * mm, "end": v(153.22, -312.95) * mm});
            skLineSegment(sketch, "E5254", {"start": v(153.22, -312.95) * mm, "end": v(153.92, -311.55) * mm});
            skLineSegment(sketch, "E5255", {"start": v(153.92, -311.55) * mm, "end": v(154.55, -310.09) * mm});
            skLineSegment(sketch, "E5256", {"start": v(154.55, -310.09) * mm, "end": v(155.1, -308.58) * mm});
            skLineSegment(sketch, "E5257", {"start": v(155.1, -308.58) * mm, "end": v(155.6, -307.02) * mm});
            skLineSegment(sketch, "E5258", {"start": v(155.6, -307.02) * mm, "end": v(156.03, -305.42) * mm});
            skLineSegment(sketch, "E5259", {"start": v(156.03, -305.42) * mm, "end": v(156.4, -303.77) * mm});
            skLineSegment(sketch, "E5260", {"start": v(156.4, -303.77) * mm, "end": v(156.72, -302.1) * mm});
            skLineSegment(sketch, "E5261", {"start": v(156.72, -302.1) * mm, "end": v(156.99, -300.38) * mm});
            skLineSegment(sketch, "E5262", {"start": v(156.99, -300.38) * mm, "end": v(157.2, -298.64) * mm});
            skLineSegment(sketch, "E5263", {"start": v(157.2, -298.64) * mm, "end": v(157.38, -296.87) * mm});
            skLineSegment(sketch, "E5264", {"start": v(157.38, -296.87) * mm, "end": v(157.5, -295.08) * mm});
            skLineSegment(sketch, "E5265", {"start": v(157.5, -295.08) * mm, "end": v(157.6, -293.27) * mm});
            skLineSegment(sketch, "E5266", {"start": v(157.6, -293.27) * mm, "end": v(157.65, -291.44) * mm});
            skLineSegment(sketch, "E5267", {"start": v(157.65, -291.44) * mm, "end": v(157.67, -289.6) * mm});
            skLineSegment(sketch, "E5268", {"start": v(157.67, -289.6) * mm, "end": v(157.66, -287.76) * mm});
            skLineSegment(sketch, "E5269", {"start": v(157.66, -287.76) * mm, "end": v(157.63, -285.92) * mm});
            skLineSegment(sketch, "E5270", {"start": v(157.63, -285.92) * mm, "end": v(157.58, -284.07) * mm});
            skLineSegment(sketch, "E5271", {"start": v(157.58, -284.07) * mm, "end": v(157.5, -282.22) * mm});
            skLineSegment(sketch, "E5272", {"start": v(157.5, -282.22) * mm, "end": v(157.42, -280.39) * mm});
            skLineSegment(sketch, "E5273", {"start": v(157.42, -280.39) * mm, "end": v(157.31, -278.56) * mm});
            skLineSegment(sketch, "E5274", {"start": v(157.31, -278.56) * mm, "end": v(157.2, -276.75) * mm});
            skLineSegment(sketch, "E5275", {"start": v(157.2, -276.75) * mm, "end": v(157.1, -274.96) * mm});
            skLineSegment(sketch, "E5276", {"start": v(157.1, -274.96) * mm, "end": v(156.97, -273.19) * mm});
            skLineSegment(sketch, "E5277", {"start": v(156.97, -273.19) * mm, "end": v(156.86, -271.44) * mm});
            skLineSegment(sketch, "E5278", {"start": v(156.86, -271.44) * mm, "end": v(156.75, -269.73) * mm});
            skLineSegment(sketch, "E5279", {"start": v(156.75, -269.73) * mm, "end": v(156.64, -268.05) * mm});
            skLineSegment(sketch, "E5280", {"start": v(156.64, -268.05) * mm, "end": v(156.55, -266.4) * mm});
            skLineSegment(sketch, "E5281", {"start": v(156.55, -266.4) * mm, "end": v(156.47, -264.8) * mm});
            skLineSegment(sketch, "E5282", {"start": v(156.47, -264.8) * mm, "end": v(156.41, -263.23) * mm});
            skLineSegment(sketch, "E5283", {"start": v(156.41, -263.23) * mm, "end": v(156.38, -261.72) * mm});
            skLineSegment(sketch, "E5284", {"start": v(156.38, -261.72) * mm, "end": v(156.36, -260.26) * mm});
            skLineSegment(sketch, "E5285", {"start": v(156.36, -260.26) * mm, "end": v(225.16, -260.26) * mm});
            skLineSegment(sketch, "E5286", {"start": v(225.16, -260.26) * mm, "end": v(225.16, -138.97) * mm});
            skLineSegment(sketch, "E5287", {"start": v(225.16, -138.97) * mm, "end": v(156.36, -138.97) * mm});
            skLineSegment(sketch, "E5288", {"start": v(156.36, -138.97) * mm, "end": v(156.35, -137.92) * mm});
            skLineSegment(sketch, "E5289", {"start": v(156.35, -137.92) * mm, "end": v(156.3, -136.75) * mm});
            skLineSegment(sketch, "E5290", {"start": v(156.3, -136.75) * mm, "end": v(156.25, -135.46) * mm});
            skLineSegment(sketch, "E5291", {"start": v(156.25, -135.46) * mm, "end": v(156.16, -134.05) * mm});
            skLineSegment(sketch, "E5292", {"start": v(156.16, -134.05) * mm, "end": v(156.06, -132.55) * mm});
            skLineSegment(sketch, "E5293", {"start": v(156.06, -132.55) * mm, "end": v(155.95, -130.95) * mm});
            skLineSegment(sketch, "E5294", {"start": v(155.95, -130.95) * mm, "end": v(155.82, -129.26) * mm});
            skLineSegment(sketch, "E5295", {"start": v(155.82, -129.26) * mm, "end": v(155.69, -127.5) * mm});
            skLineSegment(sketch, "E5296", {"start": v(155.69, -127.5) * mm, "end": v(155.55, -125.66) * mm});
            skLineSegment(sketch, "E5297", {"start": v(155.55, -125.66) * mm, "end": v(155.4, -123.77) * mm});
            skLineSegment(sketch, "E5298", {"start": v(155.4, -123.77) * mm, "end": v(155.27, -121.82) * mm});
            skLineSegment(sketch, "E5299", {"start": v(155.27, -121.82) * mm, "end": v(155.13, -119.82) * mm});
            skLineSegment(sketch, "E5300", {"start": v(155.13, -119.82) * mm, "end": v(155, -117.78) * mm});
            skLineSegment(sketch, "E5301", {"start": v(155, -117.78) * mm, "end": v(154.88, -115.72) * mm});
            skLineSegment(sketch, "E5302", {"start": v(154.88, -115.72) * mm, "end": v(154.77, -113.63) * mm});
            skLineSegment(sketch, "E5303", {"start": v(154.77, -113.63) * mm, "end": v(154.67, -111.54) * mm});
            skLineSegment(sketch, "E5304", {"start": v(154.67, -111.54) * mm, "end": v(154.6, -109.43) * mm});
            skLineSegment(sketch, "E5305", {"start": v(154.6, -109.43) * mm, "end": v(154.54, -107.33) * mm});
            skLineSegment(sketch, "E5306", {"start": v(154.54, -107.33) * mm, "end": v(154.51, -105.24) * mm});
            skLineSegment(sketch, "E5307", {"start": v(154.51, -105.24) * mm, "end": v(154.5, -103.17) * mm});
            skLineSegment(sketch, "E5308", {"start": v(154.5, -103.17) * mm, "end": v(154.54, -101.13) * mm});
            skLineSegment(sketch, "E5309", {"start": v(154.54, -101.13) * mm, "end": v(154.6, -99.12) * mm});
            skLineSegment(sketch, "E5310", {"start": v(154.6, -99.12) * mm, "end": v(154.7, -97.15) * mm});
            skLineSegment(sketch, "E5311", {"start": v(154.7, -97.15) * mm, "end": v(154.83, -95.24) * mm});
            skLineSegment(sketch, "E5312", {"start": v(154.83, -95.24) * mm, "end": v(155, -93.39) * mm});
            skLineSegment(sketch, "E5313", {"start": v(155, -93.39) * mm, "end": v(155.23, -91.6) * mm});
            skLineSegment(sketch, "E5314", {"start": v(155.23, -91.6) * mm, "end": v(155.5, -89.9) * mm});
            skLineSegment(sketch, "E5315", {"start": v(155.5, -89.9) * mm, "end": v(155.81, -88.27) * mm});
            skLineSegment(sketch, "E5316", {"start": v(155.81, -88.27) * mm, "end": v(156.19, -86.74) * mm});
            skLineSegment(sketch, "E5317", {"start": v(156.19, -86.74) * mm, "end": v(156.62, -85.3) * mm});
            skLineSegment(sketch, "E5318", {"start": v(156.62, -85.3) * mm, "end": v(157.1, -83.98) * mm});
            skLineSegment(sketch, "E5319", {"start": v(157.1, -83.98) * mm, "end": v(157.66, -82.77) * mm});
            skLineSegment(sketch, "E5320", {"start": v(157.66, -82.77) * mm, "end": v(158.28, -81.7) * mm});
            skLineSegment(sketch, "E5321", {"start": v(158.28, -81.7) * mm, "end": v(158.97, -80.74) * mm});
            skLineSegment(sketch, "E5322", {"start": v(158.97, -80.74) * mm, "end": v(159.73, -79.93) * mm});
            skLineSegment(sketch, "E5323", {"start": v(159.73, -79.93) * mm, "end": v(160.56, -79.28) * mm});
            skLineSegment(sketch, "E5324", {"start": v(160.56, -79.28) * mm, "end": v(161.67, -78.6) * mm});
            skLineSegment(sketch, "E5325", {"start": v(161.67, -78.6) * mm, "end": v(162.87, -78) * mm});
            skLineSegment(sketch, "E5326", {"start": v(162.87, -78) * mm, "end": v(164.17, -77.47) * mm});
            skLineSegment(sketch, "E5327", {"start": v(164.17, -77.47) * mm, "end": v(165.56, -77) * mm});
            skLineSegment(sketch, "E5328", {"start": v(165.56, -77) * mm, "end": v(167.04, -76.6) * mm});
            skLineSegment(sketch, "E5329", {"start": v(167.04, -76.6) * mm, "end": v(168.6, -76.23) * mm});
            skLineSegment(sketch, "E5330", {"start": v(168.6, -76.23) * mm, "end": v(170.22, -75.93) * mm});
            skLineSegment(sketch, "E5331", {"start": v(170.22, -75.93) * mm, "end": v(171.9, -75.68) * mm});
            skLineSegment(sketch, "E5332", {"start": v(171.9, -75.68) * mm, "end": v(173.66, -75.48) * mm});
            skLineSegment(sketch, "E5333", {"start": v(173.66, -75.48) * mm, "end": v(175.46, -75.32) * mm});
            skLineSegment(sketch, "E5334", {"start": v(175.46, -75.32) * mm, "end": v(177.32, -75.2) * mm});
            skLineSegment(sketch, "E5335", {"start": v(177.32, -75.2) * mm, "end": v(179.21, -75.13) * mm});
            skLineSegment(sketch, "E5336", {"start": v(179.21, -75.13) * mm, "end": v(181.15, -75.09) * mm});
            skLineSegment(sketch, "E5337", {"start": v(181.15, -75.09) * mm, "end": v(183.11, -75.08) * mm});
            skLineSegment(sketch, "E5338", {"start": v(183.11, -75.08) * mm, "end": v(185.1, -75.1) * mm});
            skLineSegment(sketch, "E5339", {"start": v(185.1, -75.1) * mm, "end": v(187.12, -75.15) * mm});
            skLineSegment(sketch, "E5340", {"start": v(187.12, -75.15) * mm, "end": v(189.15, -75.22) * mm});
            skLineSegment(sketch, "E5341", {"start": v(189.15, -75.22) * mm, "end": v(191.18, -75.32) * mm});
            skLineSegment(sketch, "E5342", {"start": v(191.18, -75.32) * mm, "end": v(193.22, -75.43) * mm});
            skLineSegment(sketch, "E5343", {"start": v(193.22, -75.43) * mm, "end": v(195.26, -75.56) * mm});
            skLineSegment(sketch, "E5344", {"start": v(195.26, -75.56) * mm, "end": v(197.28, -75.7) * mm});
            skLineSegment(sketch, "E5345", {"start": v(197.28, -75.7) * mm, "end": v(199.3, -75.86) * mm});
            skLineSegment(sketch, "E5346", {"start": v(199.3, -75.86) * mm, "end": v(201.29, -76.02) * mm});
            skLineSegment(sketch, "E5347", {"start": v(201.29, -76.02) * mm, "end": v(203.25, -76.18) * mm});
            skLineSegment(sketch, "E5348", {"start": v(203.25, -76.18) * mm, "end": v(205.19, -76.35) * mm});
            skLineSegment(sketch, "E5349", {"start": v(205.19, -76.35) * mm, "end": v(207.09, -76.51) * mm});
            skLineSegment(sketch, "E5350", {"start": v(207.09, -76.51) * mm, "end": v(208.94, -76.67) * mm});
            skLineSegment(sketch, "E5351", {"start": v(208.94, -76.67) * mm, "end": v(210.75, -76.82) * mm});
            skLineSegment(sketch, "E5352", {"start": v(210.75, -76.82) * mm, "end": v(212.5, -76.96) * mm});
            skLineSegment(sketch, "E5353", {"start": v(212.5, -76.96) * mm, "end": v(214.19, -77.09) * mm});
            skLineSegment(sketch, "E5354", {"start": v(214.19, -77.09) * mm, "end": v(215.81, -77.2) * mm});
            skLineSegment(sketch, "E5355", {"start": v(215.81, -77.2) * mm, "end": v(217.37, -77.29) * mm});
            skLineSegment(sketch, "E5356", {"start": v(217.37, -77.29) * mm, "end": v(218.84, -77.36) * mm});
            skLineSegment(sketch, "E5357", {"start": v(218.84, -77.36) * mm, "end": v(220.23, -77.4) * mm});
            skLineSegment(sketch, "E5358", {"start": v(220.23, -77.4) * mm, "end": v(221.53, -77.42) * mm});
            skLineSegment(sketch, "E5359", {"start": v(221.53, -77.42) * mm, "end": v(380.84, -77.42) * mm});
            skLineSegment(sketch, "E5360", {"start": v(380.84, -77.42) * mm, "end": v(382.14, -77.4) * mm});
            skLineSegment(sketch, "E5361", {"start": v(382.14, -77.4) * mm, "end": v(383.52, -77.36) * mm});
            skLineSegment(sketch, "E5362", {"start": v(383.52, -77.36) * mm, "end": v(384.98, -77.3) * mm});
            skLineSegment(sketch, "E5363", {"start": v(384.98, -77.3) * mm, "end": v(386.52, -77.2) * mm});
            skLineSegment(sketch, "E5364", {"start": v(386.52, -77.2) * mm, "end": v(388.12, -77.1) * mm});
            skLineSegment(sketch, "E5365", {"start": v(388.12, -77.1) * mm, "end": v(389.8, -76.98) * mm});
            skLineSegment(sketch, "E5366", {"start": v(389.8, -76.98) * mm, "end": v(391.53, -76.84) * mm});
            skLineSegment(sketch, "E5367", {"start": v(391.53, -76.84) * mm, "end": v(393.32, -76.7) * mm});
            skLineSegment(sketch, "E5368", {"start": v(393.32, -76.7) * mm, "end": v(395.16, -76.54) * mm});
            skLineSegment(sketch, "E5369", {"start": v(395.16, -76.54) * mm, "end": v(397.04, -76.37) * mm});
            skLineSegment(sketch, "E5370", {"start": v(397.04, -76.37) * mm, "end": v(398.96, -76.2) * mm});
            skLineSegment(sketch, "E5371", {"start": v(398.96, -76.2) * mm, "end": v(400.91, -76.04) * mm});
            skLineSegment(sketch, "E5372", {"start": v(400.91, -76.04) * mm, "end": v(402.9, -75.88) * mm});
            skLineSegment(sketch, "E5373", {"start": v(402.9, -75.88) * mm, "end": v(404.9, -75.72) * mm});
            skLineSegment(sketch, "E5374", {"start": v(404.9, -75.72) * mm, "end": v(406.93, -75.56) * mm});
            skLineSegment(sketch, "E5375", {"start": v(406.93, -75.56) * mm, "end": v(408.97, -75.42) * mm});
            skLineSegment(sketch, "E5376", {"start": v(408.97, -75.42) * mm, "end": v(411.01, -75.29) * mm});
            skLineSegment(sketch, "E5377", {"start": v(411.01, -75.29) * mm, "end": v(413.06, -75.17) * mm});
            skLineSegment(sketch, "E5378", {"start": v(413.06, -75.17) * mm, "end": v(415.1, -75.07) * mm});
            skLineSegment(sketch, "E5379", {"start": v(415.1, -75.07) * mm, "end": v(417.14, -75) * mm});
            skLineSegment(sketch, "E5380", {"start": v(417.14, -75) * mm, "end": v(419.16, -74.94) * mm});
            skLineSegment(sketch, "E5381", {"start": v(419.16, -74.94) * mm, "end": v(421.17, -74.9) * mm});
            skLineSegment(sketch, "E5382", {"start": v(421.17, -74.9) * mm, "end": v(423.15, -74.9) * mm});
            skLineSegment(sketch, "E5383", {"start": v(423.15, -74.9) * mm, "end": v(425.1, -74.93) * mm});
            skLineSegment(sketch, "E5384", {"start": v(425.1, -74.93) * mm, "end": v(427.02, -75) * mm});
            skLineSegment(sketch, "E5385", {"start": v(427.02, -75) * mm, "end": v(428.9, -75.1) * mm});
            skLineSegment(sketch, "E5386", {"start": v(428.9, -75.1) * mm, "end": v(430.73, -75.23) * mm});
            skLineSegment(sketch, "E5387", {"start": v(430.73, -75.23) * mm, "end": v(432.51, -75.4) * mm});
            skLineSegment(sketch, "E5388", {"start": v(432.51, -75.4) * mm, "end": v(434.24, -75.62) * mm});
            skLineSegment(sketch, "E5389", {"start": v(434.24, -75.62) * mm, "end": v(435.9, -75.9) * mm});
            skLineSegment(sketch, "E5390", {"start": v(435.9, -75.9) * mm, "end": v(437.5, -76.2) * mm});
            skLineSegment(sketch, "E5391", {"start": v(437.5, -76.2) * mm, "end": v(439.04, -76.57) * mm});
            skLineSegment(sketch, "E5392", {"start": v(439.04, -76.57) * mm, "end": v(440.5, -77) * mm});
            skLineSegment(sketch, "E5393", {"start": v(440.5, -77) * mm, "end": v(441.86, -77.47) * mm});
            skLineSegment(sketch, "E5394", {"start": v(441.86, -77.47) * mm, "end": v(443.15, -78.01) * mm});
            skLineSegment(sketch, "E5395", {"start": v(443.15, -78.01) * mm, "end": v(444.34, -78.61) * mm});
            skLineSegment(sketch, "E5396", {"start": v(444.34, -78.61) * mm, "end": v(445.44, -79.28) * mm});
            skLineSegment(sketch, "E5397", {"start": v(445.44, -79.28) * mm, "end": v(446.08, -79.8) * mm});
            skLineSegment(sketch, "E5398", {"start": v(446.08, -79.8) * mm, "end": v(446.68, -80.53) * mm});
            skLineSegment(sketch, "E5399", {"start": v(446.68, -80.53) * mm, "end": v(447.24, -81.42) * mm});
            skLineSegment(sketch, "E5400", {"start": v(447.24, -81.42) * mm, "end": v(447.77, -82.47) * mm});
            skLineSegment(sketch, "E5401", {"start": v(447.77, -82.47) * mm, "end": v(448.26, -83.67) * mm});
            skLineSegment(sketch, "E5402", {"start": v(448.26, -83.67) * mm, "end": v(448.72, -85.02) * mm});
            skLineSegment(sketch, "E5403", {"start": v(448.72, -85.02) * mm, "end": v(449.14, -86.5) * mm});
            skLineSegment(sketch, "E5404", {"start": v(449.14, -86.5) * mm, "end": v(449.52, -88.09) * mm});
            skLineSegment(sketch, "E5405", {"start": v(449.52, -88.09) * mm, "end": v(449.87, -89.79) * mm});
            skLineSegment(sketch, "E5406", {"start": v(449.87, -89.79) * mm, "end": v(450.18, -91.59) * mm});
            skLineSegment(sketch, "E5407", {"start": v(450.18, -91.59) * mm, "end": v(450.45, -93.47) * mm});
            skLineSegment(sketch, "E5408", {"start": v(450.45, -93.47) * mm, "end": v(450.69, -95.44) * mm});
            skLineSegment(sketch, "E5409", {"start": v(450.69, -95.44) * mm, "end": v(450.89, -97.46) * mm});
            skLineSegment(sketch, "E5410", {"start": v(450.89, -97.46) * mm, "end": v(451.05, -99.54) * mm});
            skLineSegment(sketch, "E5411", {"start": v(451.05, -99.54) * mm, "end": v(451.18, -101.67) * mm});
            skLineSegment(sketch, "E5412", {"start": v(451.18, -101.67) * mm, "end": v(451.27, -103.82) * mm});
            skLineSegment(sketch, "E5413", {"start": v(451.27, -103.82) * mm, "end": v(451.32, -106) * mm});
            skLineSegment(sketch, "E5414", {"start": v(451.32, -106) * mm, "end": v(451.34, -108.2) * mm});
            skLineSegment(sketch, "E5415", {"start": v(451.34, -108.2) * mm, "end": v(451.32, -110.38) * mm});
            skLineSegment(sketch, "E5416", {"start": v(451.32, -110.38) * mm, "end": v(451.27, -112.56) * mm});
            skLineSegment(sketch, "E5417", {"start": v(451.27, -112.56) * mm, "end": v(451.18, -114.72) * mm});
            skLineSegment(sketch, "E5418", {"start": v(451.18, -114.72) * mm, "end": v(451.05, -116.84) * mm});
            skLineSegment(sketch, "E5419", {"start": v(451.05, -116.84) * mm, "end": v(450.89, -118.92) * mm});
            skLineSegment(sketch, "E5420", {"start": v(450.89, -118.92) * mm, "end": v(450.69, -120.95) * mm});
            skLineSegment(sketch, "E5421", {"start": v(450.69, -120.95) * mm, "end": v(450.45, -122.9) * mm});
            skLineSegment(sketch, "E5422", {"start": v(450.45, -122.9) * mm, "end": v(450.18, -124.8) * mm});
            skLineSegment(sketch, "E5423", {"start": v(450.18, -124.8) * mm, "end": v(449.87, -126.6) * mm});
            skLineSegment(sketch, "E5424", {"start": v(449.87, -126.6) * mm, "end": v(449.52, -128.3) * mm});
            skLineSegment(sketch, "E5425", {"start": v(449.52, -128.3) * mm, "end": v(449.14, -129.89) * mm});
            skLineSegment(sketch, "E5426", {"start": v(449.14, -129.89) * mm, "end": v(448.72, -131.36) * mm});
            skLineSegment(sketch, "E5427", {"start": v(448.72, -131.36) * mm, "end": v(448.26, -132.7) * mm});
            skLineSegment(sketch, "E5428", {"start": v(448.26, -132.7) * mm, "end": v(447.77, -133.91) * mm});
            skLineSegment(sketch, "E5429", {"start": v(447.77, -133.91) * mm, "end": v(447.24, -134.97) * mm});
            skLineSegment(sketch, "E5430", {"start": v(447.24, -134.97) * mm, "end": v(446.68, -135.86) * mm});
            skLineSegment(sketch, "E5431", {"start": v(446.68, -135.86) * mm, "end": v(446.08, -136.57) * mm});
            skLineSegment(sketch, "E5432", {"start": v(446.08, -136.57) * mm, "end": v(445.44, -137.1) * mm});
            skLineSegment(sketch, "E5433", {"start": v(445.44, -137.1) * mm, "end": v(444.35, -137.77) * mm});
            skLineSegment(sketch, "E5434", {"start": v(444.35, -137.77) * mm, "end": v(443.16, -138.37) * mm});
            skLineSegment(sketch, "E5435", {"start": v(443.16, -138.37) * mm, "end": v(441.88, -138.91) * mm});
            skLineSegment(sketch, "E5436", {"start": v(441.88, -138.91) * mm, "end": v(440.52, -139.4) * mm});
            skLineSegment(sketch, "E5437", {"start": v(440.52, -139.4) * mm, "end": v(439.07, -139.82) * mm});
            skLineSegment(sketch, "E5438", {"start": v(439.07, -139.82) * mm, "end": v(437.55, -140.2) * mm});
            skLineSegment(sketch, "E5439", {"start": v(437.55, -140.2) * mm, "end": v(435.96, -140.52) * mm});
            skLineSegment(sketch, "E5440", {"start": v(435.96, -140.52) * mm, "end": v(434.3, -140.8) * mm});
            skLineSegment(sketch, "E5441", {"start": v(434.3, -140.8) * mm, "end": v(432.6, -141.02) * mm});
            skLineSegment(sketch, "E5442", {"start": v(432.6, -141.02) * mm, "end": v(430.82, -141.2) * mm});
            skLineSegment(sketch, "E5443", {"start": v(430.82, -141.2) * mm, "end": v(429, -141.35) * mm});
            skLineSegment(sketch, "E5444", {"start": v(429, -141.35) * mm, "end": v(427.13, -141.46) * mm});
            skLineSegment(sketch, "E5445", {"start": v(427.13, -141.46) * mm, "end": v(425.22, -141.53) * mm});
            skLineSegment(sketch, "E5446", {"start": v(425.22, -141.53) * mm, "end": v(423.28, -141.57) * mm});
            skLineSegment(sketch, "E5447", {"start": v(423.28, -141.57) * mm, "end": v(421.3, -141.58) * mm});
            skLineSegment(sketch, "E5448", {"start": v(421.3, -141.58) * mm, "end": v(419.31, -141.55) * mm});
            skLineSegment(sketch, "E5449", {"start": v(419.31, -141.55) * mm, "end": v(417.3, -141.5) * mm});
            skLineSegment(sketch, "E5450", {"start": v(417.3, -141.5) * mm, "end": v(415.26, -141.44) * mm});
            skLineSegment(sketch, "E5451", {"start": v(415.26, -141.44) * mm, "end": v(413.21, -141.35) * mm});
            skLineSegment(sketch, "E5452", {"start": v(413.21, -141.35) * mm, "end": v(411.17, -141.24) * mm});
            skLineSegment(sketch, "E5453", {"start": v(411.17, -141.24) * mm, "end": v(409.12, -141.11) * mm});
            skLineSegment(sketch, "E5454", {"start": v(409.12, -141.11) * mm, "end": v(407.07, -140.97) * mm});
            skLineSegment(sketch, "E5455", {"start": v(407.07, -140.97) * mm, "end": v(405.03, -140.82) * mm});
            skLineSegment(sketch, "E5456", {"start": v(405.03, -140.82) * mm, "end": v(403.01, -140.66) * mm});
            skLineSegment(sketch, "E5457", {"start": v(403.01, -140.66) * mm, "end": v(401.01, -140.5) * mm});
            skLineSegment(sketch, "E5458", {"start": v(401.01, -140.5) * mm, "end": v(399.03, -140.33) * mm});
            skLineSegment(sketch, "E5459", {"start": v(399.03, -140.33) * mm, "end": v(397.08, -140.17) * mm});
            skLineSegment(sketch, "E5460", {"start": v(397.08, -140.17) * mm, "end": v(395.17, -140) * mm});
            skLineSegment(sketch, "E5461", {"start": v(395.17, -140) * mm, "end": v(393.3, -139.84) * mm});
            skLineSegment(sketch, "E5462", {"start": v(393.3, -139.84) * mm, "end": v(391.47, -139.68) * mm});
            skLineSegment(sketch, "E5463", {"start": v(391.47, -139.68) * mm, "end": v(389.69, -139.53) * mm});
            skLineSegment(sketch, "E5464", {"start": v(389.69, -139.53) * mm, "end": v(387.96, -139.4) * mm});
            skLineSegment(sketch, "E5465", {"start": v(387.96, -139.4) * mm, "end": v(386.3, -139.28) * mm});
            skLineSegment(sketch, "E5466", {"start": v(386.3, -139.28) * mm, "end": v(384.7, -139.17) * mm});
            skLineSegment(sketch, "E5467", {"start": v(384.7, -139.17) * mm, "end": v(383.16, -139.09) * mm});
            skLineSegment(sketch, "E5468", {"start": v(383.16, -139.09) * mm, "end": v(381.7, -139.02) * mm});
            skLineSegment(sketch, "E5469", {"start": v(381.7, -139.02) * mm, "end": v(380.33, -138.98) * mm});
            skLineSegment(sketch, "E5470", {"start": v(380.33, -138.98) * mm, "end": v(379.03, -138.97) * mm});
            skLineSegment(sketch, "E5471", {"start": v(379.03, -138.97) * mm, "end": v(379.03, -260.26) * mm});
            skLineSegment(sketch, "E5472", {"start": v(379.03, -260.26) * mm, "end": v(380.3, -260.28) * mm});
            skLineSegment(sketch, "E5473", {"start": v(380.3, -260.28) * mm, "end": v(381.69, -260.33) * mm});
            skLineSegment(sketch, "E5474", {"start": v(381.69, -260.33) * mm, "end": v(383.17, -260.4) * mm});
            skLineSegment(sketch, "E5475", {"start": v(383.17, -260.4) * mm, "end": v(384.75, -260.51) * mm});
            skLineSegment(sketch, "E5476", {"start": v(384.75, -260.51) * mm, "end": v(386.41, -260.63) * mm});
            skLineSegment(sketch, "E5477", {"start": v(386.41, -260.63) * mm, "end": v(388.15, -260.77) * mm});
            skLineSegment(sketch, "E5478", {"start": v(388.15, -260.77) * mm, "end": v(389.96, -260.92) * mm});
            skLineSegment(sketch, "E5479", {"start": v(389.96, -260.92) * mm, "end": v(391.82, -261.07) * mm});
            skLineSegment(sketch, "E5480", {"start": v(391.82, -261.07) * mm, "end": v(393.73, -261.21) * mm});
            skLineSegment(sketch, "E5481", {"start": v(393.73, -261.21) * mm, "end": v(395.67, -261.36) * mm});
            skLineSegment(sketch, "E5482", {"start": v(395.67, -261.36) * mm, "end": v(397.64, -261.49) * mm});
            skLineSegment(sketch, "E5483", {"start": v(397.64, -261.49) * mm, "end": v(399.64, -261.6) * mm});
            skLineSegment(sketch, "E5484", {"start": v(399.64, -261.6) * mm, "end": v(401.64, -261.7) * mm});
            skLineSegment(sketch, "E5485", {"start": v(401.64, -261.7) * mm, "end": v(403.64, -261.77) * mm});
            skLineSegment(sketch, "E5486", {"start": v(403.64, -261.77) * mm, "end": v(405.62, -261.81) * mm});
            skLineSegment(sketch, "E5487", {"start": v(405.62, -261.81) * mm, "end": v(407.6, -261.82) * mm});
            skLineSegment(sketch, "E5488", {"start": v(407.6, -261.82) * mm, "end": v(409.54, -261.78) * mm});
            skLineSegment(sketch, "E5489", {"start": v(409.54, -261.78) * mm, "end": v(411.44, -261.7) * mm});
            skLineSegment(sketch, "E5490", {"start": v(411.44, -261.7) * mm, "end": v(413.3, -261.57) * mm});
            skLineSegment(sketch, "E5491", {"start": v(413.3, -261.57) * mm, "end": v(415.1, -261.39) * mm});
            skLineSegment(sketch, "E5492", {"start": v(415.1, -261.39) * mm, "end": v(416.82, -261.14) * mm});
            skLineSegment(sketch, "E5493", {"start": v(416.82, -261.14) * mm, "end": v(418.48, -260.83) * mm});
            skLineSegment(sketch, "E5494", {"start": v(418.48, -260.83) * mm, "end": v(420.04, -260.46) * mm});
            skLineSegment(sketch, "E5495", {"start": v(420.04, -260.46) * mm, "end": v(421.52, -260) * mm});
            skLineSegment(sketch, "E5496", {"start": v(421.52, -260) * mm, "end": v(422.89, -259.47) * mm});
            skLineSegment(sketch, "E5497", {"start": v(422.89, -259.47) * mm, "end": v(424.14, -258.86) * mm});
            skLineSegment(sketch, "E5498", {"start": v(424.14, -258.86) * mm, "end": v(425.28, -258.15) * mm});
            skLineSegment(sketch, "E5499", {"start": v(425.28, -258.15) * mm, "end": v(426.28, -257.36) * mm});
            skLineSegment(sketch, "E5500", {"start": v(426.28, -257.36) * mm, "end": v(427.44, -256.26) * mm});
            skLineSegment(sketch, "E5501", {"start": v(427.44, -256.26) * mm, "end": v(428.57, -255.1) * mm});
            skLineSegment(sketch, "E5502", {"start": v(428.57, -255.1) * mm, "end": v(429.68, -253.87) * mm});
            skLineSegment(sketch, "E5503", {"start": v(429.68, -253.87) * mm, "end": v(430.77, -252.6) * mm});
            skLineSegment(sketch, "E5504", {"start": v(430.77, -252.6) * mm, "end": v(431.83, -251.26) * mm});
            skLineSegment(sketch, "E5505", {"start": v(431.83, -251.26) * mm, "end": v(432.87, -249.88) * mm});
            skLineSegment(sketch, "E5506", {"start": v(432.87, -249.88) * mm, "end": v(433.89, -248.45) * mm});
            skLineSegment(sketch, "E5507", {"start": v(433.89, -248.45) * mm, "end": v(434.88, -246.98) * mm});
            skLineSegment(sketch, "E5508", {"start": v(434.88, -246.98) * mm, "end": v(435.86, -245.47) * mm});
            skLineSegment(sketch, "E5509", {"start": v(435.86, -245.47) * mm, "end": v(436.8, -243.92) * mm});
            skLineSegment(sketch, "E5510", {"start": v(436.8, -243.92) * mm, "end": v(437.74, -242.34) * mm});
            skLineSegment(sketch, "E5511", {"start": v(437.74, -242.34) * mm, "end": v(438.65, -240.72) * mm});
            skLineSegment(sketch, "E5512", {"start": v(438.65, -240.72) * mm, "end": v(439.55, -239.08) * mm});
            skLineSegment(sketch, "E5513", {"start": v(439.55, -239.08) * mm, "end": v(440.43, -237.41) * mm});
            skLineSegment(sketch, "E5514", {"start": v(440.43, -237.41) * mm, "end": v(441.28, -235.73) * mm});
            skLineSegment(sketch, "E5515", {"start": v(441.28, -235.73) * mm, "end": v(442.12, -234.02) * mm});
            skLineSegment(sketch, "E5516", {"start": v(442.12, -234.02) * mm, "end": v(442.95, -232.3) * mm});
            skLineSegment(sketch, "E5517", {"start": v(442.95, -232.3) * mm, "end": v(443.76, -230.57) * mm});
            skLineSegment(sketch, "E5518", {"start": v(443.76, -230.57) * mm, "end": v(444.55, -228.82) * mm});
            skLineSegment(sketch, "E5519", {"start": v(444.55, -228.82) * mm, "end": v(445.33, -227.08) * mm});
            skLineSegment(sketch, "E5520", {"start": v(445.33, -227.08) * mm, "end": v(446.09, -225.33) * mm});
            skLineSegment(sketch, "E5521", {"start": v(446.09, -225.33) * mm, "end": v(446.84, -223.58) * mm});
            skLineSegment(sketch, "E5522", {"start": v(446.84, -223.58) * mm, "end": v(447.57, -221.83) * mm});
            skLineSegment(sketch, "E5523", {"start": v(447.57, -221.83) * mm, "end": v(448.3, -220.1) * mm});
            skLineSegment(sketch, "E5524", {"start": v(448.3, -220.1) * mm, "end": v(449, -218.36) * mm});
            skLineSegment(sketch, "E5525", {"start": v(449, -218.36) * mm, "end": v(449.7, -216.65) * mm});
            skLineSegment(sketch, "E5526", {"start": v(449.7, -216.65) * mm, "end": v(450.4, -214.95) * mm});
            skLineSegment(sketch, "E5527", {"start": v(450.4, -214.95) * mm, "end": v(451.07, -213.27) * mm});
            skLineSegment(sketch, "E5528", {"start": v(451.07, -213.27) * mm, "end": v(451.74, -211.61) * mm});
            skLineSegment(sketch, "E5529", {"start": v(451.74, -211.61) * mm, "end": v(452.4, -209.98) * mm});
            skLineSegment(sketch, "E5530", {"start": v(452.4, -209.98) * mm, "end": v(453.05, -208.38) * mm});
            skLineSegment(sketch, "E5531", {"start": v(453.05, -208.38) * mm, "end": v(453.7, -206.81) * mm});
            skLineSegment(sketch, "E5532", {"start": v(453.7, -206.81) * mm, "end": v(454.33, -205.28) * mm});
            skLineSegment(sketch, "E5533", {"start": v(454.33, -205.28) * mm, "end": v(454.95, -203.78) * mm});
            skLineSegment(sketch, "E5534", {"start": v(454.95, -203.78) * mm, "end": v(455.58, -202.33) * mm});
            skLineSegment(sketch, "E5535", {"start": v(455.58, -202.33) * mm, "end": v(456.3, -200.65) * mm});
            skLineSegment(sketch, "E5536", {"start": v(456.3, -200.65) * mm, "end": v(457.02, -198.96) * mm});
            skLineSegment(sketch, "E5537", {"start": v(457.02, -198.96) * mm, "end": v(457.73, -197.28) * mm});
            skLineSegment(sketch, "E5538", {"start": v(457.73, -197.28) * mm, "end": v(458.43, -195.6) * mm});
            skLineSegment(sketch, "E5539", {"start": v(458.43, -195.6) * mm, "end": v(459.13, -193.9) * mm});
            skLineSegment(sketch, "E5540", {"start": v(459.13, -193.9) * mm, "end": v(459.83, -192.21) * mm});
            skLineSegment(sketch, "E5541", {"start": v(459.83, -192.21) * mm, "end": v(460.52, -190.52) * mm});
            skLineSegment(sketch, "E5542", {"start": v(460.52, -190.52) * mm, "end": v(461.2, -188.83) * mm});
            skLineSegment(sketch, "E5543", {"start": v(461.2, -188.83) * mm, "end": v(461.88, -187.14) * mm});
            skLineSegment(sketch, "E5544", {"start": v(461.88, -187.14) * mm, "end": v(462.55, -185.44) * mm});
            skLineSegment(sketch, "E5545", {"start": v(462.55, -185.44) * mm, "end": v(463.22, -183.75) * mm});
            skLineSegment(sketch, "E5546", {"start": v(463.22, -183.75) * mm, "end": v(463.88, -182.05) * mm});
            skLineSegment(sketch, "E5547", {"start": v(463.88, -182.05) * mm, "end": v(464.53, -180.35) * mm});
            skLineSegment(sketch, "E5548", {"start": v(464.53, -180.35) * mm, "end": v(465.18, -178.65) * mm});
            skLineSegment(sketch, "E5549", {"start": v(465.18, -178.65) * mm, "end": v(465.82, -176.95) * mm});
            skLineSegment(sketch, "E5550", {"start": v(465.82, -176.95) * mm, "end": v(466.46, -175.24) * mm});
            skLineSegment(sketch, "E5551", {"start": v(466.46, -175.24) * mm, "end": v(467.1, -173.54) * mm});
            skLineSegment(sketch, "E5552", {"start": v(467.1, -173.54) * mm, "end": v(467.72, -171.83) * mm});
            skLineSegment(sketch, "E5553", {"start": v(467.72, -171.83) * mm, "end": v(468.34, -170.12) * mm});
            skLineSegment(sketch, "E5554", {"start": v(468.34, -170.12) * mm, "end": v(468.95, -168.41) * mm});
            skLineSegment(sketch, "E5555", {"start": v(468.95, -168.41) * mm, "end": v(469.56, -166.7) * mm});
            skLineSegment(sketch, "E5556", {"start": v(469.56, -166.7) * mm, "end": v(470.16, -164.99) * mm});
            skLineSegment(sketch, "E5557", {"start": v(470.16, -164.99) * mm, "end": v(470.76, -163.28) * mm});
            skLineSegment(sketch, "E5558", {"start": v(470.76, -163.28) * mm, "end": v(471.35, -161.56) * mm});
            skLineSegment(sketch, "E5559", {"start": v(471.35, -161.56) * mm, "end": v(471.93, -159.84) * mm});
            skLineSegment(sketch, "E5560", {"start": v(471.93, -159.84) * mm, "end": v(472.51, -158.12) * mm});
            skLineSegment(sketch, "E5561", {"start": v(472.51, -158.12) * mm, "end": v(473.08, -156.4) * mm});
            skLineSegment(sketch, "E5562", {"start": v(473.08, -156.4) * mm, "end": v(473.65, -154.68) * mm});
            skLineSegment(sketch, "E5563", {"start": v(473.65, -154.68) * mm, "end": v(474.2, -152.96) * mm});
            skLineSegment(sketch, "E5564", {"start": v(474.2, -152.96) * mm, "end": v(474.76, -151.24) * mm});
            skLineSegment(sketch, "E5565", {"start": v(474.76, -151.24) * mm, "end": v(475.31, -149.51) * mm});
            skLineSegment(sketch, "E5566", {"start": v(475.31, -149.51) * mm, "end": v(475.85, -147.78) * mm});
            skLineSegment(sketch, "E5567", {"start": v(475.85, -147.78) * mm, "end": v(476.39, -146.05) * mm});
            skLineSegment(sketch, "E5568", {"start": v(476.39, -146.05) * mm, "end": v(476.92, -144.32) * mm});
            skLineSegment(sketch, "E5569", {"start": v(476.92, -144.32) * mm, "end": v(477.44, -142.6) * mm});
            skLineSegment(sketch, "E5570", {"start": v(477.44, -142.6) * mm, "end": v(477.96, -140.86) * mm});
            skLineSegment(sketch, "E5571", {"start": v(477.96, -140.86) * mm, "end": v(478.47, -139.12) * mm});
            skLineSegment(sketch, "E5572", {"start": v(478.47, -139.12) * mm, "end": v(478.98, -137.39) * mm});
            skLineSegment(sketch, "E5573", {"start": v(478.98, -137.39) * mm, "end": v(479.48, -135.65) * mm});
            skLineSegment(sketch, "E5574", {"start": v(479.48, -135.65) * mm, "end": v(479.97, -133.9) * mm});
            skLineSegment(sketch, "E5575", {"start": v(479.97, -133.9) * mm, "end": v(480.45, -132.17) * mm});
            skLineSegment(sketch, "E5576", {"start": v(480.45, -132.17) * mm, "end": v(480.93, -130.43) * mm});
            skLineSegment(sketch, "E5577", {"start": v(480.93, -130.43) * mm, "end": v(481.4, -128.68) * mm});
            skLineSegment(sketch, "E5578", {"start": v(481.4, -128.68) * mm, "end": v(481.88, -126.94) * mm});
            skLineSegment(sketch, "E5579", {"start": v(481.88, -126.94) * mm, "end": v(482.34, -125.19) * mm});
            skLineSegment(sketch, "E5580", {"start": v(482.34, -125.19) * mm, "end": v(482.8, -123.44) * mm});
            skLineSegment(sketch, "E5581", {"start": v(482.8, -123.44) * mm, "end": v(483.24, -121.69) * mm});
            skLineSegment(sketch, "E5582", {"start": v(483.24, -121.69) * mm, "end": v(483.68, -119.94) * mm});
            skLineSegment(sketch, "E5583", {"start": v(483.68, -119.94) * mm, "end": v(484.12, -118.18) * mm});
            skLineSegment(sketch, "E5584", {"start": v(484.12, -118.18) * mm, "end": v(484.55, -116.43) * mm});
            skLineSegment(sketch, "E5585", {"start": v(484.55, -116.43) * mm, "end": v(484.97, -114.67) * mm});
            skLineSegment(sketch, "E5586", {"start": v(484.97, -114.67) * mm, "end": v(485.39, -112.91) * mm});
            skLineSegment(sketch, "E5587", {"start": v(485.39, -112.91) * mm, "end": v(485.8, -111.15) * mm});
            skLineSegment(sketch, "E5588", {"start": v(485.8, -111.15) * mm, "end": v(486.2, -109.4) * mm});
            skLineSegment(sketch, "E5589", {"start": v(486.2, -109.4) * mm, "end": v(486.6, -107.63) * mm});
            skLineSegment(sketch, "E5590", {"start": v(486.6, -107.63) * mm, "end": v(487, -105.86) * mm});
            skLineSegment(sketch, "E5591", {"start": v(487, -105.86) * mm, "end": v(487.38, -104.1) * mm});
            skLineSegment(sketch, "E5592", {"start": v(487.38, -104.1) * mm, "end": v(487.75, -102.33) * mm});
            skLineSegment(sketch, "E5593", {"start": v(487.75, -102.33) * mm, "end": v(488.12, -100.56) * mm});
            skLineSegment(sketch, "E5594", {"start": v(488.12, -100.56) * mm, "end": v(488.49, -98.79) * mm});
            skLineSegment(sketch, "E5595", {"start": v(488.49, -98.79) * mm, "end": v(488.85, -97.02) * mm});
            skLineSegment(sketch, "E5596", {"start": v(488.85, -97.02) * mm, "end": v(489.2, -95.24) * mm});
            skLineSegment(sketch, "E5597", {"start": v(489.2, -95.24) * mm, "end": v(489.54, -93.47) * mm});
            skLineSegment(sketch, "E5598", {"start": v(489.54, -93.47) * mm, "end": v(489.88, -91.69) * mm});
            skLineSegment(sketch, "E5599", {"start": v(489.88, -91.69) * mm, "end": v(490.21, -89.9) * mm});
            skLineSegment(sketch, "E5600", {"start": v(490.21, -89.9) * mm, "end": v(490.54, -88.13) * mm});
            skLineSegment(sketch, "E5601", {"start": v(490.54, -88.13) * mm, "end": v(490.86, -86.35) * mm});
            skLineSegment(sketch, "E5602", {"start": v(490.86, -86.35) * mm, "end": v(491.17, -84.56) * mm});
            skLineSegment(sketch, "E5603", {"start": v(491.17, -84.56) * mm, "end": v(491.47, -82.78) * mm});
            skLineSegment(sketch, "E5604", {"start": v(491.47, -82.78) * mm, "end": v(491.77, -80.99) * mm});
            skLineSegment(sketch, "E5605", {"start": v(491.77, -80.99) * mm, "end": v(492.06, -79.2) * mm});
            skLineSegment(sketch, "E5606", {"start": v(492.06, -79.2) * mm, "end": v(492.35, -77.4) * mm});
            skLineSegment(sketch, "E5607", {"start": v(492.35, -77.4) * mm, "end": v(492.63, -75.62) * mm});
            skLineSegment(sketch, "E5608", {"start": v(492.63, -75.62) * mm, "end": v(492.9, -73.82) * mm});
            skLineSegment(sketch, "E5609", {"start": v(492.9, -73.82) * mm, "end": v(493.16, -72.03) * mm});
            skLineSegment(sketch, "E5610", {"start": v(493.16, -72.03) * mm, "end": v(493.42, -70.23) * mm});
            skLineSegment(sketch, "E5611", {"start": v(493.42, -70.23) * mm, "end": v(493.67, -68.43) * mm});
            skLineSegment(sketch, "E5612", {"start": v(493.67, -68.43) * mm, "end": v(493.91, -66.63) * mm});
            skLineSegment(sketch, "E5613", {"start": v(493.91, -66.63) * mm, "end": v(494.15, -64.83) * mm});
            skLineSegment(sketch, "E5614", {"start": v(494.15, -64.83) * mm, "end": v(494.38, -63.02) * mm});
            skLineSegment(sketch, "E5615", {"start": v(494.38, -63.02) * mm, "end": v(494.6, -61.22) * mm});
            skLineSegment(sketch, "E5616", {"start": v(494.6, -61.22) * mm, "end": v(494.82, -59.41) * mm});
            skLineSegment(sketch, "E5617", {"start": v(494.82, -59.41) * mm, "end": v(495.03, -57.6) * mm});
            skLineSegment(sketch, "E5618", {"start": v(495.03, -57.6) * mm, "end": v(495.23, -55.8) * mm});
            skLineSegment(sketch, "E5619", {"start": v(495.23, -55.8) * mm, "end": v(495.43, -53.98) * mm});
            skLineSegment(sketch, "E5620", {"start": v(495.43, -53.98) * mm, "end": v(495.61, -52.16) * mm});
            skLineSegment(sketch, "E5621", {"start": v(495.61, -52.16) * mm, "end": v(495.8, -50.35) * mm});
            skLineSegment(sketch, "E5622", {"start": v(495.8, -50.35) * mm, "end": v(495.97, -48.53) * mm});
            skLineSegment(sketch, "E5623", {"start": v(495.97, -48.53) * mm, "end": v(496.14, -46.71) * mm});
            skLineSegment(sketch, "E5624", {"start": v(496.14, -46.71) * mm, "end": v(496.3, -44.9) * mm});
            skLineSegment(sketch, "E5625", {"start": v(496.3, -44.9) * mm, "end": v(496.45, -43.07) * mm});
            skLineSegment(sketch, "E5626", {"start": v(496.45, -43.07) * mm, "end": v(496.6, -41.24) * mm});
            skLineSegment(sketch, "E5627", {"start": v(496.6, -41.24) * mm, "end": v(496.73, -39.42) * mm});
            skLineSegment(sketch, "E5628", {"start": v(496.73, -39.42) * mm, "end": v(496.87, -37.59) * mm});
            skLineSegment(sketch, "E5629", {"start": v(496.87, -37.59) * mm, "end": v(496.98, -36.12) * mm});
            skLineSegment(sketch, "E5630", {"start": v(496.98, -36.12) * mm, "end": v(497.1, -34.61) * mm});
            skLineSegment(sketch, "E5631", {"start": v(497.1, -34.61) * mm, "end": v(497.24, -33.06) * mm});
            skLineSegment(sketch, "E5632", {"start": v(497.24, -33.06) * mm, "end": v(497.4, -31.46) * mm});
            skLineSegment(sketch, "E5633", {"start": v(497.4, -31.46) * mm, "end": v(497.56, -29.83) * mm});
            skLineSegment(sketch, "E5634", {"start": v(497.56, -29.83) * mm, "end": v(497.74, -28.16) * mm});
            skLineSegment(sketch, "E5635", {"start": v(497.74, -28.16) * mm, "end": v(497.92, -26.45) * mm});
            skLineSegment(sketch, "E5636", {"start": v(497.92, -26.45) * mm, "end": v(498.1, -24.72) * mm});
            skLineSegment(sketch, "E5637", {"start": v(498.1, -24.72) * mm, "end": v(498.3, -22.95) * mm});
            skLineSegment(sketch, "E5638", {"start": v(498.3, -22.95) * mm, "end": v(498.48, -21.16) * mm});
            skLineSegment(sketch, "E5639", {"start": v(498.48, -21.16) * mm, "end": v(498.67, -19.35) * mm});
            skLineSegment(sketch, "E5640", {"start": v(498.67, -19.35) * mm, "end": v(498.85, -17.52) * mm});
            skLineSegment(sketch, "E5641", {"start": v(498.85, -17.52) * mm, "end": v(499.03, -15.66) * mm});
            skLineSegment(sketch, "E5642", {"start": v(499.03, -15.66) * mm, "end": v(499.2, -13.8) * mm});
            skLineSegment(sketch, "E5643", {"start": v(499.2, -13.8) * mm, "end": v(499.36, -11.91) * mm});
            skLineSegment(sketch, "E5644", {"start": v(499.36, -11.91) * mm, "end": v(499.5, -10.02) * mm});
            skLineSegment(sketch, "E5645", {"start": v(499.5, -10.02) * mm, "end": v(499.65, -8.12) * mm});
            skLineSegment(sketch, "E5646", {"start": v(499.65, -8.12) * mm, "end": v(499.77, -6.2) * mm});
            skLineSegment(sketch, "E5647", {"start": v(499.77, -6.2) * mm, "end": v(499.87, -4.3) * mm});
            skLineSegment(sketch, "E5648", {"start": v(499.87, -4.3) * mm, "end": v(499.95, -2.38) * mm});
            skLineSegment(sketch, "E5649", {"start": v(499.95, -2.38) * mm, "end": v(500.02, -0.46) * mm});
            skLineSegment(sketch, "E5650", {"start": v(500.02, -0.46) * mm, "end": v(500.06, 1.45) * mm});
            skLineSegment(sketch, "E5651", {"start": v(500.06, 1.45) * mm, "end": v(500.07, 3.35) * mm});
            skLineSegment(sketch, "E5652", {"start": v(500.07, 3.35) * mm, "end": v(500.06, 5.25) * mm});
            skLineSegment(sketch, "E5653", {"start": v(500.06, 5.25) * mm, "end": v(500.01, 7.14) * mm});
            skLineSegment(sketch, "E5654", {"start": v(500.01, 7.14) * mm, "end": v(499.94, 9) * mm});
            skLineSegment(sketch, "E5655", {"start": v(499.94, 9) * mm, "end": v(499.83, 10.87) * mm});
            skLineSegment(sketch, "E5656", {"start": v(499.83, 10.87) * mm, "end": v(499.69, 12.7) * mm});
            skLineSegment(sketch, "E5657", {"start": v(499.69, 12.7) * mm, "end": v(499.5, 14.52) * mm});
            skLineSegment(sketch, "E5658", {"start": v(499.5, 14.52) * mm, "end": v(499.28, 16.32) * mm});
            skLineSegment(sketch, "E5659", {"start": v(499.28, 16.32) * mm, "end": v(499.02, 18.09) * mm});
            skLineSegment(sketch, "E5660", {"start": v(499.02, 18.09) * mm, "end": v(498.72, 19.83) * mm});
            skLineSegment(sketch, "E5661", {"start": v(498.72, 19.83) * mm, "end": v(498.36, 21.54) * mm});
            skLineSegment(sketch, "E5662", {"start": v(498.36, 21.54) * mm, "end": v(497.97, 23.22) * mm});
            skLineSegment(sketch, "E5663", {"start": v(497.97, 23.22) * mm, "end": v(497.52, 24.86) * mm});
            skLineSegment(sketch, "E5664", {"start": v(497.52, 24.86) * mm, "end": v(497.02, 26.47) * mm});
            skLineSegment(sketch, "E5665", {"start": v(497.02, 26.47) * mm, "end": v(496.46, 28.03) * mm});
            skLineSegment(sketch, "E5666", {"start": v(496.46, 28.03) * mm, "end": v(495.85, 29.56) * mm});
            skLineSegment(sketch, "E5667", {"start": v(495.85, 29.56) * mm, "end": v(495.19, 31.04) * mm});
            skLineSegment(sketch, "E5668", {"start": v(495.19, 31.04) * mm, "end": v(494.46, 32.47) * mm});
            skLineSegment(sketch, "E5669", {"start": v(494.46, 32.47) * mm, "end": v(493.67, 33.84) * mm});
            skLineSegment(sketch, "E5670", {"start": v(493.67, 33.84) * mm, "end": v(492.82, 35.17) * mm});
            skLineSegment(sketch, "E5671", {"start": v(492.82, 35.17) * mm, "end": v(491.9, 36.44) * mm});
            skLineSegment(sketch, "E5672", {"start": v(491.9, 36.44) * mm, "end": v(490.72, 37.89) * mm});
            skLineSegment(sketch, "E5673", {"start": v(490.72, 37.89) * mm, "end": v(489.48, 39.18) * mm});
            skLineSegment(sketch, "E5674", {"start": v(489.48, 39.18) * mm, "end": v(488.21, 40.33) * mm});
            skLineSegment(sketch, "E5675", {"start": v(488.21, 40.33) * mm, "end": v(486.9, 41.35) * mm});
            skLineSegment(sketch, "E5676", {"start": v(486.9, 41.35) * mm, "end": v(485.54, 42.23) * mm});
            skLineSegment(sketch, "E5677", {"start": v(485.54, 42.23) * mm, "end": v(484.15, 43) * mm});
            skLineSegment(sketch, "E5678", {"start": v(484.15, 43) * mm, "end": v(482.73, 43.64) * mm});
            skLineSegment(sketch, "E5679", {"start": v(482.73, 43.64) * mm, "end": v(481.28, 44.17) * mm});
            skLineSegment(sketch, "E5680", {"start": v(481.28, 44.17) * mm, "end": v(479.8, 44.6) * mm});
            skLineSegment(sketch, "E5681", {"start": v(479.8, 44.6) * mm, "end": v(478.29, 44.95) * mm});
            skLineSegment(sketch, "E5682", {"start": v(478.29, 44.95) * mm, "end": v(476.75, 45.2) * mm});
            skLineSegment(sketch, "E5683", {"start": v(476.75, 45.2) * mm, "end": v(475.2, 45.37) * mm});
            skLineSegment(sketch, "E5684", {"start": v(475.2, 45.37) * mm, "end": v(473.62, 45.46) * mm});
            skLineSegment(sketch, "E5685", {"start": v(473.62, 45.46) * mm, "end": v(472.03, 45.49) * mm});
            skLineSegment(sketch, "E5686", {"start": v(472.03, 45.49) * mm, "end": v(470.42, 45.45) * mm});
            skLineSegment(sketch, "E5687", {"start": v(470.42, 45.45) * mm, "end": v(468.8, 45.36) * mm});
            skLineSegment(sketch, "E5688", {"start": v(468.8, 45.36) * mm, "end": v(467.16, 45.22) * mm});
            skLineSegment(sketch, "E5689", {"start": v(467.16, 45.22) * mm, "end": v(465.52, 45.04) * mm});
            skLineSegment(sketch, "E5690", {"start": v(465.52, 45.04) * mm, "end": v(463.88, 44.83) * mm});
            skLineSegment(sketch, "E5691", {"start": v(463.88, 44.83) * mm, "end": v(462.23, 44.6) * mm});
            skLineSegment(sketch, "E5692", {"start": v(462.23, 44.6) * mm, "end": v(460.57, 44.33) * mm});
            skLineSegment(sketch, "E5693", {"start": v(460.57, 44.33) * mm, "end": v(458.92, 44.06) * mm});
            skLineSegment(sketch, "E5694", {"start": v(458.92, 44.06) * mm, "end": v(457.27, 43.78) * mm});
            skLineSegment(sketch, "E5695", {"start": v(457.27, 43.78) * mm, "end": v(455.63, 43.5) * mm});
            skLineSegment(sketch, "E5696", {"start": v(455.63, 43.5) * mm, "end": v(454, 43.23) * mm});
            skLineSegment(sketch, "E5697", {"start": v(454, 43.23) * mm, "end": v(452.37, 42.98) * mm});
            skLineSegment(sketch, "E5698", {"start": v(452.37, 42.98) * mm, "end": v(450.76, 42.74) * mm});
            skLineSegment(sketch, "E5699", {"start": v(450.76, 42.74) * mm, "end": v(449.16, 42.53) * mm});
            skLineSegment(sketch, "E5700", {"start": v(449.16, 42.53) * mm, "end": v(447.58, 42.36) * mm});
            skLineSegment(sketch, "E5701", {"start": v(447.58, 42.36) * mm, "end": v(446.02, 42.23) * mm});
            skLineSegment(sketch, "E5702", {"start": v(446.02, 42.23) * mm, "end": v(444.22, 42.1) * mm});
            skLineSegment(sketch, "E5703", {"start": v(444.22, 42.1) * mm, "end": v(442.43, 42) * mm});
            skLineSegment(sketch, "E5704", {"start": v(442.43, 42) * mm, "end": v(440.63, 41.89) * mm});
            skLineSegment(sketch, "E5705", {"start": v(440.63, 41.89) * mm, "end": v(438.83, 41.79) * mm});
            skLineSegment(sketch, "E5706", {"start": v(438.83, 41.79) * mm, "end": v(437.03, 41.7) * mm});
            skLineSegment(sketch, "E5707", {"start": v(437.03, 41.7) * mm, "end": v(435.23, 41.61) * mm});
            skLineSegment(sketch, "E5708", {"start": v(435.23, 41.61) * mm, "end": v(433.43, 41.53) * mm});
            skLineSegment(sketch, "E5709", {"start": v(433.43, 41.53) * mm, "end": v(431.63, 41.46) * mm});
            skLineSegment(sketch, "E5710", {"start": v(431.63, 41.46) * mm, "end": v(429.83, 41.4) * mm});
            skLineSegment(sketch, "E5711", {"start": v(429.83, 41.4) * mm, "end": v(428.02, 41.34) * mm});
            skLineSegment(sketch, "E5712", {"start": v(428.02, 41.34) * mm, "end": v(426.21, 41.29) * mm});
            skLineSegment(sketch, "E5713", {"start": v(426.21, 41.29) * mm, "end": v(424.4, 41.24) * mm});
            skLineSegment(sketch, "E5714", {"start": v(424.4, 41.24) * mm, "end": v(422.6, 41.2) * mm});
            skLineSegment(sketch, "E5715", {"start": v(422.6, 41.2) * mm, "end": v(420.79, 41.16) * mm});
            skLineSegment(sketch, "E5716", {"start": v(420.79, 41.16) * mm, "end": v(418.98, 41.13) * mm});
            skLineSegment(sketch, "E5717", {"start": v(418.98, 41.13) * mm, "end": v(417.17, 41.1) * mm});
            skLineSegment(sketch, "E5718", {"start": v(417.17, 41.1) * mm, "end": v(415.35, 41.09) * mm});
            skLineSegment(sketch, "E5719", {"start": v(415.35, 41.09) * mm, "end": v(413.54, 41.07) * mm});
            skLineSegment(sketch, "E5720", {"start": v(413.54, 41.07) * mm, "end": v(411.73, 41.06) * mm});
            skLineSegment(sketch, "E5721", {"start": v(411.73, 41.06) * mm, "end": v(409.91, 41.05) * mm});
            skLineSegment(sketch, "E5722", {"start": v(409.91, 41.05) * mm, "end": v(408.1, 41.05) * mm});
            skLineSegment(sketch, "E5723", {"start": v(408.1, 41.05) * mm, "end": v(406.28, 41.05) * mm});
            skLineSegment(sketch, "E5724", {"start": v(406.28, 41.05) * mm, "end": v(404.47, 41.05) * mm});
            skLineSegment(sketch, "E5725", {"start": v(404.47, 41.05) * mm, "end": v(402.65, 41.06) * mm});
            skLineSegment(sketch, "E5726", {"start": v(402.65, 41.06) * mm, "end": v(400.83, 41.07) * mm});
            skLineSegment(sketch, "E5727", {"start": v(400.83, 41.07) * mm, "end": v(399.02, 41.09) * mm});
            skLineSegment(sketch, "E5728", {"start": v(399.02, 41.09) * mm, "end": v(397.2, 41.1) * mm});
            skLineSegment(sketch, "E5729", {"start": v(397.2, 41.1) * mm, "end": v(395.38, 41.13) * mm});
            skLineSegment(sketch, "E5730", {"start": v(395.38, 41.13) * mm, "end": v(393.56, 41.15) * mm});
            skLineSegment(sketch, "E5731", {"start": v(393.56, 41.15) * mm, "end": v(391.75, 41.18) * mm});
            skLineSegment(sketch, "E5732", {"start": v(391.75, 41.18) * mm, "end": v(389.93, 41.2) * mm});
            skLineSegment(sketch, "E5733", {"start": v(389.93, 41.2) * mm, "end": v(388.1, 41.23) * mm});
            skLineSegment(sketch, "E5734", {"start": v(388.1, 41.23) * mm, "end": v(386.3, 41.26) * mm});
            skLineSegment(sketch, "E5735", {"start": v(386.3, 41.26) * mm, "end": v(384.47, 41.3) * mm});
            skLineSegment(sketch, "E5736", {"start": v(384.47, 41.3) * mm, "end": v(382.65, 41.33) * mm});
            skLineSegment(sketch, "E5737", {"start": v(382.65, 41.33) * mm, "end": v(380.84, 41.37) * mm});
            skLineSegment(sketch, "E5738", {"start": v(380.84, 41.37) * mm, "end": v(379.02, 41.4) * mm});
            skLineSegment(sketch, "E5739", {"start": v(379.02, 41.4) * mm, "end": v(377.2, 41.44) * mm});
            skLineSegment(sketch, "E5740", {"start": v(377.2, 41.44) * mm, "end": v(375.38, 41.48) * mm});
            skLineSegment(sketch, "E5741", {"start": v(375.38, 41.48) * mm, "end": v(373.57, 41.51) * mm});
            skLineSegment(sketch, "E5742", {"start": v(373.57, 41.51) * mm, "end": v(371.75, 41.55) * mm});
            skLineSegment(sketch, "E5743", {"start": v(371.75, 41.55) * mm, "end": v(369.93, 41.6) * mm});
            skLineSegment(sketch, "E5744", {"start": v(369.93, 41.6) * mm, "end": v(368.12, 41.63) * mm});
            skLineSegment(sketch, "E5745", {"start": v(368.12, 41.63) * mm, "end": v(366.3, 41.67) * mm});
            skLineSegment(sketch, "E5746", {"start": v(366.3, 41.67) * mm, "end": v(364.5, 41.7) * mm});
            skLineSegment(sketch, "E5747", {"start": v(364.5, 41.7) * mm, "end": v(362.68, 41.74) * mm});
            skLineSegment(sketch, "E5748", {"start": v(362.68, 41.74) * mm, "end": v(360.86, 41.78) * mm});
            skLineSegment(sketch, "E5749", {"start": v(360.86, 41.78) * mm, "end": v(359.05, 41.81) * mm});
            skLineSegment(sketch, "E5750", {"start": v(359.05, 41.81) * mm, "end": v(357.24, 41.84) * mm});
            skLineSegment(sketch, "E5751", {"start": v(357.24, 41.84) * mm, "end": v(355.43, 41.88) * mm});
            skLineSegment(sketch, "E5752", {"start": v(355.43, 41.88) * mm, "end": v(353.62, 41.9) * mm});
            skLineSegment(sketch, "E5753", {"start": v(353.62, 41.9) * mm, "end": v(351.81, 41.93) * mm});
            skLineSegment(sketch, "E5754", {"start": v(351.81, 41.93) * mm, "end": v(350, 41.96) * mm});
            skLineSegment(sketch, "E5755", {"start": v(350, 41.96) * mm, "end": v(348.2, 41.98) * mm});
            skLineSegment(sketch, "E5756", {"start": v(348.2, 41.98) * mm, "end": v(346.4, 42) * mm});
            skLineSegment(sketch, "E5757", {"start": v(346.4, 42) * mm, "end": v(344.59, 42.02) * mm});
            skLineSegment(sketch, "E5758", {"start": v(344.59, 42.02) * mm, "end": v(342.78, 42.04) * mm});
            skLineSegment(sketch, "E5759", {"start": v(342.78, 42.04) * mm, "end": v(340.98, 42.05) * mm});
            skLineSegment(sketch, "E5760", {"start": v(340.98, 42.05) * mm, "end": v(339.18, 42.06) * mm});
            skLineSegment(sketch, "E5761", {"start": v(339.18, 42.06) * mm, "end": v(337.38, 42.06) * mm});
            skLineSegment(sketch, "E5762", {"start": v(337.38, 42.06) * mm, "end": v(335.59, 42.07) * mm});
            skLineSegment(sketch, "E5763", {"start": v(335.59, 42.07) * mm, "end": v(336.61, 43.8) * mm});
            skLineSegment(sketch, "E5764", {"start": v(336.61, 43.8) * mm, "end": v(337.56, 45.52) * mm});
            skLineSegment(sketch, "E5765", {"start": v(337.56, 45.52) * mm, "end": v(338.42, 47.23) * mm});
            skLineSegment(sketch, "E5766", {"start": v(338.42, 47.23) * mm, "end": v(339.22, 48.92) * mm});
            skLineSegment(sketch, "E5767", {"start": v(339.22, 48.92) * mm, "end": v(339.94, 50.6) * mm});
            skLineSegment(sketch, "E5768", {"start": v(339.94, 50.6) * mm, "end": v(340.6, 52.29) * mm});
            skLineSegment(sketch, "E5769", {"start": v(340.6, 52.29) * mm, "end": v(341.2, 53.96) * mm});
            skLineSegment(sketch, "E5770", {"start": v(341.2, 53.96) * mm, "end": v(341.73, 55.63) * mm});
            skLineSegment(sketch, "E5771", {"start": v(341.73, 55.63) * mm, "end": v(342.2, 57.3) * mm});
            skLineSegment(sketch, "E5772", {"start": v(342.2, 57.3) * mm, "end": v(342.63, 58.96) * mm});
            skLineSegment(sketch, "E5773", {"start": v(342.63, 58.96) * mm, "end": v(343, 60.62) * mm});
            skLineSegment(sketch, "E5774", {"start": v(343, 60.62) * mm, "end": v(343.32, 62.3) * mm});
            skLineSegment(sketch, "E5775", {"start": v(343.32, 62.3) * mm, "end": v(343.6, 63.97) * mm});
            skLineSegment(sketch, "E5776", {"start": v(343.6, 63.97) * mm, "end": v(343.84, 65.65) * mm});
            skLineSegment(sketch, "E5777", {"start": v(343.84, 65.65) * mm, "end": v(344.04, 67.34) * mm});
            skLineSegment(sketch, "E5778", {"start": v(344.04, 67.34) * mm, "end": v(344.2, 69.04) * mm});
            skLineSegment(sketch, "E5779", {"start": v(344.2, 69.04) * mm, "end": v(344.34, 70.75) * mm});
            skLineSegment(sketch, "E5780", {"start": v(344.34, 70.75) * mm, "end": v(344.45, 72.48) * mm});
            skLineSegment(sketch, "E5781", {"start": v(344.45, 72.48) * mm, "end": v(344.53, 74.23) * mm});
            skLineSegment(sketch, "E5782", {"start": v(344.53, 74.23) * mm, "end": v(344.58, 75.99) * mm});
            skLineSegment(sketch, "E5783", {"start": v(344.58, 75.99) * mm, "end": v(344.62, 77.77) * mm});
            skLineSegment(sketch, "E5784", {"start": v(344.62, 77.77) * mm, "end": v(344.65, 79.57) * mm});
            skLineSegment(sketch, "E5785", {"start": v(344.65, 79.57) * mm, "end": v(344.66, 81.4) * mm});
            skLineSegment(sketch, "E5786", {"start": v(344.66, 81.4) * mm, "end": v(344.66, 83.25) * mm});
            skLineSegment(sketch, "E5787", {"start": v(344.66, 83.25) * mm, "end": v(344.65, 85.13) * mm});
            skLineSegment(sketch, "E5788", {"start": v(344.65, 85.13) * mm, "end": v(344.65, 87.04) * mm});
            skLineSegment(sketch, "E5789", {"start": v(344.65, 87.04) * mm, "end": v(344.64, 88.97) * mm});
            skLineSegment(sketch, "E5790", {"start": v(344.64, 88.97) * mm, "end": v(344.64, 90.94) * mm});
            skLineSegment(sketch, "E5791", {"start": v(344.64, 90.94) * mm, "end": v(344.64, 139.82) * mm});
            skLineSegment(sketch, "E5792", {"start": v(344.64, 139.82) * mm, "end": v(344.67, 141.4) * mm});
            skLineSegment(sketch, "E5793", {"start": v(344.67, 141.4) * mm, "end": v(344.75, 143.1) * mm});
            skLineSegment(sketch, "E5794", {"start": v(344.75, 143.1) * mm, "end": v(344.85, 144.9) * mm});
            skLineSegment(sketch, "E5795", {"start": v(344.85, 144.9) * mm, "end": v(344.94, 146.76) * mm});
            skLineSegment(sketch, "E5796", {"start": v(344.94, 146.76) * mm, "end": v(344.99, 148.65) * mm});
            skLineSegment(sketch, "E5797", {"start": v(344.99, 148.65) * mm, "end": v(344.96, 150.54) * mm});
            skLineSegment(sketch, "E5798", {"start": v(344.96, 150.54) * mm, "end": v(344.84, 152.39) * mm});
            skLineSegment(sketch, "E5799", {"start": v(344.84, 152.39) * mm, "end": v(344.6, 154.17) * mm});
            skLineSegment(sketch, "E5800", {"start": v(344.6, 154.17) * mm, "end": v(344.18, 155.86) * mm});
            skLineSegment(sketch, "E5801", {"start": v(344.18, 155.86) * mm, "end": v(343.59, 157.41) * mm});
            skLineSegment(sketch, "E5802", {"start": v(343.59, 157.41) * mm, "end": v(342.78, 158.8) * mm});
            skLineSegment(sketch, "E5803", {"start": v(342.78, 158.8) * mm, "end": v(341.63, 160.1) * mm});
            skLineSegment(sketch, "E5804", {"start": v(341.63, 160.1) * mm, "end": v(340.29, 161.13) * mm});
            skLineSegment(sketch, "E5805", {"start": v(340.29, 161.13) * mm, "end": v(338.77, 161.92) * mm});
            skLineSegment(sketch, "E5806", {"start": v(338.77, 161.92) * mm, "end": v(337.11, 162.5) * mm});
            skLineSegment(sketch, "E5807", {"start": v(337.11, 162.5) * mm, "end": v(335.36, 162.9) * mm});
            skLineSegment(sketch, "E5808", {"start": v(335.36, 162.9) * mm, "end": v(333.55, 163.16) * mm});
            skLineSegment(sketch, "E5809", {"start": v(333.55, 163.16) * mm, "end": v(331.7, 163.3) * mm});
            skLineSegment(sketch, "E5810", {"start": v(331.7, 163.3) * mm, "end": v(329.86, 163.37) * mm});
            skLineSegment(sketch, "E5811", {"start": v(329.86, 163.37) * mm, "end": v(328.06, 163.38) * mm});
            skLineSegment(sketch, "E5812", {"start": v(328.06, 163.38) * mm, "end": v(326.34, 163.36) * mm});
            skLineSegment(sketch, "E5813", {"start": v(326.34, 163.36) * mm, "end": v(324.72, 163.36) * mm});
            skLineSegment(sketch, "E5814", {"start": v(324.72, 163.36) * mm, "end": v(322.91, 163.36) * mm});
            skLineSegment(sketch, "E5815", {"start": v(322.91, 163.36) * mm, "end": v(321.1, 163.37) * mm});
            skLineSegment(sketch, "E5816", {"start": v(321.1, 163.37) * mm, "end": v(319.3, 163.38) * mm});
            skLineSegment(sketch, "E5817", {"start": v(319.3, 163.38) * mm, "end": v(317.48, 163.39) * mm});
            skLineSegment(sketch, "E5818", {"start": v(317.48, 163.39) * mm, "end": v(315.67, 163.4) * mm});
            skLineSegment(sketch, "E5819", {"start": v(315.67, 163.4) * mm, "end": v(313.86, 163.4) * mm});
            skLineSegment(sketch, "E5820", {"start": v(313.86, 163.4) * mm, "end": v(312.05, 163.4) * mm});
            skLineSegment(sketch, "E5821", {"start": v(312.05, 163.4) * mm, "end": v(310.24, 163.4) * mm});
            skLineSegment(sketch, "E5822", {"start": v(310.24, 163.4) * mm, "end": v(308.43, 163.4) * mm});
            skLineSegment(sketch, "E5823", {"start": v(308.43, 163.4) * mm, "end": v(306.62, 163.41) * mm});
            skLineSegment(sketch, "E5824", {"start": v(306.62, 163.41) * mm, "end": v(304.81, 163.41) * mm});
            skLineSegment(sketch, "E5825", {"start": v(304.81, 163.41) * mm, "end": v(303, 163.42) * mm});
            skLineSegment(sketch, "E5826", {"start": v(303, 163.42) * mm, "end": v(301.19, 163.42) * mm});
            skLineSegment(sketch, "E5827", {"start": v(301.19, 163.42) * mm, "end": v(299.38, 163.42) * mm});
            skLineSegment(sketch, "E5828", {"start": v(299.38, 163.42) * mm, "end": v(297.57, 163.42) * mm});
            skLineSegment(sketch, "E5829", {"start": v(297.57, 163.42) * mm, "end": v(295.76, 163.41) * mm});
            skLineSegment(sketch, "E5830", {"start": v(295.76, 163.41) * mm, "end": v(293.95, 163.41) * mm});
            skLineSegment(sketch, "E5831", {"start": v(293.95, 163.41) * mm, "end": v(292.14, 163.4) * mm});
            skLineSegment(sketch, "E5832", {"start": v(292.14, 163.4) * mm, "end": v(290.33, 163.4) * mm});
            skLineSegment(sketch, "E5833", {"start": v(290.33, 163.4) * mm, "end": v(288.52, 163.4) * mm});
            skLineSegment(sketch, "E5834", {"start": v(288.52, 163.4) * mm, "end": v(286.7, 163.4) * mm});
            skLineSegment(sketch, "E5835", {"start": v(286.7, 163.4) * mm, "end": v(284.9, 163.4) * mm});
            skLineSegment(sketch, "E5836", {"start": v(284.9, 163.4) * mm, "end": v(283.09, 163.39) * mm});
            skLineSegment(sketch, "E5837", {"start": v(283.09, 163.39) * mm, "end": v(281.28, 163.38) * mm});
            skLineSegment(sketch, "E5838", {"start": v(281.28, 163.38) * mm, "end": v(279.46, 163.37) * mm});
            skLineSegment(sketch, "E5839", {"start": v(279.46, 163.37) * mm, "end": v(277.65, 163.36) * mm});
            skLineSegment(sketch, "E5840", {"start": v(277.65, 163.36) * mm, "end": v(275.84, 163.36) * mm});
            skLineSegment(sketch, "E5841", {"start": v(275.84, 163.36) * mm, "end": v(274.23, 163.36) * mm});
            skLineSegment(sketch, "E5842", {"start": v(274.23, 163.36) * mm, "end": v(272.5, 163.38) * mm});
            skLineSegment(sketch, "E5843", {"start": v(272.5, 163.38) * mm, "end": v(270.7, 163.37) * mm});
            skLineSegment(sketch, "E5844", {"start": v(270.7, 163.37) * mm, "end": v(268.87, 163.3) * mm});
            skLineSegment(sketch, "E5845", {"start": v(268.87, 163.3) * mm, "end": v(267.02, 163.16) * mm});
            skLineSegment(sketch, "E5846", {"start": v(267.02, 163.16) * mm, "end": v(265.2, 162.9) * mm});
            skLineSegment(sketch, "E5847", {"start": v(265.2, 162.9) * mm, "end": v(263.45, 162.5) * mm});
            skLineSegment(sketch, "E5848", {"start": v(263.45, 162.5) * mm, "end": v(261.8, 161.92) * mm});
            skLineSegment(sketch, "E5849", {"start": v(261.8, 161.92) * mm, "end": v(260.28, 161.13) * mm});
            skLineSegment(sketch, "E5850", {"start": v(260.28, 161.13) * mm, "end": v(258.93, 160.1) * mm});
            skLineSegment(sketch, "E5851", {"start": v(258.93, 160.1) * mm, "end": v(257.8, 158.8) * mm});
            skLineSegment(sketch, "E5852", {"start": v(257.8, 158.8) * mm, "end": v(257.03, 157.56) * mm});
            skLineSegment(sketch, "E5853", {"start": v(257.03, 157.56) * mm, "end": v(256.42, 156.16) * mm});
            skLineSegment(sketch, "E5854", {"start": v(256.42, 156.16) * mm, "end": v(255.92, 154.61) * mm});
            skLineSegment(sketch, "E5855", {"start": v(255.92, 154.61) * mm, "end": v(255.55, 152.95) * mm});
            skLineSegment(sketch, "E5856", {"start": v(255.55, 152.95) * mm, "end": v(255.27, 151.18) * mm});
            skLineSegment(sketch, "E5857", {"start": v(255.27, 151.18) * mm, "end": v(255.1, 149.33) * mm});
            skLineSegment(sketch, "E5858", {"start": v(255.1, 149.33) * mm, "end": v(255, 147.41) * mm});
            skLineSegment(sketch, "E5859", {"start": v(255, 147.41) * mm, "end": v(254.97, 145.45) * mm});
            skLineSegment(sketch, "E5860", {"start": v(254.97, 145.45) * mm, "end": v(255, 143.45) * mm});
            skLineSegment(sketch, "E5861", {"start": v(255, 143.45) * mm, "end": v(255.07, 141.45) * mm});
            skLineSegment(sketch, "E5862", {"start": v(255.07, 141.45) * mm, "end": v(255.17, 139.44) * mm});
            skLineSegment(sketch, "E5863", {"start": v(255.17, 139.44) * mm, "end": v(255.3, 137.47) * mm});
            skLineSegment(sketch, "E5864", {"start": v(255.3, 137.47) * mm, "end": v(255.45, 135.54) * mm});
            skLineSegment(sketch, "E5865", {"start": v(255.45, 135.54) * mm, "end": v(255.6, 133.66) * mm});
            skLineSegment(sketch, "E5866", {"start": v(255.6, 133.66) * mm, "end": v(255.72, 131.87) * mm});
            skLineSegment(sketch, "E5867", {"start": v(255.72, 131.87) * mm, "end": v(255.83, 130.18) * mm});
            skLineSegment(sketch, "E5868", {"start": v(255.83, 130.18) * mm, "end": v(255.9, 128.6) * mm});
            skLineSegment(sketch, "E5869", {"start": v(255.9, 128.6) * mm, "end": v(255.93, 127.15) * mm});
            skLineSegment(sketch, "E5870", {"start": v(255.93, 127.15) * mm, "end": v(255.92, 125.42) * mm});
            skLineSegment(sketch, "E5871", {"start": v(255.92, 125.42) * mm, "end": v(255.9, 123.69) * mm});
            skLineSegment(sketch, "E5872", {"start": v(255.9, 123.69) * mm, "end": v(255.88, 121.95) * mm});
            skLineSegment(sketch, "E5873", {"start": v(255.88, 121.95) * mm, "end": v(255.84, 120.2) * mm});
            skLineSegment(sketch, "E5874", {"start": v(255.84, 120.2) * mm, "end": v(255.79, 118.45) * mm});
            skLineSegment(sketch, "E5875", {"start": v(255.79, 118.45) * mm, "end": v(255.73, 116.7) * mm});
            skLineSegment(sketch, "E5876", {"start": v(255.73, 116.7) * mm, "end": v(255.67, 114.93) * mm});
            skLineSegment(sketch, "E5877", {"start": v(255.67, 114.93) * mm, "end": v(255.6, 113.17) * mm});
            skLineSegment(sketch, "E5878", {"start": v(255.6, 113.17) * mm, "end": v(255.54, 111.4) * mm});
            skLineSegment(sketch, "E5879", {"start": v(255.54, 111.4) * mm, "end": v(255.47, 109.63) * mm});
            skLineSegment(sketch, "E5880", {"start": v(255.47, 109.63) * mm, "end": v(255.4, 107.86) * mm});
            skLineSegment(sketch, "E5881", {"start": v(255.4, 107.86) * mm, "end": v(255.33, 106.08) * mm});
            skLineSegment(sketch, "E5882", {"start": v(255.33, 106.08) * mm, "end": v(255.26, 104.3) * mm});
            skLineSegment(sketch, "E5883", {"start": v(255.26, 104.3) * mm, "end": v(255.2, 102.53) * mm});
            skLineSegment(sketch, "E5884", {"start": v(255.2, 102.53) * mm, "end": v(255.14, 100.75) * mm});
            skLineSegment(sketch, "E5885", {"start": v(255.14, 100.75) * mm, "end": v(255.09, 98.98) * mm});
            skLineSegment(sketch, "E5886", {"start": v(255.09, 98.98) * mm, "end": v(255.05, 97.2) * mm});
            skLineSegment(sketch, "E5887", {"start": v(255.05, 97.2) * mm, "end": v(255.01, 95.42) * mm});
            skLineSegment(sketch, "E5888", {"start": v(255.01, 95.42) * mm, "end": v(254.99, 93.65) * mm});
            skLineSegment(sketch, "E5889", {"start": v(254.99, 93.65) * mm, "end": v(254.98, 91.88) * mm});
            skLineSegment(sketch, "E5890", {"start": v(254.98, 91.88) * mm, "end": v(254.98, 90.1) * mm});
            skLineSegment(sketch, "E5891", {"start": v(254.98, 90.1) * mm, "end": v(255, 88.34) * mm});
            skLineSegment(sketch, "E5892", {"start": v(255, 88.34) * mm, "end": v(255.02, 86.58) * mm});
            skLineSegment(sketch, "E5893", {"start": v(255.02, 86.58) * mm, "end": v(255.07, 84.82) * mm});
            skLineSegment(sketch, "E5894", {"start": v(255.07, 84.82) * mm, "end": v(255.14, 83.07) * mm});
            skLineSegment(sketch, "E5895", {"start": v(255.14, 83.07) * mm, "end": v(255.23, 81.32) * mm});
            skLineSegment(sketch, "E5896", {"start": v(255.23, 81.32) * mm, "end": v(255.34, 79.57) * mm});
            skLineSegment(sketch, "E5897", {"start": v(255.34, 79.57) * mm, "end": v(255.47, 77.83) * mm});
            skLineSegment(sketch, "E5898", {"start": v(255.47, 77.83) * mm, "end": v(255.62, 76.1) * mm});
            skLineSegment(sketch, "E5899", {"start": v(255.62, 76.1) * mm, "end": v(255.8, 74.38) * mm});
            skLineSegment(sketch, "E5900", {"start": v(255.8, 74.38) * mm, "end": v(256, 72.66) * mm});
            skLineSegment(sketch, "E5901", {"start": v(256, 72.66) * mm, "end": v(256.24, 70.95) * mm});
            skLineSegment(sketch, "E5902", {"start": v(256.24, 70.95) * mm, "end": v(256.5, 69.25) * mm});
            skLineSegment(sketch, "E5903", {"start": v(256.5, 69.25) * mm, "end": v(256.8, 67.55) * mm});
            skLineSegment(sketch, "E5904", {"start": v(256.8, 67.55) * mm, "end": v(257.13, 65.87) * mm});
            skLineSegment(sketch, "E5905", {"start": v(257.13, 65.87) * mm, "end": v(257.49, 64.2) * mm});
            skLineSegment(sketch, "E5906", {"start": v(257.49, 64.2) * mm, "end": v(257.88, 62.53) * mm});
            skLineSegment(sketch, "E5907", {"start": v(257.88, 62.53) * mm, "end": v(258.32, 60.88) * mm});
            skLineSegment(sketch, "E5908", {"start": v(258.32, 60.88) * mm, "end": v(258.78, 59.24) * mm});
            skLineSegment(sketch, "E5909", {"start": v(258.78, 59.24) * mm, "end": v(259.3, 57.61) * mm});
            skLineSegment(sketch, "E5910", {"start": v(259.3, 57.61) * mm, "end": v(259.84, 56) * mm});
            skLineSegment(sketch, "E5911", {"start": v(259.84, 56) * mm, "end": v(260.43, 54.39) * mm});
            skLineSegment(sketch, "E5912", {"start": v(260.43, 54.39) * mm, "end": v(261.06, 52.8) * mm});
            skLineSegment(sketch, "E5913", {"start": v(261.06, 52.8) * mm, "end": v(261.74, 51.22) * mm});
            skLineSegment(sketch, "E5914", {"start": v(261.74, 51.22) * mm, "end": v(262.46, 49.66) * mm});
            skLineSegment(sketch, "E5915", {"start": v(262.46, 49.66) * mm, "end": v(263.23, 48.1) * mm});
            skLineSegment(sketch, "E5916", {"start": v(263.23, 48.1) * mm, "end": v(264.04, 46.57) * mm});
            skLineSegment(sketch, "E5917", {"start": v(264.04, 46.57) * mm, "end": v(264.9, 45.05) * mm});
            skLineSegment(sketch, "E5918", {"start": v(264.9, 45.05) * mm, "end": v(265.82, 43.55) * mm});
            skLineSegment(sketch, "E5919", {"start": v(265.82, 43.55) * mm, "end": v(266.8, 42.07) * mm});
            skLineSegment(sketch, "E5920", {"start": v(266.8, 42.07) * mm, "end": v(154.55, 42.07) * mm});
            skLineSegment(sketch, "E5921", {"start": v(154.55, 42.07) * mm, "end": v(155.57, 43.63) * mm});
            skLineSegment(sketch, "E5922", {"start": v(155.57, 43.63) * mm, "end": v(156.53, 45.2) * mm});
            skLineSegment(sketch, "E5923", {"start": v(156.53, 45.2) * mm, "end": v(157.43, 46.79) * mm});
            skLineSegment(sketch, "E5924", {"start": v(157.43, 46.79) * mm, "end": v(158.27, 48.38) * mm});
            skLineSegment(sketch, "E5925", {"start": v(158.27, 48.38) * mm, "end": v(159.06, 49.99) * mm});
            skLineSegment(sketch, "E5926", {"start": v(159.06, 49.99) * mm, "end": v(159.8, 51.6) * mm});
            skLineSegment(sketch, "E5927", {"start": v(159.8, 51.6) * mm, "end": v(160.48, 53.23) * mm});
            skLineSegment(sketch, "E5928", {"start": v(160.48, 53.23) * mm, "end": v(161.12, 54.87) * mm});
            skLineSegment(sketch, "E5929", {"start": v(161.12, 54.87) * mm, "end": v(161.7, 56.52) * mm});
            skLineSegment(sketch, "E5930", {"start": v(161.7, 56.52) * mm, "end": v(162.24, 58.17) * mm});
            skLineSegment(sketch, "E5931", {"start": v(162.24, 58.17) * mm, "end": v(162.74, 59.84) * mm});
            skLineSegment(sketch, "E5932", {"start": v(162.74, 59.84) * mm, "end": v(163.2, 61.5) * mm});
            skLineSegment(sketch, "E5933", {"start": v(163.2, 61.5) * mm, "end": v(163.6, 63.2) * mm});
            skLineSegment(sketch, "E5934", {"start": v(163.6, 63.2) * mm, "end": v(163.98, 64.88) * mm});
            skLineSegment(sketch, "E5935", {"start": v(163.98, 64.88) * mm, "end": v(164.31, 66.58) * mm});
            skLineSegment(sketch, "E5936", {"start": v(164.31, 66.58) * mm, "end": v(164.61, 68.28) * mm});
            skLineSegment(sketch, "E5937", {"start": v(164.61, 68.28) * mm, "end": v(164.88, 70) * mm});
            skLineSegment(sketch, "E5938", {"start": v(164.88, 70) * mm, "end": v(165.11, 71.72) * mm});
            skLineSegment(sketch, "E5939", {"start": v(165.11, 71.72) * mm, "end": v(165.31, 73.44) * mm});
            skLineSegment(sketch, "E5940", {"start": v(165.31, 73.44) * mm, "end": v(165.49, 75.18) * mm});
            skLineSegment(sketch, "E5941", {"start": v(165.49, 75.18) * mm, "end": v(165.63, 76.92) * mm});
            skLineSegment(sketch, "E5942", {"start": v(165.63, 76.92) * mm, "end": v(165.75, 78.67) * mm});
            skLineSegment(sketch, "E5943", {"start": v(165.75, 78.67) * mm, "end": v(165.85, 80.42) * mm});
            skLineSegment(sketch, "E5944", {"start": v(165.85, 80.42) * mm, "end": v(165.92, 82.18) * mm});
            skLineSegment(sketch, "E5945", {"start": v(165.92, 82.18) * mm, "end": v(165.98, 83.94) * mm});
            skLineSegment(sketch, "E5946", {"start": v(165.98, 83.94) * mm, "end": v(166.01, 85.7) * mm});
            skLineSegment(sketch, "E5947", {"start": v(166.01, 85.7) * mm, "end": v(166.03, 87.48) * mm});
            skLineSegment(sketch, "E5948", {"start": v(166.03, 87.48) * mm, "end": v(166.03, 89.26) * mm});
            skLineSegment(sketch, "E5949", {"start": v(166.03, 89.26) * mm, "end": v(166.02, 91.04) * mm});
            skLineSegment(sketch, "E5950", {"start": v(166.02, 91.04) * mm, "end": v(166, 92.83) * mm});
            skLineSegment(sketch, "E5951", {"start": v(166, 92.83) * mm, "end": v(165.97, 94.61) * mm});
            skLineSegment(sketch, "E5952", {"start": v(165.97, 94.61) * mm, "end": v(165.93, 96.4) * mm});
            skLineSegment(sketch, "E5953", {"start": v(165.93, 96.4) * mm, "end": v(165.88, 98.2) * mm});
            skLineSegment(sketch, "E5954", {"start": v(165.88, 98.2) * mm, "end": v(165.83, 100) * mm});
            skLineSegment(sketch, "E5955", {"start": v(165.83, 100) * mm, "end": v(165.77, 101.8) * mm});
            skLineSegment(sketch, "E5956", {"start": v(165.77, 101.8) * mm, "end": v(165.72, 103.6) * mm});
            skLineSegment(sketch, "E5957", {"start": v(165.72, 103.6) * mm, "end": v(165.66, 105.42) * mm});
            skLineSegment(sketch, "E5958", {"start": v(165.66, 105.42) * mm, "end": v(165.6, 107.22) * mm});
            skLineSegment(sketch, "E5959", {"start": v(165.6, 107.22) * mm, "end": v(165.55, 109.03) * mm});
            skLineSegment(sketch, "E5960", {"start": v(165.55, 109.03) * mm, "end": v(165.5, 110.85) * mm});
            skLineSegment(sketch, "E5961", {"start": v(165.5, 110.85) * mm, "end": v(165.47, 112.66) * mm});
            skLineSegment(sketch, "E5962", {"start": v(165.47, 112.66) * mm, "end": v(165.44, 114.47) * mm});
            skLineSegment(sketch, "E5963", {"start": v(165.44, 114.47) * mm, "end": v(165.42, 116.29) * mm});
            skLineSegment(sketch, "E5964", {"start": v(165.42, 116.29) * mm, "end": v(165.41, 118.1) * mm});
            skLineSegment(sketch, "E5965", {"start": v(165.41, 118.1) * mm, "end": v(165.41, 237.58) * mm});
            skLineSegment(sketch, "E5966", {"start": v(165.41, 237.58) * mm, "end": v(165.42, 239.52) * mm});
            skLineSegment(sketch, "E5967", {"start": v(165.42, 239.52) * mm, "end": v(165.43, 241.44) * mm});
            skLineSegment(sketch, "E5968", {"start": v(165.43, 241.44) * mm, "end": v(165.44, 243.34) * mm});
            skLineSegment(sketch, "E5969", {"start": v(165.44, 243.34) * mm, "end": v(165.46, 245.24) * mm});
            skLineSegment(sketch, "E5970", {"start": v(165.46, 245.24) * mm, "end": v(165.47, 247.12) * mm});
            skLineSegment(sketch, "E5971", {"start": v(165.47, 247.12) * mm, "end": v(165.5, 249) * mm});
            skLineSegment(sketch, "E5972", {"start": v(165.5, 249) * mm, "end": v(165.51, 250.86) * mm});
            skLineSegment(sketch, "E5973", {"start": v(165.51, 250.86) * mm, "end": v(165.53, 252.71) * mm});
            skLineSegment(sketch, "E5974", {"start": v(165.53, 252.71) * mm, "end": v(165.55, 254.55) * mm});
            skLineSegment(sketch, "E5975", {"start": v(165.55, 254.55) * mm, "end": v(165.57, 256.38) * mm});
            skLineSegment(sketch, "E5976", {"start": v(165.57, 256.38) * mm, "end": v(165.58, 258.2) * mm});
            skLineSegment(sketch, "E5977", {"start": v(165.58, 258.2) * mm, "end": v(165.59, 260.02) * mm});
            skLineSegment(sketch, "E5978", {"start": v(165.59, 260.02) * mm, "end": v(165.6, 261.82) * mm});
            skLineSegment(sketch, "E5979", {"start": v(165.6, 261.82) * mm, "end": v(165.59, 263.62) * mm});
            skLineSegment(sketch, "E5980", {"start": v(165.59, 263.62) * mm, "end": v(165.57, 265.4) * mm});
            skLineSegment(sketch, "E5981", {"start": v(165.57, 265.4) * mm, "end": v(165.55, 267.2) * mm});
            skLineSegment(sketch, "E5982", {"start": v(165.55, 267.2) * mm, "end": v(165.52, 268.96) * mm});
            skLineSegment(sketch, "E5983", {"start": v(165.52, 268.96) * mm, "end": v(165.48, 270.73) * mm});
            skLineSegment(sketch, "E5984", {"start": v(165.48, 270.73) * mm, "end": v(165.43, 272.5) * mm});
            skLineSegment(sketch, "E5985", {"start": v(165.43, 272.5) * mm, "end": v(165.37, 274.25) * mm});
            skLineSegment(sketch, "E5986", {"start": v(165.37, 274.25) * mm, "end": v(165.3, 276) * mm});
            skLineSegment(sketch, "E5987", {"start": v(165.3, 276) * mm, "end": v(165.2, 277.74) * mm});
            skLineSegment(sketch, "E5988", {"start": v(165.2, 277.74) * mm, "end": v(165.1, 279.48) * mm});
            skLineSegment(sketch, "E5989", {"start": v(165.1, 279.48) * mm, "end": v(164.97, 281.22) * mm});
            skLineSegment(sketch, "E5990", {"start": v(164.97, 281.22) * mm, "end": v(164.83, 282.95) * mm});
            skLineSegment(sketch, "E5991", {"start": v(164.83, 282.95) * mm, "end": v(164.67, 284.68) * mm});
            skLineSegment(sketch, "E5992", {"start": v(164.67, 284.68) * mm, "end": v(164.5, 286.4) * mm});
            skLineSegment(sketch, "E5993", {"start": v(164.5, 286.4) * mm, "end": v(164.3, 288.13) * mm});
            skLineSegment(sketch, "E5994", {"start": v(164.3, 288.13) * mm, "end": v(164.08, 289.85) * mm});
            skLineSegment(sketch, "E5995", {"start": v(164.08, 289.85) * mm, "end": v(163.83, 291.57) * mm});
            skLineSegment(sketch, "E5996", {"start": v(163.83, 291.57) * mm, "end": v(163.57, 293.3) * mm});
            skLineSegment(sketch, "E5997", {"start": v(163.57, 293.3) * mm, "end": v(163.28, 295) * mm});
            skLineSegment(sketch, "E5998", {"start": v(163.28, 295) * mm, "end": v(162.97, 296.72) * mm});
            skLineSegment(sketch, "E5999", {"start": v(162.97, 296.72) * mm, "end": v(162.62, 298.44) * mm});
            skLineSegment(sketch, "E6000", {"start": v(162.62, 298.44) * mm, "end": v(162.26, 300.16) * mm});
            skLineSegment(sketch, "E6001", {"start": v(162.26, 300.16) * mm, "end": v(161.86, 301.87) * mm});
            skLineSegment(sketch, "E6002", {"start": v(161.86, 301.87) * mm, "end": v(161.44, 303.6) * mm});
            skLineSegment(sketch, "E6003", {"start": v(161.44, 303.6) * mm, "end": v(160.98, 305.31) * mm});
            skLineSegment(sketch, "E6004", {"start": v(160.98, 305.31) * mm, "end": v(160.5, 307.03) * mm});
            skLineSegment(sketch, "E6005", {"start": v(160.5, 307.03) * mm, "end": v(159.98, 308.76) * mm});
            skLineSegment(sketch, "E6006", {"start": v(159.98, 308.76) * mm, "end": v(159.42, 310.48) * mm});
            skLineSegment(sketch, "E6007", {"start": v(159.42, 310.48) * mm, "end": v(158.84, 312.21) * mm});
            skLineSegment(sketch, "E6008", {"start": v(158.84, 312.21) * mm, "end": v(158.22, 313.94) * mm});
            skLineSegment(sketch, "E6009", {"start": v(158.22, 313.94) * mm, "end": v(157.56, 315.68) * mm});
            skLineSegment(sketch, "E6010", {"start": v(157.56, 315.68) * mm, "end": v(156.87, 317.42) * mm});
            skLineSegment(sketch, "E6011", {"start": v(156.87, 317.42) * mm, "end": v(156.13, 319.16) * mm});
            skLineSegment(sketch, "E6012", {"start": v(156.13, 319.16) * mm, "end": v(155.36, 320.91) * mm});
            skLineSegment(sketch, "E6013", {"start": v(155.36, 320.91) * mm, "end": v(154.55, 322.67) * mm});
            skLineSegment(sketch, "E6014", {"start": v(154.55, 322.67) * mm, "end": v(266.8, 322.67) * mm});
            skLineSegment(sketch, "E6015", {"start": v(266.8, 322.67) * mm, "end": v(265.9, 321.03) * mm});
            skLineSegment(sketch, "E6016", {"start": v(265.9, 321.03) * mm, "end": v(265.06, 319.38) * mm});
            skLineSegment(sketch, "E6017", {"start": v(265.06, 319.38) * mm, "end": v(264.27, 317.74) * mm});
            skLineSegment(sketch, "E6018", {"start": v(264.27, 317.74) * mm, "end": v(263.51, 316.09) * mm});
            skLineSegment(sketch, "E6019", {"start": v(263.51, 316.09) * mm, "end": v(262.8, 314.44) * mm});
            skLineSegment(sketch, "E6020", {"start": v(262.8, 314.44) * mm, "end": v(262.13, 312.78) * mm});
            skLineSegment(sketch, "E6021", {"start": v(262.13, 312.78) * mm, "end": v(261.5, 311.12) * mm});
            skLineSegment(sketch, "E6022", {"start": v(261.5, 311.12) * mm, "end": v(260.91, 309.45) * mm});
            skLineSegment(sketch, "E6023", {"start": v(260.91, 309.45) * mm, "end": v(260.36, 307.78) * mm});
            skLineSegment(sketch, "E6024", {"start": v(260.36, 307.78) * mm, "end": v(259.85, 306.11) * mm});
            skLineSegment(sketch, "E6025", {"start": v(259.85, 306.11) * mm, "end": v(259.37, 304.44) * mm});
            skLineSegment(sketch, "E6026", {"start": v(259.37, 304.44) * mm, "end": v(258.92, 302.76) * mm});
            skLineSegment(sketch, "E6027", {"start": v(258.92, 302.76) * mm, "end": v(258.51, 301.07) * mm});
            skLineSegment(sketch, "E6028", {"start": v(258.51, 301.07) * mm, "end": v(258.13, 299.38) * mm});
            skLineSegment(sketch, "E6029", {"start": v(258.13, 299.38) * mm, "end": v(257.78, 297.7) * mm});
            skLineSegment(sketch, "E6030", {"start": v(257.78, 297.7) * mm, "end": v(257.46, 296) * mm});
            skLineSegment(sketch, "E6031", {"start": v(257.46, 296) * mm, "end": v(257.17, 294.3) * mm});
            skLineSegment(sketch, "E6032", {"start": v(257.17, 294.3) * mm, "end": v(256.9, 292.6) * mm});
            skLineSegment(sketch, "E6033", {"start": v(256.9, 292.6) * mm, "end": v(256.67, 290.88) * mm});
            skLineSegment(sketch, "E6034", {"start": v(256.67, 290.88) * mm, "end": v(256.46, 289.17) * mm});
            skLineSegment(sketch, "E6035", {"start": v(256.46, 289.17) * mm, "end": v(256.27, 287.46) * mm});
            skLineSegment(sketch, "E6036", {"start": v(256.27, 287.46) * mm, "end": v(256.1, 285.74) * mm});
            skLineSegment(sketch, "E6037", {"start": v(256.1, 285.74) * mm, "end": v(255.96, 284.01) * mm});
            skLineSegment(sketch, "E6038", {"start": v(255.96, 284.01) * mm, "end": v(255.83, 282.28) * mm});
            skLineSegment(sketch, "E6039", {"start": v(255.83, 282.28) * mm, "end": v(255.73, 280.55) * mm});
            skLineSegment(sketch, "E6040", {"start": v(255.73, 280.55) * mm, "end": v(255.64, 278.81) * mm});
            skLineSegment(sketch, "E6041", {"start": v(255.64, 278.81) * mm, "end": v(255.57, 277.07) * mm});
            skLineSegment(sketch, "E6042", {"start": v(255.57, 277.07) * mm, "end": v(255.52, 275.32) * mm});
            skLineSegment(sketch, "E6043", {"start": v(255.52, 275.32) * mm, "end": v(255.48, 273.57) * mm});
            skLineSegment(sketch, "E6044", {"start": v(255.48, 273.57) * mm, "end": v(255.45, 271.82) * mm});
            skLineSegment(sketch, "E6045", {"start": v(255.45, 271.82) * mm, "end": v(255.44, 270.06) * mm});
            skLineSegment(sketch, "E6046", {"start": v(255.44, 270.06) * mm, "end": v(255.44, 268.3) * mm});
            skLineSegment(sketch, "E6047", {"start": v(255.44, 268.3) * mm, "end": v(255.44, 266.52) * mm});
            skLineSegment(sketch, "E6048", {"start": v(255.44, 266.52) * mm, "end": v(255.46, 264.75) * mm});
            skLineSegment(sketch, "E6049", {"start": v(255.46, 264.75) * mm, "end": v(255.48, 262.97) * mm});
            skLineSegment(sketch, "E6050", {"start": v(255.48, 262.97) * mm, "end": v(255.5, 261.19) * mm});
            skLineSegment(sketch, "E6051", {"start": v(255.5, 261.19) * mm, "end": v(255.54, 259.4) * mm});
            skLineSegment(sketch, "E6052", {"start": v(255.54, 259.4) * mm, "end": v(255.58, 257.61) * mm});
            skLineSegment(sketch, "E6053", {"start": v(255.58, 257.61) * mm, "end": v(255.62, 255.81) * mm});
            skLineSegment(sketch, "E6054", {"start": v(255.62, 255.81) * mm, "end": v(255.67, 254.01) * mm});
            skLineSegment(sketch, "E6055", {"start": v(255.67, 254.01) * mm, "end": v(255.7, 252.2) * mm});
            skLineSegment(sketch, "E6056", {"start": v(255.7, 252.2) * mm, "end": v(255.75, 250.4) * mm});
            skLineSegment(sketch, "E6057", {"start": v(255.75, 250.4) * mm, "end": v(255.8, 248.58) * mm});
            skLineSegment(sketch, "E6058", {"start": v(255.8, 248.58) * mm, "end": v(255.83, 246.76) * mm});
            skLineSegment(sketch, "E6059", {"start": v(255.83, 246.76) * mm, "end": v(255.86, 244.93) * mm});
            skLineSegment(sketch, "E6060", {"start": v(255.86, 244.93) * mm, "end": v(255.9, 243.1) * mm});
            skLineSegment(sketch, "E6061", {"start": v(255.9, 243.1) * mm, "end": v(255.91, 241.27) * mm});
            skLineSegment(sketch, "E6062", {"start": v(255.91, 241.27) * mm, "end": v(255.93, 239.43) * mm});
            skLineSegment(sketch, "E6063", {"start": v(255.93, 239.43) * mm, "end": v(255.93, 237.58) * mm});
            skLineSegment(sketch, "E6064", {"start": v(255.93, 237.58) * mm, "end": v(255.9, 236.04) * mm});
            skLineSegment(sketch, "E6065", {"start": v(255.9, 236.04) * mm, "end": v(255.84, 234.4) * mm});
            skLineSegment(sketch, "E6066", {"start": v(255.84, 234.4) * mm, "end": v(255.74, 232.69) * mm});
            skLineSegment(sketch, "E6067", {"start": v(255.74, 232.69) * mm, "end": v(255.62, 230.9) * mm});
            skLineSegment(sketch, "E6068", {"start": v(255.62, 230.9) * mm, "end": v(255.48, 229.05) * mm});
            skLineSegment(sketch, "E6069", {"start": v(255.48, 229.05) * mm, "end": v(255.34, 227.17) * mm});
            skLineSegment(sketch, "E6070", {"start": v(255.34, 227.17) * mm, "end": v(255.21, 225.25) * mm});
            skLineSegment(sketch, "E6071", {"start": v(255.21, 225.25) * mm, "end": v(255.1, 223.3) * mm});
            skLineSegment(sketch, "E6072", {"start": v(255.1, 223.3) * mm, "end": v(255, 221.36) * mm});
            skLineSegment(sketch, "E6073", {"start": v(255, 221.36) * mm, "end": v(254.96, 219.42) * mm});
            skLineSegment(sketch, "E6074", {"start": v(254.96, 219.42) * mm, "end": v(254.95, 217.5) * mm});
            skLineSegment(sketch, "E6075", {"start": v(254.95, 217.5) * mm, "end": v(255, 215.62) * mm});
            skLineSegment(sketch, "E6076", {"start": v(255, 215.62) * mm, "end": v(255.12, 213.78) * mm});
            skLineSegment(sketch, "E6077", {"start": v(255.12, 213.78) * mm, "end": v(255.3, 212) * mm});
            skLineSegment(sketch, "E6078", {"start": v(255.3, 212) * mm, "end": v(255.58, 210.29) * mm});
            skLineSegment(sketch, "E6079", {"start": v(255.58, 210.29) * mm, "end": v(255.95, 208.66) * mm});
            skLineSegment(sketch, "E6080", {"start": v(255.95, 208.66) * mm, "end": v(256.43, 207.13) * mm});
            skLineSegment(sketch, "E6081", {"start": v(256.43, 207.13) * mm, "end": v(257.02, 205.7) * mm});
            skLineSegment(sketch, "E6082", {"start": v(257.02, 205.7) * mm, "end": v(257.95, 204.19) * mm});
            skLineSegment(sketch, "E6083", {"start": v(257.95, 204.19) * mm, "end": v(259.1, 202.94) * mm});
            skLineSegment(sketch, "E6084", {"start": v(259.1, 202.94) * mm, "end": v(260.44, 201.94) * mm});
            skLineSegment(sketch, "E6085", {"start": v(260.44, 201.94) * mm, "end": v(261.95, 201.16) * mm});
            skLineSegment(sketch, "E6086", {"start": v(261.95, 201.16) * mm, "end": v(263.58, 200.57) * mm});
            skLineSegment(sketch, "E6087", {"start": v(263.58, 200.57) * mm, "end": v(265.32, 200.15) * mm});
            skLineSegment(sketch, "E6088", {"start": v(265.32, 200.15) * mm, "end": v(267.1, 199.86) * mm});
            skLineSegment(sketch, "E6089", {"start": v(267.1, 199.86) * mm, "end": v(268.93, 199.69) * mm});
            skLineSegment(sketch, "E6090", {"start": v(268.93, 199.69) * mm, "end": v(270.75, 199.6) * mm});
            skLineSegment(sketch, "E6091", {"start": v(270.75, 199.6) * mm, "end": v(272.53, 199.57) * mm});
            skLineSegment(sketch, "E6092", {"start": v(272.53, 199.57) * mm, "end": v(274.24, 199.57) * mm});
            skLineSegment(sketch, "E6093", {"start": v(274.24, 199.57) * mm, "end": v(275.84, 199.57) * mm});
            skLineSegment(sketch, "E6094", {"start": v(275.84, 199.57) * mm, "end": v(277.04, 199.55) * mm});
            skLineSegment(sketch, "E6095", {"start": v(277.04, 199.55) * mm, "end": v(278.34, 199.5) * mm});
            skLineSegment(sketch, "E6096", {"start": v(278.34, 199.5) * mm, "end": v(279.73, 199.43) * mm});
            skLineSegment(sketch, "E6097", {"start": v(279.73, 199.43) * mm, "end": v(281.22, 199.34) * mm});
            skLineSegment(sketch, "E6098", {"start": v(281.22, 199.34) * mm, "end": v(282.78, 199.24) * mm});
            skLineSegment(sketch, "E6099", {"start": v(282.78, 199.24) * mm, "end": v(284.43, 199.12) * mm});
            skLineSegment(sketch, "E6100", {"start": v(284.43, 199.12) * mm, "end": v(286.15, 198.98) * mm});
            skLineSegment(sketch, "E6101", {"start": v(286.15, 198.98) * mm, "end": v(287.93, 198.84) * mm});
            skLineSegment(sketch, "E6102", {"start": v(287.93, 198.84) * mm, "end": v(289.77, 198.69) * mm});
            skLineSegment(sketch, "E6103", {"start": v(289.77, 198.69) * mm, "end": v(291.66, 198.53) * mm});
            skLineSegment(sketch, "E6104", {"start": v(291.66, 198.53) * mm, "end": v(293.6, 198.37) * mm});
            skLineSegment(sketch, "E6105", {"start": v(293.6, 198.37) * mm, "end": v(295.59, 198.22) * mm});
            skLineSegment(sketch, "E6106", {"start": v(295.59, 198.22) * mm, "end": v(297.6, 198.06) * mm});
            skLineSegment(sketch, "E6107", {"start": v(297.6, 198.06) * mm, "end": v(299.66, 197.91) * mm});
            skLineSegment(sketch, "E6108", {"start": v(299.66, 197.91) * mm, "end": v(301.73, 197.77) * mm});
            skLineSegment(sketch, "E6109", {"start": v(301.73, 197.77) * mm, "end": v(303.81, 197.65) * mm});
            skLineSegment(sketch, "E6110", {"start": v(303.81, 197.65) * mm, "end": v(305.91, 197.53) * mm});
            skLineSegment(sketch, "E6111", {"start": v(305.91, 197.53) * mm, "end": v(308.02, 197.43) * mm});
            skLineSegment(sketch, "E6112", {"start": v(308.02, 197.43) * mm, "end": v(310.12, 197.35) * mm});
            skLineSegment(sketch, "E6113", {"start": v(310.12, 197.35) * mm, "end": v(312.21, 197.3) * mm});
            skLineSegment(sketch, "E6114", {"start": v(312.21, 197.3) * mm, "end": v(314.3, 197.26) * mm});
            skLineSegment(sketch, "E6115", {"start": v(314.3, 197.26) * mm, "end": v(316.36, 197.25) * mm});
            skLineSegment(sketch, "E6116", {"start": v(316.36, 197.25) * mm, "end": v(318.4, 197.28) * mm});
            skLineSegment(sketch, "E6117", {"start": v(318.4, 197.28) * mm, "end": v(320.4, 197.33) * mm});
            skLineSegment(sketch, "E6118", {"start": v(320.4, 197.33) * mm, "end": v(322.36, 197.42) * mm});
            skLineSegment(sketch, "E6119", {"start": v(322.36, 197.42) * mm, "end": v(324.29, 197.55) * mm});
            skLineSegment(sketch, "E6120", {"start": v(324.29, 197.55) * mm, "end": v(326.16, 197.71) * mm});
            skLineSegment(sketch, "E6121", {"start": v(326.16, 197.71) * mm, "end": v(327.98, 197.92) * mm});
            skLineSegment(sketch, "E6122", {"start": v(327.98, 197.92) * mm, "end": v(329.73, 198.18) * mm});
            skLineSegment(sketch, "E6123", {"start": v(329.73, 198.18) * mm, "end": v(331.42, 198.48) * mm});
            skLineSegment(sketch, "E6124", {"start": v(331.42, 198.48) * mm, "end": v(333.03, 198.83) * mm});
            skLineSegment(sketch, "E6125", {"start": v(333.03, 198.83) * mm, "end": v(334.56, 199.24) * mm});
            skLineSegment(sketch, "E6126", {"start": v(334.56, 199.24) * mm, "end": v(336.01, 199.7) * mm});
            skLineSegment(sketch, "E6127", {"start": v(336.01, 199.7) * mm, "end": v(337.36, 200.22) * mm});
            skLineSegment(sketch, "E6128", {"start": v(337.36, 200.22) * mm, "end": v(338.62, 200.8) * mm});
            skLineSegment(sketch, "E6129", {"start": v(338.62, 200.8) * mm, "end": v(339.77, 201.44) * mm});
            skLineSegment(sketch, "E6130", {"start": v(339.77, 201.44) * mm, "end": v(340.81, 202.15) * mm});
            skLineSegment(sketch, "E6131", {"start": v(340.81, 202.15) * mm, "end": v(341.73, 202.93) * mm});
            skLineSegment(sketch, "E6132", {"start": v(341.73, 202.93) * mm, "end": v(342.68, 204) * mm});
            skLineSegment(sketch, "E6133", {"start": v(342.68, 204) * mm, "end": v(343.45, 205.26) * mm});
            skLineSegment(sketch, "E6134", {"start": v(343.45, 205.26) * mm, "end": v(344.09, 206.7) * mm});
            skLineSegment(sketch, "E6135", {"start": v(344.09, 206.7) * mm, "end": v(344.58, 208.3) * mm});
            skLineSegment(sketch, "E6136", {"start": v(344.58, 208.3) * mm, "end": v(344.96, 210) * mm});
            skLineSegment(sketch, "E6137", {"start": v(344.96, 210) * mm, "end": v(345.22, 211.83) * mm});
            skLineSegment(sketch, "E6138", {"start": v(345.22, 211.83) * mm, "end": v(345.4, 213.74) * mm});
            skLineSegment(sketch, "E6139", {"start": v(345.4, 213.74) * mm, "end": v(345.48, 215.7) * mm});
            skLineSegment(sketch, "E6140", {"start": v(345.48, 215.7) * mm, "end": v(345.5, 217.71) * mm});
            skLineSegment(sketch, "E6141", {"start": v(345.5, 217.71) * mm, "end": v(345.45, 219.74) * mm});
            skLineSegment(sketch, "E6142", {"start": v(345.45, 219.74) * mm, "end": v(345.37, 221.76) * mm});
            skLineSegment(sketch, "E6143", {"start": v(345.37, 221.76) * mm, "end": v(345.25, 223.76) * mm});
            skLineSegment(sketch, "E6144", {"start": v(345.25, 223.76) * mm, "end": v(345.12, 225.7) * mm});
            skLineSegment(sketch, "E6145", {"start": v(345.12, 225.7) * mm, "end": v(344.98, 227.59) * mm});
            skLineSegment(sketch, "E6146", {"start": v(344.98, 227.59) * mm, "end": v(344.85, 229.37) * mm});
            skLineSegment(sketch, "E6147", {"start": v(344.85, 229.37) * mm, "end": v(344.74, 231.05) * mm});
            skLineSegment(sketch, "E6148", {"start": v(344.74, 231.05) * mm, "end": v(344.67, 232.58) * mm});
            skLineSegment(sketch, "E6149", {"start": v(344.67, 232.58) * mm, "end": v(344.64, 233.96) * mm});
            skLineSegment(sketch, "E6150", {"start": v(344.64, 233.96) * mm, "end": v(344.64, 235.8) * mm});
            skLineSegment(sketch, "E6151", {"start": v(344.64, 235.8) * mm, "end": v(344.65, 237.62) * mm});
            skLineSegment(sketch, "E6152", {"start": v(344.65, 237.62) * mm, "end": v(344.68, 239.45) * mm});
            skLineSegment(sketch, "E6153", {"start": v(344.68, 239.45) * mm, "end": v(344.7, 241.28) * mm});
            skLineSegment(sketch, "E6154", {"start": v(344.7, 241.28) * mm, "end": v(344.74, 243.11) * mm});
            skLineSegment(sketch, "E6155", {"start": v(344.74, 243.11) * mm, "end": v(344.77, 244.94) * mm});
            skLineSegment(sketch, "E6156", {"start": v(344.77, 244.94) * mm, "end": v(344.81, 246.76) * mm});
            skLineSegment(sketch, "E6157", {"start": v(344.81, 246.76) * mm, "end": v(344.86, 248.59) * mm});
            skLineSegment(sketch, "E6158", {"start": v(344.86, 248.59) * mm, "end": v(344.9, 250.41) * mm});
            skLineSegment(sketch, "E6159", {"start": v(344.9, 250.41) * mm, "end": v(344.95, 252.23) * mm});
            skLineSegment(sketch, "E6160", {"start": v(344.95, 252.23) * mm, "end": v(345, 254.05) * mm});
            skLineSegment(sketch, "E6161", {"start": v(345, 254.05) * mm, "end": v(345.03, 255.87) * mm});
            skLineSegment(sketch, "E6162", {"start": v(345.03, 255.87) * mm, "end": v(345.07, 257.69) * mm});
            skLineSegment(sketch, "E6163", {"start": v(345.07, 257.69) * mm, "end": v(345.11, 259.5) * mm});
            skLineSegment(sketch, "E6164", {"start": v(345.11, 259.5) * mm, "end": v(345.14, 261.31) * mm});
            skLineSegment(sketch, "E6165", {"start": v(345.14, 261.31) * mm, "end": v(345.17, 263.12) * mm});
            skLineSegment(sketch, "E6166", {"start": v(345.17, 263.12) * mm, "end": v(345.2, 264.93) * mm});
            skLineSegment(sketch, "E6167", {"start": v(345.2, 264.93) * mm, "end": v(345.2, 266.74) * mm});
            skLineSegment(sketch, "E6168", {"start": v(345.2, 266.74) * mm, "end": v(345.2, 268.54) * mm});
            skLineSegment(sketch, "E6169", {"start": v(345.2, 268.54) * mm, "end": v(345.2, 270.34) * mm});
            skLineSegment(sketch, "E6170", {"start": v(345.2, 270.34) * mm, "end": v(345.19, 272.14) * mm});
            skLineSegment(sketch, "E6171", {"start": v(345.19, 272.14) * mm, "end": v(345.16, 273.93) * mm});
            skLineSegment(sketch, "E6172", {"start": v(345.16, 273.93) * mm, "end": v(345.12, 275.72) * mm});
            skLineSegment(sketch, "E6173", {"start": v(345.12, 275.72) * mm, "end": v(345.06, 277.51) * mm});
            skLineSegment(sketch, "E6174", {"start": v(345.06, 277.51) * mm, "end": v(345, 279.3) * mm});
            skLineSegment(sketch, "E6175", {"start": v(345, 279.3) * mm, "end": v(344.91, 281.08) * mm});
            skLineSegment(sketch, "E6176", {"start": v(344.91, 281.08) * mm, "end": v(344.81, 282.86) * mm});
            skLineSegment(sketch, "E6177", {"start": v(344.81, 282.86) * mm, "end": v(344.7, 284.64) * mm});
            skLineSegment(sketch, "E6178", {"start": v(344.7, 284.64) * mm, "end": v(344.56, 286.41) * mm});
            skLineSegment(sketch, "E6179", {"start": v(344.56, 286.41) * mm, "end": v(344.4, 288.18) * mm});
            skLineSegment(sketch, "E6180", {"start": v(344.4, 288.18) * mm, "end": v(344.22, 289.95) * mm});
            skLineSegment(sketch, "E6181", {"start": v(344.22, 289.95) * mm, "end": v(344.02, 291.7) * mm});
            skLineSegment(sketch, "E6182", {"start": v(344.02, 291.7) * mm, "end": v(343.8, 293.47) * mm});
            skLineSegment(sketch, "E6183", {"start": v(343.8, 293.47) * mm, "end": v(343.56, 295.22) * mm});
            skLineSegment(sketch, "E6184", {"start": v(343.56, 295.22) * mm, "end": v(343.29, 296.97) * mm});
            skLineSegment(sketch, "E6185", {"start": v(343.29, 296.97) * mm, "end": v(342.99, 298.72) * mm});
            skLineSegment(sketch, "E6186", {"start": v(342.99, 298.72) * mm, "end": v(342.67, 300.46) * mm});
            skLineSegment(sketch, "E6187", {"start": v(342.67, 300.46) * mm, "end": v(342.32, 302.2) * mm});
            skLineSegment(sketch, "E6188", {"start": v(342.32, 302.2) * mm, "end": v(341.94, 303.93) * mm});
            skLineSegment(sketch, "E6189", {"start": v(341.94, 303.93) * mm, "end": v(341.53, 305.66) * mm});
            skLineSegment(sketch, "E6190", {"start": v(341.53, 305.66) * mm, "end": v(341.09, 307.38) * mm});
            skLineSegment(sketch, "E6191", {"start": v(341.09, 307.38) * mm, "end": v(340.62, 309.1) * mm});
            skLineSegment(sketch, "E6192", {"start": v(340.62, 309.1) * mm, "end": v(340.11, 310.81) * mm});
            skLineSegment(sketch, "E6193", {"start": v(340.11, 310.81) * mm, "end": v(339.58, 312.52) * mm});
            skLineSegment(sketch, "E6194", {"start": v(339.58, 312.52) * mm, "end": v(339, 314.23) * mm});
            skLineSegment(sketch, "E6195", {"start": v(339, 314.23) * mm, "end": v(338.4, 315.92) * mm});
            skLineSegment(sketch, "E6196", {"start": v(338.4, 315.92) * mm, "end": v(337.75, 317.62) * mm});
            skLineSegment(sketch, "E6197", {"start": v(337.75, 317.62) * mm, "end": v(337.07, 319.3) * mm});
            skLineSegment(sketch, "E6198", {"start": v(337.07, 319.3) * mm, "end": v(336.35, 320.99) * mm});
            skLineSegment(sketch, "E6199", {"start": v(336.35, 320.99) * mm, "end": v(335.59, 322.67) * mm});
            skLineSegment(sketch, "E6200", {"start": v(335.59, 322.67) * mm, "end": v(379.03, 322.67) * mm});
            skLineSegment(sketch, "E6201", {"start": v(379.03, 322.67) * mm, "end": v(378.14, 324.09) * mm});
            skLineSegment(sketch, "E6202", {"start": v(378.14, 324.09) * mm, "end": v(377.23, 325.5) * mm});
            skLineSegment(sketch, "E6203", {"start": v(377.23, 325.5) * mm, "end": v(376.3, 326.9) * mm});
            skLineSegment(sketch, "E6204", {"start": v(376.3, 326.9) * mm, "end": v(375.36, 328.31) * mm});
            skLineSegment(sketch, "E6205", {"start": v(375.36, 328.31) * mm, "end": v(374.41, 329.7) * mm});
            skLineSegment(sketch, "E6206", {"start": v(374.41, 329.7) * mm, "end": v(373.44, 331.1) * mm});
            skLineSegment(sketch, "E6207", {"start": v(373.44, 331.1) * mm, "end": v(372.47, 332.49) * mm});
            skLineSegment(sketch, "E6208", {"start": v(372.47, 332.49) * mm, "end": v(371.47, 333.87) * mm});
            skLineSegment(sketch, "E6209", {"start": v(371.47, 333.87) * mm, "end": v(370.47, 335.24) * mm});
            skLineSegment(sketch, "E6210", {"start": v(370.47, 335.24) * mm, "end": v(369.45, 336.62) * mm});
            skLineSegment(sketch, "E6211", {"start": v(369.45, 336.62) * mm, "end": v(368.42, 337.98) * mm});
            skLineSegment(sketch, "E6212", {"start": v(368.42, 337.98) * mm, "end": v(367.37, 339.34) * mm});
            skLineSegment(sketch, "E6213", {"start": v(367.37, 339.34) * mm, "end": v(366.31, 340.7) * mm});
            skLineSegment(sketch, "E6214", {"start": v(366.31, 340.7) * mm, "end": v(365.24, 342.04) * mm});
            skLineSegment(sketch, "E6215", {"start": v(365.24, 342.04) * mm, "end": v(364.16, 343.39) * mm});
            skLineSegment(sketch, "E6216", {"start": v(364.16, 343.39) * mm, "end": v(363.07, 344.72) * mm});
            skLineSegment(sketch, "E6217", {"start": v(363.07, 344.72) * mm, "end": v(361.96, 346.06) * mm});
            skLineSegment(sketch, "E6218", {"start": v(361.96, 346.06) * mm, "end": v(360.84, 347.38) * mm});
            skLineSegment(sketch, "E6219", {"start": v(360.84, 347.38) * mm, "end": v(359.71, 348.7) * mm});
            skLineSegment(sketch, "E6220", {"start": v(359.71, 348.7) * mm, "end": v(358.57, 350.02) * mm});
            skLineSegment(sketch, "E6221", {"start": v(358.57, 350.02) * mm, "end": v(357.42, 351.33) * mm});
            skLineSegment(sketch, "E6222", {"start": v(357.42, 351.33) * mm, "end": v(356.25, 352.63) * mm});
            skLineSegment(sketch, "E6223", {"start": v(356.25, 352.63) * mm, "end": v(355.08, 353.93) * mm});
            skLineSegment(sketch, "E6224", {"start": v(355.08, 353.93) * mm, "end": v(353.9, 355.23) * mm});
            skLineSegment(sketch, "E6225", {"start": v(353.9, 355.23) * mm, "end": v(352.7, 356.51) * mm});
            skLineSegment(sketch, "E6226", {"start": v(352.7, 356.51) * mm, "end": v(351.49, 357.8) * mm});
            skLineSegment(sketch, "E6227", {"start": v(351.49, 357.8) * mm, "end": v(350.27, 359.07) * mm});
            skLineSegment(sketch, "E6228", {"start": v(350.27, 359.07) * mm, "end": v(349.04, 360.34) * mm});
            skLineSegment(sketch, "E6229", {"start": v(349.04, 360.34) * mm, "end": v(347.8, 361.6) * mm});
            skLineSegment(sketch, "E6230", {"start": v(347.8, 361.6) * mm, "end": v(346.55, 362.87) * mm});
            skLineSegment(sketch, "E6231", {"start": v(346.55, 362.87) * mm, "end": v(345.3, 364.12) * mm});
            skLineSegment(sketch, "E6232", {"start": v(345.3, 364.12) * mm, "end": v(344.02, 365.37) * mm});
            skLineSegment(sketch, "E6233", {"start": v(344.02, 365.37) * mm, "end": v(342.74, 366.61) * mm});
            skLineSegment(sketch, "E6234", {"start": v(342.74, 366.61) * mm, "end": v(341.45, 367.85) * mm});
            skLineSegment(sketch, "E6235", {"start": v(341.45, 367.85) * mm, "end": v(340.15, 369.08) * mm});
            skLineSegment(sketch, "E6236", {"start": v(340.15, 369.08) * mm, "end": v(338.85, 370.3) * mm});
            skLineSegment(sketch, "E6237", {"start": v(338.85, 370.3) * mm, "end": v(337.53, 371.52) * mm});
            skLineSegment(sketch, "E6238", {"start": v(337.53, 371.52) * mm, "end": v(336.2, 372.74) * mm});
            skLineSegment(sketch, "E6239", {"start": v(336.2, 372.74) * mm, "end": v(334.87, 373.95) * mm});
            skLineSegment(sketch, "E6240", {"start": v(334.87, 373.95) * mm, "end": v(333.53, 375.15) * mm});
            skLineSegment(sketch, "E6241", {"start": v(333.53, 375.15) * mm, "end": v(332.17, 376.35) * mm});
            skLineSegment(sketch, "E6242", {"start": v(332.17, 376.35) * mm, "end": v(330.81, 377.54) * mm});
            skLineSegment(sketch, "E6243", {"start": v(330.81, 377.54) * mm, "end": v(329.44, 378.72) * mm});
            skLineSegment(sketch, "E6244", {"start": v(329.44, 378.72) * mm, "end": v(328.07, 379.9) * mm});
            skLineSegment(sketch, "E6245", {"start": v(328.07, 379.9) * mm, "end": v(326.68, 381.07) * mm});
            skLineSegment(sketch, "E6246", {"start": v(326.68, 381.07) * mm, "end": v(325.29, 382.24) * mm});
            skLineSegment(sketch, "E6247", {"start": v(325.29, 382.24) * mm, "end": v(323.89, 383.4) * mm});
            skLineSegment(sketch, "E6248", {"start": v(323.89, 383.4) * mm, "end": v(322.48, 384.56) * mm});
            skLineSegment(sketch, "E6249", {"start": v(322.48, 384.56) * mm, "end": v(321.06, 385.71) * mm});
            skLineSegment(sketch, "E6250", {"start": v(321.06, 385.71) * mm, "end": v(319.64, 386.85) * mm});
            skLineSegment(sketch, "E6251", {"start": v(319.64, 386.85) * mm, "end": v(318.21, 388) * mm});
            skLineSegment(sketch, "E6252", {"start": v(318.21, 388) * mm, "end": v(316.77, 389.13) * mm});
            skLineSegment(sketch, "E6253", {"start": v(316.77, 389.13) * mm, "end": v(315.33, 390.25) * mm});
            skLineSegment(sketch, "E6254", {"start": v(315.33, 390.25) * mm, "end": v(313.88, 391.37) * mm});
            skLineSegment(sketch, "E6255", {"start": v(313.88, 391.37) * mm, "end": v(312.42, 392.49) * mm});
            skLineSegment(sketch, "E6256", {"start": v(312.42, 392.49) * mm, "end": v(310.96, 393.6) * mm});
            skLineSegment(sketch, "E6257", {"start": v(310.96, 393.6) * mm, "end": v(309.49, 394.7) * mm});
            skLineSegment(sketch, "E6258", {"start": v(309.49, 394.7) * mm, "end": v(308.01, 395.8) * mm});
            skLineSegment(sketch, "E6259", {"start": v(308.01, 395.8) * mm, "end": v(306.53, 396.89) * mm});
            skLineSegment(sketch, "E6260", {"start": v(306.53, 396.89) * mm, "end": v(305.04, 397.98) * mm});
            skLineSegment(sketch, "E6261", {"start": v(305.04, 397.98) * mm, "end": v(303.55, 399.05) * mm});
            skLineSegment(sketch, "E6262", {"start": v(303.55, 399.05) * mm, "end": v(302.05, 400.13) * mm});
            skLineSegment(sketch, "E6263", {"start": v(302.05, 400.13) * mm, "end": v(300.54, 401.2) * mm});
            skLineSegment(sketch, "E6264", {"start": v(300.54, 401.2) * mm, "end": v(299.03, 402.26) * mm});
            skLineSegment(sketch, "E6265", {"start": v(299.03, 402.26) * mm, "end": v(297.52, 403.31) * mm});
            skLineSegment(sketch, "E6266", {"start": v(297.52, 403.31) * mm, "end": v(296, 404.36) * mm});
            skLineSegment(sketch, "E6267", {"start": v(296, 404.36) * mm, "end": v(294.47, 405.4) * mm});
            skLineSegment(sketch, "E6268", {"start": v(294.47, 405.4) * mm, "end": v(292.94, 406.44) * mm});
            skLineSegment(sketch, "E6269", {"start": v(292.94, 406.44) * mm, "end": v(291.4, 407.47) * mm});
            skLineSegment(sketch, "E6270", {"start": v(291.4, 407.47) * mm, "end": v(289.87, 408.5) * mm});
            skLineSegment(sketch, "E6271", {"start": v(289.87, 408.5) * mm, "end": v(288.32, 409.52) * mm});
            skLineSegment(sketch, "E6272", {"start": v(288.32, 409.52) * mm, "end": v(286.78, 410.53) * mm});
            skLineSegment(sketch, "E6273", {"start": v(286.78, 410.53) * mm, "end": v(285.22, 411.54) * mm});
            skLineSegment(sketch, "E6274", {"start": v(285.22, 411.54) * mm, "end": v(283.67, 412.54) * mm});
            skLineSegment(sketch, "E6275", {"start": v(283.67, 412.54) * mm, "end": v(282.1, 413.54) * mm});
            skLineSegment(sketch, "E6276", {"start": v(282.1, 413.54) * mm, "end": v(280.55, 414.52) * mm});
            skLineSegment(sketch, "E6277", {"start": v(280.55, 414.52) * mm, "end": v(278.98, 415.5) * mm});
            skLineSegment(sketch, "E6278", {"start": v(278.98, 415.5) * mm, "end": v(277.41, 416.48) * mm});
            skLineSegment(sketch, "E6279", {"start": v(277.41, 416.48) * mm, "end": v(275.84, 417.45) * mm});
            skLineSegment(sketch, "E6280", {"start": v(275.84, 417.45) * mm, "end": v(274.26, 418.42) * mm});
            skLineSegment(sketch, "E6281", {"start": v(274.26, 418.42) * mm, "end": v(272.68, 419.38) * mm});
            skLineSegment(sketch, "E6282", {"start": v(272.68, 419.38) * mm, "end": v(271.1, 420.33) * mm});
            skLineSegment(sketch, "E6283", {"start": v(271.1, 420.33) * mm, "end": v(269.52, 421.28) * mm});
            skLineSegment(sketch, "E6284", {"start": v(269.52, 421.28) * mm, "end": v(267.93, 422.21) * mm});
            skLineSegment(sketch, "E6285", {"start": v(267.93, 422.21) * mm, "end": v(266.34, 423.15) * mm});
            skLineSegment(sketch, "E6286", {"start": v(266.34, 423.15) * mm, "end": v(264.75, 424.08) * mm});
            skLineSegment(sketch, "E6287", {"start": v(264.75, 424.08) * mm, "end": v(263.16, 425) * mm});
            skLineSegment(sketch, "E6288", {"start": v(263.16, 425) * mm, "end": v(261.56, 425.91) * mm});
            skLineSegment(sketch, "E6289", {"start": v(261.56, 425.91) * mm, "end": v(259.97, 426.82) * mm});
            skLineSegment(sketch, "E6290", {"start": v(259.97, 426.82) * mm, "end": v(258.37, 427.72) * mm});
            skLineSegment(sketch, "E6291", {"start": v(258.37, 427.72) * mm, "end": v(256.77, 428.62) * mm});
            skLineSegment(sketch, "E6292", {"start": v(256.77, 428.62) * mm, "end": v(255.17, 429.5) * mm});
            skLineSegment(sketch, "E6293", {"start": v(255.17, 429.5) * mm, "end": v(253.57, 430.4) * mm});
            skLineSegment(sketch, "E6294", {"start": v(253.57, 430.4) * mm, "end": v(251.96, 431.27) * mm});
            skLineSegment(sketch, "E6295", {"start": v(251.96, 431.27) * mm, "end": v(250.36, 432.14) * mm});
            skLineSegment(sketch, "E6296", {"start": v(250.36, 432.14) * mm, "end": v(248.76, 433) * mm});
            skLineSegment(sketch, "E6297", {"start": v(248.76, 433) * mm, "end": v(247.15, 433.86) * mm});
            skLineSegment(sketch, "E6298", {"start": v(247.15, 433.86) * mm, "end": v(245.55, 434.72) * mm});
            skLineSegment(sketch, "E6299", {"start": v(245.55, 434.72) * mm, "end": v(243.94, 435.56) * mm});
            skLineSegment(sketch, "E6300", {"start": v(243.94, 435.56) * mm, "end": v(242.33, 436.4) * mm});
            skLineSegment(sketch, "E6301", {"start": v(242.33, 436.4) * mm, "end": v(240.73, 437.23) * mm});
            skLineSegment(sketch, "E6302", {"start": v(240.73, 437.23) * mm, "end": v(239.12, 438.06) * mm});
            skLineSegment(sketch, "E6303", {"start": v(239.12, 438.06) * mm, "end": v(237.52, 438.88) * mm});
            skLineSegment(sketch, "E6304", {"start": v(237.52, 438.88) * mm, "end": v(235.91, 439.7) * mm});
            skLineSegment(sketch, "E6305", {"start": v(235.91, 439.7) * mm, "end": v(234.3, 440.5) * mm});
            skLineSegment(sketch, "E6306", {"start": v(234.3, 440.5) * mm, "end": v(232.7, 441.3) * mm});
            skLineSegment(sketch, "E6307", {"start": v(232.7, 441.3) * mm, "end": v(231.1, 442.1) * mm});
            skLineSegment(sketch, "E6308", {"start": v(231.1, 442.1) * mm, "end": v(229.5, 442.89) * mm});
            skLineSegment(sketch, "E6309", {"start": v(229.5, 442.89) * mm, "end": v(227.9, 443.67) * mm});
            skLineSegment(sketch, "E6310", {"start": v(227.9, 443.67) * mm, "end": v(226.3, 444.44) * mm});
            skLineSegment(sketch, "E6311", {"start": v(226.3, 444.44) * mm, "end": v(224.7, 445.21) * mm});
            skLineSegment(sketch, "E6312", {"start": v(224.7, 445.21) * mm, "end": v(223.1, 445.97) * mm});
            skLineSegment(sketch, "E6313", {"start": v(223.1, 445.97) * mm, "end": v(221.5, 446.73) * mm});
            skLineSegment(sketch, "E6314", {"start": v(221.5, 446.73) * mm, "end": v(219.91, 447.48) * mm});
            skLineSegment(sketch, "E6315", {"start": v(219.91, 447.48) * mm, "end": v(218.32, 448.22) * mm});
            skLineSegment(sketch, "E6316", {"start": v(218.32, 448.22) * mm, "end": v(216.73, 448.96) * mm});
            skLineSegment(sketch, "E6317", {"start": v(216.73, 448.96) * mm, "end": v(215.15, 449.69) * mm});
            skLineSegment(sketch, "E6318", {"start": v(215.15, 449.69) * mm, "end": v(213.56, 450.41) * mm});
            skLineSegment(sketch, "E6319", {"start": v(213.56, 450.41) * mm, "end": v(211.98, 451.13) * mm});
            skLineSegment(sketch, "E6320", {"start": v(211.98, 451.13) * mm, "end": v(210.4, 451.84) * mm});
            skLineSegment(sketch, "E6321", {"start": v(210.4, 451.84) * mm, "end": v(208.83, 452.54) * mm});
            skLineSegment(sketch, "E6322", {"start": v(208.83, 452.54) * mm, "end": v(207.25, 453.24) * mm});
            skLineSegment(sketch, "E6323", {"start": v(207.25, 453.24) * mm, "end": v(205.68, 453.93) * mm});
            skLineSegment(sketch, "E6324", {"start": v(205.68, 453.93) * mm, "end": v(204.12, 454.61) * mm});
            skLineSegment(sketch, "E6325", {"start": v(204.12, 454.61) * mm, "end": v(202.55, 455.3) * mm});
            skLineSegment(sketch, "E6326", {"start": v(202.55, 455.3) * mm, "end": v(201, 455.96) * mm});
            skLineSegment(sketch, "E6327", {"start": v(201, 455.96) * mm, "end": v(199.44, 456.63) * mm});
            skLineSegment(sketch, "E6328", {"start": v(199.44, 456.63) * mm, "end": v(197.88, 457.28) * mm});
            skLineSegment(sketch, "E6329", {"start": v(197.88, 457.28) * mm, "end": v(196.34, 457.93) * mm});
            skLineSegment(sketch, "E6330", {"start": v(196.34, 457.93) * mm, "end": v(194.8, 458.58) * mm});
            skLineSegment(sketch, "E6331", {"start": v(194.8, 458.58) * mm, "end": v(193.25, 459.22) * mm});
            skLineSegment(sketch, "E6332", {"start": v(193.25, 459.22) * mm, "end": v(191.72, 459.85) * mm});
            skLineSegment(sketch, "E6333", {"start": v(191.72, 459.85) * mm, "end": v(190.19, 460.47) * mm});
            skLineSegment(sketch, "E6334", {"start": v(190.19, 460.47) * mm, "end": v(188.66, 461.09) * mm});
            skLineSegment(sketch, "E6335", {"start": v(188.66, 461.09) * mm, "end": v(187.14, 461.7) * mm});
            skLineSegment(sketch, "E6336", {"start": v(187.14, 461.7) * mm, "end": v(185.9, 462.2) * mm});
            skLineSegment(sketch, "E6337", {"start": v(185.9, 462.2) * mm, "end": v(184.6, 462.74) * mm});
            skLineSegment(sketch, "E6338", {"start": v(184.6, 462.74) * mm, "end": v(183.27, 463.3) * mm});
            skLineSegment(sketch, "E6339", {"start": v(183.27, 463.3) * mm, "end": v(181.9, 463.87) * mm});
            skLineSegment(sketch, "E6340", {"start": v(181.9, 463.87) * mm, "end": v(180.5, 464.47) * mm});
            skLineSegment(sketch, "E6341", {"start": v(180.5, 464.47) * mm, "end": v(179.06, 465.08) * mm});
            skLineSegment(sketch, "E6342", {"start": v(179.06, 465.08) * mm, "end": v(177.59, 465.71) * mm});
            skLineSegment(sketch, "E6343", {"start": v(177.59, 465.71) * mm, "end": v(176.09, 466.36) * mm});
            skLineSegment(sketch, "E6344", {"start": v(176.09, 466.36) * mm, "end": v(174.55, 467) * mm});
            skLineSegment(sketch, "E6345", {"start": v(174.55, 467) * mm, "end": v(173, 467.67) * mm});
            skLineSegment(sketch, "E6346", {"start": v(173, 467.67) * mm, "end": v(171.4, 468.33) * mm});
            skLineSegment(sketch, "E6347", {"start": v(171.4, 468.33) * mm, "end": v(169.8, 469) * mm});
            skLineSegment(sketch, "E6348", {"start": v(169.8, 469) * mm, "end": v(168.16, 469.67) * mm});
            skLineSegment(sketch, "E6349", {"start": v(168.16, 469.67) * mm, "end": v(166.5, 470.34) * mm});
            skLineSegment(sketch, "E6350", {"start": v(166.5, 470.34) * mm, "end": v(164.84, 471) * mm});
            skLineSegment(sketch, "E6351", {"start": v(164.84, 471) * mm, "end": v(163.15, 471.65) * mm});
            skLineSegment(sketch, "E6352", {"start": v(163.15, 471.65) * mm, "end": v(161.45, 472.3) * mm});
            skLineSegment(sketch, "E6353", {"start": v(161.45, 472.3) * mm, "end": v(159.73, 472.93) * mm});
            skLineSegment(sketch, "E6354", {"start": v(159.73, 472.93) * mm, "end": v(158, 473.55) * mm});
            skLineSegment(sketch, "E6355", {"start": v(158, 473.55) * mm, "end": v(156.26, 474.16) * mm});
            skLineSegment(sketch, "E6356", {"start": v(156.26, 474.16) * mm, "end": v(154.51, 474.74) * mm});
            skLineSegment(sketch, "E6357", {"start": v(154.51, 474.74) * mm, "end": v(152.76, 475.3) * mm});
            skLineSegment(sketch, "E6358", {"start": v(152.76, 475.3) * mm, "end": v(151, 475.84) * mm});
            skLineSegment(sketch, "E6359", {"start": v(151, 475.84) * mm, "end": v(149.24, 476.35) * mm});
            skLineSegment(sketch, "E6360", {"start": v(149.24, 476.35) * mm, "end": v(147.48, 476.84) * mm});
            skLineSegment(sketch, "E6361", {"start": v(147.48, 476.84) * mm, "end": v(145.72, 477.3) * mm});
            skLineSegment(sketch, "E6362", {"start": v(145.72, 477.3) * mm, "end": v(143.97, 477.71) * mm});
            skLineSegment(sketch, "E6363", {"start": v(143.97, 477.71) * mm, "end": v(142.21, 478.1) * mm});
            skLineSegment(sketch, "E6364", {"start": v(142.21, 478.1) * mm, "end": v(140.47, 478.44) * mm});
            skLineSegment(sketch, "E6365", {"start": v(140.47, 478.44) * mm, "end": v(138.73, 478.74) * mm});
            skLineSegment(sketch, "E6366", {"start": v(138.73, 478.74) * mm, "end": v(137, 479) * mm});
            skLineSegment(sketch, "E6367", {"start": v(137, 479) * mm, "end": v(135.29, 479.22) * mm});
            skLineSegment(sketch, "E6368", {"start": v(135.29, 479.22) * mm, "end": v(133.58, 479.39) * mm});
            skLineSegment(sketch, "E6369", {"start": v(133.58, 479.39) * mm, "end": v(131.9, 479.5) * mm});
            skLineSegment(sketch, "E6370", {"start": v(131.9, 479.5) * mm, "end": v(130.23, 479.57) * mm});
            skLineSegment(sketch, "E6371", {"start": v(130.23, 479.57) * mm, "end": v(128.57, 479.58) * mm});
            skLineSegment(sketch, "E6372", {"start": v(128.57, 479.58) * mm, "end": v(126.94, 479.53) * mm});
            skLineSegment(sketch, "E6373", {"start": v(126.94, 479.53) * mm, "end": v(125.33, 479.42) * mm});
            skLineSegment(sketch, "E6374", {"start": v(125.33, 479.42) * mm, "end": v(123.75, 479.25) * mm});
            skLineSegment(sketch, "E6375", {"start": v(123.75, 479.25) * mm, "end": v(122.2, 479) * mm});
            skLineSegment(sketch, "E6376", {"start": v(122.2, 479) * mm, "end": v(120.66, 478.7) * mm});
            skLineSegment(sketch, "E6377", {"start": v(120.66, 478.7) * mm, "end": v(119.16, 478.33) * mm});
            skLineSegment(sketch, "E6378", {"start": v(119.16, 478.33) * mm, "end": v(117.7, 477.88) * mm});
            skLineSegment(sketch, "E6379", {"start": v(117.7, 477.88) * mm, "end": v(116.26, 477.36) * mm});
            skLineSegment(sketch, "E6380", {"start": v(116.26, 477.36) * mm, "end": v(114.85, 476.77) * mm});
            skLineSegment(sketch, "E6381", {"start": v(114.85, 476.77) * mm, "end": v(113.5, 476.09) * mm});
            skLineSegment(sketch, "E6382", {"start": v(113.5, 476.09) * mm, "end": v(112.16, 475.33) * mm});
            skLineSegment(sketch, "E6383", {"start": v(112.16, 475.33) * mm, "end": v(110.88, 474.48) * mm});
            skLineSegment(sketch, "E6384", {"start": v(110.88, 474.48) * mm, "end": v(109.64, 473.55) * mm});
            skLineSegment(sketch, "E6385", {"start": v(109.64, 473.55) * mm, "end": v(108.28, 472.38) * mm});
            skLineSegment(sketch, "E6386", {"start": v(108.28, 472.38) * mm, "end": v(107.04, 471.13) * mm});
            skLineSegment(sketch, "E6387", {"start": v(107.04, 471.13) * mm, "end": v(105.92, 469.82) * mm});
            skLineSegment(sketch, "E6388", {"start": v(105.92, 469.82) * mm, "end": v(104.92, 468.44) * mm});
            skLineSegment(sketch, "E6389", {"start": v(104.92, 468.44) * mm, "end": v(104.02, 467) * mm});
            skLineSegment(sketch, "E6390", {"start": v(104.02, 467) * mm, "end": v(103.22, 465.5) * mm});
            skLineSegment(sketch, "E6391", {"start": v(103.22, 465.5) * mm, "end": v(102.5, 463.97) * mm});
            skLineSegment(sketch, "E6392", {"start": v(102.5, 463.97) * mm, "end": v(101.88, 462.38) * mm});
            skLineSegment(sketch, "E6393", {"start": v(101.88, 462.38) * mm, "end": v(101.33, 460.76) * mm});
            skLineSegment(sketch, "E6394", {"start": v(101.33, 460.76) * mm, "end": v(100.85, 459.1) * mm});
            skLineSegment(sketch, "E6395", {"start": v(100.85, 459.1) * mm, "end": v(100.44, 457.41) * mm});
            skLineSegment(sketch, "E6396", {"start": v(100.44, 457.41) * mm, "end": v(100.09, 455.7) * mm});
            skLineSegment(sketch, "E6397", {"start": v(100.09, 455.7) * mm, "end": v(99.78, 453.97) * mm});
            skLineSegment(sketch, "E6398", {"start": v(99.78, 453.97) * mm, "end": v(99.52, 452.22) * mm});
            skLineSegment(sketch, "E6399", {"start": v(99.52, 452.22) * mm, "end": v(99.3, 450.46) * mm});
            skLineSegment(sketch, "E6400", {"start": v(99.3, 450.46) * mm, "end": v(99.11, 448.69) * mm});
            skLineSegment(sketch, "E6401", {"start": v(99.11, 448.69) * mm, "end": v(98.95, 446.92) * mm});
            skLineSegment(sketch, "E6402", {"start": v(98.95, 446.92) * mm, "end": v(98.8, 445.16) * mm});
            skLineSegment(sketch, "E6403", {"start": v(98.8, 445.16) * mm, "end": v(98.66, 443.4) * mm});
            skLineSegment(sketch, "E6404", {"start": v(98.66, 443.4) * mm, "end": v(98.53, 441.66) * mm});
            skLineSegment(sketch, "E6405", {"start": v(98.53, 441.66) * mm, "end": v(98.4, 439.93) * mm});
            skLineSegment(sketch, "E6406", {"start": v(98.4, 439.93) * mm, "end": v(98.26, 438.23) * mm});
            skLineSegment(sketch, "E6407", {"start": v(98.26, 438.23) * mm, "end": v(98.1, 436.55) * mm});
            skLineSegment(sketch, "E6408", {"start": v(98.1, 436.55) * mm, "end": v(97.92, 434.9) * mm});
            skLineSegment(sketch, "E6409", {"start": v(97.92, 434.9) * mm, "end": v(97.7, 433.13) * mm});
            skLineSegment(sketch, "E6410", {"start": v(97.7, 433.13) * mm, "end": v(97.49, 431.35) * mm});
            skLineSegment(sketch, "E6411", {"start": v(97.49, 431.35) * mm, "end": v(97.27, 429.56) * mm});
            skLineSegment(sketch, "E6412", {"start": v(97.27, 429.56) * mm, "end": v(97.05, 427.78) * mm});
            skLineSegment(sketch, "E6413", {"start": v(97.05, 427.78) * mm, "end": v(96.83, 425.99) * mm});
            skLineSegment(sketch, "E6414", {"start": v(96.83, 425.99) * mm, "end": v(96.6, 424.2) * mm});
            skLineSegment(sketch, "E6415", {"start": v(96.6, 424.2) * mm, "end": v(96.38, 422.4) * mm});
            skLineSegment(sketch, "E6416", {"start": v(96.38, 422.4) * mm, "end": v(96.16, 420.6) * mm});
            skLineSegment(sketch, "E6417", {"start": v(96.16, 420.6) * mm, "end": v(95.93, 418.8) * mm});
            skLineSegment(sketch, "E6418", {"start": v(95.93, 418.8) * mm, "end": v(95.7, 417) * mm});
            skLineSegment(sketch, "E6419", {"start": v(95.7, 417) * mm, "end": v(95.48, 415.2) * mm});
            skLineSegment(sketch, "E6420", {"start": v(95.48, 415.2) * mm, "end": v(95.25, 413.4) * mm});
            skLineSegment(sketch, "E6421", {"start": v(95.25, 413.4) * mm, "end": v(95.03, 411.6) * mm});
            skLineSegment(sketch, "E6422", {"start": v(95.03, 411.6) * mm, "end": v(94.8, 409.79) * mm});
            skLineSegment(sketch, "E6423", {"start": v(94.8, 409.79) * mm, "end": v(94.57, 407.98) * mm});
            skLineSegment(sketch, "E6424", {"start": v(94.57, 407.98) * mm, "end": v(94.35, 406.17) * mm});
            skLineSegment(sketch, "E6425", {"start": v(94.35, 406.17) * mm, "end": v(94.12, 404.36) * mm});
            skLineSegment(sketch, "E6426", {"start": v(94.12, 404.36) * mm, "end": v(93.9, 402.54) * mm});
            skLineSegment(sketch, "E6427", {"start": v(93.9, 402.54) * mm, "end": v(93.67, 400.73) * mm});
            skLineSegment(sketch, "E6428", {"start": v(93.67, 400.73) * mm, "end": v(93.45, 398.91) * mm});
            skLineSegment(sketch, "E6429", {"start": v(93.45, 398.91) * mm, "end": v(93.23, 397.1) * mm});
            skLineSegment(sketch, "E6430", {"start": v(93.23, 397.1) * mm, "end": v(93.01, 395.28) * mm});
            skLineSegment(sketch, "E6431", {"start": v(93.01, 395.28) * mm, "end": v(92.8, 393.46) * mm});
            skLineSegment(sketch, "E6432", {"start": v(92.8, 393.46) * mm, "end": v(92.58, 391.64) * mm});
            skLineSegment(sketch, "E6433", {"start": v(92.58, 391.64) * mm, "end": v(92.36, 389.82) * mm});
            skLineSegment(sketch, "E6434", {"start": v(92.36, 389.82) * mm, "end": v(92.15, 388) * mm});
            skLineSegment(sketch, "E6435", {"start": v(92.15, 388) * mm, "end": v(91.94, 386.17) * mm});
            skLineSegment(sketch, "E6436", {"start": v(91.94, 386.17) * mm, "end": v(91.74, 384.35) * mm});
            skLineSegment(sketch, "E6437", {"start": v(91.74, 384.35) * mm, "end": v(91.53, 382.53) * mm});
            skLineSegment(sketch, "E6438", {"start": v(91.53, 382.53) * mm, "end": v(91.33, 380.7) * mm});
            skLineSegment(sketch, "E6439", {"start": v(91.33, 380.7) * mm, "end": v(91.13, 378.88) * mm});
            skLineSegment(sketch, "E6440", {"start": v(91.13, 378.88) * mm, "end": v(90.94, 377.06) * mm});
            skLineSegment(sketch, "E6441", {"start": v(90.94, 377.06) * mm, "end": v(90.75, 375.23) * mm});
            skLineSegment(sketch, "E6442", {"start": v(90.75, 375.23) * mm, "end": v(90.56, 373.41) * mm});
            skLineSegment(sketch, "E6443", {"start": v(90.56, 373.41) * mm, "end": v(90.38, 371.59) * mm});
            skLineSegment(sketch, "E6444", {"start": v(90.38, 371.59) * mm, "end": v(90.2, 369.76) * mm});
            skLineSegment(sketch, "E6445", {"start": v(90.2, 369.76) * mm, "end": v(90.03, 367.94) * mm});
            skLineSegment(sketch, "E6446", {"start": v(90.03, 367.94) * mm, "end": v(89.85, 366.12) * mm});
            skLineSegment(sketch, "E6447", {"start": v(89.85, 366.12) * mm, "end": v(89.69, 364.3) * mm});
            skLineSegment(sketch, "E6448", {"start": v(89.69, 364.3) * mm, "end": v(89.53, 362.47) * mm});
            skLineSegment(sketch, "E6449", {"start": v(89.53, 362.47) * mm, "end": v(89.37, 360.65) * mm});
            skLineSegment(sketch, "E6450", {"start": v(89.37, 360.65) * mm, "end": v(89.22, 358.83) * mm});
            skLineSegment(sketch, "E6451", {"start": v(89.22, 358.83) * mm, "end": v(89.08, 357) * mm});
            skLineSegment(sketch, "E6452", {"start": v(89.08, 357) * mm, "end": v(88.94, 355.19) * mm});
            skLineSegment(sketch, "E6453", {"start": v(88.94, 355.19) * mm, "end": v(88.8, 353.37) * mm});
            skLineSegment(sketch, "E6454", {"start": v(88.8, 353.37) * mm, "end": v(88.67, 351.55) * mm});
            skLineSegment(sketch, "E6455", {"start": v(88.67, 351.55) * mm, "end": v(88.55, 349.74) * mm});
            skLineSegment(sketch, "E6456", {"start": v(88.55, 349.74) * mm, "end": v(88.44, 347.92) * mm});
            skLineSegment(sketch, "E6457", {"start": v(88.44, 347.92) * mm, "end": v(88.33, 346.1) * mm});
            skLineSegment(sketch, "E6458", {"start": v(88.33, 346.1) * mm, "end": v(88.22, 344.3) * mm});
            skLineSegment(sketch, "E6459", {"start": v(88.22, 344.3) * mm, "end": v(88.13, 342.48) * mm});
            skLineSegment(sketch, "E6460", {"start": v(88.13, 342.48) * mm, "end": v(88.04, 340.67) * mm});
            skLineSegment(sketch, "E6461", {"start": v(88.04, 340.67) * mm, "end": v(87.96, 338.86) * mm});
            skLineSegment(sketch, "E6462", {"start": v(87.96, 338.86) * mm, "end": v(87.88, 337.05) * mm});
            skLineSegment(sketch, "E6463", {"start": v(87.88, 337.05) * mm, "end": v(87.81, 335.25) * mm});
            skLineSegment(sketch, "E6464", {"start": v(87.81, 335.25) * mm, "end": v(87.76, 333.45) * mm});
            skLineSegment(sketch, "E6465", {"start": v(87.76, 333.45) * mm, "end": v(87.7, 331.64) * mm});
            skLineSegment(sketch, "E6466", {"start": v(87.7, 331.64) * mm, "end": v(87.66, 329.84) * mm});
            skLineSegment(sketch, "E6467", {"start": v(87.66, 329.84) * mm, "end": v(87.63, 328.05) * mm});
            skLineSegment(sketch, "E6468", {"start": v(87.63, 328.05) * mm, "end": v(87.6, 326.25) * mm});
            skLineSegment(sketch, "E6469", {"start": v(87.6, 326.25) * mm, "end": v(87.58, 324.46) * mm});
            skLineSegment(sketch, "E6470", {"start": v(87.58, 324.46) * mm, "end": v(87.57, 322.67) * mm});
            skLineSegment(sketch, "E6471", {"start": v(87.57, 322.67) * mm, "end": v(147.31, 322.67) * mm});
            skLineSegment(sketch, "E6472", {"start": v(147.31, 322.67) * mm, "end": v(146.5, 320.91) * mm});
            skLineSegment(sketch, "E6473", {"start": v(146.5, 320.91) * mm, "end": v(145.73, 319.16) * mm});
            skLineSegment(sketch, "E6474", {"start": v(145.73, 319.16) * mm, "end": v(145, 317.42) * mm});
            skLineSegment(sketch, "E6475", {"start": v(145, 317.42) * mm, "end": v(144.3, 315.68) * mm});
            skLineSegment(sketch, "E6476", {"start": v(144.3, 315.68) * mm, "end": v(143.65, 313.94) * mm});
            skLineSegment(sketch, "E6477", {"start": v(143.65, 313.94) * mm, "end": v(143.03, 312.21) * mm});
            skLineSegment(sketch, "E6478", {"start": v(143.03, 312.21) * mm, "end": v(142.44, 310.48) * mm});
            skLineSegment(sketch, "E6479", {"start": v(142.44, 310.48) * mm, "end": v(141.89, 308.76) * mm});
            skLineSegment(sketch, "E6480", {"start": v(141.89, 308.76) * mm, "end": v(141.37, 307.03) * mm});
            skLineSegment(sketch, "E6481", {"start": v(141.37, 307.03) * mm, "end": v(140.88, 305.31) * mm});
            skLineSegment(sketch, "E6482", {"start": v(140.88, 305.31) * mm, "end": v(140.43, 303.6) * mm});
            skLineSegment(sketch, "E6483", {"start": v(140.43, 303.6) * mm, "end": v(140, 301.87) * mm});
            skLineSegment(sketch, "E6484", {"start": v(140, 301.87) * mm, "end": v(139.6, 300.16) * mm});
            skLineSegment(sketch, "E6485", {"start": v(139.6, 300.16) * mm, "end": v(139.24, 298.44) * mm});
            skLineSegment(sketch, "E6486", {"start": v(139.24, 298.44) * mm, "end": v(138.9, 296.72) * mm});
            skLineSegment(sketch, "E6487", {"start": v(138.9, 296.72) * mm, "end": v(138.58, 295) * mm});
            skLineSegment(sketch, "E6488", {"start": v(138.58, 295) * mm, "end": v(138.3, 293.3) * mm});
            skLineSegment(sketch, "E6489", {"start": v(138.3, 293.3) * mm, "end": v(138.03, 291.57) * mm});
            skLineSegment(sketch, "E6490", {"start": v(138.03, 291.57) * mm, "end": v(137.79, 289.85) * mm});
            skLineSegment(sketch, "E6491", {"start": v(137.79, 289.85) * mm, "end": v(137.57, 288.13) * mm});
            skLineSegment(sketch, "E6492", {"start": v(137.57, 288.13) * mm, "end": v(137.37, 286.4) * mm});
            skLineSegment(sketch, "E6493", {"start": v(137.37, 286.4) * mm, "end": v(137.2, 284.68) * mm});
            skLineSegment(sketch, "E6494", {"start": v(137.2, 284.68) * mm, "end": v(137.03, 282.95) * mm});
            skLineSegment(sketch, "E6495", {"start": v(137.03, 282.95) * mm, "end": v(136.9, 281.22) * mm});
            skLineSegment(sketch, "E6496", {"start": v(136.9, 281.22) * mm, "end": v(136.77, 279.48) * mm});
            skLineSegment(sketch, "E6497", {"start": v(136.77, 279.48) * mm, "end": v(136.66, 277.74) * mm});
            skLineSegment(sketch, "E6498", {"start": v(136.66, 277.74) * mm, "end": v(136.57, 276) * mm});
            skLineSegment(sketch, "E6499", {"start": v(136.57, 276) * mm, "end": v(136.5, 274.25) * mm});
            skLineSegment(sketch, "E6500", {"start": v(136.5, 274.25) * mm, "end": v(136.43, 272.5) * mm});
            skLineSegment(sketch, "E6501", {"start": v(136.43, 272.5) * mm, "end": v(136.38, 270.73) * mm});
            skLineSegment(sketch, "E6502", {"start": v(136.38, 270.73) * mm, "end": v(136.34, 268.96) * mm});
            skLineSegment(sketch, "E6503", {"start": v(136.34, 268.96) * mm, "end": v(136.3, 267.2) * mm});
            skLineSegment(sketch, "E6504", {"start": v(136.3, 267.2) * mm, "end": v(136.29, 265.4) * mm});
            skLineSegment(sketch, "E6505", {"start": v(136.29, 265.4) * mm, "end": v(136.28, 263.62) * mm});
            skLineSegment(sketch, "E6506", {"start": v(136.28, 263.62) * mm, "end": v(136.27, 261.82) * mm});
            skLineSegment(sketch, "E6507", {"start": v(136.27, 261.82) * mm, "end": v(136.28, 260.02) * mm});
            skLineSegment(sketch, "E6508", {"start": v(136.28, 260.02) * mm, "end": v(136.28, 258.2) * mm});
            skLineSegment(sketch, "E6509", {"start": v(136.28, 258.2) * mm, "end": v(136.3, 256.38) * mm});
            skLineSegment(sketch, "E6510", {"start": v(136.3, 256.38) * mm, "end": v(136.31, 254.55) * mm});
            skLineSegment(sketch, "E6511", {"start": v(136.31, 254.55) * mm, "end": v(136.33, 252.71) * mm});
            skLineSegment(sketch, "E6512", {"start": v(136.33, 252.71) * mm, "end": v(136.35, 250.86) * mm});
            skLineSegment(sketch, "E6513", {"start": v(136.35, 250.86) * mm, "end": v(136.37, 249) * mm});
            skLineSegment(sketch, "E6514", {"start": v(136.37, 249) * mm, "end": v(136.4, 247.12) * mm});
            skLineSegment(sketch, "E6515", {"start": v(136.4, 247.12) * mm, "end": v(136.4, 245.24) * mm});
            skLineSegment(sketch, "E6516", {"start": v(136.4, 245.24) * mm, "end": v(136.43, 243.34) * mm});
            skLineSegment(sketch, "E6517", {"start": v(136.43, 243.34) * mm, "end": v(136.44, 241.44) * mm});
            skLineSegment(sketch, "E6518", {"start": v(136.44, 241.44) * mm, "end": v(136.45, 239.52) * mm});
            skLineSegment(sketch, "E6519", {"start": v(136.45, 239.52) * mm, "end": v(136.45, 237.58) * mm});
            skLineSegment(sketch, "E6520", {"start": v(136.45, 237.58) * mm, "end": v(136.45, 118.1) * mm});
            skLineSegment(sketch, "E6521", {"start": v(136.45, 118.1) * mm, "end": v(136.44, 116.29) * mm});
            skLineSegment(sketch, "E6522", {"start": v(136.44, 116.29) * mm, "end": v(136.42, 114.47) * mm});
            skLineSegment(sketch, "E6523", {"start": v(136.42, 114.47) * mm, "end": v(136.4, 112.66) * mm});
            skLineSegment(sketch, "E6524", {"start": v(136.4, 112.66) * mm, "end": v(136.36, 110.85) * mm});
            skLineSegment(sketch, "E6525", {"start": v(136.36, 110.85) * mm, "end": v(136.31, 109.03) * mm});
            skLineSegment(sketch, "E6526", {"start": v(136.31, 109.03) * mm, "end": v(136.26, 107.22) * mm});
            skLineSegment(sketch, "E6527", {"start": v(136.26, 107.22) * mm, "end": v(136.2, 105.42) * mm});
            skLineSegment(sketch, "E6528", {"start": v(136.2, 105.42) * mm, "end": v(136.15, 103.6) * mm});
            skLineSegment(sketch, "E6529", {"start": v(136.15, 103.6) * mm, "end": v(136.1, 101.8) * mm});
            skLineSegment(sketch, "E6530", {"start": v(136.1, 101.8) * mm, "end": v(136.04, 100) * mm});
            skLineSegment(sketch, "E6531", {"start": v(136.04, 100) * mm, "end": v(135.98, 98.2) * mm});
            skLineSegment(sketch, "E6532", {"start": v(135.98, 98.2) * mm, "end": v(135.94, 96.4) * mm});
            skLineSegment(sketch, "E6533", {"start": v(135.94, 96.4) * mm, "end": v(135.9, 94.61) * mm});
            skLineSegment(sketch, "E6534", {"start": v(135.9, 94.61) * mm, "end": v(135.86, 92.83) * mm});
            skLineSegment(sketch, "E6535", {"start": v(135.86, 92.83) * mm, "end": v(135.84, 91.04) * mm});
            skLineSegment(sketch, "E6536", {"start": v(135.84, 91.04) * mm, "end": v(135.83, 89.26) * mm});
            skLineSegment(sketch, "E6537", {"start": v(135.83, 89.26) * mm, "end": v(135.83, 87.48) * mm});
            skLineSegment(sketch, "E6538", {"start": v(135.83, 87.48) * mm, "end": v(135.85, 85.7) * mm});
            skLineSegment(sketch, "E6539", {"start": v(135.85, 85.7) * mm, "end": v(135.89, 83.94) * mm});
            skLineSegment(sketch, "E6540", {"start": v(135.89, 83.94) * mm, "end": v(135.94, 82.18) * mm});
            skLineSegment(sketch, "E6541", {"start": v(135.94, 82.18) * mm, "end": v(136.01, 80.42) * mm});
            skLineSegment(sketch, "E6542", {"start": v(136.01, 80.42) * mm, "end": v(136.11, 78.67) * mm});
            skLineSegment(sketch, "E6543", {"start": v(136.11, 78.67) * mm, "end": v(136.23, 76.92) * mm});
            skLineSegment(sketch, "E6544", {"start": v(136.23, 76.92) * mm, "end": v(136.38, 75.18) * mm});
            skLineSegment(sketch, "E6545", {"start": v(136.38, 75.18) * mm, "end": v(136.55, 73.44) * mm});
            skLineSegment(sketch, "E6546", {"start": v(136.55, 73.44) * mm, "end": v(136.75, 71.72) * mm});
            skLineSegment(sketch, "E6547", {"start": v(136.75, 71.72) * mm, "end": v(136.99, 70) * mm});
            skLineSegment(sketch, "E6548", {"start": v(136.99, 70) * mm, "end": v(137.25, 68.28) * mm});
            skLineSegment(sketch, "E6549", {"start": v(137.25, 68.28) * mm, "end": v(137.55, 66.58) * mm});
            skLineSegment(sketch, "E6550", {"start": v(137.55, 66.58) * mm, "end": v(137.89, 64.88) * mm});
            skLineSegment(sketch, "E6551", {"start": v(137.89, 64.88) * mm, "end": v(138.26, 63.2) * mm});
            skLineSegment(sketch, "E6552", {"start": v(138.26, 63.2) * mm, "end": v(138.67, 61.5) * mm});
            skLineSegment(sketch, "E6553", {"start": v(138.67, 61.5) * mm, "end": v(139.12, 59.84) * mm});
            skLineSegment(sketch, "E6554", {"start": v(139.12, 59.84) * mm, "end": v(139.62, 58.17) * mm});
            skLineSegment(sketch, "E6555", {"start": v(139.62, 58.17) * mm, "end": v(140.16, 56.52) * mm});
            skLineSegment(sketch, "E6556", {"start": v(140.16, 56.52) * mm, "end": v(140.75, 54.87) * mm});
            skLineSegment(sketch, "E6557", {"start": v(140.75, 54.87) * mm, "end": v(141.38, 53.23) * mm});
            skLineSegment(sketch, "E6558", {"start": v(141.38, 53.23) * mm, "end": v(142.07, 51.6) * mm});
            skLineSegment(sketch, "E6559", {"start": v(142.07, 51.6) * mm, "end": v(142.8, 49.99) * mm});
            skLineSegment(sketch, "E6560", {"start": v(142.8, 49.99) * mm, "end": v(143.6, 48.38) * mm});
            skLineSegment(sketch, "E6561", {"start": v(143.6, 48.38) * mm, "end": v(144.43, 46.79) * mm});
            skLineSegment(sketch, "E6562", {"start": v(144.43, 46.79) * mm, "end": v(145.33, 45.2) * mm});
            skLineSegment(sketch, "E6563", {"start": v(145.33, 45.2) * mm, "end": v(146.3, 43.63) * mm});
            skLineSegment(sketch, "E6564", {"start": v(146.3, 43.63) * mm, "end": v(147.31, 42.07) * mm});
            skLineSegment(sketch, "E6565", {"start": v(147.31, 42.07) * mm, "end": v(35.07, 42.07) * mm});
            skLineSegment(sketch, "E6566", {"start": v(35.07, 42.07) * mm, "end": v(35.93, 43.92) * mm});
            skLineSegment(sketch, "E6567", {"start": v(35.93, 43.92) * mm, "end": v(36.73, 45.73) * mm});
            skLineSegment(sketch, "E6568", {"start": v(36.73, 45.73) * mm, "end": v(37.47, 47.5) * mm});
            skLineSegment(sketch, "E6569", {"start": v(37.47, 47.5) * mm, "end": v(38.17, 49.25) * mm});
            skLineSegment(sketch, "E6570", {"start": v(38.17, 49.25) * mm, "end": v(38.81, 50.98) * mm});
            skLineSegment(sketch, "E6571", {"start": v(38.81, 50.98) * mm, "end": v(39.41, 52.67) * mm});
            skLineSegment(sketch, "E6572", {"start": v(39.41, 52.67) * mm, "end": v(39.96, 54.35) * mm});
            skLineSegment(sketch, "E6573", {"start": v(39.96, 54.35) * mm, "end": v(40.47, 56.01) * mm});
            skLineSegment(sketch, "E6574", {"start": v(40.47, 56.01) * mm, "end": v(40.93, 57.66) * mm});
            skLineSegment(sketch, "E6575", {"start": v(40.93, 57.66) * mm, "end": v(41.36, 59.3) * mm});
            skLineSegment(sketch, "E6576", {"start": v(41.36, 59.3) * mm, "end": v(41.74, 60.93) * mm});
            skLineSegment(sketch, "E6577", {"start": v(41.74, 60.93) * mm, "end": v(42.1, 62.56) * mm});
            skLineSegment(sketch, "E6578", {"start": v(42.1, 62.56) * mm, "end": v(42.4, 64.18) * mm});
            skLineSegment(sketch, "E6579", {"start": v(42.4, 64.18) * mm, "end": v(42.69, 65.82) * mm});
            skLineSegment(sketch, "E6580", {"start": v(42.69, 65.82) * mm, "end": v(42.94, 67.45) * mm});
            skLineSegment(sketch, "E6581", {"start": v(42.94, 67.45) * mm, "end": v(43.15, 69.1) * mm});
            skLineSegment(sketch, "E6582", {"start": v(43.15, 69.1) * mm, "end": v(43.35, 70.77) * mm});
            skLineSegment(sketch, "E6583", {"start": v(43.35, 70.77) * mm, "end": v(43.51, 72.45) * mm});
            skLineSegment(sketch, "E6584", {"start": v(43.51, 72.45) * mm, "end": v(43.65, 74.15) * mm});
            skLineSegment(sketch, "E6585", {"start": v(43.65, 74.15) * mm, "end": v(43.77, 75.87) * mm});
            skLineSegment(sketch, "E6586", {"start": v(43.77, 75.87) * mm, "end": v(43.87, 77.62) * mm});
            skLineSegment(sketch, "E6587", {"start": v(43.87, 77.62) * mm, "end": v(43.95, 79.4) * mm});
            skLineSegment(sketch, "E6588", {"start": v(43.95, 79.4) * mm, "end": v(44, 81.22) * mm});
            skLineSegment(sketch, "E6589", {"start": v(44, 81.22) * mm, "end": v(44.05, 83.08) * mm});
            skLineSegment(sketch, "E6590", {"start": v(44.05, 83.08) * mm, "end": v(44.09, 84.98) * mm});
            skLineSegment(sketch, "E6591", {"start": v(44.09, 84.98) * mm, "end": v(44.1, 86.92) * mm});
            skLineSegment(sketch, "E6592", {"start": v(44.1, 86.92) * mm, "end": v(44.12, 88.9) * mm});
            skLineSegment(sketch, "E6593", {"start": v(44.12, 88.9) * mm, "end": v(44.12, 90.94) * mm});
            skLineSegment(sketch, "E6594", {"start": v(44.12, 90.94) * mm, "end": v(44.12, 139.82) * mm});
            skLineSegment(sketch, "E6595", {"start": v(44.12, 139.82) * mm, "end": v(44.16, 141.4) * mm});
            skLineSegment(sketch, "E6596", {"start": v(44.16, 141.4) * mm, "end": v(44.24, 143.1) * mm});
            skLineSegment(sketch, "E6597", {"start": v(44.24, 143.1) * mm, "end": v(44.34, 144.9) * mm});
            skLineSegment(sketch, "E6598", {"start": v(44.34, 144.9) * mm, "end": v(44.42, 146.76) * mm});
            skLineSegment(sketch, "E6599", {"start": v(44.42, 146.76) * mm, "end": v(44.47, 148.65) * mm});
            skLineSegment(sketch, "E6600", {"start": v(44.47, 148.65) * mm, "end": v(44.45, 150.54) * mm});
            skLineSegment(sketch, "E6601", {"start": v(44.45, 150.54) * mm, "end": v(44.33, 152.39) * mm});
            skLineSegment(sketch, "E6602", {"start": v(44.33, 152.39) * mm, "end": v(44.08, 154.17) * mm});
            skLineSegment(sketch, "E6603", {"start": v(44.08, 154.17) * mm, "end": v(43.67, 155.86) * mm});
            skLineSegment(sketch, "E6604", {"start": v(43.67, 155.86) * mm, "end": v(43.07, 157.41) * mm});
            skLineSegment(sketch, "E6605", {"start": v(43.07, 157.41) * mm, "end": v(42.26, 158.8) * mm});
            skLineSegment(sketch, "E6606", {"start": v(42.26, 158.8) * mm, "end": v(41.12, 160.1) * mm});
            skLineSegment(sketch, "E6607", {"start": v(41.12, 160.1) * mm, "end": v(39.77, 161.13) * mm});
            skLineSegment(sketch, "E6608", {"start": v(39.77, 161.13) * mm, "end": v(38.25, 161.92) * mm});
            skLineSegment(sketch, "E6609", {"start": v(38.25, 161.92) * mm, "end": v(36.6, 162.5) * mm});
            skLineSegment(sketch, "E6610", {"start": v(36.6, 162.5) * mm, "end": v(34.85, 162.9) * mm});
            skLineSegment(sketch, "E6611", {"start": v(34.85, 162.9) * mm, "end": v(33.03, 163.16) * mm});
            skLineSegment(sketch, "E6612", {"start": v(33.03, 163.16) * mm, "end": v(31.18, 163.3) * mm});
            skLineSegment(sketch, "E6613", {"start": v(31.18, 163.3) * mm, "end": v(29.34, 163.37) * mm});
            skLineSegment(sketch, "E6614", {"start": v(29.34, 163.37) * mm, "end": v(27.54, 163.38) * mm});
            skLineSegment(sketch, "E6615", {"start": v(27.54, 163.38) * mm, "end": v(25.82, 163.36) * mm});
            skLineSegment(sketch, "E6616", {"start": v(25.82, 163.36) * mm, "end": v(24.2, 163.36) * mm});
            skLineSegment(sketch, "E6617", {"start": v(24.2, 163.36) * mm, "end": v(22.4, 163.36) * mm});
            skLineSegment(sketch, "E6618", {"start": v(22.4, 163.36) * mm, "end": v(20.59, 163.37) * mm});
            skLineSegment(sketch, "E6619", {"start": v(20.59, 163.37) * mm, "end": v(18.78, 163.38) * mm});
            skLineSegment(sketch, "E6620", {"start": v(18.78, 163.38) * mm, "end": v(16.97, 163.39) * mm});
            skLineSegment(sketch, "E6621", {"start": v(16.97, 163.39) * mm, "end": v(15.16, 163.4) * mm});
            skLineSegment(sketch, "E6622", {"start": v(15.16, 163.4) * mm, "end": v(13.35, 163.4) * mm});
            skLineSegment(sketch, "E6623", {"start": v(13.35, 163.4) * mm, "end": v(11.54, 163.4) * mm});
            skLineSegment(sketch, "E6624", {"start": v(11.54, 163.4) * mm, "end": v(9.73, 163.4) * mm});
            skLineSegment(sketch, "E6625", {"start": v(9.73, 163.4) * mm, "end": v(7.92, 163.4) * mm});
            skLineSegment(sketch, "E6626", {"start": v(7.92, 163.4) * mm, "end": v(6.1, 163.41) * mm});
            skLineSegment(sketch, "E6627", {"start": v(6.1, 163.41) * mm, "end": v(4.3, 163.41) * mm});
            skLineSegment(sketch, "E6628", {"start": v(4.3, 163.41) * mm, "end": v(2.49, 163.42) * mm});
            skLineSegment(sketch, "E6629", {"start": v(2.49, 163.42) * mm, "end": v(0.68, 163.42) * mm});
            skLineSegment(sketch, "E6630", {"start": v(0.68, 163.42) * mm, "end": v(-1.14, 163.42) * mm});
            skLineSegment(sketch, "E6631", {"start": v(-1.14, 163.42) * mm, "end": v(-2.95, 163.42) * mm});
            skLineSegment(sketch, "E6632", {"start": v(-2.95, 163.42) * mm, "end": v(-4.76, 163.41) * mm});
            skLineSegment(sketch, "E6633", {"start": v(-4.76, 163.41) * mm, "end": v(-6.57, 163.41) * mm});
            skLineSegment(sketch, "E6634", {"start": v(-6.57, 163.41) * mm, "end": v(-8.38, 163.4) * mm});
            skLineSegment(sketch, "E6635", {"start": v(-8.38, 163.4) * mm, "end": v(-10.19, 163.4) * mm});
            skLineSegment(sketch, "E6636", {"start": v(-10.19, 163.4) * mm, "end": v(-12, 163.4) * mm});
            skLineSegment(sketch, "E6637", {"start": v(-12, 163.4) * mm, "end": v(-13.8, 163.4) * mm});
            skLineSegment(sketch, "E6638", {"start": v(-13.8, 163.4) * mm, "end": v(-15.62, 163.4) * mm});
            skLineSegment(sketch, "E6639", {"start": v(-15.62, 163.4) * mm, "end": v(-17.43, 163.39) * mm});
            skLineSegment(sketch, "E6640", {"start": v(-17.43, 163.39) * mm, "end": v(-19.24, 163.38) * mm});
            skLineSegment(sketch, "E6641", {"start": v(-19.24, 163.38) * mm, "end": v(-21.05, 163.37) * mm});
            skLineSegment(sketch, "E6642", {"start": v(-21.05, 163.37) * mm, "end": v(-22.86, 163.36) * mm});
            skLineSegment(sketch, "E6643", {"start": v(-22.86, 163.36) * mm, "end": v(-24.67, 163.36) * mm});
            skLineSegment(sketch, "E6644", {"start": v(-24.67, 163.36) * mm, "end": v(-26.28, 163.36) * mm});
            skLineSegment(sketch, "E6645", {"start": v(-26.28, 163.36) * mm, "end": v(-28, 163.38) * mm});
            skLineSegment(sketch, "E6646", {"start": v(-28, 163.38) * mm, "end": v(-29.8, 163.37) * mm});
            skLineSegment(sketch, "E6647", {"start": v(-29.8, 163.37) * mm, "end": v(-31.65, 163.3) * mm});
            skLineSegment(sketch, "E6648", {"start": v(-31.65, 163.3) * mm, "end": v(-33.5, 163.16) * mm});
            skLineSegment(sketch, "E6649", {"start": v(-33.5, 163.16) * mm, "end": v(-35.3, 162.9) * mm});
            skLineSegment(sketch, "E6650", {"start": v(-35.3, 162.9) * mm, "end": v(-37.06, 162.5) * mm});
            skLineSegment(sketch, "E6651", {"start": v(-37.06, 162.5) * mm, "end": v(-38.71, 161.92) * mm});
            skLineSegment(sketch, "E6652", {"start": v(-38.71, 161.92) * mm, "end": v(-40.23, 161.13) * mm});
            skLineSegment(sketch, "E6653", {"start": v(-40.23, 161.13) * mm, "end": v(-41.58, 160.1) * mm});
            skLineSegment(sketch, "E6654", {"start": v(-41.58, 160.1) * mm, "end": v(-42.72, 158.8) * mm});
            skLineSegment(sketch, "E6655", {"start": v(-42.72, 158.8) * mm, "end": v(-43.49, 157.54) * mm});
            skLineSegment(sketch, "E6656", {"start": v(-43.49, 157.54) * mm, "end": v(-44.1, 156.12) * mm});
            skLineSegment(sketch, "E6657", {"start": v(-44.1, 156.12) * mm, "end": v(-44.59, 154.55) * mm});
            skLineSegment(sketch, "E6658", {"start": v(-44.59, 154.55) * mm, "end": v(-44.95, 152.87) * mm});
            skLineSegment(sketch, "E6659", {"start": v(-44.95, 152.87) * mm, "end": v(-45.2, 151.09) * mm});
            skLineSegment(sketch, "E6660", {"start": v(-45.2, 151.09) * mm, "end": v(-45.37, 149.22) * mm});
            skLineSegment(sketch, "E6661", {"start": v(-45.37, 149.22) * mm, "end": v(-45.45, 147.3) * mm});
            skLineSegment(sketch, "E6662", {"start": v(-45.45, 147.3) * mm, "end": v(-45.46, 145.32) * mm});
            skLineSegment(sketch, "E6663", {"start": v(-45.46, 145.32) * mm, "end": v(-45.41, 143.33) * mm});
            skLineSegment(sketch, "E6664", {"start": v(-45.41, 143.33) * mm, "end": v(-45.32, 141.34) * mm});
            skLineSegment(sketch, "E6665", {"start": v(-45.32, 141.34) * mm, "end": v(-45.2, 139.36) * mm});
            skLineSegment(sketch, "E6666", {"start": v(-45.2, 139.36) * mm, "end": v(-45.07, 137.42) * mm});
            skLineSegment(sketch, "E6667", {"start": v(-45.07, 137.42) * mm, "end": v(-44.93, 135.54) * mm});
            skLineSegment(sketch, "E6668", {"start": v(-44.93, 135.54) * mm, "end": v(-44.8, 133.73) * mm});
            skLineSegment(sketch, "E6669", {"start": v(-44.8, 133.73) * mm, "end": v(-44.69, 132.02) * mm});
            skLineSegment(sketch, "E6670", {"start": v(-44.69, 132.02) * mm, "end": v(-44.61, 130.42) * mm});
            skLineSegment(sketch, "E6671", {"start": v(-44.61, 130.42) * mm, "end": v(-44.58, 128.96) * mm});
            skLineSegment(sketch, "E6672", {"start": v(-44.58, 128.96) * mm, "end": v(-44.6, 127.38) * mm});
            skLineSegment(sketch, "E6673", {"start": v(-44.6, 127.38) * mm, "end": v(-44.62, 125.78) * mm});
            skLineSegment(sketch, "E6674", {"start": v(-44.62, 125.78) * mm, "end": v(-44.65, 124.15) * mm});
            skLineSegment(sketch, "E6675", {"start": v(-44.65, 124.15) * mm, "end": v(-44.7, 122.5) * mm});
            skLineSegment(sketch, "E6676", {"start": v(-44.7, 122.5) * mm, "end": v(-44.77, 120.85) * mm});
            skLineSegment(sketch, "E6677", {"start": v(-44.77, 120.85) * mm, "end": v(-44.84, 119.16) * mm});
            skLineSegment(sketch, "E6678", {"start": v(-44.84, 119.16) * mm, "end": v(-44.92, 117.46) * mm});
            skLineSegment(sketch, "E6679", {"start": v(-44.92, 117.46) * mm, "end": v(-45, 115.75) * mm});
            skLineSegment(sketch, "E6680", {"start": v(-45, 115.75) * mm, "end": v(-45.1, 114.02) * mm});
            skLineSegment(sketch, "E6681", {"start": v(-45.1, 114.02) * mm, "end": v(-45.2, 112.28) * mm});
            skLineSegment(sketch, "E6682", {"start": v(-45.2, 112.28) * mm, "end": v(-45.3, 110.52) * mm});
            skLineSegment(sketch, "E6683", {"start": v(-45.3, 110.52) * mm, "end": v(-45.39, 108.76) * mm});
            skLineSegment(sketch, "E6684", {"start": v(-45.39, 108.76) * mm, "end": v(-45.49, 106.98) * mm});
            skLineSegment(sketch, "E6685", {"start": v(-45.49, 106.98) * mm, "end": v(-45.59, 105.2) * mm});
            skLineSegment(sketch, "E6686", {"start": v(-45.59, 105.2) * mm, "end": v(-45.68, 103.4) * mm});
            skLineSegment(sketch, "E6687", {"start": v(-45.68, 103.4) * mm, "end": v(-45.77, 101.6) * mm});
            skLineSegment(sketch, "E6688", {"start": v(-45.77, 101.6) * mm, "end": v(-45.85, 99.8) * mm});
            skLineSegment(sketch, "E6689", {"start": v(-45.85, 99.8) * mm, "end": v(-45.93, 97.99) * mm});
            skLineSegment(sketch, "E6690", {"start": v(-45.93, 97.99) * mm, "end": v(-46, 96.17) * mm});
            skLineSegment(sketch, "E6691", {"start": v(-46, 96.17) * mm, "end": v(-46.05, 94.36) * mm});
            skLineSegment(sketch, "E6692", {"start": v(-46.05, 94.36) * mm, "end": v(-46.1, 92.54) * mm});
            skLineSegment(sketch, "E6693", {"start": v(-46.1, 92.54) * mm, "end": v(-46.13, 90.73) * mm});
            skLineSegment(sketch, "E6694", {"start": v(-46.13, 90.73) * mm, "end": v(-46.15, 88.91) * mm});
            skLineSegment(sketch, "E6695", {"start": v(-46.15, 88.91) * mm, "end": v(-46.15, 87.1) * mm});
            skLineSegment(sketch, "E6696", {"start": v(-46.15, 87.1) * mm, "end": v(-46.13, 85.3) * mm});
            skLineSegment(sketch, "E6697", {"start": v(-46.13, 85.3) * mm, "end": v(-46.1, 83.5) * mm});
            skLineSegment(sketch, "E6698", {"start": v(-46.1, 83.5) * mm, "end": v(-46.04, 81.7) * mm});
            skLineSegment(sketch, "E6699", {"start": v(-46.04, 81.7) * mm, "end": v(-45.96, 79.9) * mm});
            skLineSegment(sketch, "E6700", {"start": v(-45.96, 79.9) * mm, "end": v(-45.86, 78.12) * mm});
            skLineSegment(sketch, "E6701", {"start": v(-45.86, 78.12) * mm, "end": v(-45.73, 76.35) * mm});
            skLineSegment(sketch, "E6702", {"start": v(-45.73, 76.35) * mm, "end": v(-45.58, 74.59) * mm});
            skLineSegment(sketch, "E6703", {"start": v(-45.58, 74.59) * mm, "end": v(-45.4, 72.84) * mm});
            skLineSegment(sketch, "E6704", {"start": v(-45.4, 72.84) * mm, "end": v(-45.18, 71.1) * mm});
            skLineSegment(sketch, "E6705", {"start": v(-45.18, 71.1) * mm, "end": v(-44.94, 69.38) * mm});
            skLineSegment(sketch, "E6706", {"start": v(-44.94, 69.38) * mm, "end": v(-44.67, 67.67) * mm});
            skLineSegment(sketch, "E6707", {"start": v(-44.67, 67.67) * mm, "end": v(-44.36, 65.98) * mm});
            skLineSegment(sketch, "E6708", {"start": v(-44.36, 65.98) * mm, "end": v(-44.02, 64.3) * mm});
            skLineSegment(sketch, "E6709", {"start": v(-44.02, 64.3) * mm, "end": v(-43.64, 62.65) * mm});
            skLineSegment(sketch, "E6710", {"start": v(-43.64, 62.65) * mm, "end": v(-43.23, 61.01) * mm});
            skLineSegment(sketch, "E6711", {"start": v(-43.23, 61.01) * mm, "end": v(-42.77, 59.4) * mm});
            skLineSegment(sketch, "E6712", {"start": v(-42.77, 59.4) * mm, "end": v(-42.28, 57.8) * mm});
            skLineSegment(sketch, "E6713", {"start": v(-42.28, 57.8) * mm, "end": v(-41.74, 56.24) * mm});
            skLineSegment(sketch, "E6714", {"start": v(-41.74, 56.24) * mm, "end": v(-41.16, 54.7) * mm});
            skLineSegment(sketch, "E6715", {"start": v(-41.16, 54.7) * mm, "end": v(-40.53, 53.17) * mm});
            skLineSegment(sketch, "E6716", {"start": v(-40.53, 53.17) * mm, "end": v(-39.86, 51.68) * mm});
            skLineSegment(sketch, "E6717", {"start": v(-39.86, 51.68) * mm, "end": v(-39.14, 50.21) * mm});
            skLineSegment(sketch, "E6718", {"start": v(-39.14, 50.21) * mm, "end": v(-38.37, 48.78) * mm});
            skLineSegment(sketch, "E6719", {"start": v(-38.37, 48.78) * mm, "end": v(-37.54, 47.37) * mm});
            skLineSegment(sketch, "E6720", {"start": v(-37.54, 47.37) * mm, "end": v(-36.67, 46) * mm});
            skLineSegment(sketch, "E6721", {"start": v(-36.67, 46) * mm, "end": v(-35.74, 44.65) * mm});
            skLineSegment(sketch, "E6722", {"start": v(-35.74, 44.65) * mm, "end": v(-34.76, 43.34) * mm});
            skLineSegment(sketch, "E6723", {"start": v(-34.76, 43.34) * mm, "end": v(-33.72, 42.07) * mm});
            skLineSegment(sketch, "E6724", {"start": v(-33.72, 42.07) * mm, "end": v(-145.96, 42.07) * mm});
            skLineSegment(sketch, "E6725", {"start": v(-145.96, 42.07) * mm, "end": v(-145.07, 43.7) * mm});
            skLineSegment(sketch, "E6726", {"start": v(-145.07, 43.7) * mm, "end": v(-144.23, 45.35) * mm});
            skLineSegment(sketch, "E6727", {"start": v(-144.23, 45.35) * mm, "end": v(-143.43, 47) * mm});
            skLineSegment(sketch, "E6728", {"start": v(-143.43, 47) * mm, "end": v(-142.68, 48.64) * mm});
            skLineSegment(sketch, "E6729", {"start": v(-142.68, 48.64) * mm, "end": v(-141.97, 50.3) * mm});
            skLineSegment(sketch, "E6730", {"start": v(-141.97, 50.3) * mm, "end": v(-141.3, 51.95) * mm});
            skLineSegment(sketch, "E6731", {"start": v(-141.3, 51.95) * mm, "end": v(-140.67, 53.62) * mm});
            skLineSegment(sketch, "E6732", {"start": v(-140.67, 53.62) * mm, "end": v(-140.08, 55.28) * mm});
            skLineSegment(sketch, "E6733", {"start": v(-140.08, 55.28) * mm, "end": v(-139.53, 56.95) * mm});
            skLineSegment(sketch, "E6734", {"start": v(-139.53, 56.95) * mm, "end": v(-139.02, 58.62) * mm});
            skLineSegment(sketch, "E6735", {"start": v(-139.02, 58.62) * mm, "end": v(-138.54, 60.3) * mm});
            skLineSegment(sketch, "E6736", {"start": v(-138.54, 60.3) * mm, "end": v(-138.1, 61.98) * mm});
            skLineSegment(sketch, "E6737", {"start": v(-138.1, 61.98) * mm, "end": v(-137.68, 63.66) * mm});
            skLineSegment(sketch, "E6738", {"start": v(-137.68, 63.66) * mm, "end": v(-137.3, 65.35) * mm});
            skLineSegment(sketch, "E6739", {"start": v(-137.3, 65.35) * mm, "end": v(-136.95, 67.04) * mm});
            skLineSegment(sketch, "E6740", {"start": v(-136.95, 67.04) * mm, "end": v(-136.63, 68.74) * mm});
            skLineSegment(sketch, "E6741", {"start": v(-136.63, 68.74) * mm, "end": v(-136.34, 70.44) * mm});
            skLineSegment(sketch, "E6742", {"start": v(-136.34, 70.44) * mm, "end": v(-136.08, 72.14) * mm});
            skLineSegment(sketch, "E6743", {"start": v(-136.08, 72.14) * mm, "end": v(-135.84, 73.85) * mm});
            skLineSegment(sketch, "E6744", {"start": v(-135.84, 73.85) * mm, "end": v(-135.63, 75.56) * mm});
            skLineSegment(sketch, "E6745", {"start": v(-135.63, 75.56) * mm, "end": v(-135.44, 77.28) * mm});
            skLineSegment(sketch, "E6746", {"start": v(-135.44, 77.28) * mm, "end": v(-135.27, 79) * mm});
            skLineSegment(sketch, "E6747", {"start": v(-135.27, 79) * mm, "end": v(-135.13, 80.72) * mm});
            skLineSegment(sketch, "E6748", {"start": v(-135.13, 80.72) * mm, "end": v(-135, 82.45) * mm});
            skLineSegment(sketch, "E6749", {"start": v(-135, 82.45) * mm, "end": v(-134.9, 84.18) * mm});
            skLineSegment(sketch, "E6750", {"start": v(-134.9, 84.18) * mm, "end": v(-134.81, 85.92) * mm});
            skLineSegment(sketch, "E6751", {"start": v(-134.81, 85.92) * mm, "end": v(-134.74, 87.66) * mm});
            skLineSegment(sketch, "E6752", {"start": v(-134.74, 87.66) * mm, "end": v(-134.69, 89.41) * mm});
            skLineSegment(sketch, "E6753", {"start": v(-134.69, 89.41) * mm, "end": v(-134.65, 91.16) * mm});
            skLineSegment(sketch, "E6754", {"start": v(-134.65, 91.16) * mm, "end": v(-134.62, 92.92) * mm});
            skLineSegment(sketch, "E6755", {"start": v(-134.62, 92.92) * mm, "end": v(-134.6, 94.68) * mm});
            skLineSegment(sketch, "E6756", {"start": v(-134.6, 94.68) * mm, "end": v(-134.6, 96.44) * mm});
            skLineSegment(sketch, "E6757", {"start": v(-134.6, 96.44) * mm, "end": v(-134.61, 98.2) * mm});
            skLineSegment(sketch, "E6758", {"start": v(-134.61, 98.2) * mm, "end": v(-134.63, 99.98) * mm});
            skLineSegment(sketch, "E6759", {"start": v(-134.63, 99.98) * mm, "end": v(-134.65, 101.76) * mm});
            skLineSegment(sketch, "E6760", {"start": v(-134.65, 101.76) * mm, "end": v(-134.68, 103.54) * mm});
            skLineSegment(sketch, "E6761", {"start": v(-134.68, 103.54) * mm, "end": v(-134.71, 105.33) * mm});
            skLineSegment(sketch, "E6762", {"start": v(-134.71, 105.33) * mm, "end": v(-134.75, 107.12) * mm});
            skLineSegment(sketch, "E6763", {"start": v(-134.75, 107.12) * mm, "end": v(-134.8, 108.92) * mm});
            skLineSegment(sketch, "E6764", {"start": v(-134.8, 108.92) * mm, "end": v(-134.83, 110.72) * mm});
            skLineSegment(sketch, "E6765", {"start": v(-134.83, 110.72) * mm, "end": v(-134.88, 112.53) * mm});
            skLineSegment(sketch, "E6766", {"start": v(-134.88, 112.53) * mm, "end": v(-134.92, 114.34) * mm});
            skLineSegment(sketch, "E6767", {"start": v(-134.92, 114.34) * mm, "end": v(-134.96, 116.15) * mm});
            skLineSegment(sketch, "E6768", {"start": v(-134.96, 116.15) * mm, "end": v(-135, 117.97) * mm});
            skLineSegment(sketch, "E6769", {"start": v(-135, 117.97) * mm, "end": v(-135.03, 119.8) * mm});
            skLineSegment(sketch, "E6770", {"start": v(-135.03, 119.8) * mm, "end": v(-135.06, 121.63) * mm});
            skLineSegment(sketch, "E6771", {"start": v(-135.06, 121.63) * mm, "end": v(-135.08, 123.47) * mm});
            skLineSegment(sketch, "E6772", {"start": v(-135.08, 123.47) * mm, "end": v(-135.1, 125.3) * mm});
            skLineSegment(sketch, "E6773", {"start": v(-135.1, 125.3) * mm, "end": v(-135.1, 127.15) * mm});
            skLineSegment(sketch, "E6774", {"start": v(-135.1, 127.15) * mm, "end": v(-135.1, 246.63) * mm});
            skLineSegment(sketch, "E6775", {"start": v(-135.1, 246.63) * mm, "end": v(-135.09, 248.3) * mm});
            skLineSegment(sketch, "E6776", {"start": v(-135.09, 248.3) * mm, "end": v(-135.06, 250.02) * mm});
            skLineSegment(sketch, "E6777", {"start": v(-135.06, 250.02) * mm, "end": v(-135, 251.75) * mm});
            skLineSegment(sketch, "E6778", {"start": v(-135, 251.75) * mm, "end": v(-134.93, 253.51) * mm});
            skLineSegment(sketch, "E6779", {"start": v(-134.93, 253.51) * mm, "end": v(-134.85, 255.3) * mm});
            skLineSegment(sketch, "E6780", {"start": v(-134.85, 255.3) * mm, "end": v(-134.76, 257.1) * mm});
            skLineSegment(sketch, "E6781", {"start": v(-134.76, 257.1) * mm, "end": v(-134.66, 258.93) * mm});
            skLineSegment(sketch, "E6782", {"start": v(-134.66, 258.93) * mm, "end": v(-134.55, 260.78) * mm});
            skLineSegment(sketch, "E6783", {"start": v(-134.55, 260.78) * mm, "end": v(-134.43, 262.64) * mm});
            skLineSegment(sketch, "E6784", {"start": v(-134.43, 262.64) * mm, "end": v(-134.32, 264.5) * mm});
            skLineSegment(sketch, "E6785", {"start": v(-134.32, 264.5) * mm, "end": v(-134.2, 266.4) * mm});
            skLineSegment(sketch, "E6786", {"start": v(-134.2, 266.4) * mm, "end": v(-134.1, 268.28) * mm});
            skLineSegment(sketch, "E6787", {"start": v(-134.1, 268.28) * mm, "end": v(-134, 270.18) * mm});
            skLineSegment(sketch, "E6788", {"start": v(-134, 270.18) * mm, "end": v(-133.9, 272.08) * mm});
            skLineSegment(sketch, "E6789", {"start": v(-133.9, 272.08) * mm, "end": v(-133.82, 273.98) * mm});
            skLineSegment(sketch, "E6790", {"start": v(-133.82, 273.98) * mm, "end": v(-133.75, 275.88) * mm});
            skLineSegment(sketch, "E6791", {"start": v(-133.75, 275.88) * mm, "end": v(-133.7, 277.78) * mm});
            skLineSegment(sketch, "E6792", {"start": v(-133.7, 277.78) * mm, "end": v(-133.66, 279.67) * mm});
            skLineSegment(sketch, "E6793", {"start": v(-133.66, 279.67) * mm, "end": v(-133.64, 281.56) * mm});
            skLineSegment(sketch, "E6794", {"start": v(-133.64, 281.56) * mm, "end": v(-133.65, 283.43) * mm});
            skLineSegment(sketch, "E6795", {"start": v(-133.65, 283.43) * mm, "end": v(-133.69, 285.3) * mm});
            skLineSegment(sketch, "E6796", {"start": v(-133.69, 285.3) * mm, "end": v(-133.75, 287.14) * mm});
            skLineSegment(sketch, "E6797", {"start": v(-133.75, 287.14) * mm, "end": v(-133.84, 288.97) * mm});
            skLineSegment(sketch, "E6798", {"start": v(-133.84, 288.97) * mm, "end": v(-133.97, 290.79) * mm});
            skLineSegment(sketch, "E6799", {"start": v(-133.97, 290.79) * mm, "end": v(-134.14, 292.58) * mm});
            skLineSegment(sketch, "E6800", {"start": v(-134.14, 292.58) * mm, "end": v(-134.34, 294.35) * mm});
            skLineSegment(sketch, "E6801", {"start": v(-134.34, 294.35) * mm, "end": v(-134.58, 296.09) * mm});
            skLineSegment(sketch, "E6802", {"start": v(-134.58, 296.09) * mm, "end": v(-134.87, 297.8) * mm});
            skLineSegment(sketch, "E6803", {"start": v(-134.87, 297.8) * mm, "end": v(-135.2, 299.49) * mm});
            skLineSegment(sketch, "E6804", {"start": v(-135.2, 299.49) * mm, "end": v(-135.59, 301.14) * mm});
            skLineSegment(sketch, "E6805", {"start": v(-135.59, 301.14) * mm, "end": v(-136.02, 302.75) * mm});
            skLineSegment(sketch, "E6806", {"start": v(-136.02, 302.75) * mm, "end": v(-136.6, 304.5) * mm});
            skLineSegment(sketch, "E6807", {"start": v(-136.6, 304.5) * mm, "end": v(-137.29, 306.22) * mm});
            skLineSegment(sketch, "E6808", {"start": v(-137.29, 306.22) * mm, "end": v(-138.07, 307.89) * mm});
            skLineSegment(sketch, "E6809", {"start": v(-138.07, 307.89) * mm, "end": v(-138.93, 309.54) * mm});
            skLineSegment(sketch, "E6810", {"start": v(-138.93, 309.54) * mm, "end": v(-139.83, 311.16) * mm});
            skLineSegment(sketch, "E6811", {"start": v(-139.83, 311.16) * mm, "end": v(-140.77, 312.78) * mm});
            skLineSegment(sketch, "E6812", {"start": v(-140.77, 312.78) * mm, "end": v(-141.73, 314.39) * mm});
            skLineSegment(sketch, "E6813", {"start": v(-141.73, 314.39) * mm, "end": v(-142.67, 316) * mm});
            skLineSegment(sketch, "E6814", {"start": v(-142.67, 316) * mm, "end": v(-143.59, 317.63) * mm});
            skLineSegment(sketch, "E6815", {"start": v(-143.59, 317.63) * mm, "end": v(-144.45, 319.28) * mm});
            skLineSegment(sketch, "E6816", {"start": v(-144.45, 319.28) * mm, "end": v(-145.25, 320.95) * mm});
            skLineSegment(sketch, "E6817", {"start": v(-145.25, 320.95) * mm, "end": v(-145.96, 322.67) * mm});
            skLineSegment(sketch, "E6818", {"start": v(-145.96, 322.67) * mm, "end": v(-144.46, 322.64) * mm});
            skLineSegment(sketch, "E6819", {"start": v(-144.46, 322.64) * mm, "end": v(-142.83, 322.56) * mm});
            skLineSegment(sketch, "E6820", {"start": v(-142.83, 322.56) * mm, "end": v(-141.09, 322.45) * mm});
            skLineSegment(sketch, "E6821", {"start": v(-141.09, 322.45) * mm, "end": v(-139.26, 322.33) * mm});
            skLineSegment(sketch, "E6822", {"start": v(-139.26, 322.33) * mm, "end": v(-137.37, 322.22) * mm});
            skLineSegment(sketch, "E6823", {"start": v(-137.37, 322.22) * mm, "end": v(-135.44, 322.13) * mm});
            skLineSegment(sketch, "E6824", {"start": v(-135.44, 322.13) * mm, "end": v(-133.5, 322.09) * mm});
            skLineSegment(sketch, "E6825", {"start": v(-133.5, 322.09) * mm, "end": v(-131.56, 322.1) * mm});
            skLineSegment(sketch, "E6826", {"start": v(-131.56, 322.1) * mm, "end": v(-129.66, 322.2) * mm});
            skLineSegment(sketch, "E6827", {"start": v(-129.66, 322.2) * mm, "end": v(-127.82, 322.41) * mm});
            skLineSegment(sketch, "E6828", {"start": v(-127.82, 322.41) * mm, "end": v(-126.05, 322.73) * mm});
            skLineSegment(sketch, "E6829", {"start": v(-126.05, 322.73) * mm, "end": v(-124.4, 323.19) * mm});
            skLineSegment(sketch, "E6830", {"start": v(-124.4, 323.19) * mm, "end": v(-122.87, 323.8) * mm});
            skLineSegment(sketch, "E6831", {"start": v(-122.87, 323.8) * mm, "end": v(-121.49, 324.59) * mm});
            skLineSegment(sketch, "E6832", {"start": v(-121.49, 324.59) * mm, "end": v(-120.29, 325.57) * mm});
            skLineSegment(sketch, "E6833", {"start": v(-120.29, 325.57) * mm, "end": v(-119.2, 326.73) * mm});
            skLineSegment(sketch, "E6834", {"start": v(-119.2, 326.73) * mm, "end": v(-118.17, 328.02) * mm});
            skLineSegment(sketch, "E6835", {"start": v(-118.17, 328.02) * mm, "end": v(-117.2, 329.42) * mm});
            skLineSegment(sketch, "E6836", {"start": v(-117.2, 329.42) * mm, "end": v(-116.28, 330.92) * mm});
            skLineSegment(sketch, "E6837", {"start": v(-116.28, 330.92) * mm, "end": v(-115.4, 332.51) * mm});
            skLineSegment(sketch, "E6838", {"start": v(-115.4, 332.51) * mm, "end": v(-114.58, 334.18) * mm});
            skLineSegment(sketch, "E6839", {"start": v(-114.58, 334.18) * mm, "end": v(-113.8, 335.9) * mm});
            skLineSegment(sketch, "E6840", {"start": v(-113.8, 335.9) * mm, "end": v(-113.06, 337.7) * mm});
            skLineSegment(sketch, "E6841", {"start": v(-113.06, 337.7) * mm, "end": v(-112.35, 339.51) * mm});
            skLineSegment(sketch, "E6842", {"start": v(-112.35, 339.51) * mm, "end": v(-111.67, 341.37) * mm});
            skLineSegment(sketch, "E6843", {"start": v(-111.67, 341.37) * mm, "end": v(-111.02, 343.24) * mm});
            skLineSegment(sketch, "E6844", {"start": v(-111.02, 343.24) * mm, "end": v(-110.39, 345.11) * mm});
            skLineSegment(sketch, "E6845", {"start": v(-110.39, 345.11) * mm, "end": v(-109.78, 346.98) * mm});
            skLineSegment(sketch, "E6846", {"start": v(-109.78, 346.98) * mm, "end": v(-109.19, 348.83) * mm});
            skLineSegment(sketch, "E6847", {"start": v(-109.19, 348.83) * mm, "end": v(-108.61, 350.65) * mm});
            skLineSegment(sketch, "E6848", {"start": v(-108.61, 350.65) * mm, "end": v(-108.04, 352.42) * mm});
            skLineSegment(sketch, "E6849", {"start": v(-108.04, 352.42) * mm, "end": v(-107.47, 354.15) * mm});
            skLineSegment(sketch, "E6850", {"start": v(-107.47, 354.15) * mm, "end": v(-106.91, 355.8) * mm});
            skLineSegment(sketch, "E6851", {"start": v(-106.91, 355.8) * mm, "end": v(-106.34, 357.38) * mm});
            skLineSegment(sketch, "E6852", {"start": v(-106.34, 357.38) * mm, "end": v(-105.77, 358.87) * mm});
            skLineSegment(sketch, "E6853", {"start": v(-105.77, 358.87) * mm, "end": v(-105.1, 360.56) * mm});
            skLineSegment(sketch, "E6854", {"start": v(-105.1, 360.56) * mm, "end": v(-104.41, 362.25) * mm});
            skLineSegment(sketch, "E6855", {"start": v(-104.41, 362.25) * mm, "end": v(-103.73, 363.94) * mm});
            skLineSegment(sketch, "E6856", {"start": v(-103.73, 363.94) * mm, "end": v(-103.05, 365.62) * mm});
            skLineSegment(sketch, "E6857", {"start": v(-103.05, 365.62) * mm, "end": v(-102.36, 367.31) * mm});
            skLineSegment(sketch, "E6858", {"start": v(-102.36, 367.31) * mm, "end": v(-101.67, 369) * mm});
            skLineSegment(sketch, "E6859", {"start": v(-101.67, 369) * mm, "end": v(-100.97, 370.69) * mm});
            skLineSegment(sketch, "E6860", {"start": v(-100.97, 370.69) * mm, "end": v(-100.28, 372.37) * mm});
            skLineSegment(sketch, "E6861", {"start": v(-100.28, 372.37) * mm, "end": v(-99.58, 374.06) * mm});
            skLineSegment(sketch, "E6862", {"start": v(-99.58, 374.06) * mm, "end": v(-98.88, 375.75) * mm});
            skLineSegment(sketch, "E6863", {"start": v(-98.88, 375.75) * mm, "end": v(-98.18, 377.43) * mm});
            skLineSegment(sketch, "E6864", {"start": v(-98.18, 377.43) * mm, "end": v(-97.48, 379.12) * mm});
            skLineSegment(sketch, "E6865", {"start": v(-97.48, 379.12) * mm, "end": v(-96.78, 380.8) * mm});
            skLineSegment(sketch, "E6866", {"start": v(-96.78, 380.8) * mm, "end": v(-96.08, 382.5) * mm});
            skLineSegment(sketch, "E6867", {"start": v(-96.08, 382.5) * mm, "end": v(-95.38, 384.18) * mm});
            skLineSegment(sketch, "E6868", {"start": v(-95.38, 384.18) * mm, "end": v(-94.68, 385.87) * mm});
            skLineSegment(sketch, "E6869", {"start": v(-94.68, 385.87) * mm, "end": v(-93.97, 387.56) * mm});
            skLineSegment(sketch, "E6870", {"start": v(-93.97, 387.56) * mm, "end": v(-93.27, 389.25) * mm});
            skLineSegment(sketch, "E6871", {"start": v(-93.27, 389.25) * mm, "end": v(-92.57, 390.94) * mm});
            skLineSegment(sketch, "E6872", {"start": v(-92.57, 390.94) * mm, "end": v(-91.87, 392.63) * mm});
            skLineSegment(sketch, "E6873", {"start": v(-91.87, 392.63) * mm, "end": v(-91.17, 394.32) * mm});
            skLineSegment(sketch, "E6874", {"start": v(-91.17, 394.32) * mm, "end": v(-90.48, 396) * mm});
            skLineSegment(sketch, "E6875", {"start": v(-90.48, 396) * mm, "end": v(-89.78, 397.7) * mm});
            skLineSegment(sketch, "E6876", {"start": v(-89.78, 397.7) * mm, "end": v(-89.09, 399.4) * mm});
            skLineSegment(sketch, "E6877", {"start": v(-89.09, 399.4) * mm, "end": v(-88.4, 401.08) * mm});
            skLineSegment(sketch, "E6878", {"start": v(-88.4, 401.08) * mm, "end": v(-87.7, 402.78) * mm});
            skLineSegment(sketch, "E6879", {"start": v(-87.7, 402.78) * mm, "end": v(-87.02, 404.47) * mm});
            skLineSegment(sketch, "E6880", {"start": v(-87.02, 404.47) * mm, "end": v(-86.33, 406.17) * mm});
            skLineSegment(sketch, "E6881", {"start": v(-86.33, 406.17) * mm, "end": v(-85.65, 407.87) * mm});
            skLineSegment(sketch, "E6882", {"start": v(-85.65, 407.87) * mm, "end": v(-84.97, 409.56) * mm});
            skLineSegment(sketch, "E6883", {"start": v(-84.97, 409.56) * mm, "end": v(-84.3, 411.26) * mm});
            skLineSegment(sketch, "E6884", {"start": v(-84.3, 411.26) * mm, "end": v(-83.62, 412.96) * mm});
            skLineSegment(sketch, "E6885", {"start": v(-83.62, 412.96) * mm, "end": v(-82.96, 414.66) * mm});
            skLineSegment(sketch, "E6886", {"start": v(-82.96, 414.66) * mm, "end": v(-82.3, 416.36) * mm});
            skLineSegment(sketch, "E6887", {"start": v(-82.3, 416.36) * mm, "end": v(-81.63, 418.07) * mm});
            skLineSegment(sketch, "E6888", {"start": v(-81.63, 418.07) * mm, "end": v(-80.98, 419.77) * mm});
            skLineSegment(sketch, "E6889", {"start": v(-80.98, 419.77) * mm, "end": v(-80.33, 421.48) * mm});
            skLineSegment(sketch, "E6890", {"start": v(-80.33, 421.48) * mm, "end": v(-79.68, 423.18) * mm});
            skLineSegment(sketch, "E6891", {"start": v(-79.68, 423.18) * mm, "end": v(-79.04, 424.9) * mm});
            skLineSegment(sketch, "E6892", {"start": v(-79.04, 424.9) * mm, "end": v(-78.4, 426.6) * mm});
            skLineSegment(sketch, "E6893", {"start": v(-78.4, 426.6) * mm, "end": v(-77.78, 428.31) * mm});
            skLineSegment(sketch, "E6894", {"start": v(-77.78, 428.31) * mm, "end": v(-77.16, 430.03) * mm});
            skLineSegment(sketch, "E6895", {"start": v(-77.16, 430.03) * mm, "end": v(-76.54, 431.74) * mm});
            skLineSegment(sketch, "E6896", {"start": v(-76.54, 431.74) * mm, "end": v(-75.93, 433.46) * mm});
            skLineSegment(sketch, "E6897", {"start": v(-75.93, 433.46) * mm, "end": v(-75.33, 435.17) * mm});
            skLineSegment(sketch, "E6898", {"start": v(-75.33, 435.17) * mm, "end": v(-74.73, 436.9) * mm});
            skLineSegment(sketch, "E6899", {"start": v(-74.73, 436.9) * mm, "end": v(-74.14, 438.61) * mm});
            skLineSegment(sketch, "E6900", {"start": v(-74.14, 438.61) * mm, "end": v(-73.56, 440.34) * mm});
            skLineSegment(sketch, "E6901", {"start": v(-73.56, 440.34) * mm, "end": v(-73.01, 442) * mm});
            skLineSegment(sketch, "E6902", {"start": v(-73.01, 442) * mm, "end": v(-72.5, 443.68) * mm});
            skLineSegment(sketch, "E6903", {"start": v(-72.5, 443.68) * mm, "end": v(-72.03, 445.37) * mm});
            skLineSegment(sketch, "E6904", {"start": v(-72.03, 445.37) * mm, "end": v(-71.59, 447.08) * mm});
            skLineSegment(sketch, "E6905", {"start": v(-71.59, 447.08) * mm, "end": v(-71.2, 448.8) * mm});
            skLineSegment(sketch, "E6906", {"start": v(-71.2, 448.8) * mm, "end": v(-70.85, 450.52) * mm});
            skLineSegment(sketch, "E6907", {"start": v(-70.85, 450.52) * mm, "end": v(-70.56, 452.25) * mm});
            skLineSegment(sketch, "E6908", {"start": v(-70.56, 452.25) * mm, "end": v(-70.33, 453.98) * mm});
            skLineSegment(sketch, "E6909", {"start": v(-70.33, 453.98) * mm, "end": v(-70.17, 455.7) * mm});
            skLineSegment(sketch, "E6910", {"start": v(-70.17, 455.7) * mm, "end": v(-70.07, 457.43) * mm});
            skLineSegment(sketch, "E6911", {"start": v(-70.07, 457.43) * mm, "end": v(-70.06, 459.14) * mm});
            skLineSegment(sketch, "E6912", {"start": v(-70.06, 459.14) * mm, "end": v(-70.12, 460.85) * mm});
            skLineSegment(sketch, "E6913", {"start": v(-70.12, 460.85) * mm, "end": v(-70.26, 462.54) * mm});
            skLineSegment(sketch, "E6914", {"start": v(-70.26, 462.54) * mm, "end": v(-70.5, 464.2) * mm});
            skLineSegment(sketch, "E6915", {"start": v(-70.5, 464.2) * mm, "end": v(-70.83, 465.86) * mm});
            skLineSegment(sketch, "E6916", {"start": v(-70.83, 465.86) * mm, "end": v(-71.27, 467.49) * mm});
            skLineSegment(sketch, "E6917", {"start": v(-71.27, 467.49) * mm, "end": v(-71.8, 469.09) * mm});
            skLineSegment(sketch, "E6918", {"start": v(-71.8, 469.09) * mm, "end": v(-72.46, 470.66) * mm});
            skLineSegment(sketch, "E6919", {"start": v(-72.46, 470.66) * mm, "end": v(-73.23, 472.2) * mm});
            skLineSegment(sketch, "E6920", {"start": v(-73.23, 472.2) * mm, "end": v(-74.11, 473.7) * mm});
            skLineSegment(sketch, "E6921", {"start": v(-74.11, 473.7) * mm, "end": v(-75.13, 475.17) * mm});
            skLineSegment(sketch, "E6922", {"start": v(-75.13, 475.17) * mm, "end": v(-76.27, 476.59) * mm});
            skLineSegment(sketch, "E6923", {"start": v(-76.27, 476.59) * mm, "end": v(-77.56, 477.97) * mm});
            skLineSegment(sketch, "E6924", {"start": v(-77.56, 477.97) * mm, "end": v(-78.7, 479.04) * mm});
            skLineSegment(sketch, "E6925", {"start": v(-78.7, 479.04) * mm, "end": v(-79.87, 480.04) * mm});
            skLineSegment(sketch, "E6926", {"start": v(-79.87, 480.04) * mm, "end": v(-81.1, 480.96) * mm});
            skLineSegment(sketch, "E6927", {"start": v(-81.1, 480.96) * mm, "end": v(-82.35, 481.8) * mm});
            skLineSegment(sketch, "E6928", {"start": v(-82.35, 481.8) * mm, "end": v(-83.66, 482.57) * mm});
            skLineSegment(sketch, "E6929", {"start": v(-83.66, 482.57) * mm, "end": v(-85, 483.27) * mm});
            skLineSegment(sketch, "E6930", {"start": v(-85, 483.27) * mm, "end": v(-86.37, 483.9) * mm});
            skLineSegment(sketch, "E6931", {"start": v(-86.37, 483.9) * mm, "end": v(-87.78, 484.46) * mm});
            skLineSegment(sketch, "E6932", {"start": v(-87.78, 484.46) * mm, "end": v(-89.22, 484.96) * mm});
            skLineSegment(sketch, "E6933", {"start": v(-89.22, 484.96) * mm, "end": v(-90.7, 485.4) * mm});
            skLineSegment(sketch, "E6934", {"start": v(-90.7, 485.4) * mm, "end": v(-92.2, 485.76) * mm});
            skLineSegment(sketch, "E6935", {"start": v(-92.2, 485.76) * mm, "end": v(-93.74, 486.07) * mm});
            skLineSegment(sketch, "E6936", {"start": v(-93.74, 486.07) * mm, "end": v(-95.3, 486.33) * mm});
            skLineSegment(sketch, "E6937", {"start": v(-95.3, 486.33) * mm, "end": v(-96.88, 486.53) * mm});
            skLineSegment(sketch, "E6938", {"start": v(-96.88, 486.53) * mm, "end": v(-98.49, 486.67) * mm});
            skLineSegment(sketch, "E6939", {"start": v(-98.49, 486.67) * mm, "end": v(-100.12, 486.76) * mm});
            skLineSegment(sketch, "E6940", {"start": v(-100.12, 486.76) * mm, "end": v(-101.77, 486.8) * mm});
            skLineSegment(sketch, "E6941", {"start": v(-101.77, 486.8) * mm, "end": v(-103.44, 486.8) * mm});
            skLineSegment(sketch, "E6942", {"start": v(-103.44, 486.8) * mm, "end": v(-105.13, 486.75) * mm});
            skLineSegment(sketch, "E6943", {"start": v(-105.13, 486.75) * mm, "end": v(-106.83, 486.65) * mm});
            skLineSegment(sketch, "E6944", {"start": v(-106.83, 486.65) * mm, "end": v(-108.55, 486.5) * mm});
            skLineSegment(sketch, "E6945", {"start": v(-108.55, 486.5) * mm, "end": v(-110.28, 486.33) * mm});
            skLineSegment(sketch, "E6946", {"start": v(-110.28, 486.33) * mm, "end": v(-112.02, 486.11) * mm});
            skLineSegment(sketch, "E6947", {"start": v(-112.02, 486.11) * mm, "end": v(-113.77, 485.86) * mm});
            skLineSegment(sketch, "E6948", {"start": v(-113.77, 485.86) * mm, "end": v(-115.52, 485.57) * mm});
            skLineSegment(sketch, "E6949", {"start": v(-115.52, 485.57) * mm, "end": v(-117.29, 485.24) * mm});
            skLineSegment(sketch, "E6950", {"start": v(-117.29, 485.24) * mm, "end": v(-119.06, 484.89) * mm});
            skLineSegment(sketch, "E6951", {"start": v(-119.06, 484.89) * mm, "end": v(-120.83, 484.5) * mm});
            skLineSegment(sketch, "E6952", {"start": v(-120.83, 484.5) * mm, "end": v(-122.6, 484.1) * mm});
            skLineSegment(sketch, "E6953", {"start": v(-122.6, 484.1) * mm, "end": v(-124.37, 483.66) * mm});
            skLineSegment(sketch, "E6954", {"start": v(-124.37, 483.66) * mm, "end": v(-126.14, 483.2) * mm});
            skLineSegment(sketch, "E6955", {"start": v(-126.14, 483.2) * mm, "end": v(-127.91, 482.72) * mm});
            skLineSegment(sketch, "E6956", {"start": v(-127.91, 482.72) * mm, "end": v(-129.68, 482.22) * mm});
            skLineSegment(sketch, "E6957", {"start": v(-129.68, 482.22) * mm, "end": v(-131.43, 481.7) * mm});
            skLineSegment(sketch, "E6958", {"start": v(-131.43, 481.7) * mm, "end": v(-133.18, 481.17) * mm});
            skLineSegment(sketch, "E6959", {"start": v(-133.18, 481.17) * mm, "end": v(-134.92, 480.63) * mm});
            skLineSegment(sketch, "E6960", {"start": v(-134.92, 480.63) * mm, "end": v(-136.65, 480.07) * mm});
            skLineSegment(sketch, "E6961", {"start": v(-136.65, 480.07) * mm, "end": v(-138.37, 479.5) * mm});
            skLineSegment(sketch, "E6962", {"start": v(-138.37, 479.5) * mm, "end": v(-140.07, 478.93) * mm});
            skLineSegment(sketch, "E6963", {"start": v(-140.07, 478.93) * mm, "end": v(-141.75, 478.35) * mm});
            skLineSegment(sketch, "E6964", {"start": v(-141.75, 478.35) * mm, "end": v(-143.42, 477.76) * mm});
            skLineSegment(sketch, "E6965", {"start": v(-143.42, 477.76) * mm, "end": v(-145.07, 477.17) * mm});
            skLineSegment(sketch, "E6966", {"start": v(-145.07, 477.17) * mm, "end": v(-146.7, 476.58) * mm});
            skLineSegment(sketch, "E6967", {"start": v(-146.7, 476.58) * mm, "end": v(-148.3, 476) * mm});
            skLineSegment(sketch, "E6968", {"start": v(-148.3, 476) * mm, "end": v(-149.89, 475.41) * mm});
            skLineSegment(sketch, "E6969", {"start": v(-149.89, 475.41) * mm, "end": v(-151.45, 474.84) * mm});
            skLineSegment(sketch, "E6970", {"start": v(-151.45, 474.84) * mm, "end": v(-152.98, 474.27) * mm});
            skLineSegment(sketch, "E6971", {"start": v(-152.98, 474.27) * mm, "end": v(-154.48, 473.7) * mm});
            skLineSegment(sketch, "E6972", {"start": v(-154.48, 473.7) * mm, "end": v(-155.95, 473.16) * mm});
            skLineSegment(sketch, "E6973", {"start": v(-155.95, 473.16) * mm, "end": v(-157.4, 472.62) * mm});
            skLineSegment(sketch, "E6974", {"start": v(-157.4, 472.62) * mm, "end": v(-158.8, 472.1) * mm});
            skLineSegment(sketch, "E6975", {"start": v(-158.8, 472.1) * mm, "end": v(-160.17, 471.6) * mm});
            skLineSegment(sketch, "E6976", {"start": v(-160.17, 471.6) * mm, "end": v(-161.5, 471.1) * mm});
            skLineSegment(sketch, "E6977", {"start": v(-161.5, 471.1) * mm, "end": v(-162.8, 470.64) * mm});
            skLineSegment(sketch, "E6978", {"start": v(-162.8, 470.64) * mm, "end": v(-164.06, 470.2) * mm});
            skLineSegment(sketch, "E6979", {"start": v(-164.06, 470.2) * mm, "end": v(-165.63, 469.65) * mm});
            skLineSegment(sketch, "E6980", {"start": v(-165.63, 469.65) * mm, "end": v(-167.2, 469.1) * mm});
            skLineSegment(sketch, "E6981", {"start": v(-167.2, 469.1) * mm, "end": v(-168.76, 468.55) * mm});
            skLineSegment(sketch, "E6982", {"start": v(-168.76, 468.55) * mm, "end": v(-170.33, 467.98) * mm});
            skLineSegment(sketch, "E6983", {"start": v(-170.33, 467.98) * mm, "end": v(-171.9, 467.4) * mm});
            skLineSegment(sketch, "E6984", {"start": v(-171.9, 467.4) * mm, "end": v(-173.48, 466.83) * mm});
            skLineSegment(sketch, "E6985", {"start": v(-173.48, 466.83) * mm, "end": v(-175.07, 466.24) * mm});
            skLineSegment(sketch, "E6986", {"start": v(-175.07, 466.24) * mm, "end": v(-176.65, 465.65) * mm});
            skLineSegment(sketch, "E6987", {"start": v(-176.65, 465.65) * mm, "end": v(-178.24, 465.05) * mm});
            skLineSegment(sketch, "E6988", {"start": v(-178.24, 465.05) * mm, "end": v(-179.83, 464.45) * mm});
            skLineSegment(sketch, "E6989", {"start": v(-179.83, 464.45) * mm, "end": v(-181.42, 463.84) * mm});
            skLineSegment(sketch, "E6990", {"start": v(-181.42, 463.84) * mm, "end": v(-183.02, 463.22) * mm});
            skLineSegment(sketch, "E6991", {"start": v(-183.02, 463.22) * mm, "end": v(-184.62, 462.6) * mm});
            skLineSegment(sketch, "E6992", {"start": v(-184.62, 462.6) * mm, "end": v(-186.22, 461.96) * mm});
            skLineSegment(sketch, "E6993", {"start": v(-186.22, 461.96) * mm, "end": v(-187.82, 461.32) * mm});
            skLineSegment(sketch, "E6994", {"start": v(-187.82, 461.32) * mm, "end": v(-189.43, 460.68) * mm});
            skLineSegment(sketch, "E6995", {"start": v(-189.43, 460.68) * mm, "end": v(-191.03, 460.03) * mm});
            skLineSegment(sketch, "E6996", {"start": v(-191.03, 460.03) * mm, "end": v(-192.64, 459.37) * mm});
            skLineSegment(sketch, "E6997", {"start": v(-192.64, 459.37) * mm, "end": v(-194.25, 458.7) * mm});
            skLineSegment(sketch, "E6998", {"start": v(-194.25, 458.7) * mm, "end": v(-195.87, 458.03) * mm});
            skLineSegment(sketch, "E6999", {"start": v(-195.87, 458.03) * mm, "end": v(-197.48, 457.35) * mm});
            skLineSegment(sketch, "E7000", {"start": v(-197.48, 457.35) * mm, "end": v(-199.1, 456.67) * mm});
            skLineSegment(sketch, "E7001", {"start": v(-199.1, 456.67) * mm, "end": v(-200.71, 455.98) * mm});
            skLineSegment(sketch, "E7002", {"start": v(-200.71, 455.98) * mm, "end": v(-202.33, 455.28) * mm});
            skLineSegment(sketch, "E7003", {"start": v(-202.33, 455.28) * mm, "end": v(-203.95, 454.58) * mm});
            skLineSegment(sketch, "E7004", {"start": v(-203.95, 454.58) * mm, "end": v(-205.57, 453.87) * mm});
            skLineSegment(sketch, "E7005", {"start": v(-205.57, 453.87) * mm, "end": v(-207.2, 453.15) * mm});
            skLineSegment(sketch, "E7006", {"start": v(-207.2, 453.15) * mm, "end": v(-208.82, 452.43) * mm});
            skLineSegment(sketch, "E7007", {"start": v(-208.82, 452.43) * mm, "end": v(-210.44, 451.7) * mm});
            skLineSegment(sketch, "E7008", {"start": v(-210.44, 451.7) * mm, "end": v(-212.07, 450.96) * mm});
            skLineSegment(sketch, "E7009", {"start": v(-212.07, 450.96) * mm, "end": v(-213.7, 450.22) * mm});
            skLineSegment(sketch, "E7010", {"start": v(-213.7, 450.22) * mm, "end": v(-215.32, 449.47) * mm});
            skLineSegment(sketch, "E7011", {"start": v(-215.32, 449.47) * mm, "end": v(-216.94, 448.71) * mm});
            skLineSegment(sketch, "E7012", {"start": v(-216.94, 448.71) * mm, "end": v(-218.57, 447.95) * mm});
            skLineSegment(sketch, "E7013", {"start": v(-218.57, 447.95) * mm, "end": v(-220.2, 447.19) * mm});
            skLineSegment(sketch, "E7014", {"start": v(-220.2, 447.19) * mm, "end": v(-221.82, 446.41) * mm});
            skLineSegment(sketch, "E7015", {"start": v(-221.82, 446.41) * mm, "end": v(-223.44, 445.63) * mm});
            skLineSegment(sketch, "E7016", {"start": v(-223.44, 445.63) * mm, "end": v(-225.07, 444.84) * mm});
            skLineSegment(sketch, "E7017", {"start": v(-225.07, 444.84) * mm, "end": v(-226.7, 444.05) * mm});
            skLineSegment(sketch, "E7018", {"start": v(-226.7, 444.05) * mm, "end": v(-228.32, 443.25) * mm});
            skLineSegment(sketch, "E7019", {"start": v(-228.32, 443.25) * mm, "end": v(-229.94, 442.44) * mm});
            skLineSegment(sketch, "E7020", {"start": v(-229.94, 442.44) * mm, "end": v(-231.57, 441.63) * mm});
            skLineSegment(sketch, "E7021", {"start": v(-231.57, 441.63) * mm, "end": v(-233.19, 440.81) * mm});
            skLineSegment(sketch, "E7022", {"start": v(-233.19, 440.81) * mm, "end": v(-234.81, 440) * mm});
            skLineSegment(sketch, "E7023", {"start": v(-234.81, 440) * mm, "end": v(-236.43, 439.16) * mm});
            skLineSegment(sketch, "E7024", {"start": v(-236.43, 439.16) * mm, "end": v(-238.05, 438.32) * mm});
            skLineSegment(sketch, "E7025", {"start": v(-238.05, 438.32) * mm, "end": v(-239.67, 437.48) * mm});
            skLineSegment(sketch, "E7026", {"start": v(-239.67, 437.48) * mm, "end": v(-241.29, 436.63) * mm});
            skLineSegment(sketch, "E7027", {"start": v(-241.29, 436.63) * mm, "end": v(-242.9, 435.77) * mm});
            skLineSegment(sketch, "E7028", {"start": v(-242.9, 435.77) * mm, "end": v(-244.52, 434.91) * mm});
            skLineSegment(sketch, "E7029", {"start": v(-244.52, 434.91) * mm, "end": v(-246.13, 434.05) * mm});
            skLineSegment(sketch, "E7030", {"start": v(-246.13, 434.05) * mm, "end": v(-247.74, 433.17) * mm});
            skLineSegment(sketch, "E7031", {"start": v(-247.74, 433.17) * mm, "end": v(-249.35, 432.3) * mm});
            skLineSegment(sketch, "E7032", {"start": v(-249.35, 432.3) * mm, "end": v(-250.96, 431.4) * mm});
            skLineSegment(sketch, "E7033", {"start": v(-250.96, 431.4) * mm, "end": v(-252.56, 430.51) * mm});
            skLineSegment(sketch, "E7034", {"start": v(-252.56, 430.51) * mm, "end": v(-254.17, 429.61) * mm});
            skLineSegment(sketch, "E7035", {"start": v(-254.17, 429.61) * mm, "end": v(-255.77, 428.7) * mm});
            skLineSegment(sketch, "E7036", {"start": v(-255.77, 428.7) * mm, "end": v(-257.36, 427.8) * mm});
            skLineSegment(sketch, "E7037", {"start": v(-257.36, 427.8) * mm, "end": v(-258.96, 426.88) * mm});
            skLineSegment(sketch, "E7038", {"start": v(-258.96, 426.88) * mm, "end": v(-260.55, 425.96) * mm});
            skLineSegment(sketch, "E7039", {"start": v(-260.55, 425.96) * mm, "end": v(-262.14, 425.03) * mm});
            skLineSegment(sketch, "E7040", {"start": v(-262.14, 425.03) * mm, "end": v(-263.73, 424.1) * mm});
            skLineSegment(sketch, "E7041", {"start": v(-263.73, 424.1) * mm, "end": v(-265.32, 423.16) * mm});
            skLineSegment(sketch, "E7042", {"start": v(-265.32, 423.16) * mm, "end": v(-266.9, 422.21) * mm});
            skLineSegment(sketch, "E7043", {"start": v(-266.9, 422.21) * mm, "end": v(-268.48, 421.26) * mm});
            skLineSegment(sketch, "E7044", {"start": v(-268.48, 421.26) * mm, "end": v(-270.05, 420.3) * mm});
            skLineSegment(sketch, "E7045", {"start": v(-270.05, 420.3) * mm, "end": v(-271.62, 419.33) * mm});
            skLineSegment(sketch, "E7046", {"start": v(-271.62, 419.33) * mm, "end": v(-273.2, 418.36) * mm});
            skLineSegment(sketch, "E7047", {"start": v(-273.2, 418.36) * mm, "end": v(-274.76, 417.39) * mm});
            skLineSegment(sketch, "E7048", {"start": v(-274.76, 417.39) * mm, "end": v(-276.32, 416.4) * mm});
            skLineSegment(sketch, "E7049", {"start": v(-276.32, 416.4) * mm, "end": v(-277.87, 415.42) * mm});
            skLineSegment(sketch, "E7050", {"start": v(-277.87, 415.42) * mm, "end": v(-279.43, 414.42) * mm});
            skLineSegment(sketch, "E7051", {"start": v(-279.43, 414.42) * mm, "end": v(-280.98, 413.42) * mm});
            skLineSegment(sketch, "E7052", {"start": v(-280.98, 413.42) * mm, "end": v(-282.52, 412.42) * mm});
            skLineSegment(sketch, "E7053", {"start": v(-282.52, 412.42) * mm, "end": v(-284.06, 411.4) * mm});
            skLineSegment(sketch, "E7054", {"start": v(-284.06, 411.4) * mm, "end": v(-285.6, 410.39) * mm});
            skLineSegment(sketch, "E7055", {"start": v(-285.6, 410.39) * mm, "end": v(-287.13, 409.37) * mm});
            skLineSegment(sketch, "E7056", {"start": v(-287.13, 409.37) * mm, "end": v(-288.66, 408.34) * mm});
            skLineSegment(sketch, "E7057", {"start": v(-288.66, 408.34) * mm, "end": v(-290.18, 407.3) * mm});
            skLineSegment(sketch, "E7058", {"start": v(-290.18, 407.3) * mm, "end": v(-291.7, 406.26) * mm});
            skLineSegment(sketch, "E7059", {"start": v(-291.7, 406.26) * mm, "end": v(-293.2, 405.22) * mm});
            skLineSegment(sketch, "E7060", {"start": v(-293.2, 405.22) * mm, "end": v(-294.72, 404.16) * mm});
            skLineSegment(sketch, "E7061", {"start": v(-294.72, 404.16) * mm, "end": v(-296.22, 403.1) * mm});
            skLineSegment(sketch, "E7062", {"start": v(-296.22, 403.1) * mm, "end": v(-297.72, 402.04) * mm});
            skLineSegment(sketch, "E7063", {"start": v(-297.72, 402.04) * mm, "end": v(-299.2, 400.97) * mm});
            skLineSegment(sketch, "E7064", {"start": v(-299.2, 400.97) * mm, "end": v(-300.7, 399.9) * mm});
            skLineSegment(sketch, "E7065", {"start": v(-300.7, 399.9) * mm, "end": v(-302.18, 398.82) * mm});
            skLineSegment(sketch, "E7066", {"start": v(-302.18, 398.82) * mm, "end": v(-303.65, 397.73) * mm});
            skLineSegment(sketch, "E7067", {"start": v(-303.65, 397.73) * mm, "end": v(-305.12, 396.64) * mm});
            skLineSegment(sketch, "E7068", {"start": v(-305.12, 396.64) * mm, "end": v(-306.59, 395.54) * mm});
            skLineSegment(sketch, "E7069", {"start": v(-306.59, 395.54) * mm, "end": v(-308.04, 394.44) * mm});
            skLineSegment(sketch, "E7070", {"start": v(-308.04, 394.44) * mm, "end": v(-309.5, 393.33) * mm});
            skLineSegment(sketch, "E7071", {"start": v(-309.5, 393.33) * mm, "end": v(-310.94, 392.22) * mm});
            skLineSegment(sketch, "E7072", {"start": v(-310.94, 392.22) * mm, "end": v(-312.38, 391.1) * mm});
            skLineSegment(sketch, "E7073", {"start": v(-312.38, 391.1) * mm, "end": v(-313.81, 389.97) * mm});
            skLineSegment(sketch, "E7074", {"start": v(-313.81, 389.97) * mm, "end": v(-315.24, 388.84) * mm});
            skLineSegment(sketch, "E7075", {"start": v(-315.24, 388.84) * mm, "end": v(-316.66, 387.7) * mm});
            skLineSegment(sketch, "E7076", {"start": v(-316.66, 387.7) * mm, "end": v(-318.07, 386.56) * mm});
            skLineSegment(sketch, "E7077", {"start": v(-318.07, 386.56) * mm, "end": v(-319.48, 385.41) * mm});
            skLineSegment(sketch, "E7078", {"start": v(-319.48, 385.41) * mm, "end": v(-320.88, 384.26) * mm});
            skLineSegment(sketch, "E7079", {"start": v(-320.88, 384.26) * mm, "end": v(-322.27, 383.1) * mm});
            skLineSegment(sketch, "E7080", {"start": v(-322.27, 383.1) * mm, "end": v(-323.65, 381.94) * mm});
            skLineSegment(sketch, "E7081", {"start": v(-323.65, 381.94) * mm, "end": v(-325.03, 380.77) * mm});
            skLineSegment(sketch, "E7082", {"start": v(-325.03, 380.77) * mm, "end": v(-326.4, 379.6) * mm});
            skLineSegment(sketch, "E7083", {"start": v(-326.4, 379.6) * mm, "end": v(-327.76, 378.41) * mm});
            skLineSegment(sketch, "E7084", {"start": v(-327.76, 378.41) * mm, "end": v(-329.12, 377.23) * mm});
            skLineSegment(sketch, "E7085", {"start": v(-329.12, 377.23) * mm, "end": v(-330.46, 376.03) * mm});
            skLineSegment(sketch, "E7086", {"start": v(-330.46, 376.03) * mm, "end": v(-331.8, 374.84) * mm});
            skLineSegment(sketch, "E7087", {"start": v(-331.8, 374.84) * mm, "end": v(-333.14, 373.63) * mm});
            skLineSegment(sketch, "E7088", {"start": v(-333.14, 373.63) * mm, "end": v(-334.46, 372.43) * mm});
            skLineSegment(sketch, "E7089", {"start": v(-334.46, 372.43) * mm, "end": v(-335.77, 371.21) * mm});
            skLineSegment(sketch, "E7090", {"start": v(-335.77, 371.21) * mm, "end": v(-337.08, 370) * mm});
            skLineSegment(sketch, "E7091", {"start": v(-337.08, 370) * mm, "end": v(-338.38, 368.77) * mm});
            skLineSegment(sketch, "E7092", {"start": v(-338.38, 368.77) * mm, "end": v(-339.67, 367.54) * mm});
            skLineSegment(sketch, "E7093", {"start": v(-339.67, 367.54) * mm, "end": v(-340.95, 366.3) * mm});
            skLineSegment(sketch, "E7094", {"start": v(-340.95, 366.3) * mm, "end": v(-342.22, 365.07) * mm});
            skLineSegment(sketch, "E7095", {"start": v(-342.22, 365.07) * mm, "end": v(-343.49, 363.82) * mm});
            skLineSegment(sketch, "E7096", {"start": v(-343.49, 363.82) * mm, "end": v(-344.74, 362.57) * mm});
            skLineSegment(sketch, "E7097", {"start": v(-344.74, 362.57) * mm, "end": v(-345.99, 361.32) * mm});
            skLineSegment(sketch, "E7098", {"start": v(-345.99, 361.32) * mm, "end": v(-347.22, 360.06) * mm});
            skLineSegment(sketch, "E7099", {"start": v(-347.22, 360.06) * mm, "end": v(-348.45, 358.79) * mm});
            skLineSegment(sketch, "E7100", {"start": v(-348.45, 358.79) * mm, "end": v(-349.67, 357.52) * mm});
            skLineSegment(sketch, "E7101", {"start": v(-349.67, 357.52) * mm, "end": v(-350.88, 356.24) * mm});
            skLineSegment(sketch, "E7102", {"start": v(-350.88, 356.24) * mm, "end": v(-352.07, 354.96) * mm});
            skLineSegment(sketch, "E7103", {"start": v(-352.07, 354.96) * mm, "end": v(-353.26, 353.67) * mm});
            skLineSegment(sketch, "E7104", {"start": v(-353.26, 353.67) * mm, "end": v(-354.44, 352.38) * mm});
            skLineSegment(sketch, "E7105", {"start": v(-354.44, 352.38) * mm, "end": v(-355.61, 351.08) * mm});
            skLineSegment(sketch, "E7106", {"start": v(-355.61, 351.08) * mm, "end": v(-356.77, 349.78) * mm});
            skLineSegment(sketch, "E7107", {"start": v(-356.77, 349.78) * mm, "end": v(-357.92, 348.47) * mm});
            skLineSegment(sketch, "E7108", {"start": v(-357.92, 348.47) * mm, "end": v(-359.06, 347.16) * mm});
            skLineSegment(sketch, "E7109", {"start": v(-359.06, 347.16) * mm, "end": v(-360.19, 345.84) * mm});
            skLineSegment(sketch, "E7110", {"start": v(-360.19, 345.84) * mm, "end": v(-361.3, 344.52) * mm});
            skLineSegment(sketch, "E7111", {"start": v(-361.3, 344.52) * mm, "end": v(-362.41, 343.2) * mm});
            skLineSegment(sketch, "E7112", {"start": v(-362.41, 343.2) * mm, "end": v(-363.51, 341.86) * mm});
            skLineSegment(sketch, "E7113", {"start": v(-363.51, 341.86) * mm, "end": v(-364.6, 340.52) * mm});
            skLineSegment(sketch, "E7114", {"start": v(-364.6, 340.52) * mm, "end": v(-365.67, 339.18) * mm});
            skLineSegment(sketch, "E7115", {"start": v(-365.67, 339.18) * mm, "end": v(-366.74, 337.83) * mm});
            skLineSegment(sketch, "E7116", {"start": v(-366.74, 337.83) * mm, "end": v(-367.79, 336.47) * mm});
            skLineSegment(sketch, "E7117", {"start": v(-367.79, 336.47) * mm, "end": v(-368.83, 335.12) * mm});
            skLineSegment(sketch, "E7118", {"start": v(-368.83, 335.12) * mm, "end": v(-369.86, 333.75) * mm});
            skLineSegment(sketch, "E7119", {"start": v(-369.86, 333.75) * mm, "end": v(-370.88, 332.38) * mm});
            skLineSegment(sketch, "E7120", {"start": v(-370.88, 332.38) * mm, "end": v(-371.89, 331.01) * mm});
            skLineSegment(sketch, "E7121", {"start": v(-371.89, 331.01) * mm, "end": v(-372.88, 329.63) * mm});
            skLineSegment(sketch, "E7122", {"start": v(-372.88, 329.63) * mm, "end": v(-373.87, 328.25) * mm});
            skLineSegment(sketch, "E7123", {"start": v(-373.87, 328.25) * mm, "end": v(-374.84, 326.86) * mm});
            skLineSegment(sketch, "E7124", {"start": v(-374.84, 326.86) * mm, "end": v(-375.8, 325.47) * mm});
            skLineSegment(sketch, "E7125", {"start": v(-375.8, 325.47) * mm, "end": v(-376.75, 324.07) * mm});
            skLineSegment(sketch, "E7126", {"start": v(-376.75, 324.07) * mm, "end": v(-377.68, 322.67) * mm});
            skLineSegment(sketch, "E7127", {"start": v(-377.68, 322.67) * mm, "end": v(-336.05, 322.67) * mm});
            skLineSegment(sketch, "E7128", {"start": v(-336.05, 322.67) * mm, "end": v(-336.85, 320.93) * mm});
            skLineSegment(sketch, "E7129", {"start": v(-336.85, 320.93) * mm, "end": v(-337.61, 319.2) * mm});
            skLineSegment(sketch, "E7130", {"start": v(-337.61, 319.2) * mm, "end": v(-338.34, 317.46) * mm});
            skLineSegment(sketch, "E7131", {"start": v(-338.34, 317.46) * mm, "end": v(-339.03, 315.73) * mm});
            skLineSegment(sketch, "E7132", {"start": v(-339.03, 315.73) * mm, "end": v(-339.69, 314) * mm});
            skLineSegment(sketch, "E7133", {"start": v(-339.69, 314) * mm, "end": v(-340.3, 312.27) * mm});
            skLineSegment(sketch, "E7134", {"start": v(-340.3, 312.27) * mm, "end": v(-340.89, 310.54) * mm});
            skLineSegment(sketch, "E7135", {"start": v(-340.89, 310.54) * mm, "end": v(-341.44, 308.82) * mm});
            skLineSegment(sketch, "E7136", {"start": v(-341.44, 308.82) * mm, "end": v(-341.96, 307.1) * mm});
            skLineSegment(sketch, "E7137", {"start": v(-341.96, 307.1) * mm, "end": v(-342.45, 305.37) * mm});
            skLineSegment(sketch, "E7138", {"start": v(-342.45, 305.37) * mm, "end": v(-342.9, 303.65) * mm});
            skLineSegment(sketch, "E7139", {"start": v(-342.9, 303.65) * mm, "end": v(-343.33, 301.93) * mm});
            skLineSegment(sketch, "E7140", {"start": v(-343.33, 301.93) * mm, "end": v(-343.73, 300.2) * mm});
            skLineSegment(sketch, "E7141", {"start": v(-343.73, 300.2) * mm, "end": v(-344.1, 298.49) * mm});
            skLineSegment(sketch, "E7142", {"start": v(-344.1, 298.49) * mm, "end": v(-344.44, 296.76) * mm});
            skLineSegment(sketch, "E7143", {"start": v(-344.44, 296.76) * mm, "end": v(-344.76, 295.04) * mm});
            skLineSegment(sketch, "E7144", {"start": v(-344.76, 295.04) * mm, "end": v(-345.06, 293.32) * mm});
            skLineSegment(sketch, "E7145", {"start": v(-345.06, 293.32) * mm, "end": v(-345.33, 291.59) * mm});
            skLineSegment(sketch, "E7146", {"start": v(-345.33, 291.59) * mm, "end": v(-345.57, 289.86) * mm});
            skLineSegment(sketch, "E7147", {"start": v(-345.57, 289.86) * mm, "end": v(-345.8, 288.13) * mm});
            skLineSegment(sketch, "E7148", {"start": v(-345.8, 288.13) * mm, "end": v(-346, 286.4) * mm});
            skLineSegment(sketch, "E7149", {"start": v(-346, 286.4) * mm, "end": v(-346.19, 284.67) * mm});
            skLineSegment(sketch, "E7150", {"start": v(-346.19, 284.67) * mm, "end": v(-346.35, 282.93) * mm});
            skLineSegment(sketch, "E7151", {"start": v(-346.35, 282.93) * mm, "end": v(-346.5, 281.19) * mm});
            skLineSegment(sketch, "E7152", {"start": v(-346.5, 281.19) * mm, "end": v(-346.62, 279.44) * mm});
            skLineSegment(sketch, "E7153", {"start": v(-346.62, 279.44) * mm, "end": v(-346.74, 277.7) * mm});
            skLineSegment(sketch, "E7154", {"start": v(-346.74, 277.7) * mm, "end": v(-346.83, 275.95) * mm});
            skLineSegment(sketch, "E7155", {"start": v(-346.83, 275.95) * mm, "end": v(-346.91, 274.2) * mm});
            skLineSegment(sketch, "E7156", {"start": v(-346.91, 274.2) * mm, "end": v(-346.98, 272.43) * mm});
            skLineSegment(sketch, "E7157", {"start": v(-346.98, 272.43) * mm, "end": v(-347.04, 270.67) * mm});
            skLineSegment(sketch, "E7158", {"start": v(-347.04, 270.67) * mm, "end": v(-347.08, 268.9) * mm});
            skLineSegment(sketch, "E7159", {"start": v(-347.08, 268.9) * mm, "end": v(-347.11, 267.12) * mm});
            skLineSegment(sketch, "E7160", {"start": v(-347.11, 267.12) * mm, "end": v(-347.14, 265.34) * mm});
            skLineSegment(sketch, "E7161", {"start": v(-347.14, 265.34) * mm, "end": v(-347.15, 263.56) * mm});
            skLineSegment(sketch, "E7162", {"start": v(-347.15, 263.56) * mm, "end": v(-347.16, 261.76) * mm});
            skLineSegment(sketch, "E7163", {"start": v(-347.16, 261.76) * mm, "end": v(-347.15, 259.97) * mm});
            skLineSegment(sketch, "E7164", {"start": v(-347.15, 259.97) * mm, "end": v(-347.15, 258.16) * mm});
            skLineSegment(sketch, "E7165", {"start": v(-347.15, 258.16) * mm, "end": v(-347.13, 256.35) * mm});
            skLineSegment(sketch, "E7166", {"start": v(-347.13, 256.35) * mm, "end": v(-347.12, 254.53) * mm});
            skLineSegment(sketch, "E7167", {"start": v(-347.12, 254.53) * mm, "end": v(-347.1, 252.7) * mm});
            skLineSegment(sketch, "E7168", {"start": v(-347.1, 252.7) * mm, "end": v(-347.07, 250.87) * mm});
            skLineSegment(sketch, "E7169", {"start": v(-347.07, 250.87) * mm, "end": v(-347.05, 249.02) * mm});
            skLineSegment(sketch, "E7170", {"start": v(-347.05, 249.02) * mm, "end": v(-347.02, 247.17) * mm});
            skLineSegment(sketch, "E7171", {"start": v(-347.02, 247.17) * mm, "end": v(-347, 245.31) * mm});
            skLineSegment(sketch, "E7172", {"start": v(-347, 245.31) * mm, "end": v(-346.97, 243.45) * mm});
            skLineSegment(sketch, "E7173", {"start": v(-346.97, 243.45) * mm, "end": v(-346.95, 241.57) * mm});
            skLineSegment(sketch, "E7174", {"start": v(-346.95, 241.57) * mm, "end": v(-346.93, 239.68) * mm});
            skLineSegment(sketch, "E7175", {"start": v(-346.93, 239.68) * mm, "end": v(-346.92, 237.78) * mm});
            skLineSegment(sketch, "E7176", {"start": v(-346.92, 237.78) * mm, "end": v(-346.91, 235.88) * mm});
            skLineSegment(sketch, "E7177", {"start": v(-346.91, 235.88) * mm, "end": v(-346.9, 233.96) * mm});
            skLineSegment(sketch, "E7178", {"start": v(-346.9, 233.96) * mm, "end": v(-346.94, 232.59) * mm});
            skLineSegment(sketch, "E7179", {"start": v(-346.94, 232.59) * mm, "end": v(-347.01, 231.06) * mm});
            skLineSegment(sketch, "E7180", {"start": v(-347.01, 231.06) * mm, "end": v(-347.12, 229.4) * mm});
            skLineSegment(sketch, "E7181", {"start": v(-347.12, 229.4) * mm, "end": v(-347.25, 227.63) * mm});
            skLineSegment(sketch, "E7182", {"start": v(-347.25, 227.63) * mm, "end": v(-347.39, 225.77) * mm});
            skLineSegment(sketch, "E7183", {"start": v(-347.39, 225.77) * mm, "end": v(-347.52, 223.84) * mm});
            skLineSegment(sketch, "E7184", {"start": v(-347.52, 223.84) * mm, "end": v(-347.63, 221.86) * mm});
            skLineSegment(sketch, "E7185", {"start": v(-347.63, 221.86) * mm, "end": v(-347.72, 219.86) * mm});
            skLineSegment(sketch, "E7186", {"start": v(-347.72, 219.86) * mm, "end": v(-347.76, 217.85) * mm});
            skLineSegment(sketch, "E7187", {"start": v(-347.76, 217.85) * mm, "end": v(-347.74, 215.86) * mm});
            skLineSegment(sketch, "E7188", {"start": v(-347.74, 215.86) * mm, "end": v(-347.66, 213.92) * mm});
            skLineSegment(sketch, "E7189", {"start": v(-347.66, 213.92) * mm, "end": v(-347.49, 212.03) * mm});
            skLineSegment(sketch, "E7190", {"start": v(-347.49, 212.03) * mm, "end": v(-347.22, 210.23) * mm});
            skLineSegment(sketch, "E7191", {"start": v(-347.22, 210.23) * mm, "end": v(-346.85, 208.53) * mm});
            skLineSegment(sketch, "E7192", {"start": v(-346.85, 208.53) * mm, "end": v(-346.35, 206.95) * mm});
            skLineSegment(sketch, "E7193", {"start": v(-346.35, 206.95) * mm, "end": v(-345.72, 205.53) * mm});
            skLineSegment(sketch, "E7194", {"start": v(-345.72, 205.53) * mm, "end": v(-344.94, 204.27) * mm});
            skLineSegment(sketch, "E7195", {"start": v(-344.94, 204.27) * mm, "end": v(-344, 203.2) * mm});
            skLineSegment(sketch, "E7196", {"start": v(-344, 203.2) * mm, "end": v(-343.1, 202.43) * mm});
            skLineSegment(sketch, "E7197", {"start": v(-343.1, 202.43) * mm, "end": v(-342.09, 201.73) * mm});
            skLineSegment(sketch, "E7198", {"start": v(-342.09, 201.73) * mm, "end": v(-340.97, 201.08) * mm});
            skLineSegment(sketch, "E7199", {"start": v(-340.97, 201.08) * mm, "end": v(-339.76, 200.5) * mm});
            skLineSegment(sketch, "E7200", {"start": v(-339.76, 200.5) * mm, "end": v(-338.45, 199.97) * mm});
            skLineSegment(sketch, "E7201", {"start": v(-338.45, 199.97) * mm, "end": v(-337.06, 199.5) * mm});
            skLineSegment(sketch, "E7202", {"start": v(-337.06, 199.5) * mm, "end": v(-335.6, 199.07) * mm});
            skLineSegment(sketch, "E7203", {"start": v(-335.6, 199.07) * mm, "end": v(-334.05, 198.7) * mm});
            skLineSegment(sketch, "E7204", {"start": v(-334.05, 198.7) * mm, "end": v(-332.43, 198.37) * mm});
            skLineSegment(sketch, "E7205", {"start": v(-332.43, 198.37) * mm, "end": v(-330.75, 198.1) * mm});
            skLineSegment(sketch, "E7206", {"start": v(-330.75, 198.1) * mm, "end": v(-329, 197.86) * mm});
            skLineSegment(sketch, "E7207", {"start": v(-329, 197.86) * mm, "end": v(-327.21, 197.66) * mm});
            skLineSegment(sketch, "E7208", {"start": v(-327.21, 197.66) * mm, "end": v(-325.37, 197.5) * mm});
            skLineSegment(sketch, "E7209", {"start": v(-325.37, 197.5) * mm, "end": v(-323.48, 197.39) * mm});
            skLineSegment(sketch, "E7210", {"start": v(-323.48, 197.39) * mm, "end": v(-321.55, 197.3) * mm});
            skLineSegment(sketch, "E7211", {"start": v(-321.55, 197.3) * mm, "end": v(-319.6, 197.25) * mm});
            skLineSegment(sketch, "E7212", {"start": v(-319.6, 197.25) * mm, "end": v(-317.6, 197.22) * mm});
            skLineSegment(sketch, "E7213", {"start": v(-317.6, 197.22) * mm, "end": v(-315.6, 197.23) * mm});
            skLineSegment(sketch, "E7214", {"start": v(-315.6, 197.23) * mm, "end": v(-313.57, 197.26) * mm});
            skLineSegment(sketch, "E7215", {"start": v(-313.57, 197.26) * mm, "end": v(-311.53, 197.3) * mm});
            skLineSegment(sketch, "E7216", {"start": v(-311.53, 197.3) * mm, "end": v(-309.48, 197.38) * mm});
            skLineSegment(sketch, "E7217", {"start": v(-309.48, 197.38) * mm, "end": v(-307.43, 197.47) * mm});
            skLineSegment(sketch, "E7218", {"start": v(-307.43, 197.47) * mm, "end": v(-305.38, 197.57) * mm});
            skLineSegment(sketch, "E7219", {"start": v(-305.38, 197.57) * mm, "end": v(-303.35, 197.69) * mm});
            skLineSegment(sketch, "E7220", {"start": v(-303.35, 197.69) * mm, "end": v(-301.33, 197.82) * mm});
            skLineSegment(sketch, "E7221", {"start": v(-301.33, 197.82) * mm, "end": v(-299.32, 197.96) * mm});
            skLineSegment(sketch, "E7222", {"start": v(-299.32, 197.96) * mm, "end": v(-297.35, 198.1) * mm});
            skLineSegment(sketch, "E7223", {"start": v(-297.35, 198.1) * mm, "end": v(-295.4, 198.25) * mm});
            skLineSegment(sketch, "E7224", {"start": v(-295.4, 198.25) * mm, "end": v(-293.49, 198.4) * mm});
            skLineSegment(sketch, "E7225", {"start": v(-293.49, 198.4) * mm, "end": v(-291.62, 198.56) * mm});
            skLineSegment(sketch, "E7226", {"start": v(-291.62, 198.56) * mm, "end": v(-289.8, 198.7) * mm});
            skLineSegment(sketch, "E7227", {"start": v(-289.8, 198.7) * mm, "end": v(-288.02, 198.85) * mm});
            skLineSegment(sketch, "E7228", {"start": v(-288.02, 198.85) * mm, "end": v(-286.3, 198.99) * mm});
            skLineSegment(sketch, "E7229", {"start": v(-286.3, 198.99) * mm, "end": v(-284.64, 199.12) * mm});
            skLineSegment(sketch, "E7230", {"start": v(-284.64, 199.12) * mm, "end": v(-283.06, 199.24) * mm});
            skLineSegment(sketch, "E7231", {"start": v(-283.06, 199.24) * mm, "end": v(-281.54, 199.34) * mm});
            skLineSegment(sketch, "E7232", {"start": v(-281.54, 199.34) * mm, "end": v(-280.1, 199.43) * mm});
            skLineSegment(sketch, "E7233", {"start": v(-280.1, 199.43) * mm, "end": v(-278.75, 199.5) * mm});
            skLineSegment(sketch, "E7234", {"start": v(-278.75, 199.5) * mm, "end": v(-277.48, 199.55) * mm});
            skLineSegment(sketch, "E7235", {"start": v(-277.48, 199.55) * mm, "end": v(-276.3, 199.57) * mm});
            skLineSegment(sketch, "E7236", {"start": v(-276.3, 199.57) * mm, "end": v(-274.74, 199.59) * mm});
            skLineSegment(sketch, "E7237", {"start": v(-274.74, 199.59) * mm, "end": v(-273.06, 199.61) * mm});
            skLineSegment(sketch, "E7238", {"start": v(-273.06, 199.61) * mm, "end": v(-271.29, 199.67) * mm});
            skLineSegment(sketch, "E7239", {"start": v(-271.29, 199.67) * mm, "end": v(-269.47, 199.8) * mm});
            skLineSegment(sketch, "E7240", {"start": v(-269.47, 199.8) * mm, "end": v(-267.64, 200) * mm});
            skLineSegment(sketch, "E7241", {"start": v(-267.64, 200) * mm, "end": v(-265.83, 200.3) * mm});
            skLineSegment(sketch, "E7242", {"start": v(-265.83, 200.3) * mm, "end": v(-264.08, 200.75) * mm});
            skLineSegment(sketch, "E7243", {"start": v(-264.08, 200.75) * mm, "end": v(-262.42, 201.34) * mm});
            skLineSegment(sketch, "E7244", {"start": v(-262.42, 201.34) * mm, "end": v(-260.9, 202.12) * mm});
            skLineSegment(sketch, "E7245", {"start": v(-260.9, 202.12) * mm, "end": v(-259.55, 203.1) * mm});
            skLineSegment(sketch, "E7246", {"start": v(-259.55, 203.1) * mm, "end": v(-258.4, 204.3) * mm});
            skLineSegment(sketch, "E7247", {"start": v(-258.4, 204.3) * mm, "end": v(-257.48, 205.75) * mm});
            skLineSegment(sketch, "E7248", {"start": v(-257.48, 205.75) * mm, "end": v(-256.89, 207.16) * mm});
            skLineSegment(sketch, "E7249", {"start": v(-256.89, 207.16) * mm, "end": v(-256.4, 208.68) * mm});
            skLineSegment(sketch, "E7250", {"start": v(-256.4, 208.68) * mm, "end": v(-256.03, 210.3) * mm});
            skLineSegment(sketch, "E7251", {"start": v(-256.03, 210.3) * mm, "end": v(-255.75, 212) * mm});
            skLineSegment(sketch, "E7252", {"start": v(-255.75, 212) * mm, "end": v(-255.56, 213.78) * mm});
            skLineSegment(sketch, "E7253", {"start": v(-255.56, 213.78) * mm, "end": v(-255.44, 215.62) * mm});
            skLineSegment(sketch, "E7254", {"start": v(-255.44, 215.62) * mm, "end": v(-255.4, 217.51) * mm});
            skLineSegment(sketch, "E7255", {"start": v(-255.4, 217.51) * mm, "end": v(-255.4, 219.43) * mm});
            skLineSegment(sketch, "E7256", {"start": v(-255.4, 219.43) * mm, "end": v(-255.45, 221.37) * mm});
            skLineSegment(sketch, "E7257", {"start": v(-255.45, 221.37) * mm, "end": v(-255.54, 223.32) * mm});
            skLineSegment(sketch, "E7258", {"start": v(-255.54, 223.32) * mm, "end": v(-255.66, 225.27) * mm});
            skLineSegment(sketch, "E7259", {"start": v(-255.66, 225.27) * mm, "end": v(-255.8, 227.2) * mm});
            skLineSegment(sketch, "E7260", {"start": v(-255.8, 227.2) * mm, "end": v(-255.94, 229.08) * mm});
            skLineSegment(sketch, "E7261", {"start": v(-255.94, 229.08) * mm, "end": v(-256.07, 230.93) * mm});
            skLineSegment(sketch, "E7262", {"start": v(-256.07, 230.93) * mm, "end": v(-256.2, 232.71) * mm});
            skLineSegment(sketch, "E7263", {"start": v(-256.2, 232.71) * mm, "end": v(-256.3, 234.43) * mm});
            skLineSegment(sketch, "E7264", {"start": v(-256.3, 234.43) * mm, "end": v(-256.37, 236.05) * mm});
            skLineSegment(sketch, "E7265", {"start": v(-256.37, 236.05) * mm, "end": v(-256.4, 237.58) * mm});
            skLineSegment(sketch, "E7266", {"start": v(-256.4, 237.58) * mm, "end": v(-256.39, 239.43) * mm});
            skLineSegment(sketch, "E7267", {"start": v(-256.39, 239.43) * mm, "end": v(-256.37, 241.28) * mm});
            skLineSegment(sketch, "E7268", {"start": v(-256.37, 241.28) * mm, "end": v(-256.36, 243.12) * mm});
            skLineSegment(sketch, "E7269", {"start": v(-256.36, 243.12) * mm, "end": v(-256.33, 244.95) * mm});
            skLineSegment(sketch, "E7270", {"start": v(-256.33, 244.95) * mm, "end": v(-256.3, 246.78) * mm});
            skLineSegment(sketch, "E7271", {"start": v(-256.3, 246.78) * mm, "end": v(-256.27, 248.6) * mm});
            skLineSegment(sketch, "E7272", {"start": v(-256.27, 248.6) * mm, "end": v(-256.23, 250.42) * mm});
            skLineSegment(sketch, "E7273", {"start": v(-256.23, 250.42) * mm, "end": v(-256.2, 252.23) * mm});
            skLineSegment(sketch, "E7274", {"start": v(-256.2, 252.23) * mm, "end": v(-256.16, 254.03) * mm});
            skLineSegment(sketch, "E7275", {"start": v(-256.16, 254.03) * mm, "end": v(-256.13, 255.83) * mm});
            skLineSegment(sketch, "E7276", {"start": v(-256.13, 255.83) * mm, "end": v(-256.1, 257.62) * mm});
            skLineSegment(sketch, "E7277", {"start": v(-256.1, 257.62) * mm, "end": v(-256.06, 259.4) * mm});
            skLineSegment(sketch, "E7278", {"start": v(-256.06, 259.4) * mm, "end": v(-256.04, 261.18) * mm});
            skLineSegment(sketch, "E7279", {"start": v(-256.04, 261.18) * mm, "end": v(-256.02, 262.96) * mm});
            skLineSegment(sketch, "E7280", {"start": v(-256.02, 262.96) * mm, "end": v(-256, 264.73) * mm});
            skLineSegment(sketch, "E7281", {"start": v(-256, 264.73) * mm, "end": v(-256, 266.5) * mm});
            skLineSegment(sketch, "E7282", {"start": v(-256, 266.5) * mm, "end": v(-256, 268.25) * mm});
            skLineSegment(sketch, "E7283", {"start": v(-256, 268.25) * mm, "end": v(-256, 270) * mm});
            skLineSegment(sketch, "E7284", {"start": v(-256, 270) * mm, "end": v(-256.03, 271.76) * mm});
            skLineSegment(sketch, "E7285", {"start": v(-256.03, 271.76) * mm, "end": v(-256.07, 273.5) * mm});
            skLineSegment(sketch, "E7286", {"start": v(-256.07, 273.5) * mm, "end": v(-256.11, 275.25) * mm});
            skLineSegment(sketch, "E7287", {"start": v(-256.11, 275.25) * mm, "end": v(-256.18, 276.98) * mm});
            skLineSegment(sketch, "E7288", {"start": v(-256.18, 276.98) * mm, "end": v(-256.25, 278.72) * mm});
            skLineSegment(sketch, "E7289", {"start": v(-256.25, 278.72) * mm, "end": v(-256.35, 280.45) * mm});
            skLineSegment(sketch, "E7290", {"start": v(-256.35, 280.45) * mm, "end": v(-256.46, 282.17) * mm});
            skLineSegment(sketch, "E7291", {"start": v(-256.46, 282.17) * mm, "end": v(-256.59, 283.9) * mm});
            skLineSegment(sketch, "E7292", {"start": v(-256.59, 283.9) * mm, "end": v(-256.74, 285.6) * mm});
            skLineSegment(sketch, "E7293", {"start": v(-256.74, 285.6) * mm, "end": v(-256.9, 287.32) * mm});
            skLineSegment(sketch, "E7294", {"start": v(-256.9, 287.32) * mm, "end": v(-257.1, 289.03) * mm});
            skLineSegment(sketch, "E7295", {"start": v(-257.1, 289.03) * mm, "end": v(-257.32, 290.74) * mm});
            skLineSegment(sketch, "E7296", {"start": v(-257.32, 290.74) * mm, "end": v(-257.56, 292.44) * mm});
            skLineSegment(sketch, "E7297", {"start": v(-257.56, 292.44) * mm, "end": v(-257.82, 294.14) * mm});
            skLineSegment(sketch, "E7298", {"start": v(-257.82, 294.14) * mm, "end": v(-258.11, 295.84) * mm});
            skLineSegment(sketch, "E7299", {"start": v(-258.11, 295.84) * mm, "end": v(-258.43, 297.53) * mm});
            skLineSegment(sketch, "E7300", {"start": v(-258.43, 297.53) * mm, "end": v(-258.78, 299.22) * mm});
            skLineSegment(sketch, "E7301", {"start": v(-258.78, 299.22) * mm, "end": v(-259.15, 300.91) * mm});
            skLineSegment(sketch, "E7302", {"start": v(-259.15, 300.91) * mm, "end": v(-259.56, 302.6) * mm});
            skLineSegment(sketch, "E7303", {"start": v(-259.56, 302.6) * mm, "end": v(-260, 304.28) * mm});
            skLineSegment(sketch, "E7304", {"start": v(-260, 304.28) * mm, "end": v(-260.47, 305.96) * mm});
            skLineSegment(sketch, "E7305", {"start": v(-260.47, 305.96) * mm, "end": v(-260.98, 307.64) * mm});
            skLineSegment(sketch, "E7306", {"start": v(-260.98, 307.64) * mm, "end": v(-261.52, 309.32) * mm});
            skLineSegment(sketch, "E7307", {"start": v(-261.52, 309.32) * mm, "end": v(-262.1, 311) * mm});
            skLineSegment(sketch, "E7308", {"start": v(-262.1, 311) * mm, "end": v(-262.71, 312.66) * mm});
            skLineSegment(sketch, "E7309", {"start": v(-262.71, 312.66) * mm, "end": v(-263.37, 314.34) * mm});
            skLineSegment(sketch, "E7310", {"start": v(-263.37, 314.34) * mm, "end": v(-264.06, 316) * mm});
            skLineSegment(sketch, "E7311", {"start": v(-264.06, 316) * mm, "end": v(-264.8, 317.67) * mm});
            skLineSegment(sketch, "E7312", {"start": v(-264.8, 317.67) * mm, "end": v(-265.57, 319.34) * mm});
            skLineSegment(sketch, "E7313", {"start": v(-265.57, 319.34) * mm, "end": v(-266.4, 321) * mm});
            skLineSegment(sketch, "E7314", {"start": v(-266.4, 321) * mm, "end": v(-267.25, 322.67) * mm});
            skLineSegment(sketch, "E7315", {"start": v(-267.25, 322.67) * mm, "end": v(-153.2, 322.67) * mm});
            skLineSegment(sketch, "E7316", {"start": v(-153.2, 322.67) * mm, "end": v(-154.22, 321.07) * mm});
            skLineSegment(sketch, "E7317", {"start": v(-154.22, 321.07) * mm, "end": v(-155.18, 319.47) * mm});
            skLineSegment(sketch, "E7318", {"start": v(-155.18, 319.47) * mm, "end": v(-156.08, 317.87) * mm});
            skLineSegment(sketch, "E7319", {"start": v(-156.08, 317.87) * mm, "end": v(-156.92, 316.25) * mm});
            skLineSegment(sketch, "E7320", {"start": v(-156.92, 316.25) * mm, "end": v(-157.7, 314.63) * mm});
            skLineSegment(sketch, "E7321", {"start": v(-157.7, 314.63) * mm, "end": v(-158.44, 313) * mm});
            skLineSegment(sketch, "E7322", {"start": v(-158.44, 313) * mm, "end": v(-159.12, 311.37) * mm});
            skLineSegment(sketch, "E7323", {"start": v(-159.12, 311.37) * mm, "end": v(-159.75, 309.72) * mm});
            skLineSegment(sketch, "E7324", {"start": v(-159.75, 309.72) * mm, "end": v(-160.33, 308.08) * mm});
            skLineSegment(sketch, "E7325", {"start": v(-160.33, 308.08) * mm, "end": v(-160.86, 306.42) * mm});
            skLineSegment(sketch, "E7326", {"start": v(-160.86, 306.42) * mm, "end": v(-161.35, 304.76) * mm});
            skLineSegment(sketch, "E7327", {"start": v(-161.35, 304.76) * mm, "end": v(-161.8, 303.09) * mm});
            skLineSegment(sketch, "E7328", {"start": v(-161.8, 303.09) * mm, "end": v(-162.2, 301.41) * mm});
            skLineSegment(sketch, "E7329", {"start": v(-162.2, 301.41) * mm, "end": v(-162.56, 299.73) * mm});
            skLineSegment(sketch, "E7330", {"start": v(-162.56, 299.73) * mm, "end": v(-162.89, 298.04) * mm});
            skLineSegment(sketch, "E7331", {"start": v(-162.89, 298.04) * mm, "end": v(-163.18, 296.34) * mm});
            skLineSegment(sketch, "E7332", {"start": v(-163.18, 296.34) * mm, "end": v(-163.43, 294.64) * mm});
            skLineSegment(sketch, "E7333", {"start": v(-163.43, 294.64) * mm, "end": v(-163.66, 292.94) * mm});
            skLineSegment(sketch, "E7334", {"start": v(-163.66, 292.94) * mm, "end": v(-163.85, 291.22) * mm});
            skLineSegment(sketch, "E7335", {"start": v(-163.85, 291.22) * mm, "end": v(-164.01, 289.5) * mm});
            skLineSegment(sketch, "E7336", {"start": v(-164.01, 289.5) * mm, "end": v(-164.15, 287.78) * mm});
            skLineSegment(sketch, "E7337", {"start": v(-164.15, 287.78) * mm, "end": v(-164.27, 286.04) * mm});
            skLineSegment(sketch, "E7338", {"start": v(-164.27, 286.04) * mm, "end": v(-164.36, 284.3) * mm});
            skLineSegment(sketch, "E7339", {"start": v(-164.36, 284.3) * mm, "end": v(-164.42, 282.56) * mm});
            skLineSegment(sketch, "E7340", {"start": v(-164.42, 282.56) * mm, "end": v(-164.47, 280.81) * mm});
            skLineSegment(sketch, "E7341", {"start": v(-164.47, 280.81) * mm, "end": v(-164.5, 279.06) * mm});
            skLineSegment(sketch, "E7342", {"start": v(-164.5, 279.06) * mm, "end": v(-164.52, 277.3) * mm});
            skLineSegment(sketch, "E7343", {"start": v(-164.52, 277.3) * mm, "end": v(-164.52, 275.53) * mm});
            skLineSegment(sketch, "E7344", {"start": v(-164.52, 275.53) * mm, "end": v(-164.5, 273.76) * mm});
            skLineSegment(sketch, "E7345", {"start": v(-164.5, 273.76) * mm, "end": v(-164.49, 271.98) * mm});
            skLineSegment(sketch, "E7346", {"start": v(-164.49, 271.98) * mm, "end": v(-164.46, 270.2) * mm});
            skLineSegment(sketch, "E7347", {"start": v(-164.46, 270.2) * mm, "end": v(-164.42, 268.4) * mm});
            skLineSegment(sketch, "E7348", {"start": v(-164.42, 268.4) * mm, "end": v(-164.38, 266.62) * mm});
            skLineSegment(sketch, "E7349", {"start": v(-164.38, 266.62) * mm, "end": v(-164.33, 264.82) * mm});
            skLineSegment(sketch, "E7350", {"start": v(-164.33, 264.82) * mm, "end": v(-164.28, 263.01) * mm});
            skLineSegment(sketch, "E7351", {"start": v(-164.28, 263.01) * mm, "end": v(-164.24, 261.2) * mm});
            skLineSegment(sketch, "E7352", {"start": v(-164.24, 261.2) * mm, "end": v(-164.2, 259.4) * mm});
            skLineSegment(sketch, "E7353", {"start": v(-164.2, 259.4) * mm, "end": v(-164.15, 257.57) * mm});
            skLineSegment(sketch, "E7354", {"start": v(-164.15, 257.57) * mm, "end": v(-164.12, 255.75) * mm});
            skLineSegment(sketch, "E7355", {"start": v(-164.12, 255.75) * mm, "end": v(-164.09, 253.92) * mm});
            skLineSegment(sketch, "E7356", {"start": v(-164.09, 253.92) * mm, "end": v(-164.07, 252.1) * mm});
            skLineSegment(sketch, "E7357", {"start": v(-164.07, 252.1) * mm, "end": v(-164.06, 250.25) * mm});
            skLineSegment(sketch, "E7358", {"start": v(-164.06, 250.25) * mm, "end": v(-164.06, 110.86) * mm});
            skLineSegment(sketch, "E7359", {"start": v(-164.06, 110.86) * mm, "end": v(-164.07, 109.1) * mm});
            skLineSegment(sketch, "E7360", {"start": v(-164.07, 109.1) * mm, "end": v(-164.1, 107.33) * mm});
            skLineSegment(sketch, "E7361", {"start": v(-164.1, 107.33) * mm, "end": v(-164.13, 105.56) * mm});
            skLineSegment(sketch, "E7362", {"start": v(-164.13, 105.56) * mm, "end": v(-164.17, 103.79) * mm});
            skLineSegment(sketch, "E7363", {"start": v(-164.17, 103.79) * mm, "end": v(-164.22, 102.02) * mm});
            skLineSegment(sketch, "E7364", {"start": v(-164.22, 102.02) * mm, "end": v(-164.28, 100.25) * mm});
            skLineSegment(sketch, "E7365", {"start": v(-164.28, 100.25) * mm, "end": v(-164.34, 98.48) * mm});
            skLineSegment(sketch, "E7366", {"start": v(-164.34, 98.48) * mm, "end": v(-164.4, 96.72) * mm});
            skLineSegment(sketch, "E7367", {"start": v(-164.4, 96.72) * mm, "end": v(-164.46, 94.95) * mm});
            skLineSegment(sketch, "E7368", {"start": v(-164.46, 94.95) * mm, "end": v(-164.52, 93.2) * mm});
            skLineSegment(sketch, "E7369", {"start": v(-164.52, 93.2) * mm, "end": v(-164.57, 91.43) * mm});
            skLineSegment(sketch, "E7370", {"start": v(-164.57, 91.43) * mm, "end": v(-164.61, 89.68) * mm});
            skLineSegment(sketch, "E7371", {"start": v(-164.61, 89.68) * mm, "end": v(-164.65, 87.92) * mm});
            skLineSegment(sketch, "E7372", {"start": v(-164.65, 87.92) * mm, "end": v(-164.67, 86.17) * mm});
            skLineSegment(sketch, "E7373", {"start": v(-164.67, 86.17) * mm, "end": v(-164.68, 84.43) * mm});
            skLineSegment(sketch, "E7374", {"start": v(-164.68, 84.43) * mm, "end": v(-164.68, 82.69) * mm});
            skLineSegment(sketch, "E7375", {"start": v(-164.68, 82.69) * mm, "end": v(-164.66, 80.95) * mm});
            skLineSegment(sketch, "E7376", {"start": v(-164.66, 80.95) * mm, "end": v(-164.61, 79.22) * mm});
            skLineSegment(sketch, "E7377", {"start": v(-164.61, 79.22) * mm, "end": v(-164.55, 77.5) * mm});
            skLineSegment(sketch, "E7378", {"start": v(-164.55, 77.5) * mm, "end": v(-164.46, 75.79) * mm});
            skLineSegment(sketch, "E7379", {"start": v(-164.46, 75.79) * mm, "end": v(-164.34, 74.08) * mm});
            skLineSegment(sketch, "E7380", {"start": v(-164.34, 74.08) * mm, "end": v(-164.2, 72.37) * mm});
            skLineSegment(sketch, "E7381", {"start": v(-164.2, 72.37) * mm, "end": v(-164.02, 70.68) * mm});
            skLineSegment(sketch, "E7382", {"start": v(-164.02, 70.68) * mm, "end": v(-163.81, 69) * mm});
            skLineSegment(sketch, "E7383", {"start": v(-163.81, 69) * mm, "end": v(-163.57, 67.32) * mm});
            skLineSegment(sketch, "E7384", {"start": v(-163.57, 67.32) * mm, "end": v(-163.3, 65.65) * mm});
            skLineSegment(sketch, "E7385", {"start": v(-163.3, 65.65) * mm, "end": v(-162.97, 64) * mm});
            skLineSegment(sketch, "E7386", {"start": v(-162.97, 64) * mm, "end": v(-162.61, 62.35) * mm});
            skLineSegment(sketch, "E7387", {"start": v(-162.61, 62.35) * mm, "end": v(-162.2, 60.71) * mm});
            skLineSegment(sketch, "E7388", {"start": v(-162.2, 60.71) * mm, "end": v(-161.76, 59.09) * mm});
            skLineSegment(sketch, "E7389", {"start": v(-161.76, 59.09) * mm, "end": v(-161.26, 57.47) * mm});
            skLineSegment(sketch, "E7390", {"start": v(-161.26, 57.47) * mm, "end": v(-160.71, 55.87) * mm});
            skLineSegment(sketch, "E7391", {"start": v(-160.71, 55.87) * mm, "end": v(-160.12, 54.28) * mm});
            skLineSegment(sketch, "E7392", {"start": v(-160.12, 54.28) * mm, "end": v(-159.46, 52.7) * mm});
            skLineSegment(sketch, "E7393", {"start": v(-159.46, 52.7) * mm, "end": v(-158.75, 51.14) * mm});
            skLineSegment(sketch, "E7394", {"start": v(-158.75, 51.14) * mm, "end": v(-157.99, 49.6) * mm});
            skLineSegment(sketch, "E7395", {"start": v(-157.99, 49.6) * mm, "end": v(-157.16, 48.06) * mm});
            skLineSegment(sketch, "E7396", {"start": v(-157.16, 48.06) * mm, "end": v(-156.27, 46.54) * mm});
            skLineSegment(sketch, "E7397", {"start": v(-156.27, 46.54) * mm, "end": v(-155.31, 45.03) * mm});
            skLineSegment(sketch, "E7398", {"start": v(-155.31, 45.03) * mm, "end": v(-154.3, 43.54) * mm});
            skLineSegment(sketch, "E7399", {"start": v(-154.3, 43.54) * mm, "end": v(-153.2, 42.07) * mm});
            skLineSegment(sketch, "E7400", {"start": v(-153.2, 42.07) * mm, "end": v(-267.25, 42.07) * mm});
            skLineSegment(sketch, "E7401", {"start": v(-267.25, 42.07) * mm, "end": v(-266.1, 43.83) * mm});
            skLineSegment(sketch, "E7402", {"start": v(-266.1, 43.83) * mm, "end": v(-265.03, 45.56) * mm});
            skLineSegment(sketch, "E7403", {"start": v(-265.03, 45.56) * mm, "end": v(-264.05, 47.27) * mm});
            skLineSegment(sketch, "E7404", {"start": v(-264.05, 47.27) * mm, "end": v(-263.14, 48.97) * mm});
            skLineSegment(sketch, "E7405", {"start": v(-263.14, 48.97) * mm, "end": v(-262.3, 50.64) * mm});
            skLineSegment(sketch, "E7406", {"start": v(-262.3, 50.64) * mm, "end": v(-261.54, 52.3) * mm});
            skLineSegment(sketch, "E7407", {"start": v(-261.54, 52.3) * mm, "end": v(-260.85, 53.96) * mm});
            skLineSegment(sketch, "E7408", {"start": v(-260.85, 53.96) * mm, "end": v(-260.22, 55.6) * mm});
            skLineSegment(sketch, "E7409", {"start": v(-260.22, 55.6) * mm, "end": v(-259.65, 57.24) * mm});
            skLineSegment(sketch, "E7410", {"start": v(-259.65, 57.24) * mm, "end": v(-259.15, 58.87) * mm});
            skLineSegment(sketch, "E7411", {"start": v(-259.15, 58.87) * mm, "end": v(-258.7, 60.5) * mm});
            skLineSegment(sketch, "E7412", {"start": v(-258.7, 60.5) * mm, "end": v(-258.3, 62.14) * mm});
            skLineSegment(sketch, "E7413", {"start": v(-258.3, 62.14) * mm, "end": v(-257.94, 63.79) * mm});
            skLineSegment(sketch, "E7414", {"start": v(-257.94, 63.79) * mm, "end": v(-257.64, 65.44) * mm});
            skLineSegment(sketch, "E7415", {"start": v(-257.64, 65.44) * mm, "end": v(-257.38, 67.1) * mm});
            skLineSegment(sketch, "E7416", {"start": v(-257.38, 67.1) * mm, "end": v(-257.15, 68.77) * mm});
            skLineSegment(sketch, "E7417", {"start": v(-257.15, 68.77) * mm, "end": v(-256.97, 70.46) * mm});
            skLineSegment(sketch, "E7418", {"start": v(-256.97, 70.46) * mm, "end": v(-256.81, 72.17) * mm});
            skLineSegment(sketch, "E7419", {"start": v(-256.81, 72.17) * mm, "end": v(-256.7, 73.9) * mm});
            skLineSegment(sketch, "E7420", {"start": v(-256.7, 73.9) * mm, "end": v(-256.6, 75.66) * mm});
            skLineSegment(sketch, "E7421", {"start": v(-256.6, 75.66) * mm, "end": v(-256.52, 77.45) * mm});
            skLineSegment(sketch, "E7422", {"start": v(-256.52, 77.45) * mm, "end": v(-256.47, 79.26) * mm});
            skLineSegment(sketch, "E7423", {"start": v(-256.47, 79.26) * mm, "end": v(-256.43, 81.11) * mm});
            skLineSegment(sketch, "E7424", {"start": v(-256.43, 81.11) * mm, "end": v(-256.4, 83) * mm});
            skLineSegment(sketch, "E7425", {"start": v(-256.4, 83) * mm, "end": v(-256.4, 84.92) * mm});
            skLineSegment(sketch, "E7426", {"start": v(-256.4, 84.92) * mm, "end": v(-256.4, 86.88) * mm});
            skLineSegment(sketch, "E7427", {"start": v(-256.4, 86.88) * mm, "end": v(-256.4, 88.89) * mm});
            skLineSegment(sketch, "E7428", {"start": v(-256.4, 88.89) * mm, "end": v(-256.4, 90.94) * mm});
            skLineSegment(sketch, "E7429", {"start": v(-256.4, 90.94) * mm, "end": v(-256.4, 139.82) * mm});
            skLineSegment(sketch, "E7430", {"start": v(-256.4, 139.82) * mm, "end": v(-256.36, 141.4) * mm});
            skLineSegment(sketch, "E7431", {"start": v(-256.36, 141.4) * mm, "end": v(-256.28, 143.1) * mm});
            skLineSegment(sketch, "E7432", {"start": v(-256.28, 143.1) * mm, "end": v(-256.18, 144.9) * mm});
            skLineSegment(sketch, "E7433", {"start": v(-256.18, 144.9) * mm, "end": v(-256.1, 146.76) * mm});
            skLineSegment(sketch, "E7434", {"start": v(-256.1, 146.76) * mm, "end": v(-256.04, 148.65) * mm});
            skLineSegment(sketch, "E7435", {"start": v(-256.04, 148.65) * mm, "end": v(-256.07, 150.54) * mm});
            skLineSegment(sketch, "E7436", {"start": v(-256.07, 150.54) * mm, "end": v(-256.19, 152.39) * mm});
            skLineSegment(sketch, "E7437", {"start": v(-256.19, 152.39) * mm, "end": v(-256.44, 154.17) * mm});
            skLineSegment(sketch, "E7438", {"start": v(-256.44, 154.17) * mm, "end": v(-256.85, 155.86) * mm});
            skLineSegment(sketch, "E7439", {"start": v(-256.85, 155.86) * mm, "end": v(-257.44, 157.41) * mm});
            skLineSegment(sketch, "E7440", {"start": v(-257.44, 157.41) * mm, "end": v(-258.25, 158.8) * mm});
            skLineSegment(sketch, "E7441", {"start": v(-258.25, 158.8) * mm, "end": v(-259.4, 160.1) * mm});
            skLineSegment(sketch, "E7442", {"start": v(-259.4, 160.1) * mm, "end": v(-260.74, 161.13) * mm});
            skLineSegment(sketch, "E7443", {"start": v(-260.74, 161.13) * mm, "end": v(-262.26, 161.92) * mm});
            skLineSegment(sketch, "E7444", {"start": v(-262.26, 161.92) * mm, "end": v(-263.91, 162.5) * mm});
            skLineSegment(sketch, "E7445", {"start": v(-263.91, 162.5) * mm, "end": v(-265.67, 162.9) * mm});
            skLineSegment(sketch, "E7446", {"start": v(-265.67, 162.9) * mm, "end": v(-267.48, 163.16) * mm});
            skLineSegment(sketch, "E7447", {"start": v(-267.48, 163.16) * mm, "end": v(-269.33, 163.3) * mm});
            skLineSegment(sketch, "E7448", {"start": v(-269.33, 163.3) * mm, "end": v(-271.17, 163.37) * mm});
            skLineSegment(sketch, "E7449", {"start": v(-271.17, 163.37) * mm, "end": v(-272.97, 163.38) * mm});
            skLineSegment(sketch, "E7450", {"start": v(-272.97, 163.38) * mm, "end": v(-274.7, 163.36) * mm});
            skLineSegment(sketch, "E7451", {"start": v(-274.7, 163.36) * mm, "end": v(-276.3, 163.36) * mm});
            skLineSegment(sketch, "E7452", {"start": v(-276.3, 163.36) * mm, "end": v(-278.12, 163.36) * mm});
            skLineSegment(sketch, "E7453", {"start": v(-278.12, 163.36) * mm, "end": v(-279.93, 163.37) * mm});
            skLineSegment(sketch, "E7454", {"start": v(-279.93, 163.37) * mm, "end": v(-281.74, 163.38) * mm});
            skLineSegment(sketch, "E7455", {"start": v(-281.74, 163.38) * mm, "end": v(-283.55, 163.38) * mm});
            skLineSegment(sketch, "E7456", {"start": v(-283.55, 163.38) * mm, "end": v(-285.36, 163.39) * mm});
            skLineSegment(sketch, "E7457", {"start": v(-285.36, 163.39) * mm, "end": v(-287.17, 163.4) * mm});
            skLineSegment(sketch, "E7458", {"start": v(-287.17, 163.4) * mm, "end": v(-288.98, 163.4) * mm});
            skLineSegment(sketch, "E7459", {"start": v(-288.98, 163.4) * mm, "end": v(-290.79, 163.4) * mm});
            skLineSegment(sketch, "E7460", {"start": v(-290.79, 163.4) * mm, "end": v(-292.6, 163.4) * mm});
            skLineSegment(sketch, "E7461", {"start": v(-292.6, 163.4) * mm, "end": v(-294.4, 163.4) * mm});
            skLineSegment(sketch, "E7462", {"start": v(-294.4, 163.4) * mm, "end": v(-296.22, 163.4) * mm});
            skLineSegment(sketch, "E7463", {"start": v(-296.22, 163.4) * mm, "end": v(-298.03, 163.4) * mm});
            skLineSegment(sketch, "E7464", {"start": v(-298.03, 163.4) * mm, "end": v(-299.84, 163.4) * mm});
            skLineSegment(sketch, "E7465", {"start": v(-299.84, 163.4) * mm, "end": v(-301.65, 163.4) * mm});
            skLineSegment(sketch, "E7466", {"start": v(-301.65, 163.4) * mm, "end": v(-303.46, 163.4) * mm});
            skLineSegment(sketch, "E7467", {"start": v(-303.46, 163.4) * mm, "end": v(-305.27, 163.4) * mm});
            skLineSegment(sketch, "E7468", {"start": v(-305.27, 163.4) * mm, "end": v(-307.08, 163.39) * mm});
            skLineSegment(sketch, "E7469", {"start": v(-307.08, 163.39) * mm, "end": v(-308.9, 163.39) * mm});
            skLineSegment(sketch, "E7470", {"start": v(-308.9, 163.39) * mm, "end": v(-310.7, 163.38) * mm});
            skLineSegment(sketch, "E7471", {"start": v(-310.7, 163.38) * mm, "end": v(-312.51, 163.38) * mm});
            skLineSegment(sketch, "E7472", {"start": v(-312.51, 163.38) * mm, "end": v(-314.32, 163.38) * mm});
            skLineSegment(sketch, "E7473", {"start": v(-314.32, 163.38) * mm, "end": v(-316.13, 163.37) * mm});
            skLineSegment(sketch, "E7474", {"start": v(-316.13, 163.37) * mm, "end": v(-317.94, 163.37) * mm});
            skLineSegment(sketch, "E7475", {"start": v(-317.94, 163.37) * mm, "end": v(-319.75, 163.37) * mm});
            skLineSegment(sketch, "E7476", {"start": v(-319.75, 163.37) * mm, "end": v(-321.56, 163.36) * mm});
            skLineSegment(sketch, "E7477", {"start": v(-321.56, 163.36) * mm, "end": v(-323.37, 163.36) * mm});
            skLineSegment(sketch, "E7478", {"start": v(-323.37, 163.36) * mm, "end": v(-325.18, 163.36) * mm});
            skLineSegment(sketch, "E7479", {"start": v(-325.18, 163.36) * mm, "end": v(-326.77, 163.37) * mm});
            skLineSegment(sketch, "E7480", {"start": v(-326.77, 163.37) * mm, "end": v(-328.48, 163.41) * mm});
            skLineSegment(sketch, "E7481", {"start": v(-328.48, 163.41) * mm, "end": v(-330.27, 163.44) * mm});
            skLineSegment(sketch, "E7482", {"start": v(-330.27, 163.44) * mm, "end": v(-332.12, 163.44) * mm});
            skLineSegment(sketch, "E7483", {"start": v(-332.12, 163.44) * mm, "end": v(-334, 163.37) * mm});
            skLineSegment(sketch, "E7484", {"start": v(-334, 163.37) * mm, "end": v(-335.86, 163.21) * mm});
            skLineSegment(sketch, "E7485", {"start": v(-335.86, 163.21) * mm, "end": v(-337.69, 162.94) * mm});
            skLineSegment(sketch, "E7486", {"start": v(-337.69, 162.94) * mm, "end": v(-339.44, 162.51) * mm});
            skLineSegment(sketch, "E7487", {"start": v(-339.44, 162.51) * mm, "end": v(-341.08, 161.92) * mm});
            skLineSegment(sketch, "E7488", {"start": v(-341.08, 161.92) * mm, "end": v(-342.58, 161.12) * mm});
            skLineSegment(sketch, "E7489", {"start": v(-342.58, 161.12) * mm, "end": v(-343.92, 160.1) * mm});
            skLineSegment(sketch, "E7490", {"start": v(-343.92, 160.1) * mm, "end": v(-345.05, 158.8) * mm});
            skLineSegment(sketch, "E7491", {"start": v(-345.05, 158.8) * mm, "end": v(-345.8, 157.56) * mm});
            skLineSegment(sketch, "E7492", {"start": v(-345.8, 157.56) * mm, "end": v(-346.42, 156.16) * mm});
            skLineSegment(sketch, "E7493", {"start": v(-346.42, 156.16) * mm, "end": v(-346.92, 154.61) * mm});
            skLineSegment(sketch, "E7494", {"start": v(-346.92, 154.61) * mm, "end": v(-347.3, 152.95) * mm});
            skLineSegment(sketch, "E7495", {"start": v(-347.3, 152.95) * mm, "end": v(-347.56, 151.18) * mm});
            skLineSegment(sketch, "E7496", {"start": v(-347.56, 151.18) * mm, "end": v(-347.74, 149.33) * mm});
            skLineSegment(sketch, "E7497", {"start": v(-347.74, 149.33) * mm, "end": v(-347.84, 147.41) * mm});
            skLineSegment(sketch, "E7498", {"start": v(-347.84, 147.41) * mm, "end": v(-347.87, 145.45) * mm});
            skLineSegment(sketch, "E7499", {"start": v(-347.87, 145.45) * mm, "end": v(-347.85, 143.45) * mm});
            skLineSegment(sketch, "E7500", {"start": v(-347.85, 143.45) * mm, "end": v(-347.77, 141.45) * mm});
            skLineSegment(sketch, "E7501", {"start": v(-347.77, 141.45) * mm, "end": v(-347.66, 139.44) * mm});
            skLineSegment(sketch, "E7502", {"start": v(-347.66, 139.44) * mm, "end": v(-347.53, 137.47) * mm});
            skLineSegment(sketch, "E7503", {"start": v(-347.53, 137.47) * mm, "end": v(-347.39, 135.54) * mm});
            skLineSegment(sketch, "E7504", {"start": v(-347.39, 135.54) * mm, "end": v(-347.25, 133.66) * mm});
            skLineSegment(sketch, "E7505", {"start": v(-347.25, 133.66) * mm, "end": v(-347.12, 131.87) * mm});
            skLineSegment(sketch, "E7506", {"start": v(-347.12, 131.87) * mm, "end": v(-347, 130.18) * mm});
            skLineSegment(sketch, "E7507", {"start": v(-347, 130.18) * mm, "end": v(-346.93, 128.6) * mm});
            skLineSegment(sketch, "E7508", {"start": v(-346.93, 128.6) * mm, "end": v(-346.9, 127.15) * mm});
            skLineSegment(sketch, "E7509", {"start": v(-346.9, 127.15) * mm, "end": v(-346.91, 125.42) * mm});
            skLineSegment(sketch, "E7510", {"start": v(-346.91, 125.42) * mm, "end": v(-346.93, 123.69) * mm});
            skLineSegment(sketch, "E7511", {"start": v(-346.93, 123.69) * mm, "end": v(-346.96, 121.95) * mm});
            skLineSegment(sketch, "E7512", {"start": v(-346.96, 121.95) * mm, "end": v(-347, 120.2) * mm});
            skLineSegment(sketch, "E7513", {"start": v(-347, 120.2) * mm, "end": v(-347.05, 118.45) * mm});
            skLineSegment(sketch, "E7514", {"start": v(-347.05, 118.45) * mm, "end": v(-347.1, 116.7) * mm});
            skLineSegment(sketch, "E7515", {"start": v(-347.1, 116.7) * mm, "end": v(-347.17, 114.93) * mm});
            skLineSegment(sketch, "E7516", {"start": v(-347.17, 114.93) * mm, "end": v(-347.23, 113.17) * mm});
            skLineSegment(sketch, "E7517", {"start": v(-347.23, 113.17) * mm, "end": v(-347.3, 111.4) * mm});
            skLineSegment(sketch, "E7518", {"start": v(-347.3, 111.4) * mm, "end": v(-347.37, 109.63) * mm});
            skLineSegment(sketch, "E7519", {"start": v(-347.37, 109.63) * mm, "end": v(-347.44, 107.86) * mm});
            skLineSegment(sketch, "E7520", {"start": v(-347.44, 107.86) * mm, "end": v(-347.51, 106.08) * mm});
            skLineSegment(sketch, "E7521", {"start": v(-347.51, 106.08) * mm, "end": v(-347.58, 104.3) * mm});
            skLineSegment(sketch, "E7522", {"start": v(-347.58, 104.3) * mm, "end": v(-347.64, 102.53) * mm});
            skLineSegment(sketch, "E7523", {"start": v(-347.64, 102.53) * mm, "end": v(-347.7, 100.75) * mm});
            skLineSegment(sketch, "E7524", {"start": v(-347.7, 100.75) * mm, "end": v(-347.75, 98.98) * mm});
            skLineSegment(sketch, "E7525", {"start": v(-347.75, 98.98) * mm, "end": v(-347.8, 97.2) * mm});
            skLineSegment(sketch, "E7526", {"start": v(-347.8, 97.2) * mm, "end": v(-347.83, 95.42) * mm});
            skLineSegment(sketch, "E7527", {"start": v(-347.83, 95.42) * mm, "end": v(-347.85, 93.65) * mm});
            skLineSegment(sketch, "E7528", {"start": v(-347.85, 93.65) * mm, "end": v(-347.86, 91.88) * mm});
            skLineSegment(sketch, "E7529", {"start": v(-347.86, 91.88) * mm, "end": v(-347.86, 90.1) * mm});
            skLineSegment(sketch, "E7530", {"start": v(-347.86, 90.1) * mm, "end": v(-347.85, 88.34) * mm});
            skLineSegment(sketch, "E7531", {"start": v(-347.85, 88.34) * mm, "end": v(-347.82, 86.58) * mm});
            skLineSegment(sketch, "E7532", {"start": v(-347.82, 86.58) * mm, "end": v(-347.77, 84.82) * mm});
            skLineSegment(sketch, "E7533", {"start": v(-347.77, 84.82) * mm, "end": v(-347.7, 83.07) * mm});
            skLineSegment(sketch, "E7534", {"start": v(-347.7, 83.07) * mm, "end": v(-347.61, 81.32) * mm});
            skLineSegment(sketch, "E7535", {"start": v(-347.61, 81.32) * mm, "end": v(-347.5, 79.57) * mm});
            skLineSegment(sketch, "E7536", {"start": v(-347.5, 79.57) * mm, "end": v(-347.37, 77.83) * mm});
            skLineSegment(sketch, "E7537", {"start": v(-347.37, 77.83) * mm, "end": v(-347.22, 76.1) * mm});
            skLineSegment(sketch, "E7538", {"start": v(-347.22, 76.1) * mm, "end": v(-347.04, 74.38) * mm});
            skLineSegment(sketch, "E7539", {"start": v(-347.04, 74.38) * mm, "end": v(-346.83, 72.66) * mm});
            skLineSegment(sketch, "E7540", {"start": v(-346.83, 72.66) * mm, "end": v(-346.6, 70.95) * mm});
            skLineSegment(sketch, "E7541", {"start": v(-346.6, 70.95) * mm, "end": v(-346.33, 69.25) * mm});
            skLineSegment(sketch, "E7542", {"start": v(-346.33, 69.25) * mm, "end": v(-346.04, 67.55) * mm});
            skLineSegment(sketch, "E7543", {"start": v(-346.04, 67.55) * mm, "end": v(-345.7, 65.87) * mm});
            skLineSegment(sketch, "E7544", {"start": v(-345.7, 65.87) * mm, "end": v(-345.35, 64.2) * mm});
            skLineSegment(sketch, "E7545", {"start": v(-345.35, 64.2) * mm, "end": v(-344.95, 62.53) * mm});
            skLineSegment(sketch, "E7546", {"start": v(-344.95, 62.53) * mm, "end": v(-344.52, 60.88) * mm});
            skLineSegment(sketch, "E7547", {"start": v(-344.52, 60.88) * mm, "end": v(-344.05, 59.24) * mm});
            skLineSegment(sketch, "E7548", {"start": v(-344.05, 59.24) * mm, "end": v(-343.55, 57.61) * mm});
            skLineSegment(sketch, "E7549", {"start": v(-343.55, 57.61) * mm, "end": v(-343, 56) * mm});
            skLineSegment(sketch, "E7550", {"start": v(-343, 56) * mm, "end": v(-342.41, 54.39) * mm});
            skLineSegment(sketch, "E7551", {"start": v(-342.41, 54.39) * mm, "end": v(-341.78, 52.8) * mm});
            skLineSegment(sketch, "E7552", {"start": v(-341.78, 52.8) * mm, "end": v(-341.1, 51.22) * mm});
            skLineSegment(sketch, "E7553", {"start": v(-341.1, 51.22) * mm, "end": v(-340.38, 49.66) * mm});
            skLineSegment(sketch, "E7554", {"start": v(-340.38, 49.66) * mm, "end": v(-339.61, 48.1) * mm});
            skLineSegment(sketch, "E7555", {"start": v(-339.61, 48.1) * mm, "end": v(-338.8, 46.57) * mm});
            skLineSegment(sketch, "E7556", {"start": v(-338.8, 46.57) * mm, "end": v(-337.93, 45.05) * mm});
            skLineSegment(sketch, "E7557", {"start": v(-337.93, 45.05) * mm, "end": v(-337.01, 43.55) * mm});
            skLineSegment(sketch, "E7558", {"start": v(-337.01, 43.55) * mm, "end": v(-336.05, 42.07) * mm});
            skLineSegment(sketch, "E7559", {"start": v(-336.05, 42.07) * mm, "end": v(-448.29, 42.07) * mm});
            skLineSegment(sketch, "E7560", {"start": v(-448.29, 42.07) * mm, "end": v(-437.42, 56.55) * mm});
            skLineSegment(sketch, "E7561", {"start": v(-437.42, 56.55) * mm, "end": v(-437.42, 58.36) * mm});
            skLineSegment(sketch, "E7562", {"start": v(-437.42, 58.36) * mm, "end": v(-438.54, 59.39) * mm});
            skLineSegment(sketch, "E7563", {"start": v(-438.54, 59.39) * mm, "end": v(-439.69, 60.39) * mm});
            skLineSegment(sketch, "E7564", {"start": v(-439.69, 60.39) * mm, "end": v(-440.87, 61.36) * mm});
            skLineSegment(sketch, "E7565", {"start": v(-440.87, 61.36) * mm, "end": v(-442.08, 62.3) * mm});
            skLineSegment(sketch, "E7566", {"start": v(-442.08, 62.3) * mm, "end": v(-443.32, 63.2) * mm});
            skLineSegment(sketch, "E7567", {"start": v(-443.32, 63.2) * mm, "end": v(-444.6, 64.08) * mm});
            skLineSegment(sketch, "E7568", {"start": v(-444.6, 64.08) * mm, "end": v(-445.88, 64.93) * mm});
            skLineSegment(sketch, "E7569", {"start": v(-445.88, 64.93) * mm, "end": v(-447.2, 65.73) * mm});
            skLineSegment(sketch, "E7570", {"start": v(-447.2, 65.73) * mm, "end": v(-448.53, 66.5) * mm});
            skLineSegment(sketch, "E7571", {"start": v(-448.53, 66.5) * mm, "end": v(-449.88, 67.22) * mm});
            skLineSegment(sketch, "E7572", {"start": v(-449.88, 67.22) * mm, "end": v(-451.24, 67.9) * mm});
            skLineSegment(sketch, "E7573", {"start": v(-451.24, 67.9) * mm, "end": v(-452.62, 68.54) * mm});
            skLineSegment(sketch, "E7574", {"start": v(-452.62, 68.54) * mm, "end": v(-454.02, 69.14) * mm});
            skLineSegment(sketch, "E7575", {"start": v(-454.02, 69.14) * mm, "end": v(-455.42, 69.69) * mm});
            skLineSegment(sketch, "E7576", {"start": v(-455.42, 69.69) * mm, "end": v(-456.83, 70.19) * mm});
            skLineSegment(sketch, "E7577", {"start": v(-456.83, 70.19) * mm, "end": v(-458.24, 70.64) * mm});
            skLineSegment(sketch, "E7578", {"start": v(-458.24, 70.64) * mm, "end": v(-459.66, 71.04) * mm});
            skLineSegment(sketch, "E7579", {"start": v(-459.66, 71.04) * mm, "end": v(-461.08, 71.38) * mm});
            skLineSegment(sketch, "E7580", {"start": v(-461.08, 71.38) * mm, "end": v(-462.5, 71.67) * mm});
            skLineSegment(sketch, "E7581", {"start": v(-462.5, 71.67) * mm, "end": v(-463.92, 71.9) * mm});
            skLineSegment(sketch, "E7582", {"start": v(-463.92, 71.9) * mm, "end": v(-465.33, 72.09) * mm});
            skLineSegment(sketch, "E7583", {"start": v(-465.33, 72.09) * mm, "end": v(-466.74, 72.2) * mm});
            skLineSegment(sketch, "E7584", {"start": v(-466.74, 72.2) * mm, "end": v(-468.14, 72.26) * mm});
            skLineSegment(sketch, "E7585", {"start": v(-468.14, 72.26) * mm, "end": v(-469.52, 72.25) * mm});
            skLineSegment(sketch, "E7586", {"start": v(-469.52, 72.25) * mm, "end": v(-470.9, 72.18) * mm});
            skLineSegment(sketch, "E7587", {"start": v(-470.9, 72.18) * mm, "end": v(-472.25, 72.05) * mm});
            skLineSegment(sketch, "E7588", {"start": v(-472.25, 72.05) * mm, "end": v(-473.6, 71.84) * mm});
            skLineSegment(sketch, "E7589", {"start": v(-473.6, 71.84) * mm, "end": v(-474.92, 71.57) * mm});
            skLineSegment(sketch, "E7590", {"start": v(-474.92, 71.57) * mm, "end": v(-476.22, 71.22) * mm});
            skLineSegment(sketch, "E7591", {"start": v(-476.22, 71.22) * mm, "end": v(-477.5, 70.8) * mm});
            skLineSegment(sketch, "E7592", {"start": v(-477.5, 70.8) * mm, "end": v(-478.75, 70.31) * mm});
            skLineSegment(sketch, "E7593", {"start": v(-478.75, 70.31) * mm, "end": v(-479.98, 69.74) * mm});
            skLineSegment(sketch, "E7594", {"start": v(-479.98, 69.74) * mm, "end": v(-481.17, 69.1) * mm});
            skLineSegment(sketch, "E7595", {"start": v(-481.17, 69.1) * mm, "end": v(-482.34, 68.38) * mm});
            skLineSegment(sketch, "E7596", {"start": v(-482.34, 68.38) * mm, "end": v(-483.47, 67.57) * mm});
            skLineSegment(sketch, "E7597", {"start": v(-483.47, 67.57) * mm, "end": v(-484.57, 66.68) * mm});
            skLineSegment(sketch, "E7598", {"start": v(-484.57, 66.68) * mm, "end": v(-485.63, 65.71) * mm});
            skLineSegment(sketch, "E7599", {"start": v(-485.63, 65.71) * mm, "end": v(-486.65, 64.66) * mm});
            skLineSegment(sketch, "E7600", {"start": v(-486.65, 64.66) * mm, "end": v(-487.63, 63.51) * mm});
            skLineSegment(sketch, "E7601", {"start": v(-487.63, 63.51) * mm, "end": v(-488.56, 62.28) * mm});
            skLineSegment(sketch, "E7602", {"start": v(-488.56, 62.28) * mm, "end": v(-489.45, 60.96) * mm});
            skLineSegment(sketch, "E7603", {"start": v(-489.45, 60.96) * mm, "end": v(-490.3, 59.54) * mm});
            skLineSegment(sketch, "E7604", {"start": v(-490.3, 59.54) * mm, "end": v(-491.08, 58.03) * mm});
            skLineSegment(sketch, "E7605", {"start": v(-491.08, 58.03) * mm, "end": v(-491.82, 56.43) * mm});
            skLineSegment(sketch, "E7606", {"start": v(-491.82, 56.43) * mm, "end": v(-492.5, 54.73) * mm});
            skLineSegment(sketch, "E7607", {"start": v(-492.5, 54.73) * mm, "end": v(-493.14, 52.93) * mm});
            skLineSegment(sketch, "E7608", {"start": v(-493.14, 52.93) * mm, "end": v(-493.66, 51.23) * mm});
            skLineSegment(sketch, "E7609", {"start": v(-493.66, 51.23) * mm, "end": v(-494.15, 49.52) * mm});
            skLineSegment(sketch, "E7610", {"start": v(-494.15, 49.52) * mm, "end": v(-494.6, 47.8) * mm});
            skLineSegment(sketch, "E7611", {"start": v(-494.6, 47.8) * mm, "end": v(-495, 46.05) * mm});
            skLineSegment(sketch, "E7612", {"start": v(-495, 46.05) * mm, "end": v(-495.37, 44.29) * mm});
            skLineSegment(sketch, "E7613", {"start": v(-495.37, 44.29) * mm, "end": v(-495.7, 42.52) * mm});
            skLineSegment(sketch, "E7614", {"start": v(-495.7, 42.52) * mm, "end": v(-496, 40.73) * mm});
            skLineSegment(sketch, "E7615", {"start": v(-496, 40.73) * mm, "end": v(-496.27, 38.94) * mm});
            skLineSegment(sketch, "E7616", {"start": v(-496.27, 38.94) * mm, "end": v(-496.5, 37.13) * mm});
            skLineSegment(sketch, "E7617", {"start": v(-496.5, 37.13) * mm, "end": v(-496.7, 35.31) * mm});
            skLineSegment(sketch, "E7618", {"start": v(-496.7, 35.31) * mm, "end": v(-496.89, 33.49) * mm});
            skLineSegment(sketch, "E7619", {"start": v(-496.89, 33.49) * mm, "end": v(-497.04, 31.66) * mm});
            skLineSegment(sketch, "E7620", {"start": v(-497.04, 31.66) * mm, "end": v(-497.17, 29.82) * mm});
            skLineSegment(sketch, "E7621", {"start": v(-497.17, 29.82) * mm, "end": v(-497.28, 27.97) * mm});
            skLineSegment(sketch, "E7622", {"start": v(-497.28, 27.97) * mm, "end": v(-497.36, 26.12) * mm});
            skLineSegment(sketch, "E7623", {"start": v(-497.36, 26.12) * mm, "end": v(-497.43, 24.27) * mm});
            skLineSegment(sketch, "E7624", {"start": v(-497.43, 24.27) * mm, "end": v(-497.48, 22.41) * mm});
            skLineSegment(sketch, "E7625", {"start": v(-497.48, 22.41) * mm, "end": v(-497.51, 20.56) * mm});
            skLineSegment(sketch, "E7626", {"start": v(-497.51, 20.56) * mm, "end": v(-497.53, 18.7) * mm});
            skLineSegment(sketch, "E7627", {"start": v(-497.53, 18.7) * mm, "end": v(-497.54, 16.84) * mm});
            skLineSegment(sketch, "E7628", {"start": v(-497.54, 16.84) * mm, "end": v(-497.53, 14.98) * mm});
            skLineSegment(sketch, "E7629", {"start": v(-497.53, 14.98) * mm, "end": v(-497.52, 13.13) * mm});
            skLineSegment(sketch, "E7630", {"start": v(-497.52, 13.13) * mm, "end": v(-497.5, 11.27) * mm});
            skLineSegment(sketch, "E7631", {"start": v(-497.5, 11.27) * mm, "end": v(-497.46, 9.43) * mm});
            skLineSegment(sketch, "E7632", {"start": v(-497.46, 9.43) * mm, "end": v(-497.43, 7.58) * mm});
            skLineSegment(sketch, "E7633", {"start": v(-497.43, 7.58) * mm, "end": v(-497.39, 5.75) * mm});
            skLineSegment(sketch, "E7634", {"start": v(-497.39, 5.75) * mm, "end": v(-497.35, 3.91) * mm});
            skLineSegment(sketch, "E7635", {"start": v(-497.35, 3.91) * mm, "end": v(-497.31, 2.1) * mm});
            skLineSegment(sketch, "E7636", {"start": v(-497.31, 2.1) * mm, "end": v(-497.27, 0.28) * mm});
            skLineSegment(sketch, "E7637", {"start": v(-497.27, 0.28) * mm, "end": v(-497.24, -1.53) * mm});
            skLineSegment(sketch, "E7638", {"start": v(-497.24, -1.53) * mm, "end": v(-497.2, -3.32) * mm});
            skLineSegment(sketch, "E7639", {"start": v(-497.2, -3.32) * mm, "end": v(-497.19, -5.1) * mm});
            skLineSegment(sketch, "E7640", {"start": v(-497.19, -5.1) * mm, "end": v(-497.17, -6.87) * mm});
            skLineSegment(sketch, "E7641", {"start": v(-497.17, -6.87) * mm, "end": v(-497.16, -8.62) * mm});
            skLineSegment(sketch, "E7642", {"start": v(-497.16, -8.62) * mm, "end": v(-497.16, -10.43) * mm});
            skLineSegment(sketch, "E7643", {"start": v(-497.16, -10.43) * mm, "end": v(-497.15, -12.23) * mm});
            skLineSegment(sketch, "E7644", {"start": v(-497.15, -12.23) * mm, "end": v(-497.13, -14.03) * mm});
            skLineSegment(sketch, "E7645", {"start": v(-497.13, -14.03) * mm, "end": v(-497.1, -15.83) * mm});
            skLineSegment(sketch, "E7646", {"start": v(-497.1, -15.83) * mm, "end": v(-497.06, -17.63) * mm});
            skLineSegment(sketch, "E7647", {"start": v(-497.06, -17.63) * mm, "end": v(-497.02, -19.43) * mm});
            skLineSegment(sketch, "E7648", {"start": v(-497.02, -19.43) * mm, "end": v(-496.97, -21.24) * mm});
            skLineSegment(sketch, "E7649", {"start": v(-496.97, -21.24) * mm, "end": v(-496.9, -23.04) * mm});
            skLineSegment(sketch, "E7650", {"start": v(-496.9, -23.04) * mm, "end": v(-496.84, -24.84) * mm});
            skLineSegment(sketch, "E7651", {"start": v(-496.84, -24.84) * mm, "end": v(-496.76, -26.64) * mm});
            skLineSegment(sketch, "E7652", {"start": v(-496.76, -26.64) * mm, "end": v(-496.68, -28.44) * mm});
            skLineSegment(sketch, "E7653", {"start": v(-496.68, -28.44) * mm, "end": v(-496.59, -30.24) * mm});
            skLineSegment(sketch, "E7654", {"start": v(-496.59, -30.24) * mm, "end": v(-496.49, -32.04) * mm});
            skLineSegment(sketch, "E7655", {"start": v(-496.49, -32.04) * mm, "end": v(-496.38, -33.84) * mm});
            skLineSegment(sketch, "E7656", {"start": v(-496.38, -33.84) * mm, "end": v(-496.27, -35.64) * mm});
            skLineSegment(sketch, "E7657", {"start": v(-496.27, -35.64) * mm, "end": v(-496.15, -37.44) * mm});
            skLineSegment(sketch, "E7658", {"start": v(-496.15, -37.44) * mm, "end": v(-496.02, -39.24) * mm});
            skLineSegment(sketch, "E7659", {"start": v(-496.02, -39.24) * mm, "end": v(-495.88, -41.04) * mm});
            skLineSegment(sketch, "E7660", {"start": v(-495.88, -41.04) * mm, "end": v(-495.73, -42.83) * mm});
            skLineSegment(sketch, "E7661", {"start": v(-495.73, -42.83) * mm, "end": v(-495.58, -44.63) * mm});
            skLineSegment(sketch, "E7662", {"start": v(-495.58, -44.63) * mm, "end": v(-495.42, -46.43) * mm});
            skLineSegment(sketch, "E7663", {"start": v(-495.42, -46.43) * mm, "end": v(-495.25, -48.22) * mm});
            skLineSegment(sketch, "E7664", {"start": v(-495.25, -48.22) * mm, "end": v(-495.08, -50.02) * mm});
            skLineSegment(sketch, "E7665", {"start": v(-495.08, -50.02) * mm, "end": v(-494.9, -51.81) * mm});
            skLineSegment(sketch, "E7666", {"start": v(-494.9, -51.81) * mm, "end": v(-494.7, -53.6) * mm});
            skLineSegment(sketch, "E7667", {"start": v(-494.7, -53.6) * mm, "end": v(-494.51, -55.4) * mm});
            skLineSegment(sketch, "E7668", {"start": v(-494.51, -55.4) * mm, "end": v(-494.3, -57.2) * mm});
            skLineSegment(sketch, "E7669", {"start": v(-494.3, -57.2) * mm, "end": v(-494.1, -58.99) * mm});
            skLineSegment(sketch, "E7670", {"start": v(-494.1, -58.99) * mm, "end": v(-493.88, -60.78) * mm});
            skLineSegment(sketch, "E7671", {"start": v(-493.88, -60.78) * mm, "end": v(-493.65, -62.57) * mm});
            skLineSegment(sketch, "E7672", {"start": v(-493.65, -62.57) * mm, "end": v(-493.42, -64.36) * mm});
            skLineSegment(sketch, "E7673", {"start": v(-493.42, -64.36) * mm, "end": v(-493.18, -66.15) * mm});
            skLineSegment(sketch, "E7674", {"start": v(-493.18, -66.15) * mm, "end": v(-492.93, -67.94) * mm});
            skLineSegment(sketch, "E7675", {"start": v(-492.93, -67.94) * mm, "end": v(-492.68, -69.73) * mm});
            skLineSegment(sketch, "E7676", {"start": v(-492.68, -69.73) * mm, "end": v(-492.41, -71.51) * mm});
            skLineSegment(sketch, "E7677", {"start": v(-492.41, -71.51) * mm, "end": v(-492.15, -73.3) * mm});
            skLineSegment(sketch, "E7678", {"start": v(-492.15, -73.3) * mm, "end": v(-491.87, -75.09) * mm});
            skLineSegment(sketch, "E7679", {"start": v(-491.87, -75.09) * mm, "end": v(-491.59, -76.87) * mm});
            skLineSegment(sketch, "E7680", {"start": v(-491.59, -76.87) * mm, "end": v(-491.3, -78.65) * mm});
            skLineSegment(sketch, "E7681", {"start": v(-491.3, -78.65) * mm, "end": v(-491, -80.44) * mm});
            skLineSegment(sketch, "E7682", {"start": v(-491, -80.44) * mm, "end": v(-490.7, -82.22) * mm});
            skLineSegment(sketch, "E7683", {"start": v(-490.7, -82.22) * mm, "end": v(-490.4, -84) * mm});
            skLineSegment(sketch, "E7684", {"start": v(-490.4, -84) * mm, "end": v(-490.07, -85.78) * mm});
            skLineSegment(sketch, "E7685", {"start": v(-490.07, -85.78) * mm, "end": v(-489.75, -87.56) * mm});
            skLineSegment(sketch, "E7686", {"start": v(-489.75, -87.56) * mm, "end": v(-489.42, -89.33) * mm});
            skLineSegment(sketch, "E7687", {"start": v(-489.42, -89.33) * mm, "end": v(-489.08, -91.1) * mm});
            skLineSegment(sketch, "E7688", {"start": v(-489.08, -91.1) * mm, "end": v(-488.74, -92.88) * mm});
            skLineSegment(sketch, "E7689", {"start": v(-488.74, -92.88) * mm, "end": v(-488.39, -94.66) * mm});
            skLineSegment(sketch, "E7690", {"start": v(-488.39, -94.66) * mm, "end": v(-488.03, -96.43) * mm});
            skLineSegment(sketch, "E7691", {"start": v(-488.03, -96.43) * mm, "end": v(-487.67, -98.2) * mm});
            skLineSegment(sketch, "E7692", {"start": v(-487.67, -98.2) * mm, "end": v(-487.3, -99.97) * mm});
            skLineSegment(sketch, "E7693", {"start": v(-487.3, -99.97) * mm, "end": v(-486.92, -101.74) * mm});
            skLineSegment(sketch, "E7694", {"start": v(-486.92, -101.74) * mm, "end": v(-486.54, -103.5) * mm});
            skLineSegment(sketch, "E7695", {"start": v(-486.54, -103.5) * mm, "end": v(-486.15, -105.27) * mm});
            skLineSegment(sketch, "E7696", {"start": v(-486.15, -105.27) * mm, "end": v(-485.76, -107.04) * mm});
            skLineSegment(sketch, "E7697", {"start": v(-485.76, -107.04) * mm, "end": v(-485.35, -108.8) * mm});
            skLineSegment(sketch, "E7698", {"start": v(-485.35, -108.8) * mm, "end": v(-484.95, -110.56) * mm});
            skLineSegment(sketch, "E7699", {"start": v(-484.95, -110.56) * mm, "end": v(-484.53, -112.32) * mm});
            skLineSegment(sketch, "E7700", {"start": v(-484.53, -112.32) * mm, "end": v(-484.11, -114.08) * mm});
            skLineSegment(sketch, "E7701", {"start": v(-484.11, -114.08) * mm, "end": v(-483.68, -115.84) * mm});
            skLineSegment(sketch, "E7702", {"start": v(-483.68, -115.84) * mm, "end": v(-483.25, -117.6) * mm});
            skLineSegment(sketch, "E7703", {"start": v(-483.25, -117.6) * mm, "end": v(-482.81, -119.35) * mm});
            skLineSegment(sketch, "E7704", {"start": v(-482.81, -119.35) * mm, "end": v(-482.37, -121.1) * mm});
            skLineSegment(sketch, "E7705", {"start": v(-482.37, -121.1) * mm, "end": v(-481.91, -122.85) * mm});
            skLineSegment(sketch, "E7706", {"start": v(-481.91, -122.85) * mm, "end": v(-481.46, -124.6) * mm});
            skLineSegment(sketch, "E7707", {"start": v(-481.46, -124.6) * mm, "end": v(-481, -126.35) * mm});
            skLineSegment(sketch, "E7708", {"start": v(-481, -126.35) * mm, "end": v(-480.52, -128.1) * mm});
            skLineSegment(sketch, "E7709", {"start": v(-480.52, -128.1) * mm, "end": v(-480.05, -129.84) * mm});
            skLineSegment(sketch, "E7710", {"start": v(-480.05, -129.84) * mm, "end": v(-479.57, -131.59) * mm});
            skLineSegment(sketch, "E7711", {"start": v(-479.57, -131.59) * mm, "end": v(-479.08, -133.33) * mm});
            skLineSegment(sketch, "E7712", {"start": v(-479.08, -133.33) * mm, "end": v(-478.58, -135.07) * mm});
            skLineSegment(sketch, "E7713", {"start": v(-478.58, -135.07) * mm, "end": v(-478.08, -136.8) * mm});
            skLineSegment(sketch, "E7714", {"start": v(-478.08, -136.8) * mm, "end": v(-477.58, -138.54) * mm});
            skLineSegment(sketch, "E7715", {"start": v(-477.58, -138.54) * mm, "end": v(-477.07, -140.28) * mm});
            skLineSegment(sketch, "E7716", {"start": v(-477.07, -140.28) * mm, "end": v(-476.55, -142) * mm});
            skLineSegment(sketch, "E7717", {"start": v(-476.55, -142) * mm, "end": v(-476.03, -143.74) * mm});
            skLineSegment(sketch, "E7718", {"start": v(-476.03, -143.74) * mm, "end": v(-475.5, -145.47) * mm});
            skLineSegment(sketch, "E7719", {"start": v(-475.5, -145.47) * mm, "end": v(-474.97, -147.2) * mm});
            skLineSegment(sketch, "E7720", {"start": v(-474.97, -147.2) * mm, "end": v(-474.43, -148.92) * mm});
            skLineSegment(sketch, "E7721", {"start": v(-474.43, -148.92) * mm, "end": v(-473.88, -150.64) * mm});
            skLineSegment(sketch, "E7722", {"start": v(-473.88, -150.64) * mm, "end": v(-473.33, -152.36) * mm});
            skLineSegment(sketch, "E7723", {"start": v(-473.33, -152.36) * mm, "end": v(-472.78, -154.08) * mm});
            skLineSegment(sketch, "E7724", {"start": v(-472.78, -154.08) * mm, "end": v(-472.21, -155.8) * mm});
            skLineSegment(sketch, "E7725", {"start": v(-472.21, -155.8) * mm, "end": v(-471.65, -157.51) * mm});
            skLineSegment(sketch, "E7726", {"start": v(-471.65, -157.51) * mm, "end": v(-471.07, -159.22) * mm});
            skLineSegment(sketch, "E7727", {"start": v(-471.07, -159.22) * mm, "end": v(-470.5, -160.93) * mm});
            skLineSegment(sketch, "E7728", {"start": v(-470.5, -160.93) * mm, "end": v(-469.91, -162.64) * mm});
            skLineSegment(sketch, "E7729", {"start": v(-469.91, -162.64) * mm, "end": v(-469.32, -164.35) * mm});
            skLineSegment(sketch, "E7730", {"start": v(-469.32, -164.35) * mm, "end": v(-468.73, -166.05) * mm});
            skLineSegment(sketch, "E7731", {"start": v(-468.73, -166.05) * mm, "end": v(-468.13, -167.75) * mm});
            skLineSegment(sketch, "E7732", {"start": v(-468.13, -167.75) * mm, "end": v(-467.53, -169.45) * mm});
            skLineSegment(sketch, "E7733", {"start": v(-467.53, -169.45) * mm, "end": v(-466.92, -171.15) * mm});
            skLineSegment(sketch, "E7734", {"start": v(-466.92, -171.15) * mm, "end": v(-466.3, -172.84) * mm});
            skLineSegment(sketch, "E7735", {"start": v(-466.3, -172.84) * mm, "end": v(-465.68, -174.54) * mm});
            skLineSegment(sketch, "E7736", {"start": v(-465.68, -174.54) * mm, "end": v(-465.05, -176.22) * mm});
            skLineSegment(sketch, "E7737", {"start": v(-465.05, -176.22) * mm, "end": v(-464.42, -177.91) * mm});
            skLineSegment(sketch, "E7738", {"start": v(-464.42, -177.91) * mm, "end": v(-463.79, -179.6) * mm});
            skLineSegment(sketch, "E7739", {"start": v(-463.79, -179.6) * mm, "end": v(-463.15, -181.28) * mm});
            skLineSegment(sketch, "E7740", {"start": v(-463.15, -181.28) * mm, "end": v(-462.5, -182.96) * mm});
            skLineSegment(sketch, "E7741", {"start": v(-462.5, -182.96) * mm, "end": v(-461.85, -184.64) * mm});
            skLineSegment(sketch, "E7742", {"start": v(-461.85, -184.64) * mm, "end": v(-461.2, -186.31) * mm});
            skLineSegment(sketch, "E7743", {"start": v(-461.2, -186.31) * mm, "end": v(-460.54, -187.99) * mm});
            skLineSegment(sketch, "E7744", {"start": v(-460.54, -187.99) * mm, "end": v(-459.87, -189.66) * mm});
            skLineSegment(sketch, "E7745", {"start": v(-459.87, -189.66) * mm, "end": v(-459.37, -190.93) * mm});
            skLineSegment(sketch, "E7746", {"start": v(-459.37, -190.93) * mm, "end": v(-458.85, -192.28) * mm});
            skLineSegment(sketch, "E7747", {"start": v(-458.85, -192.28) * mm, "end": v(-458.31, -193.67) * mm});
            skLineSegment(sketch, "E7748", {"start": v(-458.31, -193.67) * mm, "end": v(-457.77, -195.13) * mm});
            skLineSegment(sketch, "E7749", {"start": v(-457.77, -195.13) * mm, "end": v(-457.2, -196.63) * mm});
            skLineSegment(sketch, "E7750", {"start": v(-457.2, -196.63) * mm, "end": v(-456.63, -198.19) * mm});
            skLineSegment(sketch, "E7751", {"start": v(-456.63, -198.19) * mm, "end": v(-456.05, -199.79) * mm});
            skLineSegment(sketch, "E7752", {"start": v(-456.05, -199.79) * mm, "end": v(-455.44, -201.43) * mm});
            skLineSegment(sketch, "E7753", {"start": v(-455.44, -201.43) * mm, "end": v(-454.83, -203.1) * mm});
            skLineSegment(sketch, "E7754", {"start": v(-454.83, -203.1) * mm, "end": v(-454.2, -204.82) * mm});
            skLineSegment(sketch, "E7755", {"start": v(-454.2, -204.82) * mm, "end": v(-453.55, -206.56) * mm});
            skLineSegment(sketch, "E7756", {"start": v(-453.55, -206.56) * mm, "end": v(-452.9, -208.33) * mm});
            skLineSegment(sketch, "E7757", {"start": v(-452.9, -208.33) * mm, "end": v(-452.22, -210.12) * mm});
            skLineSegment(sketch, "E7758", {"start": v(-452.22, -210.12) * mm, "end": v(-451.53, -211.93) * mm});
            skLineSegment(sketch, "E7759", {"start": v(-451.53, -211.93) * mm, "end": v(-450.83, -213.76) * mm});
            skLineSegment(sketch, "E7760", {"start": v(-450.83, -213.76) * mm, "end": v(-450.11, -215.6) * mm});
            skLineSegment(sketch, "E7761", {"start": v(-450.11, -215.6) * mm, "end": v(-449.38, -217.46) * mm});
            skLineSegment(sketch, "E7762", {"start": v(-449.38, -217.46) * mm, "end": v(-448.63, -219.32) * mm});
            skLineSegment(sketch, "E7763", {"start": v(-448.63, -219.32) * mm, "end": v(-447.87, -221.18) * mm});
            skLineSegment(sketch, "E7764", {"start": v(-447.87, -221.18) * mm, "end": v(-447.1, -223.04) * mm});
            skLineSegment(sketch, "E7765", {"start": v(-447.1, -223.04) * mm, "end": v(-446.3, -224.9) * mm});
            skLineSegment(sketch, "E7766", {"start": v(-446.3, -224.9) * mm, "end": v(-445.5, -226.75) * mm});
            skLineSegment(sketch, "E7767", {"start": v(-445.5, -226.75) * mm, "end": v(-444.67, -228.58) * mm});
            skLineSegment(sketch, "E7768", {"start": v(-444.67, -228.58) * mm, "end": v(-443.84, -230.4) * mm});
            skLineSegment(sketch, "E7769", {"start": v(-443.84, -230.4) * mm, "end": v(-442.99, -232.21) * mm});
            skLineSegment(sketch, "E7770", {"start": v(-442.99, -232.21) * mm, "end": v(-442.12, -234) * mm});
            skLineSegment(sketch, "E7771", {"start": v(-442.12, -234) * mm, "end": v(-441.24, -235.75) * mm});
            skLineSegment(sketch, "E7772", {"start": v(-441.24, -235.75) * mm, "end": v(-440.34, -237.48) * mm});
            skLineSegment(sketch, "E7773", {"start": v(-440.34, -237.48) * mm, "end": v(-439.42, -239.18) * mm});
            skLineSegment(sketch, "E7774", {"start": v(-439.42, -239.18) * mm, "end": v(-438.5, -240.84) * mm});
            skLineSegment(sketch, "E7775", {"start": v(-438.5, -240.84) * mm, "end": v(-437.55, -242.46) * mm});
            skLineSegment(sketch, "E7776", {"start": v(-437.55, -242.46) * mm, "end": v(-436.59, -244.04) * mm});
            skLineSegment(sketch, "E7777", {"start": v(-436.59, -244.04) * mm, "end": v(-435.6, -245.57) * mm});
            skLineSegment(sketch, "E7778", {"start": v(-435.6, -245.57) * mm, "end": v(-434.62, -247.06) * mm});
            skLineSegment(sketch, "E7779", {"start": v(-434.62, -247.06) * mm, "end": v(-433.6, -248.49) * mm});
            skLineSegment(sketch, "E7780", {"start": v(-433.6, -248.49) * mm, "end": v(-432.58, -249.86) * mm});
            skLineSegment(sketch, "E7781", {"start": v(-432.58, -249.86) * mm, "end": v(-431.54, -251.18) * mm});
            skLineSegment(sketch, "E7782", {"start": v(-431.54, -251.18) * mm, "end": v(-430.48, -252.43) * mm});
            skLineSegment(sketch, "E7783", {"start": v(-430.48, -252.43) * mm, "end": v(-429.41, -253.6) * mm});
            skLineSegment(sketch, "E7784", {"start": v(-429.41, -253.6) * mm, "end": v(-428.32, -254.72) * mm});
            skLineSegment(sketch, "E7785", {"start": v(-428.32, -254.72) * mm, "end": v(-427.21, -255.76) * mm});
            skLineSegment(sketch, "E7786", {"start": v(-427.21, -255.76) * mm, "end": v(-426.1, -256.72) * mm});
            skLineSegment(sketch, "E7787", {"start": v(-426.1, -256.72) * mm, "end": v(-424.95, -257.6) * mm});
            skLineSegment(sketch, "E7788", {"start": v(-424.95, -257.6) * mm, "end": v(-423.8, -258.4) * mm});
            skLineSegment(sketch, "E7789", {"start": v(-423.8, -258.4) * mm, "end": v(-422.56, -259.1) * mm});
            skLineSegment(sketch, "E7790", {"start": v(-422.56, -259.1) * mm, "end": v(-421.2, -259.71) * mm});
            skLineSegment(sketch, "E7791", {"start": v(-421.2, -259.71) * mm, "end": v(-419.75, -260.23) * mm});
            skLineSegment(sketch, "E7792", {"start": v(-419.75, -260.23) * mm, "end": v(-418.19, -260.66) * mm});
            skLineSegment(sketch, "E7793", {"start": v(-418.19, -260.66) * mm, "end": v(-416.54, -261.01) * mm});
            skLineSegment(sketch, "E7794", {"start": v(-416.54, -261.01) * mm, "end": v(-414.8, -261.3) * mm});
            skLineSegment(sketch, "E7795", {"start": v(-414.8, -261.3) * mm, "end": v(-413, -261.5) * mm});
            skLineSegment(sketch, "E7796", {"start": v(-413, -261.5) * mm, "end": v(-411.14, -261.65) * mm});
            skLineSegment(sketch, "E7797", {"start": v(-411.14, -261.65) * mm, "end": v(-409.23, -261.74) * mm});
            skLineSegment(sketch, "E7798", {"start": v(-409.23, -261.74) * mm, "end": v(-407.27, -261.78) * mm});
            skLineSegment(sketch, "E7799", {"start": v(-407.27, -261.78) * mm, "end": v(-405.28, -261.77) * mm});
            skLineSegment(sketch, "E7800", {"start": v(-405.28, -261.77) * mm, "end": v(-403.27, -261.73) * mm});
            skLineSegment(sketch, "E7801", {"start": v(-403.27, -261.73) * mm, "end": v(-401.25, -261.65) * mm});
            skLineSegment(sketch, "E7802", {"start": v(-401.25, -261.65) * mm, "end": v(-399.23, -261.55) * mm});
            skLineSegment(sketch, "E7803", {"start": v(-399.23, -261.55) * mm, "end": v(-397.2, -261.42) * mm});
            skLineSegment(sketch, "E7804", {"start": v(-397.2, -261.42) * mm, "end": v(-395.2, -261.28) * mm});
            skLineSegment(sketch, "E7805", {"start": v(-395.2, -261.28) * mm, "end": v(-393.23, -261.13) * mm});
            skLineSegment(sketch, "E7806", {"start": v(-393.23, -261.13) * mm, "end": v(-391.29, -260.97) * mm});
            skLineSegment(sketch, "E7807", {"start": v(-391.29, -260.97) * mm, "end": v(-389.39, -260.82) * mm});
            skLineSegment(sketch, "E7808", {"start": v(-389.39, -260.82) * mm, "end": v(-387.55, -260.67) * mm});
            skLineSegment(sketch, "E7809", {"start": v(-387.55, -260.67) * mm, "end": v(-385.77, -260.54) * mm});
            skLineSegment(sketch, "E7810", {"start": v(-385.77, -260.54) * mm, "end": v(-384.07, -260.42) * mm});
            skLineSegment(sketch, "E7811", {"start": v(-384.07, -260.42) * mm, "end": v(-382.45, -260.34) * mm});
            skLineSegment(sketch, "E7812", {"start": v(-382.45, -260.34) * mm, "end": v(-380.92, -260.28) * mm});
            skLineSegment(sketch, "E7813", {"start": v(-380.92, -260.28) * mm, "end": v(-379.5, -260.26) * mm});
            skLineSegment(sketch, "E7814", {"start": v(-379.5, -260.26) * mm, "end": v(-379.5, -140.78) * mm});
            skLineSegment(sketch, "E7815", {"start": v(-379.5, -140.78) * mm, "end": v(-380.81, -140.8) * mm});
            skLineSegment(sketch, "E7816", {"start": v(-380.81, -140.8) * mm, "end": v(-382.21, -140.83) * mm});
            skLineSegment(sketch, "E7817", {"start": v(-382.21, -140.83) * mm, "end": v(-383.7, -140.9) * mm});
            skLineSegment(sketch, "E7818", {"start": v(-383.7, -140.9) * mm, "end": v(-385.24, -140.98) * mm});
            skLineSegment(sketch, "E7819", {"start": v(-385.24, -140.98) * mm, "end": v(-386.86, -141.09) * mm});
            skLineSegment(sketch, "E7820", {"start": v(-386.86, -141.09) * mm, "end": v(-388.54, -141.21) * mm});
            skLineSegment(sketch, "E7821", {"start": v(-388.54, -141.21) * mm, "end": v(-390.27, -141.35) * mm});
            skLineSegment(sketch, "E7822", {"start": v(-390.27, -141.35) * mm, "end": v(-392.06, -141.5) * mm});
            skLineSegment(sketch, "E7823", {"start": v(-392.06, -141.5) * mm, "end": v(-393.9, -141.65) * mm});
            skLineSegment(sketch, "E7824", {"start": v(-393.9, -141.65) * mm, "end": v(-395.78, -141.8) * mm});
            skLineSegment(sketch, "E7825", {"start": v(-395.78, -141.8) * mm, "end": v(-397.7, -141.97) * mm});
            skLineSegment(sketch, "E7826", {"start": v(-397.7, -141.97) * mm, "end": v(-399.64, -142.13) * mm});
            skLineSegment(sketch, "E7827", {"start": v(-399.64, -142.13) * mm, "end": v(-401.61, -142.3) * mm});
            skLineSegment(sketch, "E7828", {"start": v(-401.61, -142.3) * mm, "end": v(-403.61, -142.45) * mm});
            skLineSegment(sketch, "E7829", {"start": v(-403.61, -142.45) * mm, "end": v(-405.62, -142.6) * mm});
            skLineSegment(sketch, "E7830", {"start": v(-405.62, -142.6) * mm, "end": v(-407.65, -142.74) * mm});
            skLineSegment(sketch, "E7831", {"start": v(-407.65, -142.74) * mm, "end": v(-409.68, -142.86) * mm});
            skLineSegment(sketch, "E7832", {"start": v(-409.68, -142.86) * mm, "end": v(-411.72, -142.97) * mm});
            skLineSegment(sketch, "E7833", {"start": v(-411.72, -142.97) * mm, "end": v(-413.75, -143.06) * mm});
            skLineSegment(sketch, "E7834", {"start": v(-413.75, -143.06) * mm, "end": v(-415.77, -143.14) * mm});
            skLineSegment(sketch, "E7835", {"start": v(-415.77, -143.14) * mm, "end": v(-417.78, -143.18) * mm});
            skLineSegment(sketch, "E7836", {"start": v(-417.78, -143.18) * mm, "end": v(-419.77, -143.2) * mm});
            skLineSegment(sketch, "E7837", {"start": v(-419.77, -143.2) * mm, "end": v(-421.74, -143.2) * mm});
            skLineSegment(sketch, "E7838", {"start": v(-421.74, -143.2) * mm, "end": v(-423.68, -143.16) * mm});
            skLineSegment(sketch, "E7839", {"start": v(-423.68, -143.16) * mm, "end": v(-425.6, -143.1) * mm});
            skLineSegment(sketch, "E7840", {"start": v(-425.6, -143.1) * mm, "end": v(-427.46, -142.98) * mm});
            skLineSegment(sketch, "E7841", {"start": v(-427.46, -142.98) * mm, "end": v(-429.3, -142.84) * mm});
            skLineSegment(sketch, "E7842", {"start": v(-429.3, -142.84) * mm, "end": v(-431.07, -142.65) * mm});
            skLineSegment(sketch, "E7843", {"start": v(-431.07, -142.65) * mm, "end": v(-432.8, -142.42) * mm});
            skLineSegment(sketch, "E7844", {"start": v(-432.8, -142.42) * mm, "end": v(-434.46, -142.14) * mm});
            skLineSegment(sketch, "E7845", {"start": v(-434.46, -142.14) * mm, "end": v(-436.07, -141.8) * mm});
            skLineSegment(sketch, "E7846", {"start": v(-436.07, -141.8) * mm, "end": v(-437.6, -141.43) * mm});
            skLineSegment(sketch, "E7847", {"start": v(-437.6, -141.43) * mm, "end": v(-439.07, -140.99) * mm});
            skLineSegment(sketch, "E7848", {"start": v(-439.07, -140.99) * mm, "end": v(-440.45, -140.5) * mm});
            skLineSegment(sketch, "E7849", {"start": v(-440.45, -140.5) * mm, "end": v(-441.76, -139.94) * mm});
            skLineSegment(sketch, "E7850", {"start": v(-441.76, -139.94) * mm, "end": v(-442.97, -139.32) * mm});
            skLineSegment(sketch, "E7851", {"start": v(-442.97, -139.32) * mm, "end": v(-444.09, -138.64) * mm});
            skLineSegment(sketch, "E7852", {"start": v(-444.09, -138.64) * mm, "end": v(-444.76, -138.1) * mm});
            skLineSegment(sketch, "E7853", {"start": v(-444.76, -138.1) * mm, "end": v(-445.4, -137.38) * mm});
            skLineSegment(sketch, "E7854", {"start": v(-445.4, -137.38) * mm, "end": v(-445.99, -136.5) * mm});
            skLineSegment(sketch, "E7855", {"start": v(-445.99, -136.5) * mm, "end": v(-446.54, -135.48) * mm});
            skLineSegment(sketch, "E7856", {"start": v(-446.54, -135.48) * mm, "end": v(-447.05, -134.32) * mm});
            skLineSegment(sketch, "E7857", {"start": v(-447.05, -134.32) * mm, "end": v(-447.52, -133.03) * mm});
            skLineSegment(sketch, "E7858", {"start": v(-447.52, -133.03) * mm, "end": v(-447.95, -131.62) * mm});
            skLineSegment(sketch, "E7859", {"start": v(-447.95, -131.62) * mm, "end": v(-448.34, -130.1) * mm});
            skLineSegment(sketch, "E7860", {"start": v(-448.34, -130.1) * mm, "end": v(-448.69, -128.49) * mm});
            skLineSegment(sketch, "E7861", {"start": v(-448.69, -128.49) * mm, "end": v(-449, -126.77) * mm});
            skLineSegment(sketch, "E7862", {"start": v(-449, -126.77) * mm, "end": v(-449.26, -124.98) * mm});
            skLineSegment(sketch, "E7863", {"start": v(-449.26, -124.98) * mm, "end": v(-449.5, -123.11) * mm});
            skLineSegment(sketch, "E7864", {"start": v(-449.5, -123.11) * mm, "end": v(-449.69, -121.18) * mm});
            skLineSegment(sketch, "E7865", {"start": v(-449.69, -121.18) * mm, "end": v(-449.84, -119.2) * mm});
            skLineSegment(sketch, "E7866", {"start": v(-449.84, -119.2) * mm, "end": v(-449.96, -117.16) * mm});
            skLineSegment(sketch, "E7867", {"start": v(-449.96, -117.16) * mm, "end": v(-450.03, -115.1) * mm});
            skLineSegment(sketch, "E7868", {"start": v(-450.03, -115.1) * mm, "end": v(-450.07, -113) * mm});
            skLineSegment(sketch, "E7869", {"start": v(-450.07, -113) * mm, "end": v(-450.07, -110.89) * mm});
            skLineSegment(sketch, "E7870", {"start": v(-450.07, -110.89) * mm, "end": v(-450.04, -108.77) * mm});
            skLineSegment(sketch, "E7871", {"start": v(-450.04, -108.77) * mm, "end": v(-449.96, -106.65) * mm});
            skLineSegment(sketch, "E7872", {"start": v(-449.96, -106.65) * mm, "end": v(-449.85, -104.54) * mm});
            skLineSegment(sketch, "E7873", {"start": v(-449.85, -104.54) * mm, "end": v(-449.7, -102.45) * mm});
            skLineSegment(sketch, "E7874", {"start": v(-449.7, -102.45) * mm, "end": v(-449.53, -100.39) * mm});
            skLineSegment(sketch, "E7875", {"start": v(-449.53, -100.39) * mm, "end": v(-449.3, -98.36) * mm});
            skLineSegment(sketch, "E7876", {"start": v(-449.3, -98.36) * mm, "end": v(-449.05, -96.4) * mm});
            skLineSegment(sketch, "E7877", {"start": v(-449.05, -96.4) * mm, "end": v(-448.76, -94.47) * mm});
            skLineSegment(sketch, "E7878", {"start": v(-448.76, -94.47) * mm, "end": v(-448.43, -92.62) * mm});
            skLineSegment(sketch, "E7879", {"start": v(-448.43, -92.62) * mm, "end": v(-448.07, -90.84) * mm});
            skLineSegment(sketch, "E7880", {"start": v(-448.07, -90.84) * mm, "end": v(-447.68, -89.15) * mm});
            skLineSegment(sketch, "E7881", {"start": v(-447.68, -89.15) * mm, "end": v(-447.25, -87.56) * mm});
            skLineSegment(sketch, "E7882", {"start": v(-447.25, -87.56) * mm, "end": v(-446.78, -86.06) * mm});
            skLineSegment(sketch, "E7883", {"start": v(-446.78, -86.06) * mm, "end": v(-446.28, -84.68) * mm});
            skLineSegment(sketch, "E7884", {"start": v(-446.28, -84.68) * mm, "end": v(-445.75, -83.42) * mm});
            skLineSegment(sketch, "E7885", {"start": v(-445.75, -83.42) * mm, "end": v(-445.18, -82.3) * mm});
            skLineSegment(sketch, "E7886", {"start": v(-445.18, -82.3) * mm, "end": v(-444.58, -81.3) * mm});
            skLineSegment(sketch, "E7887", {"start": v(-444.58, -81.3) * mm, "end": v(-443.95, -80.47) * mm});
            skLineSegment(sketch, "E7888", {"start": v(-443.95, -80.47) * mm, "end": v(-443.29, -79.79) * mm});
            skLineSegment(sketch, "E7889", {"start": v(-443.29, -79.79) * mm, "end": v(-442.59, -79.28) * mm});
            skLineSegment(sketch, "E7890", {"start": v(-442.59, -79.28) * mm, "end": v(-441.4, -78.63) * mm});
            skLineSegment(sketch, "E7891", {"start": v(-441.4, -78.63) * mm, "end": v(-440.14, -78.04) * mm});
            skLineSegment(sketch, "E7892", {"start": v(-440.14, -78.04) * mm, "end": v(-438.8, -77.51) * mm});
            skLineSegment(sketch, "E7893", {"start": v(-438.8, -77.51) * mm, "end": v(-437.4, -77.04) * mm});
            skLineSegment(sketch, "E7894", {"start": v(-437.4, -77.04) * mm, "end": v(-435.92, -76.61) * mm});
            skLineSegment(sketch, "E7895", {"start": v(-435.92, -76.61) * mm, "end": v(-434.38, -76.23) * mm});
            skLineSegment(sketch, "E7896", {"start": v(-434.38, -76.23) * mm, "end": v(-432.78, -75.9) * mm});
            skLineSegment(sketch, "E7897", {"start": v(-432.78, -75.9) * mm, "end": v(-431.12, -75.62) * mm});
            skLineSegment(sketch, "E7898", {"start": v(-431.12, -75.62) * mm, "end": v(-429.41, -75.38) * mm});
            skLineSegment(sketch, "E7899", {"start": v(-429.41, -75.38) * mm, "end": v(-427.65, -75.19) * mm});
            skLineSegment(sketch, "E7900", {"start": v(-427.65, -75.19) * mm, "end": v(-425.85, -75.03) * mm});
            skLineSegment(sketch, "E7901", {"start": v(-425.85, -75.03) * mm, "end": v(-424.01, -74.9) * mm});
            skLineSegment(sketch, "E7902", {"start": v(-424.01, -74.9) * mm, "end": v(-422.13, -74.81) * mm});
            skLineSegment(sketch, "E7903", {"start": v(-422.13, -74.81) * mm, "end": v(-420.23, -74.76) * mm});
            skLineSegment(sketch, "E7904", {"start": v(-420.23, -74.76) * mm, "end": v(-418.29, -74.73) * mm});
            skLineSegment(sketch, "E7905", {"start": v(-418.29, -74.73) * mm, "end": v(-416.33, -74.73) * mm});
            skLineSegment(sketch, "E7906", {"start": v(-416.33, -74.73) * mm, "end": v(-414.34, -74.76) * mm});
            skLineSegment(sketch, "E7907", {"start": v(-414.34, -74.76) * mm, "end": v(-412.34, -74.8) * mm});
            skLineSegment(sketch, "E7908", {"start": v(-412.34, -74.8) * mm, "end": v(-410.33, -74.88) * mm});
            skLineSegment(sketch, "E7909", {"start": v(-410.33, -74.88) * mm, "end": v(-408.31, -74.97) * mm});
            skLineSegment(sketch, "E7910", {"start": v(-408.31, -74.97) * mm, "end": v(-406.3, -75.08) * mm});
            skLineSegment(sketch, "E7911", {"start": v(-406.3, -75.08) * mm, "end": v(-404.27, -75.2) * mm});
            skLineSegment(sketch, "E7912", {"start": v(-404.27, -75.2) * mm, "end": v(-402.24, -75.33) * mm});
            skLineSegment(sketch, "E7913", {"start": v(-402.24, -75.33) * mm, "end": v(-400.23, -75.48) * mm});
            skLineSegment(sketch, "E7914", {"start": v(-400.23, -75.48) * mm, "end": v(-398.23, -75.63) * mm});
            skLineSegment(sketch, "E7915", {"start": v(-398.23, -75.63) * mm, "end": v(-396.24, -75.79) * mm});
            skLineSegment(sketch, "E7916", {"start": v(-396.24, -75.79) * mm, "end": v(-394.27, -75.95) * mm});
            skLineSegment(sketch, "E7917", {"start": v(-394.27, -75.95) * mm, "end": v(-392.33, -76.12) * mm});
            skLineSegment(sketch, "E7918", {"start": v(-392.33, -76.12) * mm, "end": v(-390.41, -76.28) * mm});
            skLineSegment(sketch, "E7919", {"start": v(-390.41, -76.28) * mm, "end": v(-388.53, -76.44) * mm});
            skLineSegment(sketch, "E7920", {"start": v(-388.53, -76.44) * mm, "end": v(-386.68, -76.6) * mm});
            skLineSegment(sketch, "E7921", {"start": v(-386.68, -76.6) * mm, "end": v(-384.86, -76.74) * mm});
            skLineSegment(sketch, "E7922", {"start": v(-384.86, -76.74) * mm, "end": v(-383.1, -76.88) * mm});
            skLineSegment(sketch, "E7923", {"start": v(-383.1, -76.88) * mm, "end": v(-381.37, -77.01) * mm});
            skLineSegment(sketch, "E7924", {"start": v(-381.37, -77.01) * mm, "end": v(-379.7, -77.13) * mm});
            skLineSegment(sketch, "E7925", {"start": v(-379.7, -77.13) * mm, "end": v(-378.09, -77.22) * mm});
            skLineSegment(sketch, "E7926", {"start": v(-378.09, -77.22) * mm, "end": v(-376.53, -77.3) * mm});
            skLineSegment(sketch, "E7927", {"start": v(-376.53, -77.3) * mm, "end": v(-375.04, -77.36) * mm});
            skLineSegment(sketch, "E7928", {"start": v(-375.04, -77.36) * mm, "end": v(-373.6, -77.4) * mm});
            skLineSegment(sketch, "E7929", {"start": v(-373.6, -77.4) * mm, "end": v(-372.25, -77.42) * mm});
            skLineSegment(sketch, "E7930", {"start": v(-372.25, -77.42) * mm, "end": v(-223.8, -77.42) * mm});
            skLineSegment(sketch, "E7931", {"start": v(-223.8, -77.42) * mm, "end": v(-222.34, -77.4) * mm});
            skLineSegment(sketch, "E7932", {"start": v(-222.34, -77.4) * mm, "end": v(-220.81, -77.37) * mm});
            skLineSegment(sketch, "E7933", {"start": v(-220.81, -77.37) * mm, "end": v(-219.23, -77.3) * mm});
            skLineSegment(sketch, "E7934", {"start": v(-219.23, -77.3) * mm, "end": v(-217.6, -77.23) * mm});
            skLineSegment(sketch, "E7935", {"start": v(-217.6, -77.23) * mm, "end": v(-215.94, -77.13) * mm});
            skLineSegment(sketch, "E7936", {"start": v(-215.94, -77.13) * mm, "end": v(-214.23, -77.02) * mm});
            skLineSegment(sketch, "E7937", {"start": v(-214.23, -77.02) * mm, "end": v(-212.48, -76.9) * mm});
            skLineSegment(sketch, "E7938", {"start": v(-212.48, -76.9) * mm, "end": v(-210.7, -76.76) * mm});
            skLineSegment(sketch, "E7939", {"start": v(-210.7, -76.76) * mm, "end": v(-208.88, -76.62) * mm});
            skLineSegment(sketch, "E7940", {"start": v(-208.88, -76.62) * mm, "end": v(-207.03, -76.47) * mm});
            skLineSegment(sketch, "E7941", {"start": v(-207.03, -76.47) * mm, "end": v(-205.16, -76.32) * mm});
            skLineSegment(sketch, "E7942", {"start": v(-205.16, -76.32) * mm, "end": v(-203.28, -76.17) * mm});
            skLineSegment(sketch, "E7943", {"start": v(-203.28, -76.17) * mm, "end": v(-201.37, -76.03) * mm});
            skLineSegment(sketch, "E7944", {"start": v(-201.37, -76.03) * mm, "end": v(-199.45, -75.88) * mm});
            skLineSegment(sketch, "E7945", {"start": v(-199.45, -75.88) * mm, "end": v(-197.52, -75.75) * mm});
            skLineSegment(sketch, "E7946", {"start": v(-197.52, -75.75) * mm, "end": v(-195.59, -75.62) * mm});
            skLineSegment(sketch, "E7947", {"start": v(-195.59, -75.62) * mm, "end": v(-193.65, -75.5) * mm});
            skLineSegment(sketch, "E7948", {"start": v(-193.65, -75.5) * mm, "end": v(-191.7, -75.4) * mm});
            skLineSegment(sketch, "E7949", {"start": v(-191.7, -75.4) * mm, "end": v(-189.77, -75.32) * mm});
            skLineSegment(sketch, "E7950", {"start": v(-189.77, -75.32) * mm, "end": v(-187.84, -75.25) * mm});
            skLineSegment(sketch, "E7951", {"start": v(-187.84, -75.25) * mm, "end": v(-185.92, -75.21) * mm});
            skLineSegment(sketch, "E7952", {"start": v(-185.92, -75.21) * mm, "end": v(-184.01, -75.2) * mm});
            skLineSegment(sketch, "E7953", {"start": v(-184.01, -75.2) * mm, "end": v(-182.12, -75.2) * mm});
            skLineSegment(sketch, "E7954", {"start": v(-182.12, -75.2) * mm, "end": v(-180.26, -75.23) * mm});
            skLineSegment(sketch, "E7955", {"start": v(-180.26, -75.23) * mm, "end": v(-178.41, -75.3) * mm});
            skLineSegment(sketch, "E7956", {"start": v(-178.41, -75.3) * mm, "end": v(-176.6, -75.4) * mm});
            skLineSegment(sketch, "E7957", {"start": v(-176.6, -75.4) * mm, "end": v(-174.81, -75.53) * mm});
            skLineSegment(sketch, "E7958", {"start": v(-174.81, -75.53) * mm, "end": v(-173.06, -75.7) * mm});
            skLineSegment(sketch, "E7959", {"start": v(-173.06, -75.7) * mm, "end": v(-171.35, -75.92) * mm});
            skLineSegment(sketch, "E7960", {"start": v(-171.35, -75.92) * mm, "end": v(-169.68, -76.18) * mm});
            skLineSegment(sketch, "E7961", {"start": v(-169.68, -76.18) * mm, "end": v(-168.05, -76.48) * mm});
            skLineSegment(sketch, "E7962", {"start": v(-168.05, -76.48) * mm, "end": v(-166.47, -76.83) * mm});
            skLineSegment(sketch, "E7963", {"start": v(-166.47, -76.83) * mm, "end": v(-164.95, -77.23) * mm});
            skLineSegment(sketch, "E7964", {"start": v(-164.95, -77.23) * mm, "end": v(-163.48, -77.68) * mm});
            skLineSegment(sketch, "E7965", {"start": v(-163.48, -77.68) * mm, "end": v(-162.06, -78.2) * mm});
            skLineSegment(sketch, "E7966", {"start": v(-162.06, -78.2) * mm, "end": v(-160.71, -78.76) * mm});
            skLineSegment(sketch, "E7967", {"start": v(-160.71, -78.76) * mm, "end": v(-160, -79.18) * mm});
            skLineSegment(sketch, "E7968", {"start": v(-160, -79.18) * mm, "end": v(-159.34, -79.76) * mm});
            skLineSegment(sketch, "E7969", {"start": v(-159.34, -79.76) * mm, "end": v(-158.7, -80.52) * mm});
            skLineSegment(sketch, "E7970", {"start": v(-158.7, -80.52) * mm, "end": v(-158.1, -81.42) * mm});
            skLineSegment(sketch, "E7971", {"start": v(-158.1, -81.42) * mm, "end": v(-157.53, -82.47) * mm});
            skLineSegment(sketch, "E7972", {"start": v(-157.53, -82.47) * mm, "end": v(-157, -83.66) * mm});
            skLineSegment(sketch, "E7973", {"start": v(-157, -83.66) * mm, "end": v(-156.5, -84.97) * mm});
            skLineSegment(sketch, "E7974", {"start": v(-156.5, -84.97) * mm, "end": v(-156.04, -86.4) * mm});
            skLineSegment(sketch, "E7975", {"start": v(-156.04, -86.4) * mm, "end": v(-155.62, -87.94) * mm});
            skLineSegment(sketch, "E7976", {"start": v(-155.62, -87.94) * mm, "end": v(-155.23, -89.58) * mm});
            skLineSegment(sketch, "E7977", {"start": v(-155.23, -89.58) * mm, "end": v(-154.87, -91.3) * mm});
            skLineSegment(sketch, "E7978", {"start": v(-154.87, -91.3) * mm, "end": v(-154.55, -93.11) * mm});
            skLineSegment(sketch, "E7979", {"start": v(-154.55, -93.11) * mm, "end": v(-154.26, -95) * mm});
            skLineSegment(sketch, "E7980", {"start": v(-154.26, -95) * mm, "end": v(-154.01, -96.94) * mm});
            skLineSegment(sketch, "E7981", {"start": v(-154.01, -96.94) * mm, "end": v(-153.8, -98.93) * mm});
            skLineSegment(sketch, "E7982", {"start": v(-153.8, -98.93) * mm, "end": v(-153.62, -100.97) * mm});
            skLineSegment(sketch, "E7983", {"start": v(-153.62, -100.97) * mm, "end": v(-153.47, -103.04) * mm});
            skLineSegment(sketch, "E7984", {"start": v(-153.47, -103.04) * mm, "end": v(-153.36, -105.14) * mm});
            skLineSegment(sketch, "E7985", {"start": v(-153.36, -105.14) * mm, "end": v(-153.29, -107.26) * mm});
            skLineSegment(sketch, "E7986", {"start": v(-153.29, -107.26) * mm, "end": v(-153.25, -109.38) * mm});
            skLineSegment(sketch, "E7987", {"start": v(-153.25, -109.38) * mm, "end": v(-153.24, -111.5) * mm});
            skLineSegment(sketch, "E7988", {"start": v(-153.24, -111.5) * mm, "end": v(-153.28, -113.61) * mm});
            skLineSegment(sketch, "E7989", {"start": v(-153.28, -113.61) * mm, "end": v(-153.34, -115.7) * mm});
            skLineSegment(sketch, "E7990", {"start": v(-153.34, -115.7) * mm, "end": v(-153.44, -117.76) * mm});
            skLineSegment(sketch, "E7991", {"start": v(-153.44, -117.76) * mm, "end": v(-153.58, -119.79) * mm});
            skLineSegment(sketch, "E7992", {"start": v(-153.58, -119.79) * mm, "end": v(-153.75, -121.76) * mm});
            skLineSegment(sketch, "E7993", {"start": v(-153.75, -121.76) * mm, "end": v(-153.96, -123.68) * mm});
            skLineSegment(sketch, "E7994", {"start": v(-153.96, -123.68) * mm, "end": v(-154.2, -125.53) * mm});
            skLineSegment(sketch, "E7995", {"start": v(-154.2, -125.53) * mm, "end": v(-154.48, -127.3) * mm});
            skLineSegment(sketch, "E7996", {"start": v(-154.48, -127.3) * mm, "end": v(-154.8, -129) * mm});
            skLineSegment(sketch, "E7997", {"start": v(-154.8, -129) * mm, "end": v(-155.14, -130.6) * mm});
            skLineSegment(sketch, "E7998", {"start": v(-155.14, -130.6) * mm, "end": v(-155.53, -132.1) * mm});
            skLineSegment(sketch, "E7999", {"start": v(-155.53, -132.1) * mm, "end": v(-155.95, -133.48) * mm});
            skLineSegment(sketch, "E8000", {"start": v(-155.95, -133.48) * mm, "end": v(-156.4, -134.74) * mm});
            skLineSegment(sketch, "E8001", {"start": v(-156.4, -134.74) * mm, "end": v(-156.9, -135.87) * mm});
            skLineSegment(sketch, "E8002", {"start": v(-156.9, -135.87) * mm, "end": v(-157.42, -136.86) * mm});
            skLineSegment(sketch, "E8003", {"start": v(-157.42, -136.86) * mm, "end": v(-157.98, -137.7) * mm});
            skLineSegment(sketch, "E8004", {"start": v(-157.98, -137.7) * mm, "end": v(-158.58, -138.4) * mm});
            skLineSegment(sketch, "E8005", {"start": v(-158.58, -138.4) * mm, "end": v(-159.2, -138.92) * mm});
            skLineSegment(sketch, "E8006", {"start": v(-159.2, -138.92) * mm, "end": v(-160.3, -139.58) * mm});
            skLineSegment(sketch, "E8007", {"start": v(-160.3, -139.58) * mm, "end": v(-161.5, -140.18) * mm});
            skLineSegment(sketch, "E8008", {"start": v(-161.5, -140.18) * mm, "end": v(-162.77, -140.72) * mm});
            skLineSegment(sketch, "E8009", {"start": v(-162.77, -140.72) * mm, "end": v(-164.13, -141.2) * mm});
            skLineSegment(sketch, "E8010", {"start": v(-164.13, -141.2) * mm, "end": v(-165.58, -141.63) * mm});
            skLineSegment(sketch, "E8011", {"start": v(-165.58, -141.63) * mm, "end": v(-167.1, -142) * mm});
            skLineSegment(sketch, "E8012", {"start": v(-167.1, -142) * mm, "end": v(-168.69, -142.33) * mm});
            skLineSegment(sketch, "E8013", {"start": v(-168.69, -142.33) * mm, "end": v(-170.34, -142.6) * mm});
            skLineSegment(sketch, "E8014", {"start": v(-170.34, -142.6) * mm, "end": v(-172.06, -142.83) * mm});
            skLineSegment(sketch, "E8015", {"start": v(-172.06, -142.83) * mm, "end": v(-173.83, -143.02) * mm});
            skLineSegment(sketch, "E8016", {"start": v(-173.83, -143.02) * mm, "end": v(-175.65, -143.16) * mm});
            skLineSegment(sketch, "E8017", {"start": v(-175.65, -143.16) * mm, "end": v(-177.52, -143.27) * mm});
            skLineSegment(sketch, "E8018", {"start": v(-177.52, -143.27) * mm, "end": v(-179.42, -143.34) * mm});
            skLineSegment(sketch, "E8019", {"start": v(-179.42, -143.34) * mm, "end": v(-181.37, -143.38) * mm});
            skLineSegment(sketch, "E8020", {"start": v(-181.37, -143.38) * mm, "end": v(-183.34, -143.39) * mm});
            skLineSegment(sketch, "E8021", {"start": v(-183.34, -143.39) * mm, "end": v(-185.34, -143.36) * mm});
            skLineSegment(sketch, "E8022", {"start": v(-185.34, -143.36) * mm, "end": v(-187.36, -143.32) * mm});
            skLineSegment(sketch, "E8023", {"start": v(-187.36, -143.32) * mm, "end": v(-189.4, -143.25) * mm});
            skLineSegment(sketch, "E8024", {"start": v(-189.4, -143.25) * mm, "end": v(-191.43, -143.16) * mm});
            skLineSegment(sketch, "E8025", {"start": v(-191.43, -143.16) * mm, "end": v(-193.48, -143.05) * mm});
            skLineSegment(sketch, "E8026", {"start": v(-193.48, -143.05) * mm, "end": v(-195.53, -142.92) * mm});
            skLineSegment(sketch, "E8027", {"start": v(-195.53, -142.92) * mm, "end": v(-197.58, -142.78) * mm});
            skLineSegment(sketch, "E8028", {"start": v(-197.58, -142.78) * mm, "end": v(-199.62, -142.63) * mm});
            skLineSegment(sketch, "E8029", {"start": v(-199.62, -142.63) * mm, "end": v(-201.64, -142.48) * mm});
            skLineSegment(sketch, "E8030", {"start": v(-201.64, -142.48) * mm, "end": v(-203.64, -142.31) * mm});
            skLineSegment(sketch, "E8031", {"start": v(-203.64, -142.31) * mm, "end": v(-205.62, -142.14) * mm});
            skLineSegment(sketch, "E8032", {"start": v(-205.62, -142.14) * mm, "end": v(-207.56, -141.98) * mm});
            skLineSegment(sketch, "E8033", {"start": v(-207.56, -141.98) * mm, "end": v(-209.48, -141.8) * mm});
            skLineSegment(sketch, "E8034", {"start": v(-209.48, -141.8) * mm, "end": v(-211.35, -141.65) * mm});
            skLineSegment(sketch, "E8035", {"start": v(-211.35, -141.65) * mm, "end": v(-213.18, -141.5) * mm});
            skLineSegment(sketch, "E8036", {"start": v(-213.18, -141.5) * mm, "end": v(-214.96, -141.34) * mm});
            skLineSegment(sketch, "E8037", {"start": v(-214.96, -141.34) * mm, "end": v(-216.69, -141.2) * mm});
            skLineSegment(sketch, "E8038", {"start": v(-216.69, -141.2) * mm, "end": v(-218.35, -141.09) * mm});
            skLineSegment(sketch, "E8039", {"start": v(-218.35, -141.09) * mm, "end": v(-219.95, -140.98) * mm});
            skLineSegment(sketch, "E8040", {"start": v(-219.95, -140.98) * mm, "end": v(-221.49, -140.9) * mm});
            skLineSegment(sketch, "E8041", {"start": v(-221.49, -140.9) * mm, "end": v(-222.94, -140.83) * mm});
            skLineSegment(sketch, "E8042", {"start": v(-222.94, -140.83) * mm, "end": v(-224.32, -140.8) * mm});
            skLineSegment(sketch, "E8043", {"start": v(-224.32, -140.8) * mm, "end": v(-225.62, -140.78) * mm});
            skLineSegment(sketch, "E8044", {"start": v(-225.62, -140.78) * mm, "end": v(-225.62, -260.26) * mm});
            skLineSegment(sketch, "E8045", {"start": v(-225.62, -260.26) * mm, "end": v(-176.74, -260.26) * mm});
            skLineSegment(sketch, "E8046", {"start": v(-176.74, -260.26) * mm, "end": v(-175.13, -260.23) * mm});
            skLineSegment(sketch, "E8047", {"start": v(-175.13, -260.23) * mm, "end": v(-173.4, -260.16) * mm});
            skLineSegment(sketch, "E8048", {"start": v(-173.4, -260.16) * mm, "end": v(-171.58, -260.08) * mm});
            skLineSegment(sketch, "E8049", {"start": v(-171.58, -260.08) * mm, "end": v(-169.7, -260.02) * mm});
            skLineSegment(sketch, "E8050", {"start": v(-169.7, -260.02) * mm, "end": v(-167.81, -260.03) * mm});
            skLineSegment(sketch, "E8051", {"start": v(-167.81, -260.03) * mm, "end": v(-165.93, -260.13) * mm});
            skLineSegment(sketch, "E8052", {"start": v(-165.93, -260.13) * mm, "end": v(-164.1, -260.35) * mm});
            skLineSegment(sketch, "E8053", {"start": v(-164.1, -260.35) * mm, "end": v(-162.34, -260.73) * mm});
            skLineSegment(sketch, "E8054", {"start": v(-162.34, -260.73) * mm, "end": v(-160.7, -261.3) * mm});
            skLineSegment(sketch, "E8055", {"start": v(-160.7, -261.3) * mm, "end": v(-159.22, -262.1) * mm});
            skLineSegment(sketch, "E8056", {"start": v(-159.22, -262.1) * mm, "end": v(-157.92, -263.16) * mm});
            skLineSegment(sketch, "E8057", {"start": v(-157.92, -263.16) * mm, "end": v(-157.13, -264.07) * mm});
            skLineSegment(sketch, "E8058", {"start": v(-157.13, -264.07) * mm, "end": v(-156.43, -265.11) * mm});
            skLineSegment(sketch, "E8059", {"start": v(-156.43, -265.11) * mm, "end": v(-155.8, -266.3) * mm});
            skLineSegment(sketch, "E8060", {"start": v(-155.8, -266.3) * mm, "end": v(-155.26, -267.6) * mm});
            skLineSegment(sketch, "E8061", {"start": v(-155.26, -267.6) * mm, "end": v(-154.8, -269.02) * mm});
            skLineSegment(sketch, "E8062", {"start": v(-154.8, -269.02) * mm, "end": v(-154.4, -270.55) * mm});
            skLineSegment(sketch, "E8063", {"start": v(-154.4, -270.55) * mm, "end": v(-154.06, -272.17) * mm});
            skLineSegment(sketch, "E8064", {"start": v(-154.06, -272.17) * mm, "end": v(-153.78, -273.89) * mm});
            skLineSegment(sketch, "E8065", {"start": v(-153.78, -273.89) * mm, "end": v(-153.56, -275.68) * mm});
            skLineSegment(sketch, "E8066", {"start": v(-153.56, -275.68) * mm, "end": v(-153.4, -277.54) * mm});
            skLineSegment(sketch, "E8067", {"start": v(-153.4, -277.54) * mm, "end": v(-153.28, -279.46) * mm});
            skLineSegment(sketch, "E8068", {"start": v(-153.28, -279.46) * mm, "end": v(-153.2, -281.43) * mm});
            skLineSegment(sketch, "E8069", {"start": v(-153.2, -281.43) * mm, "end": v(-153.17, -283.44) * mm});
            skLineSegment(sketch, "E8070", {"start": v(-153.17, -283.44) * mm, "end": v(-153.18, -285.5) * mm});
            skLineSegment(sketch, "E8071", {"start": v(-153.18, -285.5) * mm, "end": v(-153.22, -287.56) * mm});
            skLineSegment(sketch, "E8072", {"start": v(-153.22, -287.56) * mm, "end": v(-153.28, -289.64) * mm});
            skLineSegment(sketch, "E8073", {"start": v(-153.28, -289.64) * mm, "end": v(-153.38, -291.73) * mm});
            skLineSegment(sketch, "E8074", {"start": v(-153.38, -291.73) * mm, "end": v(-153.49, -293.82) * mm});
            skLineSegment(sketch, "E8075", {"start": v(-153.49, -293.82) * mm, "end": v(-153.62, -295.9) * mm});
            skLineSegment(sketch, "E8076", {"start": v(-153.62, -295.9) * mm, "end": v(-153.76, -297.94) * mm});
            skLineSegment(sketch, "E8077", {"start": v(-153.76, -297.94) * mm, "end": v(-153.91, -299.96) * mm});
            skLineSegment(sketch, "E8078", {"start": v(-153.91, -299.96) * mm, "end": v(-154.07, -301.94) * mm});
            skLineSegment(sketch, "E8079", {"start": v(-154.07, -301.94) * mm, "end": v(-154.22, -303.86) * mm});
            skLineSegment(sketch, "E8080", {"start": v(-154.22, -303.86) * mm, "end": v(-154.37, -305.73) * mm});
            skLineSegment(sketch, "E8081", {"start": v(-154.37, -305.73) * mm, "end": v(-154.52, -307.53) * mm});
            skLineSegment(sketch, "E8082", {"start": v(-154.52, -307.53) * mm, "end": v(-154.65, -309.25) * mm});
            skLineSegment(sketch, "E8083", {"start": v(-154.65, -309.25) * mm, "end": v(-154.77, -310.89) * mm});
            skLineSegment(sketch, "E8084", {"start": v(-154.77, -310.89) * mm, "end": v(-154.87, -312.43) * mm});
            skLineSegment(sketch, "E8085", {"start": v(-154.87, -312.43) * mm, "end": v(-154.95, -313.86) * mm});
            skLineSegment(sketch, "E8086", {"start": v(-154.95, -313.86) * mm, "end": v(-155, -315.18) * mm});
            skLineSegment(sketch, "E8087", {"start": v(-155, -315.18) * mm, "end": v(-155.01, -316.38) * mm});
            skLineSegment(sketch, "E8088", {"start": v(-155.01, -316.38) * mm, "end": v(-153.76, -315.6) * mm});
            skLineSegment(sketch, "E8089", {"start": v(-153.76, -315.6) * mm, "end": v(-152.61, -314.72) * mm});
            skLineSegment(sketch, "E8090", {"start": v(-152.61, -314.72) * mm, "end": v(-151.56, -313.74) * mm});
            skLineSegment(sketch, "E8091", {"start": v(-151.56, -313.74) * mm, "end": v(-150.6, -312.67) * mm});
            skLineSegment(sketch, "E8092", {"start": v(-150.6, -312.67) * mm, "end": v(-149.72, -311.51) * mm});
            skLineSegment(sketch, "E8093", {"start": v(-149.72, -311.51) * mm, "end": v(-148.92, -310.28) * mm});
            skLineSegment(sketch, "E8094", {"start": v(-148.92, -310.28) * mm, "end": v(-148.21, -308.97) * mm});
            skLineSegment(sketch, "E8095", {"start": v(-148.21, -308.97) * mm, "end": v(-147.58, -307.59) * mm});
            skLineSegment(sketch, "E8096", {"start": v(-147.58, -307.59) * mm, "end": v(-147.02, -306.14) * mm});
            skLineSegment(sketch, "E8097", {"start": v(-147.02, -306.14) * mm, "end": v(-146.52, -304.63) * mm});
            skLineSegment(sketch, "E8098", {"start": v(-146.52, -304.63) * mm, "end": v(-146.1, -303.06) * mm});
            skLineSegment(sketch, "E8099", {"start": v(-146.1, -303.06) * mm, "end": v(-145.73, -301.45) * mm});
            skLineSegment(sketch, "E8100", {"start": v(-145.73, -301.45) * mm, "end": v(-145.42, -299.78) * mm});
            skLineSegment(sketch, "E8101", {"start": v(-145.42, -299.78) * mm, "end": v(-145.17, -298.08) * mm});
            skLineSegment(sketch, "E8102", {"start": v(-145.17, -298.08) * mm, "end": v(-144.97, -296.34) * mm});
            skLineSegment(sketch, "E8103", {"start": v(-144.97, -296.34) * mm, "end": v(-144.82, -294.57) * mm});
            skLineSegment(sketch, "E8104", {"start": v(-144.82, -294.57) * mm, "end": v(-144.7, -292.77) * mm});
            skLineSegment(sketch, "E8105", {"start": v(-144.7, -292.77) * mm, "end": v(-144.64, -290.96) * mm});
            skLineSegment(sketch, "E8106", {"start": v(-144.64, -290.96) * mm, "end": v(-144.6, -289.12) * mm});
            skLineSegment(sketch, "E8107", {"start": v(-144.6, -289.12) * mm, "end": v(-144.6, -287.28) * mm});
            skLineSegment(sketch, "E8108", {"start": v(-144.6, -287.28) * mm, "end": v(-144.63, -285.42) * mm});
            skLineSegment(sketch, "E8109", {"start": v(-144.63, -285.42) * mm, "end": v(-144.68, -283.57) * mm});
            skLineSegment(sketch, "E8110", {"start": v(-144.68, -283.57) * mm, "end": v(-144.75, -281.72) * mm});
            skLineSegment(sketch, "E8111", {"start": v(-144.75, -281.72) * mm, "end": v(-144.84, -279.88) * mm});
            skLineSegment(sketch, "E8112", {"start": v(-144.84, -279.88) * mm, "end": v(-144.95, -278.05) * mm});
            skLineSegment(sketch, "E8113", {"start": v(-144.95, -278.05) * mm, "end": v(-145.06, -276.24) * mm});
            skLineSegment(sketch, "E8114", {"start": v(-145.06, -276.24) * mm, "end": v(-145.18, -274.46) * mm});
            skLineSegment(sketch, "E8115", {"start": v(-145.18, -274.46) * mm, "end": v(-145.3, -272.7) * mm});
            skLineSegment(sketch, "E8116", {"start": v(-145.3, -272.7) * mm, "end": v(-145.43, -270.98) * mm});
            skLineSegment(sketch, "E8117", {"start": v(-145.43, -270.98) * mm, "end": v(-145.55, -269.3) * mm});
            skLineSegment(sketch, "E8118", {"start": v(-145.55, -269.3) * mm, "end": v(-145.66, -267.65) * mm});
            skLineSegment(sketch, "E8119", {"start": v(-145.66, -267.65) * mm, "end": v(-145.76, -266.05) * mm});
            skLineSegment(sketch, "E8120", {"start": v(-145.76, -266.05) * mm, "end": v(-145.84, -264.51) * mm});
            skLineSegment(sketch, "E8121", {"start": v(-145.84, -264.51) * mm, "end": v(-145.9, -263.03) * mm});
            skLineSegment(sketch, "E8122", {"start": v(-145.9, -263.03) * mm, "end": v(-145.95, -261.61) * mm});
            skLineSegment(sketch, "E8123", {"start": v(-145.95, -261.61) * mm, "end": v(-145.96, -260.26) * mm});
            skLineSegment(sketch, "E8124", {"start": v(-145.96, -260.26) * mm, "end": v(-77.17, -260.26) * mm});
            skLineSegment(sketch, "E8125", {"start": v(-77.17, -260.26) * mm, "end": v(-77.17, -138.97) * mm});
            skLineSegment(sketch, "E8126", {"start": v(-77.17, -138.97) * mm, "end": v(-145.96, -138.97) * mm});
            skLineSegment(sketch, "E8127", {"start": v(-145.96, -138.97) * mm, "end": v(-145.98, -137.8) * mm});
            skLineSegment(sketch, "E8128", {"start": v(-145.98, -137.8) * mm, "end": v(-146.02, -136.53) * mm});
            skLineSegment(sketch, "E8129", {"start": v(-146.02, -136.53) * mm, "end": v(-146.1, -135.14) * mm});
            skLineSegment(sketch, "E8130", {"start": v(-146.1, -135.14) * mm, "end": v(-146.18, -133.65) * mm});
            skLineSegment(sketch, "E8131", {"start": v(-146.18, -133.65) * mm, "end": v(-146.3, -132.06) * mm});
            skLineSegment(sketch, "E8132", {"start": v(-146.3, -132.06) * mm, "end": v(-146.42, -130.38) * mm});
            skLineSegment(sketch, "E8133", {"start": v(-146.42, -130.38) * mm, "end": v(-146.56, -128.63) * mm});
            skLineSegment(sketch, "E8134", {"start": v(-146.56, -128.63) * mm, "end": v(-146.71, -126.8) * mm});
            skLineSegment(sketch, "E8135", {"start": v(-146.71, -126.8) * mm, "end": v(-146.87, -124.9) * mm});
            skLineSegment(sketch, "E8136", {"start": v(-146.87, -124.9) * mm, "end": v(-147.03, -122.96) * mm});
            skLineSegment(sketch, "E8137", {"start": v(-147.03, -122.96) * mm, "end": v(-147.19, -120.97) * mm});
            skLineSegment(sketch, "E8138", {"start": v(-147.19, -120.97) * mm, "end": v(-147.34, -118.94) * mm});
            skLineSegment(sketch, "E8139", {"start": v(-147.34, -118.94) * mm, "end": v(-147.49, -116.87) * mm});
            skLineSegment(sketch, "E8140", {"start": v(-147.49, -116.87) * mm, "end": v(-147.62, -114.78) * mm});
            skLineSegment(sketch, "E8141", {"start": v(-147.62, -114.78) * mm, "end": v(-147.74, -112.68) * mm});
            skLineSegment(sketch, "E8142", {"start": v(-147.74, -112.68) * mm, "end": v(-147.85, -110.57) * mm});
            skLineSegment(sketch, "E8143", {"start": v(-147.85, -110.57) * mm, "end": v(-147.93, -108.46) * mm});
            skLineSegment(sketch, "E8144", {"start": v(-147.93, -108.46) * mm, "end": v(-148, -106.36) * mm});
            skLineSegment(sketch, "E8145", {"start": v(-148, -106.36) * mm, "end": v(-148.03, -104.28) * mm});
            skLineSegment(sketch, "E8146", {"start": v(-148.03, -104.28) * mm, "end": v(-148.03, -102.22) * mm});
            skLineSegment(sketch, "E8147", {"start": v(-148.03, -102.22) * mm, "end": v(-148, -100.2) * mm});
            skLineSegment(sketch, "E8148", {"start": v(-148, -100.2) * mm, "end": v(-147.93, -98.22) * mm});
            skLineSegment(sketch, "E8149", {"start": v(-147.93, -98.22) * mm, "end": v(-147.83, -96.28) * mm});
            skLineSegment(sketch, "E8150", {"start": v(-147.83, -96.28) * mm, "end": v(-147.68, -94.4) * mm});
            skLineSegment(sketch, "E8151", {"start": v(-147.68, -94.4) * mm, "end": v(-147.48, -92.6) * mm});
            skLineSegment(sketch, "E8152", {"start": v(-147.48, -92.6) * mm, "end": v(-147.23, -90.86) * mm});
            skLineSegment(sketch, "E8153", {"start": v(-147.23, -90.86) * mm, "end": v(-146.93, -89.2) * mm});
            skLineSegment(sketch, "E8154", {"start": v(-146.93, -89.2) * mm, "end": v(-146.58, -87.64) * mm});
            skLineSegment(sketch, "E8155", {"start": v(-146.58, -87.64) * mm, "end": v(-146.16, -86.17) * mm});
            skLineSegment(sketch, "E8156", {"start": v(-146.16, -86.17) * mm, "end": v(-145.68, -84.8) * mm});
            skLineSegment(sketch, "E8157", {"start": v(-145.68, -84.8) * mm, "end": v(-145.13, -83.56) * mm});
            skLineSegment(sketch, "E8158", {"start": v(-145.13, -83.56) * mm, "end": v(-144.51, -82.43) * mm});
            skLineSegment(sketch, "E8159", {"start": v(-144.51, -82.43) * mm, "end": v(-143.82, -81.43) * mm});
            skLineSegment(sketch, "E8160", {"start": v(-143.82, -81.43) * mm, "end": v(-143.06, -80.57) * mm});
            skLineSegment(sketch, "E8161", {"start": v(-437.42, 121.72) * mm, "end": v(-437.42, 188.7) * mm});
            skLineSegment(sketch, "E8162", {"start": v(-437.42, 188.7) * mm, "end": v(-439.36, 188.51) * mm});
            skLineSegment(sketch, "E8163", {"start": v(-439.36, 188.51) * mm, "end": v(-441.22, 188.28) * mm});
            skLineSegment(sketch, "E8164", {"start": v(-441.22, 188.28) * mm, "end": v(-443, 188) * mm});
            skLineSegment(sketch, "E8165", {"start": v(-443, 188) * mm, "end": v(-444.72, 187.66) * mm});
            skLineSegment(sketch, "E8166", {"start": v(-444.72, 187.66) * mm, "end": v(-446.36, 187.28) * mm});
            skLineSegment(sketch, "E8167", {"start": v(-446.36, 187.28) * mm, "end": v(-447.94, 186.86) * mm});
            skLineSegment(sketch, "E8168", {"start": v(-447.94, 186.86) * mm, "end": v(-449.44, 186.4) * mm});
            skLineSegment(sketch, "E8169", {"start": v(-449.44, 186.4) * mm, "end": v(-450.88, 185.9) * mm});
            skLineSegment(sketch, "E8170", {"start": v(-450.88, 185.9) * mm, "end": v(-452.24, 185.34) * mm});
            skLineSegment(sketch, "E8171", {"start": v(-452.24, 185.34) * mm, "end": v(-453.54, 184.75) * mm});
            skLineSegment(sketch, "E8172", {"start": v(-453.54, 184.75) * mm, "end": v(-454.77, 184.13) * mm});
            skLineSegment(sketch, "E8173", {"start": v(-454.77, 184.13) * mm, "end": v(-455.94, 183.47) * mm});
            skLineSegment(sketch, "E8174", {"start": v(-455.94, 183.47) * mm, "end": v(-457.04, 182.77) * mm});
            skLineSegment(sketch, "E8175", {"start": v(-457.04, 182.77) * mm, "end": v(-458.08, 182.03) * mm});
            skLineSegment(sketch, "E8176", {"start": v(-458.08, 182.03) * mm, "end": v(-459.06, 181.27) * mm});
            skLineSegment(sketch, "E8177", {"start": v(-459.06, 181.27) * mm, "end": v(-459.97, 180.47) * mm});
            skLineSegment(sketch, "E8178", {"start": v(-459.97, 180.47) * mm, "end": v(-460.82, 179.64) * mm});
            skLineSegment(sketch, "E8179", {"start": v(-460.82, 179.64) * mm, "end": v(-461.61, 178.78) * mm});
            skLineSegment(sketch, "E8180", {"start": v(-461.61, 178.78) * mm, "end": v(-462.35, 177.89) * mm});
            skLineSegment(sketch, "E8181", {"start": v(-462.35, 177.89) * mm, "end": v(-463.02, 176.97) * mm});
            skLineSegment(sketch, "E8182", {"start": v(-463.02, 176.97) * mm, "end": v(-463.63, 176.03) * mm});
            skLineSegment(sketch, "E8183", {"start": v(-463.63, 176.03) * mm, "end": v(-464.19, 175.06) * mm});
            skLineSegment(sketch, "E8184", {"start": v(-464.19, 175.06) * mm, "end": v(-464.7, 174.07) * mm});
            skLineSegment(sketch, "E8185", {"start": v(-464.7, 174.07) * mm, "end": v(-465.14, 173.05) * mm});
            skLineSegment(sketch, "E8186", {"start": v(-465.14, 173.05) * mm, "end": v(-465.53, 172.02) * mm});
            skLineSegment(sketch, "E8187", {"start": v(-465.53, 172.02) * mm, "end": v(-465.86, 170.96) * mm});
            skLineSegment(sketch, "E8188", {"start": v(-465.86, 170.96) * mm, "end": v(-466.15, 169.89) * mm});
            skLineSegment(sketch, "E8189", {"start": v(-466.15, 169.89) * mm, "end": v(-466.38, 168.8) * mm});
            skLineSegment(sketch, "E8190", {"start": v(-466.38, 168.8) * mm, "end": v(-466.56, 167.69) * mm});
            skLineSegment(sketch, "E8191", {"start": v(-466.56, 167.69) * mm, "end": v(-466.69, 166.56) * mm});
            skLineSegment(sketch, "E8192", {"start": v(-466.69, 166.56) * mm, "end": v(-466.77, 165.43) * mm});
            skLineSegment(sketch, "E8193", {"start": v(-466.77, 165.43) * mm, "end": v(-466.8, 164.28) * mm});
            skLineSegment(sketch, "E8194", {"start": v(-466.8, 164.28) * mm, "end": v(-466.78, 163.11) * mm});
            skLineSegment(sketch, "E8195", {"start": v(-466.78, 163.11) * mm, "end": v(-466.71, 161.94) * mm});
            skLineSegment(sketch, "E8196", {"start": v(-466.71, 161.94) * mm, "end": v(-466.6, 160.76) * mm});
            skLineSegment(sketch, "E8197", {"start": v(-466.6, 160.76) * mm, "end": v(-466.44, 159.57) * mm});
            skLineSegment(sketch, "E8198", {"start": v(-466.44, 159.57) * mm, "end": v(-466.24, 158.37) * mm});
            skLineSegment(sketch, "E8199", {"start": v(-466.24, 158.37) * mm, "end": v(-466, 157.17) * mm});
            skLineSegment(sketch, "E8200", {"start": v(-466, 157.17) * mm, "end": v(-465.7, 155.97) * mm});
            skLineSegment(sketch, "E8201", {"start": v(-465.7, 155.97) * mm, "end": v(-465.38, 154.76) * mm});
            skLineSegment(sketch, "E8202", {"start": v(-465.38, 154.76) * mm, "end": v(-465, 153.54) * mm});
            skLineSegment(sketch, "E8203", {"start": v(-465, 153.54) * mm, "end": v(-464.6, 152.33) * mm});
            skLineSegment(sketch, "E8204", {"start": v(-464.6, 152.33) * mm, "end": v(-464.14, 151.12) * mm});
            skLineSegment(sketch, "E8205", {"start": v(-464.14, 151.12) * mm, "end": v(-463.65, 149.91) * mm});
            skLineSegment(sketch, "E8206", {"start": v(-463.65, 149.91) * mm, "end": v(-463.12, 148.7) * mm});
            skLineSegment(sketch, "E8207", {"start": v(-463.12, 148.7) * mm, "end": v(-462.55, 147.5) * mm});
            skLineSegment(sketch, "E8208", {"start": v(-462.55, 147.5) * mm, "end": v(-461.94, 146.3) * mm});
            skLineSegment(sketch, "E8209", {"start": v(-461.94, 146.3) * mm, "end": v(-461.3, 145.12) * mm});
            skLineSegment(sketch, "E8210", {"start": v(-461.3, 145.12) * mm, "end": v(-460.63, 143.94) * mm});
            skLineSegment(sketch, "E8211", {"start": v(-460.63, 143.94) * mm, "end": v(-459.92, 142.76) * mm});
            skLineSegment(sketch, "E8212", {"start": v(-459.92, 142.76) * mm, "end": v(-459.18, 141.6) * mm});
            skLineSegment(sketch, "E8213", {"start": v(-459.18, 141.6) * mm, "end": v(-458.4, 140.45) * mm});
            skLineSegment(sketch, "E8214", {"start": v(-458.4, 140.45) * mm, "end": v(-457.6, 139.3) * mm});
            skLineSegment(sketch, "E8215", {"start": v(-457.6, 139.3) * mm, "end": v(-456.76, 138.19) * mm});
            skLineSegment(sketch, "E8216", {"start": v(-456.76, 138.19) * mm, "end": v(-455.9, 137.08) * mm});
            skLineSegment(sketch, "E8217", {"start": v(-455.9, 137.08) * mm, "end": v(-455, 135.98) * mm});
            skLineSegment(sketch, "E8218", {"start": v(-455, 135.98) * mm, "end": v(-454.08, 134.9) * mm});
            skLineSegment(sketch, "E8219", {"start": v(-454.08, 134.9) * mm, "end": v(-453.13, 133.85) * mm});
            skLineSegment(sketch, "E8220", {"start": v(-453.13, 133.85) * mm, "end": v(-452.15, 132.81) * mm});
            skLineSegment(sketch, "E8221", {"start": v(-452.15, 132.81) * mm, "end": v(-451.15, 131.8) * mm});
            skLineSegment(sketch, "E8222", {"start": v(-451.15, 131.8) * mm, "end": v(-450.12, 130.8) * mm});
            skLineSegment(sketch, "E8223", {"start": v(-450.12, 130.8) * mm, "end": v(-449.07, 129.84) * mm});
            skLineSegment(sketch, "E8224", {"start": v(-449.07, 129.84) * mm, "end": v(-448, 128.9) * mm});
            skLineSegment(sketch, "E8225", {"start": v(-448, 128.9) * mm, "end": v(-446.9, 127.98) * mm});
            skLineSegment(sketch, "E8226", {"start": v(-446.9, 127.98) * mm, "end": v(-445.78, 127.09) * mm});
            skLineSegment(sketch, "E8227", {"start": v(-445.78, 127.09) * mm, "end": v(-444.65, 126.22) * mm});
            skLineSegment(sketch, "E8228", {"start": v(-444.65, 126.22) * mm, "end": v(-443.49, 125.4) * mm});
            skLineSegment(sketch, "E8229", {"start": v(-443.49, 125.4) * mm, "end": v(-442.3, 124.6) * mm});
            skLineSegment(sketch, "E8230", {"start": v(-442.3, 124.6) * mm, "end": v(-441.11, 123.82) * mm});
            skLineSegment(sketch, "E8231", {"start": v(-441.11, 123.82) * mm, "end": v(-439.9, 123.09) * mm});
            skLineSegment(sketch, "E8232", {"start": v(-439.9, 123.09) * mm, "end": v(-438.67, 122.39) * mm});
            skLineSegment(sketch, "E8233", {"start": v(-438.67, 122.39) * mm, "end": v(-437.42, 121.72) * mm});
            skLineSegment(sketch, "E8234", {"start": v(438.77, 157.93) * mm, "end": v(438.77, 94.57) * mm});
            skLineSegment(sketch, "E8235", {"start": v(438.77, 94.57) * mm, "end": v(440, 94.74) * mm});
            skLineSegment(sketch, "E8236", {"start": v(440, 94.74) * mm, "end": v(441.24, 94.96) * mm});
            skLineSegment(sketch, "E8237", {"start": v(441.24, 94.96) * mm, "end": v(442.5, 95.2) * mm});
            skLineSegment(sketch, "E8238", {"start": v(442.5, 95.2) * mm, "end": v(443.77, 95.5) * mm});
            skLineSegment(sketch, "E8239", {"start": v(443.77, 95.5) * mm, "end": v(445.06, 95.82) * mm});
            skLineSegment(sketch, "E8240", {"start": v(445.06, 95.82) * mm, "end": v(446.35, 96.18) * mm});
            skLineSegment(sketch, "E8241", {"start": v(446.35, 96.18) * mm, "end": v(447.66, 96.57) * mm});
            skLineSegment(sketch, "E8242", {"start": v(447.66, 96.57) * mm, "end": v(448.97, 97) * mm});
            skLineSegment(sketch, "E8243", {"start": v(448.97, 97) * mm, "end": v(450.28, 97.46) * mm});
            skLineSegment(sketch, "E8244", {"start": v(450.28, 97.46) * mm, "end": v(451.6, 97.96) * mm});
            skLineSegment(sketch, "E8245", {"start": v(451.6, 97.96) * mm, "end": v(452.92, 98.49) * mm});
            skLineSegment(sketch, "E8246", {"start": v(452.92, 98.49) * mm, "end": v(454.23, 99.04) * mm});
            skLineSegment(sketch, "E8247", {"start": v(454.23, 99.04) * mm, "end": v(455.54, 99.63) * mm});
            skLineSegment(sketch, "E8248", {"start": v(455.54, 99.63) * mm, "end": v(456.84, 100.25) * mm});
            skLineSegment(sketch, "E8249", {"start": v(456.84, 100.25) * mm, "end": v(458.13, 100.9) * mm});
            skLineSegment(sketch, "E8250", {"start": v(458.13, 100.9) * mm, "end": v(459.42, 101.58) * mm});
            skLineSegment(sketch, "E8251", {"start": v(459.42, 101.58) * mm, "end": v(460.68, 102.29) * mm});
            skLineSegment(sketch, "E8252", {"start": v(460.68, 102.29) * mm, "end": v(461.93, 103.02) * mm});
            skLineSegment(sketch, "E8253", {"start": v(461.93, 103.02) * mm, "end": v(463.17, 103.78) * mm});
            skLineSegment(sketch, "E8254", {"start": v(463.17, 103.78) * mm, "end": v(464.38, 104.56) * mm});
            skLineSegment(sketch, "E8255", {"start": v(464.38, 104.56) * mm, "end": v(465.57, 105.38) * mm});
            skLineSegment(sketch, "E8256", {"start": v(465.57, 105.38) * mm, "end": v(466.74, 106.21) * mm});
            skLineSegment(sketch, "E8257", {"start": v(466.74, 106.21) * mm, "end": v(467.88, 107.07) * mm});
            skLineSegment(sketch, "E8258", {"start": v(467.88, 107.07) * mm, "end": v(468.99, 107.95) * mm});
            skLineSegment(sketch, "E8259", {"start": v(468.99, 107.95) * mm, "end": v(470.06, 108.86) * mm});
            skLineSegment(sketch, "E8260", {"start": v(470.06, 108.86) * mm, "end": v(471.1, 109.79) * mm});
            skLineSegment(sketch, "E8261", {"start": v(471.1, 109.79) * mm, "end": v(472.12, 110.74) * mm});
            skLineSegment(sketch, "E8262", {"start": v(472.12, 110.74) * mm, "end": v(473.09, 111.7) * mm});
            skLineSegment(sketch, "E8263", {"start": v(473.09, 111.7) * mm, "end": v(474.02, 112.7) * mm});
            skLineSegment(sketch, "E8264", {"start": v(474.02, 112.7) * mm, "end": v(474.91, 113.7) * mm});
            skLineSegment(sketch, "E8265", {"start": v(474.91, 113.7) * mm, "end": v(475.75, 114.74) * mm});
            skLineSegment(sketch, "E8266", {"start": v(475.75, 114.74) * mm, "end": v(476.55, 115.78) * mm});
            skLineSegment(sketch, "E8267", {"start": v(476.55, 115.78) * mm, "end": v(477.3, 116.85) * mm});
            skLineSegment(sketch, "E8268", {"start": v(477.3, 116.85) * mm, "end": v(478, 117.93) * mm});
            skLineSegment(sketch, "E8269", {"start": v(478, 117.93) * mm, "end": v(478.64, 119.02) * mm});
            skLineSegment(sketch, "E8270", {"start": v(478.64, 119.02) * mm, "end": v(479.23, 120.14) * mm});
            skLineSegment(sketch, "E8271", {"start": v(479.23, 120.14) * mm, "end": v(479.76, 121.26) * mm});
            skLineSegment(sketch, "E8272", {"start": v(479.76, 121.26) * mm, "end": v(480.23, 122.4) * mm});
            skLineSegment(sketch, "E8273", {"start": v(480.23, 122.4) * mm, "end": v(480.64, 123.56) * mm});
            skLineSegment(sketch, "E8274", {"start": v(480.64, 123.56) * mm, "end": v(480.99, 124.72) * mm});
            skLineSegment(sketch, "E8275", {"start": v(480.99, 124.72) * mm, "end": v(481.27, 125.9) * mm});
            skLineSegment(sketch, "E8276", {"start": v(481.27, 125.9) * mm, "end": v(481.47, 127.1) * mm});
            skLineSegment(sketch, "E8277", {"start": v(481.47, 127.1) * mm, "end": v(481.61, 128.3) * mm});
            skLineSegment(sketch, "E8278", {"start": v(481.61, 128.3) * mm, "end": v(481.68, 129.5) * mm});
            skLineSegment(sketch, "E8279", {"start": v(481.68, 129.5) * mm, "end": v(481.67, 130.72) * mm});
            skLineSegment(sketch, "E8280", {"start": v(481.67, 130.72) * mm, "end": v(481.58, 131.95) * mm});
            skLineSegment(sketch, "E8281", {"start": v(481.58, 131.95) * mm, "end": v(481.41, 133.19) * mm});
            skLineSegment(sketch, "E8282", {"start": v(481.41, 133.19) * mm, "end": v(481.16, 134.43) * mm});
            skLineSegment(sketch, "E8283", {"start": v(481.16, 134.43) * mm, "end": v(480.83, 135.68) * mm});
            skLineSegment(sketch, "E8284", {"start": v(480.83, 135.68) * mm, "end": v(480.4, 136.94) * mm});
            skLineSegment(sketch, "E8285", {"start": v(480.4, 136.94) * mm, "end": v(479.9, 138.2) * mm});
            skLineSegment(sketch, "E8286", {"start": v(479.9, 138.2) * mm, "end": v(479.3, 139.46) * mm});
            skLineSegment(sketch, "E8287", {"start": v(479.3, 139.46) * mm, "end": v(478.6, 140.73) * mm});
            skLineSegment(sketch, "E8288", {"start": v(478.6, 140.73) * mm, "end": v(477.82, 142) * mm});
            skLineSegment(sketch, "E8289", {"start": v(477.82, 142) * mm, "end": v(476.94, 143.28) * mm});
            skLineSegment(sketch, "E8290", {"start": v(476.94, 143.28) * mm, "end": v(475.95, 144.56) * mm});
            skLineSegment(sketch, "E8291", {"start": v(475.95, 144.56) * mm, "end": v(474.86, 145.84) * mm});
            skLineSegment(sketch, "E8292", {"start": v(474.86, 145.84) * mm, "end": v(473.67, 147.12) * mm});
            skLineSegment(sketch, "E8293", {"start": v(473.67, 147.12) * mm, "end": v(472.38, 148.4) * mm});
            skLineSegment(sketch, "E8294", {"start": v(472.38, 148.4) * mm, "end": v(470.97, 149.68) * mm});
            skLineSegment(sketch, "E8295", {"start": v(470.97, 149.68) * mm, "end": v(469.55, 150.82) * mm});
            skLineSegment(sketch, "E8296", {"start": v(469.55, 150.82) * mm, "end": v(468.07, 151.82) * mm});
            skLineSegment(sketch, "E8297", {"start": v(468.07, 151.82) * mm, "end": v(466.54, 152.69) * mm});
            skLineSegment(sketch, "E8298", {"start": v(466.54, 152.69) * mm, "end": v(464.96, 153.44) * mm});
            skLineSegment(sketch, "E8299", {"start": v(464.96, 153.44) * mm, "end": v(463.34, 154.08) * mm});
            skLineSegment(sketch, "E8300", {"start": v(463.34, 154.08) * mm, "end": v(461.68, 154.63) * mm});
            skLineSegment(sketch, "E8301", {"start": v(461.68, 154.63) * mm, "end": v(459.98, 155.1) * mm});
            skLineSegment(sketch, "E8302", {"start": v(459.98, 155.1) * mm, "end": v(458.26, 155.48) * mm});
            skLineSegment(sketch, "E8303", {"start": v(458.26, 155.48) * mm, "end": v(456.5, 155.8) * mm});
            skLineSegment(sketch, "E8304", {"start": v(456.5, 155.8) * mm, "end": v(454.74, 156.07) * mm});
            skLineSegment(sketch, "E8305", {"start": v(454.74, 156.07) * mm, "end": v(452.96, 156.3) * mm});
            skLineSegment(sketch, "E8306", {"start": v(452.96, 156.3) * mm, "end": v(451.16, 156.49) * mm});
            skLineSegment(sketch, "E8307", {"start": v(451.16, 156.49) * mm, "end": v(449.37, 156.67) * mm});
            skLineSegment(sketch, "E8308", {"start": v(449.37, 156.67) * mm, "end": v(447.57, 156.83) * mm});
            skLineSegment(sketch, "E8309", {"start": v(447.57, 156.83) * mm, "end": v(445.78, 157) * mm});
            skLineSegment(sketch, "E8310", {"start": v(445.78, 157) * mm, "end": v(444, 157.19) * mm});
            skLineSegment(sketch, "E8311", {"start": v(444, 157.19) * mm, "end": v(442.24, 157.4) * mm});
            skLineSegment(sketch, "E8312", {"start": v(442.24, 157.4) * mm, "end": v(440.5, 157.64) * mm});
            skLineSegment(sketch, "E8313", {"start": v(440.5, 157.64) * mm, "end": v(438.77, 157.93) * mm});
            skLineSegment(sketch, "E8314", {"start": v(-448.29, 31.2) * mm, "end": v(-448.07, 29.46) * mm});
            skLineSegment(sketch, "E8315", {"start": v(-448.07, 29.46) * mm, "end": v(-447.86, 27.7) * mm});
            skLineSegment(sketch, "E8316", {"start": v(-447.86, 27.7) * mm, "end": v(-447.66, 25.94) * mm});
            skLineSegment(sketch, "E8317", {"start": v(-447.66, 25.94) * mm, "end": v(-447.47, 24.18) * mm});
            skLineSegment(sketch, "E8318", {"start": v(-447.47, 24.18) * mm, "end": v(-447.28, 22.4) * mm});
            skLineSegment(sketch, "E8319", {"start": v(-447.28, 22.4) * mm, "end": v(-447.1, 20.62) * mm});
            skLineSegment(sketch, "E8320", {"start": v(-447.1, 20.62) * mm, "end": v(-446.94, 18.84) * mm});
            skLineSegment(sketch, "E8321", {"start": v(-446.94, 18.84) * mm, "end": v(-446.78, 17.05) * mm});
            skLineSegment(sketch, "E8322", {"start": v(-446.78, 17.05) * mm, "end": v(-446.63, 15.25) * mm});
            skLineSegment(sketch, "E8323", {"start": v(-446.63, 15.25) * mm, "end": v(-446.48, 13.45) * mm});
            skLineSegment(sketch, "E8324", {"start": v(-446.48, 13.45) * mm, "end": v(-446.35, 11.64) * mm});
            skLineSegment(sketch, "E8325", {"start": v(-446.35, 11.64) * mm, "end": v(-446.22, 9.84) * mm});
            skLineSegment(sketch, "E8326", {"start": v(-446.22, 9.84) * mm, "end": v(-446.1, 8.02) * mm});
            skLineSegment(sketch, "E8327", {"start": v(-446.1, 8.02) * mm, "end": v(-445.99, 6.2) * mm});
            skLineSegment(sketch, "E8328", {"start": v(-445.99, 6.2) * mm, "end": v(-445.88, 4.38) * mm});
            skLineSegment(sketch, "E8329", {"start": v(-445.88, 4.38) * mm, "end": v(-445.79, 2.56) * mm});
            skLineSegment(sketch, "E8330", {"start": v(-445.79, 2.56) * mm, "end": v(-445.7, 0.73) * mm});
            skLineSegment(sketch, "E8331", {"start": v(-445.7, 0.73) * mm, "end": v(-445.62, -1.1) * mm});
            skLineSegment(sketch, "E8332", {"start": v(-445.62, -1.1) * mm, "end": v(-445.55, -2.93) * mm});
            skLineSegment(sketch, "E8333", {"start": v(-445.55, -2.93) * mm, "end": v(-445.48, -4.77) * mm});
            skLineSegment(sketch, "E8334", {"start": v(-445.48, -4.77) * mm, "end": v(-445.43, -6.6) * mm});
            skLineSegment(sketch, "E8335", {"start": v(-445.43, -6.6) * mm, "end": v(-445.38, -8.45) * mm});
            skLineSegment(sketch, "E8336", {"start": v(-445.38, -8.45) * mm, "end": v(-445.34, -10.29) * mm});
            skLineSegment(sketch, "E8337", {"start": v(-445.34, -10.29) * mm, "end": v(-445.3, -12.13) * mm});
            skLineSegment(sketch, "E8338", {"start": v(-445.3, -12.13) * mm, "end": v(-445.28, -13.97) * mm});
            skLineSegment(sketch, "E8339", {"start": v(-445.28, -13.97) * mm, "end": v(-445.27, -15.81) * mm});
            skLineSegment(sketch, "E8340", {"start": v(-445.27, -15.81) * mm, "end": v(-445.26, -17.66) * mm});
            skLineSegment(sketch, "E8341", {"start": v(-445.26, -17.66) * mm, "end": v(-445.26, -19.5) * mm});
            skLineSegment(sketch, "E8342", {"start": v(-445.26, -19.5) * mm, "end": v(-445.27, -21.35) * mm});
            skLineSegment(sketch, "E8343", {"start": v(-445.27, -21.35) * mm, "end": v(-445.28, -23.19) * mm});
            skLineSegment(sketch, "E8344", {"start": v(-445.28, -23.19) * mm, "end": v(-445.3, -25.03) * mm});
            skLineSegment(sketch, "E8345", {"start": v(-445.3, -25.03) * mm, "end": v(-445.34, -26.87) * mm});
            skLineSegment(sketch, "E8346", {"start": v(-445.34, -26.87) * mm, "end": v(-445.38, -28.71) * mm});
            skLineSegment(sketch, "E8347", {"start": v(-445.38, -28.71) * mm, "end": v(-445.43, -30.55) * mm});
            skLineSegment(sketch, "E8348", {"start": v(-445.43, -30.55) * mm, "end": v(-445.48, -32.4) * mm});
            skLineSegment(sketch, "E8349", {"start": v(-445.48, -32.4) * mm, "end": v(-445.55, -34.23) * mm});
            skLineSegment(sketch, "E8350", {"start": v(-445.55, -34.23) * mm, "end": v(-445.62, -36.06) * mm});
            skLineSegment(sketch, "E8351", {"start": v(-445.62, -36.06) * mm, "end": v(-445.7, -37.89) * mm});
            skLineSegment(sketch, "E8352", {"start": v(-445.7, -37.89) * mm, "end": v(-445.79, -39.72) * mm});
            skLineSegment(sketch, "E8353", {"start": v(-445.79, -39.72) * mm, "end": v(-445.88, -41.54) * mm});
            skLineSegment(sketch, "E8354", {"start": v(-445.88, -41.54) * mm, "end": v(-445.99, -43.36) * mm});
            skLineSegment(sketch, "E8355", {"start": v(-445.99, -43.36) * mm, "end": v(-446.1, -45.18) * mm});
            skLineSegment(sketch, "E8356", {"start": v(-446.1, -45.18) * mm, "end": v(-446.22, -47) * mm});
            skLineSegment(sketch, "E8357", {"start": v(-446.22, -47) * mm, "end": v(-446.35, -48.8) * mm});
            skLineSegment(sketch, "E8358", {"start": v(-446.35, -48.8) * mm, "end": v(-446.48, -50.61) * mm});
            skLineSegment(sketch, "E8359", {"start": v(-446.48, -50.61) * mm, "end": v(-446.63, -52.41) * mm});
            skLineSegment(sketch, "E8360", {"start": v(-446.63, -52.41) * mm, "end": v(-446.78, -54.2) * mm});
            skLineSegment(sketch, "E8361", {"start": v(-446.78, -54.2) * mm, "end": v(-446.94, -56) * mm});
            skLineSegment(sketch, "E8362", {"start": v(-446.94, -56) * mm, "end": v(-447.1, -57.78) * mm});
            skLineSegment(sketch, "E8363", {"start": v(-447.1, -57.78) * mm, "end": v(-447.28, -59.56) * mm});
            skLineSegment(sketch, "E8364", {"start": v(-447.28, -59.56) * mm, "end": v(-447.47, -61.34) * mm});
            skLineSegment(sketch, "E8365", {"start": v(-447.47, -61.34) * mm, "end": v(-447.66, -63.1) * mm});
            skLineSegment(sketch, "E8366", {"start": v(-447.66, -63.1) * mm, "end": v(-447.86, -64.86) * mm});
            skLineSegment(sketch, "E8367", {"start": v(-447.86, -64.86) * mm, "end": v(-448.07, -66.62) * mm});
            skLineSegment(sketch, "E8368", {"start": v(-448.07, -66.62) * mm, "end": v(-448.29, -68.36) * mm});
            skLineSegment(sketch, "E8369", {"start": v(-448.29, -68.36) * mm, "end": v(-430.18, -68.36) * mm});
            skLineSegment(sketch, "E8370", {"start": v(-430.18, -68.36) * mm, "end": v(-430.31, -67.4) * mm});
            skLineSegment(sketch, "E8371", {"start": v(-430.31, -67.4) * mm, "end": v(-430.48, -66.28) * mm});
            skLineSegment(sketch, "E8372", {"start": v(-430.48, -66.28) * mm, "end": v(-430.67, -65) * mm});
            skLineSegment(sketch, "E8373", {"start": v(-430.67, -65) * mm, "end": v(-430.89, -63.6) * mm});
            skLineSegment(sketch, "E8374", {"start": v(-430.89, -63.6) * mm, "end": v(-431.12, -62.09) * mm});
            skLineSegment(sketch, "E8375", {"start": v(-431.12, -62.09) * mm, "end": v(-431.36, -60.46) * mm});
            skLineSegment(sketch, "E8376", {"start": v(-431.36, -60.46) * mm, "end": v(-431.6, -58.75) * mm});
            skLineSegment(sketch, "E8377", {"start": v(-431.6, -58.75) * mm, "end": v(-431.85, -56.95) * mm});
            skLineSegment(sketch, "E8378", {"start": v(-431.85, -56.95) * mm, "end": v(-432.08, -55.1) * mm});
            skLineSegment(sketch, "E8379", {"start": v(-432.08, -55.1) * mm, "end": v(-432.3, -53.2) * mm});
            skLineSegment(sketch, "E8380", {"start": v(-432.3, -53.2) * mm, "end": v(-432.49, -51.26) * mm});
            skLineSegment(sketch, "E8381", {"start": v(-432.49, -51.26) * mm, "end": v(-432.65, -49.3) * mm});
            skLineSegment(sketch, "E8382", {"start": v(-432.65, -49.3) * mm, "end": v(-432.78, -47.33) * mm});
            skLineSegment(sketch, "E8383", {"start": v(-432.78, -47.33) * mm, "end": v(-432.87, -45.37) * mm});
            skLineSegment(sketch, "E8384", {"start": v(-432.87, -45.37) * mm, "end": v(-432.92, -43.42) * mm});
            skLineSegment(sketch, "E8385", {"start": v(-432.92, -43.42) * mm, "end": v(-432.9, -41.52) * mm});
            skLineSegment(sketch, "E8386", {"start": v(-432.9, -41.52) * mm, "end": v(-432.84, -39.66) * mm});
            skLineSegment(sketch, "E8387", {"start": v(-432.84, -39.66) * mm, "end": v(-432.7, -37.86) * mm});
            skLineSegment(sketch, "E8388", {"start": v(-432.7, -37.86) * mm, "end": v(-432.5, -36.13) * mm});
            skLineSegment(sketch, "E8389", {"start": v(-432.5, -36.13) * mm, "end": v(-432.2, -34.5) * mm});
            skLineSegment(sketch, "E8390", {"start": v(-432.2, -34.5) * mm, "end": v(-431.84, -32.96) * mm});
            skLineSegment(sketch, "E8391", {"start": v(-431.84, -32.96) * mm, "end": v(-431.37, -31.55) * mm});
            skLineSegment(sketch, "E8392", {"start": v(-431.37, -31.55) * mm, "end": v(-430.81, -30.26) * mm});
            skLineSegment(sketch, "E8393", {"start": v(-430.81, -30.26) * mm, "end": v(-430.15, -29.12) * mm});
            skLineSegment(sketch, "E8394", {"start": v(-430.15, -29.12) * mm, "end": v(-429.37, -28.14) * mm});
            skLineSegment(sketch, "E8395", {"start": v(-429.37, -28.14) * mm, "end": v(-428.48, -27.33) * mm});
            skLineSegment(sketch, "E8396", {"start": v(-428.48, -27.33) * mm, "end": v(-427.47, -26.7) * mm});
            skLineSegment(sketch, "E8397", {"start": v(-427.47, -26.7) * mm, "end": v(-426.33, -26.28) * mm});
            skLineSegment(sketch, "E8398", {"start": v(-426.33, -26.28) * mm, "end": v(-425.1, -26.05) * mm});
            skLineSegment(sketch, "E8399", {"start": v(-425.1, -26.05) * mm, "end": v(-423.97, -26.05) * mm});
            skLineSegment(sketch, "E8400", {"start": v(-423.97, -26.05) * mm, "end": v(-422.95, -26.25) * mm});
            skLineSegment(sketch, "E8401", {"start": v(-422.95, -26.25) * mm, "end": v(-422.02, -26.66) * mm});
            skLineSegment(sketch, "E8402", {"start": v(-422.02, -26.66) * mm, "end": v(-421.19, -27.25) * mm});
            skLineSegment(sketch, "E8403", {"start": v(-421.19, -27.25) * mm, "end": v(-420.45, -28) * mm});
            skLineSegment(sketch, "E8404", {"start": v(-420.45, -28) * mm, "end": v(-419.79, -28.93) * mm});
            skLineSegment(sketch, "E8405", {"start": v(-419.79, -28.93) * mm, "end": v(-419.21, -30) * mm});
            skLineSegment(sketch, "E8406", {"start": v(-419.21, -30) * mm, "end": v(-418.71, -31.2) * mm});
            skLineSegment(sketch, "E8407", {"start": v(-418.71, -31.2) * mm, "end": v(-418.3, -32.54) * mm});
            skLineSegment(sketch, "E8408", {"start": v(-418.3, -32.54) * mm, "end": v(-417.94, -33.98) * mm});
            skLineSegment(sketch, "E8409", {"start": v(-417.94, -33.98) * mm, "end": v(-417.65, -35.52) * mm});
            skLineSegment(sketch, "E8410", {"start": v(-417.65, -35.52) * mm, "end": v(-417.42, -37.14) * mm});
            skLineSegment(sketch, "E8411", {"start": v(-417.42, -37.14) * mm, "end": v(-417.24, -38.84) * mm});
            skLineSegment(sketch, "E8412", {"start": v(-417.24, -38.84) * mm, "end": v(-417.12, -40.6) * mm});
            skLineSegment(sketch, "E8413", {"start": v(-417.12, -40.6) * mm, "end": v(-417.05, -42.4) * mm});
            skLineSegment(sketch, "E8414", {"start": v(-417.05, -42.4) * mm, "end": v(-417.03, -44.24) * mm});
            skLineSegment(sketch, "E8415", {"start": v(-417.03, -44.24) * mm, "end": v(-417.04, -46.1) * mm});
            skLineSegment(sketch, "E8416", {"start": v(-417.04, -46.1) * mm, "end": v(-417.1, -47.98) * mm});
            skLineSegment(sketch, "E8417", {"start": v(-417.1, -47.98) * mm, "end": v(-417.18, -49.85) * mm});
            skLineSegment(sketch, "E8418", {"start": v(-417.18, -49.85) * mm, "end": v(-417.29, -51.71) * mm});
            skLineSegment(sketch, "E8419", {"start": v(-417.29, -51.71) * mm, "end": v(-417.42, -53.54) * mm});
            skLineSegment(sketch, "E8420", {"start": v(-417.42, -53.54) * mm, "end": v(-417.58, -55.34) * mm});
            skLineSegment(sketch, "E8421", {"start": v(-417.58, -55.34) * mm, "end": v(-417.75, -57.08) * mm});
            skLineSegment(sketch, "E8422", {"start": v(-417.75, -57.08) * mm, "end": v(-417.93, -58.75) * mm});
            skLineSegment(sketch, "E8423", {"start": v(-417.93, -58.75) * mm, "end": v(-418.12, -60.36) * mm});
            skLineSegment(sketch, "E8424", {"start": v(-418.12, -60.36) * mm, "end": v(-418.31, -61.87) * mm});
            skLineSegment(sketch, "E8425", {"start": v(-418.31, -61.87) * mm, "end": v(-418.5, -63.28) * mm});
            skLineSegment(sketch, "E8426", {"start": v(-418.5, -63.28) * mm, "end": v(-418.7, -64.57) * mm});
            skLineSegment(sketch, "E8427", {"start": v(-418.7, -64.57) * mm, "end": v(-418.88, -65.74) * mm});
            skLineSegment(sketch, "E8428", {"start": v(-418.88, -65.74) * mm, "end": v(-419.04, -66.77) * mm});
            skLineSegment(sketch, "E8429", {"start": v(-419.04, -66.77) * mm, "end": v(-419.2, -67.65) * mm});
            skLineSegment(sketch, "E8430", {"start": v(-419.2, -67.65) * mm, "end": v(-419.32, -68.36) * mm});
            skLineSegment(sketch, "E8431", {"start": v(-419.32, -68.36) * mm, "end": v(-399.4, -68.36) * mm});
            skLineSegment(sketch, "E8432", {"start": v(-399.4, -68.36) * mm, "end": v(-399.75, -66.87) * mm});
            skLineSegment(sketch, "E8433", {"start": v(-399.75, -66.87) * mm, "end": v(-400.09, -65.33) * mm});
            skLineSegment(sketch, "E8434", {"start": v(-400.09, -65.33) * mm, "end": v(-400.4, -63.77) * mm});
            skLineSegment(sketch, "E8435", {"start": v(-400.4, -63.77) * mm, "end": v(-400.71, -62.17) * mm});
            skLineSegment(sketch, "E8436", {"start": v(-400.71, -62.17) * mm, "end": v(-401, -60.54) * mm});
            skLineSegment(sketch, "E8437", {"start": v(-401, -60.54) * mm, "end": v(-401.29, -58.88) * mm});
            skLineSegment(sketch, "E8438", {"start": v(-401.29, -58.88) * mm, "end": v(-401.55, -57.19) * mm});
            skLineSegment(sketch, "E8439", {"start": v(-401.55, -57.19) * mm, "end": v(-401.8, -55.47) * mm});
            skLineSegment(sketch, "E8440", {"start": v(-401.8, -55.47) * mm, "end": v(-402.05, -53.73) * mm});
            skLineSegment(sketch, "E8441", {"start": v(-402.05, -53.73) * mm, "end": v(-402.28, -51.96) * mm});
            skLineSegment(sketch, "E8442", {"start": v(-402.28, -51.96) * mm, "end": v(-402.5, -50.17) * mm});
            skLineSegment(sketch, "E8443", {"start": v(-402.5, -50.17) * mm, "end": v(-402.7, -48.36) * mm});
            skLineSegment(sketch, "E8444", {"start": v(-402.7, -48.36) * mm, "end": v(-402.88, -46.53) * mm});
            skLineSegment(sketch, "E8445", {"start": v(-402.88, -46.53) * mm, "end": v(-403.06, -44.67) * mm});
            skLineSegment(sketch, "E8446", {"start": v(-403.06, -44.67) * mm, "end": v(-403.22, -42.8) * mm});
            skLineSegment(sketch, "E8447", {"start": v(-403.22, -42.8) * mm, "end": v(-403.37, -40.92) * mm});
            skLineSegment(sketch, "E8448", {"start": v(-403.37, -40.92) * mm, "end": v(-403.5, -39.02) * mm});
            skLineSegment(sketch, "E8449", {"start": v(-403.5, -39.02) * mm, "end": v(-403.63, -37.1) * mm});
            skLineSegment(sketch, "E8450", {"start": v(-403.63, -37.1) * mm, "end": v(-403.74, -35.18) * mm});
            skLineSegment(sketch, "E8451", {"start": v(-403.74, -35.18) * mm, "end": v(-403.84, -33.24) * mm});
            skLineSegment(sketch, "E8452", {"start": v(-403.84, -33.24) * mm, "end": v(-403.93, -31.3) * mm});
            skLineSegment(sketch, "E8453", {"start": v(-403.93, -31.3) * mm, "end": v(-404, -29.34) * mm});
            skLineSegment(sketch, "E8454", {"start": v(-404, -29.34) * mm, "end": v(-404.06, -27.37) * mm});
            skLineSegment(sketch, "E8455", {"start": v(-404.06, -27.37) * mm, "end": v(-404.1, -25.4) * mm});
            skLineSegment(sketch, "E8456", {"start": v(-404.1, -25.4) * mm, "end": v(-404.13, -23.44) * mm});
            skLineSegment(sketch, "E8457", {"start": v(-404.13, -23.44) * mm, "end": v(-404.15, -21.46) * mm});
            skLineSegment(sketch, "E8458", {"start": v(-404.15, -21.46) * mm, "end": v(-404.16, -19.49) * mm});
            skLineSegment(sketch, "E8459", {"start": v(-404.16, -19.49) * mm, "end": v(-404.15, -17.5) * mm});
            skLineSegment(sketch, "E8460", {"start": v(-404.15, -17.5) * mm, "end": v(-404.13, -15.54) * mm});
            skLineSegment(sketch, "E8461", {"start": v(-404.13, -15.54) * mm, "end": v(-404.1, -13.56) * mm});
            skLineSegment(sketch, "E8462", {"start": v(-404.1, -13.56) * mm, "end": v(-404.06, -11.6) * mm});
            skLineSegment(sketch, "E8463", {"start": v(-404.06, -11.6) * mm, "end": v(-404, -9.63) * mm});
            skLineSegment(sketch, "E8464", {"start": v(-404, -9.63) * mm, "end": v(-403.93, -7.68) * mm});
            skLineSegment(sketch, "E8465", {"start": v(-403.93, -7.68) * mm, "end": v(-403.84, -5.73) * mm});
            skLineSegment(sketch, "E8466", {"start": v(-403.84, -5.73) * mm, "end": v(-403.74, -3.8) * mm});
            skLineSegment(sketch, "E8467", {"start": v(-403.74, -3.8) * mm, "end": v(-403.63, -1.87) * mm});
            skLineSegment(sketch, "E8468", {"start": v(-403.63, -1.87) * mm, "end": v(-403.5, 0.05) * mm});
            skLineSegment(sketch, "E8469", {"start": v(-403.5, 0.05) * mm, "end": v(-403.37, 1.95) * mm});
            skLineSegment(sketch, "E8470", {"start": v(-403.37, 1.95) * mm, "end": v(-403.22, 3.83) * mm});
            skLineSegment(sketch, "E8471", {"start": v(-403.22, 3.83) * mm, "end": v(-403.06, 5.7) * mm});
            skLineSegment(sketch, "E8472", {"start": v(-403.06, 5.7) * mm, "end": v(-402.88, 7.55) * mm});
            skLineSegment(sketch, "E8473", {"start": v(-402.88, 7.55) * mm, "end": v(-402.7, 9.39) * mm});
            skLineSegment(sketch, "E8474", {"start": v(-402.7, 9.39) * mm, "end": v(-402.5, 11.2) * mm});
            skLineSegment(sketch, "E8475", {"start": v(-402.5, 11.2) * mm, "end": v(-402.28, 13) * mm});
            skLineSegment(sketch, "E8476", {"start": v(-402.28, 13) * mm, "end": v(-402.05, 14.76) * mm});
            skLineSegment(sketch, "E8477", {"start": v(-402.05, 14.76) * mm, "end": v(-401.8, 16.5) * mm});
            skLineSegment(sketch, "E8478", {"start": v(-401.8, 16.5) * mm, "end": v(-401.55, 18.22) * mm});
            skLineSegment(sketch, "E8479", {"start": v(-401.55, 18.22) * mm, "end": v(-401.29, 19.9) * mm});
            skLineSegment(sketch, "E8480", {"start": v(-401.29, 19.9) * mm, "end": v(-401, 21.57) * mm});
            skLineSegment(sketch, "E8481", {"start": v(-401, 21.57) * mm, "end": v(-400.71, 23.2) * mm});
            skLineSegment(sketch, "E8482", {"start": v(-400.71, 23.2) * mm, "end": v(-400.4, 24.8) * mm});
            skLineSegment(sketch, "E8483", {"start": v(-400.4, 24.8) * mm, "end": v(-400.09, 26.36) * mm});
            skLineSegment(sketch, "E8484", {"start": v(-400.09, 26.36) * mm, "end": v(-399.75, 27.9) * mm});
            skLineSegment(sketch, "E8485", {"start": v(-399.75, 27.9) * mm, "end": v(-399.4, 29.4) * mm});
            skLineSegment(sketch, "E8486", {"start": v(-399.4, 29.4) * mm, "end": v(-419.32, 29.4) * mm});
            skLineSegment(sketch, "E8487", {"start": v(-419.32, 29.4) * mm, "end": v(-417.51, -12.24) * mm});
            skLineSegment(sketch, "E8488", {"start": v(-417.51, -12.24) * mm, "end": v(-419.28, -12.12) * mm});
            skLineSegment(sketch, "E8489", {"start": v(-419.28, -12.12) * mm, "end": v(-420.92, -11.88) * mm});
            skLineSegment(sketch, "E8490", {"start": v(-420.92, -11.88) * mm, "end": v(-422.43, -11.53) * mm});
            skLineSegment(sketch, "E8491", {"start": v(-422.43, -11.53) * mm, "end": v(-423.81, -11.07) * mm});
            skLineSegment(sketch, "E8492", {"start": v(-423.81, -11.07) * mm, "end": v(-425.07, -10.5) * mm});
            skLineSegment(sketch, "E8493", {"start": v(-425.07, -10.5) * mm, "end": v(-426.21, -9.84) * mm});
            skLineSegment(sketch, "E8494", {"start": v(-426.21, -9.84) * mm, "end": v(-427.25, -9.09) * mm});
            skLineSegment(sketch, "E8495", {"start": v(-427.25, -9.09) * mm, "end": v(-428.17, -8.24) * mm});
            skLineSegment(sketch, "E8496", {"start": v(-428.17, -8.24) * mm, "end": v(-429, -7.32) * mm});
            skLineSegment(sketch, "E8497", {"start": v(-429, -7.32) * mm, "end": v(-429.72, -6.3) * mm});
            skLineSegment(sketch, "E8498", {"start": v(-429.72, -6.3) * mm, "end": v(-430.35, -5.23) * mm});
            skLineSegment(sketch, "E8499", {"start": v(-430.35, -5.23) * mm, "end": v(-430.9, -4.08) * mm});
            skLineSegment(sketch, "E8500", {"start": v(-430.9, -4.08) * mm, "end": v(-431.36, -2.87) * mm});
            skLineSegment(sketch, "E8501", {"start": v(-431.36, -2.87) * mm, "end": v(-431.74, -1.6) * mm});
            skLineSegment(sketch, "E8502", {"start": v(-431.74, -1.6) * mm, "end": v(-432.05, -0.27) * mm});
            skLineSegment(sketch, "E8503", {"start": v(-432.05, -0.27) * mm, "end": v(-432.3, 1.1) * mm});
            skLineSegment(sketch, "E8504", {"start": v(-432.3, 1.1) * mm, "end": v(-432.48, 2.52) * mm});
            skLineSegment(sketch, "E8505", {"start": v(-432.48, 2.52) * mm, "end": v(-432.6, 3.98) * mm});
            skLineSegment(sketch, "E8506", {"start": v(-432.6, 3.98) * mm, "end": v(-432.66, 5.47) * mm});
            skLineSegment(sketch, "E8507", {"start": v(-432.66, 5.47) * mm, "end": v(-432.68, 6.99) * mm});
            skLineSegment(sketch, "E8508", {"start": v(-432.68, 6.99) * mm, "end": v(-432.65, 8.53) * mm});
            skLineSegment(sketch, "E8509", {"start": v(-432.65, 8.53) * mm, "end": v(-432.59, 10.1) * mm});
            skLineSegment(sketch, "E8510", {"start": v(-432.59, 10.1) * mm, "end": v(-432.48, 11.67) * mm});
            skLineSegment(sketch, "E8511", {"start": v(-432.48, 11.67) * mm, "end": v(-432.35, 13.26) * mm});
            skLineSegment(sketch, "E8512", {"start": v(-432.35, 13.26) * mm, "end": v(-432.2, 14.85) * mm});
            skLineSegment(sketch, "E8513", {"start": v(-432.2, 14.85) * mm, "end": v(-432.02, 16.44) * mm});
            skLineSegment(sketch, "E8514", {"start": v(-432.02, 16.44) * mm, "end": v(-431.83, 18.02) * mm});
            skLineSegment(sketch, "E8515", {"start": v(-431.83, 18.02) * mm, "end": v(-431.62, 19.6) * mm});
            skLineSegment(sketch, "E8516", {"start": v(-431.62, 19.6) * mm, "end": v(-431.41, 21.15) * mm});
            skLineSegment(sketch, "E8517", {"start": v(-431.41, 21.15) * mm, "end": v(-431.2, 22.7) * mm});
            skLineSegment(sketch, "E8518", {"start": v(-431.2, 22.7) * mm, "end": v(-431, 24.2) * mm});
            skLineSegment(sketch, "E8519", {"start": v(-431, 24.2) * mm, "end": v(-430.8, 25.68) * mm});
            skLineSegment(sketch, "E8520", {"start": v(-430.8, 25.68) * mm, "end": v(-430.61, 27.13) * mm});
            skLineSegment(sketch, "E8521", {"start": v(-430.61, 27.13) * mm, "end": v(-430.44, 28.53) * mm});
            skLineSegment(sketch, "E8522", {"start": v(-430.44, 28.53) * mm, "end": v(-430.3, 29.9) * mm});
            skLineSegment(sketch, "E8523", {"start": v(-430.3, 29.9) * mm, "end": v(-430.18, 31.2) * mm});
            skLineSegment(sketch, "E8524", {"start": v(-430.18, 31.2) * mm, "end": v(-448.29, 31.2) * mm});
            skLineSegment(sketch, "E8525", {"start": v(-375.87, 31.2) * mm, "end": v(-375.8, 29.53) * mm});
            skLineSegment(sketch, "E8526", {"start": v(-375.8, 29.53) * mm, "end": v(-375.77, 27.84) * mm});
            skLineSegment(sketch, "E8527", {"start": v(-375.77, 27.84) * mm, "end": v(-375.75, 26.13) * mm});
            skLineSegment(sketch, "E8528", {"start": v(-375.75, 26.13) * mm, "end": v(-375.76, 24.42) * mm});
            skLineSegment(sketch, "E8529", {"start": v(-375.76, 24.42) * mm, "end": v(-375.79, 22.69) * mm});
            skLineSegment(sketch, "E8530", {"start": v(-375.79, 22.69) * mm, "end": v(-375.84, 20.95) * mm});
            skLineSegment(sketch, "E8531", {"start": v(-375.84, 20.95) * mm, "end": v(-375.92, 19.2) * mm});
            skLineSegment(sketch, "E8532", {"start": v(-375.92, 19.2) * mm, "end": v(-376.01, 17.43) * mm});
            skLineSegment(sketch, "E8533", {"start": v(-376.01, 17.43) * mm, "end": v(-376.13, 15.66) * mm});
            skLineSegment(sketch, "E8534", {"start": v(-376.13, 15.66) * mm, "end": v(-376.27, 13.87) * mm});
            skLineSegment(sketch, "E8535", {"start": v(-376.27, 13.87) * mm, "end": v(-376.43, 12.08) * mm});
            skLineSegment(sketch, "E8536", {"start": v(-376.43, 12.08) * mm, "end": v(-376.6, 10.28) * mm});
            skLineSegment(sketch, "E8537", {"start": v(-376.6, 10.28) * mm, "end": v(-376.8, 8.47) * mm});
            skLineSegment(sketch, "E8538", {"start": v(-376.8, 8.47) * mm, "end": v(-377.02, 6.66) * mm});
            skLineSegment(sketch, "E8539", {"start": v(-377.02, 6.66) * mm, "end": v(-377.25, 4.84) * mm});
            skLineSegment(sketch, "E8540", {"start": v(-377.25, 4.84) * mm, "end": v(-377.5, 3) * mm});
            skLineSegment(sketch, "E8541", {"start": v(-377.5, 3) * mm, "end": v(-377.77, 1.18) * mm});
            skLineSegment(sketch, "E8542", {"start": v(-377.77, 1.18) * mm, "end": v(-378.06, -0.66) * mm});
            skLineSegment(sketch, "E8543", {"start": v(-378.06, -0.66) * mm, "end": v(-378.36, -2.5) * mm});
            skLineSegment(sketch, "E8544", {"start": v(-378.36, -2.5) * mm, "end": v(-378.67, -4.35) * mm});
            skLineSegment(sketch, "E8545", {"start": v(-378.67, -4.35) * mm, "end": v(-379, -6.2) * mm});
            skLineSegment(sketch, "E8546", {"start": v(-379, -6.2) * mm, "end": v(-379.35, -8.05) * mm});
            skLineSegment(sketch, "E8547", {"start": v(-379.35, -8.05) * mm, "end": v(-379.7, -9.9) * mm});
            skLineSegment(sketch, "E8548", {"start": v(-379.7, -9.9) * mm, "end": v(-380.07, -11.76) * mm});
            skLineSegment(sketch, "E8549", {"start": v(-380.07, -11.76) * mm, "end": v(-380.46, -13.62) * mm});
            skLineSegment(sketch, "E8550", {"start": v(-380.46, -13.62) * mm, "end": v(-380.85, -15.48) * mm});
            skLineSegment(sketch, "E8551", {"start": v(-380.85, -15.48) * mm, "end": v(-381.26, -17.33) * mm});
            skLineSegment(sketch, "E8552", {"start": v(-381.26, -17.33) * mm, "end": v(-381.68, -19.19) * mm});
            skLineSegment(sketch, "E8553", {"start": v(-381.68, -19.19) * mm, "end": v(-382.11, -21.04) * mm});
            skLineSegment(sketch, "E8554", {"start": v(-382.11, -21.04) * mm, "end": v(-382.55, -22.9) * mm});
            skLineSegment(sketch, "E8555", {"start": v(-382.55, -22.9) * mm, "end": v(-383, -24.74) * mm});
            skLineSegment(sketch, "E8556", {"start": v(-383, -24.74) * mm, "end": v(-383.46, -26.59) * mm});
            skLineSegment(sketch, "E8557", {"start": v(-383.46, -26.59) * mm, "end": v(-383.92, -28.43) * mm});
            skLineSegment(sketch, "E8558", {"start": v(-383.92, -28.43) * mm, "end": v(-384.4, -30.26) * mm});
            skLineSegment(sketch, "E8559", {"start": v(-384.4, -30.26) * mm, "end": v(-384.88, -32.1) * mm});
            skLineSegment(sketch, "E8560", {"start": v(-384.88, -32.1) * mm, "end": v(-385.37, -33.92) * mm});
            skLineSegment(sketch, "E8561", {"start": v(-385.37, -33.92) * mm, "end": v(-385.86, -35.74) * mm});
            skLineSegment(sketch, "E8562", {"start": v(-385.86, -35.74) * mm, "end": v(-386.37, -37.56) * mm});
            skLineSegment(sketch, "E8563", {"start": v(-386.37, -37.56) * mm, "end": v(-386.87, -39.36) * mm});
            skLineSegment(sketch, "E8564", {"start": v(-386.87, -39.36) * mm, "end": v(-387.38, -41.16) * mm});
            skLineSegment(sketch, "E8565", {"start": v(-387.38, -41.16) * mm, "end": v(-387.9, -42.95) * mm});
            skLineSegment(sketch, "E8566", {"start": v(-387.9, -42.95) * mm, "end": v(-388.42, -44.73) * mm});
            skLineSegment(sketch, "E8567", {"start": v(-388.42, -44.73) * mm, "end": v(-388.94, -46.5) * mm});
            skLineSegment(sketch, "E8568", {"start": v(-388.94, -46.5) * mm, "end": v(-389.47, -48.26) * mm});
            skLineSegment(sketch, "E8569", {"start": v(-389.47, -48.26) * mm, "end": v(-390, -50) * mm});
            skLineSegment(sketch, "E8570", {"start": v(-390, -50) * mm, "end": v(-390.52, -51.75) * mm});
            skLineSegment(sketch, "E8571", {"start": v(-390.52, -51.75) * mm, "end": v(-391.05, -53.47) * mm});
            skLineSegment(sketch, "E8572", {"start": v(-391.05, -53.47) * mm, "end": v(-391.58, -55.19) * mm});
            skLineSegment(sketch, "E8573", {"start": v(-391.58, -55.19) * mm, "end": v(-392.11, -56.89) * mm});
            skLineSegment(sketch, "E8574", {"start": v(-392.11, -56.89) * mm, "end": v(-392.64, -58.57) * mm});
            skLineSegment(sketch, "E8575", {"start": v(-392.64, -58.57) * mm, "end": v(-393.17, -60.24) * mm});
            skLineSegment(sketch, "E8576", {"start": v(-393.17, -60.24) * mm, "end": v(-393.7, -61.9) * mm});
            skLineSegment(sketch, "E8577", {"start": v(-393.7, -61.9) * mm, "end": v(-394.23, -63.54) * mm});
            skLineSegment(sketch, "E8578", {"start": v(-394.23, -63.54) * mm, "end": v(-394.75, -65.17) * mm});
            skLineSegment(sketch, "E8579", {"start": v(-394.75, -65.17) * mm, "end": v(-395.27, -66.77) * mm});
            skLineSegment(sketch, "E8580", {"start": v(-395.27, -66.77) * mm, "end": v(-395.79, -68.36) * mm});
            skLineSegment(sketch, "E8581", {"start": v(-395.79, -68.36) * mm, "end": v(-375.87, -68.36) * mm});
            skLineSegment(sketch, "E8582", {"start": v(-375.87, -68.36) * mm, "end": v(-376.05, -66.45) * mm});
            skLineSegment(sketch, "E8583", {"start": v(-376.05, -66.45) * mm, "end": v(-376.14, -64.63) * mm});
            skLineSegment(sketch, "E8584", {"start": v(-376.14, -64.63) * mm, "end": v(-376.17, -62.9) * mm});
            skLineSegment(sketch, "E8585", {"start": v(-376.17, -62.9) * mm, "end": v(-376.12, -61.24) * mm});
            skLineSegment(sketch, "E8586", {"start": v(-376.12, -61.24) * mm, "end": v(-376.01, -59.69) * mm});
            skLineSegment(sketch, "E8587", {"start": v(-376.01, -59.69) * mm, "end": v(-375.84, -58.21) * mm});
            skLineSegment(sketch, "E8588", {"start": v(-375.84, -58.21) * mm, "end": v(-375.6, -56.83) * mm});
            skLineSegment(sketch, "E8589", {"start": v(-375.6, -56.83) * mm, "end": v(-375.3, -55.53) * mm});
            skLineSegment(sketch, "E8590", {"start": v(-375.3, -55.53) * mm, "end": v(-374.96, -54.33) * mm});
            skLineSegment(sketch, "E8591", {"start": v(-374.96, -54.33) * mm, "end": v(-374.56, -53.2) * mm});
            skLineSegment(sketch, "E8592", {"start": v(-374.56, -53.2) * mm, "end": v(-374.12, -52.17) * mm});
            skLineSegment(sketch, "E8593", {"start": v(-374.12, -52.17) * mm, "end": v(-373.63, -51.23) * mm});
            skLineSegment(sketch, "E8594", {"start": v(-373.63, -51.23) * mm, "end": v(-373.1, -50.37) * mm});
            skLineSegment(sketch, "E8595", {"start": v(-373.1, -50.37) * mm, "end": v(-372.54, -49.6) * mm});
            skLineSegment(sketch, "E8596", {"start": v(-372.54, -49.6) * mm, "end": v(-371.94, -48.91) * mm});
            skLineSegment(sketch, "E8597", {"start": v(-371.94, -48.91) * mm, "end": v(-371.3, -48.32) * mm});
            skLineSegment(sketch, "E8598", {"start": v(-371.3, -48.32) * mm, "end": v(-370.65, -47.8) * mm});
            skLineSegment(sketch, "E8599", {"start": v(-370.65, -47.8) * mm, "end": v(-369.96, -47.38) * mm});
            skLineSegment(sketch, "E8600", {"start": v(-369.96, -47.38) * mm, "end": v(-369.26, -47.04) * mm});
            skLineSegment(sketch, "E8601", {"start": v(-369.26, -47.04) * mm, "end": v(-368.54, -46.8) * mm});
            skLineSegment(sketch, "E8602", {"start": v(-368.54, -46.8) * mm, "end": v(-367.8, -46.63) * mm});
            skLineSegment(sketch, "E8603", {"start": v(-367.8, -46.63) * mm, "end": v(-367.05, -46.55) * mm});
            skLineSegment(sketch, "E8604", {"start": v(-367.05, -46.55) * mm, "end": v(-366.3, -46.56) * mm});
            skLineSegment(sketch, "E8605", {"start": v(-366.3, -46.56) * mm, "end": v(-365.53, -46.66) * mm});
            skLineSegment(sketch, "E8606", {"start": v(-365.53, -46.66) * mm, "end": v(-364.77, -46.84) * mm});
            skLineSegment(sketch, "E8607", {"start": v(-364.77, -46.84) * mm, "end": v(-364, -47.1) * mm});
            skLineSegment(sketch, "E8608", {"start": v(-364, -47.1) * mm, "end": v(-363.25, -47.46) * mm});
            skLineSegment(sketch, "E8609", {"start": v(-363.25, -47.46) * mm, "end": v(-362.5, -47.9) * mm});
            skLineSegment(sketch, "E8610", {"start": v(-362.5, -47.9) * mm, "end": v(-361.77, -48.42) * mm});
            skLineSegment(sketch, "E8611", {"start": v(-361.77, -48.42) * mm, "end": v(-361.04, -49.03) * mm});
            skLineSegment(sketch, "E8612", {"start": v(-361.04, -49.03) * mm, "end": v(-360.34, -49.72) * mm});
            skLineSegment(sketch, "E8613", {"start": v(-360.34, -49.72) * mm, "end": v(-359.65, -50.5) * mm});
            skLineSegment(sketch, "E8614", {"start": v(-359.65, -50.5) * mm, "end": v(-359, -51.37) * mm});
            skLineSegment(sketch, "E8615", {"start": v(-359, -51.37) * mm, "end": v(-358.36, -52.32) * mm});
            skLineSegment(sketch, "E8616", {"start": v(-358.36, -52.32) * mm, "end": v(-357.76, -53.35) * mm});
            skLineSegment(sketch, "E8617", {"start": v(-357.76, -53.35) * mm, "end": v(-357.2, -54.48) * mm});
            skLineSegment(sketch, "E8618", {"start": v(-357.2, -54.48) * mm, "end": v(-356.66, -55.68) * mm});
            skLineSegment(sketch, "E8619", {"start": v(-356.66, -55.68) * mm, "end": v(-356.17, -56.97) * mm});
            skLineSegment(sketch, "E8620", {"start": v(-356.17, -56.97) * mm, "end": v(-355.73, -58.35) * mm});
            skLineSegment(sketch, "E8621", {"start": v(-355.73, -58.35) * mm, "end": v(-355.33, -59.8) * mm});
            skLineSegment(sketch, "E8622", {"start": v(-355.33, -59.8) * mm, "end": v(-354.98, -61.35) * mm});
            skLineSegment(sketch, "E8623", {"start": v(-354.98, -61.35) * mm, "end": v(-354.68, -62.98) * mm});
            skLineSegment(sketch, "E8624", {"start": v(-354.68, -62.98) * mm, "end": v(-354.44, -64.69) * mm});
            skLineSegment(sketch, "E8625", {"start": v(-354.44, -64.69) * mm, "end": v(-354.26, -66.48) * mm});
            skLineSegment(sketch, "E8626", {"start": v(-354.26, -66.48) * mm, "end": v(-354.15, -68.36) * mm});
            skLineSegment(sketch, "E8627", {"start": v(-354.15, -68.36) * mm, "end": v(-336.05, -68.36) * mm});
            skLineSegment(sketch, "E8628", {"start": v(-336.05, -68.36) * mm, "end": v(-355.96, 31.2) * mm});
            skLineSegment(sketch, "E8629", {"start": v(-355.96, 31.2) * mm, "end": v(-375.87, 31.2) * mm});
            skLineSegment(sketch, "E8630", {"start": v(-287.75, 26.8) * mm, "end": v(-288.88, 27.78) * mm});
            skLineSegment(sketch, "E8631", {"start": v(-288.88, 27.78) * mm, "end": v(-290.14, 28.64) * mm});
            skLineSegment(sketch, "E8632", {"start": v(-290.14, 28.64) * mm, "end": v(-291.5, 29.4) * mm});
            skLineSegment(sketch, "E8633", {"start": v(-291.5, 29.4) * mm, "end": v(-292.97, 30.04) * mm});
            skLineSegment(sketch, "E8634", {"start": v(-292.97, 30.04) * mm, "end": v(-294.53, 30.6) * mm});
            skLineSegment(sketch, "E8635", {"start": v(-294.53, 30.6) * mm, "end": v(-296.18, 31.05) * mm});
            skLineSegment(sketch, "E8636", {"start": v(-296.18, 31.05) * mm, "end": v(-297.9, 31.43) * mm});
            skLineSegment(sketch, "E8637", {"start": v(-297.9, 31.43) * mm, "end": v(-299.67, 31.72) * mm});
            skLineSegment(sketch, "E8638", {"start": v(-299.67, 31.72) * mm, "end": v(-301.5, 31.94) * mm});
            skLineSegment(sketch, "E8639", {"start": v(-301.5, 31.94) * mm, "end": v(-303.38, 32.1) * mm});
            skLineSegment(sketch, "E8640", {"start": v(-303.38, 32.1) * mm, "end": v(-305.3, 32.2) * mm});
            skLineSegment(sketch, "E8641", {"start": v(-305.3, 32.2) * mm, "end": v(-307.23, 32.25) * mm});
            skLineSegment(sketch, "E8642", {"start": v(-307.23, 32.25) * mm, "end": v(-309.19, 32.26) * mm});
            skLineSegment(sketch, "E8643", {"start": v(-309.19, 32.26) * mm, "end": v(-311.15, 32.22) * mm});
            skLineSegment(sketch, "E8644", {"start": v(-311.15, 32.22) * mm, "end": v(-313.11, 32.16) * mm});
            skLineSegment(sketch, "E8645", {"start": v(-313.11, 32.16) * mm, "end": v(-315.07, 32.06) * mm});
            skLineSegment(sketch, "E8646", {"start": v(-315.07, 32.06) * mm, "end": v(-317, 31.95) * mm});
            skLineSegment(sketch, "E8647", {"start": v(-317, 31.95) * mm, "end": v(-318.9, 31.83) * mm});
            skLineSegment(sketch, "E8648", {"start": v(-318.9, 31.83) * mm, "end": v(-320.76, 31.7) * mm});
            skLineSegment(sketch, "E8649", {"start": v(-320.76, 31.7) * mm, "end": v(-322.58, 31.58) * mm});
            skLineSegment(sketch, "E8650", {"start": v(-322.58, 31.58) * mm, "end": v(-324.34, 31.46) * mm});
            skLineSegment(sketch, "E8651", {"start": v(-324.34, 31.46) * mm, "end": v(-326.03, 31.36) * mm});
            skLineSegment(sketch, "E8652", {"start": v(-326.03, 31.36) * mm, "end": v(-327.65, 31.28) * mm});
            skLineSegment(sketch, "E8653", {"start": v(-327.65, 31.28) * mm, "end": v(-329.18, 31.22) * mm});
            skLineSegment(sketch, "E8654", {"start": v(-329.18, 31.22) * mm, "end": v(-330.61, 31.2) * mm});
            skLineSegment(sketch, "E8655", {"start": v(-330.61, 31.2) * mm, "end": v(-330.4, 29.46) * mm});
            skLineSegment(sketch, "E8656", {"start": v(-330.4, 29.46) * mm, "end": v(-330.2, 27.7) * mm});
            skLineSegment(sketch, "E8657", {"start": v(-330.2, 27.7) * mm, "end": v(-330, 25.94) * mm});
            skLineSegment(sketch, "E8658", {"start": v(-330, 25.94) * mm, "end": v(-329.8, 24.18) * mm});
            skLineSegment(sketch, "E8659", {"start": v(-329.8, 24.18) * mm, "end": v(-329.61, 22.4) * mm});
            skLineSegment(sketch, "E8660", {"start": v(-329.61, 22.4) * mm, "end": v(-329.44, 20.62) * mm});
            skLineSegment(sketch, "E8661", {"start": v(-329.44, 20.62) * mm, "end": v(-329.27, 18.84) * mm});
            skLineSegment(sketch, "E8662", {"start": v(-329.27, 18.84) * mm, "end": v(-329.1, 17.05) * mm});
            skLineSegment(sketch, "E8663", {"start": v(-329.1, 17.05) * mm, "end": v(-328.96, 15.25) * mm});
            skLineSegment(sketch, "E8664", {"start": v(-328.96, 15.25) * mm, "end": v(-328.81, 13.45) * mm});
            skLineSegment(sketch, "E8665", {"start": v(-328.81, 13.45) * mm, "end": v(-328.68, 11.64) * mm});
            skLineSegment(sketch, "E8666", {"start": v(-328.68, 11.64) * mm, "end": v(-328.55, 9.84) * mm});
            skLineSegment(sketch, "E8667", {"start": v(-328.55, 9.84) * mm, "end": v(-328.43, 8.02) * mm});
            skLineSegment(sketch, "E8668", {"start": v(-328.43, 8.02) * mm, "end": v(-328.32, 6.2) * mm});
            skLineSegment(sketch, "E8669", {"start": v(-328.32, 6.2) * mm, "end": v(-328.21, 4.38) * mm});
            skLineSegment(sketch, "E8670", {"start": v(-328.21, 4.38) * mm, "end": v(-328.12, 2.56) * mm});
            skLineSegment(sketch, "E8671", {"start": v(-328.12, 2.56) * mm, "end": v(-328.03, 0.73) * mm});
            skLineSegment(sketch, "E8672", {"start": v(-328.03, 0.73) * mm, "end": v(-327.95, -1.1) * mm});
            skLineSegment(sketch, "E8673", {"start": v(-327.95, -1.1) * mm, "end": v(-327.88, -2.93) * mm});
            skLineSegment(sketch, "E8674", {"start": v(-327.88, -2.93) * mm, "end": v(-327.81, -4.77) * mm});
            skLineSegment(sketch, "E8675", {"start": v(-327.81, -4.77) * mm, "end": v(-327.76, -6.6) * mm});
            skLineSegment(sketch, "E8676", {"start": v(-327.76, -6.6) * mm, "end": v(-327.7, -8.45) * mm});
            skLineSegment(sketch, "E8677", {"start": v(-327.7, -8.45) * mm, "end": v(-327.67, -10.29) * mm});
            skLineSegment(sketch, "E8678", {"start": v(-327.67, -10.29) * mm, "end": v(-327.63, -12.13) * mm});
            skLineSegment(sketch, "E8679", {"start": v(-327.63, -12.13) * mm, "end": v(-327.61, -13.97) * mm});
            skLineSegment(sketch, "E8680", {"start": v(-327.61, -13.97) * mm, "end": v(-327.6, -15.81) * mm});
            skLineSegment(sketch, "E8681", {"start": v(-327.6, -15.81) * mm, "end": v(-327.59, -17.66) * mm});
            skLineSegment(sketch, "E8682", {"start": v(-327.59, -17.66) * mm, "end": v(-327.59, -19.5) * mm});
            skLineSegment(sketch, "E8683", {"start": v(-327.59, -19.5) * mm, "end": v(-327.6, -21.35) * mm});
            skLineSegment(sketch, "E8684", {"start": v(-327.6, -21.35) * mm, "end": v(-327.61, -23.19) * mm});
            skLineSegment(sketch, "E8685", {"start": v(-327.61, -23.19) * mm, "end": v(-327.63, -25.03) * mm});
            skLineSegment(sketch, "E8686", {"start": v(-327.63, -25.03) * mm, "end": v(-327.67, -26.87) * mm});
            skLineSegment(sketch, "E8687", {"start": v(-327.67, -26.87) * mm, "end": v(-327.7, -28.71) * mm});
            skLineSegment(sketch, "E8688", {"start": v(-327.7, -28.71) * mm, "end": v(-327.76, -30.55) * mm});
            skLineSegment(sketch, "E8689", {"start": v(-327.76, -30.55) * mm, "end": v(-327.81, -32.4) * mm});
            skLineSegment(sketch, "E8690", {"start": v(-327.81, -32.4) * mm, "end": v(-327.88, -34.23) * mm});
            skLineSegment(sketch, "E8691", {"start": v(-327.88, -34.23) * mm, "end": v(-327.95, -36.06) * mm});
            skLineSegment(sketch, "E8692", {"start": v(-327.95, -36.06) * mm, "end": v(-328.03, -37.89) * mm});
            skLineSegment(sketch, "E8693", {"start": v(-328.03, -37.89) * mm, "end": v(-328.12, -39.72) * mm});
            skLineSegment(sketch, "E8694", {"start": v(-328.12, -39.72) * mm, "end": v(-328.21, -41.54) * mm});
            skLineSegment(sketch, "E8695", {"start": v(-328.21, -41.54) * mm, "end": v(-328.32, -43.36) * mm});
            skLineSegment(sketch, "E8696", {"start": v(-328.32, -43.36) * mm, "end": v(-328.43, -45.18) * mm});
            skLineSegment(sketch, "E8697", {"start": v(-328.43, -45.18) * mm, "end": v(-328.55, -47) * mm});
            skLineSegment(sketch, "E8698", {"start": v(-328.55, -47) * mm, "end": v(-328.68, -48.8) * mm});
            skLineSegment(sketch, "E8699", {"start": v(-328.68, -48.8) * mm, "end": v(-328.81, -50.61) * mm});
            skLineSegment(sketch, "E8700", {"start": v(-328.81, -50.61) * mm, "end": v(-328.96, -52.41) * mm});
            skLineSegment(sketch, "E8701", {"start": v(-328.96, -52.41) * mm, "end": v(-329.1, -54.2) * mm});
            skLineSegment(sketch, "E8702", {"start": v(-329.1, -54.2) * mm, "end": v(-329.27, -56) * mm});
            skLineSegment(sketch, "E8703", {"start": v(-329.27, -56) * mm, "end": v(-329.44, -57.78) * mm});
            skLineSegment(sketch, "E8704", {"start": v(-329.44, -57.78) * mm, "end": v(-329.61, -59.56) * mm});
            skLineSegment(sketch, "E8705", {"start": v(-329.61, -59.56) * mm, "end": v(-329.8, -61.34) * mm});
            skLineSegment(sketch, "E8706", {"start": v(-329.8, -61.34) * mm, "end": v(-330, -63.1) * mm});
            skLineSegment(sketch, "E8707", {"start": v(-330, -63.1) * mm, "end": v(-330.2, -64.86) * mm});
            skLineSegment(sketch, "E8708", {"start": v(-330.2, -64.86) * mm, "end": v(-330.4, -66.62) * mm});
            skLineSegment(sketch, "E8709", {"start": v(-330.4, -66.62) * mm, "end": v(-330.61, -68.36) * mm});
            skLineSegment(sketch, "E8710", {"start": v(-330.61, -68.36) * mm, "end": v(-312.51, -68.36) * mm});
            skLineSegment(sketch, "E8711", {"start": v(-312.51, -68.36) * mm, "end": v(-312.7, -67) * mm});
            skLineSegment(sketch, "E8712", {"start": v(-312.7, -67) * mm, "end": v(-312.9, -65.56) * mm});
            skLineSegment(sketch, "E8713", {"start": v(-312.9, -65.56) * mm, "end": v(-313.13, -64.04) * mm});
            skLineSegment(sketch, "E8714", {"start": v(-313.13, -64.04) * mm, "end": v(-313.38, -62.45) * mm});
            skLineSegment(sketch, "E8715", {"start": v(-313.38, -62.45) * mm, "end": v(-313.63, -60.8) * mm});
            skLineSegment(sketch, "E8716", {"start": v(-313.63, -60.8) * mm, "end": v(-313.88, -59.11) * mm});
            skLineSegment(sketch, "E8717", {"start": v(-313.88, -59.11) * mm, "end": v(-314.13, -57.37) * mm});
            skLineSegment(sketch, "E8718", {"start": v(-314.13, -57.37) * mm, "end": v(-314.36, -55.6) * mm});
            skLineSegment(sketch, "E8719", {"start": v(-314.36, -55.6) * mm, "end": v(-314.58, -53.8) * mm});
            skLineSegment(sketch, "E8720", {"start": v(-314.58, -53.8) * mm, "end": v(-314.78, -51.98) * mm});
            skLineSegment(sketch, "E8721", {"start": v(-314.78, -51.98) * mm, "end": v(-314.94, -50.15) * mm});
            skLineSegment(sketch, "E8722", {"start": v(-314.94, -50.15) * mm, "end": v(-315.07, -48.32) * mm});
            skLineSegment(sketch, "E8723", {"start": v(-315.07, -48.32) * mm, "end": v(-315.16, -46.5) * mm});
            skLineSegment(sketch, "E8724", {"start": v(-315.16, -46.5) * mm, "end": v(-315.2, -44.68) * mm});
            skLineSegment(sketch, "E8725", {"start": v(-315.2, -44.68) * mm, "end": v(-315.18, -42.88) * mm});
            skLineSegment(sketch, "E8726", {"start": v(-315.18, -42.88) * mm, "end": v(-315.1, -41.11) * mm});
            skLineSegment(sketch, "E8727", {"start": v(-315.1, -41.11) * mm, "end": v(-314.95, -39.38) * mm});
            skLineSegment(sketch, "E8728", {"start": v(-314.95, -39.38) * mm, "end": v(-314.73, -37.69) * mm});
            skLineSegment(sketch, "E8729", {"start": v(-314.73, -37.69) * mm, "end": v(-314.43, -36.05) * mm});
            skLineSegment(sketch, "E8730", {"start": v(-314.43, -36.05) * mm, "end": v(-314.05, -34.47) * mm});
            skLineSegment(sketch, "E8731", {"start": v(-314.05, -34.47) * mm, "end": v(-313.57, -32.96) * mm});
            skLineSegment(sketch, "E8732", {"start": v(-313.57, -32.96) * mm, "end": v(-312.99, -31.52) * mm});
            skLineSegment(sketch, "E8733", {"start": v(-312.99, -31.52) * mm, "end": v(-312.3, -30.17) * mm});
            skLineSegment(sketch, "E8734", {"start": v(-312.3, -30.17) * mm, "end": v(-311.5, -28.9) * mm});
            skLineSegment(sketch, "E8735", {"start": v(-311.5, -28.9) * mm, "end": v(-310.6, -27.74) * mm});
            skLineSegment(sketch, "E8736", {"start": v(-310.6, -27.74) * mm, "end": v(-309.55, -26.68) * mm});
            skLineSegment(sketch, "E8737", {"start": v(-309.55, -26.68) * mm, "end": v(-308.39, -25.74) * mm});
            skLineSegment(sketch, "E8738", {"start": v(-308.39, -25.74) * mm, "end": v(-307.08, -24.92) * mm});
            skLineSegment(sketch, "E8739", {"start": v(-307.08, -24.92) * mm, "end": v(-301.65, -68.36) * mm});
            skLineSegment(sketch, "E8740", {"start": v(-301.65, -68.36) * mm, "end": v(-283.55, -68.36) * mm});
            skLineSegment(sketch, "E8741", {"start": v(-283.55, -68.36) * mm, "end": v(-283.8, -66.67) * mm});
            skLineSegment(sketch, "E8742", {"start": v(-283.8, -66.67) * mm, "end": v(-284.1, -64.95) * mm});
            skLineSegment(sketch, "E8743", {"start": v(-284.1, -64.95) * mm, "end": v(-284.46, -63.2) * mm});
            skLineSegment(sketch, "E8744", {"start": v(-284.46, -63.2) * mm, "end": v(-284.85, -61.42) * mm});
            skLineSegment(sketch, "E8745", {"start": v(-284.85, -61.42) * mm, "end": v(-285.27, -59.63) * mm});
            skLineSegment(sketch, "E8746", {"start": v(-285.27, -59.63) * mm, "end": v(-285.72, -57.81) * mm});
            skLineSegment(sketch, "E8747", {"start": v(-285.72, -57.81) * mm, "end": v(-286.18, -55.98) * mm});
            skLineSegment(sketch, "E8748", {"start": v(-286.18, -55.98) * mm, "end": v(-286.65, -54.14) * mm});
            skLineSegment(sketch, "E8749", {"start": v(-286.65, -54.14) * mm, "end": v(-287.12, -52.3) * mm});
            skLineSegment(sketch, "E8750", {"start": v(-287.12, -52.3) * mm, "end": v(-287.58, -50.44) * mm});
            skLineSegment(sketch, "E8751", {"start": v(-287.58, -50.44) * mm, "end": v(-288.03, -48.58) * mm});
            skLineSegment(sketch, "E8752", {"start": v(-288.03, -48.58) * mm, "end": v(-288.46, -46.72) * mm});
            skLineSegment(sketch, "E8753", {"start": v(-288.46, -46.72) * mm, "end": v(-288.85, -44.86) * mm});
            skLineSegment(sketch, "E8754", {"start": v(-288.85, -44.86) * mm, "end": v(-289.22, -43) * mm});
            skLineSegment(sketch, "E8755", {"start": v(-289.22, -43) * mm, "end": v(-289.53, -41.16) * mm});
            skLineSegment(sketch, "E8756", {"start": v(-289.53, -41.16) * mm, "end": v(-289.8, -39.32) * mm});
            skLineSegment(sketch, "E8757", {"start": v(-289.8, -39.32) * mm, "end": v(-290, -37.5) * mm});
            skLineSegment(sketch, "E8758", {"start": v(-290, -37.5) * mm, "end": v(-290.15, -35.7) * mm});
            skLineSegment(sketch, "E8759", {"start": v(-290.15, -35.7) * mm, "end": v(-290.22, -33.91) * mm});
            skLineSegment(sketch, "E8760", {"start": v(-290.22, -33.91) * mm, "end": v(-290.2, -32.15) * mm});
            skLineSegment(sketch, "E8761", {"start": v(-290.2, -32.15) * mm, "end": v(-290.1, -30.4) * mm});
            skLineSegment(sketch, "E8762", {"start": v(-290.1, -30.4) * mm, "end": v(-289.91, -28.7) * mm});
            skLineSegment(sketch, "E8763", {"start": v(-289.91, -28.7) * mm, "end": v(-289.7, -27.46) * mm});
            skLineSegment(sketch, "E8764", {"start": v(-289.7, -27.46) * mm, "end": v(-289.45, -26.15) * mm});
            skLineSegment(sketch, "E8765", {"start": v(-289.45, -26.15) * mm, "end": v(-289.15, -24.78) * mm});
            skLineSegment(sketch, "E8766", {"start": v(-289.15, -24.78) * mm, "end": v(-288.8, -23.36) * mm});
            skLineSegment(sketch, "E8767", {"start": v(-288.8, -23.36) * mm, "end": v(-288.42, -21.88) * mm});
            skLineSegment(sketch, "E8768", {"start": v(-288.42, -21.88) * mm, "end": v(-288.01, -20.36) * mm});
            skLineSegment(sketch, "E8769", {"start": v(-288.01, -20.36) * mm, "end": v(-287.58, -18.79) * mm});
            skLineSegment(sketch, "E8770", {"start": v(-287.58, -18.79) * mm, "end": v(-287.12, -17.18) * mm});
            skLineSegment(sketch, "E8771", {"start": v(-287.12, -17.18) * mm, "end": v(-286.65, -15.54) * mm});
            skLineSegment(sketch, "E8772", {"start": v(-286.65, -15.54) * mm, "end": v(-286.17, -13.86) * mm});
            skLineSegment(sketch, "E8773", {"start": v(-286.17, -13.86) * mm, "end": v(-285.7, -12.16) * mm});
            skLineSegment(sketch, "E8774", {"start": v(-285.7, -12.16) * mm, "end": v(-285.21, -10.43) * mm});
            skLineSegment(sketch, "E8775", {"start": v(-285.21, -10.43) * mm, "end": v(-284.74, -8.68) * mm});
            skLineSegment(sketch, "E8776", {"start": v(-284.74, -8.68) * mm, "end": v(-284.29, -6.92) * mm});
            skLineSegment(sketch, "E8777", {"start": v(-284.29, -6.92) * mm, "end": v(-283.85, -5.14) * mm});
            skLineSegment(sketch, "E8778", {"start": v(-283.85, -5.14) * mm, "end": v(-283.44, -3.36) * mm});
            skLineSegment(sketch, "E8779", {"start": v(-283.44, -3.36) * mm, "end": v(-283.06, -1.57) * mm});
            skLineSegment(sketch, "E8780", {"start": v(-283.06, -1.57) * mm, "end": v(-282.72, 0.22) * mm});
            skLineSegment(sketch, "E8781", {"start": v(-282.72, 0.22) * mm, "end": v(-282.41, 2) * mm});
            skLineSegment(sketch, "E8782", {"start": v(-282.41, 2) * mm, "end": v(-282.16, 3.78) * mm});
            skLineSegment(sketch, "E8783", {"start": v(-282.16, 3.78) * mm, "end": v(-281.95, 5.55) * mm});
            skLineSegment(sketch, "E8784", {"start": v(-281.95, 5.55) * mm, "end": v(-281.8, 7.3) * mm});
            skLineSegment(sketch, "E8785", {"start": v(-281.8, 7.3) * mm, "end": v(-281.73, 9.03) * mm});
            skLineSegment(sketch, "E8786", {"start": v(-281.73, 9.03) * mm, "end": v(-281.72, 10.74) * mm});
            skLineSegment(sketch, "E8787", {"start": v(-281.72, 10.74) * mm, "end": v(-281.78, 12.41) * mm});
            skLineSegment(sketch, "E8788", {"start": v(-281.78, 12.41) * mm, "end": v(-281.92, 14.06) * mm});
            skLineSegment(sketch, "E8789", {"start": v(-281.92, 14.06) * mm, "end": v(-282.15, 15.67) * mm});
            skLineSegment(sketch, "E8790", {"start": v(-282.15, 15.67) * mm, "end": v(-282.47, 17.24) * mm});
            skLineSegment(sketch, "E8791", {"start": v(-282.47, 17.24) * mm, "end": v(-282.89, 18.77) * mm});
            skLineSegment(sketch, "E8792", {"start": v(-282.89, 18.77) * mm, "end": v(-283.4, 20.25) * mm});
            skLineSegment(sketch, "E8793", {"start": v(-283.4, 20.25) * mm, "end": v(-284.04, 21.68) * mm});
            skLineSegment(sketch, "E8794", {"start": v(-284.04, 21.68) * mm, "end": v(-284.78, 23.05) * mm});
            skLineSegment(sketch, "E8795", {"start": v(-284.78, 23.05) * mm, "end": v(-285.64, 24.37) * mm});
            skLineSegment(sketch, "E8796", {"start": v(-285.64, 24.37) * mm, "end": v(-286.63, 25.62) * mm});
            skLineSegment(sketch, "E8797", {"start": v(-286.63, 25.62) * mm, "end": v(-287.74, 26.8) * mm});
            skLineSegment(sketch, "E8798", {"start": v(-233.8, -28.7) * mm, "end": v(-233.59, -27.46) * mm});
            skLineSegment(sketch, "E8799", {"start": v(-233.59, -27.46) * mm, "end": v(-233.33, -26.15) * mm});
            skLineSegment(sketch, "E8800", {"start": v(-233.33, -26.15) * mm, "end": v(-233.03, -24.78) * mm});
            skLineSegment(sketch, "E8801", {"start": v(-233.03, -24.78) * mm, "end": v(-232.68, -23.36) * mm});
            skLineSegment(sketch, "E8802", {"start": v(-232.68, -23.36) * mm, "end": v(-232.3, -21.88) * mm});
            skLineSegment(sketch, "E8803", {"start": v(-232.3, -21.88) * mm, "end": v(-231.9, -20.36) * mm});
            skLineSegment(sketch, "E8804", {"start": v(-231.9, -20.36) * mm, "end": v(-231.46, -18.79) * mm});
            skLineSegment(sketch, "E8805", {"start": v(-231.46, -18.79) * mm, "end": v(-231, -17.18) * mm});
            skLineSegment(sketch, "E8806", {"start": v(-231, -17.18) * mm, "end": v(-230.53, -15.54) * mm});
            skLineSegment(sketch, "E8807", {"start": v(-230.53, -15.54) * mm, "end": v(-230.05, -13.86) * mm});
            skLineSegment(sketch, "E8808", {"start": v(-230.05, -13.86) * mm, "end": v(-229.57, -12.16) * mm});
            skLineSegment(sketch, "E8809", {"start": v(-229.57, -12.16) * mm, "end": v(-229.1, -10.43) * mm});
            skLineSegment(sketch, "E8810", {"start": v(-229.1, -10.43) * mm, "end": v(-228.62, -8.68) * mm});
            skLineSegment(sketch, "E8811", {"start": v(-228.62, -8.68) * mm, "end": v(-228.17, -6.92) * mm});
            skLineSegment(sketch, "E8812", {"start": v(-228.17, -6.92) * mm, "end": v(-227.73, -5.14) * mm});
            skLineSegment(sketch, "E8813", {"start": v(-227.73, -5.14) * mm, "end": v(-227.32, -3.36) * mm});
            skLineSegment(sketch, "E8814", {"start": v(-227.32, -3.36) * mm, "end": v(-226.94, -1.57) * mm});
            skLineSegment(sketch, "E8815", {"start": v(-226.94, -1.57) * mm, "end": v(-226.6, 0.22) * mm});
            skLineSegment(sketch, "E8816", {"start": v(-226.6, 0.22) * mm, "end": v(-226.3, 2) * mm});
            skLineSegment(sketch, "E8817", {"start": v(-226.3, 2) * mm, "end": v(-226.04, 3.78) * mm});
            skLineSegment(sketch, "E8818", {"start": v(-226.04, 3.78) * mm, "end": v(-225.83, 5.55) * mm});
            skLineSegment(sketch, "E8819", {"start": v(-225.83, 5.55) * mm, "end": v(-225.69, 7.3) * mm});
            skLineSegment(sketch, "E8820", {"start": v(-225.69, 7.3) * mm, "end": v(-225.6, 9.03) * mm});
            skLineSegment(sketch, "E8821", {"start": v(-225.6, 9.03) * mm, "end": v(-225.6, 10.74) * mm});
            skLineSegment(sketch, "E8822", {"start": v(-225.6, 10.74) * mm, "end": v(-225.66, 12.41) * mm});
            skLineSegment(sketch, "E8823", {"start": v(-225.66, 12.41) * mm, "end": v(-225.8, 14.06) * mm});
            skLineSegment(sketch, "E8824", {"start": v(-225.8, 14.06) * mm, "end": v(-226.03, 15.67) * mm});
            skLineSegment(sketch, "E8825", {"start": v(-226.03, 15.67) * mm, "end": v(-226.35, 17.24) * mm});
            skLineSegment(sketch, "E8826", {"start": v(-226.35, 17.24) * mm, "end": v(-226.77, 18.77) * mm});
            skLineSegment(sketch, "E8827", {"start": v(-226.77, 18.77) * mm, "end": v(-227.29, 20.25) * mm});
            skLineSegment(sketch, "E8828", {"start": v(-227.29, 20.25) * mm, "end": v(-227.92, 21.68) * mm});
            skLineSegment(sketch, "E8829", {"start": v(-227.92, 21.68) * mm, "end": v(-228.66, 23.05) * mm});
            skLineSegment(sketch, "E8830", {"start": v(-228.66, 23.05) * mm, "end": v(-229.52, 24.37) * mm});
            skLineSegment(sketch, "E8831", {"start": v(-229.52, 24.37) * mm, "end": v(-230.5, 25.62) * mm});
            skLineSegment(sketch, "E8832", {"start": v(-230.5, 25.62) * mm, "end": v(-231.62, 26.8) * mm});
            skLineSegment(sketch, "E8833", {"start": v(-231.62, 26.8) * mm, "end": v(-232.76, 27.78) * mm});
            skLineSegment(sketch, "E8834", {"start": v(-232.76, 27.78) * mm, "end": v(-234.02, 28.64) * mm});
            skLineSegment(sketch, "E8835", {"start": v(-234.02, 28.64) * mm, "end": v(-235.39, 29.4) * mm});
            skLineSegment(sketch, "E8836", {"start": v(-235.39, 29.4) * mm, "end": v(-236.85, 30.04) * mm});
            skLineSegment(sketch, "E8837", {"start": v(-236.85, 30.04) * mm, "end": v(-238.41, 30.6) * mm});
            skLineSegment(sketch, "E8838", {"start": v(-238.41, 30.6) * mm, "end": v(-240.06, 31.05) * mm});
            skLineSegment(sketch, "E8839", {"start": v(-240.06, 31.05) * mm, "end": v(-241.77, 31.43) * mm});
            skLineSegment(sketch, "E8840", {"start": v(-241.77, 31.43) * mm, "end": v(-243.55, 31.72) * mm});
            skLineSegment(sketch, "E8841", {"start": v(-243.55, 31.72) * mm, "end": v(-245.38, 31.94) * mm});
            skLineSegment(sketch, "E8842", {"start": v(-245.38, 31.94) * mm, "end": v(-247.26, 32.1) * mm});
            skLineSegment(sketch, "E8843", {"start": v(-247.26, 32.1) * mm, "end": v(-249.17, 32.2) * mm});
            skLineSegment(sketch, "E8844", {"start": v(-249.17, 32.2) * mm, "end": v(-251.11, 32.25) * mm});
            skLineSegment(sketch, "E8845", {"start": v(-251.11, 32.25) * mm, "end": v(-253.07, 32.26) * mm});
            skLineSegment(sketch, "E8846", {"start": v(-253.07, 32.26) * mm, "end": v(-255.03, 32.22) * mm});
            skLineSegment(sketch, "E8847", {"start": v(-255.03, 32.22) * mm, "end": v(-257, 32.16) * mm});
            skLineSegment(sketch, "E8848", {"start": v(-257, 32.16) * mm, "end": v(-258.95, 32.06) * mm});
            skLineSegment(sketch, "E8849", {"start": v(-258.95, 32.06) * mm, "end": v(-260.88, 31.95) * mm});
            skLineSegment(sketch, "E8850", {"start": v(-260.88, 31.95) * mm, "end": v(-262.78, 31.83) * mm});
            skLineSegment(sketch, "E8851", {"start": v(-262.78, 31.83) * mm, "end": v(-264.64, 31.7) * mm});
            skLineSegment(sketch, "E8852", {"start": v(-264.64, 31.7) * mm, "end": v(-266.46, 31.58) * mm});
            skLineSegment(sketch, "E8853", {"start": v(-266.46, 31.58) * mm, "end": v(-268.22, 31.46) * mm});
            skLineSegment(sketch, "E8854", {"start": v(-268.22, 31.46) * mm, "end": v(-269.91, 31.36) * mm});
            skLineSegment(sketch, "E8855", {"start": v(-269.91, 31.36) * mm, "end": v(-271.53, 31.28) * mm});
            skLineSegment(sketch, "E8856", {"start": v(-271.53, 31.28) * mm, "end": v(-273.06, 31.22) * mm});
            skLineSegment(sketch, "E8857", {"start": v(-273.06, 31.22) * mm, "end": v(-274.5, 31.2) * mm});
            skLineSegment(sketch, "E8858", {"start": v(-274.5, 31.2) * mm, "end": v(-274.28, 29.46) * mm});
            skLineSegment(sketch, "E8859", {"start": v(-274.28, 29.46) * mm, "end": v(-274.07, 27.7) * mm});
            skLineSegment(sketch, "E8860", {"start": v(-274.07, 27.7) * mm, "end": v(-273.87, 25.94) * mm});
            skLineSegment(sketch, "E8861", {"start": v(-273.87, 25.94) * mm, "end": v(-273.68, 24.18) * mm});
            skLineSegment(sketch, "E8862", {"start": v(-273.68, 24.18) * mm, "end": v(-273.5, 22.4) * mm});
            skLineSegment(sketch, "E8863", {"start": v(-273.5, 22.4) * mm, "end": v(-273.32, 20.62) * mm});
            skLineSegment(sketch, "E8864", {"start": v(-273.32, 20.62) * mm, "end": v(-273.15, 18.84) * mm});
            skLineSegment(sketch, "E8865", {"start": v(-273.15, 18.84) * mm, "end": v(-272.99, 17.05) * mm});
            skLineSegment(sketch, "E8866", {"start": v(-272.99, 17.05) * mm, "end": v(-272.84, 15.25) * mm});
            skLineSegment(sketch, "E8867", {"start": v(-272.84, 15.25) * mm, "end": v(-272.7, 13.45) * mm});
            skLineSegment(sketch, "E8868", {"start": v(-272.7, 13.45) * mm, "end": v(-272.56, 11.64) * mm});
            skLineSegment(sketch, "E8869", {"start": v(-272.56, 11.64) * mm, "end": v(-272.43, 9.84) * mm});
            skLineSegment(sketch, "E8870", {"start": v(-272.43, 9.84) * mm, "end": v(-272.3, 8.02) * mm});
            skLineSegment(sketch, "E8871", {"start": v(-272.3, 8.02) * mm, "end": v(-272.2, 6.2) * mm});
            skLineSegment(sketch, "E8872", {"start": v(-272.2, 6.2) * mm, "end": v(-272.1, 4.38) * mm});
            skLineSegment(sketch, "E8873", {"start": v(-272.1, 4.38) * mm, "end": v(-272, 2.56) * mm});
            skLineSegment(sketch, "E8874", {"start": v(-272, 2.56) * mm, "end": v(-271.9, 0.73) * mm});
            skLineSegment(sketch, "E8875", {"start": v(-271.9, 0.73) * mm, "end": v(-271.83, -1.1) * mm});
            skLineSegment(sketch, "E8876", {"start": v(-271.83, -1.1) * mm, "end": v(-271.76, -2.93) * mm});
            skLineSegment(sketch, "E8877", {"start": v(-271.76, -2.93) * mm, "end": v(-271.7, -4.77) * mm});
            skLineSegment(sketch, "E8878", {"start": v(-271.7, -4.77) * mm, "end": v(-271.63, -6.6) * mm});
            skLineSegment(sketch, "E8879", {"start": v(-271.63, -6.6) * mm, "end": v(-271.59, -8.45) * mm});
            skLineSegment(sketch, "E8880", {"start": v(-271.59, -8.45) * mm, "end": v(-271.55, -10.29) * mm});
            skLineSegment(sketch, "E8881", {"start": v(-271.55, -10.29) * mm, "end": v(-271.51, -12.13) * mm});
            skLineSegment(sketch, "E8882", {"start": v(-271.51, -12.13) * mm, "end": v(-271.5, -13.97) * mm});
            skLineSegment(sketch, "E8883", {"start": v(-271.5, -13.97) * mm, "end": v(-271.47, -15.81) * mm});
            skLineSegment(sketch, "E8884", {"start": v(-271.47, -15.81) * mm, "end": v(-271.47, -17.66) * mm});
            skLineSegment(sketch, "E8885", {"start": v(-271.47, -17.66) * mm, "end": v(-271.47, -19.5) * mm});
            skLineSegment(sketch, "E8886", {"start": v(-271.47, -19.5) * mm, "end": v(-271.47, -21.35) * mm});
            skLineSegment(sketch, "E8887", {"start": v(-271.47, -21.35) * mm, "end": v(-271.5, -23.19) * mm});
            skLineSegment(sketch, "E8888", {"start": v(-271.5, -23.19) * mm, "end": v(-271.51, -25.03) * mm});
            skLineSegment(sketch, "E8889", {"start": v(-271.51, -25.03) * mm, "end": v(-271.55, -26.87) * mm});
            skLineSegment(sketch, "E8890", {"start": v(-271.55, -26.87) * mm, "end": v(-271.59, -28.71) * mm});
            skLineSegment(sketch, "E8891", {"start": v(-271.59, -28.71) * mm, "end": v(-271.63, -30.55) * mm});
            skLineSegment(sketch, "E8892", {"start": v(-271.63, -30.55) * mm, "end": v(-271.7, -32.4) * mm});
            skLineSegment(sketch, "E8893", {"start": v(-271.7, -32.4) * mm, "end": v(-271.76, -34.23) * mm});
            skLineSegment(sketch, "E8894", {"start": v(-271.76, -34.23) * mm, "end": v(-271.83, -36.06) * mm});
            skLineSegment(sketch, "E8895", {"start": v(-271.83, -36.06) * mm, "end": v(-271.9, -37.89) * mm});
            skLineSegment(sketch, "E8896", {"start": v(-271.9, -37.89) * mm, "end": v(-272, -39.72) * mm});
            skLineSegment(sketch, "E8897", {"start": v(-272, -39.72) * mm, "end": v(-272.1, -41.54) * mm});
            skLineSegment(sketch, "E8898", {"start": v(-272.1, -41.54) * mm, "end": v(-272.2, -43.36) * mm});
            skLineSegment(sketch, "E8899", {"start": v(-272.2, -43.36) * mm, "end": v(-272.3, -45.18) * mm});
            skLineSegment(sketch, "E8900", {"start": v(-272.3, -45.18) * mm, "end": v(-272.43, -47) * mm});
            skLineSegment(sketch, "E8901", {"start": v(-272.43, -47) * mm, "end": v(-272.56, -48.8) * mm});
            skLineSegment(sketch, "E8902", {"start": v(-272.56, -48.8) * mm, "end": v(-272.7, -50.61) * mm});
            skLineSegment(sketch, "E8903", {"start": v(-272.7, -50.61) * mm, "end": v(-272.84, -52.41) * mm});
            skLineSegment(sketch, "E8904", {"start": v(-272.84, -52.41) * mm, "end": v(-272.99, -54.2) * mm});
            skLineSegment(sketch, "E8905", {"start": v(-272.99, -54.2) * mm, "end": v(-273.15, -56) * mm});
            skLineSegment(sketch, "E8906", {"start": v(-273.15, -56) * mm, "end": v(-273.32, -57.78) * mm});
            skLineSegment(sketch, "E8907", {"start": v(-273.32, -57.78) * mm, "end": v(-273.5, -59.56) * mm});
            skLineSegment(sketch, "E8908", {"start": v(-273.5, -59.56) * mm, "end": v(-273.68, -61.34) * mm});
            skLineSegment(sketch, "E8909", {"start": v(-273.68, -61.34) * mm, "end": v(-273.87, -63.1) * mm});
            skLineSegment(sketch, "E8910", {"start": v(-273.87, -63.1) * mm, "end": v(-274.07, -64.86) * mm});
            skLineSegment(sketch, "E8911", {"start": v(-274.07, -64.86) * mm, "end": v(-274.28, -66.62) * mm});
            skLineSegment(sketch, "E8912", {"start": v(-274.28, -66.62) * mm, "end": v(-274.5, -68.36) * mm});
            skLineSegment(sketch, "E8913", {"start": v(-274.5, -68.36) * mm, "end": v(-256.4, -68.36) * mm});
            skLineSegment(sketch, "E8914", {"start": v(-256.4, -68.36) * mm, "end": v(-256.57, -67) * mm});
            skLineSegment(sketch, "E8915", {"start": v(-256.57, -67) * mm, "end": v(-256.78, -65.56) * mm});
            skLineSegment(sketch, "E8916", {"start": v(-256.78, -65.56) * mm, "end": v(-257.01, -64.04) * mm});
            skLineSegment(sketch, "E8917", {"start": v(-257.01, -64.04) * mm, "end": v(-257.25, -62.45) * mm});
            skLineSegment(sketch, "E8918", {"start": v(-257.25, -62.45) * mm, "end": v(-257.5, -60.8) * mm});
            skLineSegment(sketch, "E8919", {"start": v(-257.5, -60.8) * mm, "end": v(-257.76, -59.11) * mm});
            skLineSegment(sketch, "E8920", {"start": v(-257.76, -59.11) * mm, "end": v(-258, -57.37) * mm});
            skLineSegment(sketch, "E8921", {"start": v(-258, -57.37) * mm, "end": v(-258.24, -55.6) * mm});
            skLineSegment(sketch, "E8922", {"start": v(-258.24, -55.6) * mm, "end": v(-258.46, -53.8) * mm});
            skLineSegment(sketch, "E8923", {"start": v(-258.46, -53.8) * mm, "end": v(-258.66, -51.98) * mm});
            skLineSegment(sketch, "E8924", {"start": v(-258.66, -51.98) * mm, "end": v(-258.82, -50.15) * mm});
            skLineSegment(sketch, "E8925", {"start": v(-258.82, -50.15) * mm, "end": v(-258.95, -48.32) * mm});
            skLineSegment(sketch, "E8926", {"start": v(-258.95, -48.32) * mm, "end": v(-259.04, -46.5) * mm});
            skLineSegment(sketch, "E8927", {"start": v(-259.04, -46.5) * mm, "end": v(-259.08, -44.68) * mm});
            skLineSegment(sketch, "E8928", {"start": v(-259.08, -44.68) * mm, "end": v(-259.06, -42.88) * mm});
            skLineSegment(sketch, "E8929", {"start": v(-259.06, -42.88) * mm, "end": v(-258.98, -41.11) * mm});
            skLineSegment(sketch, "E8930", {"start": v(-258.98, -41.11) * mm, "end": v(-258.83, -39.38) * mm});
            skLineSegment(sketch, "E8931", {"start": v(-258.83, -39.38) * mm, "end": v(-258.61, -37.69) * mm});
            skLineSegment(sketch, "E8932", {"start": v(-258.61, -37.69) * mm, "end": v(-258.31, -36.05) * mm});
            skLineSegment(sketch, "E8933", {"start": v(-258.31, -36.05) * mm, "end": v(-257.93, -34.47) * mm});
            skLineSegment(sketch, "E8934", {"start": v(-257.93, -34.47) * mm, "end": v(-257.45, -32.96) * mm});
            skLineSegment(sketch, "E8935", {"start": v(-257.45, -32.96) * mm, "end": v(-256.87, -31.52) * mm});
            skLineSegment(sketch, "E8936", {"start": v(-256.87, -31.52) * mm, "end": v(-256.18, -30.17) * mm});
            skLineSegment(sketch, "E8937", {"start": v(-256.18, -30.17) * mm, "end": v(-255.39, -28.9) * mm});
            skLineSegment(sketch, "E8938", {"start": v(-255.39, -28.9) * mm, "end": v(-254.47, -27.74) * mm});
            skLineSegment(sketch, "E8939", {"start": v(-254.47, -27.74) * mm, "end": v(-253.43, -26.68) * mm});
            skLineSegment(sketch, "E8940", {"start": v(-253.43, -26.68) * mm, "end": v(-252.27, -25.74) * mm});
            skLineSegment(sketch, "E8941", {"start": v(-252.27, -25.74) * mm, "end": v(-250.96, -24.92) * mm});
            skLineSegment(sketch, "E8942", {"start": v(-250.96, -24.92) * mm, "end": v(-245.53, -68.36) * mm});
            skLineSegment(sketch, "E8943", {"start": v(-245.53, -68.36) * mm, "end": v(-227.43, -68.36) * mm});
            skLineSegment(sketch, "E8944", {"start": v(-227.43, -68.36) * mm, "end": v(-227.68, -66.67) * mm});
            skLineSegment(sketch, "E8945", {"start": v(-227.68, -66.67) * mm, "end": v(-227.99, -64.95) * mm});
            skLineSegment(sketch, "E8946", {"start": v(-227.99, -64.95) * mm, "end": v(-228.34, -63.2) * mm});
            skLineSegment(sketch, "E8947", {"start": v(-228.34, -63.2) * mm, "end": v(-228.73, -61.42) * mm});
            skLineSegment(sketch, "E8948", {"start": v(-228.73, -61.42) * mm, "end": v(-229.15, -59.63) * mm});
            skLineSegment(sketch, "E8949", {"start": v(-229.15, -59.63) * mm, "end": v(-229.6, -57.81) * mm});
            skLineSegment(sketch, "E8950", {"start": v(-229.6, -57.81) * mm, "end": v(-230.06, -55.98) * mm});
            skLineSegment(sketch, "E8951", {"start": v(-230.06, -55.98) * mm, "end": v(-230.53, -54.14) * mm});
            skLineSegment(sketch, "E8952", {"start": v(-230.53, -54.14) * mm, "end": v(-231, -52.3) * mm});
            skLineSegment(sketch, "E8953", {"start": v(-231, -52.3) * mm, "end": v(-231.46, -50.44) * mm});
            skLineSegment(sketch, "E8954", {"start": v(-231.46, -50.44) * mm, "end": v(-231.9, -48.58) * mm});
            skLineSegment(sketch, "E8955", {"start": v(-231.9, -48.58) * mm, "end": v(-232.33, -46.72) * mm});
            skLineSegment(sketch, "E8956", {"start": v(-232.33, -46.72) * mm, "end": v(-232.73, -44.86) * mm});
            skLineSegment(sketch, "E8957", {"start": v(-232.73, -44.86) * mm, "end": v(-233.1, -43) * mm});
            skLineSegment(sketch, "E8958", {"start": v(-233.1, -43) * mm, "end": v(-233.41, -41.16) * mm});
            skLineSegment(sketch, "E8959", {"start": v(-233.41, -41.16) * mm, "end": v(-233.68, -39.32) * mm});
            skLineSegment(sketch, "E8960", {"start": v(-233.68, -39.32) * mm, "end": v(-233.89, -37.5) * mm});
            skLineSegment(sketch, "E8961", {"start": v(-233.89, -37.5) * mm, "end": v(-234.03, -35.7) * mm});
            skLineSegment(sketch, "E8962", {"start": v(-234.03, -35.7) * mm, "end": v(-234.1, -33.91) * mm});
            skLineSegment(sketch, "E8963", {"start": v(-234.1, -33.91) * mm, "end": v(-234.09, -32.15) * mm});
            skLineSegment(sketch, "E8964", {"start": v(-234.09, -32.15) * mm, "end": v(-233.99, -30.4) * mm});
            skLineSegment(sketch, "E8965", {"start": v(-233.99, -30.4) * mm, "end": v(-233.8, -28.7) * mm});
            skLineSegment(sketch, "E8966", {"start": v(-218.37, 31.2) * mm, "end": v(-218.16, 29.46) * mm});
            skLineSegment(sketch, "E8967", {"start": v(-218.16, 29.46) * mm, "end": v(-217.95, 27.7) * mm});
            skLineSegment(sketch, "E8968", {"start": v(-217.95, 27.7) * mm, "end": v(-217.75, 25.94) * mm});
            skLineSegment(sketch, "E8969", {"start": v(-217.75, 25.94) * mm, "end": v(-217.56, 24.18) * mm});
            skLineSegment(sketch, "E8970", {"start": v(-217.56, 24.18) * mm, "end": v(-217.37, 22.4) * mm});
            skLineSegment(sketch, "E8971", {"start": v(-217.37, 22.4) * mm, "end": v(-217.2, 20.62) * mm});
            skLineSegment(sketch, "E8972", {"start": v(-217.2, 20.62) * mm, "end": v(-217.03, 18.84) * mm});
            skLineSegment(sketch, "E8973", {"start": v(-217.03, 18.84) * mm, "end": v(-216.87, 17.05) * mm});
            skLineSegment(sketch, "E8974", {"start": v(-216.87, 17.05) * mm, "end": v(-216.72, 15.25) * mm});
            skLineSegment(sketch, "E8975", {"start": v(-216.72, 15.25) * mm, "end": v(-216.57, 13.45) * mm});
            skLineSegment(sketch, "E8976", {"start": v(-216.57, 13.45) * mm, "end": v(-216.44, 11.64) * mm});
            skLineSegment(sketch, "E8977", {"start": v(-216.44, 11.64) * mm, "end": v(-216.3, 9.84) * mm});
            skLineSegment(sketch, "E8978", {"start": v(-216.3, 9.84) * mm, "end": v(-216.19, 8.02) * mm});
            skLineSegment(sketch, "E8979", {"start": v(-216.19, 8.02) * mm, "end": v(-216.08, 6.2) * mm});
            skLineSegment(sketch, "E8980", {"start": v(-216.08, 6.2) * mm, "end": v(-215.97, 4.38) * mm});
            skLineSegment(sketch, "E8981", {"start": v(-215.97, 4.38) * mm, "end": v(-215.88, 2.56) * mm});
            skLineSegment(sketch, "E8982", {"start": v(-215.88, 2.56) * mm, "end": v(-215.79, 0.73) * mm});
            skLineSegment(sketch, "E8983", {"start": v(-215.79, 0.73) * mm, "end": v(-215.7, -1.1) * mm});
            skLineSegment(sketch, "E8984", {"start": v(-215.7, -1.1) * mm, "end": v(-215.63, -2.93) * mm});
            skLineSegment(sketch, "E8985", {"start": v(-215.63, -2.93) * mm, "end": v(-215.57, -4.77) * mm});
            skLineSegment(sketch, "E8986", {"start": v(-215.57, -4.77) * mm, "end": v(-215.51, -6.6) * mm});
            skLineSegment(sketch, "E8987", {"start": v(-215.51, -6.6) * mm, "end": v(-215.47, -8.45) * mm});
            skLineSegment(sketch, "E8988", {"start": v(-215.47, -8.45) * mm, "end": v(-215.43, -10.29) * mm});
            skLineSegment(sketch, "E8989", {"start": v(-215.43, -10.29) * mm, "end": v(-215.4, -12.13) * mm});
            skLineSegment(sketch, "E8990", {"start": v(-215.4, -12.13) * mm, "end": v(-215.37, -13.97) * mm});
            skLineSegment(sketch, "E8991", {"start": v(-215.37, -13.97) * mm, "end": v(-215.35, -15.81) * mm});
            skLineSegment(sketch, "E8992", {"start": v(-215.35, -15.81) * mm, "end": v(-215.35, -17.66) * mm});
            skLineSegment(sketch, "E8993", {"start": v(-215.35, -17.66) * mm, "end": v(-215.35, -19.5) * mm});
            skLineSegment(sketch, "E8994", {"start": v(-215.35, -19.5) * mm, "end": v(-215.35, -21.35) * mm});
            skLineSegment(sketch, "E8995", {"start": v(-215.35, -21.35) * mm, "end": v(-215.37, -23.19) * mm});
            skLineSegment(sketch, "E8996", {"start": v(-215.37, -23.19) * mm, "end": v(-215.4, -25.03) * mm});
            skLineSegment(sketch, "E8997", {"start": v(-215.4, -25.03) * mm, "end": v(-215.43, -26.87) * mm});
            skLineSegment(sketch, "E8998", {"start": v(-215.43, -26.87) * mm, "end": v(-215.47, -28.71) * mm});
            skLineSegment(sketch, "E8999", {"start": v(-215.47, -28.71) * mm, "end": v(-215.51, -30.55) * mm});
            skLineSegment(sketch, "E9000", {"start": v(-215.51, -30.55) * mm, "end": v(-215.57, -32.4) * mm});
            skLineSegment(sketch, "E9001", {"start": v(-215.57, -32.4) * mm, "end": v(-215.63, -34.23) * mm});
            skLineSegment(sketch, "E9002", {"start": v(-215.63, -34.23) * mm, "end": v(-215.7, -36.06) * mm});
            skLineSegment(sketch, "E9003", {"start": v(-215.7, -36.06) * mm, "end": v(-215.79, -37.89) * mm});
            skLineSegment(sketch, "E9004", {"start": v(-215.79, -37.89) * mm, "end": v(-215.88, -39.72) * mm});
            skLineSegment(sketch, "E9005", {"start": v(-215.88, -39.72) * mm, "end": v(-215.97, -41.54) * mm});
            skLineSegment(sketch, "E9006", {"start": v(-215.97, -41.54) * mm, "end": v(-216.08, -43.36) * mm});
            skLineSegment(sketch, "E9007", {"start": v(-216.08, -43.36) * mm, "end": v(-216.19, -45.18) * mm});
            skLineSegment(sketch, "E9008", {"start": v(-216.19, -45.18) * mm, "end": v(-216.3, -47) * mm});
            skLineSegment(sketch, "E9009", {"start": v(-216.3, -47) * mm, "end": v(-216.44, -48.8) * mm});
            skLineSegment(sketch, "E9010", {"start": v(-216.44, -48.8) * mm, "end": v(-216.57, -50.61) * mm});
            skLineSegment(sketch, "E9011", {"start": v(-216.57, -50.61) * mm, "end": v(-216.72, -52.41) * mm});
            skLineSegment(sketch, "E9012", {"start": v(-216.72, -52.41) * mm, "end": v(-216.87, -54.2) * mm});
            skLineSegment(sketch, "E9013", {"start": v(-216.87, -54.2) * mm, "end": v(-217.03, -56) * mm});
            skLineSegment(sketch, "E9014", {"start": v(-217.03, -56) * mm, "end": v(-217.2, -57.78) * mm});
            skLineSegment(sketch, "E9015", {"start": v(-217.2, -57.78) * mm, "end": v(-217.37, -59.56) * mm});
            skLineSegment(sketch, "E9016", {"start": v(-217.37, -59.56) * mm, "end": v(-217.56, -61.34) * mm});
            skLineSegment(sketch, "E9017", {"start": v(-217.56, -61.34) * mm, "end": v(-217.75, -63.1) * mm});
            skLineSegment(sketch, "E9018", {"start": v(-217.75, -63.1) * mm, "end": v(-217.95, -64.86) * mm});
            skLineSegment(sketch, "E9019", {"start": v(-217.95, -64.86) * mm, "end": v(-218.16, -66.62) * mm});
            skLineSegment(sketch, "E9020", {"start": v(-218.16, -66.62) * mm, "end": v(-218.37, -68.36) * mm});
            skLineSegment(sketch, "E9021", {"start": v(-218.37, -68.36) * mm, "end": v(-200.27, -68.36) * mm});
            skLineSegment(sketch, "E9022", {"start": v(-200.27, -68.36) * mm, "end": v(-200.27, 31.2) * mm});
            skLineSegment(sketch, "E9023", {"start": v(-200.27, 31.2) * mm, "end": v(-218.37, 31.2) * mm});
            skLineSegment(sketch, "E9024", {"start": v(-188.32, -62.66) * mm, "end": v(-187.49, -63.61) * mm});
            skLineSegment(sketch, "E9025", {"start": v(-187.49, -63.61) * mm, "end": v(-186.47, -64.49) * mm});
            skLineSegment(sketch, "E9026", {"start": v(-186.47, -64.49) * mm, "end": v(-185.3, -65.3) * mm});
            skLineSegment(sketch, "E9027", {"start": v(-185.3, -65.3) * mm, "end": v(-183.97, -66.03) * mm});
            skLineSegment(sketch, "E9028", {"start": v(-183.97, -66.03) * mm, "end": v(-182.5, -66.7) * mm});
            skLineSegment(sketch, "E9029", {"start": v(-182.5, -66.7) * mm, "end": v(-180.92, -67.3) * mm});
            skLineSegment(sketch, "E9030", {"start": v(-180.92, -67.3) * mm, "end": v(-179.24, -67.82) * mm});
            skLineSegment(sketch, "E9031", {"start": v(-179.24, -67.82) * mm, "end": v(-177.47, -68.27) * mm});
            skLineSegment(sketch, "E9032", {"start": v(-177.47, -68.27) * mm, "end": v(-175.62, -68.65) * mm});
            skLineSegment(sketch, "E9033", {"start": v(-175.62, -68.65) * mm, "end": v(-173.72, -68.96) * mm});
            skLineSegment(sketch, "E9034", {"start": v(-173.72, -68.96) * mm, "end": v(-171.79, -69.2) * mm});
            skLineSegment(sketch, "E9035", {"start": v(-171.79, -69.2) * mm, "end": v(-169.82, -69.36) * mm});
            skLineSegment(sketch, "E9036", {"start": v(-169.82, -69.36) * mm, "end": v(-167.85, -69.45) * mm});
            skLineSegment(sketch, "E9037", {"start": v(-167.85, -69.45) * mm, "end": v(-165.89, -69.46) * mm});
            skLineSegment(sketch, "E9038", {"start": v(-165.89, -69.46) * mm, "end": v(-163.95, -69.4) * mm});
            skLineSegment(sketch, "E9039", {"start": v(-163.95, -69.4) * mm, "end": v(-162.05, -69.27) * mm});
            skLineSegment(sketch, "E9040", {"start": v(-162.05, -69.27) * mm, "end": v(-160.2, -69.06) * mm});
            skLineSegment(sketch, "E9041", {"start": v(-160.2, -69.06) * mm, "end": v(-158.43, -68.77) * mm});
            skLineSegment(sketch, "E9042", {"start": v(-158.43, -68.77) * mm, "end": v(-156.74, -68.41) * mm});
            skLineSegment(sketch, "E9043", {"start": v(-156.74, -68.41) * mm, "end": v(-155.16, -67.97) * mm});
            skLineSegment(sketch, "E9044", {"start": v(-155.16, -67.97) * mm, "end": v(-153.7, -67.46) * mm});
            skLineSegment(sketch, "E9045", {"start": v(-153.7, -67.46) * mm, "end": v(-152.36, -66.87) * mm});
            skLineSegment(sketch, "E9046", {"start": v(-152.36, -66.87) * mm, "end": v(-151.17, -66.2) * mm});
            skLineSegment(sketch, "E9047", {"start": v(-151.17, -66.2) * mm, "end": v(-150.16, -65.46) * mm});
            skLineSegment(sketch, "E9048", {"start": v(-150.16, -65.46) * mm, "end": v(-149.44, -64.75) * mm});
            skLineSegment(sketch, "E9049", {"start": v(-149.44, -64.75) * mm, "end": v(-148.78, -63.85) * mm});
            skLineSegment(sketch, "E9050", {"start": v(-148.78, -63.85) * mm, "end": v(-148.16, -62.78) * mm});
            skLineSegment(sketch, "E9051", {"start": v(-148.16, -62.78) * mm, "end": v(-147.59, -61.56) * mm});
            skLineSegment(sketch, "E9052", {"start": v(-147.59, -61.56) * mm, "end": v(-147.06, -60.2) * mm});
            skLineSegment(sketch, "E9053", {"start": v(-147.06, -60.2) * mm, "end": v(-146.59, -58.7) * mm});
            skLineSegment(sketch, "E9054", {"start": v(-146.59, -58.7) * mm, "end": v(-146.16, -57.08) * mm});
            skLineSegment(sketch, "E9055", {"start": v(-146.16, -57.08) * mm, "end": v(-145.78, -55.35) * mm});
            skLineSegment(sketch, "E9056", {"start": v(-145.78, -55.35) * mm, "end": v(-145.44, -53.54) * mm});
            skLineSegment(sketch, "E9057", {"start": v(-145.44, -53.54) * mm, "end": v(-145.16, -51.64) * mm});
            skLineSegment(sketch, "E9058", {"start": v(-145.16, -51.64) * mm, "end": v(-144.92, -49.67) * mm});
            skLineSegment(sketch, "E9059", {"start": v(-144.92, -49.67) * mm, "end": v(-144.73, -47.65) * mm});
            skLineSegment(sketch, "E9060", {"start": v(-144.73, -47.65) * mm, "end": v(-144.59, -45.58) * mm});
            skLineSegment(sketch, "E9061", {"start": v(-144.59, -45.58) * mm, "end": v(-144.5, -43.48) * mm});
            skLineSegment(sketch, "E9062", {"start": v(-144.5, -43.48) * mm, "end": v(-144.45, -41.37) * mm});
            skLineSegment(sketch, "E9063", {"start": v(-144.45, -41.37) * mm, "end": v(-144.45, -39.24) * mm});
            skLineSegment(sketch, "E9064", {"start": v(-144.45, -39.24) * mm, "end": v(-144.5, -37.13) * mm});
            skLineSegment(sketch, "E9065", {"start": v(-144.5, -37.13) * mm, "end": v(-144.59, -35.03) * mm});
            skLineSegment(sketch, "E9066", {"start": v(-144.59, -35.03) * mm, "end": v(-144.73, -32.96) * mm});
            skLineSegment(sketch, "E9067", {"start": v(-144.73, -32.96) * mm, "end": v(-144.92, -30.94) * mm});
            skLineSegment(sketch, "E9068", {"start": v(-144.92, -30.94) * mm, "end": v(-145.16, -28.97) * mm});
            skLineSegment(sketch, "E9069", {"start": v(-145.16, -28.97) * mm, "end": v(-145.44, -27.07) * mm});
            skLineSegment(sketch, "E9070", {"start": v(-145.44, -27.07) * mm, "end": v(-145.78, -25.26) * mm});
            skLineSegment(sketch, "E9071", {"start": v(-145.78, -25.26) * mm, "end": v(-146.16, -23.53) * mm});
            skLineSegment(sketch, "E9072", {"start": v(-146.16, -23.53) * mm, "end": v(-146.59, -21.92) * mm});
            skLineSegment(sketch, "E9073", {"start": v(-146.59, -21.92) * mm, "end": v(-147.06, -20.42) * mm});
            skLineSegment(sketch, "E9074", {"start": v(-147.06, -20.42) * mm, "end": v(-147.59, -19.05) * mm});
            skLineSegment(sketch, "E9075", {"start": v(-147.59, -19.05) * mm, "end": v(-148.16, -17.83) * mm});
            skLineSegment(sketch, "E9076", {"start": v(-148.16, -17.83) * mm, "end": v(-148.78, -16.76) * mm});
            skLineSegment(sketch, "E9077", {"start": v(-148.78, -16.76) * mm, "end": v(-149.44, -15.86) * mm});
            skLineSegment(sketch, "E9078", {"start": v(-149.44, -15.86) * mm, "end": v(-150.16, -15.15) * mm});
            skLineSegment(sketch, "E9079", {"start": v(-150.16, -15.15) * mm, "end": v(-151.52, -14.18) * mm});
            skLineSegment(sketch, "E9080", {"start": v(-151.52, -14.18) * mm, "end": v(-153.03, -13.4) * mm});
            skLineSegment(sketch, "E9081", {"start": v(-153.03, -13.4) * mm, "end": v(-154.66, -12.8) * mm});
            skLineSegment(sketch, "E9082", {"start": v(-154.66, -12.8) * mm, "end": v(-156.4, -12.37) * mm});
            skLineSegment(sketch, "E9083", {"start": v(-156.4, -12.37) * mm, "end": v(-158.23, -12.07) * mm});
            skLineSegment(sketch, "E9084", {"start": v(-158.23, -12.07) * mm, "end": v(-160.12, -11.9) * mm});
            skLineSegment(sketch, "E9085", {"start": v(-160.12, -11.9) * mm, "end": v(-162.06, -11.8) * mm});
            skLineSegment(sketch, "E9086", {"start": v(-162.06, -11.8) * mm, "end": v(-164, -11.8) * mm});
            skLineSegment(sketch, "E9087", {"start": v(-164, -11.8) * mm, "end": v(-165.96, -11.85) * mm});
            skLineSegment(sketch, "E9088", {"start": v(-165.96, -11.85) * mm, "end": v(-167.88, -11.94) * mm});
            skLineSegment(sketch, "E9089", {"start": v(-167.88, -11.94) * mm, "end": v(-169.76, -12.04) * mm});
            skLineSegment(sketch, "E9090", {"start": v(-169.76, -12.04) * mm, "end": v(-171.58, -12.14) * mm});
            skLineSegment(sketch, "E9091", {"start": v(-171.58, -12.14) * mm, "end": v(-173.3, -12.21) * mm});
            skLineSegment(sketch, "E9092", {"start": v(-173.3, -12.21) * mm, "end": v(-174.93, -12.24) * mm});
            skLineSegment(sketch, "E9093", {"start": v(-174.93, -12.24) * mm, "end": v(-174.93, 16.72) * mm});
            skLineSegment(sketch, "E9094", {"start": v(-174.93, 16.72) * mm, "end": v(-160.44, 16.72) * mm});
            skLineSegment(sketch, "E9095", {"start": v(-160.44, 16.72) * mm, "end": v(-162.25, 5.86) * mm});
            skLineSegment(sketch, "E9096", {"start": v(-162.25, 5.86) * mm, "end": v(-144.15, 5.86) * mm});
            skLineSegment(sketch, "E9097", {"start": v(-144.15, 5.86) * mm, "end": v(-144.33, 7.47) * mm});
            skLineSegment(sketch, "E9098", {"start": v(-144.33, 7.47) * mm, "end": v(-144.48, 9.2) * mm});
            skLineSegment(sketch, "E9099", {"start": v(-144.48, 9.2) * mm, "end": v(-144.62, 11.03) * mm});
            skLineSegment(sketch, "E9100", {"start": v(-144.62, 11.03) * mm, "end": v(-144.78, 12.92) * mm});
            skLineSegment(sketch, "E9101", {"start": v(-144.78, 12.92) * mm, "end": v(-144.97, 14.84) * mm});
            skLineSegment(sketch, "E9102", {"start": v(-144.97, 14.84) * mm, "end": v(-145.22, 16.77) * mm});
            skLineSegment(sketch, "E9103", {"start": v(-145.22, 16.77) * mm, "end": v(-145.54, 18.67) * mm});
            skLineSegment(sketch, "E9104", {"start": v(-145.54, 18.67) * mm, "end": v(-145.95, 20.53) * mm});
            skLineSegment(sketch, "E9105", {"start": v(-145.95, 20.53) * mm, "end": v(-146.48, 22.3) * mm});
            skLineSegment(sketch, "E9106", {"start": v(-146.48, 22.3) * mm, "end": v(-147.15, 23.98) * mm});
            skLineSegment(sketch, "E9107", {"start": v(-147.15, 23.98) * mm, "end": v(-147.97, 25.5) * mm});
            skLineSegment(sketch, "E9108", {"start": v(-147.97, 25.5) * mm, "end": v(-148.97, 26.88) * mm});
            skLineSegment(sketch, "E9109", {"start": v(-148.97, 26.88) * mm, "end": v(-150.16, 28.05) * mm});
            skLineSegment(sketch, "E9110", {"start": v(-150.16, 28.05) * mm, "end": v(-151.19, 28.81) * mm});
            skLineSegment(sketch, "E9111", {"start": v(-151.19, 28.81) * mm, "end": v(-152.34, 29.5) * mm});
            skLineSegment(sketch, "E9112", {"start": v(-152.34, 29.5) * mm, "end": v(-153.6, 30.12) * mm});
            skLineSegment(sketch, "E9113", {"start": v(-153.6, 30.12) * mm, "end": v(-154.96, 30.66) * mm});
            skLineSegment(sketch, "E9114", {"start": v(-154.96, 30.66) * mm, "end": v(-156.42, 31.14) * mm});
            skLineSegment(sketch, "E9115", {"start": v(-156.42, 31.14) * mm, "end": v(-157.94, 31.54) * mm});
            skLineSegment(sketch, "E9116", {"start": v(-157.94, 31.54) * mm, "end": v(-159.54, 31.86) * mm});
            skLineSegment(sketch, "E9117", {"start": v(-159.54, 31.86) * mm, "end": v(-161.2, 32.12) * mm});
            skLineSegment(sketch, "E9118", {"start": v(-161.2, 32.12) * mm, "end": v(-162.9, 32.3) * mm});
            skLineSegment(sketch, "E9119", {"start": v(-162.9, 32.3) * mm, "end": v(-164.64, 32.4) * mm});
            skLineSegment(sketch, "E9120", {"start": v(-164.64, 32.4) * mm, "end": v(-166.4, 32.44) * mm});
            skLineSegment(sketch, "E9121", {"start": v(-166.4, 32.44) * mm, "end": v(-168.19, 32.4) * mm});
            skLineSegment(sketch, "E9122", {"start": v(-168.19, 32.4) * mm, "end": v(-169.97, 32.3) * mm});
            skLineSegment(sketch, "E9123", {"start": v(-169.97, 32.3) * mm, "end": v(-171.75, 32.1) * mm});
            skLineSegment(sketch, "E9124", {"start": v(-171.75, 32.1) * mm, "end": v(-173.51, 31.85) * mm});
            skLineSegment(sketch, "E9125", {"start": v(-173.51, 31.85) * mm, "end": v(-175.25, 31.51) * mm});
            skLineSegment(sketch, "E9126", {"start": v(-175.25, 31.51) * mm, "end": v(-176.95, 31.1) * mm});
            skLineSegment(sketch, "E9127", {"start": v(-176.95, 31.1) * mm, "end": v(-178.6, 30.62) * mm});
            skLineSegment(sketch, "E9128", {"start": v(-178.6, 30.62) * mm, "end": v(-180.2, 30.06) * mm});
            skLineSegment(sketch, "E9129", {"start": v(-180.2, 30.06) * mm, "end": v(-181.73, 29.42) * mm});
            skLineSegment(sketch, "E9130", {"start": v(-181.73, 29.42) * mm, "end": v(-183.18, 28.71) * mm});
            skLineSegment(sketch, "E9131", {"start": v(-183.18, 28.71) * mm, "end": v(-184.53, 27.93) * mm});
            skLineSegment(sketch, "E9132", {"start": v(-184.53, 27.93) * mm, "end": v(-185.8, 27.07) * mm});
            skLineSegment(sketch, "E9133", {"start": v(-185.8, 27.07) * mm, "end": v(-186.94, 26.13) * mm});
            skLineSegment(sketch, "E9134", {"start": v(-186.94, 26.13) * mm, "end": v(-187.96, 25.12) * mm});
            skLineSegment(sketch, "E9135", {"start": v(-187.96, 25.12) * mm, "end": v(-188.86, 24.03) * mm});
            skLineSegment(sketch, "E9136", {"start": v(-188.86, 24.03) * mm, "end": v(-189.6, 22.87) * mm});
            skLineSegment(sketch, "E9137", {"start": v(-189.6, 22.87) * mm, "end": v(-190.2, 21.63) * mm});
            skLineSegment(sketch, "E9138", {"start": v(-190.2, 21.63) * mm, "end": v(-190.64, 20.31) * mm});
            skLineSegment(sketch, "E9139", {"start": v(-190.64, 20.31) * mm, "end": v(-190.92, 19.15) * mm});
            skLineSegment(sketch, "E9140", {"start": v(-190.92, 19.15) * mm, "end": v(-191.19, 17.83) * mm});
            skLineSegment(sketch, "E9141", {"start": v(-191.19, 17.83) * mm, "end": v(-191.44, 16.38) * mm});
            skLineSegment(sketch, "E9142", {"start": v(-191.44, 16.38) * mm, "end": v(-191.68, 14.8) * mm});
            skLineSegment(sketch, "E9143", {"start": v(-191.68, 14.8) * mm, "end": v(-191.9, 13.13) * mm});
            skLineSegment(sketch, "E9144", {"start": v(-191.9, 13.13) * mm, "end": v(-192.09, 11.36) * mm});
            skLineSegment(sketch, "E9145", {"start": v(-192.09, 11.36) * mm, "end": v(-192.25, 9.5) * mm});
            skLineSegment(sketch, "E9146", {"start": v(-192.25, 9.5) * mm, "end": v(-192.39, 7.58) * mm});
            skLineSegment(sketch, "E9147", {"start": v(-192.39, 7.58) * mm, "end": v(-192.49, 5.6) * mm});
            skLineSegment(sketch, "E9148", {"start": v(-192.49, 5.6) * mm, "end": v(-192.55, 3.6) * mm});
            skLineSegment(sketch, "E9149", {"start": v(-192.55, 3.6) * mm, "end": v(-192.57, 1.56) * mm});
            skLineSegment(sketch, "E9150", {"start": v(-192.57, 1.56) * mm, "end": v(-192.55, -0.48) * mm});
            skLineSegment(sketch, "E9151", {"start": v(-192.55, -0.48) * mm, "end": v(-192.47, -2.53) * mm});
            skLineSegment(sketch, "E9152", {"start": v(-192.47, -2.53) * mm, "end": v(-192.35, -4.55) * mm});
            skLineSegment(sketch, "E9153", {"start": v(-192.35, -4.55) * mm, "end": v(-192.17, -6.55) * mm});
            skLineSegment(sketch, "E9154", {"start": v(-192.17, -6.55) * mm, "end": v(-191.93, -8.5) * mm});
            skLineSegment(sketch, "E9155", {"start": v(-191.93, -8.5) * mm, "end": v(-191.63, -10.4) * mm});
            skLineSegment(sketch, "E9156", {"start": v(-191.63, -10.4) * mm, "end": v(-191.26, -12.22) * mm});
            skLineSegment(sketch, "E9157", {"start": v(-191.26, -12.22) * mm, "end": v(-190.82, -13.95) * mm});
            skLineSegment(sketch, "E9158", {"start": v(-190.82, -13.95) * mm, "end": v(-190.3, -15.59) * mm});
            skLineSegment(sketch, "E9159", {"start": v(-190.3, -15.59) * mm, "end": v(-189.72, -17.1) * mm});
            skLineSegment(sketch, "E9160", {"start": v(-189.72, -17.1) * mm, "end": v(-189.06, -18.5) * mm});
            skLineSegment(sketch, "E9161", {"start": v(-189.06, -18.5) * mm, "end": v(-188.3, -19.76) * mm});
            skLineSegment(sketch, "E9162", {"start": v(-188.3, -19.76) * mm, "end": v(-187.47, -20.86) * mm});
            skLineSegment(sketch, "E9163", {"start": v(-187.47, -20.86) * mm, "end": v(-186.54, -21.78) * mm});
            skLineSegment(sketch, "E9164", {"start": v(-186.54, -21.78) * mm, "end": v(-185.52, -22.53) * mm});
            skLineSegment(sketch, "E9165", {"start": v(-185.52, -22.53) * mm, "end": v(-184.2, -23.2) * mm});
            skLineSegment(sketch, "E9166", {"start": v(-184.2, -23.2) * mm, "end": v(-182.79, -23.7) * mm});
            skLineSegment(sketch, "E9167", {"start": v(-182.79, -23.7) * mm, "end": v(-181.29, -24.05) * mm});
            skLineSegment(sketch, "E9168", {"start": v(-181.29, -24.05) * mm, "end": v(-179.72, -24.3) * mm});
            skLineSegment(sketch, "E9169", {"start": v(-179.72, -24.3) * mm, "end": v(-178.1, -24.46) * mm});
            skLineSegment(sketch, "E9170", {"start": v(-178.1, -24.46) * mm, "end": v(-176.47, -24.57) * mm});
            skLineSegment(sketch, "E9171", {"start": v(-176.47, -24.57) * mm, "end": v(-174.8, -24.65) * mm});
            skLineSegment(sketch, "E9172", {"start": v(-174.8, -24.65) * mm, "end": v(-173.16, -24.74) * mm});
            skLineSegment(sketch, "E9173", {"start": v(-173.16, -24.74) * mm, "end": v(-171.53, -24.86) * mm});
            skLineSegment(sketch, "E9174", {"start": v(-171.53, -24.86) * mm, "end": v(-169.95, -25.05) * mm});
            skLineSegment(sketch, "E9175", {"start": v(-169.95, -25.05) * mm, "end": v(-168.42, -25.33) * mm});
            skLineSegment(sketch, "E9176", {"start": v(-168.42, -25.33) * mm, "end": v(-166.98, -25.73) * mm});
            skLineSegment(sketch, "E9177", {"start": v(-166.98, -25.73) * mm, "end": v(-165.63, -26.29) * mm});
            skLineSegment(sketch, "E9178", {"start": v(-165.63, -26.29) * mm, "end": v(-164.39, -27.02) * mm});
            skLineSegment(sketch, "E9179", {"start": v(-164.39, -27.02) * mm, "end": v(-163.28, -27.97) * mm});
            skLineSegment(sketch, "E9180", {"start": v(-163.28, -27.97) * mm, "end": v(-162.33, -29.16) * mm});
            skLineSegment(sketch, "E9181", {"start": v(-162.33, -29.16) * mm, "end": v(-161.54, -30.62) * mm});
            skLineSegment(sketch, "E9182", {"start": v(-161.54, -30.62) * mm, "end": v(-160.97, -32.07) * mm});
            skLineSegment(sketch, "E9183", {"start": v(-160.97, -32.07) * mm, "end": v(-160.53, -33.5) * mm});
            skLineSegment(sketch, "E9184", {"start": v(-160.53, -33.5) * mm, "end": v(-160.2, -34.93) * mm});
            skLineSegment(sketch, "E9185", {"start": v(-160.2, -34.93) * mm, "end": v(-160, -36.33) * mm});
            skLineSegment(sketch, "E9186", {"start": v(-160, -36.33) * mm, "end": v(-159.9, -37.71) * mm});
            skLineSegment(sketch, "E9187", {"start": v(-159.9, -37.71) * mm, "end": v(-159.9, -39.06) * mm});
            skLineSegment(sketch, "E9188", {"start": v(-159.9, -39.06) * mm, "end": v(-160, -40.37) * mm});
            skLineSegment(sketch, "E9189", {"start": v(-160, -40.37) * mm, "end": v(-160.2, -41.65) * mm});
            skLineSegment(sketch, "E9190", {"start": v(-160.2, -41.65) * mm, "end": v(-160.46, -42.88) * mm});
            skLineSegment(sketch, "E9191", {"start": v(-160.46, -42.88) * mm, "end": v(-160.8, -44.06) * mm});
            skLineSegment(sketch, "E9192", {"start": v(-160.8, -44.06) * mm, "end": v(-161.2, -45.19) * mm});
            skLineSegment(sketch, "E9193", {"start": v(-161.2, -45.19) * mm, "end": v(-161.67, -46.26) * mm});
            skLineSegment(sketch, "E9194", {"start": v(-161.67, -46.26) * mm, "end": v(-162.19, -47.27) * mm});
            skLineSegment(sketch, "E9195", {"start": v(-162.19, -47.27) * mm, "end": v(-162.75, -48.21) * mm});
            skLineSegment(sketch, "E9196", {"start": v(-162.75, -48.21) * mm, "end": v(-163.36, -49.09) * mm});
            skLineSegment(sketch, "E9197", {"start": v(-163.36, -49.09) * mm, "end": v(-164, -49.88) * mm});
            skLineSegment(sketch, "E9198", {"start": v(-164, -49.88) * mm, "end": v(-164.66, -50.6) * mm});
            skLineSegment(sketch, "E9199", {"start": v(-164.66, -50.6) * mm, "end": v(-165.34, -51.23) * mm});
            skLineSegment(sketch, "E9200", {"start": v(-165.34, -51.23) * mm, "end": v(-166.04, -51.78) * mm});
            skLineSegment(sketch, "E9201", {"start": v(-166.04, -51.78) * mm, "end": v(-166.74, -52.23) * mm});
            skLineSegment(sketch, "E9202", {"start": v(-166.74, -52.23) * mm, "end": v(-167.44, -52.58) * mm});
            skLineSegment(sketch, "E9203", {"start": v(-167.44, -52.58) * mm, "end": v(-168.13, -52.83) * mm});
            skLineSegment(sketch, "E9204", {"start": v(-168.13, -52.83) * mm, "end": v(-168.8, -52.97) * mm});
            skLineSegment(sketch, "E9205", {"start": v(-168.8, -52.97) * mm, "end": v(-169.46, -53) * mm});
            skLineSegment(sketch, "E9206", {"start": v(-169.46, -53) * mm, "end": v(-170.08, -52.92) * mm});
            skLineSegment(sketch, "E9207", {"start": v(-170.08, -52.92) * mm, "end": v(-170.67, -52.72) * mm});
            skLineSegment(sketch, "E9208", {"start": v(-170.67, -52.72) * mm, "end": v(-171.22, -52.38) * mm});
            skLineSegment(sketch, "E9209", {"start": v(-171.22, -52.38) * mm, "end": v(-171.72, -51.92) * mm});
            skLineSegment(sketch, "E9210", {"start": v(-171.72, -51.92) * mm, "end": v(-172.16, -51.33) * mm});
            skLineSegment(sketch, "E9211", {"start": v(-172.16, -51.33) * mm, "end": v(-172.54, -50.6) * mm});
            skLineSegment(sketch, "E9212", {"start": v(-172.54, -50.6) * mm, "end": v(-172.85, -49.72) * mm});
            skLineSegment(sketch, "E9213", {"start": v(-172.85, -49.72) * mm, "end": v(-173.08, -48.7) * mm});
            skLineSegment(sketch, "E9214", {"start": v(-173.08, -48.7) * mm, "end": v(-173.23, -47.51) * mm});
            skLineSegment(sketch, "E9215", {"start": v(-173.23, -47.51) * mm, "end": v(-173.3, -46.18) * mm});
            skLineSegment(sketch, "E9216", {"start": v(-173.3, -46.18) * mm, "end": v(-173.26, -44.68) * mm});
            skLineSegment(sketch, "E9217", {"start": v(-173.26, -44.68) * mm, "end": v(-173.12, -43.02) * mm});
            skLineSegment(sketch, "E9218", {"start": v(-173.12, -43.02) * mm, "end": v(-191.22, -43.02) * mm});
            skLineSegment(sketch, "E9219", {"start": v(-191.22, -43.02) * mm, "end": v(-191.24, -44.78) * mm});
            skLineSegment(sketch, "E9220", {"start": v(-191.24, -44.78) * mm, "end": v(-191.3, -46.6) * mm});
            skLineSegment(sketch, "E9221", {"start": v(-191.3, -46.6) * mm, "end": v(-191.34, -48.47) * mm});
            skLineSegment(sketch, "E9222", {"start": v(-191.34, -48.47) * mm, "end": v(-191.37, -50.36) * mm});
            skLineSegment(sketch, "E9223", {"start": v(-191.37, -50.36) * mm, "end": v(-191.33, -52.25) * mm});
            skLineSegment(sketch, "E9224", {"start": v(-191.33, -52.25) * mm, "end": v(-191.2, -54.13) * mm});
            skLineSegment(sketch, "E9225", {"start": v(-191.2, -54.13) * mm, "end": v(-190.97, -55.98) * mm});
            skLineSegment(sketch, "E9226", {"start": v(-190.97, -55.98) * mm, "end": v(-190.6, -57.77) * mm});
            skLineSegment(sketch, "E9227", {"start": v(-190.6, -57.77) * mm, "end": v(-190.04, -59.5) * mm});
            skLineSegment(sketch, "E9228", {"start": v(-190.04, -59.5) * mm, "end": v(-189.3, -61.13) * mm});
            skLineSegment(sketch, "E9229", {"start": v(-189.3, -61.13) * mm, "end": v(-188.32, -62.66) * mm});
            skLineSegment(sketch, "E9230", {"start": v(-100.7, 31.2) * mm, "end": v(-100.49, 29.46) * mm});
            skLineSegment(sketch, "E9231", {"start": v(-100.49, 29.46) * mm, "end": v(-100.28, 27.7) * mm});
            skLineSegment(sketch, "E9232", {"start": v(-100.28, 27.7) * mm, "end": v(-100.08, 25.94) * mm});
            skLineSegment(sketch, "E9233", {"start": v(-100.08, 25.94) * mm, "end": v(-99.89, 24.18) * mm});
            skLineSegment(sketch, "E9234", {"start": v(-99.89, 24.18) * mm, "end": v(-99.7, 22.4) * mm});
            skLineSegment(sketch, "E9235", {"start": v(-99.7, 22.4) * mm, "end": v(-99.53, 20.62) * mm});
            skLineSegment(sketch, "E9236", {"start": v(-99.53, 20.62) * mm, "end": v(-99.36, 18.84) * mm});
            skLineSegment(sketch, "E9237", {"start": v(-99.36, 18.84) * mm, "end": v(-99.2, 17.05) * mm});
            skLineSegment(sketch, "E9238", {"start": v(-99.2, 17.05) * mm, "end": v(-99.04, 15.25) * mm});
            skLineSegment(sketch, "E9239", {"start": v(-99.04, 15.25) * mm, "end": v(-98.9, 13.45) * mm});
            skLineSegment(sketch, "E9240", {"start": v(-98.9, 13.45) * mm, "end": v(-98.76, 11.64) * mm});
            skLineSegment(sketch, "E9241", {"start": v(-98.76, 11.64) * mm, "end": v(-98.64, 9.84) * mm});
            skLineSegment(sketch, "E9242", {"start": v(-98.64, 9.84) * mm, "end": v(-98.52, 8.02) * mm});
            skLineSegment(sketch, "E9243", {"start": v(-98.52, 8.02) * mm, "end": v(-98.4, 6.2) * mm});
            skLineSegment(sketch, "E9244", {"start": v(-98.4, 6.2) * mm, "end": v(-98.3, 4.38) * mm});
            skLineSegment(sketch, "E9245", {"start": v(-98.3, 4.38) * mm, "end": v(-98.2, 2.56) * mm});
            skLineSegment(sketch, "E9246", {"start": v(-98.2, 2.56) * mm, "end": v(-98.12, 0.73) * mm});
            skLineSegment(sketch, "E9247", {"start": v(-98.12, 0.73) * mm, "end": v(-98.04, -1.1) * mm});
            skLineSegment(sketch, "E9248", {"start": v(-98.04, -1.1) * mm, "end": v(-97.96, -2.93) * mm});
            skLineSegment(sketch, "E9249", {"start": v(-97.96, -2.93) * mm, "end": v(-97.9, -4.77) * mm});
            skLineSegment(sketch, "E9250", {"start": v(-97.9, -4.77) * mm, "end": v(-97.84, -6.6) * mm});
            skLineSegment(sketch, "E9251", {"start": v(-97.84, -6.6) * mm, "end": v(-97.8, -8.45) * mm});
            skLineSegment(sketch, "E9252", {"start": v(-97.8, -8.45) * mm, "end": v(-97.76, -10.29) * mm});
            skLineSegment(sketch, "E9253", {"start": v(-97.76, -10.29) * mm, "end": v(-97.72, -12.13) * mm});
            skLineSegment(sketch, "E9254", {"start": v(-97.72, -12.13) * mm, "end": v(-97.7, -13.97) * mm});
            skLineSegment(sketch, "E9255", {"start": v(-97.7, -13.97) * mm, "end": v(-97.68, -15.81) * mm});
            skLineSegment(sketch, "E9256", {"start": v(-97.68, -15.81) * mm, "end": v(-97.68, -17.66) * mm});
            skLineSegment(sketch, "E9257", {"start": v(-97.68, -17.66) * mm, "end": v(-97.68, -19.5) * mm});
            skLineSegment(sketch, "E9258", {"start": v(-97.68, -19.5) * mm, "end": v(-97.68, -21.35) * mm});
            skLineSegment(sketch, "E9259", {"start": v(-97.68, -21.35) * mm, "end": v(-97.7, -23.19) * mm});
            skLineSegment(sketch, "E9260", {"start": v(-97.7, -23.19) * mm, "end": v(-97.72, -25.03) * mm});
            skLineSegment(sketch, "E9261", {"start": v(-97.72, -25.03) * mm, "end": v(-97.76, -26.87) * mm});
            skLineSegment(sketch, "E9262", {"start": v(-97.76, -26.87) * mm, "end": v(-97.8, -28.71) * mm});
            skLineSegment(sketch, "E9263", {"start": v(-97.8, -28.71) * mm, "end": v(-97.84, -30.55) * mm});
            skLineSegment(sketch, "E9264", {"start": v(-97.84, -30.55) * mm, "end": v(-97.9, -32.4) * mm});
            skLineSegment(sketch, "E9265", {"start": v(-97.9, -32.4) * mm, "end": v(-97.96, -34.23) * mm});
            skLineSegment(sketch, "E9266", {"start": v(-97.96, -34.23) * mm, "end": v(-98.04, -36.06) * mm});
            skLineSegment(sketch, "E9267", {"start": v(-98.04, -36.06) * mm, "end": v(-98.12, -37.89) * mm});
            skLineSegment(sketch, "E9268", {"start": v(-98.12, -37.89) * mm, "end": v(-98.2, -39.72) * mm});
            skLineSegment(sketch, "E9269", {"start": v(-98.2, -39.72) * mm, "end": v(-98.3, -41.54) * mm});
            skLineSegment(sketch, "E9270", {"start": v(-98.3, -41.54) * mm, "end": v(-98.4, -43.36) * mm});
            skLineSegment(sketch, "E9271", {"start": v(-98.4, -43.36) * mm, "end": v(-98.52, -45.18) * mm});
            skLineSegment(sketch, "E9272", {"start": v(-98.52, -45.18) * mm, "end": v(-98.64, -47) * mm});
            skLineSegment(sketch, "E9273", {"start": v(-98.64, -47) * mm, "end": v(-98.76, -48.8) * mm});
            skLineSegment(sketch, "E9274", {"start": v(-98.76, -48.8) * mm, "end": v(-98.9, -50.61) * mm});
            skLineSegment(sketch, "E9275", {"start": v(-98.9, -50.61) * mm, "end": v(-99.04, -52.41) * mm});
            skLineSegment(sketch, "E9276", {"start": v(-99.04, -52.41) * mm, "end": v(-99.2, -54.2) * mm});
            skLineSegment(sketch, "E9277", {"start": v(-99.2, -54.2) * mm, "end": v(-99.36, -56) * mm});
            skLineSegment(sketch, "E9278", {"start": v(-99.36, -56) * mm, "end": v(-99.53, -57.78) * mm});
            skLineSegment(sketch, "E9279", {"start": v(-99.53, -57.78) * mm, "end": v(-99.7, -59.56) * mm});
            skLineSegment(sketch, "E9280", {"start": v(-99.7, -59.56) * mm, "end": v(-99.89, -61.34) * mm});
            skLineSegment(sketch, "E9281", {"start": v(-99.89, -61.34) * mm, "end": v(-100.08, -63.1) * mm});
            skLineSegment(sketch, "E9282", {"start": v(-100.08, -63.1) * mm, "end": v(-100.28, -64.86) * mm});
            skLineSegment(sketch, "E9283", {"start": v(-100.28, -64.86) * mm, "end": v(-100.49, -66.62) * mm});
            skLineSegment(sketch, "E9284", {"start": v(-100.49, -66.62) * mm, "end": v(-100.7, -68.36) * mm});
            skLineSegment(sketch, "E9285", {"start": v(-100.7, -68.36) * mm, "end": v(-82.6, -68.36) * mm});
            skLineSegment(sketch, "E9286", {"start": v(-82.6, -68.36) * mm, "end": v(-82.73, -67.4) * mm});
            skLineSegment(sketch, "E9287", {"start": v(-82.73, -67.4) * mm, "end": v(-82.9, -66.28) * mm});
            skLineSegment(sketch, "E9288", {"start": v(-82.9, -66.28) * mm, "end": v(-83.09, -65) * mm});
            skLineSegment(sketch, "E9289", {"start": v(-83.09, -65) * mm, "end": v(-83.3, -63.6) * mm});
            skLineSegment(sketch, "E9290", {"start": v(-83.3, -63.6) * mm, "end": v(-83.54, -62.09) * mm});
            skLineSegment(sketch, "E9291", {"start": v(-83.54, -62.09) * mm, "end": v(-83.78, -60.46) * mm});
            skLineSegment(sketch, "E9292", {"start": v(-83.78, -60.46) * mm, "end": v(-84.02, -58.75) * mm});
            skLineSegment(sketch, "E9293", {"start": v(-84.02, -58.75) * mm, "end": v(-84.26, -56.95) * mm});
            skLineSegment(sketch, "E9294", {"start": v(-84.26, -56.95) * mm, "end": v(-84.5, -55.1) * mm});
            skLineSegment(sketch, "E9295", {"start": v(-84.5, -55.1) * mm, "end": v(-84.71, -53.2) * mm});
            skLineSegment(sketch, "E9296", {"start": v(-84.71, -53.2) * mm, "end": v(-84.9, -51.26) * mm});
            skLineSegment(sketch, "E9297", {"start": v(-84.9, -51.26) * mm, "end": v(-85.07, -49.3) * mm});
            skLineSegment(sketch, "E9298", {"start": v(-85.07, -49.3) * mm, "end": v(-85.2, -47.33) * mm});
            skLineSegment(sketch, "E9299", {"start": v(-85.2, -47.33) * mm, "end": v(-85.3, -45.37) * mm});
            skLineSegment(sketch, "E9300", {"start": v(-85.3, -45.37) * mm, "end": v(-85.34, -43.42) * mm});
            skLineSegment(sketch, "E9301", {"start": v(-85.34, -43.42) * mm, "end": v(-85.32, -41.52) * mm});
            skLineSegment(sketch, "E9302", {"start": v(-85.32, -41.52) * mm, "end": v(-85.26, -39.66) * mm});
            skLineSegment(sketch, "E9303", {"start": v(-85.26, -39.66) * mm, "end": v(-85.12, -37.86) * mm});
            skLineSegment(sketch, "E9304", {"start": v(-85.12, -37.86) * mm, "end": v(-84.91, -36.13) * mm});
            skLineSegment(sketch, "E9305", {"start": v(-84.91, -36.13) * mm, "end": v(-84.62, -34.5) * mm});
            skLineSegment(sketch, "E9306", {"start": v(-84.62, -34.5) * mm, "end": v(-84.25, -32.96) * mm});
            skLineSegment(sketch, "E9307", {"start": v(-84.25, -32.96) * mm, "end": v(-83.79, -31.55) * mm});
            skLineSegment(sketch, "E9308", {"start": v(-83.79, -31.55) * mm, "end": v(-83.23, -30.26) * mm});
            skLineSegment(sketch, "E9309", {"start": v(-83.23, -30.26) * mm, "end": v(-82.57, -29.12) * mm});
            skLineSegment(sketch, "E9310", {"start": v(-82.57, -29.12) * mm, "end": v(-81.8, -28.14) * mm});
            skLineSegment(sketch, "E9311", {"start": v(-81.8, -28.14) * mm, "end": v(-80.9, -27.33) * mm});
            skLineSegment(sketch, "E9312", {"start": v(-80.9, -27.33) * mm, "end": v(-79.89, -26.7) * mm});
            skLineSegment(sketch, "E9313", {"start": v(-79.89, -26.7) * mm, "end": v(-78.75, -26.28) * mm});
            skLineSegment(sketch, "E9314", {"start": v(-78.75, -26.28) * mm, "end": v(-77.51, -26.05) * mm});
            skLineSegment(sketch, "E9315", {"start": v(-77.51, -26.05) * mm, "end": v(-76.39, -26.05) * mm});
            skLineSegment(sketch, "E9316", {"start": v(-76.39, -26.05) * mm, "end": v(-75.36, -26.25) * mm});
            skLineSegment(sketch, "E9317", {"start": v(-75.36, -26.25) * mm, "end": v(-74.44, -26.66) * mm});
            skLineSegment(sketch, "E9318", {"start": v(-74.44, -26.66) * mm, "end": v(-73.6, -27.25) * mm});
            skLineSegment(sketch, "E9319", {"start": v(-73.6, -27.25) * mm, "end": v(-72.86, -28) * mm});
            skLineSegment(sketch, "E9320", {"start": v(-72.86, -28) * mm, "end": v(-72.2, -28.93) * mm});
            skLineSegment(sketch, "E9321", {"start": v(-72.2, -28.93) * mm, "end": v(-71.63, -30) * mm});
            skLineSegment(sketch, "E9322", {"start": v(-71.63, -30) * mm, "end": v(-71.13, -31.2) * mm});
            skLineSegment(sketch, "E9323", {"start": v(-71.13, -31.2) * mm, "end": v(-70.7, -32.54) * mm});
            skLineSegment(sketch, "E9324", {"start": v(-70.7, -32.54) * mm, "end": v(-70.35, -33.98) * mm});
            skLineSegment(sketch, "E9325", {"start": v(-70.35, -33.98) * mm, "end": v(-70.06, -35.52) * mm});
            skLineSegment(sketch, "E9326", {"start": v(-70.06, -35.52) * mm, "end": v(-69.83, -37.14) * mm});
            skLineSegment(sketch, "E9327", {"start": v(-69.83, -37.14) * mm, "end": v(-69.66, -38.84) * mm});
            skLineSegment(sketch, "E9328", {"start": v(-69.66, -38.84) * mm, "end": v(-69.54, -40.6) * mm});
            skLineSegment(sketch, "E9329", {"start": v(-69.54, -40.6) * mm, "end": v(-69.47, -42.4) * mm});
            skLineSegment(sketch, "E9330", {"start": v(-69.47, -42.4) * mm, "end": v(-69.44, -44.24) * mm});
            skLineSegment(sketch, "E9331", {"start": v(-69.44, -44.24) * mm, "end": v(-69.46, -46.1) * mm});
            skLineSegment(sketch, "E9332", {"start": v(-69.46, -46.1) * mm, "end": v(-69.5, -47.98) * mm});
            skLineSegment(sketch, "E9333", {"start": v(-69.5, -47.98) * mm, "end": v(-69.6, -49.85) * mm});
            skLineSegment(sketch, "E9334", {"start": v(-69.6, -49.85) * mm, "end": v(-69.7, -51.71) * mm});
            skLineSegment(sketch, "E9335", {"start": v(-69.7, -51.71) * mm, "end": v(-69.84, -53.54) * mm});
            skLineSegment(sketch, "E9336", {"start": v(-69.84, -53.54) * mm, "end": v(-70, -55.34) * mm});
            skLineSegment(sketch, "E9337", {"start": v(-70, -55.34) * mm, "end": v(-70.16, -57.08) * mm});
            skLineSegment(sketch, "E9338", {"start": v(-70.16, -57.08) * mm, "end": v(-70.35, -58.75) * mm});
            skLineSegment(sketch, "E9339", {"start": v(-70.35, -58.75) * mm, "end": v(-70.54, -60.36) * mm});
            skLineSegment(sketch, "E9340", {"start": v(-70.54, -60.36) * mm, "end": v(-70.73, -61.87) * mm});
            skLineSegment(sketch, "E9341", {"start": v(-70.73, -61.87) * mm, "end": v(-70.92, -63.28) * mm});
            skLineSegment(sketch, "E9342", {"start": v(-70.92, -63.28) * mm, "end": v(-71.11, -64.57) * mm});
            skLineSegment(sketch, "E9343", {"start": v(-71.11, -64.57) * mm, "end": v(-71.3, -65.74) * mm});
            skLineSegment(sketch, "E9344", {"start": v(-71.3, -65.74) * mm, "end": v(-71.46, -66.77) * mm});
            skLineSegment(sketch, "E9345", {"start": v(-71.46, -66.77) * mm, "end": v(-71.6, -67.65) * mm});
            skLineSegment(sketch, "E9346", {"start": v(-71.6, -67.65) * mm, "end": v(-71.74, -68.36) * mm});
            skLineSegment(sketch, "E9347", {"start": v(-71.74, -68.36) * mm, "end": v(-53.63, -68.36) * mm});
            skLineSegment(sketch, "E9348", {"start": v(-53.63, -68.36) * mm, "end": v(-53.63, 31.2) * mm});
            skLineSegment(sketch, "E9349", {"start": v(-53.63, 31.2) * mm, "end": v(-71.74, 31.2) * mm});
            skLineSegment(sketch, "E9350", {"start": v(-71.74, 31.2) * mm, "end": v(-69.93, -12.24) * mm});
            skLineSegment(sketch, "E9351", {"start": v(-69.93, -12.24) * mm, "end": v(-84.41, -12.24) * mm});
            skLineSegment(sketch, "E9352", {"start": v(-84.41, -12.24) * mm, "end": v(-82.6, 31.2) * mm});
            skLineSegment(sketch, "E9353", {"start": v(-82.6, 31.2) * mm, "end": v(-100.7, 31.2) * mm});
            skLineSegment(sketch, "E9354", {"start": v(-44.58, 31.2) * mm, "end": v(-44.29, 29.58) * mm});
            skLineSegment(sketch, "E9355", {"start": v(-44.29, 29.58) * mm, "end": v(-44, 27.93) * mm});
            skLineSegment(sketch, "E9356", {"start": v(-44, 27.93) * mm, "end": v(-43.73, 26.27) * mm});
            skLineSegment(sketch, "E9357", {"start": v(-43.73, 26.27) * mm, "end": v(-43.47, 24.58) * mm});
            skLineSegment(sketch, "E9358", {"start": v(-43.47, 24.58) * mm, "end": v(-43.22, 22.88) * mm});
            skLineSegment(sketch, "E9359", {"start": v(-43.22, 22.88) * mm, "end": v(-42.98, 21.16) * mm});
            skLineSegment(sketch, "E9360", {"start": v(-42.98, 21.16) * mm, "end": v(-42.75, 19.42) * mm});
            skLineSegment(sketch, "E9361", {"start": v(-42.75, 19.42) * mm, "end": v(-42.53, 17.67) * mm});
            skLineSegment(sketch, "E9362", {"start": v(-42.53, 17.67) * mm, "end": v(-42.33, 15.9) * mm});
            skLineSegment(sketch, "E9363", {"start": v(-42.33, 15.9) * mm, "end": v(-42.13, 14.12) * mm});
            skLineSegment(sketch, "E9364", {"start": v(-42.13, 14.12) * mm, "end": v(-41.95, 12.32) * mm});
            skLineSegment(sketch, "E9365", {"start": v(-41.95, 12.32) * mm, "end": v(-41.77, 10.52) * mm});
            skLineSegment(sketch, "E9366", {"start": v(-41.77, 10.52) * mm, "end": v(-41.6, 8.7) * mm});
            skLineSegment(sketch, "E9367", {"start": v(-41.6, 8.7) * mm, "end": v(-41.46, 6.86) * mm});
            skLineSegment(sketch, "E9368", {"start": v(-41.46, 6.86) * mm, "end": v(-41.31, 5.02) * mm});
            skLineSegment(sketch, "E9369", {"start": v(-41.31, 5.02) * mm, "end": v(-41.18, 3.17) * mm});
            skLineSegment(sketch, "E9370", {"start": v(-41.18, 3.17) * mm, "end": v(-41.06, 1.3) * mm});
            skLineSegment(sketch, "E9371", {"start": v(-41.06, 1.3) * mm, "end": v(-40.95, -0.56) * mm});
            skLineSegment(sketch, "E9372", {"start": v(-40.95, -0.56) * mm, "end": v(-40.86, -2.44) * mm});
            skLineSegment(sketch, "E9373", {"start": v(-40.86, -2.44) * mm, "end": v(-40.77, -4.32) * mm});
            skLineSegment(sketch, "E9374", {"start": v(-40.77, -4.32) * mm, "end": v(-40.7, -6.21) * mm});
            skLineSegment(sketch, "E9375", {"start": v(-40.7, -6.21) * mm, "end": v(-40.63, -8.1) * mm});
            skLineSegment(sketch, "E9376", {"start": v(-40.63, -8.1) * mm, "end": v(-40.57, -10) * mm});
            skLineSegment(sketch, "E9377", {"start": v(-40.57, -10) * mm, "end": v(-40.53, -11.9) * mm});
            skLineSegment(sketch, "E9378", {"start": v(-40.53, -11.9) * mm, "end": v(-40.5, -13.81) * mm});
            skLineSegment(sketch, "E9379", {"start": v(-40.5, -13.81) * mm, "end": v(-40.47, -15.72) * mm});
            skLineSegment(sketch, "E9380", {"start": v(-40.47, -15.72) * mm, "end": v(-40.46, -17.63) * mm});
            skLineSegment(sketch, "E9381", {"start": v(-40.46, -17.63) * mm, "end": v(-40.46, -19.53) * mm});
            skLineSegment(sketch, "E9382", {"start": v(-40.46, -19.53) * mm, "end": v(-40.47, -21.44) * mm});
            skLineSegment(sketch, "E9383", {"start": v(-40.47, -21.44) * mm, "end": v(-40.5, -23.35) * mm});
            skLineSegment(sketch, "E9384", {"start": v(-40.5, -23.35) * mm, "end": v(-40.53, -25.25) * mm});
            skLineSegment(sketch, "E9385", {"start": v(-40.53, -25.25) * mm, "end": v(-40.57, -27.16) * mm});
            skLineSegment(sketch, "E9386", {"start": v(-40.57, -27.16) * mm, "end": v(-40.63, -29.05) * mm});
            skLineSegment(sketch, "E9387", {"start": v(-40.63, -29.05) * mm, "end": v(-40.7, -30.95) * mm});
            skLineSegment(sketch, "E9388", {"start": v(-40.7, -30.95) * mm, "end": v(-40.77, -32.84) * mm});
            skLineSegment(sketch, "E9389", {"start": v(-40.77, -32.84) * mm, "end": v(-40.86, -34.72) * mm});
            skLineSegment(sketch, "E9390", {"start": v(-40.86, -34.72) * mm, "end": v(-40.95, -36.6) * mm});
            skLineSegment(sketch, "E9391", {"start": v(-40.95, -36.6) * mm, "end": v(-41.06, -38.47) * mm});
            skLineSegment(sketch, "E9392", {"start": v(-41.06, -38.47) * mm, "end": v(-41.18, -40.33) * mm});
            skLineSegment(sketch, "E9393", {"start": v(-41.18, -40.33) * mm, "end": v(-41.31, -42.18) * mm});
            skLineSegment(sketch, "E9394", {"start": v(-41.31, -42.18) * mm, "end": v(-41.46, -44.02) * mm});
            skLineSegment(sketch, "E9395", {"start": v(-41.46, -44.02) * mm, "end": v(-41.6, -45.85) * mm});
            skLineSegment(sketch, "E9396", {"start": v(-41.6, -45.85) * mm, "end": v(-41.77, -47.68) * mm});
            skLineSegment(sketch, "E9397", {"start": v(-41.77, -47.68) * mm, "end": v(-41.95, -49.48) * mm});
            skLineSegment(sketch, "E9398", {"start": v(-41.95, -49.48) * mm, "end": v(-42.13, -51.28) * mm});
            skLineSegment(sketch, "E9399", {"start": v(-42.13, -51.28) * mm, "end": v(-42.33, -53.06) * mm});
            skLineSegment(sketch, "E9400", {"start": v(-42.33, -53.06) * mm, "end": v(-42.53, -54.83) * mm});
            skLineSegment(sketch, "E9401", {"start": v(-42.53, -54.83) * mm, "end": v(-42.75, -56.58) * mm});
            skLineSegment(sketch, "E9402", {"start": v(-42.75, -56.58) * mm, "end": v(-42.98, -58.32) * mm});
            skLineSegment(sketch, "E9403", {"start": v(-42.98, -58.32) * mm, "end": v(-43.22, -60.04) * mm});
            skLineSegment(sketch, "E9404", {"start": v(-43.22, -60.04) * mm, "end": v(-43.47, -61.74) * mm});
            skLineSegment(sketch, "E9405", {"start": v(-43.47, -61.74) * mm, "end": v(-43.73, -63.43) * mm});
            skLineSegment(sketch, "E9406", {"start": v(-43.73, -63.43) * mm, "end": v(-44, -65.1) * mm});
            skLineSegment(sketch, "E9407", {"start": v(-44, -65.1) * mm, "end": v(-44.29, -66.74) * mm});
            skLineSegment(sketch, "E9408", {"start": v(-44.29, -66.74) * mm, "end": v(-44.58, -68.36) * mm});
            skLineSegment(sketch, "E9409", {"start": v(-44.58, -68.36) * mm, "end": v(-26.48, -68.36) * mm});
            skLineSegment(sketch, "E9410", {"start": v(-26.48, -68.36) * mm, "end": v(-26.48, 31.2) * mm});
            skLineSegment(sketch, "E9411", {"start": v(-26.48, 31.2) * mm, "end": v(-44.58, 31.2) * mm});
            skLineSegment(sketch, "E9412", {"start": v(-17.43, 29.4) * mm, "end": v(-17.08, 27.9) * mm});
            skLineSegment(sketch, "E9413", {"start": v(-17.08, 27.9) * mm, "end": v(-16.75, 26.36) * mm});
            skLineSegment(sketch, "E9414", {"start": v(-16.75, 26.36) * mm, "end": v(-16.43, 24.8) * mm});
            skLineSegment(sketch, "E9415", {"start": v(-16.43, 24.8) * mm, "end": v(-16.12, 23.2) * mm});
            skLineSegment(sketch, "E9416", {"start": v(-16.12, 23.2) * mm, "end": v(-15.83, 21.57) * mm});
            skLineSegment(sketch, "E9417", {"start": v(-15.83, 21.57) * mm, "end": v(-15.55, 19.9) * mm});
            skLineSegment(sketch, "E9418", {"start": v(-15.55, 19.9) * mm, "end": v(-15.28, 18.22) * mm});
            skLineSegment(sketch, "E9419", {"start": v(-15.28, 18.22) * mm, "end": v(-15.03, 16.5) * mm});
            skLineSegment(sketch, "E9420", {"start": v(-15.03, 16.5) * mm, "end": v(-14.79, 14.76) * mm});
            skLineSegment(sketch, "E9421", {"start": v(-14.79, 14.76) * mm, "end": v(-14.56, 13) * mm});
            skLineSegment(sketch, "E9422", {"start": v(-14.56, 13) * mm, "end": v(-14.34, 11.2) * mm});
            skLineSegment(sketch, "E9423", {"start": v(-14.34, 11.2) * mm, "end": v(-14.14, 9.39) * mm});
            skLineSegment(sketch, "E9424", {"start": v(-14.14, 9.39) * mm, "end": v(-13.95, 7.55) * mm});
            skLineSegment(sketch, "E9425", {"start": v(-13.95, 7.55) * mm, "end": v(-13.78, 5.7) * mm});
            skLineSegment(sketch, "E9426", {"start": v(-13.78, 5.7) * mm, "end": v(-13.61, 3.83) * mm});
            skLineSegment(sketch, "E9427", {"start": v(-13.61, 3.83) * mm, "end": v(-13.46, 1.95) * mm});
            skLineSegment(sketch, "E9428", {"start": v(-13.46, 1.95) * mm, "end": v(-13.33, 0.05) * mm});
            skLineSegment(sketch, "E9429", {"start": v(-13.33, 0.05) * mm, "end": v(-13.2, -1.87) * mm});
            skLineSegment(sketch, "E9430", {"start": v(-13.2, -1.87) * mm, "end": v(-13.1, -3.8) * mm});
            skLineSegment(sketch, "E9431", {"start": v(-13.1, -3.8) * mm, "end": v(-13, -5.73) * mm});
            skLineSegment(sketch, "E9432", {"start": v(-13, -5.73) * mm, "end": v(-12.9, -7.68) * mm});
            skLineSegment(sketch, "E9433", {"start": v(-12.9, -7.68) * mm, "end": v(-12.84, -9.63) * mm});
            skLineSegment(sketch, "E9434", {"start": v(-12.84, -9.63) * mm, "end": v(-12.78, -11.6) * mm});
            skLineSegment(sketch, "E9435", {"start": v(-12.78, -11.6) * mm, "end": v(-12.73, -13.56) * mm});
            skLineSegment(sketch, "E9436", {"start": v(-12.73, -13.56) * mm, "end": v(-12.7, -15.54) * mm});
            skLineSegment(sketch, "E9437", {"start": v(-12.7, -15.54) * mm, "end": v(-12.68, -17.5) * mm});
            skLineSegment(sketch, "E9438", {"start": v(-12.68, -17.5) * mm, "end": v(-12.67, -19.49) * mm});
            skLineSegment(sketch, "E9439", {"start": v(-12.67, -19.49) * mm, "end": v(-12.68, -21.46) * mm});
            skLineSegment(sketch, "E9440", {"start": v(-12.68, -21.46) * mm, "end": v(-12.7, -23.44) * mm});
            skLineSegment(sketch, "E9441", {"start": v(-12.7, -23.44) * mm, "end": v(-12.73, -25.4) * mm});
            skLineSegment(sketch, "E9442", {"start": v(-12.73, -25.4) * mm, "end": v(-12.78, -27.37) * mm});
            skLineSegment(sketch, "E9443", {"start": v(-12.78, -27.37) * mm, "end": v(-12.84, -29.34) * mm});
            skLineSegment(sketch, "E9444", {"start": v(-12.84, -29.34) * mm, "end": v(-12.9, -31.3) * mm});
            skLineSegment(sketch, "E9445", {"start": v(-12.9, -31.3) * mm, "end": v(-13, -33.24) * mm});
            skLineSegment(sketch, "E9446", {"start": v(-13, -33.24) * mm, "end": v(-13.1, -35.18) * mm});
            skLineSegment(sketch, "E9447", {"start": v(-13.1, -35.18) * mm, "end": v(-13.2, -37.1) * mm});
            skLineSegment(sketch, "E9448", {"start": v(-13.2, -37.1) * mm, "end": v(-13.33, -39.02) * mm});
            skLineSegment(sketch, "E9449", {"start": v(-13.33, -39.02) * mm, "end": v(-13.46, -40.92) * mm});
            skLineSegment(sketch, "E9450", {"start": v(-13.46, -40.92) * mm, "end": v(-13.61, -42.8) * mm});
            skLineSegment(sketch, "E9451", {"start": v(-13.61, -42.8) * mm, "end": v(-13.78, -44.67) * mm});
            skLineSegment(sketch, "E9452", {"start": v(-13.78, -44.67) * mm, "end": v(-13.95, -46.53) * mm});
            skLineSegment(sketch, "E9453", {"start": v(-13.95, -46.53) * mm, "end": v(-14.14, -48.36) * mm});
            skLineSegment(sketch, "E9454", {"start": v(-14.14, -48.36) * mm, "end": v(-14.34, -50.17) * mm});
            skLineSegment(sketch, "E9455", {"start": v(-14.34, -50.17) * mm, "end": v(-14.56, -51.96) * mm});
            skLineSegment(sketch, "E9456", {"start": v(-14.56, -51.96) * mm, "end": v(-14.79, -53.73) * mm});
            skLineSegment(sketch, "E9457", {"start": v(-14.79, -53.73) * mm, "end": v(-15.03, -55.47) * mm});
            skLineSegment(sketch, "E9458", {"start": v(-15.03, -55.47) * mm, "end": v(-15.28, -57.19) * mm});
            skLineSegment(sketch, "E9459", {"start": v(-15.28, -57.19) * mm, "end": v(-15.55, -58.88) * mm});
            skLineSegment(sketch, "E9460", {"start": v(-15.55, -58.88) * mm, "end": v(-15.83, -60.54) * mm});
            skLineSegment(sketch, "E9461", {"start": v(-15.83, -60.54) * mm, "end": v(-16.12, -62.17) * mm});
            skLineSegment(sketch, "E9462", {"start": v(-16.12, -62.17) * mm, "end": v(-16.43, -63.77) * mm});
            skLineSegment(sketch, "E9463", {"start": v(-16.43, -63.77) * mm, "end": v(-16.75, -65.33) * mm});
            skLineSegment(sketch, "E9464", {"start": v(-16.75, -65.33) * mm, "end": v(-17.08, -66.87) * mm});
            skLineSegment(sketch, "E9465", {"start": v(-17.08, -66.87) * mm, "end": v(-17.43, -68.36) * mm});
            skLineSegment(sketch, "E9466", {"start": v(-17.43, -68.36) * mm, "end": v(27.83, -68.36) * mm});
            skLineSegment(sketch, "E9467", {"start": v(27.83, -68.36) * mm, "end": v(29.64, -53.88) * mm});
            skLineSegment(sketch, "E9468", {"start": v(29.64, -53.88) * mm, "end": v(3.58, -52.79) * mm});
            skLineSegment(sketch, "E9469", {"start": v(3.58, -52.79) * mm, "end": v(0.68, -32.16) * mm});
            skLineSegment(sketch, "E9470", {"start": v(0.68, -32.16) * mm, "end": v(2.49, 29.4) * mm});
            skLineSegment(sketch, "E9471", {"start": v(2.49, 29.4) * mm, "end": v(-17.43, 29.4) * mm});
            skLineSegment(sketch, "E9472", {"start": v(36.88, 31.2) * mm, "end": v(36.88, -68.36) * mm});
            skLineSegment(sketch, "E9473", {"start": v(36.88, -68.36) * mm, "end": v(38.38, -68.38) * mm});
            skLineSegment(sketch, "E9474", {"start": v(38.38, -68.38) * mm, "end": v(39.92, -68.42) * mm});
            skLineSegment(sketch, "E9475", {"start": v(39.92, -68.42) * mm, "end": v(41.48, -68.5) * mm});
            skLineSegment(sketch, "E9476", {"start": v(41.48, -68.5) * mm, "end": v(43.06, -68.58) * mm});
            skLineSegment(sketch, "E9477", {"start": v(43.06, -68.58) * mm, "end": v(44.66, -68.68) * mm});
            skLineSegment(sketch, "E9478", {"start": v(44.66, -68.68) * mm, "end": v(46.27, -68.79) * mm});
            skLineSegment(sketch, "E9479", {"start": v(46.27, -68.79) * mm, "end": v(47.9, -68.9) * mm});
            skLineSegment(sketch, "E9480", {"start": v(47.9, -68.9) * mm, "end": v(49.53, -69.02) * mm});
            skLineSegment(sketch, "E9481", {"start": v(49.53, -69.02) * mm, "end": v(51.17, -69.13) * mm});
            skLineSegment(sketch, "E9482", {"start": v(51.17, -69.13) * mm, "end": v(52.8, -69.23) * mm});
            skLineSegment(sketch, "E9483", {"start": v(52.8, -69.23) * mm, "end": v(54.44, -69.32) * mm});
            skLineSegment(sketch, "E9484", {"start": v(54.44, -69.32) * mm, "end": v(56.07, -69.4) * mm});
            skLineSegment(sketch, "E9485", {"start": v(56.07, -69.4) * mm, "end": v(57.69, -69.44) * mm});
            skLineSegment(sketch, "E9486", {"start": v(57.69, -69.44) * mm, "end": v(59.3, -69.47) * mm});
            skLineSegment(sketch, "E9487", {"start": v(59.3, -69.47) * mm, "end": v(60.88, -69.46) * mm});
            skLineSegment(sketch, "E9488", {"start": v(60.88, -69.46) * mm, "end": v(62.45, -69.41) * mm});
            skLineSegment(sketch, "E9489", {"start": v(62.45, -69.41) * mm, "end": v(64, -69.33) * mm});
            skLineSegment(sketch, "E9490", {"start": v(64, -69.33) * mm, "end": v(65.5, -69.2) * mm});
            skLineSegment(sketch, "E9491", {"start": v(65.5, -69.2) * mm, "end": v(67, -69.02) * mm});
            skLineSegment(sketch, "E9492", {"start": v(67, -69.02) * mm, "end": v(68.44, -68.78) * mm});
            skLineSegment(sketch, "E9493", {"start": v(68.44, -68.78) * mm, "end": v(69.85, -68.49) * mm});
            skLineSegment(sketch, "E9494", {"start": v(69.85, -68.49) * mm, "end": v(71.22, -68.13) * mm});
            skLineSegment(sketch, "E9495", {"start": v(71.22, -68.13) * mm, "end": v(72.54, -67.7) * mm});
            skLineSegment(sketch, "E9496", {"start": v(72.54, -67.7) * mm, "end": v(73.82, -67.2) * mm});
            skLineSegment(sketch, "E9497", {"start": v(73.82, -67.2) * mm, "end": v(75.04, -66.63) * mm});
            skLineSegment(sketch, "E9498", {"start": v(75.04, -66.63) * mm, "end": v(76.2, -65.97) * mm});
            skLineSegment(sketch, "E9499", {"start": v(76.2, -65.97) * mm, "end": v(77.3, -65.23) * mm});
            skLineSegment(sketch, "E9500", {"start": v(77.3, -65.23) * mm, "end": v(78.35, -64.4) * mm});
            skLineSegment(sketch, "E9501", {"start": v(78.35, -64.4) * mm, "end": v(79.32, -63.46) * mm});
            skLineSegment(sketch, "E9502", {"start": v(79.32, -63.46) * mm, "end": v(80.22, -62.43) * mm});
            skLineSegment(sketch, "E9503", {"start": v(80.22, -62.43) * mm, "end": v(81.05, -61.3) * mm});
            skLineSegment(sketch, "E9504", {"start": v(81.05, -61.3) * mm, "end": v(81.8, -60.05) * mm});
            skLineSegment(sketch, "E9505", {"start": v(81.8, -60.05) * mm, "end": v(82.47, -58.69) * mm});
            skLineSegment(sketch, "E9506", {"start": v(82.47, -58.69) * mm, "end": v(83.05, -57.21) * mm});
            skLineSegment(sketch, "E9507", {"start": v(83.05, -57.21) * mm, "end": v(83.55, -55.61) * mm});
            skLineSegment(sketch, "E9508", {"start": v(83.55, -55.61) * mm, "end": v(83.95, -53.88) * mm});
            skLineSegment(sketch, "E9509", {"start": v(83.95, -53.88) * mm, "end": v(56.08, -52.79) * mm});
            skLineSegment(sketch, "E9510", {"start": v(56.08, -52.79) * mm, "end": v(53.17, -30.35) * mm});
            skLineSegment(sketch, "E9511", {"start": v(53.17, -30.35) * mm, "end": v(54.98, 31.2) * mm});
            skLineSegment(sketch, "E9512", {"start": v(54.98, 31.2) * mm, "end": v(36.88, 31.2) * mm});
            skLineSegment(sketch, "E9513", {"start": v(147.31, -26.07) * mm, "end": v(148.55, -26.18) * mm});
            skLineSegment(sketch, "E9514", {"start": v(148.55, -26.18) * mm, "end": v(149.66, -26.51) * mm});
            skLineSegment(sketch, "E9515", {"start": v(149.66, -26.51) * mm, "end": v(150.65, -27.05) * mm});
            skLineSegment(sketch, "E9516", {"start": v(150.65, -27.05) * mm, "end": v(151.52, -27.77) * mm});
            skLineSegment(sketch, "E9517", {"start": v(151.52, -27.77) * mm, "end": v(152.3, -28.67) * mm});
            skLineSegment(sketch, "E9518", {"start": v(152.3, -28.67) * mm, "end": v(152.96, -29.73) * mm});
            skLineSegment(sketch, "E9519", {"start": v(152.96, -29.73) * mm, "end": v(153.53, -30.95) * mm});
            skLineSegment(sketch, "E9520", {"start": v(153.53, -30.95) * mm, "end": v(154, -32.3) * mm});
            skLineSegment(sketch, "E9521", {"start": v(154, -32.3) * mm, "end": v(154.4, -33.76) * mm});
            skLineSegment(sketch, "E9522", {"start": v(154.4, -33.76) * mm, "end": v(154.71, -35.34) * mm});
            skLineSegment(sketch, "E9523", {"start": v(154.71, -35.34) * mm, "end": v(154.95, -37) * mm});
            skLineSegment(sketch, "E9524", {"start": v(154.95, -37) * mm, "end": v(155.12, -38.76) * mm});
            skLineSegment(sketch, "E9525", {"start": v(155.12, -38.76) * mm, "end": v(155.22, -40.58) * mm});
            skLineSegment(sketch, "E9526", {"start": v(155.22, -40.58) * mm, "end": v(155.27, -42.45) * mm});
            skLineSegment(sketch, "E9527", {"start": v(155.27, -42.45) * mm, "end": v(155.26, -44.35) * mm});
            skLineSegment(sketch, "E9528", {"start": v(155.26, -44.35) * mm, "end": v(155.21, -46.29) * mm});
            skLineSegment(sketch, "E9529", {"start": v(155.21, -46.29) * mm, "end": v(155.12, -48.24) * mm});
            skLineSegment(sketch, "E9530", {"start": v(155.12, -48.24) * mm, "end": v(155, -50.18) * mm});
            skLineSegment(sketch, "E9531", {"start": v(155, -50.18) * mm, "end": v(154.83, -52.1) * mm});
            skLineSegment(sketch, "E9532", {"start": v(154.83, -52.1) * mm, "end": v(154.65, -54) * mm});
            skLineSegment(sketch, "E9533", {"start": v(154.65, -54) * mm, "end": v(154.45, -55.86) * mm});
            skLineSegment(sketch, "E9534", {"start": v(154.45, -55.86) * mm, "end": v(154.24, -57.66) * mm});
            skLineSegment(sketch, "E9535", {"start": v(154.24, -57.66) * mm, "end": v(154.02, -59.4) * mm});
            skLineSegment(sketch, "E9536", {"start": v(154.02, -59.4) * mm, "end": v(153.8, -61.04) * mm});
            skLineSegment(sketch, "E9537", {"start": v(153.8, -61.04) * mm, "end": v(153.58, -62.58) * mm});
            skLineSegment(sketch, "E9538", {"start": v(153.58, -62.58) * mm, "end": v(153.37, -64.02) * mm});
            skLineSegment(sketch, "E9539", {"start": v(153.37, -64.02) * mm, "end": v(153.18, -65.33) * mm});
            skLineSegment(sketch, "E9540", {"start": v(153.18, -65.33) * mm, "end": v(153, -66.5) * mm});
            skLineSegment(sketch, "E9541", {"start": v(153, -66.5) * mm, "end": v(152.86, -67.51) * mm});
            skLineSegment(sketch, "E9542", {"start": v(152.86, -67.51) * mm, "end": v(152.74, -68.36) * mm});
            skLineSegment(sketch, "E9543", {"start": v(152.74, -68.36) * mm, "end": v(170.85, -68.36) * mm});
            skLineSegment(sketch, "E9544", {"start": v(170.85, -68.36) * mm, "end": v(170.85, 31.2) * mm});
            skLineSegment(sketch, "E9545", {"start": v(170.85, 31.2) * mm, "end": v(152.74, 31.2) * mm});
            skLineSegment(sketch, "E9546", {"start": v(152.74, 31.2) * mm, "end": v(154.55, -12.24) * mm});
            skLineSegment(sketch, "E9547", {"start": v(154.55, -12.24) * mm, "end": v(140.07, -12.24) * mm});
            skLineSegment(sketch, "E9548", {"start": v(140.07, -12.24) * mm, "end": v(141.88, 31.2) * mm});
            skLineSegment(sketch, "E9549", {"start": v(141.88, 31.2) * mm, "end": v(123.78, 31.2) * mm});
            skLineSegment(sketch, "E9550", {"start": v(123.78, 31.2) * mm, "end": v(123.78, -68.36) * mm});
            skLineSegment(sketch, "E9551", {"start": v(123.78, -68.36) * mm, "end": v(141.88, -68.36) * mm});
            skLineSegment(sketch, "E9552", {"start": v(141.88, -68.36) * mm, "end": v(141.77, -67.51) * mm});
            skLineSegment(sketch, "E9553", {"start": v(141.77, -67.51) * mm, "end": v(141.62, -66.5) * mm});
            skLineSegment(sketch, "E9554", {"start": v(141.62, -66.5) * mm, "end": v(141.45, -65.33) * mm});
            skLineSegment(sketch, "E9555", {"start": v(141.45, -65.33) * mm, "end": v(141.25, -64.02) * mm});
            skLineSegment(sketch, "E9556", {"start": v(141.25, -64.02) * mm, "end": v(141.05, -62.58) * mm});
            skLineSegment(sketch, "E9557", {"start": v(141.05, -62.58) * mm, "end": v(140.83, -61.04) * mm});
            skLineSegment(sketch, "E9558", {"start": v(140.83, -61.04) * mm, "end": v(140.6, -59.4) * mm});
            skLineSegment(sketch, "E9559", {"start": v(140.6, -59.4) * mm, "end": v(140.38, -57.66) * mm});
            skLineSegment(sketch, "E9560", {"start": v(140.38, -57.66) * mm, "end": v(140.17, -55.86) * mm});
            skLineSegment(sketch, "E9561", {"start": v(140.17, -55.86) * mm, "end": v(139.97, -54) * mm});
            skLineSegment(sketch, "E9562", {"start": v(139.97, -54) * mm, "end": v(139.8, -52.1) * mm});
            skLineSegment(sketch, "E9563", {"start": v(139.8, -52.1) * mm, "end": v(139.63, -50.18) * mm});
            skLineSegment(sketch, "E9564", {"start": v(139.63, -50.18) * mm, "end": v(139.5, -48.24) * mm});
            skLineSegment(sketch, "E9565", {"start": v(139.5, -48.24) * mm, "end": v(139.41, -46.29) * mm});
            skLineSegment(sketch, "E9566", {"start": v(139.41, -46.29) * mm, "end": v(139.36, -44.35) * mm});
            skLineSegment(sketch, "E9567", {"start": v(139.36, -44.35) * mm, "end": v(139.36, -42.45) * mm});
            skLineSegment(sketch, "E9568", {"start": v(139.36, -42.45) * mm, "end": v(139.4, -40.58) * mm});
            skLineSegment(sketch, "E9569", {"start": v(139.4, -40.58) * mm, "end": v(139.5, -38.76) * mm});
            skLineSegment(sketch, "E9570", {"start": v(139.5, -38.76) * mm, "end": v(139.68, -37) * mm});
            skLineSegment(sketch, "E9571", {"start": v(139.68, -37) * mm, "end": v(139.91, -35.34) * mm});
            skLineSegment(sketch, "E9572", {"start": v(139.91, -35.34) * mm, "end": v(140.22, -33.76) * mm});
            skLineSegment(sketch, "E9573", {"start": v(140.22, -33.76) * mm, "end": v(140.62, -32.3) * mm});
            skLineSegment(sketch, "E9574", {"start": v(140.62, -32.3) * mm, "end": v(141.1, -30.95) * mm});
            skLineSegment(sketch, "E9575", {"start": v(141.1, -30.95) * mm, "end": v(141.66, -29.73) * mm});
            skLineSegment(sketch, "E9576", {"start": v(141.66, -29.73) * mm, "end": v(142.33, -28.67) * mm});
            skLineSegment(sketch, "E9577", {"start": v(142.33, -28.67) * mm, "end": v(143.1, -27.77) * mm});
            skLineSegment(sketch, "E9578", {"start": v(143.1, -27.77) * mm, "end": v(143.97, -27.05) * mm});
            skLineSegment(sketch, "E9579", {"start": v(143.97, -27.05) * mm, "end": v(144.97, -26.51) * mm});
            skLineSegment(sketch, "E9580", {"start": v(144.97, -26.51) * mm, "end": v(146.08, -26.18) * mm});
            skLineSegment(sketch, "E9581", {"start": v(146.08, -26.18) * mm, "end": v(147.31, -26.07) * mm});
            skLineSegment(sketch, "E9582", {"start": v(179.9, 29.4) * mm, "end": v(180.29, 27.68) * mm});
            skLineSegment(sketch, "E9583", {"start": v(180.29, 27.68) * mm, "end": v(180.64, 25.95) * mm});
            skLineSegment(sketch, "E9584", {"start": v(180.64, 25.95) * mm, "end": v(180.96, 24.21) * mm});
            skLineSegment(sketch, "E9585", {"start": v(180.96, 24.21) * mm, "end": v(181.24, 22.46) * mm});
            skLineSegment(sketch, "E9586", {"start": v(181.24, 22.46) * mm, "end": v(181.5, 20.7) * mm});
            skLineSegment(sketch, "E9587", {"start": v(181.5, 20.7) * mm, "end": v(181.72, 18.92) * mm});
            skLineSegment(sketch, "E9588", {"start": v(181.72, 18.92) * mm, "end": v(181.92, 17.13) * mm});
            skLineSegment(sketch, "E9589", {"start": v(181.92, 17.13) * mm, "end": v(182.1, 15.33) * mm});
            skLineSegment(sketch, "E9590", {"start": v(182.1, 15.33) * mm, "end": v(182.24, 13.53) * mm});
            skLineSegment(sketch, "E9591", {"start": v(182.24, 13.53) * mm, "end": v(182.36, 11.71) * mm});
            skLineSegment(sketch, "E9592", {"start": v(182.36, 11.71) * mm, "end": v(182.46, 9.89) * mm});
            skLineSegment(sketch, "E9593", {"start": v(182.46, 9.89) * mm, "end": v(182.53, 8.06) * mm});
            skLineSegment(sketch, "E9594", {"start": v(182.53, 8.06) * mm, "end": v(182.59, 6.23) * mm});
            skLineSegment(sketch, "E9595", {"start": v(182.59, 6.23) * mm, "end": v(182.63, 4.39) * mm});
            skLineSegment(sketch, "E9596", {"start": v(182.63, 4.39) * mm, "end": v(182.65, 2.55) * mm});
            skLineSegment(sketch, "E9597", {"start": v(182.65, 2.55) * mm, "end": v(182.66, 0.7) * mm});
            skLineSegment(sketch, "E9598", {"start": v(182.66, 0.7) * mm, "end": v(182.65, -1.15) * mm});
            skLineSegment(sketch, "E9599", {"start": v(182.65, -1.15) * mm, "end": v(182.63, -3) * mm});
            skLineSegment(sketch, "E9600", {"start": v(182.63, -3) * mm, "end": v(182.6, -4.85) * mm});
            skLineSegment(sketch, "E9601", {"start": v(182.6, -4.85) * mm, "end": v(182.56, -6.7) * mm});
            skLineSegment(sketch, "E9602", {"start": v(182.56, -6.7) * mm, "end": v(182.5, -8.56) * mm});
            skLineSegment(sketch, "E9603", {"start": v(182.5, -8.56) * mm, "end": v(182.45, -10.41) * mm});
            skLineSegment(sketch, "E9604", {"start": v(182.45, -10.41) * mm, "end": v(182.39, -12.26) * mm});
            skLineSegment(sketch, "E9605", {"start": v(182.39, -12.26) * mm, "end": v(182.32, -14.1) * mm});
            skLineSegment(sketch, "E9606", {"start": v(182.32, -14.1) * mm, "end": v(182.25, -15.95) * mm});
            skLineSegment(sketch, "E9607", {"start": v(182.25, -15.95) * mm, "end": v(182.18, -17.79) * mm});
            skLineSegment(sketch, "E9608", {"start": v(182.18, -17.79) * mm, "end": v(182.11, -19.62) * mm});
            skLineSegment(sketch, "E9609", {"start": v(182.11, -19.62) * mm, "end": v(182.04, -21.45) * mm});
            skLineSegment(sketch, "E9610", {"start": v(182.04, -21.45) * mm, "end": v(181.97, -23.27) * mm});
            skLineSegment(sketch, "E9611", {"start": v(181.97, -23.27) * mm, "end": v(181.91, -25.09) * mm});
            skLineSegment(sketch, "E9612", {"start": v(181.91, -25.09) * mm, "end": v(181.86, -26.9) * mm});
            skLineSegment(sketch, "E9613", {"start": v(181.86, -26.9) * mm, "end": v(181.8, -28.7) * mm});
            skLineSegment(sketch, "E9614", {"start": v(181.8, -28.7) * mm, "end": v(181.77, -30.48) * mm});
            skLineSegment(sketch, "E9615", {"start": v(181.77, -30.48) * mm, "end": v(181.73, -32.26) * mm});
            skLineSegment(sketch, "E9616", {"start": v(181.73, -32.26) * mm, "end": v(181.71, -34.02) * mm});
            skLineSegment(sketch, "E9617", {"start": v(181.71, -34.02) * mm, "end": v(181.7, -35.78) * mm});
            skLineSegment(sketch, "E9618", {"start": v(181.7, -35.78) * mm, "end": v(181.68, -37.35) * mm});
            skLineSegment(sketch, "E9619", {"start": v(181.68, -37.35) * mm, "end": v(181.6, -39.02) * mm});
            skLineSegment(sketch, "E9620", {"start": v(181.6, -39.02) * mm, "end": v(181.5, -40.8) * mm});
            skLineSegment(sketch, "E9621", {"start": v(181.5, -40.8) * mm, "end": v(181.38, -42.63) * mm});
            skLineSegment(sketch, "E9622", {"start": v(181.38, -42.63) * mm, "end": v(181.26, -44.53) * mm});
            skLineSegment(sketch, "E9623", {"start": v(181.26, -44.53) * mm, "end": v(181.16, -46.46) * mm});
            skLineSegment(sketch, "E9624", {"start": v(181.16, -46.46) * mm, "end": v(181.1, -48.4) * mm});
            skLineSegment(sketch, "E9625", {"start": v(181.1, -48.4) * mm, "end": v(181.07, -50.35) * mm});
            skLineSegment(sketch, "E9626", {"start": v(181.07, -50.35) * mm, "end": v(181.1, -52.27) * mm});
            skLineSegment(sketch, "E9627", {"start": v(181.1, -52.27) * mm, "end": v(181.23, -54.15) * mm});
            skLineSegment(sketch, "E9628", {"start": v(181.23, -54.15) * mm, "end": v(181.45, -55.98) * mm});
            skLineSegment(sketch, "E9629", {"start": v(181.45, -55.98) * mm, "end": v(181.77, -57.73) * mm});
            skLineSegment(sketch, "E9630", {"start": v(181.77, -57.73) * mm, "end": v(182.22, -59.37) * mm});
            skLineSegment(sketch, "E9631", {"start": v(182.22, -59.37) * mm, "end": v(182.82, -60.9) * mm});
            skLineSegment(sketch, "E9632", {"start": v(182.82, -60.9) * mm, "end": v(183.57, -62.31) * mm});
            skLineSegment(sketch, "E9633", {"start": v(183.57, -62.31) * mm, "end": v(184.27, -63.26) * mm});
            skLineSegment(sketch, "E9634", {"start": v(184.27, -63.26) * mm, "end": v(185.13, -64.15) * mm});
            skLineSegment(sketch, "E9635", {"start": v(185.13, -64.15) * mm, "end": v(186.13, -64.96) * mm});
            skLineSegment(sketch, "E9636", {"start": v(186.13, -64.96) * mm, "end": v(187.26, -65.71) * mm});
            skLineSegment(sketch, "E9637", {"start": v(187.26, -65.71) * mm, "end": v(188.52, -66.4) * mm});
            skLineSegment(sketch, "E9638", {"start": v(188.52, -66.4) * mm, "end": v(189.89, -67.01) * mm});
            skLineSegment(sketch, "E9639", {"start": v(189.89, -67.01) * mm, "end": v(191.35, -67.56) * mm});
            skLineSegment(sketch, "E9640", {"start": v(191.35, -67.56) * mm, "end": v(192.9, -68.03) * mm});
            skLineSegment(sketch, "E9641", {"start": v(192.9, -68.03) * mm, "end": v(194.53, -68.44) * mm});
            skLineSegment(sketch, "E9642", {"start": v(194.53, -68.44) * mm, "end": v(196.22, -68.78) * mm});
            skLineSegment(sketch, "E9643", {"start": v(196.22, -68.78) * mm, "end": v(197.97, -69.06) * mm});
            skLineSegment(sketch, "E9644", {"start": v(197.97, -69.06) * mm, "end": v(199.75, -69.26) * mm});
            skLineSegment(sketch, "E9645", {"start": v(199.75, -69.26) * mm, "end": v(201.57, -69.4) * mm});
            skLineSegment(sketch, "E9646", {"start": v(201.57, -69.4) * mm, "end": v(203.4, -69.45) * mm});
            skLineSegment(sketch, "E9647", {"start": v(203.4, -69.45) * mm, "end": v(205.24, -69.45) * mm});
            skLineSegment(sketch, "E9648", {"start": v(205.24, -69.45) * mm, "end": v(207.08, -69.37) * mm});
            skLineSegment(sketch, "E9649", {"start": v(207.08, -69.37) * mm, "end": v(208.9, -69.22) * mm});
            skLineSegment(sketch, "E9650", {"start": v(208.9, -69.22) * mm, "end": v(210.7, -69) * mm});
            skLineSegment(sketch, "E9651", {"start": v(210.7, -69) * mm, "end": v(212.45, -68.71) * mm});
            skLineSegment(sketch, "E9652", {"start": v(212.45, -68.71) * mm, "end": v(214.15, -68.35) * mm});
            skLineSegment(sketch, "E9653", {"start": v(214.15, -68.35) * mm, "end": v(215.79, -67.92) * mm});
            skLineSegment(sketch, "E9654", {"start": v(215.79, -67.92) * mm, "end": v(217.36, -67.42) * mm});
            skLineSegment(sketch, "E9655", {"start": v(217.36, -67.42) * mm, "end": v(218.84, -66.84) * mm});
            skLineSegment(sketch, "E9656", {"start": v(218.84, -66.84) * mm, "end": v(220.22, -66.2) * mm});
            skLineSegment(sketch, "E9657", {"start": v(220.22, -66.2) * mm, "end": v(221.5, -65.47) * mm});
            skLineSegment(sketch, "E9658", {"start": v(221.5, -65.47) * mm, "end": v(222.66, -64.68) * mm});
            skLineSegment(sketch, "E9659", {"start": v(222.66, -64.68) * mm, "end": v(223.69, -63.82) * mm});
            skLineSegment(sketch, "E9660", {"start": v(223.69, -63.82) * mm, "end": v(224.58, -62.88) * mm});
            skLineSegment(sketch, "E9661", {"start": v(224.58, -62.88) * mm, "end": v(225.3, -61.87) * mm});
            skLineSegment(sketch, "E9662", {"start": v(225.3, -61.87) * mm, "end": v(225.87, -60.78) * mm});
            skLineSegment(sketch, "E9663", {"start": v(225.87, -60.78) * mm, "end": v(226.44, -59.25) * mm});
            skLineSegment(sketch, "E9664", {"start": v(226.44, -59.25) * mm, "end": v(226.88, -57.62) * mm});
            skLineSegment(sketch, "E9665", {"start": v(226.88, -57.62) * mm, "end": v(227.2, -55.9) * mm});
            skLineSegment(sketch, "E9666", {"start": v(227.2, -55.9) * mm, "end": v(227.43, -54.13) * mm});
            skLineSegment(sketch, "E9667", {"start": v(227.43, -54.13) * mm, "end": v(227.57, -52.3) * mm});
            skLineSegment(sketch, "E9668", {"start": v(227.57, -52.3) * mm, "end": v(227.63, -50.43) * mm});
            skLineSegment(sketch, "E9669", {"start": v(227.63, -50.43) * mm, "end": v(227.63, -48.52) * mm});
            skLineSegment(sketch, "E9670", {"start": v(227.63, -48.52) * mm, "end": v(227.58, -46.6) * mm});
            skLineSegment(sketch, "E9671", {"start": v(227.58, -46.6) * mm, "end": v(227.5, -44.7) * mm});
            skLineSegment(sketch, "E9672", {"start": v(227.5, -44.7) * mm, "end": v(227.39, -42.8) * mm});
            skLineSegment(sketch, "E9673", {"start": v(227.39, -42.8) * mm, "end": v(227.27, -40.92) * mm});
            skLineSegment(sketch, "E9674", {"start": v(227.27, -40.92) * mm, "end": v(227.16, -39.09) * mm});
            skLineSegment(sketch, "E9675", {"start": v(227.16, -39.09) * mm, "end": v(227.06, -37.3) * mm});
            skLineSegment(sketch, "E9676", {"start": v(227.06, -37.3) * mm, "end": v(227, -35.6) * mm});
            skLineSegment(sketch, "E9677", {"start": v(227, -35.6) * mm, "end": v(226.97, -33.97) * mm});
            skLineSegment(sketch, "E9678", {"start": v(226.97, -33.97) * mm, "end": v(226.96, -32.18) * mm});
            skLineSegment(sketch, "E9679", {"start": v(226.96, -32.18) * mm, "end": v(226.95, -30.39) * mm});
            skLineSegment(sketch, "E9680", {"start": v(226.95, -30.39) * mm, "end": v(226.93, -28.59) * mm});
            skLineSegment(sketch, "E9681", {"start": v(226.93, -28.59) * mm, "end": v(226.9, -26.79) * mm});
            skLineSegment(sketch, "E9682", {"start": v(226.9, -26.79) * mm, "end": v(226.87, -24.98) * mm});
            skLineSegment(sketch, "E9683", {"start": v(226.87, -24.98) * mm, "end": v(226.83, -23.17) * mm});
            skLineSegment(sketch, "E9684", {"start": v(226.83, -23.17) * mm, "end": v(226.79, -21.35) * mm});
            skLineSegment(sketch, "E9685", {"start": v(226.79, -21.35) * mm, "end": v(226.74, -19.54) * mm});
            skLineSegment(sketch, "E9686", {"start": v(226.74, -19.54) * mm, "end": v(226.7, -17.72) * mm});
            skLineSegment(sketch, "E9687", {"start": v(226.7, -17.72) * mm, "end": v(226.65, -15.9) * mm});
            skLineSegment(sketch, "E9688", {"start": v(226.65, -15.9) * mm, "end": v(226.6, -14.07) * mm});
            skLineSegment(sketch, "E9689", {"start": v(226.6, -14.07) * mm, "end": v(226.56, -12.24) * mm});
            skLineSegment(sketch, "E9690", {"start": v(226.56, -12.24) * mm, "end": v(226.52, -10.41) * mm});
            skLineSegment(sketch, "E9691", {"start": v(226.52, -10.41) * mm, "end": v(226.49, -8.59) * mm});
            skLineSegment(sketch, "E9692", {"start": v(226.49, -8.59) * mm, "end": v(226.46, -6.76) * mm});
            skLineSegment(sketch, "E9693", {"start": v(226.46, -6.76) * mm, "end": v(226.43, -4.93) * mm});
            skLineSegment(sketch, "E9694", {"start": v(226.43, -4.93) * mm, "end": v(226.41, -3.1) * mm});
            skLineSegment(sketch, "E9695", {"start": v(226.41, -3.1) * mm, "end": v(226.4, -1.27) * mm});
            skLineSegment(sketch, "E9696", {"start": v(226.4, -1.27) * mm, "end": v(226.4, 0.56) * mm});
            skLineSegment(sketch, "E9697", {"start": v(226.4, 0.56) * mm, "end": v(226.4, 2.4) * mm});
            skLineSegment(sketch, "E9698", {"start": v(226.4, 2.4) * mm, "end": v(226.43, 4.22) * mm});
            skLineSegment(sketch, "E9699", {"start": v(226.43, 4.22) * mm, "end": v(226.46, 6.04) * mm});
            skLineSegment(sketch, "E9700", {"start": v(226.46, 6.04) * mm, "end": v(226.5, 7.86) * mm});
            skLineSegment(sketch, "E9701", {"start": v(226.5, 7.86) * mm, "end": v(226.56, 9.68) * mm});
            skLineSegment(sketch, "E9702", {"start": v(226.56, 9.68) * mm, "end": v(226.64, 11.5) * mm});
            skLineSegment(sketch, "E9703", {"start": v(226.64, 11.5) * mm, "end": v(226.73, 13.31) * mm});
            skLineSegment(sketch, "E9704", {"start": v(226.73, 13.31) * mm, "end": v(226.84, 15.12) * mm});
            skLineSegment(sketch, "E9705", {"start": v(226.84, 15.12) * mm, "end": v(226.97, 16.93) * mm});
            skLineSegment(sketch, "E9706", {"start": v(226.97, 16.93) * mm, "end": v(227.11, 18.73) * mm});
            skLineSegment(sketch, "E9707", {"start": v(227.11, 18.73) * mm, "end": v(227.28, 20.53) * mm});
            skLineSegment(sketch, "E9708", {"start": v(227.28, 20.53) * mm, "end": v(227.47, 22.32) * mm});
            skLineSegment(sketch, "E9709", {"start": v(227.47, 22.32) * mm, "end": v(227.68, 24.11) * mm});
            skLineSegment(sketch, "E9710", {"start": v(227.68, 24.11) * mm, "end": v(227.92, 25.9) * mm});
            skLineSegment(sketch, "E9711", {"start": v(227.92, 25.9) * mm, "end": v(228.18, 27.67) * mm});
            skLineSegment(sketch, "E9712", {"start": v(228.18, 27.67) * mm, "end": v(228.46, 29.44) * mm});
            skLineSegment(sketch, "E9713", {"start": v(228.46, 29.44) * mm, "end": v(228.78, 31.2) * mm});
            skLineSegment(sketch, "E9714", {"start": v(228.78, 31.2) * mm, "end": v(210.67, 31.2) * mm});
            skLineSegment(sketch, "E9715", {"start": v(210.67, 31.2) * mm, "end": v(210.67, -32.16) * mm});
            skLineSegment(sketch, "E9716", {"start": v(210.67, -32.16) * mm, "end": v(210.68, -33.9) * mm});
            skLineSegment(sketch, "E9717", {"start": v(210.68, -33.9) * mm, "end": v(210.7, -35.63) * mm});
            skLineSegment(sketch, "E9718", {"start": v(210.7, -35.63) * mm, "end": v(210.72, -37.32) * mm});
            skLineSegment(sketch, "E9719", {"start": v(210.72, -37.32) * mm, "end": v(210.72, -38.99) * mm});
            skLineSegment(sketch, "E9720", {"start": v(210.72, -38.99) * mm, "end": v(210.7, -40.6) * mm});
            skLineSegment(sketch, "E9721", {"start": v(210.7, -40.6) * mm, "end": v(210.63, -42.19) * mm});
            skLineSegment(sketch, "E9722", {"start": v(210.63, -42.19) * mm, "end": v(210.5, -43.71) * mm});
            skLineSegment(sketch, "E9723", {"start": v(210.5, -43.71) * mm, "end": v(210.32, -45.17) * mm});
            skLineSegment(sketch, "E9724", {"start": v(210.32, -45.17) * mm, "end": v(210.05, -46.57) * mm});
            skLineSegment(sketch, "E9725", {"start": v(210.05, -46.57) * mm, "end": v(209.69, -47.9) * mm});
            skLineSegment(sketch, "E9726", {"start": v(209.69, -47.9) * mm, "end": v(209.21, -49.14) * mm});
            skLineSegment(sketch, "E9727", {"start": v(209.21, -49.14) * mm, "end": v(208.62, -50.3) * mm});
            skLineSegment(sketch, "E9728", {"start": v(208.62, -50.3) * mm, "end": v(207.9, -51.37) * mm});
            skLineSegment(sketch, "E9729", {"start": v(207.9, -51.37) * mm, "end": v(207.03, -52.34) * mm});
            skLineSegment(sketch, "E9730", {"start": v(207.03, -52.34) * mm, "end": v(206, -53.2) * mm});
            skLineSegment(sketch, "E9731", {"start": v(206, -53.2) * mm, "end": v(204.8, -53.95) * mm});
            skLineSegment(sketch, "E9732", {"start": v(204.8, -53.95) * mm, "end": v(203.4, -54.58) * mm});
            skLineSegment(sketch, "E9733", {"start": v(203.4, -54.58) * mm, "end": v(201.82, -55.08) * mm});
            skLineSegment(sketch, "E9734", {"start": v(201.82, -55.08) * mm, "end": v(200.02, -55.46) * mm});
            skLineSegment(sketch, "E9735", {"start": v(200.02, -55.46) * mm, "end": v(198, -55.7) * mm});
            skLineSegment(sketch, "E9736", {"start": v(198, -55.7) * mm, "end": v(198, 31.2) * mm});
            skLineSegment(sketch, "E9737", {"start": v(198, 31.2) * mm, "end": v(179.9, 29.4) * mm});
            skLineSegment(sketch, "E9738", {"start": v(266.8, -24.92) * mm, "end": v(266.8, -55.7) * mm});
            skLineSegment(sketch, "E9739", {"start": v(266.8, -55.7) * mm, "end": v(264.7, -55.47) * mm});
            skLineSegment(sketch, "E9740", {"start": v(264.7, -55.47) * mm, "end": v(262.83, -55.15) * mm});
            skLineSegment(sketch, "E9741", {"start": v(262.83, -55.15) * mm, "end": v(261.18, -54.7) * mm});
            skLineSegment(sketch, "E9742", {"start": v(261.18, -54.7) * mm, "end": v(259.74, -54.1) * mm});
            skLineSegment(sketch, "E9743", {"start": v(259.74, -54.1) * mm, "end": v(258.52, -53.37) * mm});
            skLineSegment(sketch, "E9744", {"start": v(258.52, -53.37) * mm, "end": v(257.5, -52.48) * mm});
            skLineSegment(sketch, "E9745", {"start": v(257.5, -52.48) * mm, "end": v(256.71, -51.4) * mm});
            skLineSegment(sketch, "E9746", {"start": v(256.71, -51.4) * mm, "end": v(256.13, -50.16) * mm});
            skLineSegment(sketch, "E9747", {"start": v(256.13, -50.16) * mm, "end": v(255.77, -48.7) * mm});
            skLineSegment(sketch, "E9748", {"start": v(255.77, -48.7) * mm, "end": v(255.61, -47.04) * mm});
            skLineSegment(sketch, "E9749", {"start": v(255.61, -47.04) * mm, "end": v(255.67, -45.15) * mm});
            skLineSegment(sketch, "E9750", {"start": v(255.67, -45.15) * mm, "end": v(255.93, -43.02) * mm});
            skLineSegment(sketch, "E9751", {"start": v(255.93, -43.02) * mm, "end": v(236.02, -43.02) * mm});
            skLineSegment(sketch, "E9752", {"start": v(236.02, -43.02) * mm, "end": v(236.27, -44.63) * mm});
            skLineSegment(sketch, "E9753", {"start": v(236.27, -44.63) * mm, "end": v(236.46, -46.35) * mm});
            skLineSegment(sketch, "E9754", {"start": v(236.46, -46.35) * mm, "end": v(236.63, -48.17) * mm});
            skLineSegment(sketch, "E9755", {"start": v(236.63, -48.17) * mm, "end": v(236.8, -50.04) * mm});
            skLineSegment(sketch, "E9756", {"start": v(236.8, -50.04) * mm, "end": v(236.97, -51.94) * mm});
            skLineSegment(sketch, "E9757", {"start": v(236.97, -51.94) * mm, "end": v(237.2, -53.85) * mm});
            skLineSegment(sketch, "E9758", {"start": v(237.2, -53.85) * mm, "end": v(237.48, -55.73) * mm});
            skLineSegment(sketch, "E9759", {"start": v(237.48, -55.73) * mm, "end": v(237.85, -57.55) * mm});
            skLineSegment(sketch, "E9760", {"start": v(237.85, -57.55) * mm, "end": v(238.34, -59.3) * mm});
            skLineSegment(sketch, "E9761", {"start": v(238.34, -59.3) * mm, "end": v(238.97, -60.92) * mm});
            skLineSegment(sketch, "E9762", {"start": v(238.97, -60.92) * mm, "end": v(239.76, -62.4) * mm});
            skLineSegment(sketch, "E9763", {"start": v(239.76, -62.4) * mm, "end": v(240.73, -63.7) * mm});
            skLineSegment(sketch, "E9764", {"start": v(240.73, -63.7) * mm, "end": v(241.62, -64.58) * mm});
            skLineSegment(sketch, "E9765", {"start": v(241.62, -64.58) * mm, "end": v(242.69, -65.38) * mm});
            skLineSegment(sketch, "E9766", {"start": v(242.69, -65.38) * mm, "end": v(243.91, -66.1) * mm});
            skLineSegment(sketch, "E9767", {"start": v(243.91, -66.1) * mm, "end": v(245.27, -66.76) * mm});
            skLineSegment(sketch, "E9768", {"start": v(245.27, -66.76) * mm, "end": v(246.76, -67.34) * mm});
            skLineSegment(sketch, "E9769", {"start": v(246.76, -67.34) * mm, "end": v(248.36, -67.85) * mm});
            skLineSegment(sketch, "E9770", {"start": v(248.36, -67.85) * mm, "end": v(250.06, -68.28) * mm});
            skLineSegment(sketch, "E9771", {"start": v(250.06, -68.28) * mm, "end": v(251.84, -68.64) * mm});
            skLineSegment(sketch, "E9772", {"start": v(251.84, -68.64) * mm, "end": v(253.68, -68.93) * mm});
            skLineSegment(sketch, "E9773", {"start": v(253.68, -68.93) * mm, "end": v(255.58, -69.15) * mm});
            skLineSegment(sketch, "E9774", {"start": v(255.58, -69.15) * mm, "end": v(257.52, -69.3) * mm});
            skLineSegment(sketch, "E9775", {"start": v(257.52, -69.3) * mm, "end": v(259.47, -69.37) * mm});
            skLineSegment(sketch, "E9776", {"start": v(259.47, -69.37) * mm, "end": v(261.44, -69.37) * mm});
            skLineSegment(sketch, "E9777", {"start": v(261.44, -69.37) * mm, "end": v(263.4, -69.3) * mm});
            skLineSegment(sketch, "E9778", {"start": v(263.4, -69.3) * mm, "end": v(265.33, -69.15) * mm});
            skLineSegment(sketch, "E9779", {"start": v(265.33, -69.15) * mm, "end": v(267.23, -68.93) * mm});
            skLineSegment(sketch, "E9780", {"start": v(267.23, -68.93) * mm, "end": v(269.08, -68.64) * mm});
            skLineSegment(sketch, "E9781", {"start": v(269.08, -68.64) * mm, "end": v(270.85, -68.28) * mm});
            skLineSegment(sketch, "E9782", {"start": v(270.85, -68.28) * mm, "end": v(272.55, -67.85) * mm});
            skLineSegment(sketch, "E9783", {"start": v(272.55, -67.85) * mm, "end": v(274.15, -67.34) * mm});
            skLineSegment(sketch, "E9784", {"start": v(274.15, -67.34) * mm, "end": v(275.64, -66.76) * mm});
            skLineSegment(sketch, "E9785", {"start": v(275.64, -66.76) * mm, "end": v(277, -66.1) * mm});
            skLineSegment(sketch, "E9786", {"start": v(277, -66.1) * mm, "end": v(278.22, -65.38) * mm});
            skLineSegment(sketch, "E9787", {"start": v(278.22, -65.38) * mm, "end": v(279.29, -64.58) * mm});
            skLineSegment(sketch, "E9788", {"start": v(279.29, -64.58) * mm, "end": v(280.18, -63.7) * mm});
            skLineSegment(sketch, "E9789", {"start": v(280.18, -63.7) * mm, "end": v(280.8, -62.88) * mm});
            skLineSegment(sketch, "E9790", {"start": v(280.8, -62.88) * mm, "end": v(281.38, -61.87) * mm});
            skLineSegment(sketch, "E9791", {"start": v(281.38, -61.87) * mm, "end": v(281.9, -60.68) * mm});
            skLineSegment(sketch, "E9792", {"start": v(281.9, -60.68) * mm, "end": v(282.38, -59.33) * mm});
            skLineSegment(sketch, "E9793", {"start": v(282.38, -59.33) * mm, "end": v(282.82, -57.84) * mm});
            skLineSegment(sketch, "E9794", {"start": v(282.82, -57.84) * mm, "end": v(283.2, -56.22) * mm});
            skLineSegment(sketch, "E9795", {"start": v(283.2, -56.22) * mm, "end": v(283.55, -54.47) * mm});
            skLineSegment(sketch, "E9796", {"start": v(283.55, -54.47) * mm, "end": v(283.84, -52.63) * mm});
            skLineSegment(sketch, "E9797", {"start": v(283.84, -52.63) * mm, "end": v(284.09, -50.7) * mm});
            skLineSegment(sketch, "E9798", {"start": v(284.09, -50.7) * mm, "end": v(284.29, -48.68) * mm});
            skLineSegment(sketch, "E9799", {"start": v(284.29, -48.68) * mm, "end": v(284.44, -46.61) * mm});
            skLineSegment(sketch, "E9800", {"start": v(284.44, -46.61) * mm, "end": v(284.54, -44.5) * mm});
            skLineSegment(sketch, "E9801", {"start": v(284.54, -44.5) * mm, "end": v(284.6, -42.35) * mm});
            skLineSegment(sketch, "E9802", {"start": v(284.6, -42.35) * mm, "end": v(284.6, -40.18) * mm});
            skLineSegment(sketch, "E9803", {"start": v(284.6, -40.18) * mm, "end": v(284.57, -38.01) * mm});
            skLineSegment(sketch, "E9804", {"start": v(284.57, -38.01) * mm, "end": v(284.48, -35.85) * mm});
            skLineSegment(sketch, "E9805", {"start": v(284.48, -35.85) * mm, "end": v(284.35, -33.71) * mm});
            skLineSegment(sketch, "E9806", {"start": v(284.35, -33.71) * mm, "end": v(284.16, -31.62) * mm});
            skLineSegment(sketch, "E9807", {"start": v(284.16, -31.62) * mm, "end": v(283.93, -29.57) * mm});
            skLineSegment(sketch, "E9808", {"start": v(283.93, -29.57) * mm, "end": v(283.65, -27.6) * mm});
            skLineSegment(sketch, "E9809", {"start": v(283.65, -27.6) * mm, "end": v(283.32, -25.7) * mm});
            skLineSegment(sketch, "E9810", {"start": v(283.32, -25.7) * mm, "end": v(282.94, -23.9) * mm});
            skLineSegment(sketch, "E9811", {"start": v(282.94, -23.9) * mm, "end": v(282.5, -22.2) * mm});
            skLineSegment(sketch, "E9812", {"start": v(282.5, -22.2) * mm, "end": v(282.03, -20.63) * mm});
            skLineSegment(sketch, "E9813", {"start": v(282.03, -20.63) * mm, "end": v(281.5, -19.2) * mm});
            skLineSegment(sketch, "E9814", {"start": v(281.5, -19.2) * mm, "end": v(280.92, -17.93) * mm});
            skLineSegment(sketch, "E9815", {"start": v(280.92, -17.93) * mm, "end": v(280.3, -16.81) * mm});
            skLineSegment(sketch, "E9816", {"start": v(280.3, -16.81) * mm, "end": v(279.62, -15.88) * mm});
            skLineSegment(sketch, "E9817", {"start": v(279.62, -15.88) * mm, "end": v(278.89, -15.15) * mm});
            skLineSegment(sketch, "E9818", {"start": v(278.89, -15.15) * mm, "end": v(277.53, -14.18) * mm});
            skLineSegment(sketch, "E9819", {"start": v(277.53, -14.18) * mm, "end": v(276.02, -13.4) * mm});
            skLineSegment(sketch, "E9820", {"start": v(276.02, -13.4) * mm, "end": v(274.38, -12.8) * mm});
            skLineSegment(sketch, "E9821", {"start": v(274.38, -12.8) * mm, "end": v(272.64, -12.37) * mm});
            skLineSegment(sketch, "E9822", {"start": v(272.64, -12.37) * mm, "end": v(270.81, -12.07) * mm});
            skLineSegment(sketch, "E9823", {"start": v(270.81, -12.07) * mm, "end": v(268.92, -11.9) * mm});
            skLineSegment(sketch, "E9824", {"start": v(268.92, -11.9) * mm, "end": v(267, -11.8) * mm});
            skLineSegment(sketch, "E9825", {"start": v(267, -11.8) * mm, "end": v(265.04, -11.8) * mm});
            skLineSegment(sketch, "E9826", {"start": v(265.04, -11.8) * mm, "end": v(263.1, -11.85) * mm});
            skLineSegment(sketch, "E9827", {"start": v(263.1, -11.85) * mm, "end": v(261.17, -11.94) * mm});
            skLineSegment(sketch, "E9828", {"start": v(261.17, -11.94) * mm, "end": v(259.28, -12.04) * mm});
            skLineSegment(sketch, "E9829", {"start": v(259.28, -12.04) * mm, "end": v(257.47, -12.14) * mm});
            skLineSegment(sketch, "E9830", {"start": v(257.47, -12.14) * mm, "end": v(255.74, -12.21) * mm});
            skLineSegment(sketch, "E9831", {"start": v(255.74, -12.21) * mm, "end": v(254.12, -12.24) * mm});
            skLineSegment(sketch, "E9832", {"start": v(254.12, -12.24) * mm, "end": v(254.12, 16.72) * mm});
            skLineSegment(sketch, "E9833", {"start": v(254.12, 16.72) * mm, "end": v(266.8, 16.72) * mm});
            skLineSegment(sketch, "E9834", {"start": v(266.8, 16.72) * mm, "end": v(266.8, 5.86) * mm});
            skLineSegment(sketch, "E9835", {"start": v(266.8, 5.86) * mm, "end": v(284.9, 5.86) * mm});
            skLineSegment(sketch, "E9836", {"start": v(284.9, 5.86) * mm, "end": v(284.65, 7.47) * mm});
            skLineSegment(sketch, "E9837", {"start": v(284.65, 7.47) * mm, "end": v(284.45, 9.2) * mm});
            skLineSegment(sketch, "E9838", {"start": v(284.45, 9.2) * mm, "end": v(284.28, 11) * mm});
            skLineSegment(sketch, "E9839", {"start": v(284.28, 11) * mm, "end": v(284.12, 12.88) * mm});
            skLineSegment(sketch, "E9840", {"start": v(284.12, 12.88) * mm, "end": v(283.94, 14.78) * mm});
            skLineSegment(sketch, "E9841", {"start": v(283.94, 14.78) * mm, "end": v(283.72, 16.7) * mm});
            skLineSegment(sketch, "E9842", {"start": v(283.72, 16.7) * mm, "end": v(283.44, 18.57) * mm});
            skLineSegment(sketch, "E9843", {"start": v(283.44, 18.57) * mm, "end": v(283.06, 20.4) * mm});
            skLineSegment(sketch, "E9844", {"start": v(283.06, 20.4) * mm, "end": v(282.57, 22.13) * mm});
            skLineSegment(sketch, "E9845", {"start": v(282.57, 22.13) * mm, "end": v(281.95, 23.76) * mm});
            skLineSegment(sketch, "E9846", {"start": v(281.95, 23.76) * mm, "end": v(281.16, 25.24) * mm});
            skLineSegment(sketch, "E9847", {"start": v(281.16, 25.24) * mm, "end": v(280.18, 26.55) * mm});
            skLineSegment(sketch, "E9848", {"start": v(280.18, 26.55) * mm, "end": v(279.26, 27.44) * mm});
            skLineSegment(sketch, "E9849", {"start": v(279.26, 27.44) * mm, "end": v(278.17, 28.26) * mm});
            skLineSegment(sketch, "E9850", {"start": v(278.17, 28.26) * mm, "end": v(276.92, 29) * mm});
            skLineSegment(sketch, "E9851", {"start": v(276.92, 29) * mm, "end": v(275.53, 29.66) * mm});
            skLineSegment(sketch, "E9852", {"start": v(275.53, 29.66) * mm, "end": v(274.02, 30.24) * mm});
            skLineSegment(sketch, "E9853", {"start": v(274.02, 30.24) * mm, "end": v(272.4, 30.75) * mm});
            skLineSegment(sketch, "E9854", {"start": v(272.4, 30.75) * mm, "end": v(270.68, 31.18) * mm});
            skLineSegment(sketch, "E9855", {"start": v(270.68, 31.18) * mm, "end": v(268.88, 31.53) * mm});
            skLineSegment(sketch, "E9856", {"start": v(268.88, 31.53) * mm, "end": v(267.02, 31.8) * mm});
            skLineSegment(sketch, "E9857", {"start": v(267.02, 31.8) * mm, "end": v(265.1, 32) * mm});
            skLineSegment(sketch, "E9858", {"start": v(265.1, 32) * mm, "end": v(263.17, 32.13) * mm});
            skLineSegment(sketch, "E9859", {"start": v(263.17, 32.13) * mm, "end": v(261.2, 32.18) * mm});
            skLineSegment(sketch, "E9860", {"start": v(261.2, 32.18) * mm, "end": v(259.25, 32.15) * mm});
            skLineSegment(sketch, "E9861", {"start": v(259.25, 32.15) * mm, "end": v(257.3, 32.05) * mm});
            skLineSegment(sketch, "E9862", {"start": v(257.3, 32.05) * mm, "end": v(255.39, 31.87) * mm});
            skLineSegment(sketch, "E9863", {"start": v(255.39, 31.87) * mm, "end": v(253.52, 31.63) * mm});
            skLineSegment(sketch, "E9864", {"start": v(253.52, 31.63) * mm, "end": v(251.7, 31.3) * mm});
            skLineSegment(sketch, "E9865", {"start": v(251.7, 31.3) * mm, "end": v(249.97, 30.9) * mm});
            skLineSegment(sketch, "E9866", {"start": v(249.97, 30.9) * mm, "end": v(248.33, 30.44) * mm});
            skLineSegment(sketch, "E9867", {"start": v(248.33, 30.44) * mm, "end": v(246.8, 29.9) * mm});
            skLineSegment(sketch, "E9868", {"start": v(246.8, 29.9) * mm, "end": v(245.38, 29.28) * mm});
            skLineSegment(sketch, "E9869", {"start": v(245.38, 29.28) * mm, "end": v(244.1, 28.6) * mm});
            skLineSegment(sketch, "E9870", {"start": v(244.1, 28.6) * mm, "end": v(242.98, 27.84) * mm});
            skLineSegment(sketch, "E9871", {"start": v(242.98, 27.84) * mm, "end": v(242.02, 27) * mm});
            skLineSegment(sketch, "E9872", {"start": v(242.02, 27) * mm, "end": v(241.33, 26.2) * mm});
            skLineSegment(sketch, "E9873", {"start": v(241.33, 26.2) * mm, "end": v(240.68, 25.22) * mm});
            skLineSegment(sketch, "E9874", {"start": v(240.68, 25.22) * mm, "end": v(240.08, 24.08) * mm});
            skLineSegment(sketch, "E9875", {"start": v(240.08, 24.08) * mm, "end": v(239.51, 22.8) * mm});
            skLineSegment(sketch, "E9876", {"start": v(239.51, 22.8) * mm, "end": v(239, 21.37) * mm});
            skLineSegment(sketch, "E9877", {"start": v(239, 21.37) * mm, "end": v(238.52, 19.82) * mm});
            skLineSegment(sketch, "E9878", {"start": v(238.52, 19.82) * mm, "end": v(238.1, 18.15) * mm});
            skLineSegment(sketch, "E9879", {"start": v(238.1, 18.15) * mm, "end": v(237.7, 16.4) * mm});
            skLineSegment(sketch, "E9880", {"start": v(237.7, 16.4) * mm, "end": v(237.37, 14.54) * mm});
            skLineSegment(sketch, "E9881", {"start": v(237.37, 14.54) * mm, "end": v(237.08, 12.62) * mm});
            skLineSegment(sketch, "E9882", {"start": v(237.08, 12.62) * mm, "end": v(236.84, 10.64) * mm});
            skLineSegment(sketch, "E9883", {"start": v(236.84, 10.64) * mm, "end": v(236.65, 8.6) * mm});
            skLineSegment(sketch, "E9884", {"start": v(236.65, 8.6) * mm, "end": v(236.5, 6.54) * mm});
            skLineSegment(sketch, "E9885", {"start": v(236.5, 6.54) * mm, "end": v(236.4, 4.45) * mm});
            skLineSegment(sketch, "E9886", {"start": v(236.4, 4.45) * mm, "end": v(236.36, 2.34) * mm});
            skLineSegment(sketch, "E9887", {"start": v(236.36, 2.34) * mm, "end": v(236.36, 0.24) * mm});
            skLineSegment(sketch, "E9888", {"start": v(236.36, 0.24) * mm, "end": v(236.42, -1.85) * mm});
            skLineSegment(sketch, "E9889", {"start": v(236.42, -1.85) * mm, "end": v(236.52, -3.9) * mm});
            skLineSegment(sketch, "E9890", {"start": v(236.52, -3.9) * mm, "end": v(236.68, -5.93) * mm});
            skLineSegment(sketch, "E9891", {"start": v(236.68, -5.93) * mm, "end": v(236.9, -7.9) * mm});
            skLineSegment(sketch, "E9892", {"start": v(236.9, -7.9) * mm, "end": v(237.16, -9.8) * mm});
            skLineSegment(sketch, "E9893", {"start": v(237.16, -9.8) * mm, "end": v(237.48, -11.64) * mm});
            skLineSegment(sketch, "E9894", {"start": v(237.48, -11.64) * mm, "end": v(237.85, -13.38) * mm});
            skLineSegment(sketch, "E9895", {"start": v(237.85, -13.38) * mm, "end": v(238.28, -15.02) * mm});
            skLineSegment(sketch, "E9896", {"start": v(238.28, -15.02) * mm, "end": v(238.76, -16.54) * mm});
            skLineSegment(sketch, "E9897", {"start": v(238.76, -16.54) * mm, "end": v(239.3, -17.94) * mm});
            skLineSegment(sketch, "E9898", {"start": v(239.3, -17.94) * mm, "end": v(239.9, -19.2) * mm});
            skLineSegment(sketch, "E9899", {"start": v(239.9, -19.2) * mm, "end": v(240.55, -20.3) * mm});
            skLineSegment(sketch, "E9900", {"start": v(240.55, -20.3) * mm, "end": v(241.26, -21.25) * mm});
            skLineSegment(sketch, "E9901", {"start": v(241.26, -21.25) * mm, "end": v(242.02, -22.01) * mm});
            skLineSegment(sketch, "E9902", {"start": v(242.02, -22.01) * mm, "end": v(243.38, -22.99) * mm});
            skLineSegment(sketch, "E9903", {"start": v(243.38, -22.99) * mm, "end": v(244.9, -23.76) * mm});
            skLineSegment(sketch, "E9904", {"start": v(244.9, -23.76) * mm, "end": v(246.53, -24.35) * mm});
            skLineSegment(sketch, "E9905", {"start": v(246.53, -24.35) * mm, "end": v(248.27, -24.79) * mm});
            skLineSegment(sketch, "E9906", {"start": v(248.27, -24.79) * mm, "end": v(250.1, -25.09) * mm});
            skLineSegment(sketch, "E9907", {"start": v(250.1, -25.09) * mm, "end": v(251.99, -25.27) * mm});
            skLineSegment(sketch, "E9908", {"start": v(251.99, -25.27) * mm, "end": v(253.92, -25.35) * mm});
            skLineSegment(sketch, "E9909", {"start": v(253.92, -25.35) * mm, "end": v(255.87, -25.36) * mm});
            skLineSegment(sketch, "E9910", {"start": v(255.87, -25.36) * mm, "end": v(257.82, -25.3) * mm});
            skLineSegment(sketch, "E9911", {"start": v(257.82, -25.3) * mm, "end": v(259.75, -25.22) * mm});
            skLineSegment(sketch, "E9912", {"start": v(259.75, -25.22) * mm, "end": v(261.63, -25.12) * mm});
            skLineSegment(sketch, "E9913", {"start": v(261.63, -25.12) * mm, "end": v(263.45, -25.02) * mm});
            skLineSegment(sketch, "E9914", {"start": v(263.45, -25.02) * mm, "end": v(265.17, -24.95) * mm});
            skLineSegment(sketch, "E9915", {"start": v(265.17, -24.95) * mm, "end": v(266.8, -24.92) * mm});
            skLineSegment(sketch, "E9916", {"start": v(290.33, 16.72) * mm, "end": v(308.43, 16.72) * mm});
            skLineSegment(sketch, "E9917", {"start": v(308.43, 16.72) * mm, "end": v(306.62, -68.36) * mm});
            skLineSegment(sketch, "E9918", {"start": v(306.62, -68.36) * mm, "end": v(326.53, -68.36) * mm});
            skLineSegment(sketch, "E9919", {"start": v(326.53, -68.36) * mm, "end": v(324.72, 16.72) * mm});
            skLineSegment(sketch, "E9920", {"start": v(324.72, 16.72) * mm, "end": v(342.83, 16.72) * mm});
            skLineSegment(sketch, "E9921", {"start": v(342.83, 16.72) * mm, "end": v(341.02, 31.2) * mm});
            skLineSegment(sketch, "E9922", {"start": v(341.02, 31.2) * mm, "end": v(339.7, 31.22) * mm});
            skLineSegment(sketch, "E9923", {"start": v(339.7, 31.22) * mm, "end": v(338.32, 31.26) * mm});
            skLineSegment(sketch, "E9924", {"start": v(338.32, 31.26) * mm, "end": v(336.9, 31.32) * mm});
            skLineSegment(sketch, "E9925", {"start": v(336.9, 31.32) * mm, "end": v(335.42, 31.4) * mm});
            skLineSegment(sketch, "E9926", {"start": v(335.42, 31.4) * mm, "end": v(333.9, 31.5) * mm});
            skLineSegment(sketch, "E9927", {"start": v(333.9, 31.5) * mm, "end": v(332.35, 31.62) * mm});
            skLineSegment(sketch, "E9928", {"start": v(332.35, 31.62) * mm, "end": v(330.77, 31.74) * mm});
            skLineSegment(sketch, "E9929", {"start": v(330.77, 31.74) * mm, "end": v(329.16, 31.86) * mm});
            skLineSegment(sketch, "E9930", {"start": v(329.16, 31.86) * mm, "end": v(327.53, 31.98) * mm});
            skLineSegment(sketch, "E9931", {"start": v(327.53, 31.98) * mm, "end": v(325.88, 32.1) * mm});
            skLineSegment(sketch, "E9932", {"start": v(325.88, 32.1) * mm, "end": v(324.2, 32.21) * mm});
            skLineSegment(sketch, "E9933", {"start": v(324.2, 32.21) * mm, "end": v(322.53, 32.3) * mm});
            skLineSegment(sketch, "E9934", {"start": v(322.53, 32.3) * mm, "end": v(320.85, 32.4) * mm});
            skLineSegment(sketch, "E9935", {"start": v(320.85, 32.4) * mm, "end": v(319.17, 32.46) * mm});
            skLineSegment(sketch, "E9936", {"start": v(319.17, 32.46) * mm, "end": v(317.5, 32.5) * mm});
            skLineSegment(sketch, "E9937", {"start": v(317.5, 32.5) * mm, "end": v(315.83, 32.52) * mm});
            skLineSegment(sketch, "E9938", {"start": v(315.83, 32.52) * mm, "end": v(314.18, 32.5) * mm});
            skLineSegment(sketch, "E9939", {"start": v(314.18, 32.5) * mm, "end": v(312.54, 32.45) * mm});
            skLineSegment(sketch, "E9940", {"start": v(312.54, 32.45) * mm, "end": v(310.93, 32.37) * mm});
            skLineSegment(sketch, "E9941", {"start": v(310.93, 32.37) * mm, "end": v(309.34, 32.24) * mm});
            skLineSegment(sketch, "E9942", {"start": v(309.34, 32.24) * mm, "end": v(307.78, 32.06) * mm});
            skLineSegment(sketch, "E9943", {"start": v(307.78, 32.06) * mm, "end": v(306.26, 31.84) * mm});
            skLineSegment(sketch, "E9944", {"start": v(306.26, 31.84) * mm, "end": v(304.78, 31.56) * mm});
            skLineSegment(sketch, "E9945", {"start": v(304.78, 31.56) * mm, "end": v(303.35, 31.22) * mm});
            skLineSegment(sketch, "E9946", {"start": v(303.35, 31.22) * mm, "end": v(301.96, 30.83) * mm});
            skLineSegment(sketch, "E9947", {"start": v(301.96, 30.83) * mm, "end": v(300.63, 30.37) * mm});
            skLineSegment(sketch, "E9948", {"start": v(300.63, 30.37) * mm, "end": v(299.36, 29.84) * mm});
            skLineSegment(sketch, "E9949", {"start": v(299.36, 29.84) * mm, "end": v(298.15, 29.23) * mm});
            skLineSegment(sketch, "E9950", {"start": v(298.15, 29.23) * mm, "end": v(297.01, 28.55) * mm});
            skLineSegment(sketch, "E9951", {"start": v(297.01, 28.55) * mm, "end": v(295.94, 27.8) * mm});
            skLineSegment(sketch, "E9952", {"start": v(295.94, 27.8) * mm, "end": v(294.95, 26.95) * mm});
            skLineSegment(sketch, "E9953", {"start": v(294.95, 26.95) * mm, "end": v(294.04, 26.02) * mm});
            skLineSegment(sketch, "E9954", {"start": v(294.04, 26.02) * mm, "end": v(293.22, 25) * mm});
            skLineSegment(sketch, "E9955", {"start": v(293.22, 25) * mm, "end": v(292.48, 23.88) * mm});
            skLineSegment(sketch, "E9956", {"start": v(292.48, 23.88) * mm, "end": v(291.84, 22.66) * mm});
            skLineSegment(sketch, "E9957", {"start": v(291.84, 22.66) * mm, "end": v(291.3, 21.34) * mm});
            skLineSegment(sketch, "E9958", {"start": v(291.3, 21.34) * mm, "end": v(290.87, 19.91) * mm});
            skLineSegment(sketch, "E9959", {"start": v(290.87, 19.91) * mm, "end": v(290.54, 18.37) * mm});
            skLineSegment(sketch, "E9960", {"start": v(290.54, 18.37) * mm, "end": v(290.33, 16.72) * mm});
            skLineSegment(sketch, "E9961", {"start": v(348.26, 31.2) * mm, "end": v(348.55, 29.58) * mm});
            skLineSegment(sketch, "E9962", {"start": v(348.55, 29.58) * mm, "end": v(348.84, 27.93) * mm});
            skLineSegment(sketch, "E9963", {"start": v(348.84, 27.93) * mm, "end": v(349.1, 26.27) * mm});
            skLineSegment(sketch, "E9964", {"start": v(349.1, 26.27) * mm, "end": v(349.37, 24.58) * mm});
            skLineSegment(sketch, "E9965", {"start": v(349.37, 24.58) * mm, "end": v(349.62, 22.88) * mm});
            skLineSegment(sketch, "E9966", {"start": v(349.62, 22.88) * mm, "end": v(349.86, 21.16) * mm});
            skLineSegment(sketch, "E9967", {"start": v(349.86, 21.16) * mm, "end": v(350.09, 19.42) * mm});
            skLineSegment(sketch, "E9968", {"start": v(350.09, 19.42) * mm, "end": v(350.3, 17.67) * mm});
            skLineSegment(sketch, "E9969", {"start": v(350.3, 17.67) * mm, "end": v(350.51, 15.9) * mm});
            skLineSegment(sketch, "E9970", {"start": v(350.51, 15.9) * mm, "end": v(350.71, 14.12) * mm});
            skLineSegment(sketch, "E9971", {"start": v(350.71, 14.12) * mm, "end": v(350.9, 12.32) * mm});
            skLineSegment(sketch, "E9972", {"start": v(350.9, 12.32) * mm, "end": v(351.07, 10.52) * mm});
            skLineSegment(sketch, "E9973", {"start": v(351.07, 10.52) * mm, "end": v(351.23, 8.7) * mm});
            skLineSegment(sketch, "E9974", {"start": v(351.23, 8.7) * mm, "end": v(351.39, 6.86) * mm});
            skLineSegment(sketch, "E9975", {"start": v(351.39, 6.86) * mm, "end": v(351.53, 5.02) * mm});
            skLineSegment(sketch, "E9976", {"start": v(351.53, 5.02) * mm, "end": v(351.66, 3.17) * mm});
            skLineSegment(sketch, "E9977", {"start": v(351.66, 3.17) * mm, "end": v(351.78, 1.3) * mm});
            skLineSegment(sketch, "E9978", {"start": v(351.78, 1.3) * mm, "end": v(351.89, -0.56) * mm});
            skLineSegment(sketch, "E9979", {"start": v(351.89, -0.56) * mm, "end": v(351.99, -2.44) * mm});
            skLineSegment(sketch, "E9980", {"start": v(351.99, -2.44) * mm, "end": v(352.07, -4.32) * mm});
            skLineSegment(sketch, "E9981", {"start": v(352.07, -4.32) * mm, "end": v(352.15, -6.21) * mm});
            skLineSegment(sketch, "E9982", {"start": v(352.15, -6.21) * mm, "end": v(352.21, -8.1) * mm});
            skLineSegment(sketch, "E9983", {"start": v(352.21, -8.1) * mm, "end": v(352.27, -10) * mm});
            skLineSegment(sketch, "E9984", {"start": v(352.27, -10) * mm, "end": v(352.31, -11.9) * mm});
            skLineSegment(sketch, "E9985", {"start": v(352.31, -11.9) * mm, "end": v(352.35, -13.81) * mm});
            skLineSegment(sketch, "E9986", {"start": v(352.35, -13.81) * mm, "end": v(352.37, -15.72) * mm});
            skLineSegment(sketch, "E9987", {"start": v(352.37, -15.72) * mm, "end": v(352.38, -17.63) * mm});
            skLineSegment(sketch, "E9988", {"start": v(352.38, -17.63) * mm, "end": v(352.38, -19.53) * mm});
            skLineSegment(sketch, "E9989", {"start": v(352.38, -19.53) * mm, "end": v(352.37, -21.44) * mm});
            skLineSegment(sketch, "E9990", {"start": v(352.37, -21.44) * mm, "end": v(352.35, -23.35) * mm});
            skLineSegment(sketch, "E9991", {"start": v(352.35, -23.35) * mm, "end": v(352.31, -25.25) * mm});
            skLineSegment(sketch, "E9992", {"start": v(352.31, -25.25) * mm, "end": v(352.27, -27.16) * mm});
            skLineSegment(sketch, "E9993", {"start": v(352.27, -27.16) * mm, "end": v(352.21, -29.05) * mm});
            skLineSegment(sketch, "E9994", {"start": v(352.21, -29.05) * mm, "end": v(352.15, -30.95) * mm});
            skLineSegment(sketch, "E9995", {"start": v(352.15, -30.95) * mm, "end": v(352.07, -32.84) * mm});
            skLineSegment(sketch, "E9996", {"start": v(352.07, -32.84) * mm, "end": v(351.99, -34.72) * mm});
            skLineSegment(sketch, "E9997", {"start": v(351.99, -34.72) * mm, "end": v(351.89, -36.6) * mm});
            skLineSegment(sketch, "E9998", {"start": v(351.89, -36.6) * mm, "end": v(351.78, -38.47) * mm});
            skLineSegment(sketch, "E9999", {"start": v(351.78, -38.47) * mm, "end": v(351.66, -40.33) * mm});
            skLineSegment(sketch, "E10000", {"start": v(351.66, -40.33) * mm, "end": v(351.53, -42.18) * mm});
            skLineSegment(sketch, "E10001", {"start": v(351.53, -42.18) * mm, "end": v(351.39, -44.02) * mm});
            skLineSegment(sketch, "E10002", {"start": v(351.39, -44.02) * mm, "end": v(351.23, -45.86) * mm});
            skLineSegment(sketch, "E10003", {"start": v(351.23, -45.86) * mm, "end": v(351.07, -47.68) * mm});
            skLineSegment(sketch, "E10004", {"start": v(351.07, -47.68) * mm, "end": v(350.9, -49.48) * mm});
            skLineSegment(sketch, "E10005", {"start": v(350.9, -49.48) * mm, "end": v(350.71, -51.28) * mm});
            skLineSegment(sketch, "E10006", {"start": v(350.71, -51.28) * mm, "end": v(350.51, -53.06) * mm});
            skLineSegment(sketch, "E10007", {"start": v(350.51, -53.06) * mm, "end": v(350.3, -54.83) * mm});
            skLineSegment(sketch, "E10008", {"start": v(350.3, -54.83) * mm, "end": v(350.09, -56.58) * mm});
            skLineSegment(sketch, "E10009", {"start": v(350.09, -56.58) * mm, "end": v(349.86, -58.32) * mm});
            skLineSegment(sketch, "E10010", {"start": v(349.86, -58.32) * mm, "end": v(349.62, -60.04) * mm});
            skLineSegment(sketch, "E10011", {"start": v(349.62, -60.04) * mm, "end": v(349.37, -61.74) * mm});
            skLineSegment(sketch, "E10012", {"start": v(349.37, -61.74) * mm, "end": v(349.1, -63.43) * mm});
            skLineSegment(sketch, "E10013", {"start": v(349.1, -63.43) * mm, "end": v(348.84, -65.1) * mm});
            skLineSegment(sketch, "E10014", {"start": v(348.84, -65.1) * mm, "end": v(348.55, -66.74) * mm});
            skLineSegment(sketch, "E10015", {"start": v(348.55, -66.74) * mm, "end": v(348.26, -68.36) * mm});
            skLineSegment(sketch, "E10016", {"start": v(348.26, -68.36) * mm, "end": v(349.59, -68.38) * mm});
            skLineSegment(sketch, "E10017", {"start": v(349.59, -68.38) * mm, "end": v(350.97, -68.42) * mm});
            skLineSegment(sketch, "E10018", {"start": v(350.97, -68.42) * mm, "end": v(352.4, -68.49) * mm});
            skLineSegment(sketch, "E10019", {"start": v(352.4, -68.49) * mm, "end": v(353.87, -68.58) * mm});
            skLineSegment(sketch, "E10020", {"start": v(353.87, -68.58) * mm, "end": v(355.38, -68.68) * mm});
            skLineSegment(sketch, "E10021", {"start": v(355.38, -68.68) * mm, "end": v(356.92, -68.8) * mm});
            skLineSegment(sketch, "E10022", {"start": v(356.92, -68.8) * mm, "end": v(358.5, -68.91) * mm});
            skLineSegment(sketch, "E10023", {"start": v(358.5, -68.91) * mm, "end": v(360.08, -69.04) * mm});
            skLineSegment(sketch, "E10024", {"start": v(360.08, -69.04) * mm, "end": v(361.7, -69.16) * mm});
            skLineSegment(sketch, "E10025", {"start": v(361.7, -69.16) * mm, "end": v(363.32, -69.28) * mm});
            skLineSegment(sketch, "E10026", {"start": v(363.32, -69.28) * mm, "end": v(364.95, -69.39) * mm});
            skLineSegment(sketch, "E10027", {"start": v(364.95, -69.39) * mm, "end": v(366.59, -69.48) * mm});
            skLineSegment(sketch, "E10028", {"start": v(366.59, -69.48) * mm, "end": v(368.23, -69.56) * mm});
            skLineSegment(sketch, "E10029", {"start": v(368.23, -69.56) * mm, "end": v(369.86, -69.62) * mm});
            skLineSegment(sketch, "E10030", {"start": v(369.86, -69.62) * mm, "end": v(371.48, -69.65) * mm});
            skLineSegment(sketch, "E10031", {"start": v(371.48, -69.65) * mm, "end": v(373.1, -69.65) * mm});
            skLineSegment(sketch, "E10032", {"start": v(373.1, -69.65) * mm, "end": v(374.68, -69.62) * mm});
            skLineSegment(sketch, "E10033", {"start": v(374.68, -69.62) * mm, "end": v(376.25, -69.55) * mm});
            skLineSegment(sketch, "E10034", {"start": v(376.25, -69.55) * mm, "end": v(377.78, -69.44) * mm});
            skLineSegment(sketch, "E10035", {"start": v(377.78, -69.44) * mm, "end": v(379.29, -69.28) * mm});
            skLineSegment(sketch, "E10036", {"start": v(379.29, -69.28) * mm, "end": v(380.75, -69.07) * mm});
            skLineSegment(sketch, "E10037", {"start": v(380.75, -69.07) * mm, "end": v(382.18, -68.81) * mm});
            skLineSegment(sketch, "E10038", {"start": v(382.18, -68.81) * mm, "end": v(383.55, -68.5) * mm});
            skLineSegment(sketch, "E10039", {"start": v(383.55, -68.5) * mm, "end": v(384.88, -68.1) * mm});
            skLineSegment(sketch, "E10040", {"start": v(384.88, -68.1) * mm, "end": v(386.15, -67.66) * mm});
            skLineSegment(sketch, "E10041", {"start": v(386.15, -67.66) * mm, "end": v(387.35, -67.14) * mm});
            skLineSegment(sketch, "E10042", {"start": v(387.35, -67.14) * mm, "end": v(388.5, -66.54) * mm});
            skLineSegment(sketch, "E10043", {"start": v(388.5, -66.54) * mm, "end": v(389.56, -65.87) * mm});
            skLineSegment(sketch, "E10044", {"start": v(389.56, -65.87) * mm, "end": v(390.55, -65.11) * mm});
            skLineSegment(sketch, "E10045", {"start": v(390.55, -65.11) * mm, "end": v(391.47, -64.27) * mm});
            skLineSegment(sketch, "E10046", {"start": v(391.47, -64.27) * mm, "end": v(392.3, -63.33) * mm});
            skLineSegment(sketch, "E10047", {"start": v(392.3, -63.33) * mm, "end": v(393.04, -62.3) * mm});
            skLineSegment(sketch, "E10048", {"start": v(393.04, -62.3) * mm, "end": v(393.68, -61.17) * mm});
            skLineSegment(sketch, "E10049", {"start": v(393.68, -61.17) * mm, "end": v(394.23, -59.94) * mm});
            skLineSegment(sketch, "E10050", {"start": v(394.23, -59.94) * mm, "end": v(394.67, -58.6) * mm});
            skLineSegment(sketch, "E10051", {"start": v(394.67, -58.6) * mm, "end": v(395, -57.14) * mm});
            skLineSegment(sketch, "E10052", {"start": v(395, -57.14) * mm, "end": v(395.22, -55.57) * mm});
            skLineSegment(sketch, "E10053", {"start": v(395.22, -55.57) * mm, "end": v(395.33, -53.88) * mm});
            skLineSegment(sketch, "E10054", {"start": v(395.33, -53.88) * mm, "end": v(369.26, -52.79) * mm});
            skLineSegment(sketch, "E10055", {"start": v(369.26, -52.79) * mm, "end": v(366.36, -30.35) * mm});
            skLineSegment(sketch, "E10056", {"start": v(366.36, -30.35) * mm, "end": v(366.36, 31.2) * mm});
            skLineSegment(sketch, "E10057", {"start": v(366.36, 31.2) * mm, "end": v(348.26, 31.2) * mm});
            skLineSegment(sketch, "E10058", {"start": v(402.57, 31.2) * mm, "end": v(402.57, -68.36) * mm});
            skLineSegment(sketch, "E10059", {"start": v(402.57, -68.36) * mm, "end": v(404.07, -68.38) * mm});
            skLineSegment(sketch, "E10060", {"start": v(404.07, -68.38) * mm, "end": v(405.6, -68.42) * mm});
            skLineSegment(sketch, "E10061", {"start": v(405.6, -68.42) * mm, "end": v(407.16, -68.5) * mm});
            skLineSegment(sketch, "E10062", {"start": v(407.16, -68.5) * mm, "end": v(408.74, -68.58) * mm});
            skLineSegment(sketch, "E10063", {"start": v(408.74, -68.58) * mm, "end": v(410.34, -68.68) * mm});
            skLineSegment(sketch, "E10064", {"start": v(410.34, -68.68) * mm, "end": v(411.96, -68.79) * mm});
            skLineSegment(sketch, "E10065", {"start": v(411.96, -68.79) * mm, "end": v(413.58, -68.9) * mm});
            skLineSegment(sketch, "E10066", {"start": v(413.58, -68.9) * mm, "end": v(415.21, -69.02) * mm});
            skLineSegment(sketch, "E10067", {"start": v(415.21, -69.02) * mm, "end": v(416.85, -69.13) * mm});
            skLineSegment(sketch, "E10068", {"start": v(416.85, -69.13) * mm, "end": v(418.5, -69.23) * mm});
            skLineSegment(sketch, "E10069", {"start": v(418.5, -69.23) * mm, "end": v(420.13, -69.32) * mm});
            skLineSegment(sketch, "E10070", {"start": v(420.13, -69.32) * mm, "end": v(421.76, -69.4) * mm});
            skLineSegment(sketch, "E10071", {"start": v(421.76, -69.4) * mm, "end": v(423.37, -69.44) * mm});
            skLineSegment(sketch, "E10072", {"start": v(423.37, -69.44) * mm, "end": v(424.98, -69.47) * mm});
            skLineSegment(sketch, "E10073", {"start": v(424.98, -69.47) * mm, "end": v(426.57, -69.46) * mm});
            skLineSegment(sketch, "E10074", {"start": v(426.57, -69.46) * mm, "end": v(428.14, -69.41) * mm});
            skLineSegment(sketch, "E10075", {"start": v(428.14, -69.41) * mm, "end": v(429.68, -69.33) * mm});
            skLineSegment(sketch, "E10076", {"start": v(429.68, -69.33) * mm, "end": v(431.2, -69.2) * mm});
            skLineSegment(sketch, "E10077", {"start": v(431.2, -69.2) * mm, "end": v(432.68, -69.02) * mm});
            skLineSegment(sketch, "E10078", {"start": v(432.68, -69.02) * mm, "end": v(434.13, -68.78) * mm});
            skLineSegment(sketch, "E10079", {"start": v(434.13, -68.78) * mm, "end": v(435.54, -68.49) * mm});
            skLineSegment(sketch, "E10080", {"start": v(435.54, -68.49) * mm, "end": v(436.9, -68.13) * mm});
            skLineSegment(sketch, "E10081", {"start": v(436.9, -68.13) * mm, "end": v(438.23, -67.7) * mm});
            skLineSegment(sketch, "E10082", {"start": v(438.23, -67.7) * mm, "end": v(439.5, -67.2) * mm});
            skLineSegment(sketch, "E10083", {"start": v(439.5, -67.2) * mm, "end": v(440.72, -66.63) * mm});
            skLineSegment(sketch, "E10084", {"start": v(440.72, -66.63) * mm, "end": v(441.89, -65.97) * mm});
            skLineSegment(sketch, "E10085", {"start": v(441.89, -65.97) * mm, "end": v(443, -65.23) * mm});
            skLineSegment(sketch, "E10086", {"start": v(443, -65.23) * mm, "end": v(444.03, -64.4) * mm});
            skLineSegment(sketch, "E10087", {"start": v(444.03, -64.4) * mm, "end": v(445, -63.46) * mm});
            skLineSegment(sketch, "E10088", {"start": v(445, -63.46) * mm, "end": v(445.9, -62.43) * mm});
            skLineSegment(sketch, "E10089", {"start": v(445.9, -62.43) * mm, "end": v(446.74, -61.3) * mm});
            skLineSegment(sketch, "E10090", {"start": v(446.74, -61.3) * mm, "end": v(447.49, -60.05) * mm});
            skLineSegment(sketch, "E10091", {"start": v(447.49, -60.05) * mm, "end": v(448.15, -58.69) * mm});
            skLineSegment(sketch, "E10092", {"start": v(448.15, -58.69) * mm, "end": v(448.74, -57.21) * mm});
            skLineSegment(sketch, "E10093", {"start": v(448.74, -57.21) * mm, "end": v(449.23, -55.61) * mm});
            skLineSegment(sketch, "E10094", {"start": v(449.23, -55.61) * mm, "end": v(449.64, -53.88) * mm});
            skLineSegment(sketch, "E10095", {"start": v(449.64, -53.88) * mm, "end": v(418.86, -53.88) * mm});
            skLineSegment(sketch, "E10096", {"start": v(418.86, -53.88) * mm, "end": v(418.86, -24.92) * mm});
            skLineSegment(sketch, "E10097", {"start": v(418.86, -24.92) * mm, "end": v(433.34, -26.73) * mm});
            skLineSegment(sketch, "E10098", {"start": v(433.34, -26.73) * mm, "end": v(433.34, -10.43) * mm});
            skLineSegment(sketch, "E10099", {"start": v(433.34, -10.43) * mm, "end": v(418.86, -12.24) * mm});
            skLineSegment(sketch, "E10100", {"start": v(418.86, -12.24) * mm, "end": v(418.86, 16.72) * mm});
            skLineSegment(sketch, "E10101", {"start": v(418.86, 16.72) * mm, "end": v(449.64, 16.72) * mm});
            skLineSegment(sketch, "E10102", {"start": v(449.64, 16.72) * mm, "end": v(449.23, 18.45) * mm});
            skLineSegment(sketch, "E10103", {"start": v(449.23, 18.45) * mm, "end": v(448.74, 20.05) * mm});
            skLineSegment(sketch, "E10104", {"start": v(448.74, 20.05) * mm, "end": v(448.15, 21.53) * mm});
            skLineSegment(sketch, "E10105", {"start": v(448.15, 21.53) * mm, "end": v(447.49, 22.89) * mm});
            skLineSegment(sketch, "E10106", {"start": v(447.49, 22.89) * mm, "end": v(446.74, 24.13) * mm});
            skLineSegment(sketch, "E10107", {"start": v(446.74, 24.13) * mm, "end": v(445.9, 25.27) * mm});
            skLineSegment(sketch, "E10108", {"start": v(445.9, 25.27) * mm, "end": v(445, 26.3) * mm});
            skLineSegment(sketch, "E10109", {"start": v(445, 26.3) * mm, "end": v(444.03, 27.23) * mm});
            skLineSegment(sketch, "E10110", {"start": v(444.03, 27.23) * mm, "end": v(443, 28.07) * mm});
            skLineSegment(sketch, "E10111", {"start": v(443, 28.07) * mm, "end": v(441.89, 28.81) * mm});
            skLineSegment(sketch, "E10112", {"start": v(441.89, 28.81) * mm, "end": v(440.72, 29.47) * mm});
            skLineSegment(sketch, "E10113", {"start": v(440.72, 29.47) * mm, "end": v(439.5, 30.04) * mm});
            skLineSegment(sketch, "E10114", {"start": v(439.5, 30.04) * mm, "end": v(438.23, 30.54) * mm});
            skLineSegment(sketch, "E10115", {"start": v(438.23, 30.54) * mm, "end": v(436.9, 30.97) * mm});
            skLineSegment(sketch, "E10116", {"start": v(436.9, 30.97) * mm, "end": v(435.54, 31.33) * mm});
            skLineSegment(sketch, "E10117", {"start": v(435.54, 31.33) * mm, "end": v(434.13, 31.62) * mm});
            skLineSegment(sketch, "E10118", {"start": v(434.13, 31.62) * mm, "end": v(432.68, 31.86) * mm});
            skLineSegment(sketch, "E10119", {"start": v(432.68, 31.86) * mm, "end": v(431.2, 32.04) * mm});
            skLineSegment(sketch, "E10120", {"start": v(431.2, 32.04) * mm, "end": v(429.68, 32.17) * mm});
            skLineSegment(sketch, "E10121", {"start": v(429.68, 32.17) * mm, "end": v(428.14, 32.25) * mm});
            skLineSegment(sketch, "E10122", {"start": v(428.14, 32.25) * mm, "end": v(426.57, 32.3) * mm});
            skLineSegment(sketch, "E10123", {"start": v(426.57, 32.3) * mm, "end": v(424.98, 32.3) * mm});
            skLineSegment(sketch, "E10124", {"start": v(424.98, 32.3) * mm, "end": v(423.37, 32.28) * mm});
            skLineSegment(sketch, "E10125", {"start": v(423.37, 32.28) * mm, "end": v(421.76, 32.23) * mm});
            skLineSegment(sketch, "E10126", {"start": v(421.76, 32.23) * mm, "end": v(420.13, 32.16) * mm});
            skLineSegment(sketch, "E10127", {"start": v(420.13, 32.16) * mm, "end": v(418.5, 32.07) * mm});
            skLineSegment(sketch, "E10128", {"start": v(418.5, 32.07) * mm, "end": v(416.85, 31.97) * mm});
            skLineSegment(sketch, "E10129", {"start": v(416.85, 31.97) * mm, "end": v(415.21, 31.86) * mm});
            skLineSegment(sketch, "E10130", {"start": v(415.21, 31.86) * mm, "end": v(413.58, 31.74) * mm});
            skLineSegment(sketch, "E10131", {"start": v(413.58, 31.74) * mm, "end": v(411.96, 31.63) * mm});
            skLineSegment(sketch, "E10132", {"start": v(411.96, 31.63) * mm, "end": v(410.34, 31.52) * mm});
            skLineSegment(sketch, "E10133", {"start": v(410.34, 31.52) * mm, "end": v(408.74, 31.42) * mm});
            skLineSegment(sketch, "E10134", {"start": v(408.74, 31.42) * mm, "end": v(407.16, 31.33) * mm});
            skLineSegment(sketch, "E10135", {"start": v(407.16, 31.33) * mm, "end": v(405.6, 31.26) * mm});
            skLineSegment(sketch, "E10136", {"start": v(405.6, 31.26) * mm, "end": v(404.07, 31.22) * mm});
            skLineSegment(sketch, "E10137", {"start": v(404.07, 31.22) * mm, "end": v(402.57, 31.2) * mm});
            skLineSegment(sketch, "E10138", {"start": v(-314.32, 16.72) * mm, "end": v(-314.34, 15.04) * mm});
            skLineSegment(sketch, "E10139", {"start": v(-314.34, 15.04) * mm, "end": v(-314.38, 13.38) * mm});
            skLineSegment(sketch, "E10140", {"start": v(-314.38, 13.38) * mm, "end": v(-314.44, 11.72) * mm});
            skLineSegment(sketch, "E10141", {"start": v(-314.44, 11.72) * mm, "end": v(-314.5, 10.08) * mm});
            skLineSegment(sketch, "E10142", {"start": v(-314.5, 10.08) * mm, "end": v(-314.56, 8.46) * mm});
            skLineSegment(sketch, "E10143", {"start": v(-314.56, 8.46) * mm, "end": v(-314.61, 6.87) * mm});
            skLineSegment(sketch, "E10144", {"start": v(-314.61, 6.87) * mm, "end": v(-314.65, 5.3) * mm});
            skLineSegment(sketch, "E10145", {"start": v(-314.65, 5.3) * mm, "end": v(-314.65, 3.79) * mm});
            skLineSegment(sketch, "E10146", {"start": v(-314.65, 3.79) * mm, "end": v(-314.62, 2.3) * mm});
            skLineSegment(sketch, "E10147", {"start": v(-314.62, 2.3) * mm, "end": v(-314.54, 0.86) * mm});
            skLineSegment(sketch, "E10148", {"start": v(-314.54, 0.86) * mm, "end": v(-314.41, -0.53) * mm});
            skLineSegment(sketch, "E10149", {"start": v(-314.41, -0.53) * mm, "end": v(-314.22, -1.86) * mm});
            skLineSegment(sketch, "E10150", {"start": v(-314.22, -1.86) * mm, "end": v(-313.95, -3.14) * mm});
            skLineSegment(sketch, "E10151", {"start": v(-313.95, -3.14) * mm, "end": v(-313.6, -4.35) * mm});
            skLineSegment(sketch, "E10152", {"start": v(-313.6, -4.35) * mm, "end": v(-313.16, -5.5) * mm});
            skLineSegment(sketch, "E10153", {"start": v(-313.16, -5.5) * mm, "end": v(-312.62, -6.57) * mm});
            skLineSegment(sketch, "E10154", {"start": v(-312.62, -6.57) * mm, "end": v(-311.97, -7.56) * mm});
            skLineSegment(sketch, "E10155", {"start": v(-311.97, -7.56) * mm, "end": v(-311.21, -8.47) * mm});
            skLineSegment(sketch, "E10156", {"start": v(-311.21, -8.47) * mm, "end": v(-310.32, -9.3) * mm});
            skLineSegment(sketch, "E10157", {"start": v(-310.32, -9.3) * mm, "end": v(-309.3, -10.03) * mm});
            skLineSegment(sketch, "E10158", {"start": v(-309.3, -10.03) * mm, "end": v(-308.13, -10.66) * mm});
            skLineSegment(sketch, "E10159", {"start": v(-308.13, -10.66) * mm, "end": v(-306.81, -11.2) * mm});
            skLineSegment(sketch, "E10160", {"start": v(-306.81, -11.2) * mm, "end": v(-305.33, -11.63) * mm});
            skLineSegment(sketch, "E10161", {"start": v(-305.33, -11.63) * mm, "end": v(-303.68, -11.95) * mm});
            skLineSegment(sketch, "E10162", {"start": v(-303.68, -11.95) * mm, "end": v(-301.86, -12.16) * mm});
            skLineSegment(sketch, "E10163", {"start": v(-301.86, -12.16) * mm, "end": v(-299.84, -12.24) * mm});
            skLineSegment(sketch, "E10164", {"start": v(-299.84, -12.24) * mm, "end": v(-299.84, 16.72) * mm});
            skLineSegment(sketch, "E10165", {"start": v(-299.84, 16.72) * mm, "end": v(-314.32, 16.72) * mm});
            skLineSegment(sketch, "E10166", {"start": v(-258.2, 16.72) * mm, "end": v(-258.2, -12.24) * mm});
            skLineSegment(sketch, "E10167", {"start": v(-258.2, -12.24) * mm, "end": v(-243.72, -12.24) * mm});
            skLineSegment(sketch, "E10168", {"start": v(-243.72, -12.24) * mm, "end": v(-243.72, 16.72) * mm});
            skLineSegment(sketch, "E10169", {"start": v(-243.72, 16.72) * mm, "end": v(-258.2, 16.72) * mm});
            skLineSegment(sketch, "E10170", {"start": v(-366.82, -8.62) * mm, "end": v(-370.44, -30.35) * mm});
            skLineSegment(sketch, "E10171", {"start": v(-370.44, -30.35) * mm, "end": v(-361.4, -30.35) * mm});
            skLineSegment(sketch, "E10172", {"start": v(-361.4, -30.35) * mm, "end": v(-366.82, -8.62) * mm});
            skLineSegment(sketch, "E10173", {"start": v(-205.51, -409.3) * mm, "end": v(-206.71, -410.47) * mm});
            skLineSegment(sketch, "E10174", {"start": v(-206.71, -410.47) * mm, "end": v(-207.83, -411.7) * mm});
            skLineSegment(sketch, "E10175", {"start": v(-207.83, -411.7) * mm, "end": v(-208.87, -413) * mm});
            skLineSegment(sketch, "E10176", {"start": v(-208.87, -413) * mm, "end": v(-209.84, -414.36) * mm});
            skLineSegment(sketch, "E10177", {"start": v(-209.84, -414.36) * mm, "end": v(-210.72, -415.76) * mm});
            skLineSegment(sketch, "E10178", {"start": v(-210.72, -415.76) * mm, "end": v(-211.52, -417.2) * mm});
            skLineSegment(sketch, "E10179", {"start": v(-211.52, -417.2) * mm, "end": v(-212.23, -418.7) * mm});
            skLineSegment(sketch, "E10180", {"start": v(-212.23, -418.7) * mm, "end": v(-212.86, -420.23) * mm});
            skLineSegment(sketch, "E10181", {"start": v(-212.86, -420.23) * mm, "end": v(-213.41, -421.79) * mm});
            skLineSegment(sketch, "E10182", {"start": v(-213.41, -421.79) * mm, "end": v(-213.87, -423.37) * mm});
            skLineSegment(sketch, "E10183", {"start": v(-213.87, -423.37) * mm, "end": v(-214.25, -424.98) * mm});
            skLineSegment(sketch, "E10184", {"start": v(-214.25, -424.98) * mm, "end": v(-214.53, -426.6) * mm});
            skLineSegment(sketch, "E10185", {"start": v(-214.53, -426.6) * mm, "end": v(-214.72, -428.24) * mm});
            skLineSegment(sketch, "E10186", {"start": v(-214.72, -428.24) * mm, "end": v(-214.83, -429.89) * mm});
            skLineSegment(sketch, "E10187", {"start": v(-214.83, -429.89) * mm, "end": v(-214.84, -431.53) * mm});
            skLineSegment(sketch, "E10188", {"start": v(-214.84, -431.53) * mm, "end": v(-214.76, -433.17) * mm});
            skLineSegment(sketch, "E10189", {"start": v(-214.76, -433.17) * mm, "end": v(-214.59, -434.8) * mm});
            skLineSegment(sketch, "E10190", {"start": v(-214.59, -434.8) * mm, "end": v(-214.32, -436.43) * mm});
            skLineSegment(sketch, "E10191", {"start": v(-214.32, -436.43) * mm, "end": v(-213.95, -438.03) * mm});
            skLineSegment(sketch, "E10192", {"start": v(-213.95, -438.03) * mm, "end": v(-213.49, -439.61) * mm});
            skLineSegment(sketch, "E10193", {"start": v(-213.49, -439.61) * mm, "end": v(-212.93, -441.17) * mm});
            skLineSegment(sketch, "E10194", {"start": v(-212.93, -441.17) * mm, "end": v(-212.27, -442.69) * mm});
            skLineSegment(sketch, "E10195", {"start": v(-212.27, -442.69) * mm, "end": v(-211.5, -444.17) * mm});
            skLineSegment(sketch, "E10196", {"start": v(-211.5, -444.17) * mm, "end": v(-210.64, -445.6) * mm});
            skLineSegment(sketch, "E10197", {"start": v(-210.64, -445.6) * mm, "end": v(-209.68, -447) * mm});
            skLineSegment(sketch, "E10198", {"start": v(-209.68, -447) * mm, "end": v(-208.6, -448.34) * mm});
            skLineSegment(sketch, "E10199", {"start": v(-208.6, -448.34) * mm, "end": v(-207.5, -449.58) * mm});
            skLineSegment(sketch, "E10200", {"start": v(-207.5, -449.58) * mm, "end": v(-206.32, -450.77) * mm});
            skLineSegment(sketch, "E10201", {"start": v(-206.32, -450.77) * mm, "end": v(-205.1, -451.9) * mm});
            skLineSegment(sketch, "E10202", {"start": v(-205.1, -451.9) * mm, "end": v(-203.8, -453) * mm});
            skLineSegment(sketch, "E10203", {"start": v(-203.8, -453) * mm, "end": v(-202.47, -454.04) * mm});
            skLineSegment(sketch, "E10204", {"start": v(-202.47, -454.04) * mm, "end": v(-201.1, -455.03) * mm});
            skLineSegment(sketch, "E10205", {"start": v(-201.1, -455.03) * mm, "end": v(-199.66, -455.99) * mm});
            skLineSegment(sketch, "E10206", {"start": v(-199.66, -455.99) * mm, "end": v(-198.2, -456.9) * mm});
            skLineSegment(sketch, "E10207", {"start": v(-198.2, -456.9) * mm, "end": v(-196.68, -457.77) * mm});
            skLineSegment(sketch, "E10208", {"start": v(-196.68, -457.77) * mm, "end": v(-195.14, -458.61) * mm});
            skLineSegment(sketch, "E10209", {"start": v(-195.14, -458.61) * mm, "end": v(-193.56, -459.41) * mm});
            skLineSegment(sketch, "E10210", {"start": v(-193.56, -459.41) * mm, "end": v(-191.95, -460.18) * mm});
            skLineSegment(sketch, "E10211", {"start": v(-191.95, -460.18) * mm, "end": v(-190.31, -460.92) * mm});
            skLineSegment(sketch, "E10212", {"start": v(-190.31, -460.92) * mm, "end": v(-188.66, -461.63) * mm});
            skLineSegment(sketch, "E10213", {"start": v(-188.66, -461.63) * mm, "end": v(-186.97, -462.31) * mm});
            skLineSegment(sketch, "E10214", {"start": v(-186.97, -462.31) * mm, "end": v(-185.28, -462.97) * mm});
            skLineSegment(sketch, "E10215", {"start": v(-185.28, -462.97) * mm, "end": v(-183.56, -463.6) * mm});
            skLineSegment(sketch, "E10216", {"start": v(-183.56, -463.6) * mm, "end": v(-181.84, -464.22) * mm});
            skLineSegment(sketch, "E10217", {"start": v(-181.84, -464.22) * mm, "end": v(-180.1, -464.82) * mm});
            skLineSegment(sketch, "E10218", {"start": v(-180.1, -464.82) * mm, "end": v(-178.36, -465.4) * mm});
            skLineSegment(sketch, "E10219", {"start": v(-178.36, -465.4) * mm, "end": v(-176.62, -465.96) * mm});
            skLineSegment(sketch, "E10220", {"start": v(-176.62, -465.96) * mm, "end": v(-174.87, -466.51) * mm});
            skLineSegment(sketch, "E10221", {"start": v(-174.87, -466.51) * mm, "end": v(-173.13, -467.05) * mm});
            skLineSegment(sketch, "E10222", {"start": v(-173.13, -467.05) * mm, "end": v(-171.4, -467.58) * mm});
            skLineSegment(sketch, "E10223", {"start": v(-171.4, -467.58) * mm, "end": v(-169.67, -468.1) * mm});
            skLineSegment(sketch, "E10224", {"start": v(-169.67, -468.1) * mm, "end": v(-167.95, -468.62) * mm});
            skLineSegment(sketch, "E10225", {"start": v(-167.95, -468.62) * mm, "end": v(-166.25, -469.14) * mm});
            skLineSegment(sketch, "E10226", {"start": v(-166.25, -469.14) * mm, "end": v(-164.57, -469.66) * mm});
            skLineSegment(sketch, "E10227", {"start": v(-164.57, -469.66) * mm, "end": v(-162.9, -470.17) * mm});
            skLineSegment(sketch, "E10228", {"start": v(-162.9, -470.17) * mm, "end": v(-161.27, -470.7) * mm});
            skLineSegment(sketch, "E10229", {"start": v(-161.27, -470.7) * mm, "end": v(-159.66, -471.21) * mm});
            skLineSegment(sketch, "E10230", {"start": v(-159.66, -471.21) * mm, "end": v(-158.07, -471.75) * mm});
            skLineSegment(sketch, "E10231", {"start": v(-158.07, -471.75) * mm, "end": v(-156.53, -472.28) * mm});
            skLineSegment(sketch, "E10232", {"start": v(-156.53, -472.28) * mm, "end": v(-155.01, -472.84) * mm});
            skLineSegment(sketch, "E10233", {"start": v(-155.01, -472.84) * mm, "end": v(-153.32, -473.46) * mm});
            skLineSegment(sketch, "E10234", {"start": v(-153.32, -473.46) * mm, "end": v(-151.63, -474.07) * mm});
            skLineSegment(sketch, "E10235", {"start": v(-151.63, -474.07) * mm, "end": v(-149.94, -474.68) * mm});
            skLineSegment(sketch, "E10236", {"start": v(-149.94, -474.68) * mm, "end": v(-148.24, -475.27) * mm});
            skLineSegment(sketch, "E10237", {"start": v(-148.24, -475.27) * mm, "end": v(-146.53, -475.86) * mm});
            skLineSegment(sketch, "E10238", {"start": v(-146.53, -475.86) * mm, "end": v(-144.83, -476.44) * mm});
            skLineSegment(sketch, "E10239", {"start": v(-144.83, -476.44) * mm, "end": v(-143.12, -477) * mm});
            skLineSegment(sketch, "E10240", {"start": v(-143.12, -477) * mm, "end": v(-141.41, -477.56) * mm});
            skLineSegment(sketch, "E10241", {"start": v(-141.41, -477.56) * mm, "end": v(-139.7, -478.11) * mm});
            skLineSegment(sketch, "E10242", {"start": v(-139.7, -478.11) * mm, "end": v(-137.98, -478.65) * mm});
            skLineSegment(sketch, "E10243", {"start": v(-137.98, -478.65) * mm, "end": v(-136.26, -479.18) * mm});
            skLineSegment(sketch, "E10244", {"start": v(-136.26, -479.18) * mm, "end": v(-134.54, -479.7) * mm});
            skLineSegment(sketch, "E10245", {"start": v(-134.54, -479.7) * mm, "end": v(-132.82, -480.22) * mm});
            skLineSegment(sketch, "E10246", {"start": v(-132.82, -480.22) * mm, "end": v(-131.09, -480.72) * mm});
            skLineSegment(sketch, "E10247", {"start": v(-131.09, -480.72) * mm, "end": v(-129.36, -481.21) * mm});
            skLineSegment(sketch, "E10248", {"start": v(-129.36, -481.21) * mm, "end": v(-127.63, -481.7) * mm});
            skLineSegment(sketch, "E10249", {"start": v(-127.63, -481.7) * mm, "end": v(-125.9, -482.18) * mm});
            skLineSegment(sketch, "E10250", {"start": v(-125.9, -482.18) * mm, "end": v(-124.15, -482.65) * mm});
            skLineSegment(sketch, "E10251", {"start": v(-124.15, -482.65) * mm, "end": v(-122.41, -483.1) * mm});
            skLineSegment(sketch, "E10252", {"start": v(-122.41, -483.1) * mm, "end": v(-120.67, -483.56) * mm});
            skLineSegment(sketch, "E10253", {"start": v(-120.67, -483.56) * mm, "end": v(-118.93, -484) * mm});
            skLineSegment(sketch, "E10254", {"start": v(-118.93, -484) * mm, "end": v(-117.18, -484.44) * mm});
            skLineSegment(sketch, "E10255", {"start": v(-117.18, -484.44) * mm, "end": v(-115.43, -484.86) * mm});
            skLineSegment(sketch, "E10256", {"start": v(-115.43, -484.86) * mm, "end": v(-113.68, -485.28) * mm});
            skLineSegment(sketch, "E10257", {"start": v(-113.68, -485.28) * mm, "end": v(-111.93, -485.7) * mm});
            skLineSegment(sketch, "E10258", {"start": v(-111.93, -485.7) * mm, "end": v(-110.17, -486.1) * mm});
            skLineSegment(sketch, "E10259", {"start": v(-110.17, -486.1) * mm, "end": v(-108.41, -486.49) * mm});
            skLineSegment(sketch, "E10260", {"start": v(-108.41, -486.49) * mm, "end": v(-106.66, -486.87) * mm});
            skLineSegment(sketch, "E10261", {"start": v(-106.66, -486.87) * mm, "end": v(-104.9, -487.25) * mm});
            skLineSegment(sketch, "E10262", {"start": v(-104.9, -487.25) * mm, "end": v(-103.13, -487.62) * mm});
            skLineSegment(sketch, "E10263", {"start": v(-103.13, -487.62) * mm, "end": v(-101.37, -487.98) * mm});
            skLineSegment(sketch, "E10264", {"start": v(-101.37, -487.98) * mm, "end": v(-99.6, -488.33) * mm});
            skLineSegment(sketch, "E10265", {"start": v(-99.6, -488.33) * mm, "end": v(-97.83, -488.68) * mm});
            skLineSegment(sketch, "E10266", {"start": v(-97.83, -488.68) * mm, "end": v(-96.06, -489.02) * mm});
            skLineSegment(sketch, "E10267", {"start": v(-96.06, -489.02) * mm, "end": v(-94.29, -489.35) * mm});
            skLineSegment(sketch, "E10268", {"start": v(-94.29, -489.35) * mm, "end": v(-92.51, -489.67) * mm});
            skLineSegment(sketch, "E10269", {"start": v(-92.51, -489.67) * mm, "end": v(-90.74, -490) * mm});
            skLineSegment(sketch, "E10270", {"start": v(-90.74, -490) * mm, "end": v(-88.96, -490.3) * mm});
            skLineSegment(sketch, "E10271", {"start": v(-88.96, -490.3) * mm, "end": v(-87.18, -490.6) * mm});
            skLineSegment(sketch, "E10272", {"start": v(-87.18, -490.6) * mm, "end": v(-85.4, -490.9) * mm});
            skLineSegment(sketch, "E10273", {"start": v(-85.4, -490.9) * mm, "end": v(-83.62, -491.18) * mm});
            skLineSegment(sketch, "E10274", {"start": v(-83.62, -491.18) * mm, "end": v(-81.83, -491.46) * mm});
            skLineSegment(sketch, "E10275", {"start": v(-81.83, -491.46) * mm, "end": v(-80.05, -491.73) * mm});
            skLineSegment(sketch, "E10276", {"start": v(-80.05, -491.73) * mm, "end": v(-78.26, -492) * mm});
            skLineSegment(sketch, "E10277", {"start": v(-78.26, -492) * mm, "end": v(-76.48, -492.26) * mm});
            skLineSegment(sketch, "E10278", {"start": v(-76.48, -492.26) * mm, "end": v(-74.69, -492.5) * mm});
            skLineSegment(sketch, "E10279", {"start": v(-74.69, -492.5) * mm, "end": v(-72.9, -492.75) * mm});
            skLineSegment(sketch, "E10280", {"start": v(-72.9, -492.75) * mm, "end": v(-71.1, -493) * mm});
            skLineSegment(sketch, "E10281", {"start": v(-71.1, -493) * mm, "end": v(-69.32, -493.22) * mm});
            skLineSegment(sketch, "E10282", {"start": v(-69.32, -493.22) * mm, "end": v(-67.52, -493.45) * mm});
            skLineSegment(sketch, "E10283", {"start": v(-67.52, -493.45) * mm, "end": v(-65.73, -493.66) * mm});
            skLineSegment(sketch, "E10284", {"start": v(-65.73, -493.66) * mm, "end": v(-63.94, -493.88) * mm});
            skLineSegment(sketch, "E10285", {"start": v(-63.94, -493.88) * mm, "end": v(-62.14, -494.08) * mm});
            skLineSegment(sketch, "E10286", {"start": v(-62.14, -494.08) * mm, "end": v(-60.34, -494.28) * mm});
            skLineSegment(sketch, "E10287", {"start": v(-60.34, -494.28) * mm, "end": v(-58.55, -494.47) * mm});
            skLineSegment(sketch, "E10288", {"start": v(-58.55, -494.47) * mm, "end": v(-56.75, -494.66) * mm});
            skLineSegment(sketch, "E10289", {"start": v(-56.75, -494.66) * mm, "end": v(-54.95, -494.84) * mm});
            skLineSegment(sketch, "E10290", {"start": v(-54.95, -494.84) * mm, "end": v(-53.15, -495) * mm});
            skLineSegment(sketch, "E10291", {"start": v(-53.15, -495) * mm, "end": v(-51.35, -495.18) * mm});
            skLineSegment(sketch, "E10292", {"start": v(-51.35, -495.18) * mm, "end": v(-49.55, -495.34) * mm});
            skLineSegment(sketch, "E10293", {"start": v(-49.55, -495.34) * mm, "end": v(-47.75, -495.5) * mm});
            skLineSegment(sketch, "E10294", {"start": v(-47.75, -495.5) * mm, "end": v(-45.95, -495.64) * mm});
            skLineSegment(sketch, "E10295", {"start": v(-45.95, -495.64) * mm, "end": v(-44.14, -495.78) * mm});
            skLineSegment(sketch, "E10296", {"start": v(-44.14, -495.78) * mm, "end": v(-42.34, -495.92) * mm});
            skLineSegment(sketch, "E10297", {"start": v(-42.34, -495.92) * mm, "end": v(-40.54, -496.05) * mm});
            skLineSegment(sketch, "E10298", {"start": v(-40.54, -496.05) * mm, "end": v(-38.73, -496.18) * mm});
            skLineSegment(sketch, "E10299", {"start": v(-38.73, -496.18) * mm, "end": v(-36.93, -496.3) * mm});
            skLineSegment(sketch, "E10300", {"start": v(-36.93, -496.3) * mm, "end": v(-35.13, -496.41) * mm});
            skLineSegment(sketch, "E10301", {"start": v(-35.13, -496.41) * mm, "end": v(-33.32, -496.52) * mm});
            skLineSegment(sketch, "E10302", {"start": v(-33.32, -496.52) * mm, "end": v(-31.52, -496.63) * mm});
            skLineSegment(sketch, "E10303", {"start": v(-31.52, -496.63) * mm, "end": v(-29.71, -496.72) * mm});
            skLineSegment(sketch, "E10304", {"start": v(-29.71, -496.72) * mm, "end": v(-27.9, -496.82) * mm});
            skLineSegment(sketch, "E10305", {"start": v(-27.9, -496.82) * mm, "end": v(-26.1, -496.9) * mm});
            skLineSegment(sketch, "E10306", {"start": v(-26.1, -496.9) * mm, "end": v(-24.3, -496.99) * mm});
            skLineSegment(sketch, "E10307", {"start": v(-24.3, -496.99) * mm, "end": v(-22.5, -497.06) * mm});
            skLineSegment(sketch, "E10308", {"start": v(-22.5, -497.06) * mm, "end": v(-20.7, -497.14) * mm});
            skLineSegment(sketch, "E10309", {"start": v(-20.7, -497.14) * mm, "end": v(-18.89, -497.2) * mm});
            skLineSegment(sketch, "E10310", {"start": v(-18.89, -497.2) * mm, "end": v(-17.08, -497.27) * mm});
            skLineSegment(sketch, "E10311", {"start": v(-17.08, -497.27) * mm, "end": v(-15.28, -497.32) * mm});
            skLineSegment(sketch, "E10312", {"start": v(-15.28, -497.32) * mm, "end": v(-13.47, -497.37) * mm});
            skLineSegment(sketch, "E10313", {"start": v(-13.47, -497.37) * mm, "end": v(-11.67, -497.42) * mm});
            skLineSegment(sketch, "E10314", {"start": v(-11.67, -497.42) * mm, "end": v(-9.87, -497.47) * mm});
            skLineSegment(sketch, "E10315", {"start": v(-9.87, -497.47) * mm, "end": v(-8.07, -497.5) * mm});
            skLineSegment(sketch, "E10316", {"start": v(-8.07, -497.5) * mm, "end": v(-6.26, -497.54) * mm});
            skLineSegment(sketch, "E10317", {"start": v(-6.26, -497.54) * mm, "end": v(-4.46, -497.57) * mm});
            skLineSegment(sketch, "E10318", {"start": v(-4.46, -497.57) * mm, "end": v(-2.66, -497.6) * mm});
            skLineSegment(sketch, "E10319", {"start": v(-2.66, -497.6) * mm, "end": v(-0.86, -497.61) * mm});
            skLineSegment(sketch, "E10320", {"start": v(-0.86, -497.61) * mm, "end": v(0.94, -497.63) * mm});
            skLineSegment(sketch, "E10321", {"start": v(0.94, -497.63) * mm, "end": v(2.74, -497.64) * mm});
            skLineSegment(sketch, "E10322", {"start": v(2.74, -497.64) * mm, "end": v(4.54, -497.65) * mm});
            skLineSegment(sketch, "E10323", {"start": v(4.54, -497.65) * mm, "end": v(6.33, -497.65) * mm});
            skLineSegment(sketch, "E10324", {"start": v(6.33, -497.65) * mm, "end": v(8.13, -497.65) * mm});
            skLineSegment(sketch, "E10325", {"start": v(8.13, -497.65) * mm, "end": v(9.93, -497.64) * mm});
            skLineSegment(sketch, "E10326", {"start": v(9.93, -497.64) * mm, "end": v(11.72, -497.63) * mm});
            skLineSegment(sketch, "E10327", {"start": v(11.72, -497.63) * mm, "end": v(13.52, -497.62) * mm});
            skLineSegment(sketch, "E10328", {"start": v(13.52, -497.62) * mm, "end": v(15.3, -497.6) * mm});
            skLineSegment(sketch, "E10329", {"start": v(15.3, -497.6) * mm, "end": v(17.1, -497.58) * mm});
            skLineSegment(sketch, "E10330", {"start": v(17.1, -497.58) * mm, "end": v(18.9, -497.56) * mm});
            skLineSegment(sketch, "E10331", {"start": v(18.9, -497.56) * mm, "end": v(20.68, -497.53) * mm});
            skLineSegment(sketch, "E10332", {"start": v(20.68, -497.53) * mm, "end": v(22.47, -497.5) * mm});
            skLineSegment(sketch, "E10333", {"start": v(22.47, -497.5) * mm, "end": v(24.26, -497.47) * mm});
            skLineSegment(sketch, "E10334", {"start": v(24.26, -497.47) * mm, "end": v(26.04, -497.43) * mm});
            skLineSegment(sketch, "E10335", {"start": v(26.04, -497.43) * mm, "end": v(27.83, -497.39) * mm});
            skLineSegment(sketch, "E10336", {"start": v(27.83, -497.39) * mm, "end": v(29.63, -497.34) * mm});
            skLineSegment(sketch, "E10337", {"start": v(29.63, -497.34) * mm, "end": v(31.44, -497.27) * mm});
            skLineSegment(sketch, "E10338", {"start": v(31.44, -497.27) * mm, "end": v(33.24, -497.2) * mm});
            skLineSegment(sketch, "E10339", {"start": v(33.24, -497.2) * mm, "end": v(35.05, -497.12) * mm});
            skLineSegment(sketch, "E10340", {"start": v(35.05, -497.12) * mm, "end": v(36.85, -497.03) * mm});
            skLineSegment(sketch, "E10341", {"start": v(36.85, -497.03) * mm, "end": v(38.66, -496.92) * mm});
            skLineSegment(sketch, "E10342", {"start": v(38.66, -496.92) * mm, "end": v(40.46, -496.8) * mm});
            skLineSegment(sketch, "E10343", {"start": v(40.46, -496.8) * mm, "end": v(42.27, -496.68) * mm});
            skLineSegment(sketch, "E10344", {"start": v(42.27, -496.68) * mm, "end": v(44.07, -496.55) * mm});
            skLineSegment(sketch, "E10345", {"start": v(44.07, -496.55) * mm, "end": v(45.88, -496.4) * mm});
            skLineSegment(sketch, "E10346", {"start": v(45.88, -496.4) * mm, "end": v(47.68, -496.25) * mm});
            skLineSegment(sketch, "E10347", {"start": v(47.68, -496.25) * mm, "end": v(49.49, -496.09) * mm});
            skLineSegment(sketch, "E10348", {"start": v(49.49, -496.09) * mm, "end": v(51.3, -495.91) * mm});
            skLineSegment(sketch, "E10349", {"start": v(51.3, -495.91) * mm, "end": v(53.1, -495.73) * mm});
            skLineSegment(sketch, "E10350", {"start": v(53.1, -495.73) * mm, "end": v(54.9, -495.54) * mm});
            skLineSegment(sketch, "E10351", {"start": v(54.9, -495.54) * mm, "end": v(56.7, -495.33) * mm});
            skLineSegment(sketch, "E10352", {"start": v(56.7, -495.33) * mm, "end": v(58.51, -495.12) * mm});
            skLineSegment(sketch, "E10353", {"start": v(58.51, -495.12) * mm, "end": v(60.31, -494.9) * mm});
            skLineSegment(sketch, "E10354", {"start": v(60.31, -494.9) * mm, "end": v(62.12, -494.67) * mm});
            skLineSegment(sketch, "E10355", {"start": v(62.12, -494.67) * mm, "end": v(63.92, -494.44) * mm});
            skLineSegment(sketch, "E10356", {"start": v(63.92, -494.44) * mm, "end": v(65.72, -494.2) * mm});
            skLineSegment(sketch, "E10357", {"start": v(65.72, -494.2) * mm, "end": v(67.52, -493.94) * mm});
            skLineSegment(sketch, "E10358", {"start": v(67.52, -493.94) * mm, "end": v(69.32, -493.67) * mm});
            skLineSegment(sketch, "E10359", {"start": v(69.32, -493.67) * mm, "end": v(71.12, -493.4) * mm});
            skLineSegment(sketch, "E10360", {"start": v(71.12, -493.4) * mm, "end": v(72.92, -493.12) * mm});
            skLineSegment(sketch, "E10361", {"start": v(72.92, -493.12) * mm, "end": v(74.72, -492.84) * mm});
            skLineSegment(sketch, "E10362", {"start": v(74.72, -492.84) * mm, "end": v(76.52, -492.54) * mm});
            skLineSegment(sketch, "E10363", {"start": v(76.52, -492.54) * mm, "end": v(78.32, -492.24) * mm});
            skLineSegment(sketch, "E10364", {"start": v(78.32, -492.24) * mm, "end": v(80.11, -491.93) * mm});
            skLineSegment(sketch, "E10365", {"start": v(80.11, -491.93) * mm, "end": v(81.9, -491.61) * mm});
            skLineSegment(sketch, "E10366", {"start": v(81.9, -491.61) * mm, "end": v(83.7, -491.3) * mm});
            skLineSegment(sketch, "E10367", {"start": v(83.7, -491.3) * mm, "end": v(85.5, -490.96) * mm});
            skLineSegment(sketch, "E10368", {"start": v(85.5, -490.96) * mm, "end": v(87.29, -490.62) * mm});
            skLineSegment(sketch, "E10369", {"start": v(87.29, -490.62) * mm, "end": v(89.08, -490.28) * mm});
            skLineSegment(sketch, "E10370", {"start": v(89.08, -490.28) * mm, "end": v(90.87, -489.93) * mm});
            skLineSegment(sketch, "E10371", {"start": v(90.87, -489.93) * mm, "end": v(92.66, -489.57) * mm});
            skLineSegment(sketch, "E10372", {"start": v(92.66, -489.57) * mm, "end": v(94.44, -489.2) * mm});
            skLineSegment(sketch, "E10373", {"start": v(94.44, -489.2) * mm, "end": v(96.23, -488.83) * mm});
            skLineSegment(sketch, "E10374", {"start": v(96.23, -488.83) * mm, "end": v(98.01, -488.46) * mm});
            skLineSegment(sketch, "E10375", {"start": v(98.01, -488.46) * mm, "end": v(99.8, -488.07) * mm});
            skLineSegment(sketch, "E10376", {"start": v(99.8, -488.07) * mm, "end": v(101.58, -487.68) * mm});
            skLineSegment(sketch, "E10377", {"start": v(101.58, -487.68) * mm, "end": v(103.36, -487.29) * mm});
            skLineSegment(sketch, "E10378", {"start": v(103.36, -487.29) * mm, "end": v(105.14, -486.89) * mm});
            skLineSegment(sketch, "E10379", {"start": v(105.14, -486.89) * mm, "end": v(106.91, -486.48) * mm});
            skLineSegment(sketch, "E10380", {"start": v(106.91, -486.48) * mm, "end": v(108.69, -486.07) * mm});
            skLineSegment(sketch, "E10381", {"start": v(108.69, -486.07) * mm, "end": v(110.46, -485.66) * mm});
            skLineSegment(sketch, "E10382", {"start": v(110.46, -485.66) * mm, "end": v(112.23, -485.24) * mm});
            skLineSegment(sketch, "E10383", {"start": v(112.23, -485.24) * mm, "end": v(114, -484.8) * mm});
            skLineSegment(sketch, "E10384", {"start": v(114, -484.8) * mm, "end": v(115.77, -484.38) * mm});
            skLineSegment(sketch, "E10385", {"start": v(115.77, -484.38) * mm, "end": v(117.54, -483.94) * mm});
            skLineSegment(sketch, "E10386", {"start": v(117.54, -483.94) * mm, "end": v(119.3, -483.5) * mm});
            skLineSegment(sketch, "E10387", {"start": v(119.3, -483.5) * mm, "end": v(121.07, -483.06) * mm});
            skLineSegment(sketch, "E10388", {"start": v(121.07, -483.06) * mm, "end": v(122.83, -482.61) * mm});
            skLineSegment(sketch, "E10389", {"start": v(122.83, -482.61) * mm, "end": v(124.58, -482.16) * mm});
            skLineSegment(sketch, "E10390", {"start": v(124.58, -482.16) * mm, "end": v(126.34, -481.7) * mm});
            skLineSegment(sketch, "E10391", {"start": v(126.34, -481.7) * mm, "end": v(128.1, -481.24) * mm});
            skLineSegment(sketch, "E10392", {"start": v(128.1, -481.24) * mm, "end": v(129.85, -480.78) * mm});
            skLineSegment(sketch, "E10393", {"start": v(129.85, -480.78) * mm, "end": v(131.6, -480.3) * mm});
            skLineSegment(sketch, "E10394", {"start": v(131.6, -480.3) * mm, "end": v(133.34, -479.84) * mm});
            skLineSegment(sketch, "E10395", {"start": v(133.34, -479.84) * mm, "end": v(135.09, -479.36) * mm});
            skLineSegment(sketch, "E10396", {"start": v(135.09, -479.36) * mm, "end": v(136.83, -478.88) * mm});
            skLineSegment(sketch, "E10397", {"start": v(136.83, -478.88) * mm, "end": v(138.57, -478.4) * mm});
            skLineSegment(sketch, "E10398", {"start": v(138.57, -478.4) * mm, "end": v(140.3, -477.92) * mm});
            skLineSegment(sketch, "E10399", {"start": v(140.3, -477.92) * mm, "end": v(142.04, -477.43) * mm});
            skLineSegment(sketch, "E10400", {"start": v(142.04, -477.43) * mm, "end": v(143.77, -476.94) * mm});
            skLineSegment(sketch, "E10401", {"start": v(143.77, -476.94) * mm, "end": v(145.5, -476.45) * mm});
            skLineSegment(sketch, "E10402", {"start": v(145.5, -476.45) * mm, "end": v(147.11, -476) * mm});
            skLineSegment(sketch, "E10403", {"start": v(147.11, -476) * mm, "end": v(148.75, -475.55) * mm});
            skLineSegment(sketch, "E10404", {"start": v(148.75, -475.55) * mm, "end": v(150.42, -475.1) * mm});
            skLineSegment(sketch, "E10405", {"start": v(150.42, -475.1) * mm, "end": v(152.1, -474.64) * mm});
            skLineSegment(sketch, "E10406", {"start": v(152.1, -474.64) * mm, "end": v(153.81, -474.18) * mm});
            skLineSegment(sketch, "E10407", {"start": v(153.81, -474.18) * mm, "end": v(155.53, -473.7) * mm});
            skLineSegment(sketch, "E10408", {"start": v(155.53, -473.7) * mm, "end": v(157.26, -473.22) * mm});
            skLineSegment(sketch, "E10409", {"start": v(157.26, -473.22) * mm, "end": v(158.99, -472.71) * mm});
            skLineSegment(sketch, "E10410", {"start": v(158.99, -472.71) * mm, "end": v(160.72, -472.19) * mm});
            skLineSegment(sketch, "E10411", {"start": v(160.72, -472.19) * mm, "end": v(162.45, -471.64) * mm});
            skLineSegment(sketch, "E10412", {"start": v(162.45, -471.64) * mm, "end": v(164.17, -471.07) * mm});
            skLineSegment(sketch, "E10413", {"start": v(164.17, -471.07) * mm, "end": v(165.87, -470.47) * mm});
            skLineSegment(sketch, "E10414", {"start": v(165.87, -470.47) * mm, "end": v(167.56, -469.83) * mm});
            skLineSegment(sketch, "E10415", {"start": v(167.56, -469.83) * mm, "end": v(169.23, -469.16) * mm});
            skLineSegment(sketch, "E10416", {"start": v(169.23, -469.16) * mm, "end": v(170.88, -468.45) * mm});
            skLineSegment(sketch, "E10417", {"start": v(170.88, -468.45) * mm, "end": v(172.5, -467.7) * mm});
            skLineSegment(sketch, "E10418", {"start": v(172.5, -467.7) * mm, "end": v(174.08, -466.9) * mm});
            skLineSegment(sketch, "E10419", {"start": v(174.08, -466.9) * mm, "end": v(175.63, -466.05) * mm});
            skLineSegment(sketch, "E10420", {"start": v(175.63, -466.05) * mm, "end": v(177.13, -465.15) * mm});
            skLineSegment(sketch, "E10421", {"start": v(177.13, -465.15) * mm, "end": v(178.6, -464.2) * mm});
            skLineSegment(sketch, "E10422", {"start": v(178.6, -464.2) * mm, "end": v(180, -463.18) * mm});
            skLineSegment(sketch, "E10423", {"start": v(180, -463.18) * mm, "end": v(181.36, -462.1) * mm});
            skLineSegment(sketch, "E10424", {"start": v(181.36, -462.1) * mm, "end": v(182.66, -460.97) * mm});
            skLineSegment(sketch, "E10425", {"start": v(182.66, -460.97) * mm, "end": v(183.9, -459.76) * mm});
            skLineSegment(sketch, "E10426", {"start": v(183.9, -459.76) * mm, "end": v(185.07, -458.48) * mm});
            skLineSegment(sketch, "E10427", {"start": v(185.07, -458.48) * mm, "end": v(186.17, -457.13) * mm});
            skLineSegment(sketch, "E10428", {"start": v(186.17, -457.13) * mm, "end": v(187.2, -455.7) * mm});
            skLineSegment(sketch, "E10429", {"start": v(187.2, -455.7) * mm, "end": v(187.95, -454.5) * mm});
            skLineSegment(sketch, "E10430", {"start": v(187.95, -454.5) * mm, "end": v(188.63, -453.28) * mm});
            skLineSegment(sketch, "E10431", {"start": v(188.63, -453.28) * mm, "end": v(189.24, -452.03) * mm});
            skLineSegment(sketch, "E10432", {"start": v(189.24, -452.03) * mm, "end": v(189.78, -450.76) * mm});
            skLineSegment(sketch, "E10433", {"start": v(189.78, -450.76) * mm, "end": v(190.25, -449.46) * mm});
            skLineSegment(sketch, "E10434", {"start": v(190.25, -449.46) * mm, "end": v(190.65, -448.14) * mm});
            skLineSegment(sketch, "E10435", {"start": v(190.65, -448.14) * mm, "end": v(190.98, -446.8) * mm});
            skLineSegment(sketch, "E10436", {"start": v(190.98, -446.8) * mm, "end": v(191.25, -445.43) * mm});
            skLineSegment(sketch, "E10437", {"start": v(191.25, -445.43) * mm, "end": v(191.46, -444.05) * mm});
            skLineSegment(sketch, "E10438", {"start": v(191.46, -444.05) * mm, "end": v(191.6, -442.64) * mm});
            skLineSegment(sketch, "E10439", {"start": v(191.6, -442.64) * mm, "end": v(191.68, -441.21) * mm});
            skLineSegment(sketch, "E10440", {"start": v(191.68, -441.21) * mm, "end": v(191.7, -439.77) * mm});
            skLineSegment(sketch, "E10441", {"start": v(191.7, -439.77) * mm, "end": v(191.67, -438.31) * mm});
            skLineSegment(sketch, "E10442", {"start": v(191.67, -438.31) * mm, "end": v(191.59, -436.83) * mm});
            skLineSegment(sketch, "E10443", {"start": v(191.59, -436.83) * mm, "end": v(191.44, -435.34) * mm});
            skLineSegment(sketch, "E10444", {"start": v(191.44, -435.34) * mm, "end": v(191.25, -433.83) * mm});
            skLineSegment(sketch, "E10445", {"start": v(191.25, -433.83) * mm, "end": v(191, -432.31) * mm});
            skLineSegment(sketch, "E10446", {"start": v(191, -432.31) * mm, "end": v(190.71, -430.78) * mm});
            skLineSegment(sketch, "E10447", {"start": v(190.71, -430.78) * mm, "end": v(190.37, -429.23) * mm});
            skLineSegment(sketch, "E10448", {"start": v(190.37, -429.23) * mm, "end": v(189.98, -427.67) * mm});
            skLineSegment(sketch, "E10449", {"start": v(189.98, -427.67) * mm, "end": v(189.55, -426.1) * mm});
            skLineSegment(sketch, "E10450", {"start": v(189.55, -426.1) * mm, "end": v(189.08, -424.52) * mm});
            skLineSegment(sketch, "E10451", {"start": v(189.08, -424.52) * mm, "end": v(188.56, -422.93) * mm});
            skLineSegment(sketch, "E10452", {"start": v(188.56, -422.93) * mm, "end": v(188, -421.34) * mm});
            skLineSegment(sketch, "E10453", {"start": v(188, -421.34) * mm, "end": v(187.41, -419.73) * mm});
            skLineSegment(sketch, "E10454", {"start": v(187.41, -419.73) * mm, "end": v(186.78, -418.12) * mm});
            skLineSegment(sketch, "E10455", {"start": v(186.78, -418.12) * mm, "end": v(186.12, -416.5) * mm});
            skLineSegment(sketch, "E10456", {"start": v(186.12, -416.5) * mm, "end": v(185.42, -414.89) * mm});
            skLineSegment(sketch, "E10457", {"start": v(185.42, -414.89) * mm, "end": v(184.7, -413.26) * mm});
            skLineSegment(sketch, "E10458", {"start": v(184.7, -413.26) * mm, "end": v(183.93, -411.64) * mm});
            skLineSegment(sketch, "E10459", {"start": v(183.93, -411.64) * mm, "end": v(183.15, -410) * mm});
            skLineSegment(sketch, "E10460", {"start": v(183.15, -410) * mm, "end": v(182.33, -408.37) * mm});
            skLineSegment(sketch, "E10461", {"start": v(182.33, -408.37) * mm, "end": v(181.5, -406.74) * mm});
            skLineSegment(sketch, "E10462", {"start": v(181.5, -406.74) * mm, "end": v(180.63, -405.11) * mm});
            skLineSegment(sketch, "E10463", {"start": v(180.63, -405.11) * mm, "end": v(179.74, -403.48) * mm});
            skLineSegment(sketch, "E10464", {"start": v(179.74, -403.48) * mm, "end": v(178.84, -401.85) * mm});
            skLineSegment(sketch, "E10465", {"start": v(178.84, -401.85) * mm, "end": v(177.91, -400.23) * mm});
            skLineSegment(sketch, "E10466", {"start": v(177.91, -400.23) * mm, "end": v(176.97, -398.6) * mm});
            skLineSegment(sketch, "E10467", {"start": v(176.97, -398.6) * mm, "end": v(176.01, -396.99) * mm});
            skLineSegment(sketch, "E10468", {"start": v(176.01, -396.99) * mm, "end": v(175.04, -395.37) * mm});
            skLineSegment(sketch, "E10469", {"start": v(175.04, -395.37) * mm, "end": v(174.06, -393.77) * mm});
            skLineSegment(sketch, "E10470", {"start": v(174.06, -393.77) * mm, "end": v(173.06, -392.17) * mm});
            skLineSegment(sketch, "E10471", {"start": v(173.06, -392.17) * mm, "end": v(172.06, -390.58) * mm});
            skLineSegment(sketch, "E10472", {"start": v(172.06, -390.58) * mm, "end": v(171.04, -389) * mm});
            skLineSegment(sketch, "E10473", {"start": v(171.04, -389) * mm, "end": v(170.03, -387.42) * mm});
            skLineSegment(sketch, "E10474", {"start": v(170.03, -387.42) * mm, "end": v(169, -385.86) * mm});
            skLineSegment(sketch, "E10475", {"start": v(169, -385.86) * mm, "end": v(167.98, -384.3) * mm});
            skLineSegment(sketch, "E10476", {"start": v(167.98, -384.3) * mm, "end": v(166.95, -382.76) * mm});
            skLineSegment(sketch, "E10477", {"start": v(166.95, -382.76) * mm, "end": v(165.92, -381.24) * mm});
            skLineSegment(sketch, "E10478", {"start": v(165.92, -381.24) * mm, "end": v(164.9, -379.72) * mm});
            skLineSegment(sketch, "E10479", {"start": v(164.9, -379.72) * mm, "end": v(163.87, -378.22) * mm});
            skLineSegment(sketch, "E10480", {"start": v(163.87, -378.22) * mm, "end": v(162.86, -376.74) * mm});
            skLineSegment(sketch, "E10481", {"start": v(162.86, -376.74) * mm, "end": v(161.85, -375.27) * mm});
            skLineSegment(sketch, "E10482", {"start": v(161.85, -375.27) * mm, "end": v(160.84, -373.82) * mm});
            skLineSegment(sketch, "E10483", {"start": v(160.84, -373.82) * mm, "end": v(159.85, -372.39) * mm});
            skLineSegment(sketch, "E10484", {"start": v(159.85, -372.39) * mm, "end": v(158.87, -370.98) * mm});
            skLineSegment(sketch, "E10485", {"start": v(158.87, -370.98) * mm, "end": v(157.9, -369.58) * mm});
            skLineSegment(sketch, "E10486", {"start": v(157.9, -369.58) * mm, "end": v(156.95, -368.2) * mm});
            skLineSegment(sketch, "E10487", {"start": v(156.95, -368.2) * mm, "end": v(156.01, -366.85) * mm});
            skLineSegment(sketch, "E10488", {"start": v(156.01, -366.85) * mm, "end": v(155.1, -365.52) * mm});
            skLineSegment(sketch, "E10489", {"start": v(155.1, -365.52) * mm, "end": v(154.2, -364.22) * mm});
            skLineSegment(sketch, "E10490", {"start": v(154.2, -364.22) * mm, "end": v(153.31, -362.93) * mm});
            skLineSegment(sketch, "E10491", {"start": v(153.31, -362.93) * mm, "end": v(152.45, -361.67) * mm});
            skLineSegment(sketch, "E10492", {"start": v(152.45, -361.67) * mm, "end": v(151.62, -360.44) * mm});
            skLineSegment(sketch, "E10493", {"start": v(151.62, -360.44) * mm, "end": v(150.81, -359.23) * mm});
            skLineSegment(sketch, "E10494", {"start": v(150.81, -359.23) * mm, "end": v(150.03, -358.05) * mm});
            skLineSegment(sketch, "E10495", {"start": v(150.03, -358.05) * mm, "end": v(149.28, -356.9) * mm});
            skLineSegment(sketch, "E10496", {"start": v(149.28, -356.9) * mm, "end": v(148.56, -355.78) * mm});
            skLineSegment(sketch, "E10497", {"start": v(148.56, -355.78) * mm, "end": v(147.87, -354.68) * mm});
            skLineSegment(sketch, "E10498", {"start": v(147.87, -354.68) * mm, "end": v(147.21, -353.62) * mm});
            skLineSegment(sketch, "E10499", {"start": v(147.21, -353.62) * mm, "end": v(146.6, -352.59) * mm});
            skLineSegment(sketch, "E10500", {"start": v(146.6, -352.59) * mm, "end": v(145.85, -351.28) * mm});
            skLineSegment(sketch, "E10501", {"start": v(145.85, -351.28) * mm, "end": v(145.1, -349.86) * mm});
            skLineSegment(sketch, "E10502", {"start": v(145.1, -349.86) * mm, "end": v(144.32, -348.34) * mm});
            skLineSegment(sketch, "E10503", {"start": v(144.32, -348.34) * mm, "end": v(143.52, -346.73) * mm});
            skLineSegment(sketch, "E10504", {"start": v(143.52, -346.73) * mm, "end": v(142.7, -345.06) * mm});
            skLineSegment(sketch, "E10505", {"start": v(142.7, -345.06) * mm, "end": v(141.86, -343.33) * mm});
            skLineSegment(sketch, "E10506", {"start": v(141.86, -343.33) * mm, "end": v(141, -341.56) * mm});
            skLineSegment(sketch, "E10507", {"start": v(141, -341.56) * mm, "end": v(140.1, -339.78) * mm});
            skLineSegment(sketch, "E10508", {"start": v(140.1, -339.78) * mm, "end": v(139.19, -338) * mm});
            skLineSegment(sketch, "E10509", {"start": v(139.19, -338) * mm, "end": v(138.24, -336.22) * mm});
            skLineSegment(sketch, "E10510", {"start": v(138.24, -336.22) * mm, "end": v(137.25, -334.48) * mm});
            skLineSegment(sketch, "E10511", {"start": v(137.25, -334.48) * mm, "end": v(136.24, -332.79) * mm});
            skLineSegment(sketch, "E10512", {"start": v(136.24, -332.79) * mm, "end": v(135.19, -331.16) * mm});
            skLineSegment(sketch, "E10513", {"start": v(135.19, -331.16) * mm, "end": v(134.1, -329.6) * mm});
            skLineSegment(sketch, "E10514", {"start": v(134.1, -329.6) * mm, "end": v(132.98, -328.15) * mm});
            skLineSegment(sketch, "E10515", {"start": v(132.98, -328.15) * mm, "end": v(131.8, -326.8) * mm});
            skLineSegment(sketch, "E10516", {"start": v(131.8, -326.8) * mm, "end": v(130.6, -325.6) * mm});
            skLineSegment(sketch, "E10517", {"start": v(130.6, -325.6) * mm, "end": v(129.35, -324.53) * mm});
            skLineSegment(sketch, "E10518", {"start": v(129.35, -324.53) * mm, "end": v(128.06, -323.63) * mm});
            skLineSegment(sketch, "E10519", {"start": v(128.06, -323.63) * mm, "end": v(126.71, -322.9) * mm});
            skLineSegment(sketch, "E10520", {"start": v(126.71, -322.9) * mm, "end": v(125.22, -322.32) * mm});
            skLineSegment(sketch, "E10521", {"start": v(125.22, -322.32) * mm, "end": v(123.62, -321.87) * mm});
            skLineSegment(sketch, "E10522", {"start": v(123.62, -321.87) * mm, "end": v(121.93, -321.55) * mm});
            skLineSegment(sketch, "E10523", {"start": v(121.93, -321.55) * mm, "end": v(120.17, -321.34) * mm});
            skLineSegment(sketch, "E10524", {"start": v(120.17, -321.34) * mm, "end": v(118.34, -321.22) * mm});
            skLineSegment(sketch, "E10525", {"start": v(118.34, -321.22) * mm, "end": v(116.47, -321.18) * mm});
            skLineSegment(sketch, "E10526", {"start": v(116.47, -321.18) * mm, "end": v(114.58, -321.2) * mm});
            skLineSegment(sketch, "E10527", {"start": v(114.58, -321.2) * mm, "end": v(112.68, -321.27) * mm});
            skLineSegment(sketch, "E10528", {"start": v(112.68, -321.27) * mm, "end": v(110.79, -321.37) * mm});
            skLineSegment(sketch, "E10529", {"start": v(110.79, -321.37) * mm, "end": v(108.92, -321.49) * mm});
            skLineSegment(sketch, "E10530", {"start": v(108.92, -321.49) * mm, "end": v(107.1, -321.6) * mm});
            skLineSegment(sketch, "E10531", {"start": v(107.1, -321.6) * mm, "end": v(105.34, -321.7) * mm});
            skLineSegment(sketch, "E10532", {"start": v(105.34, -321.7) * mm, "end": v(103.65, -321.78) * mm});
            skLineSegment(sketch, "E10533", {"start": v(103.65, -321.78) * mm, "end": v(102.05, -321.8) * mm});
            skLineSegment(sketch, "E10534", {"start": v(102.05, -321.8) * mm, "end": v(-57.26, -321.8) * mm});
            skLineSegment(sketch, "E10535", {"start": v(-57.26, -321.8) * mm, "end": v(-59.05, -321.91) * mm});
            skLineSegment(sketch, "E10536", {"start": v(-59.05, -321.91) * mm, "end": v(-60.82, -322.1) * mm});
            skLineSegment(sketch, "E10537", {"start": v(-60.82, -322.1) * mm, "end": v(-62.58, -322.39) * mm});
            skLineSegment(sketch, "E10538", {"start": v(-62.58, -322.39) * mm, "end": v(-64.32, -322.76) * mm});
            skLineSegment(sketch, "E10539", {"start": v(-64.32, -322.76) * mm, "end": v(-66.03, -323.2) * mm});
            skLineSegment(sketch, "E10540", {"start": v(-66.03, -323.2) * mm, "end": v(-67.73, -323.72) * mm});
            skLineSegment(sketch, "E10541", {"start": v(-67.73, -323.72) * mm, "end": v(-69.42, -324.3) * mm});
            skLineSegment(sketch, "E10542", {"start": v(-69.42, -324.3) * mm, "end": v(-71.09, -324.95) * mm});
            skLineSegment(sketch, "E10543", {"start": v(-71.09, -324.95) * mm, "end": v(-72.74, -325.66) * mm});
            skLineSegment(sketch, "E10544", {"start": v(-72.74, -325.66) * mm, "end": v(-74.38, -326.42) * mm});
            skLineSegment(sketch, "E10545", {"start": v(-74.38, -326.42) * mm, "end": v(-76, -327.23) * mm});
            skLineSegment(sketch, "E10546", {"start": v(-76, -327.23) * mm, "end": v(-77.62, -328.09) * mm});
            skLineSegment(sketch, "E10547", {"start": v(-77.62, -328.09) * mm, "end": v(-79.22, -328.98) * mm});
            skLineSegment(sketch, "E10548", {"start": v(-79.22, -328.98) * mm, "end": v(-80.8, -329.9) * mm});
            skLineSegment(sketch, "E10549", {"start": v(-80.8, -329.9) * mm, "end": v(-82.39, -330.87) * mm});
            skLineSegment(sketch, "E10550", {"start": v(-82.39, -330.87) * mm, "end": v(-83.95, -331.85) * mm});
            skLineSegment(sketch, "E10551", {"start": v(-83.95, -331.85) * mm, "end": v(-85.51, -332.85) * mm});
            skLineSegment(sketch, "E10552", {"start": v(-85.51, -332.85) * mm, "end": v(-87.06, -333.86) * mm});
            skLineSegment(sketch, "E10553", {"start": v(-87.06, -333.86) * mm, "end": v(-88.6, -334.88) * mm});
            skLineSegment(sketch, "E10554", {"start": v(-88.6, -334.88) * mm, "end": v(-90.13, -335.9) * mm});
            skLineSegment(sketch, "E10555", {"start": v(-90.13, -335.9) * mm, "end": v(-91.66, -336.94) * mm});
            skLineSegment(sketch, "E10556", {"start": v(-91.66, -336.94) * mm, "end": v(-93.18, -337.96) * mm});
            skLineSegment(sketch, "E10557", {"start": v(-93.18, -337.96) * mm, "end": v(-94.7, -338.97) * mm});
            skLineSegment(sketch, "E10558", {"start": v(-94.7, -338.97) * mm, "end": v(-96.2, -339.97) * mm});
            skLineSegment(sketch, "E10559", {"start": v(-96.2, -339.97) * mm, "end": v(-97.7, -340.94) * mm});
            skLineSegment(sketch, "E10560", {"start": v(-97.7, -340.94) * mm, "end": v(-99.2, -341.9) * mm});
            skLineSegment(sketch, "E10561", {"start": v(-99.2, -341.9) * mm, "end": v(-100.7, -342.81) * mm});
            skLineSegment(sketch, "E10562", {"start": v(-100.7, -342.81) * mm, "end": v(-102.16, -343.7) * mm});
            skLineSegment(sketch, "E10563", {"start": v(-102.16, -343.7) * mm, "end": v(-103.64, -344.57) * mm});
            skLineSegment(sketch, "E10564", {"start": v(-103.64, -344.57) * mm, "end": v(-105.12, -345.45) * mm});
            skLineSegment(sketch, "E10565", {"start": v(-105.12, -345.45) * mm, "end": v(-106.61, -346.32) * mm});
            skLineSegment(sketch, "E10566", {"start": v(-106.61, -346.32) * mm, "end": v(-108.12, -347.2) * mm});
            skLineSegment(sketch, "E10567", {"start": v(-108.12, -347.2) * mm, "end": v(-109.63, -348.08) * mm});
            skLineSegment(sketch, "E10568", {"start": v(-109.63, -348.08) * mm, "end": v(-111.15, -348.96) * mm});
            skLineSegment(sketch, "E10569", {"start": v(-111.15, -348.96) * mm, "end": v(-112.68, -349.84) * mm});
            skLineSegment(sketch, "E10570", {"start": v(-112.68, -349.84) * mm, "end": v(-114.22, -350.72) * mm});
            skLineSegment(sketch, "E10571", {"start": v(-114.22, -350.72) * mm, "end": v(-115.76, -351.6) * mm});
            skLineSegment(sketch, "E10572", {"start": v(-115.76, -351.6) * mm, "end": v(-117.31, -352.48) * mm});
            skLineSegment(sketch, "E10573", {"start": v(-117.31, -352.48) * mm, "end": v(-118.87, -353.36) * mm});
            skLineSegment(sketch, "E10574", {"start": v(-118.87, -353.36) * mm, "end": v(-120.44, -354.24) * mm});
            skLineSegment(sketch, "E10575", {"start": v(-120.44, -354.24) * mm, "end": v(-122.01, -355.13) * mm});
            skLineSegment(sketch, "E10576", {"start": v(-122.01, -355.13) * mm, "end": v(-123.59, -356.01) * mm});
            skLineSegment(sketch, "E10577", {"start": v(-123.59, -356.01) * mm, "end": v(-125.17, -356.9) * mm});
            skLineSegment(sketch, "E10578", {"start": v(-125.17, -356.9) * mm, "end": v(-126.76, -357.79) * mm});
            skLineSegment(sketch, "E10579", {"start": v(-126.76, -357.79) * mm, "end": v(-128.35, -358.68) * mm});
            skLineSegment(sketch, "E10580", {"start": v(-128.35, -358.68) * mm, "end": v(-129.95, -359.57) * mm});
            skLineSegment(sketch, "E10581", {"start": v(-129.95, -359.57) * mm, "end": v(-131.55, -360.47) * mm});
            skLineSegment(sketch, "E10582", {"start": v(-131.55, -360.47) * mm, "end": v(-133.15, -361.36) * mm});
            skLineSegment(sketch, "E10583", {"start": v(-133.15, -361.36) * mm, "end": v(-134.75, -362.26) * mm});
            skLineSegment(sketch, "E10584", {"start": v(-134.75, -362.26) * mm, "end": v(-136.36, -363.16) * mm});
            skLineSegment(sketch, "E10585", {"start": v(-136.36, -363.16) * mm, "end": v(-137.97, -364.07) * mm});
            skLineSegment(sketch, "E10586", {"start": v(-137.97, -364.07) * mm, "end": v(-139.58, -364.97) * mm});
            skLineSegment(sketch, "E10587", {"start": v(-139.58, -364.97) * mm, "end": v(-141.2, -365.88) * mm});
            skLineSegment(sketch, "E10588", {"start": v(-141.2, -365.88) * mm, "end": v(-142.8, -366.8) * mm});
            skLineSegment(sketch, "E10589", {"start": v(-142.8, -366.8) * mm, "end": v(-144.41, -367.7) * mm});
            skLineSegment(sketch, "E10590", {"start": v(-144.41, -367.7) * mm, "end": v(-146.03, -368.62) * mm});
            skLineSegment(sketch, "E10591", {"start": v(-146.03, -368.62) * mm, "end": v(-147.64, -369.54) * mm});
            skLineSegment(sketch, "E10592", {"start": v(-147.64, -369.54) * mm, "end": v(-149.25, -370.47) * mm});
            skLineSegment(sketch, "E10593", {"start": v(-149.25, -370.47) * mm, "end": v(-150.86, -371.4) * mm});
            skLineSegment(sketch, "E10594", {"start": v(-150.86, -371.4) * mm, "end": v(-152.46, -372.33) * mm});
            skLineSegment(sketch, "E10595", {"start": v(-152.46, -372.33) * mm, "end": v(-154.07, -373.26) * mm});
            skLineSegment(sketch, "E10596", {"start": v(-154.07, -373.26) * mm, "end": v(-155.67, -374.2) * mm});
            skLineSegment(sketch, "E10597", {"start": v(-155.67, -374.2) * mm, "end": v(-157.27, -375.14) * mm});
            skLineSegment(sketch, "E10598", {"start": v(-157.27, -375.14) * mm, "end": v(-158.86, -376.09) * mm});
            skLineSegment(sketch, "E10599", {"start": v(-158.86, -376.09) * mm, "end": v(-160.45, -377.04) * mm});
            skLineSegment(sketch, "E10600", {"start": v(-160.45, -377.04) * mm, "end": v(-162.04, -378) * mm});
            skLineSegment(sketch, "E10601", {"start": v(-162.04, -378) * mm, "end": v(-163.62, -378.96) * mm});
            skLineSegment(sketch, "E10602", {"start": v(-163.62, -378.96) * mm, "end": v(-165.2, -379.92) * mm});
            skLineSegment(sketch, "E10603", {"start": v(-165.2, -379.92) * mm, "end": v(-166.77, -380.89) * mm});
            skLineSegment(sketch, "E10604", {"start": v(-166.77, -380.89) * mm, "end": v(-168.33, -381.86) * mm});
            skLineSegment(sketch, "E10605", {"start": v(-168.33, -381.86) * mm, "end": v(-169.9, -382.84) * mm});
            skLineSegment(sketch, "E10606", {"start": v(-169.9, -382.84) * mm, "end": v(-171.44, -383.83) * mm});
            skLineSegment(sketch, "E10607", {"start": v(-171.44, -383.83) * mm, "end": v(-172.99, -384.82) * mm});
            skLineSegment(sketch, "E10608", {"start": v(-172.99, -384.82) * mm, "end": v(-174.52, -385.81) * mm});
            skLineSegment(sketch, "E10609", {"start": v(-174.52, -385.81) * mm, "end": v(-176.05, -386.81) * mm});
            skLineSegment(sketch, "E10610", {"start": v(-176.05, -386.81) * mm, "end": v(-177.57, -387.82) * mm});
            skLineSegment(sketch, "E10611", {"start": v(-177.57, -387.82) * mm, "end": v(-179.08, -388.83) * mm});
            skLineSegment(sketch, "E10612", {"start": v(-179.08, -388.83) * mm, "end": v(-180.58, -389.85) * mm});
            skLineSegment(sketch, "E10613", {"start": v(-180.58, -389.85) * mm, "end": v(-182.07, -390.87) * mm});
            skLineSegment(sketch, "E10614", {"start": v(-182.07, -390.87) * mm, "end": v(-183.55, -391.9) * mm});
            skLineSegment(sketch, "E10615", {"start": v(-183.55, -391.9) * mm, "end": v(-185.02, -392.93) * mm});
            skLineSegment(sketch, "E10616", {"start": v(-185.02, -392.93) * mm, "end": v(-186.48, -393.98) * mm});
            skLineSegment(sketch, "E10617", {"start": v(-186.48, -393.98) * mm, "end": v(-187.93, -395.02) * mm});
            skLineSegment(sketch, "E10618", {"start": v(-187.93, -395.02) * mm, "end": v(-189.37, -396.08) * mm});
            skLineSegment(sketch, "E10619", {"start": v(-189.37, -396.08) * mm, "end": v(-190.8, -397.14) * mm});
            skLineSegment(sketch, "E10620", {"start": v(-190.8, -397.14) * mm, "end": v(-192.2, -398.2) * mm});
            skLineSegment(sketch, "E10621", {"start": v(-192.2, -398.2) * mm, "end": v(-193.6, -399.28) * mm});
            skLineSegment(sketch, "E10622", {"start": v(-193.6, -399.28) * mm, "end": v(-194.98, -400.37) * mm});
            skLineSegment(sketch, "E10623", {"start": v(-194.98, -400.37) * mm, "end": v(-196.35, -401.46) * mm});
            skLineSegment(sketch, "E10624", {"start": v(-196.35, -401.46) * mm, "end": v(-197.7, -402.55) * mm});
            skLineSegment(sketch, "E10625", {"start": v(-197.7, -402.55) * mm, "end": v(-199.05, -403.66) * mm});
            skLineSegment(sketch, "E10626", {"start": v(-199.05, -403.66) * mm, "end": v(-200.37, -404.77) * mm});
            skLineSegment(sketch, "E10627", {"start": v(-200.37, -404.77) * mm, "end": v(-201.68, -405.9) * mm});
            skLineSegment(sketch, "E10628", {"start": v(-201.68, -405.9) * mm, "end": v(-202.98, -407.02) * mm});
            skLineSegment(sketch, "E10629", {"start": v(-202.98, -407.02) * mm, "end": v(-204.25, -408.16) * mm});
            skLineSegment(sketch, "E10630", {"start": v(-204.25, -408.16) * mm, "end": v(-205.51, -409.3) * mm});
            skLineSegment(sketch, "E10631", {"start": v(-164.06, -323.62) * mm, "end": v(-165.46, -323.06) * mm});
            skLineSegment(sketch, "E10632", {"start": v(-165.46, -323.06) * mm, "end": v(-166.9, -322.55) * mm});
            skLineSegment(sketch, "E10633", {"start": v(-166.9, -322.55) * mm, "end": v(-168.37, -322.07) * mm});
            skLineSegment(sketch, "E10634", {"start": v(-168.37, -322.07) * mm, "end": v(-169.88, -321.63) * mm});
            skLineSegment(sketch, "E10635", {"start": v(-169.88, -321.63) * mm, "end": v(-171.42, -321.23) * mm});
            skLineSegment(sketch, "E10636", {"start": v(-171.42, -321.23) * mm, "end": v(-173, -320.86) * mm});
            skLineSegment(sketch, "E10637", {"start": v(-173, -320.86) * mm, "end": v(-174.62, -320.53) * mm});
            skLineSegment(sketch, "E10638", {"start": v(-174.62, -320.53) * mm, "end": v(-176.27, -320.23) * mm});
            skLineSegment(sketch, "E10639", {"start": v(-176.27, -320.23) * mm, "end": v(-177.95, -319.96) * mm});
            skLineSegment(sketch, "E10640", {"start": v(-177.95, -319.96) * mm, "end": v(-179.65, -319.72) * mm});
            skLineSegment(sketch, "E10641", {"start": v(-179.65, -319.72) * mm, "end": v(-181.38, -319.5) * mm});
            skLineSegment(sketch, "E10642", {"start": v(-181.38, -319.5) * mm, "end": v(-183.14, -319.33) * mm});
            skLineSegment(sketch, "E10643", {"start": v(-183.14, -319.33) * mm, "end": v(-184.92, -319.17) * mm});
            skLineSegment(sketch, "E10644", {"start": v(-184.92, -319.17) * mm, "end": v(-186.72, -319.04) * mm});
            skLineSegment(sketch, "E10645", {"start": v(-186.72, -319.04) * mm, "end": v(-188.55, -318.94) * mm});
            skLineSegment(sketch, "E10646", {"start": v(-188.55, -318.94) * mm, "end": v(-190.4, -318.86) * mm});
            skLineSegment(sketch, "E10647", {"start": v(-190.4, -318.86) * mm, "end": v(-192.25, -318.8) * mm});
            skLineSegment(sketch, "E10648", {"start": v(-192.25, -318.8) * mm, "end": v(-194.13, -318.76) * mm});
            skLineSegment(sketch, "E10649", {"start": v(-194.13, -318.76) * mm, "end": v(-196.02, -318.75) * mm});
            skLineSegment(sketch, "E10650", {"start": v(-196.02, -318.75) * mm, "end": v(-197.92, -318.75) * mm});
            skLineSegment(sketch, "E10651", {"start": v(-197.92, -318.75) * mm, "end": v(-199.83, -318.77) * mm});
            skLineSegment(sketch, "E10652", {"start": v(-199.83, -318.77) * mm, "end": v(-201.76, -318.8) * mm});
            skLineSegment(sketch, "E10653", {"start": v(-201.76, -318.8) * mm, "end": v(-203.69, -318.86) * mm});
            skLineSegment(sketch, "E10654", {"start": v(-203.69, -318.86) * mm, "end": v(-205.62, -318.92) * mm});
            skLineSegment(sketch, "E10655", {"start": v(-205.62, -318.92) * mm, "end": v(-207.57, -319) * mm});
            skLineSegment(sketch, "E10656", {"start": v(-207.57, -319) * mm, "end": v(-209.51, -319.1) * mm});
            skLineSegment(sketch, "E10657", {"start": v(-209.51, -319.1) * mm, "end": v(-211.46, -319.2) * mm});
            skLineSegment(sketch, "E10658", {"start": v(-211.46, -319.2) * mm, "end": v(-213.4, -319.3) * mm});
            skLineSegment(sketch, "E10659", {"start": v(-213.4, -319.3) * mm, "end": v(-215.35, -319.42) * mm});
            skLineSegment(sketch, "E10660", {"start": v(-215.35, -319.42) * mm, "end": v(-217.3, -319.55) * mm});
            skLineSegment(sketch, "E10661", {"start": v(-217.3, -319.55) * mm, "end": v(-219.23, -319.68) * mm});
            skLineSegment(sketch, "E10662", {"start": v(-219.23, -319.68) * mm, "end": v(-221.16, -319.82) * mm});
            skLineSegment(sketch, "E10663", {"start": v(-221.16, -319.82) * mm, "end": v(-223.09, -319.96) * mm});
            skLineSegment(sketch, "E10664", {"start": v(-223.09, -319.96) * mm, "end": v(-225, -320.1) * mm});
            skLineSegment(sketch, "E10665", {"start": v(-225, -320.1) * mm, "end": v(-226.9, -320.25) * mm});
            skLineSegment(sketch, "E10666", {"start": v(-226.9, -320.25) * mm, "end": v(-228.8, -320.4) * mm});
            skLineSegment(sketch, "E10667", {"start": v(-228.8, -320.4) * mm, "end": v(-230.67, -320.54) * mm});
            skLineSegment(sketch, "E10668", {"start": v(-230.67, -320.54) * mm, "end": v(-232.53, -320.68) * mm});
            skLineSegment(sketch, "E10669", {"start": v(-232.53, -320.68) * mm, "end": v(-234.38, -320.82) * mm});
            skLineSegment(sketch, "E10670", {"start": v(-234.38, -320.82) * mm, "end": v(-236.2, -320.96) * mm});
            skLineSegment(sketch, "E10671", {"start": v(-236.2, -320.96) * mm, "end": v(-238, -321.08) * mm});
            skLineSegment(sketch, "E10672", {"start": v(-238, -321.08) * mm, "end": v(-239.79, -321.2) * mm});
            skLineSegment(sketch, "E10673", {"start": v(-239.79, -321.2) * mm, "end": v(-241.55, -321.32) * mm});
            skLineSegment(sketch, "E10674", {"start": v(-241.55, -321.32) * mm, "end": v(-243.28, -321.43) * mm});
            skLineSegment(sketch, "E10675", {"start": v(-243.28, -321.43) * mm, "end": v(-244.99, -321.52) * mm});
            skLineSegment(sketch, "E10676", {"start": v(-244.99, -321.52) * mm, "end": v(-246.67, -321.6) * mm});
            skLineSegment(sketch, "E10677", {"start": v(-246.67, -321.6) * mm, "end": v(-248.32, -321.68) * mm});
            skLineSegment(sketch, "E10678", {"start": v(-248.32, -321.68) * mm, "end": v(-249.93, -321.73) * mm});
            skLineSegment(sketch, "E10679", {"start": v(-249.93, -321.73) * mm, "end": v(-251.52, -321.77) * mm});
            skLineSegment(sketch, "E10680", {"start": v(-251.52, -321.77) * mm, "end": v(-253.07, -321.8) * mm});
            skLineSegment(sketch, "E10681", {"start": v(-253.07, -321.8) * mm, "end": v(-254.58, -321.8) * mm});
            skLineSegment(sketch, "E10682", {"start": v(-254.58, -321.8) * mm, "end": v(-256.18, -321.79) * mm});
            skLineSegment(sketch, "E10683", {"start": v(-256.18, -321.79) * mm, "end": v(-257.87, -321.72) * mm});
            skLineSegment(sketch, "E10684", {"start": v(-257.87, -321.72) * mm, "end": v(-259.62, -321.63) * mm});
            skLineSegment(sketch, "E10685", {"start": v(-259.62, -321.63) * mm, "end": v(-261.43, -321.52) * mm});
            skLineSegment(sketch, "E10686", {"start": v(-261.43, -321.52) * mm, "end": v(-263.28, -321.42) * mm});
            skLineSegment(sketch, "E10687", {"start": v(-263.28, -321.42) * mm, "end": v(-265.17, -321.32) * mm});
            skLineSegment(sketch, "E10688", {"start": v(-265.17, -321.32) * mm, "end": v(-267.07, -321.25) * mm});
            skLineSegment(sketch, "E10689", {"start": v(-267.07, -321.25) * mm, "end": v(-268.99, -321.21) * mm});
            skLineSegment(sketch, "E10690", {"start": v(-268.99, -321.21) * mm, "end": v(-270.89, -321.23) * mm});
            skLineSegment(sketch, "E10691", {"start": v(-270.89, -321.23) * mm, "end": v(-272.77, -321.3) * mm});
            skLineSegment(sketch, "E10692", {"start": v(-272.77, -321.3) * mm, "end": v(-274.62, -321.46) * mm});
            skLineSegment(sketch, "E10693", {"start": v(-274.62, -321.46) * mm, "end": v(-276.43, -321.7) * mm});
            skLineSegment(sketch, "E10694", {"start": v(-276.43, -321.7) * mm, "end": v(-278.17, -322.05) * mm});
            skLineSegment(sketch, "E10695", {"start": v(-278.17, -322.05) * mm, "end": v(-279.85, -322.51) * mm});
            skLineSegment(sketch, "E10696", {"start": v(-279.85, -322.51) * mm, "end": v(-281.44, -323.1) * mm});
            skLineSegment(sketch, "E10697", {"start": v(-281.44, -323.1) * mm, "end": v(-282.93, -323.83) * mm});
            skLineSegment(sketch, "E10698", {"start": v(-282.93, -323.83) * mm, "end": v(-284.31, -324.71) * mm});
            skLineSegment(sketch, "E10699", {"start": v(-284.31, -324.71) * mm, "end": v(-285.15, -325.34) * mm});
            skLineSegment(sketch, "E10700", {"start": v(-285.15, -325.34) * mm, "end": v(-286, -326) * mm});
            skLineSegment(sketch, "E10701", {"start": v(-286, -326) * mm, "end": v(-286.85, -326.7) * mm});
            skLineSegment(sketch, "E10702", {"start": v(-286.85, -326.7) * mm, "end": v(-287.7, -327.43) * mm});
            skLineSegment(sketch, "E10703", {"start": v(-287.7, -327.43) * mm, "end": v(-288.58, -328.2) * mm});
            skLineSegment(sketch, "E10704", {"start": v(-288.58, -328.2) * mm, "end": v(-289.44, -329) * mm});
            skLineSegment(sketch, "E10705", {"start": v(-289.44, -329) * mm, "end": v(-290.32, -329.85) * mm});
            skLineSegment(sketch, "E10706", {"start": v(-290.32, -329.85) * mm, "end": v(-291.2, -330.71) * mm});
            skLineSegment(sketch, "E10707", {"start": v(-291.2, -330.71) * mm, "end": v(-292.07, -331.61) * mm});
            skLineSegment(sketch, "E10708", {"start": v(-292.07, -331.61) * mm, "end": v(-292.94, -332.54) * mm});
            skLineSegment(sketch, "E10709", {"start": v(-292.94, -332.54) * mm, "end": v(-293.82, -333.5) * mm});
            skLineSegment(sketch, "E10710", {"start": v(-293.82, -333.5) * mm, "end": v(-294.7, -334.48) * mm});
            skLineSegment(sketch, "E10711", {"start": v(-294.7, -334.48) * mm, "end": v(-295.56, -335.48) * mm});
            skLineSegment(sketch, "E10712", {"start": v(-295.56, -335.48) * mm, "end": v(-296.42, -336.51) * mm});
            skLineSegment(sketch, "E10713", {"start": v(-296.42, -336.51) * mm, "end": v(-297.28, -337.57) * mm});
            skLineSegment(sketch, "E10714", {"start": v(-297.28, -337.57) * mm, "end": v(-298.13, -338.64) * mm});
            skLineSegment(sketch, "E10715", {"start": v(-298.13, -338.64) * mm, "end": v(-298.97, -339.74) * mm});
            skLineSegment(sketch, "E10716", {"start": v(-298.97, -339.74) * mm, "end": v(-299.8, -340.86) * mm});
            skLineSegment(sketch, "E10717", {"start": v(-299.8, -340.86) * mm, "end": v(-300.63, -342) * mm});
            skLineSegment(sketch, "E10718", {"start": v(-300.63, -342) * mm, "end": v(-301.44, -343.14) * mm});
            skLineSegment(sketch, "E10719", {"start": v(-301.44, -343.14) * mm, "end": v(-302.23, -344.3) * mm});
            skLineSegment(sketch, "E10720", {"start": v(-302.23, -344.3) * mm, "end": v(-303.02, -345.5) * mm});
            skLineSegment(sketch, "E10721", {"start": v(-303.02, -345.5) * mm, "end": v(-303.79, -346.69) * mm});
            skLineSegment(sketch, "E10722", {"start": v(-303.79, -346.69) * mm, "end": v(-304.54, -347.9) * mm});
            skLineSegment(sketch, "E10723", {"start": v(-304.54, -347.9) * mm, "end": v(-305.27, -349.11) * mm});
            skLineSegment(sketch, "E10724", {"start": v(-305.27, -349.11) * mm, "end": v(-305.99, -350.34) * mm});
            skLineSegment(sketch, "E10725", {"start": v(-305.99, -350.34) * mm, "end": v(-306.68, -351.58) * mm});
            skLineSegment(sketch, "E10726", {"start": v(-306.68, -351.58) * mm, "end": v(-307.36, -352.82) * mm});
            skLineSegment(sketch, "E10727", {"start": v(-307.36, -352.82) * mm, "end": v(-308.01, -354.08) * mm});
            skLineSegment(sketch, "E10728", {"start": v(-308.01, -354.08) * mm, "end": v(-308.64, -355.33) * mm});
            skLineSegment(sketch, "E10729", {"start": v(-308.64, -355.33) * mm, "end": v(-309.25, -356.6) * mm});
            skLineSegment(sketch, "E10730", {"start": v(-309.25, -356.6) * mm, "end": v(-309.83, -357.86) * mm});
            skLineSegment(sketch, "E10731", {"start": v(-309.83, -357.86) * mm, "end": v(-310.38, -359.12) * mm});
            skLineSegment(sketch, "E10732", {"start": v(-310.38, -359.12) * mm, "end": v(-310.9, -360.39) * mm});
            skLineSegment(sketch, "E10733", {"start": v(-310.9, -360.39) * mm, "end": v(-311.4, -361.65) * mm});
            skLineSegment(sketch, "E10734", {"start": v(-311.4, -361.65) * mm, "end": v(-311.87, -362.92) * mm});
            skLineSegment(sketch, "E10735", {"start": v(-311.87, -362.92) * mm, "end": v(-312.3, -364.18) * mm});
            skLineSegment(sketch, "E10736", {"start": v(-312.3, -364.18) * mm, "end": v(-312.7, -365.43) * mm});
            skLineSegment(sketch, "E10737", {"start": v(-312.7, -365.43) * mm, "end": v(-313.08, -366.68) * mm});
            skLineSegment(sketch, "E10738", {"start": v(-313.08, -366.68) * mm, "end": v(-313.41, -367.93) * mm});
            skLineSegment(sketch, "E10739", {"start": v(-313.41, -367.93) * mm, "end": v(-313.71, -369.16) * mm});
            skLineSegment(sketch, "E10740", {"start": v(-313.71, -369.16) * mm, "end": v(-313.97, -370.39) * mm});
            skLineSegment(sketch, "E10741", {"start": v(-313.97, -370.39) * mm, "end": v(-314.2, -371.6) * mm});
            skLineSegment(sketch, "E10742", {"start": v(-314.2, -371.6) * mm, "end": v(-314.38, -372.8) * mm});
            skLineSegment(sketch, "E10743", {"start": v(-314.38, -372.8) * mm, "end": v(-314.52, -374) * mm});
            skLineSegment(sketch, "E10744", {"start": v(-314.52, -374) * mm, "end": v(-314.63, -375.18) * mm});
            skLineSegment(sketch, "E10745", {"start": v(-314.63, -375.18) * mm, "end": v(-314.69, -376.34) * mm});
            skLineSegment(sketch, "E10746", {"start": v(-314.69, -376.34) * mm, "end": v(-314.7, -377.5) * mm});
            skLineSegment(sketch, "E10747", {"start": v(-314.7, -377.5) * mm, "end": v(-314.67, -378.62) * mm});
            skLineSegment(sketch, "E10748", {"start": v(-314.67, -378.62) * mm, "end": v(-314.6, -379.73) * mm});
            skLineSegment(sketch, "E10749", {"start": v(-314.6, -379.73) * mm, "end": v(-314.48, -380.83) * mm});
            skLineSegment(sketch, "E10750", {"start": v(-314.48, -380.83) * mm, "end": v(-314.3, -381.9) * mm});
            skLineSegment(sketch, "E10751", {"start": v(-314.3, -381.9) * mm, "end": v(-314.08, -382.95) * mm});
            skLineSegment(sketch, "E10752", {"start": v(-314.08, -382.95) * mm, "end": v(-313.81, -383.97) * mm});
            skLineSegment(sketch, "E10753", {"start": v(-313.81, -383.97) * mm, "end": v(-313.49, -384.97) * mm});
            skLineSegment(sketch, "E10754", {"start": v(-313.49, -384.97) * mm, "end": v(-313.11, -385.95) * mm});
            skLineSegment(sketch, "E10755", {"start": v(-313.11, -385.95) * mm, "end": v(-312.68, -386.9) * mm});
            skLineSegment(sketch, "E10756", {"start": v(-312.68, -386.9) * mm, "end": v(-312.2, -387.82) * mm});
            skLineSegment(sketch, "E10757", {"start": v(-312.2, -387.82) * mm, "end": v(-311.65, -388.71) * mm});
            skLineSegment(sketch, "E10758", {"start": v(-311.65, -388.71) * mm, "end": v(-311.05, -389.57) * mm});
            skLineSegment(sketch, "E10759", {"start": v(-311.05, -389.57) * mm, "end": v(-310.4, -390.4) * mm});
            skLineSegment(sketch, "E10760", {"start": v(-310.4, -390.4) * mm, "end": v(-309.68, -391.2) * mm});
            skLineSegment(sketch, "E10761", {"start": v(-309.68, -391.2) * mm, "end": v(-308.9, -391.96) * mm});
            skLineSegment(sketch, "E10762", {"start": v(-308.9, -391.96) * mm, "end": v(-308.05, -392.69) * mm});
            skLineSegment(sketch, "E10763", {"start": v(-308.05, -392.69) * mm, "end": v(-307.15, -393.38) * mm});
            skLineSegment(sketch, "E10764", {"start": v(-307.15, -393.38) * mm, "end": v(-306.18, -394.04) * mm});
            skLineSegment(sketch, "E10765", {"start": v(-306.18, -394.04) * mm, "end": v(-305.14, -394.65) * mm});
            skLineSegment(sketch, "E10766", {"start": v(-305.14, -394.65) * mm, "end": v(-304.04, -395.23) * mm});
            skLineSegment(sketch, "E10767", {"start": v(-304.04, -395.23) * mm, "end": v(-302.87, -395.76) * mm});
            skLineSegment(sketch, "E10768", {"start": v(-302.87, -395.76) * mm, "end": v(-301.63, -396.25) * mm});
            skLineSegment(sketch, "E10769", {"start": v(-301.63, -396.25) * mm, "end": v(-300.32, -396.7) * mm});
            skLineSegment(sketch, "E10770", {"start": v(-300.32, -396.7) * mm, "end": v(-298.94, -397.1) * mm});
            skLineSegment(sketch, "E10771", {"start": v(-298.94, -397.1) * mm, "end": v(-297.48, -397.46) * mm});
            skLineSegment(sketch, "E10772", {"start": v(-297.48, -397.46) * mm, "end": v(-295.95, -397.78) * mm});
            skLineSegment(sketch, "E10773", {"start": v(-295.95, -397.78) * mm, "end": v(-294.35, -398.04) * mm});
            skLineSegment(sketch, "E10774", {"start": v(-294.35, -398.04) * mm, "end": v(-292.67, -398.25) * mm});
            skLineSegment(sketch, "E10775", {"start": v(-292.67, -398.25) * mm, "end": v(-290.92, -398.42) * mm});
            skLineSegment(sketch, "E10776", {"start": v(-290.92, -398.42) * mm, "end": v(-289.08, -398.53) * mm});
            skLineSegment(sketch, "E10777", {"start": v(-289.08, -398.53) * mm, "end": v(-287.17, -398.59) * mm});
            skLineSegment(sketch, "E10778", {"start": v(-287.17, -398.59) * mm, "end": v(-285.61, -398.57) * mm});
            skLineSegment(sketch, "E10779", {"start": v(-285.61, -398.57) * mm, "end": v(-284.05, -398.48) * mm});
            skLineSegment(sketch, "E10780", {"start": v(-284.05, -398.48) * mm, "end": v(-282.47, -398.3) * mm});
            skLineSegment(sketch, "E10781", {"start": v(-282.47, -398.3) * mm, "end": v(-280.89, -398.06) * mm});
            skLineSegment(sketch, "E10782", {"start": v(-280.89, -398.06) * mm, "end": v(-279.3, -397.75) * mm});
            skLineSegment(sketch, "E10783", {"start": v(-279.3, -397.75) * mm, "end": v(-277.7, -397.36) * mm});
            skLineSegment(sketch, "E10784", {"start": v(-277.7, -397.36) * mm, "end": v(-276.1, -396.92) * mm});
            skLineSegment(sketch, "E10785", {"start": v(-276.1, -396.92) * mm, "end": v(-274.5, -396.4) * mm});
            skLineSegment(sketch, "E10786", {"start": v(-274.5, -396.4) * mm, "end": v(-272.9, -395.84) * mm});
            skLineSegment(sketch, "E10787", {"start": v(-272.9, -395.84) * mm, "end": v(-271.29, -395.21) * mm});
            skLineSegment(sketch, "E10788", {"start": v(-271.29, -395.21) * mm, "end": v(-269.68, -394.54) * mm});
            skLineSegment(sketch, "E10789", {"start": v(-269.68, -394.54) * mm, "end": v(-268.07, -393.81) * mm});
            skLineSegment(sketch, "E10790", {"start": v(-268.07, -393.81) * mm, "end": v(-266.45, -393.04) * mm});
            skLineSegment(sketch, "E10791", {"start": v(-266.45, -393.04) * mm, "end": v(-264.84, -392.22) * mm});
            skLineSegment(sketch, "E10792", {"start": v(-264.84, -392.22) * mm, "end": v(-263.23, -391.36) * mm});
            skLineSegment(sketch, "E10793", {"start": v(-263.23, -391.36) * mm, "end": v(-261.62, -390.46) * mm});
            skLineSegment(sketch, "E10794", {"start": v(-261.62, -390.46) * mm, "end": v(-260.02, -389.52) * mm});
            skLineSegment(sketch, "E10795", {"start": v(-260.02, -389.52) * mm, "end": v(-258.42, -388.56) * mm});
            skLineSegment(sketch, "E10796", {"start": v(-258.42, -388.56) * mm, "end": v(-256.82, -387.56) * mm});
            skLineSegment(sketch, "E10797", {"start": v(-256.82, -387.56) * mm, "end": v(-255.23, -386.54) * mm});
            skLineSegment(sketch, "E10798", {"start": v(-255.23, -386.54) * mm, "end": v(-253.64, -385.49) * mm});
            skLineSegment(sketch, "E10799", {"start": v(-253.64, -385.49) * mm, "end": v(-252.06, -384.42) * mm});
            skLineSegment(sketch, "E10800", {"start": v(-252.06, -384.42) * mm, "end": v(-250.5, -383.33) * mm});
            skLineSegment(sketch, "E10801", {"start": v(-250.5, -383.33) * mm, "end": v(-248.93, -382.23) * mm});
            skLineSegment(sketch, "E10802", {"start": v(-248.93, -382.23) * mm, "end": v(-247.38, -381.11) * mm});
            skLineSegment(sketch, "E10803", {"start": v(-247.38, -381.11) * mm, "end": v(-245.84, -380) * mm});
            skLineSegment(sketch, "E10804", {"start": v(-245.84, -380) * mm, "end": v(-244.3, -378.86) * mm});
            skLineSegment(sketch, "E10805", {"start": v(-244.3, -378.86) * mm, "end": v(-242.8, -377.72) * mm});
            skLineSegment(sketch, "E10806", {"start": v(-242.8, -377.72) * mm, "end": v(-241.29, -376.59) * mm});
            skLineSegment(sketch, "E10807", {"start": v(-241.29, -376.59) * mm, "end": v(-239.8, -375.46) * mm});
            skLineSegment(sketch, "E10808", {"start": v(-239.8, -375.46) * mm, "end": v(-238.32, -374.33) * mm});
            skLineSegment(sketch, "E10809", {"start": v(-238.32, -374.33) * mm, "end": v(-236.85, -373.2) * mm});
            skLineSegment(sketch, "E10810", {"start": v(-236.85, -373.2) * mm, "end": v(-235.4, -372.1) * mm});
            skLineSegment(sketch, "E10811", {"start": v(-235.4, -372.1) * mm, "end": v(-233.98, -371) * mm});
            skLineSegment(sketch, "E10812", {"start": v(-233.98, -371) * mm, "end": v(-232.56, -369.92) * mm});
            skLineSegment(sketch, "E10813", {"start": v(-232.56, -369.92) * mm, "end": v(-231.17, -368.86) * mm});
            skLineSegment(sketch, "E10814", {"start": v(-231.17, -368.86) * mm, "end": v(-229.8, -367.83) * mm});
            skLineSegment(sketch, "E10815", {"start": v(-229.8, -367.83) * mm, "end": v(-228.44, -366.82) * mm});
            skLineSegment(sketch, "E10816", {"start": v(-228.44, -366.82) * mm, "end": v(-227.1, -365.83) * mm});
            skLineSegment(sketch, "E10817", {"start": v(-227.1, -365.83) * mm, "end": v(-225.8, -364.88) * mm});
            skLineSegment(sketch, "E10818", {"start": v(-225.8, -364.88) * mm, "end": v(-224.5, -363.96) * mm});
            skLineSegment(sketch, "E10819", {"start": v(-224.5, -363.96) * mm, "end": v(-223.24, -363.08) * mm});
            skLineSegment(sketch, "E10820", {"start": v(-223.24, -363.08) * mm, "end": v(-222, -362.24) * mm});
            skLineSegment(sketch, "E10821", {"start": v(-222, -362.24) * mm, "end": v(-220.47, -361.22) * mm});
            skLineSegment(sketch, "E10822", {"start": v(-220.47, -361.22) * mm, "end": v(-218.95, -360.2) * mm});
            skLineSegment(sketch, "E10823", {"start": v(-218.95, -360.2) * mm, "end": v(-217.42, -359.2) * mm});
            skLineSegment(sketch, "E10824", {"start": v(-217.42, -359.2) * mm, "end": v(-215.9, -358.18) * mm});
            skLineSegment(sketch, "E10825", {"start": v(-215.9, -358.18) * mm, "end": v(-214.37, -357.16) * mm});
            skLineSegment(sketch, "E10826", {"start": v(-214.37, -357.16) * mm, "end": v(-212.84, -356.15) * mm});
            skLineSegment(sketch, "E10827", {"start": v(-212.84, -356.15) * mm, "end": v(-211.32, -355.13) * mm});
            skLineSegment(sketch, "E10828", {"start": v(-211.32, -355.13) * mm, "end": v(-209.8, -354.12) * mm});
            skLineSegment(sketch, "E10829", {"start": v(-209.8, -354.12) * mm, "end": v(-208.27, -353.1) * mm});
            skLineSegment(sketch, "E10830", {"start": v(-208.27, -353.1) * mm, "end": v(-206.74, -352.1) * mm});
            skLineSegment(sketch, "E10831", {"start": v(-206.74, -352.1) * mm, "end": v(-205.21, -351.08) * mm});
            skLineSegment(sketch, "E10832", {"start": v(-205.21, -351.08) * mm, "end": v(-203.69, -350.06) * mm});
            skLineSegment(sketch, "E10833", {"start": v(-203.69, -350.06) * mm, "end": v(-202.16, -349.05) * mm});
            skLineSegment(sketch, "E10834", {"start": v(-202.16, -349.05) * mm, "end": v(-200.63, -348.04) * mm});
            skLineSegment(sketch, "E10835", {"start": v(-200.63, -348.04) * mm, "end": v(-199.1, -347.02) * mm});
            skLineSegment(sketch, "E10836", {"start": v(-199.1, -347.02) * mm, "end": v(-197.58, -346) * mm});
            skLineSegment(sketch, "E10837", {"start": v(-197.58, -346) * mm, "end": v(-196.06, -345) * mm});
            skLineSegment(sketch, "E10838", {"start": v(-196.06, -345) * mm, "end": v(-194.53, -343.98) * mm});
            skLineSegment(sketch, "E10839", {"start": v(-194.53, -343.98) * mm, "end": v(-193, -342.97) * mm});
            skLineSegment(sketch, "E10840", {"start": v(-193, -342.97) * mm, "end": v(-191.48, -341.95) * mm});
            skLineSegment(sketch, "E10841", {"start": v(-191.48, -341.95) * mm, "end": v(-189.95, -340.94) * mm});
            skLineSegment(sketch, "E10842", {"start": v(-189.95, -340.94) * mm, "end": v(-188.43, -339.92) * mm});
            skLineSegment(sketch, "E10843", {"start": v(-188.43, -339.92) * mm, "end": v(-186.9, -338.9) * mm});
            skLineSegment(sketch, "E10844", {"start": v(-186.9, -338.9) * mm, "end": v(-185.38, -337.9) * mm});
            skLineSegment(sketch, "E10845", {"start": v(-185.38, -337.9) * mm, "end": v(-183.85, -336.88) * mm});
            skLineSegment(sketch, "E10846", {"start": v(-183.85, -336.88) * mm, "end": v(-182.33, -335.86) * mm});
            skLineSegment(sketch, "E10847", {"start": v(-182.33, -335.86) * mm, "end": v(-180.8, -334.84) * mm});
            skLineSegment(sketch, "E10848", {"start": v(-180.8, -334.84) * mm, "end": v(-179.28, -333.82) * mm});
            skLineSegment(sketch, "E10849", {"start": v(-179.28, -333.82) * mm, "end": v(-177.76, -332.8) * mm});
            skLineSegment(sketch, "E10850", {"start": v(-177.76, -332.8) * mm, "end": v(-176.23, -331.79) * mm});
            skLineSegment(sketch, "E10851", {"start": v(-176.23, -331.79) * mm, "end": v(-174.71, -330.77) * mm});
            skLineSegment(sketch, "E10852", {"start": v(-174.71, -330.77) * mm, "end": v(-173.19, -329.75) * mm});
            skLineSegment(sketch, "E10853", {"start": v(-173.19, -329.75) * mm, "end": v(-171.67, -328.73) * mm});
            skLineSegment(sketch, "E10854", {"start": v(-171.67, -328.73) * mm, "end": v(-170.15, -327.7) * mm});
            skLineSegment(sketch, "E10855", {"start": v(-170.15, -327.7) * mm, "end": v(-168.62, -326.69) * mm});
            skLineSegment(sketch, "E10856", {"start": v(-168.62, -326.69) * mm, "end": v(-167.1, -325.67) * mm});
            skLineSegment(sketch, "E10857", {"start": v(-167.1, -325.67) * mm, "end": v(-165.58, -324.64) * mm});
            skLineSegment(sketch, "E10858", {"start": v(-165.58, -324.64) * mm, "end": v(-164.06, -323.62) * mm});
            skLineSegment(sketch, "E10859", {"start": v(188.95, -321.8) * mm, "end": v(189.72, -323.44) * mm});
            skLineSegment(sketch, "E10860", {"start": v(189.72, -323.44) * mm, "end": v(190.5, -325.06) * mm});
            skLineSegment(sketch, "E10861", {"start": v(190.5, -325.06) * mm, "end": v(191.3, -326.67) * mm});
            skLineSegment(sketch, "E10862", {"start": v(191.3, -326.67) * mm, "end": v(192.11, -328.29) * mm});
            skLineSegment(sketch, "E10863", {"start": v(192.11, -328.29) * mm, "end": v(192.94, -329.9) * mm});
            skLineSegment(sketch, "E10864", {"start": v(192.94, -329.9) * mm, "end": v(193.77, -331.5) * mm});
            skLineSegment(sketch, "E10865", {"start": v(193.77, -331.5) * mm, "end": v(194.62, -333.1) * mm});
            skLineSegment(sketch, "E10866", {"start": v(194.62, -333.1) * mm, "end": v(195.49, -334.7) * mm});
            skLineSegment(sketch, "E10867", {"start": v(195.49, -334.7) * mm, "end": v(196.36, -336.3) * mm});
            skLineSegment(sketch, "E10868", {"start": v(196.36, -336.3) * mm, "end": v(197.24, -337.9) * mm});
            skLineSegment(sketch, "E10869", {"start": v(197.24, -337.9) * mm, "end": v(198.13, -339.48) * mm});
            skLineSegment(sketch, "E10870", {"start": v(198.13, -339.48) * mm, "end": v(199.03, -341.07) * mm});
            skLineSegment(sketch, "E10871", {"start": v(199.03, -341.07) * mm, "end": v(199.94, -342.65) * mm});
            skLineSegment(sketch, "E10872", {"start": v(199.94, -342.65) * mm, "end": v(200.86, -344.23) * mm});
            skLineSegment(sketch, "E10873", {"start": v(200.86, -344.23) * mm, "end": v(201.79, -345.8) * mm});
            skLineSegment(sketch, "E10874", {"start": v(201.79, -345.8) * mm, "end": v(202.72, -347.38) * mm});
            skLineSegment(sketch, "E10875", {"start": v(202.72, -347.38) * mm, "end": v(203.66, -348.95) * mm});
            skLineSegment(sketch, "E10876", {"start": v(203.66, -348.95) * mm, "end": v(204.6, -350.52) * mm});
            skLineSegment(sketch, "E10877", {"start": v(204.6, -350.52) * mm, "end": v(205.55, -352.09) * mm});
            skLineSegment(sketch, "E10878", {"start": v(205.55, -352.09) * mm, "end": v(206.5, -353.65) * mm});
            skLineSegment(sketch, "E10879", {"start": v(206.5, -353.65) * mm, "end": v(207.46, -355.22) * mm});
            skLineSegment(sketch, "E10880", {"start": v(207.46, -355.22) * mm, "end": v(208.42, -356.78) * mm});
            skLineSegment(sketch, "E10881", {"start": v(208.42, -356.78) * mm, "end": v(209.38, -358.34) * mm});
            skLineSegment(sketch, "E10882", {"start": v(209.38, -358.34) * mm, "end": v(210.34, -359.9) * mm});
            skLineSegment(sketch, "E10883", {"start": v(210.34, -359.9) * mm, "end": v(211.3, -361.45) * mm});
            skLineSegment(sketch, "E10884", {"start": v(211.3, -361.45) * mm, "end": v(212.27, -363) * mm});
            skLineSegment(sketch, "E10885", {"start": v(212.27, -363) * mm, "end": v(213.24, -364.55) * mm});
            skLineSegment(sketch, "E10886", {"start": v(213.24, -364.55) * mm, "end": v(214.2, -366.1) * mm});
            skLineSegment(sketch, "E10887", {"start": v(214.2, -366.1) * mm, "end": v(215.17, -367.65) * mm});
            skLineSegment(sketch, "E10888", {"start": v(215.17, -367.65) * mm, "end": v(216.13, -369.2) * mm});
            skLineSegment(sketch, "E10889", {"start": v(216.13, -369.2) * mm, "end": v(217.1, -370.75) * mm});
            skLineSegment(sketch, "E10890", {"start": v(217.1, -370.75) * mm, "end": v(218.05, -372.3) * mm});
            skLineSegment(sketch, "E10891", {"start": v(218.05, -372.3) * mm, "end": v(219, -373.84) * mm});
            skLineSegment(sketch, "E10892", {"start": v(219, -373.84) * mm, "end": v(219.96, -375.38) * mm});
            skLineSegment(sketch, "E10893", {"start": v(219.96, -375.38) * mm, "end": v(220.9, -376.92) * mm});
            skLineSegment(sketch, "E10894", {"start": v(220.9, -376.92) * mm, "end": v(221.84, -378.47) * mm});
            skLineSegment(sketch, "E10895", {"start": v(221.84, -378.47) * mm, "end": v(222.78, -380) * mm});
            skLineSegment(sketch, "E10896", {"start": v(222.78, -380) * mm, "end": v(223.7, -381.55) * mm});
            skLineSegment(sketch, "E10897", {"start": v(223.7, -381.55) * mm, "end": v(224.59, -383.04) * mm});
            skLineSegment(sketch, "E10898", {"start": v(224.59, -383.04) * mm, "end": v(225.46, -384.56) * mm});
            skLineSegment(sketch, "E10899", {"start": v(225.46, -384.56) * mm, "end": v(226.33, -386.11) * mm});
            skLineSegment(sketch, "E10900", {"start": v(226.33, -386.11) * mm, "end": v(227.2, -387.69) * mm});
            skLineSegment(sketch, "E10901", {"start": v(227.2, -387.69) * mm, "end": v(228.09, -389.28) * mm});
            skLineSegment(sketch, "E10902", {"start": v(228.09, -389.28) * mm, "end": v(228.97, -390.88) * mm});
            skLineSegment(sketch, "E10903", {"start": v(228.97, -390.88) * mm, "end": v(229.87, -392.48) * mm});
            skLineSegment(sketch, "E10904", {"start": v(229.87, -392.48) * mm, "end": v(230.78, -394.1) * mm});
            skLineSegment(sketch, "E10905", {"start": v(230.78, -394.1) * mm, "end": v(231.7, -395.7) * mm});
            skLineSegment(sketch, "E10906", {"start": v(231.7, -395.7) * mm, "end": v(232.65, -397.28) * mm});
            skLineSegment(sketch, "E10907", {"start": v(232.65, -397.28) * mm, "end": v(233.61, -398.85) * mm});
            skLineSegment(sketch, "E10908", {"start": v(233.61, -398.85) * mm, "end": v(234.6, -400.4) * mm});
            skLineSegment(sketch, "E10909", {"start": v(234.6, -400.4) * mm, "end": v(235.63, -401.92) * mm});
            skLineSegment(sketch, "E10910", {"start": v(235.63, -401.92) * mm, "end": v(236.68, -403.41) * mm});
            skLineSegment(sketch, "E10911", {"start": v(236.68, -403.41) * mm, "end": v(237.76, -404.86) * mm});
            skLineSegment(sketch, "E10912", {"start": v(237.76, -404.86) * mm, "end": v(238.88, -406.26) * mm});
            skLineSegment(sketch, "E10913", {"start": v(238.88, -406.26) * mm, "end": v(240.05, -407.6) * mm});
            skLineSegment(sketch, "E10914", {"start": v(240.05, -407.6) * mm, "end": v(241.25, -408.9) * mm});
            skLineSegment(sketch, "E10915", {"start": v(241.25, -408.9) * mm, "end": v(242.5, -410.13) * mm});
            skLineSegment(sketch, "E10916", {"start": v(242.5, -410.13) * mm, "end": v(243.8, -411.3) * mm});
            skLineSegment(sketch, "E10917", {"start": v(243.8, -411.3) * mm, "end": v(245.14, -412.37) * mm});
            skLineSegment(sketch, "E10918", {"start": v(245.14, -412.37) * mm, "end": v(246.5, -413.33) * mm});
            skLineSegment(sketch, "E10919", {"start": v(246.5, -413.33) * mm, "end": v(247.9, -414.2) * mm});
            skLineSegment(sketch, "E10920", {"start": v(247.9, -414.2) * mm, "end": v(249.3, -414.96) * mm});
            skLineSegment(sketch, "E10921", {"start": v(249.3, -414.96) * mm, "end": v(250.74, -415.63) * mm});
            skLineSegment(sketch, "E10922", {"start": v(250.74, -415.63) * mm, "end": v(252.2, -416.2) * mm});
            skLineSegment(sketch, "E10923", {"start": v(252.2, -416.2) * mm, "end": v(253.65, -416.67) * mm});
            skLineSegment(sketch, "E10924", {"start": v(253.65, -416.67) * mm, "end": v(255.13, -417.06) * mm});
            skLineSegment(sketch, "E10925", {"start": v(255.13, -417.06) * mm, "end": v(256.61, -417.35) * mm});
            skLineSegment(sketch, "E10926", {"start": v(256.61, -417.35) * mm, "end": v(258.1, -417.55) * mm});
            skLineSegment(sketch, "E10927", {"start": v(258.1, -417.55) * mm, "end": v(259.6, -417.67) * mm});
            skLineSegment(sketch, "E10928", {"start": v(259.6, -417.67) * mm, "end": v(261.1, -417.7) * mm});
            skLineSegment(sketch, "E10929", {"start": v(261.1, -417.7) * mm, "end": v(262.58, -417.65) * mm});
            skLineSegment(sketch, "E10930", {"start": v(262.58, -417.65) * mm, "end": v(264.07, -417.52) * mm});
            skLineSegment(sketch, "E10931", {"start": v(264.07, -417.52) * mm, "end": v(265.54, -417.31) * mm});
            skLineSegment(sketch, "E10932", {"start": v(265.54, -417.31) * mm, "end": v(267, -417.03) * mm});
            skLineSegment(sketch, "E10933", {"start": v(267, -417.03) * mm, "end": v(268.46, -416.67) * mm});
            skLineSegment(sketch, "E10934", {"start": v(268.46, -416.67) * mm, "end": v(269.9, -416.23) * mm});
            skLineSegment(sketch, "E10935", {"start": v(269.9, -416.23) * mm, "end": v(271.3, -415.73) * mm});
            skLineSegment(sketch, "E10936", {"start": v(271.3, -415.73) * mm, "end": v(272.7, -415.16) * mm});
            skLineSegment(sketch, "E10937", {"start": v(272.7, -415.16) * mm, "end": v(274.06, -414.52) * mm});
            skLineSegment(sketch, "E10938", {"start": v(274.06, -414.52) * mm, "end": v(275.4, -413.8) * mm});
            skLineSegment(sketch, "E10939", {"start": v(275.4, -413.8) * mm, "end": v(276.7, -413.04) * mm});
            skLineSegment(sketch, "E10940", {"start": v(276.7, -413.04) * mm, "end": v(277.97, -412.21) * mm});
            skLineSegment(sketch, "E10941", {"start": v(277.97, -412.21) * mm, "end": v(279.2, -411.32) * mm});
            skLineSegment(sketch, "E10942", {"start": v(279.2, -411.32) * mm, "end": v(280.4, -410.37) * mm});
            skLineSegment(sketch, "E10943", {"start": v(280.4, -410.37) * mm, "end": v(281.55, -409.37) * mm});
            skLineSegment(sketch, "E10944", {"start": v(281.55, -409.37) * mm, "end": v(282.65, -408.32) * mm});
            skLineSegment(sketch, "E10945", {"start": v(282.65, -408.32) * mm, "end": v(283.7, -407.2) * mm});
            skLineSegment(sketch, "E10946", {"start": v(283.7, -407.2) * mm, "end": v(284.71, -406.05) * mm});
            skLineSegment(sketch, "E10947", {"start": v(284.71, -406.05) * mm, "end": v(285.67, -404.85) * mm});
            skLineSegment(sketch, "E10948", {"start": v(285.67, -404.85) * mm, "end": v(286.56, -403.6) * mm});
            skLineSegment(sketch, "E10949", {"start": v(286.56, -403.6) * mm, "end": v(287.4, -402.3) * mm});
            skLineSegment(sketch, "E10950", {"start": v(287.4, -402.3) * mm, "end": v(288.16, -400.96) * mm});
            skLineSegment(sketch, "E10951", {"start": v(288.16, -400.96) * mm, "end": v(288.87, -399.59) * mm});
            skLineSegment(sketch, "E10952", {"start": v(288.87, -399.59) * mm, "end": v(289.5, -398.17) * mm});
            skLineSegment(sketch, "E10953", {"start": v(289.5, -398.17) * mm, "end": v(290.07, -396.72) * mm});
            skLineSegment(sketch, "E10954", {"start": v(290.07, -396.72) * mm, "end": v(290.56, -395.24) * mm});
            skLineSegment(sketch, "E10955", {"start": v(290.56, -395.24) * mm, "end": v(290.98, -393.72) * mm});
            skLineSegment(sketch, "E10956", {"start": v(290.98, -393.72) * mm, "end": v(291.3, -392.18) * mm});
            skLineSegment(sketch, "E10957", {"start": v(291.3, -392.18) * mm, "end": v(291.56, -390.6) * mm});
            skLineSegment(sketch, "E10958", {"start": v(291.56, -390.6) * mm, "end": v(291.75, -388.9) * mm});
            skLineSegment(sketch, "E10959", {"start": v(291.75, -388.9) * mm, "end": v(291.87, -387.2) * mm});
            skLineSegment(sketch, "E10960", {"start": v(291.87, -387.2) * mm, "end": v(291.93, -385.48) * mm});
            skLineSegment(sketch, "E10961", {"start": v(291.93, -385.48) * mm, "end": v(291.93, -383.76) * mm});
            skLineSegment(sketch, "E10962", {"start": v(291.93, -383.76) * mm, "end": v(291.88, -382.04) * mm});
            skLineSegment(sketch, "E10963", {"start": v(291.88, -382.04) * mm, "end": v(291.76, -380.32) * mm});
            skLineSegment(sketch, "E10964", {"start": v(291.76, -380.32) * mm, "end": v(291.6, -378.6) * mm});
            skLineSegment(sketch, "E10965", {"start": v(291.6, -378.6) * mm, "end": v(291.38, -376.86) * mm});
            skLineSegment(sketch, "E10966", {"start": v(291.38, -376.86) * mm, "end": v(291.12, -375.13) * mm});
            skLineSegment(sketch, "E10967", {"start": v(291.12, -375.13) * mm, "end": v(290.82, -373.4) * mm});
            skLineSegment(sketch, "E10968", {"start": v(290.82, -373.4) * mm, "end": v(290.48, -371.66) * mm});
            skLineSegment(sketch, "E10969", {"start": v(290.48, -371.66) * mm, "end": v(290.1, -369.92) * mm});
            skLineSegment(sketch, "E10970", {"start": v(290.1, -369.92) * mm, "end": v(289.68, -368.18) * mm});
            skLineSegment(sketch, "E10971", {"start": v(289.68, -368.18) * mm, "end": v(289.23, -366.44) * mm});
            skLineSegment(sketch, "E10972", {"start": v(289.23, -366.44) * mm, "end": v(288.76, -364.7) * mm});
            skLineSegment(sketch, "E10973", {"start": v(288.76, -364.7) * mm, "end": v(288.25, -362.96) * mm});
            skLineSegment(sketch, "E10974", {"start": v(288.25, -362.96) * mm, "end": v(287.73, -361.22) * mm});
            skLineSegment(sketch, "E10975", {"start": v(287.73, -361.22) * mm, "end": v(287.18, -359.48) * mm});
            skLineSegment(sketch, "E10976", {"start": v(287.18, -359.48) * mm, "end": v(286.62, -357.74) * mm});
            skLineSegment(sketch, "E10977", {"start": v(286.62, -357.74) * mm, "end": v(286.04, -356) * mm});
            skLineSegment(sketch, "E10978", {"start": v(286.04, -356) * mm, "end": v(285.45, -354.26) * mm});
            skLineSegment(sketch, "E10979", {"start": v(285.45, -354.26) * mm, "end": v(284.85, -352.52) * mm});
            skLineSegment(sketch, "E10980", {"start": v(284.85, -352.52) * mm, "end": v(284.25, -350.79) * mm});
            skLineSegment(sketch, "E10981", {"start": v(284.25, -350.79) * mm, "end": v(283.64, -349.05) * mm});
            skLineSegment(sketch, "E10982", {"start": v(283.64, -349.05) * mm, "end": v(283.03, -347.32) * mm});
            skLineSegment(sketch, "E10983", {"start": v(283.03, -347.32) * mm, "end": v(282.43, -345.6) * mm});
            skLineSegment(sketch, "E10984", {"start": v(282.43, -345.6) * mm, "end": v(281.83, -343.86) * mm});
            skLineSegment(sketch, "E10985", {"start": v(281.83, -343.86) * mm, "end": v(281.24, -342.14) * mm});
            skLineSegment(sketch, "E10986", {"start": v(281.24, -342.14) * mm, "end": v(280.66, -340.42) * mm});
            skLineSegment(sketch, "E10987", {"start": v(280.66, -340.42) * mm, "end": v(280.1, -338.7) * mm});
            skLineSegment(sketch, "E10988", {"start": v(280.1, -338.7) * mm, "end": v(279.54, -337) * mm});
            skLineSegment(sketch, "E10989", {"start": v(279.54, -337) * mm, "end": v(279.02, -335.28) * mm});
            skLineSegment(sketch, "E10990", {"start": v(279.02, -335.28) * mm, "end": v(278.5, -333.58) * mm});
            skLineSegment(sketch, "E10991", {"start": v(278.5, -333.58) * mm, "end": v(278.03, -331.88) * mm});
            skLineSegment(sketch, "E10992", {"start": v(278.03, -331.88) * mm, "end": v(277.58, -330.19) * mm});
            skLineSegment(sketch, "E10993", {"start": v(277.58, -330.19) * mm, "end": v(277.16, -328.5) * mm});
            skLineSegment(sketch, "E10994", {"start": v(277.16, -328.5) * mm, "end": v(276.77, -326.82) * mm});
            skLineSegment(sketch, "E10995", {"start": v(276.77, -326.82) * mm, "end": v(276.42, -325.14) * mm});
            skLineSegment(sketch, "E10996", {"start": v(276.42, -325.14) * mm, "end": v(276.11, -323.47) * mm});
            skLineSegment(sketch, "E10997", {"start": v(276.11, -323.47) * mm, "end": v(275.84, -321.8) * mm});
            skLineSegment(sketch, "E10998", {"start": v(275.84, -321.8) * mm, "end": v(188.95, -321.8) * mm});
            skLineSegment(sketch, "E10999", {"start": v(324.72, -321.8) * mm, "end": v(325.29, -323.42) * mm});
            skLineSegment(sketch, "E11000", {"start": v(325.29, -323.42) * mm, "end": v(325.92, -324.95) * mm});
            skLineSegment(sketch, "E11001", {"start": v(325.92, -324.95) * mm, "end": v(326.61, -326.4) * mm});
            skLineSegment(sketch, "E11002", {"start": v(326.61, -326.4) * mm, "end": v(327.36, -327.77) * mm});
            skLineSegment(sketch, "E11003", {"start": v(327.36, -327.77) * mm, "end": v(328.17, -329.07) * mm});
            skLineSegment(sketch, "E11004", {"start": v(328.17, -329.07) * mm, "end": v(329.04, -330.28) * mm});
            skLineSegment(sketch, "E11005", {"start": v(329.04, -330.28) * mm, "end": v(329.95, -331.42) * mm});
            skLineSegment(sketch, "E11006", {"start": v(329.95, -331.42) * mm, "end": v(330.92, -332.49) * mm});
            skLineSegment(sketch, "E11007", {"start": v(330.92, -332.49) * mm, "end": v(331.93, -333.47) * mm});
            skLineSegment(sketch, "E11008", {"start": v(331.93, -333.47) * mm, "end": v(332.98, -334.39) * mm});
            skLineSegment(sketch, "E11009", {"start": v(332.98, -334.39) * mm, "end": v(334.08, -335.23) * mm});
            skLineSegment(sketch, "E11010", {"start": v(334.08, -335.23) * mm, "end": v(335.21, -336) * mm});
            skLineSegment(sketch, "E11011", {"start": v(335.21, -336) * mm, "end": v(336.38, -336.7) * mm});
            skLineSegment(sketch, "E11012", {"start": v(336.38, -336.7) * mm, "end": v(337.58, -337.32) * mm});
            skLineSegment(sketch, "E11013", {"start": v(337.58, -337.32) * mm, "end": v(338.81, -337.87) * mm});
            skLineSegment(sketch, "E11014", {"start": v(338.81, -337.87) * mm, "end": v(340.08, -338.36) * mm});
            skLineSegment(sketch, "E11015", {"start": v(340.08, -338.36) * mm, "end": v(341.36, -338.77) * mm});
            skLineSegment(sketch, "E11016", {"start": v(341.36, -338.77) * mm, "end": v(342.67, -339.12) * mm});
            skLineSegment(sketch, "E11017", {"start": v(342.67, -339.12) * mm, "end": v(344, -339.4) * mm});
            skLineSegment(sketch, "E11018", {"start": v(344, -339.4) * mm, "end": v(345.34, -339.61) * mm});
            skLineSegment(sketch, "E11019", {"start": v(345.34, -339.61) * mm, "end": v(346.7, -339.76) * mm});
            skLineSegment(sketch, "E11020", {"start": v(346.7, -339.76) * mm, "end": v(348.07, -339.85) * mm});
            skLineSegment(sketch, "E11021", {"start": v(348.07, -339.85) * mm, "end": v(349.45, -339.86) * mm});
            skLineSegment(sketch, "E11022", {"start": v(349.45, -339.86) * mm, "end": v(350.83, -339.82) * mm});
            skLineSegment(sketch, "E11023", {"start": v(350.83, -339.82) * mm, "end": v(352.22, -339.71) * mm});
            skLineSegment(sketch, "E11024", {"start": v(352.22, -339.71) * mm, "end": v(353.61, -339.55) * mm});
            skLineSegment(sketch, "E11025", {"start": v(353.61, -339.55) * mm, "end": v(355, -339.32) * mm});
            skLineSegment(sketch, "E11026", {"start": v(355, -339.32) * mm, "end": v(356.38, -339.03) * mm});
            skLineSegment(sketch, "E11027", {"start": v(356.38, -339.03) * mm, "end": v(357.76, -338.68) * mm});
            skLineSegment(sketch, "E11028", {"start": v(357.76, -338.68) * mm, "end": v(359.13, -338.27) * mm});
            skLineSegment(sketch, "E11029", {"start": v(359.13, -338.27) * mm, "end": v(360.48, -337.8) * mm});
            skLineSegment(sketch, "E11030", {"start": v(360.48, -337.8) * mm, "end": v(361.82, -337.28) * mm});
            skLineSegment(sketch, "E11031", {"start": v(361.82, -337.28) * mm, "end": v(363.14, -336.7) * mm});
            skLineSegment(sketch, "E11032", {"start": v(363.14, -336.7) * mm, "end": v(364.45, -336.07) * mm});
            skLineSegment(sketch, "E11033", {"start": v(364.45, -336.07) * mm, "end": v(365.72, -335.38) * mm});
            skLineSegment(sketch, "E11034", {"start": v(365.72, -335.38) * mm, "end": v(366.98, -334.64) * mm});
            skLineSegment(sketch, "E11035", {"start": v(366.98, -334.64) * mm, "end": v(368.2, -333.84) * mm});
            skLineSegment(sketch, "E11036", {"start": v(368.2, -333.84) * mm, "end": v(369.4, -333) * mm});
            skLineSegment(sketch, "E11037", {"start": v(369.4, -333) * mm, "end": v(370.55, -332.1) * mm});
            skLineSegment(sketch, "E11038", {"start": v(370.55, -332.1) * mm, "end": v(371.68, -331.14) * mm});
            skLineSegment(sketch, "E11039", {"start": v(371.68, -331.14) * mm, "end": v(372.76, -330.14) * mm});
            skLineSegment(sketch, "E11040", {"start": v(372.76, -330.14) * mm, "end": v(373.8, -329.1) * mm});
            skLineSegment(sketch, "E11041", {"start": v(373.8, -329.1) * mm, "end": v(374.8, -328) * mm});
            skLineSegment(sketch, "E11042", {"start": v(374.8, -328) * mm, "end": v(375.75, -326.85) * mm});
            skLineSegment(sketch, "E11043", {"start": v(375.75, -326.85) * mm, "end": v(376.65, -325.66) * mm});
            skLineSegment(sketch, "E11044", {"start": v(376.65, -325.66) * mm, "end": v(377.5, -324.42) * mm});
            skLineSegment(sketch, "E11045", {"start": v(377.5, -324.42) * mm, "end": v(378.3, -323.14) * mm});
            skLineSegment(sketch, "E11046", {"start": v(378.3, -323.14) * mm, "end": v(379.03, -321.8) * mm});
            skLineSegment(sketch, "E11047", {"start": v(379.03, -321.8) * mm, "end": v(324.72, -321.8) * mm});
            skSolve(sketch);
        }
        {
            var Q0;
            Q0=makeQuery(id+"F0.imprint","IMPRINT",FACE,{"disambiguationData":[TD([[makeQuery(id+"F0.imprint","IMPRINT",EDGE,{"derivedFrom":sQuery(id+"F0.wireOp",EDGE,"E0")}),1.0]])]});
            extrude(context, id + "F1", {"entities" : qUnion([Q0]), "depth" : 51.6 * mm});
        }
        {
            var Q0;
            Q0=makeQuery(id+"F0.imprint","IMPRINT",FACE,{"disambiguationData":[TD([[makeQuery(id+"F0.imprint","IMPRINT",EDGE,{"derivedFrom":sQuery(id+"F0.wireOp",EDGE,"E8314")}),1.0]])]});
            extrude(context, id + "F2", {"entities" : qUnion([Q0]), "depth" : 25.4 * mm});
        }
    });
